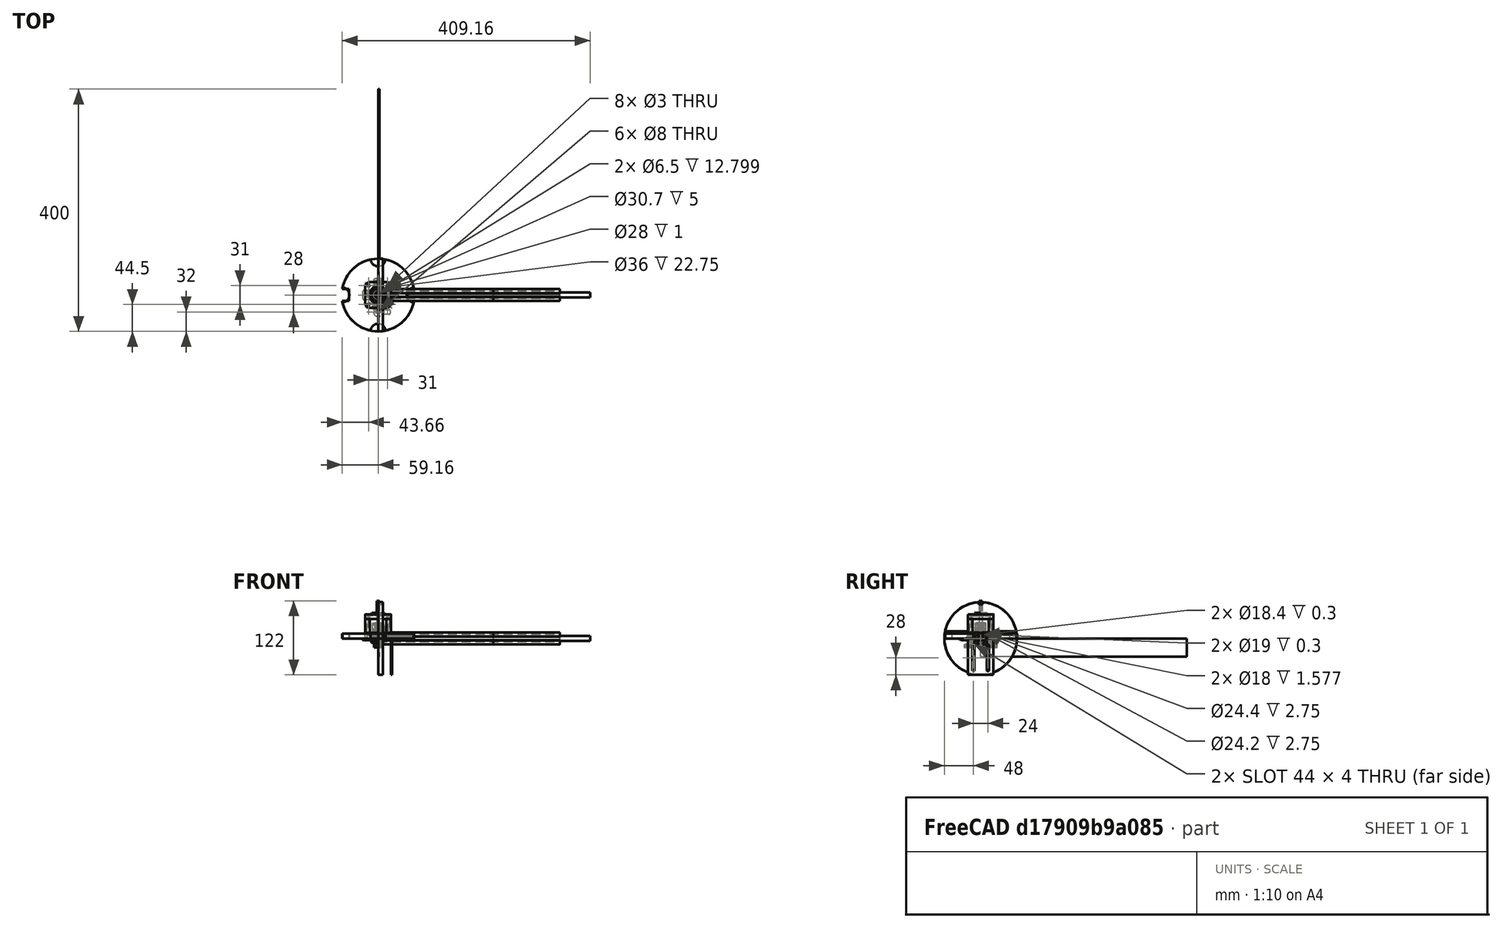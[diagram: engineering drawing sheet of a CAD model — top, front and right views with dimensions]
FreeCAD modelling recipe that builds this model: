
FCSTD DOCUMENT  (FreeCAD 0.19R)
Label: proyectoFinal_ruedasENcero-cero
License: All rights reserved
LicenseURL: http://en.wikipedia.org/wiki/All_rights_reserved
objects: Sketcher::SketchObject×360, PartDesign::Body×269, PartDesign::Pad×217, PartDesign::Fillet×183, App::Part×128, PartDesign::Pocket×123, PartDesign::FeatureBase×92, PartDesign::Revolution×52, App::DocumentObjectGroup×42, App::LinkGroup×30, PartDesign::PolarPattern×29, PartDesign::Chamfer×21, PartDesign::Groove×8, Part::FeaturePython×8, PartDesign::Mirrored×6, PartDesign::ShapeBinder×5, PartDesign::Hole×2, PartDesign::Draft×2, PartDesign::LinearPattern×2, PartDesign::Plane×2, +5 more types
note: 2002 computed .brp shape members not serialized (recipe doc carries the construction recipe); baked Part::Feature solids carry a one-line shape summary decoded from their .brp

FEATURE [Sketcher::SketchObject] Sketch001
  FullyConstrained = false
  MapMode = 5
  Support = -> [XY_Plane003]
  sketch-geometry (46):
    g0: LineSegment StartX=3.4 StartY=2.65 StartZ=0 EndX=3.4 EndY=-2.6657 EndZ=0
    g1: LineSegment StartX=2.63162 StartY=-3.4 StartZ=0 EndX=-2.65 EndY=-3.4 EndZ=0
    g2: LineSegment StartX=-3.4 StartY=-2.63136 StartZ=0 EndX=-3.4 EndY=2.61487 EndZ=0
    g3: LineSegment StartX=-10 StartY=10 StartZ=0 EndX=-3.125 EndY=10 EndZ=0
    g4: LineSegment StartX=10 StartY=10 StartZ=0 EndX=10 EndY=3.125 EndZ=0
    g5: LineSegment StartX=10 StartY=-10 StartZ=0 EndX=3.125 EndY=-10 EndZ=0
    g6: LineSegment StartX=-10 StartY=-10 StartZ=0 EndX=-10 EndY=-3.125 EndZ=0
    g7: GeomPoint X=3e-16 Y=0 Z=0
    g8: Circle CenterX=3e-16 CenterY=0 CenterZ=0 NormalX=0 NormalY=0 NormalZ=1 AngleXU=0 Radius=2.1
    g9: LineSegment StartX=-4.76483 StartY=8.08721 StartZ=0 EndX=-3.55 EndY=8.08721 EndZ=0
    g10: LineSegment StartX=8.24722 StartY=4.75 StartZ=0 EndX=8.24722 EndY=3.55 EndZ=0
    g11: LineSegment StartX=-8.2 StartY=-4.73729 StartZ=0 EndX=-8.2 EndY=-3.55 EndZ=0
    g12: LineSegment StartX=5.5 StartY=4.75 StartZ=0 EndX=8.24722 EndY=4.75 EndZ=0
    g13: LineSegment StartX=4.75 StartY=5.50457 StartZ=0 EndX=2.65 EndY=3.4 EndZ=0
    g14: LineSegment StartX=4.75 StartY=5.50457 StartZ=0 EndX=4.75 EndY=8.08721 EndZ=0
    g15: LineSegment StartX=3.4 StartY=2.65 StartZ=0 EndX=5.5 EndY=4.75 EndZ=0
    g16: LineSegment StartX=-4.76483 StartY=5.50457 StartZ=0 EndX=-2.66166 EndY=3.4 EndZ=0
    g17: LineSegment StartX=-5.5 StartY=4.70904 StartZ=0 EndX=-3.4 EndY=2.61487 EndZ=0
    g18: LineSegment StartX=-4.76483 StartY=5.50457 StartZ=0 EndX=-4.76483 EndY=8.08721 EndZ=0
    g19: LineSegment StartX=-5.5 StartY=4.70904 StartZ=0 EndX=-8.2 EndY=4.70904 EndZ=0
    g20: LineSegment StartX=-10 StartY=3.125 StartZ=0 EndX=-10 EndY=10 EndZ=0
    g21: LineSegment StartX=-8.2 StartY=3.55 StartZ=0 EndX=-8.2 EndY=4.70904 EndZ=0
    g22: LineSegment StartX=3.55 StartY=8.08721 StartZ=0 EndX=4.75 EndY=8.08721 EndZ=0
    g23: LineSegment StartX=3.125 StartY=10 StartZ=0 EndX=10 EndY=10 EndZ=0
    g24: LineSegment StartX=-5.5 StartY=-4.73729 StartZ=0 EndX=-8.2 EndY=-4.73729 EndZ=0
    g25: LineSegment StartX=-4.75 StartY=-5.5 StartZ=0 EndX=-2.65 EndY=-3.4 EndZ=0
    g26: LineSegment StartX=-4.75 StartY=-5.5 StartZ=0 EndX=-4.75 EndY=-8.2 EndZ=0
    g27: LineSegment StartX=4.73747 StartY=-5.5 StartZ=0 EndX=4.73747 EndY=-8.2 EndZ=0
    g28: LineSegment StartX=5.5 StartY=-4.7671 StartZ=0 EndX=8.24722 EndY=-4.7671 EndZ=0
    g29: LineSegment StartX=-3.125 StartY=-10 StartZ=0 EndX=-10 EndY=-10 EndZ=0
    g30: LineSegment StartX=-3.55 StartY=-8.2 StartZ=0 EndX=-4.75 EndY=-8.2 EndZ=0
    g31: LineSegment StartX=4.73747 StartY=-8.2 StartZ=0 EndX=3.55 EndY=-8.2 EndZ=0
    g32: LineSegment StartX=10 StartY=-3.125 StartZ=0 EndX=10 EndY=-10 EndZ=0
    g33: LineSegment StartX=8.24722 StartY=-3.55 StartZ=0 EndX=8.24722 EndY=-4.7671 EndZ=0
    g34: LineSegment StartX=-2.66166 StartY=3.4 StartZ=0 EndX=2.65 EndY=3.4 EndZ=0
    g35: LineSegment StartX=-3.4 StartY=-2.63136 StartZ=0 EndX=-5.5 EndY=-4.73729 EndZ=0
    g36: LineSegment StartX=3.4 StartY=-2.6657 StartZ=0 EndX=5.5 EndY=-4.7671 EndZ=0
    g37: LineSegment StartX=2.63162 StartY=-3.4 StartZ=0 EndX=4.73747 EndY=-5.5 EndZ=0
    g38: LineSegment StartX=-3.55 StartY=-8.2 StartZ=0 EndX=-3.125 EndY=-10 EndZ=0
    g39: LineSegment StartX=3.55 StartY=-8.2 StartZ=0 EndX=3.125 EndY=-10 EndZ=0
    g40: LineSegment StartX=-3.125 StartY=10 StartZ=0 EndX=-3.55 EndY=8.08721 EndZ=0
    g41: LineSegment StartX=3.125 StartY=10 StartZ=0 EndX=3.55 EndY=8.08721 EndZ=0
    g42: LineSegment StartX=8.24722 StartY=3.55 StartZ=0 EndX=10 EndY=3.125 EndZ=0
    g43: LineSegment StartX=10 StartY=-3.125 StartZ=0 EndX=8.24722 EndY=-3.55 EndZ=0
    g44: LineSegment StartX=-10 StartY=-3.125 StartZ=0 EndX=-8.2 EndY=-3.55 EndZ=0
    g45: LineSegment StartX=-10 StartY=3.125 StartZ=0 EndX=-8.2 EndY=3.55 EndZ=0
  constraints (61):
    c: Horizontal(g1)
    c: Vertical(g0)
    c: Vertical(g2)
    c: Coincident(g23,g4)
    c: Coincident(g32,g5)
    c: Coincident(g29,g6)
    c: Coincident(g20,g3)
    c: Horizontal(g3)
    c: Horizontal(g5)
    c: Vertical(g4)
    c: Vertical(g6)
    c: PointOnObject(g7,g-1)
    c: DistanceX(g3,g7) = 10
    c: DistanceX(g-1,g23) = 10
    c: DistanceY(g7,g3) = 10
    c: DistanceX(g3,g-1) = 10
    c: DistanceY(g32,g7) = 10
    c: Coincident(g8,g7)
    c: Radius(g8) = 2.1
    c: Horizontal(g9)
    c: Vertical(g10)
    c: Vertical(g11)
    c: Coincident(g12,g15)
    c: Horizontal(g12)
    c: Coincident(g14,g13)
    c: Vertical(g14)
    c: Coincident(g15,g0)
    c: Coincident(g13,g34)
    c: Coincident(g14,g22)
    c: Coincident(g18,g16)
    c: Vertical(g18)
    c: Coincident(g19,g17)
    c: Horizontal(g19)
    c: Coincident(g9,g18)
    c: Coincident(g21,g19)
    c: Coincident(g24,g35)
    c: Horizontal(g24)
    c: Coincident(g26,g25)
    c: Vertical(g26)
    c: Coincident(g27,g37)
    c: Vertical(g27)
    c: Coincident(g28,g36)
    c: Horizontal(g28)
    c: Coincident(g11,g24)
    c: Coincident(g26,g30)
    c: Coincident(g31,g27)
    c: Coincident(g12,g10)
    c: Coincident(g28,g33)
    c: Coincident(g25,g1)
    c: Coincident(g35,g2)
    c: Coincident(g17,g2)
    c: Coincident(g16,g34)
    c: Coincident(g1,g37)
    c: Coincident(g0,g36)
    c: Coincident(g39,g5)
    c: Coincident(g40,g3)
    c: Coincident(g42,g4)
    c: Coincident(g44,g6)
    c: Coincident(g21,g45)
    c: Coincident(g33,g43)
    c: Coincident(g10,g42)
FEATURE [PartDesign::Pad] Pad001
  Direction = (0,0,1)
  Length = 300
  Length2 = 10
  Profile = -> Sketch001
  Type = 0
FEATURE [PartDesign::Fillet] Fillet011
  Base = -> Pad001 [Edge53]
  BaseFeature = -> Pad001
  Radius = 1
  SupportTransform = false
FEATURE [PartDesign::Fillet] Fillet012
  Base = -> Fillet011 [Edge114]
  BaseFeature = -> Fillet011
  Radius = 1
  SupportTransform = false
FEATURE [PartDesign::Fillet] Fillet013
  Base = -> Fillet012 [Edge137,Edge95]
  BaseFeature = -> Fillet012
  Radius = 0.5
  SupportTransform = false
FEATURE [PartDesign::Fillet] Fillet014
  Base = -> Fillet013 [Edge103]
  BaseFeature = -> Fillet013
  Radius = 0.5
  SupportTransform = false
FEATURE [PartDesign::Fillet] Fillet015
  Base = -> Fillet014 [Edge96]
  BaseFeature = -> Fillet014
  Radius = 0.5
  SupportTransform = false
FEATURE [PartDesign::Fillet] Fillet016
  Base = -> Fillet015 [Edge77]
  BaseFeature = -> Fillet015
  Radius = 0.5
  SupportTransform = false
FEATURE [PartDesign::Fillet] Fillet017
  Base = -> Fillet016 [Edge102]
  BaseFeature = -> Fillet016
  Radius = 0.5
  SupportTransform = false
FEATURE [PartDesign::Fillet] Fillet018
  Base = -> Fillet017 [Edge85]
  BaseFeature = -> Fillet017
  Radius = 0.5
  SupportTransform = false
FEATURE [PartDesign::Fillet] Fillet019
  Base = -> Fillet018 [Edge78]
  BaseFeature = -> Fillet018
  Radius = 0.5
  SupportTransform = false
FEATURE [PartDesign::Fillet] Fillet020
  Base = -> Fillet019 [Edge107]
  BaseFeature = -> Fillet019
  Radius = 0.5
  SupportTransform = false
FEATURE [PartDesign::Fillet] Fillet021
  Base = -> Fillet020 [Edge74]
  BaseFeature = -> Fillet020
  Radius = 0.5
  SupportTransform = false
FEATURE [PartDesign::Body] Body001
  Group = -> [Sketch001,Pad001,Fillet011,Fillet012,Fillet013,Fillet014,Fillet015,Fillet016,Fillet017,Fillet018,Fillet019,Fillet020,Fillet021]
  Origin = -> Origin003
  Placement = pos=(0,0,0) rot=(0,1,0;1.5708rad)
  Tip = -> Fillet021
FEATURE [App::Part] Part001  label="2020-300-002"
  Group = -> [Body001]
  Origin = -> Origin002
  Placement = pos=(20,330,10) rot=(0,0,1;0rad)
FEATURE [Sketcher::SketchObject] Sketch002
  FullyConstrained = false
  MapMode = 5
  Support = -> [XY_Plane005]
  sketch-geometry (46):
    g0: LineSegment StartX=3.4 StartY=2.65 StartZ=0 EndX=3.4 EndY=-2.6657 EndZ=0
    g1: LineSegment StartX=2.63162 StartY=-3.4 StartZ=0 EndX=-2.65 EndY=-3.4 EndZ=0
    g2: LineSegment StartX=-3.4 StartY=-2.63136 StartZ=0 EndX=-3.4 EndY=2.61487 EndZ=0
    g3: LineSegment StartX=-10 StartY=10 StartZ=0 EndX=-3.125 EndY=10 EndZ=0
    g4: LineSegment StartX=10 StartY=10 StartZ=0 EndX=10 EndY=3.125 EndZ=0
    g5: LineSegment StartX=10 StartY=-10 StartZ=0 EndX=3.125 EndY=-10 EndZ=0
    g6: LineSegment StartX=-10 StartY=-10 StartZ=0 EndX=-10 EndY=-3.125 EndZ=0
    g7: GeomPoint X=3e-16 Y=0 Z=0
    g8: Circle CenterX=3e-16 CenterY=0 CenterZ=0 NormalX=0 NormalY=0 NormalZ=1 AngleXU=0 Radius=2.1
    g9: LineSegment StartX=-4.76483 StartY=8.08721 StartZ=0 EndX=-3.55 EndY=8.08721 EndZ=0
    g10: LineSegment StartX=8.24722 StartY=4.75 StartZ=0 EndX=8.24722 EndY=3.55 EndZ=0
    g11: LineSegment StartX=-8.2 StartY=-4.73729 StartZ=0 EndX=-8.2 EndY=-3.55 EndZ=0
    g12: LineSegment StartX=5.5 StartY=4.75 StartZ=0 EndX=8.24722 EndY=4.75 EndZ=0
    g13: LineSegment StartX=4.75 StartY=5.50457 StartZ=0 EndX=2.65 EndY=3.4 EndZ=0
    g14: LineSegment StartX=4.75 StartY=5.50457 StartZ=0 EndX=4.75 EndY=8.08721 EndZ=0
    g15: LineSegment StartX=3.4 StartY=2.65 StartZ=0 EndX=5.5 EndY=4.75 EndZ=0
    g16: LineSegment StartX=-4.76483 StartY=5.50457 StartZ=0 EndX=-2.66166 EndY=3.4 EndZ=0
    g17: LineSegment StartX=-5.5 StartY=4.70904 StartZ=0 EndX=-3.4 EndY=2.61487 EndZ=0
    g18: LineSegment StartX=-4.76483 StartY=5.50457 StartZ=0 EndX=-4.76483 EndY=8.08721 EndZ=0
    g19: LineSegment StartX=-5.5 StartY=4.70904 StartZ=0 EndX=-8.2 EndY=4.70904 EndZ=0
    g20: LineSegment StartX=-10 StartY=3.125 StartZ=0 EndX=-10 EndY=10 EndZ=0
    g21: LineSegment StartX=-8.2 StartY=3.55 StartZ=0 EndX=-8.2 EndY=4.70904 EndZ=0
    g22: LineSegment StartX=3.55 StartY=8.08721 StartZ=0 EndX=4.75 EndY=8.08721 EndZ=0
    g23: LineSegment StartX=3.125 StartY=10 StartZ=0 EndX=10 EndY=10 EndZ=0
    g24: LineSegment StartX=-5.5 StartY=-4.73729 StartZ=0 EndX=-8.2 EndY=-4.73729 EndZ=0
    g25: LineSegment StartX=-4.75 StartY=-5.5 StartZ=0 EndX=-2.65 EndY=-3.4 EndZ=0
    g26: LineSegment StartX=-4.75 StartY=-5.5 StartZ=0 EndX=-4.75 EndY=-8.2 EndZ=0
    g27: LineSegment StartX=4.73747 StartY=-5.5 StartZ=0 EndX=4.73747 EndY=-8.2 EndZ=0
    g28: LineSegment StartX=5.5 StartY=-4.7671 StartZ=0 EndX=8.24722 EndY=-4.7671 EndZ=0
    g29: LineSegment StartX=-3.125 StartY=-10 StartZ=0 EndX=-10 EndY=-10 EndZ=0
    g30: LineSegment StartX=-3.55 StartY=-8.2 StartZ=0 EndX=-4.75 EndY=-8.2 EndZ=0
    g31: LineSegment StartX=4.73747 StartY=-8.2 StartZ=0 EndX=3.55 EndY=-8.2 EndZ=0
    g32: LineSegment StartX=10 StartY=-3.125 StartZ=0 EndX=10 EndY=-10 EndZ=0
    g33: LineSegment StartX=8.24722 StartY=-3.55 StartZ=0 EndX=8.24722 EndY=-4.7671 EndZ=0
    g34: LineSegment StartX=-2.66166 StartY=3.4 StartZ=0 EndX=2.65 EndY=3.4 EndZ=0
    g35: LineSegment StartX=-3.4 StartY=-2.63136 StartZ=0 EndX=-5.5 EndY=-4.73729 EndZ=0
    g36: LineSegment StartX=3.4 StartY=-2.6657 StartZ=0 EndX=5.5 EndY=-4.7671 EndZ=0
    g37: LineSegment StartX=2.63162 StartY=-3.4 StartZ=0 EndX=4.73747 EndY=-5.5 EndZ=0
    g38: LineSegment StartX=-3.55 StartY=-8.2 StartZ=0 EndX=-3.125 EndY=-10 EndZ=0
    g39: LineSegment StartX=3.55 StartY=-8.2 StartZ=0 EndX=3.125 EndY=-10 EndZ=0
    g40: LineSegment StartX=-3.125 StartY=10 StartZ=0 EndX=-3.55 EndY=8.08721 EndZ=0
    g41: LineSegment StartX=3.125 StartY=10 StartZ=0 EndX=3.55 EndY=8.08721 EndZ=0
    g42: LineSegment StartX=8.24722 StartY=3.55 StartZ=0 EndX=10 EndY=3.125 EndZ=0
    g43: LineSegment StartX=10 StartY=-3.125 StartZ=0 EndX=8.24722 EndY=-3.55 EndZ=0
    g44: LineSegment StartX=-10 StartY=-3.125 StartZ=0 EndX=-8.2 EndY=-3.55 EndZ=0
    g45: LineSegment StartX=-10 StartY=3.125 StartZ=0 EndX=-8.2 EndY=3.55 EndZ=0
  constraints (61):
    c: Horizontal(g1)
    c: Vertical(g0)
    c: Vertical(g2)
    c: Coincident(g23,g4)
    c: Coincident(g32,g5)
    c: Coincident(g29,g6)
    c: Coincident(g20,g3)
    c: Horizontal(g3)
    c: Horizontal(g5)
    c: Vertical(g4)
    c: Vertical(g6)
    c: PointOnObject(g7,g-1)
    c: DistanceX(g3,g7) = 10
    c: DistanceX(g-1,g23) = 10
    c: DistanceY(g7,g3) = 10
    c: DistanceX(g3,g-1) = 10
    c: DistanceY(g32,g7) = 10
    c: Coincident(g8,g7)
    c: Radius(g8) = 2.1
    c: Horizontal(g9)
    c: Vertical(g10)
    c: Vertical(g11)
    c: Coincident(g12,g15)
    c: Horizontal(g12)
    c: Coincident(g14,g13)
    c: Vertical(g14)
    c: Coincident(g15,g0)
    c: Coincident(g13,g34)
    c: Coincident(g14,g22)
    c: Coincident(g18,g16)
    c: Vertical(g18)
    c: Coincident(g19,g17)
    c: Horizontal(g19)
    c: Coincident(g9,g18)
    c: Coincident(g21,g19)
    c: Coincident(g24,g35)
    c: Horizontal(g24)
    c: Coincident(g26,g25)
    c: Vertical(g26)
    c: Coincident(g27,g37)
    c: Vertical(g27)
    c: Coincident(g28,g36)
    c: Horizontal(g28)
    c: Coincident(g11,g24)
    c: Coincident(g26,g30)
    c: Coincident(g31,g27)
    c: Coincident(g12,g10)
    c: Coincident(g28,g33)
    c: Coincident(g25,g1)
    c: Coincident(g35,g2)
    c: Coincident(g17,g2)
    c: Coincident(g16,g34)
    c: Coincident(g1,g37)
    c: Coincident(g0,g36)
    c: Coincident(g39,g5)
    c: Coincident(g40,g3)
    c: Coincident(g42,g4)
    c: Coincident(g44,g6)
    c: Coincident(g21,g45)
    c: Coincident(g33,g43)
    c: Coincident(g10,g42)
FEATURE [PartDesign::Pad] Pad002
  Direction = (0,0,1)
  Length = 300
  Length2 = 10
  Profile = -> Sketch002
  Type = 0
FEATURE [PartDesign::Fillet] Fillet022
  Base = -> Pad002 [Edge53]
  BaseFeature = -> Pad002
  Radius = 1
  SupportTransform = false
FEATURE [PartDesign::Fillet] Fillet023
  Base = -> Fillet022 [Edge114]
  BaseFeature = -> Fillet022
  Radius = 1
  SupportTransform = false
FEATURE [PartDesign::Fillet] Fillet024
  Base = -> Fillet023 [Edge137,Edge95]
  BaseFeature = -> Fillet023
  Radius = 0.5
  SupportTransform = false
FEATURE [PartDesign::Fillet] Fillet025
  Base = -> Fillet024 [Edge103]
  BaseFeature = -> Fillet024
  Radius = 0.5
  SupportTransform = false
FEATURE [PartDesign::Fillet] Fillet026
  Base = -> Fillet025 [Edge96]
  BaseFeature = -> Fillet025
  Radius = 0.5
  SupportTransform = false
FEATURE [PartDesign::Fillet] Fillet027
  Base = -> Fillet026 [Edge77]
  BaseFeature = -> Fillet026
  Radius = 0.5
  SupportTransform = false
FEATURE [PartDesign::Fillet] Fillet028
  Base = -> Fillet027 [Edge102]
  BaseFeature = -> Fillet027
  Radius = 0.5
  SupportTransform = false
FEATURE [PartDesign::Fillet] Fillet029
  Base = -> Fillet028 [Edge85]
  BaseFeature = -> Fillet028
  Radius = 0.5
  SupportTransform = false
FEATURE [PartDesign::Fillet] Fillet030
  Base = -> Fillet029 [Edge78]
  BaseFeature = -> Fillet029
  Radius = 0.5
  SupportTransform = false
FEATURE [PartDesign::Fillet] Fillet031
  Base = -> Fillet030 [Edge107]
  BaseFeature = -> Fillet030
  Radius = 0.5
  SupportTransform = false
FEATURE [PartDesign::Fillet] Fillet032
  Base = -> Fillet031 [Edge74]
  BaseFeature = -> Fillet031
  Radius = 0.5
  SupportTransform = false
FEATURE [PartDesign::Body] Body002
  Group = -> [Sketch002,Pad002,Fillet022,Fillet023,Fillet024,Fillet025,Fillet026,Fillet027,Fillet028,Fillet029,Fillet030,Fillet031,Fillet032]
  Origin = -> Origin005
  Placement = pos=(0,0,0) rot=(0,1,0;1.5708rad)
  Tip = -> Fillet032
FEATURE [App::Part] Part002  label="2020-300-003"
  Group = -> [Body002]
  Origin = -> Origin004
  Placement = pos=(10,20,10) rot=(0,0,1;1.5708rad)
FEATURE [Sketcher::SketchObject] Sketch003
  FullyConstrained = false
  MapMode = 5
  Support = -> [XY_Plane007]
  sketch-geometry (46):
    g0: LineSegment StartX=3.4 StartY=2.65 StartZ=0 EndX=3.4 EndY=-2.6657 EndZ=0
    g1: LineSegment StartX=2.63162 StartY=-3.4 StartZ=0 EndX=-2.65 EndY=-3.4 EndZ=0
    g2: LineSegment StartX=-3.4 StartY=-2.63136 StartZ=0 EndX=-3.4 EndY=2.61487 EndZ=0
    g3: LineSegment StartX=-10 StartY=10 StartZ=0 EndX=-3.125 EndY=10 EndZ=0
    g4: LineSegment StartX=10 StartY=10 StartZ=0 EndX=10 EndY=3.125 EndZ=0
    g5: LineSegment StartX=10 StartY=-10 StartZ=0 EndX=3.125 EndY=-10 EndZ=0
    g6: LineSegment StartX=-10 StartY=-10 StartZ=0 EndX=-10 EndY=-3.125 EndZ=0
    g7: GeomPoint X=3e-16 Y=0 Z=0
    g8: Circle CenterX=3e-16 CenterY=0 CenterZ=0 NormalX=0 NormalY=0 NormalZ=1 AngleXU=0 Radius=2.1
    g9: LineSegment StartX=-4.76483 StartY=8.08721 StartZ=0 EndX=-3.55 EndY=8.08721 EndZ=0
    g10: LineSegment StartX=8.24722 StartY=4.75 StartZ=0 EndX=8.24722 EndY=3.55 EndZ=0
    g11: LineSegment StartX=-8.2 StartY=-4.73729 StartZ=0 EndX=-8.2 EndY=-3.55 EndZ=0
    g12: LineSegment StartX=5.5 StartY=4.75 StartZ=0 EndX=8.24722 EndY=4.75 EndZ=0
    g13: LineSegment StartX=4.75 StartY=5.50457 StartZ=0 EndX=2.65 EndY=3.4 EndZ=0
    g14: LineSegment StartX=4.75 StartY=5.50457 StartZ=0 EndX=4.75 EndY=8.08721 EndZ=0
    g15: LineSegment StartX=3.4 StartY=2.65 StartZ=0 EndX=5.5 EndY=4.75 EndZ=0
    g16: LineSegment StartX=-4.76483 StartY=5.50457 StartZ=0 EndX=-2.66166 EndY=3.4 EndZ=0
    g17: LineSegment StartX=-5.5 StartY=4.70904 StartZ=0 EndX=-3.4 EndY=2.61487 EndZ=0
    g18: LineSegment StartX=-4.76483 StartY=5.50457 StartZ=0 EndX=-4.76483 EndY=8.08721 EndZ=0
    g19: LineSegment StartX=-5.5 StartY=4.70904 StartZ=0 EndX=-8.2 EndY=4.70904 EndZ=0
    g20: LineSegment StartX=-10 StartY=3.125 StartZ=0 EndX=-10 EndY=10 EndZ=0
    g21: LineSegment StartX=-8.2 StartY=3.55 StartZ=0 EndX=-8.2 EndY=4.70904 EndZ=0
    g22: LineSegment StartX=3.55 StartY=8.08721 StartZ=0 EndX=4.75 EndY=8.08721 EndZ=0
    g23: LineSegment StartX=3.125 StartY=10 StartZ=0 EndX=10 EndY=10 EndZ=0
    g24: LineSegment StartX=-5.5 StartY=-4.73729 StartZ=0 EndX=-8.2 EndY=-4.73729 EndZ=0
    g25: LineSegment StartX=-4.75 StartY=-5.5 StartZ=0 EndX=-2.65 EndY=-3.4 EndZ=0
    g26: LineSegment StartX=-4.75 StartY=-5.5 StartZ=0 EndX=-4.75 EndY=-8.2 EndZ=0
    g27: LineSegment StartX=4.73747 StartY=-5.5 StartZ=0 EndX=4.73747 EndY=-8.2 EndZ=0
    g28: LineSegment StartX=5.5 StartY=-4.7671 StartZ=0 EndX=8.24722 EndY=-4.7671 EndZ=0
    g29: LineSegment StartX=-3.125 StartY=-10 StartZ=0 EndX=-10 EndY=-10 EndZ=0
    g30: LineSegment StartX=-3.55 StartY=-8.2 StartZ=0 EndX=-4.75 EndY=-8.2 EndZ=0
    g31: LineSegment StartX=4.73747 StartY=-8.2 StartZ=0 EndX=3.55 EndY=-8.2 EndZ=0
    g32: LineSegment StartX=10 StartY=-3.125 StartZ=0 EndX=10 EndY=-10 EndZ=0
    g33: LineSegment StartX=8.24722 StartY=-3.55 StartZ=0 EndX=8.24722 EndY=-4.7671 EndZ=0
    g34: LineSegment StartX=-2.66166 StartY=3.4 StartZ=0 EndX=2.65 EndY=3.4 EndZ=0
    g35: LineSegment StartX=-3.4 StartY=-2.63136 StartZ=0 EndX=-5.5 EndY=-4.73729 EndZ=0
    g36: LineSegment StartX=3.4 StartY=-2.6657 StartZ=0 EndX=5.5 EndY=-4.7671 EndZ=0
    g37: LineSegment StartX=2.63162 StartY=-3.4 StartZ=0 EndX=4.73747 EndY=-5.5 EndZ=0
    g38: LineSegment StartX=-3.55 StartY=-8.2 StartZ=0 EndX=-3.125 EndY=-10 EndZ=0
    g39: LineSegment StartX=3.55 StartY=-8.2 StartZ=0 EndX=3.125 EndY=-10 EndZ=0
    g40: LineSegment StartX=-3.125 StartY=10 StartZ=0 EndX=-3.55 EndY=8.08721 EndZ=0
    g41: LineSegment StartX=3.125 StartY=10 StartZ=0 EndX=3.55 EndY=8.08721 EndZ=0
    g42: LineSegment StartX=8.24722 StartY=3.55 StartZ=0 EndX=10 EndY=3.125 EndZ=0
    g43: LineSegment StartX=10 StartY=-3.125 StartZ=0 EndX=8.24722 EndY=-3.55 EndZ=0
    g44: LineSegment StartX=-10 StartY=-3.125 StartZ=0 EndX=-8.2 EndY=-3.55 EndZ=0
    g45: LineSegment StartX=-10 StartY=3.125 StartZ=0 EndX=-8.2 EndY=3.55 EndZ=0
  constraints (61):
    c: Horizontal(g1)
    c: Vertical(g0)
    c: Vertical(g2)
    c: Coincident(g23,g4)
    c: Coincident(g32,g5)
    c: Coincident(g29,g6)
    c: Coincident(g20,g3)
    c: Horizontal(g3)
    c: Horizontal(g5)
    c: Vertical(g4)
    c: Vertical(g6)
    c: PointOnObject(g7,g-1)
    c: DistanceX(g3,g7) = 10
    c: DistanceX(g-1,g23) = 10
    c: DistanceY(g7,g3) = 10
    c: DistanceX(g3,g-1) = 10
    c: DistanceY(g32,g7) = 10
    c: Coincident(g8,g7)
    c: Radius(g8) = 2.1
    c: Horizontal(g9)
    c: Vertical(g10)
    c: Vertical(g11)
    c: Coincident(g12,g15)
    c: Horizontal(g12)
    c: Coincident(g14,g13)
    c: Vertical(g14)
    c: Coincident(g15,g0)
    c: Coincident(g13,g34)
    c: Coincident(g14,g22)
    c: Coincident(g18,g16)
    c: Vertical(g18)
    c: Coincident(g19,g17)
    c: Horizontal(g19)
    c: Coincident(g9,g18)
    c: Coincident(g21,g19)
    c: Coincident(g24,g35)
    c: Horizontal(g24)
    c: Coincident(g26,g25)
    c: Vertical(g26)
    c: Coincident(g27,g37)
    c: Vertical(g27)
    c: Coincident(g28,g36)
    c: Horizontal(g28)
    c: Coincident(g11,g24)
    c: Coincident(g26,g30)
    c: Coincident(g31,g27)
    c: Coincident(g12,g10)
    c: Coincident(g28,g33)
    c: Coincident(g25,g1)
    c: Coincident(g35,g2)
    c: Coincident(g17,g2)
    c: Coincident(g16,g34)
    c: Coincident(g1,g37)
    c: Coincident(g0,g36)
    c: Coincident(g39,g5)
    c: Coincident(g40,g3)
    c: Coincident(g42,g4)
    c: Coincident(g44,g6)
    c: Coincident(g21,g45)
    c: Coincident(g33,g43)
    c: Coincident(g10,g42)
FEATURE [PartDesign::Pad] Pad003
  Direction = (0,0,1)
  Length = 300
  Length2 = 10
  Profile = -> Sketch003
  Type = 0
FEATURE [PartDesign::Fillet] Fillet033
  Base = -> Pad003 [Edge53]
  BaseFeature = -> Pad003
  Radius = 1
  SupportTransform = false
FEATURE [PartDesign::Fillet] Fillet034
  Base = -> Fillet033 [Edge114]
  BaseFeature = -> Fillet033
  Radius = 1
  SupportTransform = false
FEATURE [PartDesign::Fillet] Fillet035
  Base = -> Fillet034 [Edge137,Edge95]
  BaseFeature = -> Fillet034
  Radius = 0.5
  SupportTransform = false
FEATURE [PartDesign::Fillet] Fillet036
  Base = -> Fillet035 [Edge103]
  BaseFeature = -> Fillet035
  Radius = 0.5
  SupportTransform = false
FEATURE [PartDesign::Fillet] Fillet037
  Base = -> Fillet036 [Edge96]
  BaseFeature = -> Fillet036
  Radius = 0.5
  SupportTransform = false
FEATURE [PartDesign::Fillet] Fillet038
  Base = -> Fillet037 [Edge77]
  BaseFeature = -> Fillet037
  Radius = 0.5
  SupportTransform = false
FEATURE [PartDesign::Fillet] Fillet039
  Base = -> Fillet038 [Edge102]
  BaseFeature = -> Fillet038
  Radius = 0.5
  SupportTransform = false
FEATURE [PartDesign::Fillet] Fillet040
  Base = -> Fillet039 [Edge85]
  BaseFeature = -> Fillet039
  Radius = 0.5
  SupportTransform = false
FEATURE [PartDesign::Fillet] Fillet041
  Base = -> Fillet040 [Edge78]
  BaseFeature = -> Fillet040
  Radius = 0.5
  SupportTransform = false
FEATURE [PartDesign::Fillet] Fillet042
  Base = -> Fillet041 [Edge107]
  BaseFeature = -> Fillet041
  Radius = 0.5
  SupportTransform = false
FEATURE [PartDesign::Fillet] Fillet043
  Base = -> Fillet042 [Edge74]
  BaseFeature = -> Fillet042
  Radius = 0.5
  SupportTransform = false
FEATURE [PartDesign::Body] Body003
  Group = -> [Sketch003,Pad003,Fillet033,Fillet034,Fillet035,Fillet036,Fillet037,Fillet038,Fillet039,Fillet040,Fillet041,Fillet042,Fillet043]
  Origin = -> Origin007
  Placement = pos=(0,0,0) rot=(0,1,0;1.5708rad)
  Tip = -> Fillet043
FEATURE [App::Part] Part003  label="2020-300-004"
  Group = -> [Body003]
  Origin = -> Origin006
  Placement = pos=(330,20,10) rot=(0,0,1;1.5708rad)
FEATURE [Sketcher::SketchObject] Sketch004
  FullyConstrained = false
  MapMode = 5
  Support = -> [XY_Plane009]
  sketch-geometry (46):
    g0: LineSegment StartX=3.4 StartY=2.65 StartZ=0 EndX=3.4 EndY=-2.6657 EndZ=0
    g1: LineSegment StartX=2.63162 StartY=-3.4 StartZ=0 EndX=-2.65 EndY=-3.4 EndZ=0
    g2: LineSegment StartX=-3.4 StartY=-2.63136 StartZ=0 EndX=-3.4 EndY=2.61487 EndZ=0
    g3: LineSegment StartX=-10 StartY=10 StartZ=0 EndX=-3.125 EndY=10 EndZ=0
    g4: LineSegment StartX=10 StartY=10 StartZ=0 EndX=10 EndY=3.125 EndZ=0
    g5: LineSegment StartX=10 StartY=-10 StartZ=0 EndX=3.125 EndY=-10 EndZ=0
    g6: LineSegment StartX=-10 StartY=-10 StartZ=0 EndX=-10 EndY=-3.125 EndZ=0
    g7: GeomPoint X=3e-16 Y=0 Z=0
    g8: Circle CenterX=3e-16 CenterY=0 CenterZ=0 NormalX=0 NormalY=0 NormalZ=1 AngleXU=0 Radius=2.1
    g9: LineSegment StartX=-4.76483 StartY=8.08721 StartZ=0 EndX=-3.55 EndY=8.08721 EndZ=0
    g10: LineSegment StartX=8.24722 StartY=4.75 StartZ=0 EndX=8.24722 EndY=3.55 EndZ=0
    g11: LineSegment StartX=-8.2 StartY=-4.73729 StartZ=0 EndX=-8.2 EndY=-3.55 EndZ=0
    g12: LineSegment StartX=5.5 StartY=4.75 StartZ=0 EndX=8.24722 EndY=4.75 EndZ=0
    g13: LineSegment StartX=4.75 StartY=5.50457 StartZ=0 EndX=2.65 EndY=3.4 EndZ=0
    g14: LineSegment StartX=4.75 StartY=5.50457 StartZ=0 EndX=4.75 EndY=8.08721 EndZ=0
    g15: LineSegment StartX=3.4 StartY=2.65 StartZ=0 EndX=5.5 EndY=4.75 EndZ=0
    g16: LineSegment StartX=-4.76483 StartY=5.50457 StartZ=0 EndX=-2.66166 EndY=3.4 EndZ=0
    g17: LineSegment StartX=-5.5 StartY=4.70904 StartZ=0 EndX=-3.4 EndY=2.61487 EndZ=0
    g18: LineSegment StartX=-4.76483 StartY=5.50457 StartZ=0 EndX=-4.76483 EndY=8.08721 EndZ=0
    g19: LineSegment StartX=-5.5 StartY=4.70904 StartZ=0 EndX=-8.2 EndY=4.70904 EndZ=0
    g20: LineSegment StartX=-10 StartY=3.125 StartZ=0 EndX=-10 EndY=10 EndZ=0
    g21: LineSegment StartX=-8.2 StartY=3.55 StartZ=0 EndX=-8.2 EndY=4.70904 EndZ=0
    g22: LineSegment StartX=3.55 StartY=8.08721 StartZ=0 EndX=4.75 EndY=8.08721 EndZ=0
    g23: LineSegment StartX=3.125 StartY=10 StartZ=0 EndX=10 EndY=10 EndZ=0
    g24: LineSegment StartX=-5.5 StartY=-4.73729 StartZ=0 EndX=-8.2 EndY=-4.73729 EndZ=0
    g25: LineSegment StartX=-4.75 StartY=-5.5 StartZ=0 EndX=-2.65 EndY=-3.4 EndZ=0
    g26: LineSegment StartX=-4.75 StartY=-5.5 StartZ=0 EndX=-4.75 EndY=-8.2 EndZ=0
    g27: LineSegment StartX=4.73747 StartY=-5.5 StartZ=0 EndX=4.73747 EndY=-8.2 EndZ=0
    g28: LineSegment StartX=5.5 StartY=-4.7671 StartZ=0 EndX=8.24722 EndY=-4.7671 EndZ=0
    g29: LineSegment StartX=-3.125 StartY=-10 StartZ=0 EndX=-10 EndY=-10 EndZ=0
    g30: LineSegment StartX=-3.55 StartY=-8.2 StartZ=0 EndX=-4.75 EndY=-8.2 EndZ=0
    g31: LineSegment StartX=4.73747 StartY=-8.2 StartZ=0 EndX=3.55 EndY=-8.2 EndZ=0
    g32: LineSegment StartX=10 StartY=-3.125 StartZ=0 EndX=10 EndY=-10 EndZ=0
    g33: LineSegment StartX=8.24722 StartY=-3.55 StartZ=0 EndX=8.24722 EndY=-4.7671 EndZ=0
    g34: LineSegment StartX=-2.66166 StartY=3.4 StartZ=0 EndX=2.65 EndY=3.4 EndZ=0
    g35: LineSegment StartX=-3.4 StartY=-2.63136 StartZ=0 EndX=-5.5 EndY=-4.73729 EndZ=0
    g36: LineSegment StartX=3.4 StartY=-2.6657 StartZ=0 EndX=5.5 EndY=-4.7671 EndZ=0
    g37: LineSegment StartX=2.63162 StartY=-3.4 StartZ=0 EndX=4.73747 EndY=-5.5 EndZ=0
    g38: LineSegment StartX=-3.55 StartY=-8.2 StartZ=0 EndX=-3.125 EndY=-10 EndZ=0
    g39: LineSegment StartX=3.55 StartY=-8.2 StartZ=0 EndX=3.125 EndY=-10 EndZ=0
    g40: LineSegment StartX=-3.125 StartY=10 StartZ=0 EndX=-3.55 EndY=8.08721 EndZ=0
    g41: LineSegment StartX=3.125 StartY=10 StartZ=0 EndX=3.55 EndY=8.08721 EndZ=0
    g42: LineSegment StartX=8.24722 StartY=3.55 StartZ=0 EndX=10 EndY=3.125 EndZ=0
    g43: LineSegment StartX=10 StartY=-3.125 StartZ=0 EndX=8.24722 EndY=-3.55 EndZ=0
    g44: LineSegment StartX=-10 StartY=-3.125 StartZ=0 EndX=-8.2 EndY=-3.55 EndZ=0
    g45: LineSegment StartX=-10 StartY=3.125 StartZ=0 EndX=-8.2 EndY=3.55 EndZ=0
  constraints (61):
    c: Horizontal(g1)
    c: Vertical(g0)
    c: Vertical(g2)
    c: Coincident(g23,g4)
    c: Coincident(g32,g5)
    c: Coincident(g29,g6)
    c: Coincident(g20,g3)
    c: Horizontal(g3)
    c: Horizontal(g5)
    c: Vertical(g4)
    c: Vertical(g6)
    c: PointOnObject(g7,g-1)
    c: DistanceX(g3,g7) = 10
    c: DistanceX(g-1,g23) = 10
    c: DistanceY(g7,g3) = 10
    c: DistanceX(g3,g-1) = 10
    c: DistanceY(g32,g7) = 10
    c: Coincident(g8,g7)
    c: Radius(g8) = 2.1
    c: Horizontal(g9)
    c: Vertical(g10)
    c: Vertical(g11)
    c: Coincident(g12,g15)
    c: Horizontal(g12)
    c: Coincident(g14,g13)
    c: Vertical(g14)
    c: Coincident(g15,g0)
    c: Coincident(g13,g34)
    c: Coincident(g14,g22)
    c: Coincident(g18,g16)
    c: Vertical(g18)
    c: Coincident(g19,g17)
    c: Horizontal(g19)
    c: Coincident(g9,g18)
    c: Coincident(g21,g19)
    c: Coincident(g24,g35)
    c: Horizontal(g24)
    c: Coincident(g26,g25)
    c: Vertical(g26)
    c: Coincident(g27,g37)
    c: Vertical(g27)
    c: Coincident(g28,g36)
    c: Horizontal(g28)
    c: Coincident(g11,g24)
    c: Coincident(g26,g30)
    c: Coincident(g31,g27)
    c: Coincident(g12,g10)
    c: Coincident(g28,g33)
    c: Coincident(g25,g1)
    c: Coincident(g35,g2)
    c: Coincident(g17,g2)
    c: Coincident(g16,g34)
    c: Coincident(g1,g37)
    c: Coincident(g0,g36)
    c: Coincident(g39,g5)
    c: Coincident(g40,g3)
    c: Coincident(g42,g4)
    c: Coincident(g44,g6)
    c: Coincident(g21,g45)
    c: Coincident(g33,g43)
    c: Coincident(g10,g42)
FEATURE [PartDesign::Pad] Pad004
  Direction = (0,0,1)
  Length = 190
  Length2 = 10
  Profile = -> Sketch004
  Type = 0
FEATURE [PartDesign::Fillet] Fillet044
  Base = -> Pad004 [Edge53]
  BaseFeature = -> Pad004
  Radius = 1
  SupportTransform = false
FEATURE [PartDesign::Fillet] Fillet045
  Base = -> Fillet044 [Edge114]
  BaseFeature = -> Fillet044
  Radius = 1
  SupportTransform = false
FEATURE [PartDesign::Fillet] Fillet046
  Base = -> Fillet045 [Edge137,Edge95]
  BaseFeature = -> Fillet045
  Radius = 0.5
  SupportTransform = false
FEATURE [PartDesign::Fillet] Fillet047
  Base = -> Fillet046 [Edge103]
  BaseFeature = -> Fillet046
  Radius = 0.5
  SupportTransform = false
FEATURE [PartDesign::Fillet] Fillet048
  Base = -> Fillet047 [Edge96]
  BaseFeature = -> Fillet047
  Radius = 0.5
  SupportTransform = false
FEATURE [PartDesign::Fillet] Fillet049
  Base = -> Fillet048 [Edge77]
  BaseFeature = -> Fillet048
  Radius = 0.5
  SupportTransform = false
FEATURE [PartDesign::Fillet] Fillet050
  Base = -> Fillet049 [Edge102]
  BaseFeature = -> Fillet049
  Radius = 0.5
  SupportTransform = false
FEATURE [PartDesign::Fillet] Fillet051
  Base = -> Fillet050 [Edge85]
  BaseFeature = -> Fillet050
  Radius = 0.5
  SupportTransform = false
FEATURE [PartDesign::Fillet] Fillet052
  Base = -> Fillet051 [Edge78]
  BaseFeature = -> Fillet051
  Radius = 0.5
  SupportTransform = false
FEATURE [PartDesign::Fillet] Fillet053
  Base = -> Fillet052 [Edge107]
  BaseFeature = -> Fillet052
  Radius = 0.5
  SupportTransform = false
FEATURE [PartDesign::Fillet] Fillet054
  Base = -> Fillet053 [Edge74]
  BaseFeature = -> Fillet053
  Radius = 0.5
  SupportTransform = false
FEATURE [PartDesign::Body] Body004
  Group = -> [Sketch004,Pad004,Fillet044,Fillet045,Fillet046,Fillet047,Fillet048,Fillet049,Fillet050,Fillet051,Fillet052,Fillet053,Fillet054]
  Origin = -> Origin009
  Placement = pos=(0,0,0) rot=(0,1,0;1.5708rad)
  Tip = -> Fillet054
FEATURE [Sketcher::SketchObject] Sketch
  FullyConstrained = false
  MapMode = 4
  Placement = pos=(0,0,0) rot=(0.707107,0.707107,0;3.14159rad)
  Support = -> [Body004]
  sketch-geometry (46):
    g0: LineSegment StartX=3.4 StartY=2.65 StartZ=0 EndX=3.4 EndY=-2.6657 EndZ=0
    g1: LineSegment StartX=2.63162 StartY=-3.4 StartZ=0 EndX=-2.65 EndY=-3.4 EndZ=0
    g2: LineSegment StartX=-3.4 StartY=-2.63136 StartZ=0 EndX=-3.4 EndY=2.61487 EndZ=0
    g3: LineSegment StartX=-10 StartY=10 StartZ=0 EndX=-3.125 EndY=10 EndZ=0
    g4: LineSegment StartX=10 StartY=10 StartZ=0 EndX=10 EndY=3.125 EndZ=0
    g5: LineSegment StartX=10 StartY=-10 StartZ=0 EndX=3.125 EndY=-10 EndZ=0
    g6: LineSegment StartX=-10 StartY=-10 StartZ=0 EndX=-10 EndY=-3.125 EndZ=0
    g7: GeomPoint X=3e-16 Y=0 Z=0
    g8: Circle CenterX=3e-16 CenterY=0 CenterZ=0 NormalX=0 NormalY=0 NormalZ=1 AngleXU=0 Radius=2.1
    g9: LineSegment StartX=-4.76483 StartY=8.08721 StartZ=0 EndX=-3.55 EndY=8.08721 EndZ=0
    g10: LineSegment StartX=8.24722 StartY=4.75 StartZ=0 EndX=8.24722 EndY=3.55 EndZ=0
    g11: LineSegment StartX=-8.2 StartY=-4.73729 StartZ=0 EndX=-8.2 EndY=-3.55 EndZ=0
    g12: LineSegment StartX=5.5 StartY=4.75 StartZ=0 EndX=8.24722 EndY=4.75 EndZ=0
    g13: LineSegment StartX=4.75 StartY=5.50457 StartZ=0 EndX=2.65 EndY=3.4 EndZ=0
    g14: LineSegment StartX=4.75 StartY=5.50457 StartZ=0 EndX=4.75 EndY=8.08721 EndZ=0
    g15: LineSegment StartX=3.4 StartY=2.65 StartZ=0 EndX=5.5 EndY=4.75 EndZ=0
    g16: LineSegment StartX=-4.76483 StartY=5.50457 StartZ=0 EndX=-2.66166 EndY=3.4 EndZ=0
    g17: LineSegment StartX=-5.5 StartY=4.70904 StartZ=0 EndX=-3.4 EndY=2.61487 EndZ=0
    g18: LineSegment StartX=-4.76483 StartY=5.50457 StartZ=0 EndX=-4.76483 EndY=8.08721 EndZ=0
    g19: LineSegment StartX=-5.5 StartY=4.70904 StartZ=0 EndX=-8.2 EndY=4.70904 EndZ=0
    g20: LineSegment StartX=-10 StartY=3.125 StartZ=0 EndX=-10 EndY=10 EndZ=0
    g21: LineSegment StartX=-8.2 StartY=3.55 StartZ=0 EndX=-8.2 EndY=4.70904 EndZ=0
    g22: LineSegment StartX=3.55 StartY=8.08721 StartZ=0 EndX=4.75 EndY=8.08721 EndZ=0
    g23: LineSegment StartX=3.125 StartY=10 StartZ=0 EndX=10 EndY=10 EndZ=0
    g24: LineSegment StartX=-5.5 StartY=-4.73729 StartZ=0 EndX=-8.2 EndY=-4.73729 EndZ=0
    g25: LineSegment StartX=-4.75 StartY=-5.5 StartZ=0 EndX=-2.65 EndY=-3.4 EndZ=0
    g26: LineSegment StartX=-4.75 StartY=-5.5 StartZ=0 EndX=-4.75 EndY=-8.2 EndZ=0
    g27: LineSegment StartX=4.73747 StartY=-5.5 StartZ=0 EndX=4.73747 EndY=-8.2 EndZ=0
    g28: LineSegment StartX=5.5 StartY=-4.7671 StartZ=0 EndX=8.24722 EndY=-4.7671 EndZ=0
    g29: LineSegment StartX=-3.125 StartY=-10 StartZ=0 EndX=-10 EndY=-10 EndZ=0
    g30: LineSegment StartX=-3.55 StartY=-8.2 StartZ=0 EndX=-4.75 EndY=-8.2 EndZ=0
    g31: LineSegment StartX=4.73747 StartY=-8.2 StartZ=0 EndX=3.55 EndY=-8.2 EndZ=0
    g32: LineSegment StartX=10 StartY=-3.125 StartZ=0 EndX=10 EndY=-10 EndZ=0
    g33: LineSegment StartX=8.24722 StartY=-3.55 StartZ=0 EndX=8.24722 EndY=-4.7671 EndZ=0
    g34: LineSegment StartX=-2.66166 StartY=3.4 StartZ=0 EndX=2.65 EndY=3.4 EndZ=0
    g35: LineSegment StartX=-3.4 StartY=-2.63136 StartZ=0 EndX=-5.5 EndY=-4.73729 EndZ=0
    g36: LineSegment StartX=3.4 StartY=-2.6657 StartZ=0 EndX=5.5 EndY=-4.7671 EndZ=0
    g37: LineSegment StartX=2.63162 StartY=-3.4 StartZ=0 EndX=4.73747 EndY=-5.5 EndZ=0
    g38: LineSegment StartX=-3.55 StartY=-8.2 StartZ=0 EndX=-3.125 EndY=-10 EndZ=0
    g39: LineSegment StartX=3.55 StartY=-8.2 StartZ=0 EndX=3.125 EndY=-10 EndZ=0
    g40: LineSegment StartX=-3.125 StartY=10 StartZ=0 EndX=-3.55 EndY=8.08721 EndZ=0
    g41: LineSegment StartX=3.125 StartY=10 StartZ=0 EndX=3.55 EndY=8.08721 EndZ=0
    g42: LineSegment StartX=8.24722 StartY=3.55 StartZ=0 EndX=10 EndY=3.125 EndZ=0
    g43: LineSegment StartX=10 StartY=-3.125 StartZ=0 EndX=8.24722 EndY=-3.55 EndZ=0
    g44: LineSegment StartX=-10 StartY=-3.125 StartZ=0 EndX=-8.2 EndY=-3.55 EndZ=0
    g45: LineSegment StartX=-10 StartY=3.125 StartZ=0 EndX=-8.2 EndY=3.55 EndZ=0
  constraints (61):
    c: Horizontal(g1)
    c: Vertical(g0)
    c: Vertical(g2)
    c: Coincident(g23,g4)
    c: Coincident(g32,g5)
    c: Coincident(g29,g6)
    c: Coincident(g20,g3)
    c: Horizontal(g3)
    c: Horizontal(g5)
    c: Vertical(g4)
    c: Vertical(g6)
    c: PointOnObject(g7,g-1)
    c: DistanceX(g3,g7) = 10
    c: DistanceX(g-1,g23) = 10
    c: DistanceY(g7,g3) = 10
    c: DistanceX(g3,g-1) = 10
    c: DistanceY(g32,g7) = 10
    c: Coincident(g8,g7)
    c: Radius(g8) = 2.1
    c: Horizontal(g9)
    c: Vertical(g10)
    c: Vertical(g11)
    c: Coincident(g12,g15)
    c: Horizontal(g12)
    c: Coincident(g14,g13)
    c: Vertical(g14)
    c: Coincident(g15,g0)
    c: Coincident(g13,g34)
    c: Coincident(g14,g22)
    c: Coincident(g18,g16)
    c: Vertical(g18)
    c: Coincident(g19,g17)
    c: Horizontal(g19)
    c: Coincident(g9,g18)
    c: Coincident(g21,g19)
    c: Coincident(g24,g35)
    c: Horizontal(g24)
    c: Coincident(g26,g25)
    c: Vertical(g26)
    c: Coincident(g27,g37)
    c: Vertical(g27)
    c: Coincident(g28,g36)
    c: Horizontal(g28)
    c: Coincident(g11,g24)
    c: Coincident(g26,g30)
    c: Coincident(g31,g27)
    c: Coincident(g12,g10)
    c: Coincident(g28,g33)
    c: Coincident(g25,g1)
    c: Coincident(g35,g2)
    c: Coincident(g17,g2)
    c: Coincident(g16,g34)
    c: Coincident(g1,g37)
    c: Coincident(g0,g36)
    c: Coincident(g39,g5)
    c: Coincident(g40,g3)
    c: Coincident(g42,g4)
    c: Coincident(g44,g6)
    c: Coincident(g21,g45)
    c: Coincident(g33,g43)
    c: Coincident(g10,g42)
FEATURE [PartDesign::Pad] Pad
  Direction = (2e-16,0,-1)
  Length = 300
  Length2 = 10
  Placement = pos=(0,0,0) rot=(0,1,0;1.5708rad)
  Profile = -> Sketch
  Type = 0
FEATURE [PartDesign::Fillet] Fillet
  Base = -> Pad [Edge53]
  BaseFeature = -> Pad
  Placement = pos=(0,0,0) rot=(0,1,0;1.5708rad)
  Radius = 1
  SupportTransform = false
FEATURE [PartDesign::Fillet] Fillet001
  Base = -> Fillet [Edge114]
  BaseFeature = -> Fillet
  Placement = pos=(0,0,0) rot=(0,1,0;1.5708rad)
  Radius = 1
  SupportTransform = false
FEATURE [PartDesign::Fillet] Fillet002
  Base = -> Fillet001 [Edge137,Edge95]
  BaseFeature = -> Fillet001
  Placement = pos=(0,0,0) rot=(0,1,0;1.5708rad)
  Radius = 0.5
  SupportTransform = false
FEATURE [PartDesign::Fillet] Fillet003
  Base = -> Fillet002 [Edge103]
  BaseFeature = -> Fillet002
  Placement = pos=(0,0,0) rot=(0.57735,0.57735,0.57735;2.0944rad)
  Radius = 0.5
  SupportTransform = false
FEATURE [PartDesign::Fillet] Fillet004
  Base = -> Fillet003 [Edge96]
  BaseFeature = -> Fillet003
  Placement = pos=(0,0,0) rot=(0.57735,0.57735,0.57735;2.0944rad)
  Radius = 0.5
  SupportTransform = false
FEATURE [PartDesign::Fillet] Fillet005
  Base = -> Fillet004 [Edge77]
  BaseFeature = -> Fillet004
  Placement = pos=(0,0,0) rot=(0.57735,0.57735,0.57735;2.0944rad)
  Radius = 0.5
  SupportTransform = false
FEATURE [PartDesign::Fillet] Fillet006
  Base = -> Fillet005 [Edge102]
  BaseFeature = -> Fillet005
  Placement = pos=(0,0,0) rot=(0.57735,0.57735,0.57735;2.0944rad)
  Radius = 0.5
  SupportTransform = false
FEATURE [PartDesign::Fillet] Fillet007
  Base = -> Fillet006 [Edge85]
  BaseFeature = -> Fillet006
  Placement = pos=(0,0,0) rot=(0.57735,0.57735,0.57735;2.0944rad)
  Radius = 0.5
  SupportTransform = false
FEATURE [PartDesign::Fillet] Fillet008
  Base = -> Fillet007 [Edge78]
  BaseFeature = -> Fillet007
  Placement = pos=(0,0,0) rot=(0.57735,0.57735,0.57735;2.0944rad)
  Radius = 0.5
  SupportTransform = false
FEATURE [PartDesign::Fillet] Fillet009
  Base = -> Fillet008 [Edge107]
  BaseFeature = -> Fillet008
  Placement = pos=(0,0,0) rot=(0.57735,0.57735,0.57735;2.0944rad)
  Radius = 0.5
  SupportTransform = false
FEATURE [PartDesign::Fillet] Fillet010
  Base = -> Fillet009 [Edge74]
  BaseFeature = -> Fillet009
  Radius = 0.5
  SupportTransform = false
FEATURE [PartDesign::Body] Body
  Group = -> [Sketch,Pad,Fillet,Fillet001,Fillet002,Fillet003,Fillet004,Fillet005,Fillet006,Fillet007,Fillet008,Fillet009,Fillet010]
  Origin = -> Origin001
  Placement = pos=(0,0,0) rot=(0,1,0;1.5708rad)
  Tip = -> Fillet010
FEATURE [App::Part] Part  label="2020-300-001"
  Group = -> [Body]
  Origin = -> Origin
  Placement = pos=(20,10,10) rot=(0,0,1;0rad)
FEATURE [App::Part] Part004  label="2020-300-005"
  Group = -> [Body004]
  Origin = -> Origin008
  Placement = pos=(10,10,0) rot=(0,1,0;4.71239rad)
FEATURE [Sketcher::SketchObject] Sketch005
  FullyConstrained = false
  MapMode = 5
  Support = -> [XY_Plane011]
  sketch-geometry (46):
    g0: LineSegment StartX=3.4 StartY=2.65 StartZ=0 EndX=3.4 EndY=-2.6657 EndZ=0
    g1: LineSegment StartX=2.63162 StartY=-3.4 StartZ=0 EndX=-2.65 EndY=-3.4 EndZ=0
    g2: LineSegment StartX=-3.4 StartY=-2.63136 StartZ=0 EndX=-3.4 EndY=2.61487 EndZ=0
    g3: LineSegment StartX=-10 StartY=10 StartZ=0 EndX=-3.125 EndY=10 EndZ=0
    g4: LineSegment StartX=10 StartY=10 StartZ=0 EndX=10 EndY=3.125 EndZ=0
    g5: LineSegment StartX=10 StartY=-10 StartZ=0 EndX=3.125 EndY=-10 EndZ=0
    g6: LineSegment StartX=-10 StartY=-10 StartZ=0 EndX=-10 EndY=-3.125 EndZ=0
    g7: GeomPoint X=3e-16 Y=0 Z=0
    g8: Circle CenterX=3e-16 CenterY=0 CenterZ=0 NormalX=0 NormalY=0 NormalZ=1 AngleXU=0 Radius=2.1
    g9: LineSegment StartX=-4.76483 StartY=8.08721 StartZ=0 EndX=-3.55 EndY=8.08721 EndZ=0
    g10: LineSegment StartX=8.24722 StartY=4.75 StartZ=0 EndX=8.24722 EndY=3.55 EndZ=0
    g11: LineSegment StartX=-8.2 StartY=-4.73729 StartZ=0 EndX=-8.2 EndY=-3.55 EndZ=0
    g12: LineSegment StartX=5.5 StartY=4.75 StartZ=0 EndX=8.24722 EndY=4.75 EndZ=0
    g13: LineSegment StartX=4.75 StartY=5.50457 StartZ=0 EndX=2.65 EndY=3.4 EndZ=0
    g14: LineSegment StartX=4.75 StartY=5.50457 StartZ=0 EndX=4.75 EndY=8.08721 EndZ=0
    g15: LineSegment StartX=3.4 StartY=2.65 StartZ=0 EndX=5.5 EndY=4.75 EndZ=0
    g16: LineSegment StartX=-4.76483 StartY=5.50457 StartZ=0 EndX=-2.66166 EndY=3.4 EndZ=0
    g17: LineSegment StartX=-5.5 StartY=4.70904 StartZ=0 EndX=-3.4 EndY=2.61487 EndZ=0
    g18: LineSegment StartX=-4.76483 StartY=5.50457 StartZ=0 EndX=-4.76483 EndY=8.08721 EndZ=0
    g19: LineSegment StartX=-5.5 StartY=4.70904 StartZ=0 EndX=-8.2 EndY=4.70904 EndZ=0
    g20: LineSegment StartX=-10 StartY=3.125 StartZ=0 EndX=-10 EndY=10 EndZ=0
    g21: LineSegment StartX=-8.2 StartY=3.55 StartZ=0 EndX=-8.2 EndY=4.70904 EndZ=0
    g22: LineSegment StartX=3.55 StartY=8.08721 StartZ=0 EndX=4.75 EndY=8.08721 EndZ=0
    g23: LineSegment StartX=3.125 StartY=10 StartZ=0 EndX=10 EndY=10 EndZ=0
    g24: LineSegment StartX=-5.5 StartY=-4.73729 StartZ=0 EndX=-8.2 EndY=-4.73729 EndZ=0
    g25: LineSegment StartX=-4.75 StartY=-5.5 StartZ=0 EndX=-2.65 EndY=-3.4 EndZ=0
    g26: LineSegment StartX=-4.75 StartY=-5.5 StartZ=0 EndX=-4.75 EndY=-8.2 EndZ=0
    g27: LineSegment StartX=4.73747 StartY=-5.5 StartZ=0 EndX=4.73747 EndY=-8.2 EndZ=0
    g28: LineSegment StartX=5.5 StartY=-4.7671 StartZ=0 EndX=8.24722 EndY=-4.7671 EndZ=0
    g29: LineSegment StartX=-3.125 StartY=-10 StartZ=0 EndX=-10 EndY=-10 EndZ=0
    g30: LineSegment StartX=-3.55 StartY=-8.2 StartZ=0 EndX=-4.75 EndY=-8.2 EndZ=0
    g31: LineSegment StartX=4.73747 StartY=-8.2 StartZ=0 EndX=3.55 EndY=-8.2 EndZ=0
    g32: LineSegment StartX=10 StartY=-3.125 StartZ=0 EndX=10 EndY=-10 EndZ=0
    g33: LineSegment StartX=8.24722 StartY=-3.55 StartZ=0 EndX=8.24722 EndY=-4.7671 EndZ=0
    g34: LineSegment StartX=-2.66166 StartY=3.4 StartZ=0 EndX=2.65 EndY=3.4 EndZ=0
    g35: LineSegment StartX=-3.4 StartY=-2.63136 StartZ=0 EndX=-5.5 EndY=-4.73729 EndZ=0
    g36: LineSegment StartX=3.4 StartY=-2.6657 StartZ=0 EndX=5.5 EndY=-4.7671 EndZ=0
    g37: LineSegment StartX=2.63162 StartY=-3.4 StartZ=0 EndX=4.73747 EndY=-5.5 EndZ=0
    g38: LineSegment StartX=-3.55 StartY=-8.2 StartZ=0 EndX=-3.125 EndY=-10 EndZ=0
    g39: LineSegment StartX=3.55 StartY=-8.2 StartZ=0 EndX=3.125 EndY=-10 EndZ=0
    g40: LineSegment StartX=-3.125 StartY=10 StartZ=0 EndX=-3.55 EndY=8.08721 EndZ=0
    g41: LineSegment StartX=3.125 StartY=10 StartZ=0 EndX=3.55 EndY=8.08721 EndZ=0
    g42: LineSegment StartX=8.24722 StartY=3.55 StartZ=0 EndX=10 EndY=3.125 EndZ=0
    g43: LineSegment StartX=10 StartY=-3.125 StartZ=0 EndX=8.24722 EndY=-3.55 EndZ=0
    g44: LineSegment StartX=-10 StartY=-3.125 StartZ=0 EndX=-8.2 EndY=-3.55 EndZ=0
    g45: LineSegment StartX=-10 StartY=3.125 StartZ=0 EndX=-8.2 EndY=3.55 EndZ=0
  constraints (61):
    c: Horizontal(g1)
    c: Vertical(g0)
    c: Vertical(g2)
    c: Coincident(g23,g4)
    c: Coincident(g32,g5)
    c: Coincident(g29,g6)
    c: Coincident(g20,g3)
    c: Horizontal(g3)
    c: Horizontal(g5)
    c: Vertical(g4)
    c: Vertical(g6)
    c: PointOnObject(g7,g-1)
    c: DistanceX(g3,g7) = 10
    c: DistanceX(g-1,g23) = 10
    c: DistanceY(g7,g3) = 10
    c: DistanceX(g3,g-1) = 10
    c: DistanceY(g32,g7) = 10
    c: Coincident(g8,g7)
    c: Radius(g8) = 2.1
    c: Horizontal(g9)
    c: Vertical(g10)
    c: Vertical(g11)
    c: Coincident(g12,g15)
    c: Horizontal(g12)
    c: Coincident(g14,g13)
    c: Vertical(g14)
    c: Coincident(g15,g0)
    c: Coincident(g13,g34)
    c: Coincident(g14,g22)
    c: Coincident(g18,g16)
    c: Vertical(g18)
    c: Coincident(g19,g17)
    c: Horizontal(g19)
    c: Coincident(g9,g18)
    c: Coincident(g21,g19)
    c: Coincident(g24,g35)
    c: Horizontal(g24)
    c: Coincident(g26,g25)
    c: Vertical(g26)
    c: Coincident(g27,g37)
    c: Vertical(g27)
    c: Coincident(g28,g36)
    c: Horizontal(g28)
    c: Coincident(g11,g24)
    c: Coincident(g26,g30)
    c: Coincident(g31,g27)
    c: Coincident(g12,g10)
    c: Coincident(g28,g33)
    c: Coincident(g25,g1)
    c: Coincident(g35,g2)
    c: Coincident(g17,g2)
    c: Coincident(g16,g34)
    c: Coincident(g1,g37)
    c: Coincident(g0,g36)
    c: Coincident(g39,g5)
    c: Coincident(g40,g3)
    c: Coincident(g42,g4)
    c: Coincident(g44,g6)
    c: Coincident(g21,g45)
    c: Coincident(g33,g43)
    c: Coincident(g10,g42)
FEATURE [PartDesign::Pad] Pad005
  Direction = (0,0,1)
  Length = 190
  Length2 = 10
  Profile = -> Sketch005
  Type = 0
FEATURE [PartDesign::Fillet] Fillet055
  Base = -> Pad005 [Edge53]
  BaseFeature = -> Pad005
  Radius = 1
  SupportTransform = false
FEATURE [PartDesign::Fillet] Fillet056
  Base = -> Fillet055 [Edge114]
  BaseFeature = -> Fillet055
  Radius = 1
  SupportTransform = false
FEATURE [PartDesign::Fillet] Fillet057
  Base = -> Fillet056 [Edge137,Edge95]
  BaseFeature = -> Fillet056
  Radius = 0.5
  SupportTransform = false
FEATURE [PartDesign::Fillet] Fillet058
  Base = -> Fillet057 [Edge103]
  BaseFeature = -> Fillet057
  Radius = 0.5
  SupportTransform = false
FEATURE [PartDesign::Fillet] Fillet059
  Base = -> Fillet058 [Edge96]
  BaseFeature = -> Fillet058
  Radius = 0.5
  SupportTransform = false
FEATURE [PartDesign::Fillet] Fillet060
  Base = -> Fillet059 [Edge77]
  BaseFeature = -> Fillet059
  Radius = 0.5
  SupportTransform = false
FEATURE [PartDesign::Fillet] Fillet061
  Base = -> Fillet060 [Edge102]
  BaseFeature = -> Fillet060
  Radius = 0.5
  SupportTransform = false
FEATURE [PartDesign::Fillet] Fillet062
  Base = -> Fillet061 [Edge85]
  BaseFeature = -> Fillet061
  Radius = 0.5
  SupportTransform = false
FEATURE [PartDesign::Fillet] Fillet063
  Base = -> Fillet062 [Edge78]
  BaseFeature = -> Fillet062
  Radius = 0.5
  SupportTransform = false
FEATURE [PartDesign::Fillet] Fillet064
  Base = -> Fillet063 [Edge107]
  BaseFeature = -> Fillet063
  Radius = 0.5
  SupportTransform = false
FEATURE [PartDesign::Fillet] Fillet065
  Base = -> Fillet064 [Edge74]
  BaseFeature = -> Fillet064
  Radius = 0.5
  SupportTransform = false
FEATURE [PartDesign::Body] Body005
  Group = -> [Sketch005,Pad005,Fillet055,Fillet056,Fillet057,Fillet058,Fillet059,Fillet060,Fillet061,Fillet062,Fillet063,Fillet064,Fillet065]
  Origin = -> Origin011
  Placement = pos=(0,0,0) rot=(0,1,0;1.5708rad)
  Tip = -> Fillet065
FEATURE [App::Part] Part005  label="2020-300-006"
  Group = -> [Body005]
  Origin = -> Origin010
  Placement = pos=(10,330,0) rot=(0,1,0;4.71239rad)
FEATURE [Sketcher::SketchObject] Sketch006
  FullyConstrained = false
  MapMode = 5
  Support = -> [XY_Plane013]
  sketch-geometry (46):
    g0: LineSegment StartX=3.4 StartY=2.65 StartZ=0 EndX=3.4 EndY=-2.6657 EndZ=0
    g1: LineSegment StartX=2.63162 StartY=-3.4 StartZ=0 EndX=-2.65 EndY=-3.4 EndZ=0
    g2: LineSegment StartX=-3.4 StartY=-2.63136 StartZ=0 EndX=-3.4 EndY=2.61487 EndZ=0
    g3: LineSegment StartX=-10 StartY=10 StartZ=0 EndX=-3.125 EndY=10 EndZ=0
    g4: LineSegment StartX=10 StartY=10 StartZ=0 EndX=10 EndY=3.125 EndZ=0
    g5: LineSegment StartX=10 StartY=-10 StartZ=0 EndX=3.125 EndY=-10 EndZ=0
    g6: LineSegment StartX=-10 StartY=-10 StartZ=0 EndX=-10 EndY=-3.125 EndZ=0
    g7: GeomPoint X=3e-16 Y=0 Z=0
    g8: Circle CenterX=3e-16 CenterY=0 CenterZ=0 NormalX=0 NormalY=0 NormalZ=1 AngleXU=0 Radius=2.1
    g9: LineSegment StartX=-4.76483 StartY=8.08721 StartZ=0 EndX=-3.55 EndY=8.08721 EndZ=0
    g10: LineSegment StartX=8.24722 StartY=4.75 StartZ=0 EndX=8.24722 EndY=3.55 EndZ=0
    g11: LineSegment StartX=-8.2 StartY=-4.73729 StartZ=0 EndX=-8.2 EndY=-3.55 EndZ=0
    g12: LineSegment StartX=5.5 StartY=4.75 StartZ=0 EndX=8.24722 EndY=4.75 EndZ=0
    g13: LineSegment StartX=4.75 StartY=5.50457 StartZ=0 EndX=2.65 EndY=3.4 EndZ=0
    g14: LineSegment StartX=4.75 StartY=5.50457 StartZ=0 EndX=4.75 EndY=8.08721 EndZ=0
    g15: LineSegment StartX=3.4 StartY=2.65 StartZ=0 EndX=5.5 EndY=4.75 EndZ=0
    g16: LineSegment StartX=-4.76483 StartY=5.50457 StartZ=0 EndX=-2.66166 EndY=3.4 EndZ=0
    g17: LineSegment StartX=-5.5 StartY=4.70904 StartZ=0 EndX=-3.4 EndY=2.61487 EndZ=0
    g18: LineSegment StartX=-4.76483 StartY=5.50457 StartZ=0 EndX=-4.76483 EndY=8.08721 EndZ=0
    g19: LineSegment StartX=-5.5 StartY=4.70904 StartZ=0 EndX=-8.2 EndY=4.70904 EndZ=0
    g20: LineSegment StartX=-10 StartY=3.125 StartZ=0 EndX=-10 EndY=10 EndZ=0
    g21: LineSegment StartX=-8.2 StartY=3.55 StartZ=0 EndX=-8.2 EndY=4.70904 EndZ=0
    g22: LineSegment StartX=3.55 StartY=8.08721 StartZ=0 EndX=4.75 EndY=8.08721 EndZ=0
    g23: LineSegment StartX=3.125 StartY=10 StartZ=0 EndX=10 EndY=10 EndZ=0
    g24: LineSegment StartX=-5.5 StartY=-4.73729 StartZ=0 EndX=-8.2 EndY=-4.73729 EndZ=0
    g25: LineSegment StartX=-4.75 StartY=-5.5 StartZ=0 EndX=-2.65 EndY=-3.4 EndZ=0
    g26: LineSegment StartX=-4.75 StartY=-5.5 StartZ=0 EndX=-4.75 EndY=-8.2 EndZ=0
    g27: LineSegment StartX=4.73747 StartY=-5.5 StartZ=0 EndX=4.73747 EndY=-8.2 EndZ=0
    g28: LineSegment StartX=5.5 StartY=-4.7671 StartZ=0 EndX=8.24722 EndY=-4.7671 EndZ=0
    g29: LineSegment StartX=-3.125 StartY=-10 StartZ=0 EndX=-10 EndY=-10 EndZ=0
    g30: LineSegment StartX=-3.55 StartY=-8.2 StartZ=0 EndX=-4.75 EndY=-8.2 EndZ=0
    g31: LineSegment StartX=4.73747 StartY=-8.2 StartZ=0 EndX=3.55 EndY=-8.2 EndZ=0
    g32: LineSegment StartX=10 StartY=-3.125 StartZ=0 EndX=10 EndY=-10 EndZ=0
    g33: LineSegment StartX=8.24722 StartY=-3.55 StartZ=0 EndX=8.24722 EndY=-4.7671 EndZ=0
    g34: LineSegment StartX=-2.66166 StartY=3.4 StartZ=0 EndX=2.65 EndY=3.4 EndZ=0
    g35: LineSegment StartX=-3.4 StartY=-2.63136 StartZ=0 EndX=-5.5 EndY=-4.73729 EndZ=0
    g36: LineSegment StartX=3.4 StartY=-2.6657 StartZ=0 EndX=5.5 EndY=-4.7671 EndZ=0
    g37: LineSegment StartX=2.63162 StartY=-3.4 StartZ=0 EndX=4.73747 EndY=-5.5 EndZ=0
    g38: LineSegment StartX=-3.55 StartY=-8.2 StartZ=0 EndX=-3.125 EndY=-10 EndZ=0
    g39: LineSegment StartX=3.55 StartY=-8.2 StartZ=0 EndX=3.125 EndY=-10 EndZ=0
    g40: LineSegment StartX=-3.125 StartY=10 StartZ=0 EndX=-3.55 EndY=8.08721 EndZ=0
    g41: LineSegment StartX=3.125 StartY=10 StartZ=0 EndX=3.55 EndY=8.08721 EndZ=0
    g42: LineSegment StartX=8.24722 StartY=3.55 StartZ=0 EndX=10 EndY=3.125 EndZ=0
    g43: LineSegment StartX=10 StartY=-3.125 StartZ=0 EndX=8.24722 EndY=-3.55 EndZ=0
    g44: LineSegment StartX=-10 StartY=-3.125 StartZ=0 EndX=-8.2 EndY=-3.55 EndZ=0
    g45: LineSegment StartX=-10 StartY=3.125 StartZ=0 EndX=-8.2 EndY=3.55 EndZ=0
  constraints (61):
    c: Horizontal(g1)
    c: Vertical(g0)
    c: Vertical(g2)
    c: Coincident(g23,g4)
    c: Coincident(g32,g5)
    c: Coincident(g29,g6)
    c: Coincident(g20,g3)
    c: Horizontal(g3)
    c: Horizontal(g5)
    c: Vertical(g4)
    c: Vertical(g6)
    c: PointOnObject(g7,g-1)
    c: DistanceX(g3,g7) = 10
    c: DistanceX(g-1,g23) = 10
    c: DistanceY(g7,g3) = 10
    c: DistanceX(g3,g-1) = 10
    c: DistanceY(g32,g7) = 10
    c: Coincident(g8,g7)
    c: Radius(g8) = 2.1
    c: Horizontal(g9)
    c: Vertical(g10)
    c: Vertical(g11)
    c: Coincident(g12,g15)
    c: Horizontal(g12)
    c: Coincident(g14,g13)
    c: Vertical(g14)
    c: Coincident(g15,g0)
    c: Coincident(g13,g34)
    c: Coincident(g14,g22)
    c: Coincident(g18,g16)
    c: Vertical(g18)
    c: Coincident(g19,g17)
    c: Horizontal(g19)
    c: Coincident(g9,g18)
    c: Coincident(g21,g19)
    c: Coincident(g24,g35)
    c: Horizontal(g24)
    c: Coincident(g26,g25)
    c: Vertical(g26)
    c: Coincident(g27,g37)
    c: Vertical(g27)
    c: Coincident(g28,g36)
    c: Horizontal(g28)
    c: Coincident(g11,g24)
    c: Coincident(g26,g30)
    c: Coincident(g31,g27)
    c: Coincident(g12,g10)
    c: Coincident(g28,g33)
    c: Coincident(g25,g1)
    c: Coincident(g35,g2)
    c: Coincident(g17,g2)
    c: Coincident(g16,g34)
    c: Coincident(g1,g37)
    c: Coincident(g0,g36)
    c: Coincident(g39,g5)
    c: Coincident(g40,g3)
    c: Coincident(g42,g4)
    c: Coincident(g44,g6)
    c: Coincident(g21,g45)
    c: Coincident(g33,g43)
    c: Coincident(g10,g42)
FEATURE [PartDesign::Pad] Pad006
  Direction = (0,0,1)
  Length = 190
  Length2 = 10
  Profile = -> Sketch006
  Type = 0
FEATURE [PartDesign::Fillet] Fillet066
  Base = -> Pad006 [Edge53]
  BaseFeature = -> Pad006
  Radius = 1
  SupportTransform = false
FEATURE [PartDesign::Fillet] Fillet067
  Base = -> Fillet066 [Edge114]
  BaseFeature = -> Fillet066
  Radius = 1
  SupportTransform = false
FEATURE [PartDesign::Fillet] Fillet068
  Base = -> Fillet067 [Edge137,Edge95]
  BaseFeature = -> Fillet067
  Radius = 0.5
  SupportTransform = false
FEATURE [PartDesign::Fillet] Fillet069
  Base = -> Fillet068 [Edge103]
  BaseFeature = -> Fillet068
  Radius = 0.5
  SupportTransform = false
FEATURE [PartDesign::Fillet] Fillet070
  Base = -> Fillet069 [Edge96]
  BaseFeature = -> Fillet069
  Radius = 0.5
  SupportTransform = false
FEATURE [PartDesign::Fillet] Fillet071
  Base = -> Fillet070 [Edge77]
  BaseFeature = -> Fillet070
  Radius = 0.5
  SupportTransform = false
FEATURE [PartDesign::Fillet] Fillet072
  Base = -> Fillet071 [Edge102]
  BaseFeature = -> Fillet071
  Radius = 0.5
  SupportTransform = false
FEATURE [PartDesign::Fillet] Fillet073
  Base = -> Fillet072 [Edge85]
  BaseFeature = -> Fillet072
  Radius = 0.5
  SupportTransform = false
FEATURE [PartDesign::Fillet] Fillet074
  Base = -> Fillet073 [Edge78]
  BaseFeature = -> Fillet073
  Radius = 0.5
  SupportTransform = false
FEATURE [PartDesign::Fillet] Fillet075
  Base = -> Fillet074 [Edge107]
  BaseFeature = -> Fillet074
  Radius = 0.5
  SupportTransform = false
FEATURE [PartDesign::Fillet] Fillet076
  Base = -> Fillet075 [Edge74]
  BaseFeature = -> Fillet075
  Radius = 0.5
  SupportTransform = false
FEATURE [PartDesign::Body] Body006
  Group = -> [Sketch006,Pad006,Fillet066,Fillet067,Fillet068,Fillet069,Fillet070,Fillet071,Fillet072,Fillet073,Fillet074,Fillet075,Fillet076]
  Origin = -> Origin013
  Placement = pos=(0,0,0) rot=(0,1,0;1.5708rad)
  Tip = -> Fillet076
FEATURE [App::Part] Part006  label="2020-300-007"
  Group = -> [Body006]
  Origin = -> Origin012
  Placement = pos=(330,10,0) rot=(0,1,0;4.71239rad)
FEATURE [Sketcher::SketchObject] Sketch007
  FullyConstrained = false
  MapMode = 5
  Support = -> [XY_Plane015]
  sketch-geometry (46):
    g0: LineSegment StartX=3.4 StartY=2.65 StartZ=0 EndX=3.4 EndY=-2.6657 EndZ=0
    g1: LineSegment StartX=2.63162 StartY=-3.4 StartZ=0 EndX=-2.65 EndY=-3.4 EndZ=0
    g2: LineSegment StartX=-3.4 StartY=-2.63136 StartZ=0 EndX=-3.4 EndY=2.61487 EndZ=0
    g3: LineSegment StartX=-10 StartY=10 StartZ=0 EndX=-3.125 EndY=10 EndZ=0
    g4: LineSegment StartX=10 StartY=10 StartZ=0 EndX=10 EndY=3.125 EndZ=0
    g5: LineSegment StartX=10 StartY=-10 StartZ=0 EndX=3.125 EndY=-10 EndZ=0
    g6: LineSegment StartX=-10 StartY=-10 StartZ=0 EndX=-10 EndY=-3.125 EndZ=0
    g7: GeomPoint X=3e-16 Y=0 Z=0
    g8: Circle CenterX=3e-16 CenterY=0 CenterZ=0 NormalX=0 NormalY=0 NormalZ=1 AngleXU=0 Radius=2.1
    g9: LineSegment StartX=-4.76483 StartY=8.08721 StartZ=0 EndX=-3.55 EndY=8.08721 EndZ=0
    g10: LineSegment StartX=8.24722 StartY=4.75 StartZ=0 EndX=8.24722 EndY=3.55 EndZ=0
    g11: LineSegment StartX=-8.2 StartY=-4.73729 StartZ=0 EndX=-8.2 EndY=-3.55 EndZ=0
    g12: LineSegment StartX=5.5 StartY=4.75 StartZ=0 EndX=8.24722 EndY=4.75 EndZ=0
    g13: LineSegment StartX=4.75 StartY=5.50457 StartZ=0 EndX=2.65 EndY=3.4 EndZ=0
    g14: LineSegment StartX=4.75 StartY=5.50457 StartZ=0 EndX=4.75 EndY=8.08721 EndZ=0
    g15: LineSegment StartX=3.4 StartY=2.65 StartZ=0 EndX=5.5 EndY=4.75 EndZ=0
    g16: LineSegment StartX=-4.76483 StartY=5.50457 StartZ=0 EndX=-2.66166 EndY=3.4 EndZ=0
    g17: LineSegment StartX=-5.5 StartY=4.70904 StartZ=0 EndX=-3.4 EndY=2.61487 EndZ=0
    g18: LineSegment StartX=-4.76483 StartY=5.50457 StartZ=0 EndX=-4.76483 EndY=8.08721 EndZ=0
    g19: LineSegment StartX=-5.5 StartY=4.70904 StartZ=0 EndX=-8.2 EndY=4.70904 EndZ=0
    g20: LineSegment StartX=-10 StartY=3.125 StartZ=0 EndX=-10 EndY=10 EndZ=0
    g21: LineSegment StartX=-8.2 StartY=3.55 StartZ=0 EndX=-8.2 EndY=4.70904 EndZ=0
    g22: LineSegment StartX=3.55 StartY=8.08721 StartZ=0 EndX=4.75 EndY=8.08721 EndZ=0
    g23: LineSegment StartX=3.125 StartY=10 StartZ=0 EndX=10 EndY=10 EndZ=0
    g24: LineSegment StartX=-5.5 StartY=-4.73729 StartZ=0 EndX=-8.2 EndY=-4.73729 EndZ=0
    g25: LineSegment StartX=-4.75 StartY=-5.5 StartZ=0 EndX=-2.65 EndY=-3.4 EndZ=0
    g26: LineSegment StartX=-4.75 StartY=-5.5 StartZ=0 EndX=-4.75 EndY=-8.2 EndZ=0
    g27: LineSegment StartX=4.73747 StartY=-5.5 StartZ=0 EndX=4.73747 EndY=-8.2 EndZ=0
    g28: LineSegment StartX=5.5 StartY=-4.7671 StartZ=0 EndX=8.24722 EndY=-4.7671 EndZ=0
    g29: LineSegment StartX=-3.125 StartY=-10 StartZ=0 EndX=-10 EndY=-10 EndZ=0
    g30: LineSegment StartX=-3.55 StartY=-8.2 StartZ=0 EndX=-4.75 EndY=-8.2 EndZ=0
    g31: LineSegment StartX=4.73747 StartY=-8.2 StartZ=0 EndX=3.55 EndY=-8.2 EndZ=0
    g32: LineSegment StartX=10 StartY=-3.125 StartZ=0 EndX=10 EndY=-10 EndZ=0
    g33: LineSegment StartX=8.24722 StartY=-3.55 StartZ=0 EndX=8.24722 EndY=-4.7671 EndZ=0
    g34: LineSegment StartX=-2.66166 StartY=3.4 StartZ=0 EndX=2.65 EndY=3.4 EndZ=0
    g35: LineSegment StartX=-3.4 StartY=-2.63136 StartZ=0 EndX=-5.5 EndY=-4.73729 EndZ=0
    g36: LineSegment StartX=3.4 StartY=-2.6657 StartZ=0 EndX=5.5 EndY=-4.7671 EndZ=0
    g37: LineSegment StartX=2.63162 StartY=-3.4 StartZ=0 EndX=4.73747 EndY=-5.5 EndZ=0
    g38: LineSegment StartX=-3.55 StartY=-8.2 StartZ=0 EndX=-3.125 EndY=-10 EndZ=0
    g39: LineSegment StartX=3.55 StartY=-8.2 StartZ=0 EndX=3.125 EndY=-10 EndZ=0
    g40: LineSegment StartX=-3.125 StartY=10 StartZ=0 EndX=-3.55 EndY=8.08721 EndZ=0
    g41: LineSegment StartX=3.125 StartY=10 StartZ=0 EndX=3.55 EndY=8.08721 EndZ=0
    g42: LineSegment StartX=8.24722 StartY=3.55 StartZ=0 EndX=10 EndY=3.125 EndZ=0
    g43: LineSegment StartX=10 StartY=-3.125 StartZ=0 EndX=8.24722 EndY=-3.55 EndZ=0
    g44: LineSegment StartX=-10 StartY=-3.125 StartZ=0 EndX=-8.2 EndY=-3.55 EndZ=0
    g45: LineSegment StartX=-10 StartY=3.125 StartZ=0 EndX=-8.2 EndY=3.55 EndZ=0
  constraints (61):
    c: Horizontal(g1)
    c: Vertical(g0)
    c: Vertical(g2)
    c: Coincident(g23,g4)
    c: Coincident(g32,g5)
    c: Coincident(g29,g6)
    c: Coincident(g20,g3)
    c: Horizontal(g3)
    c: Horizontal(g5)
    c: Vertical(g4)
    c: Vertical(g6)
    c: PointOnObject(g7,g-1)
    c: DistanceX(g3,g7) = 10
    c: DistanceX(g-1,g23) = 10
    c: DistanceY(g7,g3) = 10
    c: DistanceX(g3,g-1) = 10
    c: DistanceY(g32,g7) = 10
    c: Coincident(g8,g7)
    c: Radius(g8) = 2.1
    c: Horizontal(g9)
    c: Vertical(g10)
    c: Vertical(g11)
    c: Coincident(g12,g15)
    c: Horizontal(g12)
    c: Coincident(g14,g13)
    c: Vertical(g14)
    c: Coincident(g15,g0)
    c: Coincident(g13,g34)
    c: Coincident(g14,g22)
    c: Coincident(g18,g16)
    c: Vertical(g18)
    c: Coincident(g19,g17)
    c: Horizontal(g19)
    c: Coincident(g9,g18)
    c: Coincident(g21,g19)
    c: Coincident(g24,g35)
    c: Horizontal(g24)
    c: Coincident(g26,g25)
    c: Vertical(g26)
    c: Coincident(g27,g37)
    c: Vertical(g27)
    c: Coincident(g28,g36)
    c: Horizontal(g28)
    c: Coincident(g11,g24)
    c: Coincident(g26,g30)
    c: Coincident(g31,g27)
    c: Coincident(g12,g10)
    c: Coincident(g28,g33)
    c: Coincident(g25,g1)
    c: Coincident(g35,g2)
    c: Coincident(g17,g2)
    c: Coincident(g16,g34)
    c: Coincident(g1,g37)
    c: Coincident(g0,g36)
    c: Coincident(g39,g5)
    c: Coincident(g40,g3)
    c: Coincident(g42,g4)
    c: Coincident(g44,g6)
    c: Coincident(g21,g45)
    c: Coincident(g33,g43)
    c: Coincident(g10,g42)
FEATURE [PartDesign::Pad] Pad007
  Direction = (0,0,1)
  Length = 190
  Length2 = 10
  Profile = -> Sketch007
  Type = 0
FEATURE [PartDesign::Fillet] Fillet077
  Base = -> Pad007 [Edge53]
  BaseFeature = -> Pad007
  Radius = 1
  SupportTransform = false
FEATURE [PartDesign::Fillet] Fillet078
  Base = -> Fillet077 [Edge114]
  BaseFeature = -> Fillet077
  Radius = 1
  SupportTransform = false
FEATURE [PartDesign::Fillet] Fillet079
  Base = -> Fillet078 [Edge137,Edge95]
  BaseFeature = -> Fillet078
  Radius = 0.5
  SupportTransform = false
FEATURE [PartDesign::Fillet] Fillet080
  Base = -> Fillet079 [Edge103]
  BaseFeature = -> Fillet079
  Radius = 0.5
  SupportTransform = false
FEATURE [PartDesign::Fillet] Fillet081
  Base = -> Fillet080 [Edge96]
  BaseFeature = -> Fillet080
  Radius = 0.5
  SupportTransform = false
FEATURE [PartDesign::Fillet] Fillet082
  Base = -> Fillet081 [Edge77]
  BaseFeature = -> Fillet081
  Radius = 0.5
  SupportTransform = false
FEATURE [PartDesign::Fillet] Fillet083
  Base = -> Fillet082 [Edge102]
  BaseFeature = -> Fillet082
  Radius = 0.5
  SupportTransform = false
FEATURE [PartDesign::Fillet] Fillet084
  Base = -> Fillet083 [Edge85]
  BaseFeature = -> Fillet083
  Radius = 0.5
  SupportTransform = false
FEATURE [PartDesign::Fillet] Fillet085
  Base = -> Fillet084 [Edge78]
  BaseFeature = -> Fillet084
  Radius = 0.5
  SupportTransform = false
FEATURE [PartDesign::Fillet] Fillet086
  Base = -> Fillet085 [Edge107]
  BaseFeature = -> Fillet085
  Radius = 0.5
  SupportTransform = false
FEATURE [PartDesign::Fillet] Fillet087
  Base = -> Fillet086 [Edge74]
  BaseFeature = -> Fillet086
  Radius = 0.5
  SupportTransform = false
FEATURE [PartDesign::Body] Body007
  Group = -> [Sketch007,Pad007,Fillet077,Fillet078,Fillet079,Fillet080,Fillet081,Fillet082,Fillet083,Fillet084,Fillet085,Fillet086,Fillet087]
  Origin = -> Origin015
  Placement = pos=(0,0,0) rot=(0,1,0;1.5708rad)
  Tip = -> Fillet087
FEATURE [App::Part] Part007  label="2020-300-008"
  Group = -> [Body007]
  Origin = -> Origin014
  Placement = pos=(330,330,0) rot=(0,1,0;4.71239rad)
FEATURE [Sketcher::SketchObject] Sketch008
  FullyConstrained = false
  MapMode = 5
  Support = -> [XY_Plane017]
  sketch-geometry (46):
    g0: LineSegment StartX=3.4 StartY=2.65 StartZ=0 EndX=3.4 EndY=-2.6657 EndZ=0
    g1: LineSegment StartX=2.63162 StartY=-3.4 StartZ=0 EndX=-2.65 EndY=-3.4 EndZ=0
    g2: LineSegment StartX=-3.4 StartY=-2.63136 StartZ=0 EndX=-3.4 EndY=2.61487 EndZ=0
    g3: LineSegment StartX=-10 StartY=10 StartZ=0 EndX=-3.125 EndY=10 EndZ=0
    g4: LineSegment StartX=10 StartY=10 StartZ=0 EndX=10 EndY=3.125 EndZ=0
    g5: LineSegment StartX=10 StartY=-10 StartZ=0 EndX=3.125 EndY=-10 EndZ=0
    g6: LineSegment StartX=-10 StartY=-10 StartZ=0 EndX=-10 EndY=-3.125 EndZ=0
    g7: GeomPoint X=3e-16 Y=0 Z=0
    g8: Circle CenterX=3e-16 CenterY=0 CenterZ=0 NormalX=0 NormalY=0 NormalZ=1 AngleXU=0 Radius=2.1
    g9: LineSegment StartX=-4.76483 StartY=8.08721 StartZ=0 EndX=-3.55 EndY=8.08721 EndZ=0
    g10: LineSegment StartX=8.24722 StartY=4.75 StartZ=0 EndX=8.24722 EndY=3.55 EndZ=0
    g11: LineSegment StartX=-8.2 StartY=-4.73729 StartZ=0 EndX=-8.2 EndY=-3.55 EndZ=0
    g12: LineSegment StartX=5.5 StartY=4.75 StartZ=0 EndX=8.24722 EndY=4.75 EndZ=0
    g13: LineSegment StartX=4.75 StartY=5.50457 StartZ=0 EndX=2.65 EndY=3.4 EndZ=0
    g14: LineSegment StartX=4.75 StartY=5.50457 StartZ=0 EndX=4.75 EndY=8.08721 EndZ=0
    g15: LineSegment StartX=3.4 StartY=2.65 StartZ=0 EndX=5.5 EndY=4.75 EndZ=0
    g16: LineSegment StartX=-4.76483 StartY=5.50457 StartZ=0 EndX=-2.66166 EndY=3.4 EndZ=0
    g17: LineSegment StartX=-5.5 StartY=4.70904 StartZ=0 EndX=-3.4 EndY=2.61487 EndZ=0
    g18: LineSegment StartX=-4.76483 StartY=5.50457 StartZ=0 EndX=-4.76483 EndY=8.08721 EndZ=0
    g19: LineSegment StartX=-5.5 StartY=4.70904 StartZ=0 EndX=-8.2 EndY=4.70904 EndZ=0
    g20: LineSegment StartX=-10 StartY=3.125 StartZ=0 EndX=-10 EndY=10 EndZ=0
    g21: LineSegment StartX=-8.2 StartY=3.55 StartZ=0 EndX=-8.2 EndY=4.70904 EndZ=0
    g22: LineSegment StartX=3.55 StartY=8.08721 StartZ=0 EndX=4.75 EndY=8.08721 EndZ=0
    g23: LineSegment StartX=3.125 StartY=10 StartZ=0 EndX=10 EndY=10 EndZ=0
    g24: LineSegment StartX=-5.5 StartY=-4.73729 StartZ=0 EndX=-8.2 EndY=-4.73729 EndZ=0
    g25: LineSegment StartX=-4.75 StartY=-5.5 StartZ=0 EndX=-2.65 EndY=-3.4 EndZ=0
    g26: LineSegment StartX=-4.75 StartY=-5.5 StartZ=0 EndX=-4.75 EndY=-8.2 EndZ=0
    g27: LineSegment StartX=4.73747 StartY=-5.5 StartZ=0 EndX=4.73747 EndY=-8.2 EndZ=0
    g28: LineSegment StartX=5.5 StartY=-4.7671 StartZ=0 EndX=8.24722 EndY=-4.7671 EndZ=0
    g29: LineSegment StartX=-3.125 StartY=-10 StartZ=0 EndX=-10 EndY=-10 EndZ=0
    g30: LineSegment StartX=-3.55 StartY=-8.2 StartZ=0 EndX=-4.75 EndY=-8.2 EndZ=0
    g31: LineSegment StartX=4.73747 StartY=-8.2 StartZ=0 EndX=3.55 EndY=-8.2 EndZ=0
    g32: LineSegment StartX=10 StartY=-3.125 StartZ=0 EndX=10 EndY=-10 EndZ=0
    g33: LineSegment StartX=8.24722 StartY=-3.55 StartZ=0 EndX=8.24722 EndY=-4.7671 EndZ=0
    g34: LineSegment StartX=-2.66166 StartY=3.4 StartZ=0 EndX=2.65 EndY=3.4 EndZ=0
    g35: LineSegment StartX=-3.4 StartY=-2.63136 StartZ=0 EndX=-5.5 EndY=-4.73729 EndZ=0
    g36: LineSegment StartX=3.4 StartY=-2.6657 StartZ=0 EndX=5.5 EndY=-4.7671 EndZ=0
    g37: LineSegment StartX=2.63162 StartY=-3.4 StartZ=0 EndX=4.73747 EndY=-5.5 EndZ=0
    g38: LineSegment StartX=-3.55 StartY=-8.2 StartZ=0 EndX=-3.125 EndY=-10 EndZ=0
    g39: LineSegment StartX=3.55 StartY=-8.2 StartZ=0 EndX=3.125 EndY=-10 EndZ=0
    g40: LineSegment StartX=-3.125 StartY=10 StartZ=0 EndX=-3.55 EndY=8.08721 EndZ=0
    g41: LineSegment StartX=3.125 StartY=10 StartZ=0 EndX=3.55 EndY=8.08721 EndZ=0
    g42: LineSegment StartX=8.24722 StartY=3.55 StartZ=0 EndX=10 EndY=3.125 EndZ=0
    g43: LineSegment StartX=10 StartY=-3.125 StartZ=0 EndX=8.24722 EndY=-3.55 EndZ=0
    g44: LineSegment StartX=-10 StartY=-3.125 StartZ=0 EndX=-8.2 EndY=-3.55 EndZ=0
    g45: LineSegment StartX=-10 StartY=3.125 StartZ=0 EndX=-8.2 EndY=3.55 EndZ=0
  constraints (61):
    c: Horizontal(g1)
    c: Vertical(g0)
    c: Vertical(g2)
    c: Coincident(g23,g4)
    c: Coincident(g32,g5)
    c: Coincident(g29,g6)
    c: Coincident(g20,g3)
    c: Horizontal(g3)
    c: Horizontal(g5)
    c: Vertical(g4)
    c: Vertical(g6)
    c: PointOnObject(g7,g-1)
    c: DistanceX(g3,g7) = 10
    c: DistanceX(g-1,g23) = 10
    c: DistanceY(g7,g3) = 10
    c: DistanceX(g3,g-1) = 10
    c: DistanceY(g32,g7) = 10
    c: Coincident(g8,g7)
    c: Radius(g8) = 2.1
    c: Horizontal(g9)
    c: Vertical(g10)
    c: Vertical(g11)
    c: Coincident(g12,g15)
    c: Horizontal(g12)
    c: Coincident(g14,g13)
    c: Vertical(g14)
    c: Coincident(g15,g0)
    c: Coincident(g13,g34)
    c: Coincident(g14,g22)
    c: Coincident(g18,g16)
    c: Vertical(g18)
    c: Coincident(g19,g17)
    c: Horizontal(g19)
    c: Coincident(g9,g18)
    c: Coincident(g21,g19)
    c: Coincident(g24,g35)
    c: Horizontal(g24)
    c: Coincident(g26,g25)
    c: Vertical(g26)
    c: Coincident(g27,g37)
    c: Vertical(g27)
    c: Coincident(g28,g36)
    c: Horizontal(g28)
    c: Coincident(g11,g24)
    c: Coincident(g26,g30)
    c: Coincident(g31,g27)
    c: Coincident(g12,g10)
    c: Coincident(g28,g33)
    c: Coincident(g25,g1)
    c: Coincident(g35,g2)
    c: Coincident(g17,g2)
    c: Coincident(g16,g34)
    c: Coincident(g1,g37)
    c: Coincident(g0,g36)
    c: Coincident(g39,g5)
    c: Coincident(g40,g3)
    c: Coincident(g42,g4)
    c: Coincident(g44,g6)
    c: Coincident(g21,g45)
    c: Coincident(g33,g43)
    c: Coincident(g10,g42)
FEATURE [PartDesign::Pad] Pad008
  Direction = (0,0,1)
  Length = 300
  Length2 = 10
  Profile = -> Sketch008
  Type = 0
FEATURE [PartDesign::Fillet] Fillet088
  Base = -> Pad008 [Edge53]
  BaseFeature = -> Pad008
  Radius = 1
  SupportTransform = false
FEATURE [PartDesign::Fillet] Fillet089
  Base = -> Fillet088 [Edge114]
  BaseFeature = -> Fillet088
  Radius = 1
  SupportTransform = false
FEATURE [PartDesign::Fillet] Fillet090
  Base = -> Fillet089 [Edge137,Edge95]
  BaseFeature = -> Fillet089
  Radius = 0.5
  SupportTransform = false
FEATURE [PartDesign::Fillet] Fillet091
  Base = -> Fillet090 [Edge103]
  BaseFeature = -> Fillet090
  Radius = 0.5
  SupportTransform = false
FEATURE [PartDesign::Fillet] Fillet092
  Base = -> Fillet091 [Edge96]
  BaseFeature = -> Fillet091
  Radius = 0.5
  SupportTransform = false
FEATURE [PartDesign::Fillet] Fillet093
  Base = -> Fillet092 [Edge77]
  BaseFeature = -> Fillet092
  Radius = 0.5
  SupportTransform = false
FEATURE [PartDesign::Fillet] Fillet094
  Base = -> Fillet093 [Edge102]
  BaseFeature = -> Fillet093
  Radius = 0.5
  SupportTransform = false
FEATURE [PartDesign::Fillet] Fillet095
  Base = -> Fillet094 [Edge85]
  BaseFeature = -> Fillet094
  Radius = 0.5
  SupportTransform = false
FEATURE [PartDesign::Fillet] Fillet096
  Base = -> Fillet095 [Edge78]
  BaseFeature = -> Fillet095
  Radius = 0.5
  SupportTransform = false
FEATURE [PartDesign::Fillet] Fillet097
  Base = -> Fillet096 [Edge107]
  BaseFeature = -> Fillet096
  Radius = 0.5
  SupportTransform = false
FEATURE [PartDesign::Fillet] Fillet098
  Base = -> Fillet097 [Edge74]
  BaseFeature = -> Fillet097
  Radius = 0.5
  SupportTransform = false
FEATURE [PartDesign::Body] Body008
  Group = -> [Sketch008,Pad008,Fillet088,Fillet089,Fillet090,Fillet091,Fillet092,Fillet093,Fillet094,Fillet095,Fillet096,Fillet097,Fillet098]
  Origin = -> Origin017
  Placement = pos=(0,0,0) rot=(0,1,0;1.5708rad)
  Tip = -> Fillet098
FEATURE [App::Part] Part008  label="2020-300-009"
  Group = -> [Body008]
  Origin = -> Origin016
  Placement = pos=(20,330,180) rot=(0,0,1;0rad)
FEATURE [Sketcher::SketchObject] Sketch009
  FullyConstrained = false
  MapMode = 5
  Support = -> [XY_Plane019]
  sketch-geometry (46):
    g0: LineSegment StartX=3.4 StartY=2.65 StartZ=0 EndX=3.4 EndY=-2.6657 EndZ=0
    g1: LineSegment StartX=2.63162 StartY=-3.4 StartZ=0 EndX=-2.65 EndY=-3.4 EndZ=0
    g2: LineSegment StartX=-3.4 StartY=-2.63136 StartZ=0 EndX=-3.4 EndY=2.61487 EndZ=0
    g3: LineSegment StartX=-10 StartY=10 StartZ=0 EndX=-3.125 EndY=10 EndZ=0
    g4: LineSegment StartX=10 StartY=10 StartZ=0 EndX=10 EndY=3.125 EndZ=0
    g5: LineSegment StartX=10 StartY=-10 StartZ=0 EndX=3.125 EndY=-10 EndZ=0
    g6: LineSegment StartX=-10 StartY=-10 StartZ=0 EndX=-10 EndY=-3.125 EndZ=0
    g7: GeomPoint X=3e-16 Y=0 Z=0
    g8: Circle CenterX=3e-16 CenterY=0 CenterZ=0 NormalX=0 NormalY=0 NormalZ=1 AngleXU=0 Radius=2.1
    g9: LineSegment StartX=-4.76483 StartY=8.08721 StartZ=0 EndX=-3.55 EndY=8.08721 EndZ=0
    g10: LineSegment StartX=8.24722 StartY=4.75 StartZ=0 EndX=8.24722 EndY=3.55 EndZ=0
    g11: LineSegment StartX=-8.2 StartY=-4.73729 StartZ=0 EndX=-8.2 EndY=-3.55 EndZ=0
    g12: LineSegment StartX=5.5 StartY=4.75 StartZ=0 EndX=8.24722 EndY=4.75 EndZ=0
    g13: LineSegment StartX=4.75 StartY=5.50457 StartZ=0 EndX=2.65 EndY=3.4 EndZ=0
    g14: LineSegment StartX=4.75 StartY=5.50457 StartZ=0 EndX=4.75 EndY=8.08721 EndZ=0
    g15: LineSegment StartX=3.4 StartY=2.65 StartZ=0 EndX=5.5 EndY=4.75 EndZ=0
    g16: LineSegment StartX=-4.76483 StartY=5.50457 StartZ=0 EndX=-2.66166 EndY=3.4 EndZ=0
    g17: LineSegment StartX=-5.5 StartY=4.70904 StartZ=0 EndX=-3.4 EndY=2.61487 EndZ=0
    g18: LineSegment StartX=-4.76483 StartY=5.50457 StartZ=0 EndX=-4.76483 EndY=8.08721 EndZ=0
    g19: LineSegment StartX=-5.5 StartY=4.70904 StartZ=0 EndX=-8.2 EndY=4.70904 EndZ=0
    g20: LineSegment StartX=-10 StartY=3.125 StartZ=0 EndX=-10 EndY=10 EndZ=0
    g21: LineSegment StartX=-8.2 StartY=3.55 StartZ=0 EndX=-8.2 EndY=4.70904 EndZ=0
    g22: LineSegment StartX=3.55 StartY=8.08721 StartZ=0 EndX=4.75 EndY=8.08721 EndZ=0
    g23: LineSegment StartX=3.125 StartY=10 StartZ=0 EndX=10 EndY=10 EndZ=0
    g24: LineSegment StartX=-5.5 StartY=-4.73729 StartZ=0 EndX=-8.2 EndY=-4.73729 EndZ=0
    g25: LineSegment StartX=-4.75 StartY=-5.5 StartZ=0 EndX=-2.65 EndY=-3.4 EndZ=0
    g26: LineSegment StartX=-4.75 StartY=-5.5 StartZ=0 EndX=-4.75 EndY=-8.2 EndZ=0
    g27: LineSegment StartX=4.73747 StartY=-5.5 StartZ=0 EndX=4.73747 EndY=-8.2 EndZ=0
    g28: LineSegment StartX=5.5 StartY=-4.7671 StartZ=0 EndX=8.24722 EndY=-4.7671 EndZ=0
    g29: LineSegment StartX=-3.125 StartY=-10 StartZ=0 EndX=-10 EndY=-10 EndZ=0
    g30: LineSegment StartX=-3.55 StartY=-8.2 StartZ=0 EndX=-4.75 EndY=-8.2 EndZ=0
    g31: LineSegment StartX=4.73747 StartY=-8.2 StartZ=0 EndX=3.55 EndY=-8.2 EndZ=0
    g32: LineSegment StartX=10 StartY=-3.125 StartZ=0 EndX=10 EndY=-10 EndZ=0
    g33: LineSegment StartX=8.24722 StartY=-3.55 StartZ=0 EndX=8.24722 EndY=-4.7671 EndZ=0
    g34: LineSegment StartX=-2.66166 StartY=3.4 StartZ=0 EndX=2.65 EndY=3.4 EndZ=0
    g35: LineSegment StartX=-3.4 StartY=-2.63136 StartZ=0 EndX=-5.5 EndY=-4.73729 EndZ=0
    g36: LineSegment StartX=3.4 StartY=-2.6657 StartZ=0 EndX=5.5 EndY=-4.7671 EndZ=0
    g37: LineSegment StartX=2.63162 StartY=-3.4 StartZ=0 EndX=4.73747 EndY=-5.5 EndZ=0
    g38: LineSegment StartX=-3.55 StartY=-8.2 StartZ=0 EndX=-3.125 EndY=-10 EndZ=0
    g39: LineSegment StartX=3.55 StartY=-8.2 StartZ=0 EndX=3.125 EndY=-10 EndZ=0
    g40: LineSegment StartX=-3.125 StartY=10 StartZ=0 EndX=-3.55 EndY=8.08721 EndZ=0
    g41: LineSegment StartX=3.125 StartY=10 StartZ=0 EndX=3.55 EndY=8.08721 EndZ=0
    g42: LineSegment StartX=8.24722 StartY=3.55 StartZ=0 EndX=10 EndY=3.125 EndZ=0
    g43: LineSegment StartX=10 StartY=-3.125 StartZ=0 EndX=8.24722 EndY=-3.55 EndZ=0
    g44: LineSegment StartX=-10 StartY=-3.125 StartZ=0 EndX=-8.2 EndY=-3.55 EndZ=0
    g45: LineSegment StartX=-10 StartY=3.125 StartZ=0 EndX=-8.2 EndY=3.55 EndZ=0
  constraints (61):
    c: Horizontal(g1)
    c: Vertical(g0)
    c: Vertical(g2)
    c: Coincident(g23,g4)
    c: Coincident(g32,g5)
    c: Coincident(g29,g6)
    c: Coincident(g20,g3)
    c: Horizontal(g3)
    c: Horizontal(g5)
    c: Vertical(g4)
    c: Vertical(g6)
    c: PointOnObject(g7,g-1)
    c: DistanceX(g3,g7) = 10
    c: DistanceX(g-1,g23) = 10
    c: DistanceY(g7,g3) = 10
    c: DistanceX(g3,g-1) = 10
    c: DistanceY(g32,g7) = 10
    c: Coincident(g8,g7)
    c: Radius(g8) = 2.1
    c: Horizontal(g9)
    c: Vertical(g10)
    c: Vertical(g11)
    c: Coincident(g12,g15)
    c: Horizontal(g12)
    c: Coincident(g14,g13)
    c: Vertical(g14)
    c: Coincident(g15,g0)
    c: Coincident(g13,g34)
    c: Coincident(g14,g22)
    c: Coincident(g18,g16)
    c: Vertical(g18)
    c: Coincident(g19,g17)
    c: Horizontal(g19)
    c: Coincident(g9,g18)
    c: Coincident(g21,g19)
    c: Coincident(g24,g35)
    c: Horizontal(g24)
    c: Coincident(g26,g25)
    c: Vertical(g26)
    c: Coincident(g27,g37)
    c: Vertical(g27)
    c: Coincident(g28,g36)
    c: Horizontal(g28)
    c: Coincident(g11,g24)
    c: Coincident(g26,g30)
    c: Coincident(g31,g27)
    c: Coincident(g12,g10)
    c: Coincident(g28,g33)
    c: Coincident(g25,g1)
    c: Coincident(g35,g2)
    c: Coincident(g17,g2)
    c: Coincident(g16,g34)
    c: Coincident(g1,g37)
    c: Coincident(g0,g36)
    c: Coincident(g39,g5)
    c: Coincident(g40,g3)
    c: Coincident(g42,g4)
    c: Coincident(g44,g6)
    c: Coincident(g21,g45)
    c: Coincident(g33,g43)
    c: Coincident(g10,g42)
FEATURE [PartDesign::Pad] Pad009
  Direction = (0,0,1)
  Length = 300
  Length2 = 10
  Profile = -> Sketch009
  Type = 0
FEATURE [PartDesign::Fillet] Fillet099
  Base = -> Pad009 [Edge53]
  BaseFeature = -> Pad009
  Radius = 1
  SupportTransform = false
FEATURE [PartDesign::Fillet] Fillet100
  Base = -> Fillet099 [Edge114]
  BaseFeature = -> Fillet099
  Radius = 1
  SupportTransform = false
FEATURE [PartDesign::Fillet] Fillet101
  Base = -> Fillet100 [Edge137,Edge95]
  BaseFeature = -> Fillet100
  Radius = 0.5
  SupportTransform = false
FEATURE [PartDesign::Fillet] Fillet102
  Base = -> Fillet101 [Edge103]
  BaseFeature = -> Fillet101
  Radius = 0.5
  SupportTransform = false
FEATURE [PartDesign::Fillet] Fillet103
  Base = -> Fillet102 [Edge96]
  BaseFeature = -> Fillet102
  Radius = 0.5
  SupportTransform = false
FEATURE [PartDesign::Fillet] Fillet104
  Base = -> Fillet103 [Edge77]
  BaseFeature = -> Fillet103
  Radius = 0.5
  SupportTransform = false
FEATURE [PartDesign::Fillet] Fillet105
  Base = -> Fillet104 [Edge102]
  BaseFeature = -> Fillet104
  Radius = 0.5
  SupportTransform = false
FEATURE [PartDesign::Fillet] Fillet106
  Base = -> Fillet105 [Edge85]
  BaseFeature = -> Fillet105
  Radius = 0.5
  SupportTransform = false
FEATURE [PartDesign::Fillet] Fillet107
  Base = -> Fillet106 [Edge78]
  BaseFeature = -> Fillet106
  Radius = 0.5
  SupportTransform = false
FEATURE [PartDesign::Fillet] Fillet108
  Base = -> Fillet107 [Edge107]
  BaseFeature = -> Fillet107
  Radius = 0.5
  SupportTransform = false
FEATURE [PartDesign::Fillet] Fillet109
  Base = -> Fillet108 [Edge74]
  BaseFeature = -> Fillet108
  Radius = 0.5
  SupportTransform = false
FEATURE [PartDesign::Body] Body009
  Group = -> [Sketch009,Pad009,Fillet099,Fillet100,Fillet101,Fillet102,Fillet103,Fillet104,Fillet105,Fillet106,Fillet107,Fillet108,Fillet109]
  Origin = -> Origin019
  Placement = pos=(0,0,0) rot=(0,1,0;1.5708rad)
  Tip = -> Fillet109
FEATURE [App::Part] Part009  label="2020-300-010"
  Group = -> [Body009]
  Origin = -> Origin018
  Placement = pos=(20,10,180) rot=(0,0,1;0rad)
FEATURE [Sketcher::SketchObject] Sketch010
  FullyConstrained = false
  MapMode = 5
  Support = -> [XY_Plane021]
  sketch-geometry (46):
    g0: LineSegment StartX=3.4 StartY=2.65 StartZ=0 EndX=3.4 EndY=-2.6657 EndZ=0
    g1: LineSegment StartX=2.63162 StartY=-3.4 StartZ=0 EndX=-2.65 EndY=-3.4 EndZ=0
    g2: LineSegment StartX=-3.4 StartY=-2.63136 StartZ=0 EndX=-3.4 EndY=2.61487 EndZ=0
    g3: LineSegment StartX=-10 StartY=10 StartZ=0 EndX=-3.125 EndY=10 EndZ=0
    g4: LineSegment StartX=10 StartY=10 StartZ=0 EndX=10 EndY=3.125 EndZ=0
    g5: LineSegment StartX=10 StartY=-10 StartZ=0 EndX=3.125 EndY=-10 EndZ=0
    g6: LineSegment StartX=-10 StartY=-10 StartZ=0 EndX=-10 EndY=-3.125 EndZ=0
    g7: GeomPoint X=3e-16 Y=0 Z=0
    g8: Circle CenterX=3e-16 CenterY=0 CenterZ=0 NormalX=0 NormalY=0 NormalZ=1 AngleXU=0 Radius=2.1
    g9: LineSegment StartX=-4.76483 StartY=8.08721 StartZ=0 EndX=-3.55 EndY=8.08721 EndZ=0
    g10: LineSegment StartX=8.24722 StartY=4.75 StartZ=0 EndX=8.24722 EndY=3.55 EndZ=0
    g11: LineSegment StartX=-8.2 StartY=-4.73729 StartZ=0 EndX=-8.2 EndY=-3.55 EndZ=0
    g12: LineSegment StartX=5.5 StartY=4.75 StartZ=0 EndX=8.24722 EndY=4.75 EndZ=0
    g13: LineSegment StartX=4.75 StartY=5.50457 StartZ=0 EndX=2.65 EndY=3.4 EndZ=0
    g14: LineSegment StartX=4.75 StartY=5.50457 StartZ=0 EndX=4.75 EndY=8.08721 EndZ=0
    g15: LineSegment StartX=3.4 StartY=2.65 StartZ=0 EndX=5.5 EndY=4.75 EndZ=0
    g16: LineSegment StartX=-4.76483 StartY=5.50457 StartZ=0 EndX=-2.66166 EndY=3.4 EndZ=0
    g17: LineSegment StartX=-5.5 StartY=4.70904 StartZ=0 EndX=-3.4 EndY=2.61487 EndZ=0
    g18: LineSegment StartX=-4.76483 StartY=5.50457 StartZ=0 EndX=-4.76483 EndY=8.08721 EndZ=0
    g19: LineSegment StartX=-5.5 StartY=4.70904 StartZ=0 EndX=-8.2 EndY=4.70904 EndZ=0
    g20: LineSegment StartX=-10 StartY=3.125 StartZ=0 EndX=-10 EndY=10 EndZ=0
    g21: LineSegment StartX=-8.2 StartY=3.55 StartZ=0 EndX=-8.2 EndY=4.70904 EndZ=0
    g22: LineSegment StartX=3.55 StartY=8.08721 StartZ=0 EndX=4.75 EndY=8.08721 EndZ=0
    g23: LineSegment StartX=3.125 StartY=10 StartZ=0 EndX=10 EndY=10 EndZ=0
    g24: LineSegment StartX=-5.5 StartY=-4.73729 StartZ=0 EndX=-8.2 EndY=-4.73729 EndZ=0
    g25: LineSegment StartX=-4.75 StartY=-5.5 StartZ=0 EndX=-2.65 EndY=-3.4 EndZ=0
    g26: LineSegment StartX=-4.75 StartY=-5.5 StartZ=0 EndX=-4.75 EndY=-8.2 EndZ=0
    g27: LineSegment StartX=4.73747 StartY=-5.5 StartZ=0 EndX=4.73747 EndY=-8.2 EndZ=0
    g28: LineSegment StartX=5.5 StartY=-4.7671 StartZ=0 EndX=8.24722 EndY=-4.7671 EndZ=0
    g29: LineSegment StartX=-3.125 StartY=-10 StartZ=0 EndX=-10 EndY=-10 EndZ=0
    g30: LineSegment StartX=-3.55 StartY=-8.2 StartZ=0 EndX=-4.75 EndY=-8.2 EndZ=0
    g31: LineSegment StartX=4.73747 StartY=-8.2 StartZ=0 EndX=3.55 EndY=-8.2 EndZ=0
    g32: LineSegment StartX=10 StartY=-3.125 StartZ=0 EndX=10 EndY=-10 EndZ=0
    g33: LineSegment StartX=8.24722 StartY=-3.55 StartZ=0 EndX=8.24722 EndY=-4.7671 EndZ=0
    g34: LineSegment StartX=-2.66166 StartY=3.4 StartZ=0 EndX=2.65 EndY=3.4 EndZ=0
    g35: LineSegment StartX=-3.4 StartY=-2.63136 StartZ=0 EndX=-5.5 EndY=-4.73729 EndZ=0
    g36: LineSegment StartX=3.4 StartY=-2.6657 StartZ=0 EndX=5.5 EndY=-4.7671 EndZ=0
    g37: LineSegment StartX=2.63162 StartY=-3.4 StartZ=0 EndX=4.73747 EndY=-5.5 EndZ=0
    g38: LineSegment StartX=-3.55 StartY=-8.2 StartZ=0 EndX=-3.125 EndY=-10 EndZ=0
    g39: LineSegment StartX=3.55 StartY=-8.2 StartZ=0 EndX=3.125 EndY=-10 EndZ=0
    g40: LineSegment StartX=-3.125 StartY=10 StartZ=0 EndX=-3.55 EndY=8.08721 EndZ=0
    g41: LineSegment StartX=3.125 StartY=10 StartZ=0 EndX=3.55 EndY=8.08721 EndZ=0
    g42: LineSegment StartX=8.24722 StartY=3.55 StartZ=0 EndX=10 EndY=3.125 EndZ=0
    g43: LineSegment StartX=10 StartY=-3.125 StartZ=0 EndX=8.24722 EndY=-3.55 EndZ=0
    g44: LineSegment StartX=-10 StartY=-3.125 StartZ=0 EndX=-8.2 EndY=-3.55 EndZ=0
    g45: LineSegment StartX=-10 StartY=3.125 StartZ=0 EndX=-8.2 EndY=3.55 EndZ=0
  constraints (61):
    c: Horizontal(g1)
    c: Vertical(g0)
    c: Vertical(g2)
    c: Coincident(g23,g4)
    c: Coincident(g32,g5)
    c: Coincident(g29,g6)
    c: Coincident(g20,g3)
    c: Horizontal(g3)
    c: Horizontal(g5)
    c: Vertical(g4)
    c: Vertical(g6)
    c: PointOnObject(g7,g-1)
    c: DistanceX(g3,g7) = 10
    c: DistanceX(g-1,g23) = 10
    c: DistanceY(g7,g3) = 10
    c: DistanceX(g3,g-1) = 10
    c: DistanceY(g32,g7) = 10
    c: Coincident(g8,g7)
    c: Radius(g8) = 2.1
    c: Horizontal(g9)
    c: Vertical(g10)
    c: Vertical(g11)
    c: Coincident(g12,g15)
    c: Horizontal(g12)
    c: Coincident(g14,g13)
    c: Vertical(g14)
    c: Coincident(g15,g0)
    c: Coincident(g13,g34)
    c: Coincident(g14,g22)
    c: Coincident(g18,g16)
    c: Vertical(g18)
    c: Coincident(g19,g17)
    c: Horizontal(g19)
    c: Coincident(g9,g18)
    c: Coincident(g21,g19)
    c: Coincident(g24,g35)
    c: Horizontal(g24)
    c: Coincident(g26,g25)
    c: Vertical(g26)
    c: Coincident(g27,g37)
    c: Vertical(g27)
    c: Coincident(g28,g36)
    c: Horizontal(g28)
    c: Coincident(g11,g24)
    c: Coincident(g26,g30)
    c: Coincident(g31,g27)
    c: Coincident(g12,g10)
    c: Coincident(g28,g33)
    c: Coincident(g25,g1)
    c: Coincident(g35,g2)
    c: Coincident(g17,g2)
    c: Coincident(g16,g34)
    c: Coincident(g1,g37)
    c: Coincident(g0,g36)
    c: Coincident(g39,g5)
    c: Coincident(g40,g3)
    c: Coincident(g42,g4)
    c: Coincident(g44,g6)
    c: Coincident(g21,g45)
    c: Coincident(g33,g43)
    c: Coincident(g10,g42)
FEATURE [PartDesign::Pad] Pad010
  Direction = (0,0,1)
  Length = 300
  Length2 = 10
  Profile = -> Sketch010
  Type = 0
FEATURE [PartDesign::Fillet] Fillet110
  Base = -> Pad010 [Edge53]
  BaseFeature = -> Pad010
  Radius = 1
  SupportTransform = false
FEATURE [PartDesign::Fillet] Fillet111
  Base = -> Fillet110 [Edge114]
  BaseFeature = -> Fillet110
  Radius = 1
  SupportTransform = false
FEATURE [PartDesign::Fillet] Fillet112
  Base = -> Fillet111 [Edge137,Edge95]
  BaseFeature = -> Fillet111
  Radius = 0.5
  SupportTransform = false
FEATURE [PartDesign::Fillet] Fillet113
  Base = -> Fillet112 [Edge103]
  BaseFeature = -> Fillet112
  Radius = 0.5
  SupportTransform = false
FEATURE [PartDesign::Fillet] Fillet114
  Base = -> Fillet113 [Edge96]
  BaseFeature = -> Fillet113
  Radius = 0.5
  SupportTransform = false
FEATURE [PartDesign::Fillet] Fillet115
  Base = -> Fillet114 [Edge77]
  BaseFeature = -> Fillet114
  Radius = 0.5
  SupportTransform = false
FEATURE [PartDesign::Fillet] Fillet116
  Base = -> Fillet115 [Edge102]
  BaseFeature = -> Fillet115
  Radius = 0.5
  SupportTransform = false
FEATURE [PartDesign::Fillet] Fillet117
  Base = -> Fillet116 [Edge85]
  BaseFeature = -> Fillet116
  Radius = 0.5
  SupportTransform = false
FEATURE [PartDesign::Fillet] Fillet118
  Base = -> Fillet117 [Edge78]
  BaseFeature = -> Fillet117
  Radius = 0.5
  SupportTransform = false
FEATURE [PartDesign::Fillet] Fillet119
  Base = -> Fillet118 [Edge107]
  BaseFeature = -> Fillet118
  Radius = 0.5
  SupportTransform = false
FEATURE [PartDesign::Fillet] Fillet120
  Base = -> Fillet119 [Edge74]
  BaseFeature = -> Fillet119
  Radius = 0.5
  SupportTransform = false
FEATURE [PartDesign::Body] Body010
  Group = -> [Sketch010,Pad010,Fillet110,Fillet111,Fillet112,Fillet113,Fillet114,Fillet115,Fillet116,Fillet117,Fillet118,Fillet119,Fillet120]
  Origin = -> Origin021
  Placement = pos=(0,0,0) rot=(0,1,0;1.5708rad)
  Tip = -> Fillet120
FEATURE [App::Part] Part010  label="2020-300-011"
  Group = -> [Body010]
  Origin = -> Origin020
  Placement = pos=(10,20,179) rot=(0,0,1;1.5708rad)
FEATURE [Sketcher::SketchObject] Sketch011
  FullyConstrained = false
  MapMode = 5
  Support = -> [XY_Plane023]
  sketch-geometry (46):
    g0: LineSegment StartX=3.4 StartY=2.65 StartZ=0 EndX=3.4 EndY=-2.6657 EndZ=0
    g1: LineSegment StartX=2.63162 StartY=-3.4 StartZ=0 EndX=-2.65 EndY=-3.4 EndZ=0
    g2: LineSegment StartX=-3.4 StartY=-2.63136 StartZ=0 EndX=-3.4 EndY=2.61487 EndZ=0
    g3: LineSegment StartX=-10 StartY=10 StartZ=0 EndX=-3.125 EndY=10 EndZ=0
    g4: LineSegment StartX=10 StartY=10 StartZ=0 EndX=10 EndY=3.125 EndZ=0
    g5: LineSegment StartX=10 StartY=-10 StartZ=0 EndX=3.125 EndY=-10 EndZ=0
    g6: LineSegment StartX=-10 StartY=-10 StartZ=0 EndX=-10 EndY=-3.125 EndZ=0
    g7: GeomPoint X=3e-16 Y=0 Z=0
    g8: Circle CenterX=3e-16 CenterY=0 CenterZ=0 NormalX=0 NormalY=0 NormalZ=1 AngleXU=0 Radius=2.1
    g9: LineSegment StartX=-4.76483 StartY=8.08721 StartZ=0 EndX=-3.55 EndY=8.08721 EndZ=0
    g10: LineSegment StartX=8.24722 StartY=4.75 StartZ=0 EndX=8.24722 EndY=3.55 EndZ=0
    g11: LineSegment StartX=-8.2 StartY=-4.73729 StartZ=0 EndX=-8.2 EndY=-3.55 EndZ=0
    g12: LineSegment StartX=5.5 StartY=4.75 StartZ=0 EndX=8.24722 EndY=4.75 EndZ=0
    g13: LineSegment StartX=4.75 StartY=5.50457 StartZ=0 EndX=2.65 EndY=3.4 EndZ=0
    g14: LineSegment StartX=4.75 StartY=5.50457 StartZ=0 EndX=4.75 EndY=8.08721 EndZ=0
    g15: LineSegment StartX=3.4 StartY=2.65 StartZ=0 EndX=5.5 EndY=4.75 EndZ=0
    g16: LineSegment StartX=-4.76483 StartY=5.50457 StartZ=0 EndX=-2.66166 EndY=3.4 EndZ=0
    g17: LineSegment StartX=-5.5 StartY=4.70904 StartZ=0 EndX=-3.4 EndY=2.61487 EndZ=0
    g18: LineSegment StartX=-4.76483 StartY=5.50457 StartZ=0 EndX=-4.76483 EndY=8.08721 EndZ=0
    g19: LineSegment StartX=-5.5 StartY=4.70904 StartZ=0 EndX=-8.2 EndY=4.70904 EndZ=0
    g20: LineSegment StartX=-10 StartY=3.125 StartZ=0 EndX=-10 EndY=10 EndZ=0
    g21: LineSegment StartX=-8.2 StartY=3.55 StartZ=0 EndX=-8.2 EndY=4.70904 EndZ=0
    g22: LineSegment StartX=3.55 StartY=8.08721 StartZ=0 EndX=4.75 EndY=8.08721 EndZ=0
    g23: LineSegment StartX=3.125 StartY=10 StartZ=0 EndX=10 EndY=10 EndZ=0
    g24: LineSegment StartX=-5.5 StartY=-4.73729 StartZ=0 EndX=-8.2 EndY=-4.73729 EndZ=0
    g25: LineSegment StartX=-4.75 StartY=-5.5 StartZ=0 EndX=-2.65 EndY=-3.4 EndZ=0
    g26: LineSegment StartX=-4.75 StartY=-5.5 StartZ=0 EndX=-4.75 EndY=-8.2 EndZ=0
    g27: LineSegment StartX=4.73747 StartY=-5.5 StartZ=0 EndX=4.73747 EndY=-8.2 EndZ=0
    g28: LineSegment StartX=5.5 StartY=-4.7671 StartZ=0 EndX=8.24722 EndY=-4.7671 EndZ=0
    g29: LineSegment StartX=-3.125 StartY=-10 StartZ=0 EndX=-10 EndY=-10 EndZ=0
    g30: LineSegment StartX=-3.55 StartY=-8.2 StartZ=0 EndX=-4.75 EndY=-8.2 EndZ=0
    g31: LineSegment StartX=4.73747 StartY=-8.2 StartZ=0 EndX=3.55 EndY=-8.2 EndZ=0
    g32: LineSegment StartX=10 StartY=-3.125 StartZ=0 EndX=10 EndY=-10 EndZ=0
    g33: LineSegment StartX=8.24722 StartY=-3.55 StartZ=0 EndX=8.24722 EndY=-4.7671 EndZ=0
    g34: LineSegment StartX=-2.66166 StartY=3.4 StartZ=0 EndX=2.65 EndY=3.4 EndZ=0
    g35: LineSegment StartX=-3.4 StartY=-2.63136 StartZ=0 EndX=-5.5 EndY=-4.73729 EndZ=0
    g36: LineSegment StartX=3.4 StartY=-2.6657 StartZ=0 EndX=5.5 EndY=-4.7671 EndZ=0
    g37: LineSegment StartX=2.63162 StartY=-3.4 StartZ=0 EndX=4.73747 EndY=-5.5 EndZ=0
    g38: LineSegment StartX=-3.55 StartY=-8.2 StartZ=0 EndX=-3.125 EndY=-10 EndZ=0
    g39: LineSegment StartX=3.55 StartY=-8.2 StartZ=0 EndX=3.125 EndY=-10 EndZ=0
    g40: LineSegment StartX=-3.125 StartY=10 StartZ=0 EndX=-3.55 EndY=8.08721 EndZ=0
    g41: LineSegment StartX=3.125 StartY=10 StartZ=0 EndX=3.55 EndY=8.08721 EndZ=0
    g42: LineSegment StartX=8.24722 StartY=3.55 StartZ=0 EndX=10 EndY=3.125 EndZ=0
    g43: LineSegment StartX=10 StartY=-3.125 StartZ=0 EndX=8.24722 EndY=-3.55 EndZ=0
    g44: LineSegment StartX=-10 StartY=-3.125 StartZ=0 EndX=-8.2 EndY=-3.55 EndZ=0
    g45: LineSegment StartX=-10 StartY=3.125 StartZ=0 EndX=-8.2 EndY=3.55 EndZ=0
  constraints (61):
    c: Horizontal(g1)
    c: Vertical(g0)
    c: Vertical(g2)
    c: Coincident(g23,g4)
    c: Coincident(g32,g5)
    c: Coincident(g29,g6)
    c: Coincident(g20,g3)
    c: Horizontal(g3)
    c: Horizontal(g5)
    c: Vertical(g4)
    c: Vertical(g6)
    c: PointOnObject(g7,g-1)
    c: DistanceX(g3,g7) = 10
    c: DistanceX(g-1,g23) = 10
    c: DistanceY(g7,g3) = 10
    c: DistanceX(g3,g-1) = 10
    c: DistanceY(g32,g7) = 10
    c: Coincident(g8,g7)
    c: Radius(g8) = 2.1
    c: Horizontal(g9)
    c: Vertical(g10)
    c: Vertical(g11)
    c: Coincident(g12,g15)
    c: Horizontal(g12)
    c: Coincident(g14,g13)
    c: Vertical(g14)
    c: Coincident(g15,g0)
    c: Coincident(g13,g34)
    c: Coincident(g14,g22)
    c: Coincident(g18,g16)
    c: Vertical(g18)
    c: Coincident(g19,g17)
    c: Horizontal(g19)
    c: Coincident(g9,g18)
    c: Coincident(g21,g19)
    c: Coincident(g24,g35)
    c: Horizontal(g24)
    c: Coincident(g26,g25)
    c: Vertical(g26)
    c: Coincident(g27,g37)
    c: Vertical(g27)
    c: Coincident(g28,g36)
    c: Horizontal(g28)
    c: Coincident(g11,g24)
    c: Coincident(g26,g30)
    c: Coincident(g31,g27)
    c: Coincident(g12,g10)
    c: Coincident(g28,g33)
    c: Coincident(g25,g1)
    c: Coincident(g35,g2)
    c: Coincident(g17,g2)
    c: Coincident(g16,g34)
    c: Coincident(g1,g37)
    c: Coincident(g0,g36)
    c: Coincident(g39,g5)
    c: Coincident(g40,g3)
    c: Coincident(g42,g4)
    c: Coincident(g44,g6)
    c: Coincident(g21,g45)
    c: Coincident(g33,g43)
    c: Coincident(g10,g42)
FEATURE [PartDesign::Pad] Pad011
  Direction = (0,0,1)
  Length = 300
  Length2 = 10
  Profile = -> Sketch011
  Type = 0
FEATURE [PartDesign::Fillet] Fillet121
  Base = -> Pad011 [Edge53]
  BaseFeature = -> Pad011
  Radius = 1
  SupportTransform = false
FEATURE [PartDesign::Fillet] Fillet122
  Base = -> Fillet121 [Edge114]
  BaseFeature = -> Fillet121
  Radius = 1
  SupportTransform = false
FEATURE [PartDesign::Fillet] Fillet123
  Base = -> Fillet122 [Edge137,Edge95]
  BaseFeature = -> Fillet122
  Radius = 0.5
  SupportTransform = false
FEATURE [PartDesign::Fillet] Fillet124
  Base = -> Fillet123 [Edge103]
  BaseFeature = -> Fillet123
  Radius = 0.5
  SupportTransform = false
FEATURE [PartDesign::Fillet] Fillet125
  Base = -> Fillet124 [Edge96]
  BaseFeature = -> Fillet124
  Radius = 0.5
  SupportTransform = false
FEATURE [PartDesign::Fillet] Fillet126
  Base = -> Fillet125 [Edge77]
  BaseFeature = -> Fillet125
  Radius = 0.5
  SupportTransform = false
FEATURE [PartDesign::Fillet] Fillet127
  Base = -> Fillet126 [Edge102]
  BaseFeature = -> Fillet126
  Radius = 0.5
  SupportTransform = false
FEATURE [PartDesign::Fillet] Fillet128
  Base = -> Fillet127 [Edge85]
  BaseFeature = -> Fillet127
  Radius = 0.5
  SupportTransform = false
FEATURE [PartDesign::Fillet] Fillet129
  Base = -> Fillet128 [Edge78]
  BaseFeature = -> Fillet128
  Radius = 0.5
  SupportTransform = false
FEATURE [PartDesign::Fillet] Fillet130
  Base = -> Fillet129 [Edge107]
  BaseFeature = -> Fillet129
  Radius = 0.5
  SupportTransform = false
FEATURE [PartDesign::Fillet] Fillet131
  Base = -> Fillet130 [Edge74]
  BaseFeature = -> Fillet130
  Radius = 0.5
  SupportTransform = false
FEATURE [PartDesign::Body] Body011
  Group = -> [Sketch011,Pad011,Fillet121,Fillet122,Fillet123,Fillet124,Fillet125,Fillet126,Fillet127,Fillet128,Fillet129,Fillet130,Fillet131]
  Origin = -> Origin023
  Placement = pos=(0,0,0) rot=(0,1,0;1.5708rad)
  Tip = -> Fillet131
FEATURE [App::Part] Part011  label="2020-300-012"
  Group = -> [Body011]
  Origin = -> Origin022
  Placement = pos=(330,20,180) rot=(0,0,1;1.5708rad)
FEATURE [Sketcher::SketchObject] Sketch012
  FullyConstrained = false
  MapMode = 5
  Support = -> [XY_Plane025]
  sketch-geometry (46):
    g0: LineSegment StartX=3.4 StartY=2.65 StartZ=0 EndX=3.4 EndY=-2.6657 EndZ=0
    g1: LineSegment StartX=2.63162 StartY=-3.4 StartZ=0 EndX=-2.65 EndY=-3.4 EndZ=0
    g2: LineSegment StartX=-3.4 StartY=-2.63136 StartZ=0 EndX=-3.4 EndY=2.61487 EndZ=0
    g3: LineSegment StartX=-10 StartY=10 StartZ=0 EndX=-3.125 EndY=10 EndZ=0
    g4: LineSegment StartX=10 StartY=10 StartZ=0 EndX=10 EndY=3.125 EndZ=0
    g5: LineSegment StartX=10 StartY=-10 StartZ=0 EndX=3.125 EndY=-10 EndZ=0
    g6: LineSegment StartX=-10 StartY=-10 StartZ=0 EndX=-10 EndY=-3.125 EndZ=0
    g7: GeomPoint X=3e-16 Y=0 Z=0
    g8: Circle CenterX=3e-16 CenterY=0 CenterZ=0 NormalX=0 NormalY=0 NormalZ=1 AngleXU=0 Radius=2.1
    g9: LineSegment StartX=-4.76483 StartY=8.08721 StartZ=0 EndX=-3.55 EndY=8.08721 EndZ=0
    g10: LineSegment StartX=8.24722 StartY=4.75 StartZ=0 EndX=8.24722 EndY=3.55 EndZ=0
    g11: LineSegment StartX=-8.2 StartY=-4.73729 StartZ=0 EndX=-8.2 EndY=-3.55 EndZ=0
    g12: LineSegment StartX=5.5 StartY=4.75 StartZ=0 EndX=8.24722 EndY=4.75 EndZ=0
    g13: LineSegment StartX=4.75 StartY=5.50457 StartZ=0 EndX=2.65 EndY=3.4 EndZ=0
    g14: LineSegment StartX=4.75 StartY=5.50457 StartZ=0 EndX=4.75 EndY=8.08721 EndZ=0
    g15: LineSegment StartX=3.4 StartY=2.65 StartZ=0 EndX=5.5 EndY=4.75 EndZ=0
    g16: LineSegment StartX=-4.76483 StartY=5.50457 StartZ=0 EndX=-2.66166 EndY=3.4 EndZ=0
    g17: LineSegment StartX=-5.5 StartY=4.70904 StartZ=0 EndX=-3.4 EndY=2.61487 EndZ=0
    g18: LineSegment StartX=-4.76483 StartY=5.50457 StartZ=0 EndX=-4.76483 EndY=8.08721 EndZ=0
    g19: LineSegment StartX=-5.5 StartY=4.70904 StartZ=0 EndX=-8.2 EndY=4.70904 EndZ=0
    g20: LineSegment StartX=-10 StartY=3.125 StartZ=0 EndX=-10 EndY=10 EndZ=0
    g21: LineSegment StartX=-8.2 StartY=3.55 StartZ=0 EndX=-8.2 EndY=4.70904 EndZ=0
    g22: LineSegment StartX=3.55 StartY=8.08721 StartZ=0 EndX=4.75 EndY=8.08721 EndZ=0
    g23: LineSegment StartX=3.125 StartY=10 StartZ=0 EndX=10 EndY=10 EndZ=0
    g24: LineSegment StartX=-5.5 StartY=-4.73729 StartZ=0 EndX=-8.2 EndY=-4.73729 EndZ=0
    g25: LineSegment StartX=-4.75 StartY=-5.5 StartZ=0 EndX=-2.65 EndY=-3.4 EndZ=0
    g26: LineSegment StartX=-4.75 StartY=-5.5 StartZ=0 EndX=-4.75 EndY=-8.2 EndZ=0
    g27: LineSegment StartX=4.73747 StartY=-5.5 StartZ=0 EndX=4.73747 EndY=-8.2 EndZ=0
    g28: LineSegment StartX=5.5 StartY=-4.7671 StartZ=0 EndX=8.24722 EndY=-4.7671 EndZ=0
    g29: LineSegment StartX=-3.125 StartY=-10 StartZ=0 EndX=-10 EndY=-10 EndZ=0
    g30: LineSegment StartX=-3.55 StartY=-8.2 StartZ=0 EndX=-4.75 EndY=-8.2 EndZ=0
    g31: LineSegment StartX=4.73747 StartY=-8.2 StartZ=0 EndX=3.55 EndY=-8.2 EndZ=0
    g32: LineSegment StartX=10 StartY=-3.125 StartZ=0 EndX=10 EndY=-10 EndZ=0
    g33: LineSegment StartX=8.24722 StartY=-3.55 StartZ=0 EndX=8.24722 EndY=-4.7671 EndZ=0
    g34: LineSegment StartX=-2.66166 StartY=3.4 StartZ=0 EndX=2.65 EndY=3.4 EndZ=0
    g35: LineSegment StartX=-3.4 StartY=-2.63136 StartZ=0 EndX=-5.5 EndY=-4.73729 EndZ=0
    g36: LineSegment StartX=3.4 StartY=-2.6657 StartZ=0 EndX=5.5 EndY=-4.7671 EndZ=0
    g37: LineSegment StartX=2.63162 StartY=-3.4 StartZ=0 EndX=4.73747 EndY=-5.5 EndZ=0
    g38: LineSegment StartX=-3.55 StartY=-8.2 StartZ=0 EndX=-3.125 EndY=-10 EndZ=0
    g39: LineSegment StartX=3.55 StartY=-8.2 StartZ=0 EndX=3.125 EndY=-10 EndZ=0
    g40: LineSegment StartX=-3.125 StartY=10 StartZ=0 EndX=-3.55 EndY=8.08721 EndZ=0
    g41: LineSegment StartX=3.125 StartY=10 StartZ=0 EndX=3.55 EndY=8.08721 EndZ=0
    g42: LineSegment StartX=8.24722 StartY=3.55 StartZ=0 EndX=10 EndY=3.125 EndZ=0
    g43: LineSegment StartX=10 StartY=-3.125 StartZ=0 EndX=8.24722 EndY=-3.55 EndZ=0
    g44: LineSegment StartX=-10 StartY=-3.125 StartZ=0 EndX=-8.2 EndY=-3.55 EndZ=0
    g45: LineSegment StartX=-10 StartY=3.125 StartZ=0 EndX=-8.2 EndY=3.55 EndZ=0
  constraints (61):
    c: Horizontal(g1)
    c: Vertical(g0)
    c: Vertical(g2)
    c: Coincident(g23,g4)
    c: Coincident(g32,g5)
    c: Coincident(g29,g6)
    c: Coincident(g20,g3)
    c: Horizontal(g3)
    c: Horizontal(g5)
    c: Vertical(g4)
    c: Vertical(g6)
    c: PointOnObject(g7,g-1)
    c: DistanceX(g3,g7) = 10
    c: DistanceX(g-1,g23) = 10
    c: DistanceY(g7,g3) = 10
    c: DistanceX(g3,g-1) = 10
    c: DistanceY(g32,g7) = 10
    c: Coincident(g8,g7)
    c: Radius(g8) = 2.1
    c: Horizontal(g9)
    c: Vertical(g10)
    c: Vertical(g11)
    c: Coincident(g12,g15)
    c: Horizontal(g12)
    c: Coincident(g14,g13)
    c: Vertical(g14)
    c: Coincident(g15,g0)
    c: Coincident(g13,g34)
    c: Coincident(g14,g22)
    c: Coincident(g18,g16)
    c: Vertical(g18)
    c: Coincident(g19,g17)
    c: Horizontal(g19)
    c: Coincident(g9,g18)
    c: Coincident(g21,g19)
    c: Coincident(g24,g35)
    c: Horizontal(g24)
    c: Coincident(g26,g25)
    c: Vertical(g26)
    c: Coincident(g27,g37)
    c: Vertical(g27)
    c: Coincident(g28,g36)
    c: Horizontal(g28)
    c: Coincident(g11,g24)
    c: Coincident(g26,g30)
    c: Coincident(g31,g27)
    c: Coincident(g12,g10)
    c: Coincident(g28,g33)
    c: Coincident(g25,g1)
    c: Coincident(g35,g2)
    c: Coincident(g17,g2)
    c: Coincident(g16,g34)
    c: Coincident(g1,g37)
    c: Coincident(g0,g36)
    c: Coincident(g39,g5)
    c: Coincident(g40,g3)
    c: Coincident(g42,g4)
    c: Coincident(g44,g6)
    c: Coincident(g21,g45)
    c: Coincident(g33,g43)
    c: Coincident(g10,g42)
FEATURE [PartDesign::Pad] Pad012
  Direction = (0,0,1)
  Length = 300
  Length2 = 10
  Profile = -> Sketch012
  Type = 0
FEATURE [PartDesign::Fillet] Fillet132
  Base = -> Pad012 [Edge53]
  BaseFeature = -> Pad012
  Radius = 1
  SupportTransform = false
FEATURE [PartDesign::Fillet] Fillet133
  Base = -> Fillet132 [Edge114]
  BaseFeature = -> Fillet132
  Radius = 1
  SupportTransform = false
FEATURE [PartDesign::Fillet] Fillet134
  Base = -> Fillet133 [Edge137,Edge95]
  BaseFeature = -> Fillet133
  Radius = 0.5
  SupportTransform = false
FEATURE [PartDesign::Fillet] Fillet135
  Base = -> Fillet134 [Edge103]
  BaseFeature = -> Fillet134
  Radius = 0.5
  SupportTransform = false
FEATURE [PartDesign::Fillet] Fillet136
  Base = -> Fillet135 [Edge96]
  BaseFeature = -> Fillet135
  Radius = 0.5
  SupportTransform = false
FEATURE [PartDesign::Fillet] Fillet137
  Base = -> Fillet136 [Edge77]
  BaseFeature = -> Fillet136
  Radius = 0.5
  SupportTransform = false
FEATURE [PartDesign::Fillet] Fillet138
  Base = -> Fillet137 [Edge102]
  BaseFeature = -> Fillet137
  Radius = 0.5
  SupportTransform = false
FEATURE [PartDesign::Fillet] Fillet139
  Base = -> Fillet138 [Edge85]
  BaseFeature = -> Fillet138
  Radius = 0.5
  SupportTransform = false
FEATURE [PartDesign::Fillet] Fillet140
  Base = -> Fillet139 [Edge78]
  BaseFeature = -> Fillet139
  Radius = 0.5
  SupportTransform = false
FEATURE [PartDesign::Fillet] Fillet141
  Base = -> Fillet140 [Edge107]
  BaseFeature = -> Fillet140
  Radius = 0.5
  SupportTransform = false
FEATURE [PartDesign::Fillet] Fillet142
  Base = -> Fillet141 [Edge74]
  BaseFeature = -> Fillet141
  Radius = 0.5
  SupportTransform = false
FEATURE [PartDesign::Body] Body012
  Group = -> [Sketch012,Pad012,Fillet132,Fillet133,Fillet134,Fillet135,Fillet136,Fillet137,Fillet138,Fillet139,Fillet140,Fillet141,Fillet142]
  Origin = -> Origin025
  Placement = pos=(0,0,0) rot=(0,1,0;1.5708rad)
  Tip = -> Fillet142
FEATURE [App::Part] Part012  label="2020-300-013"
  Group = -> [Body012]
  Origin = -> Origin024
  Placement = pos=(10,20,80) rot=(0,0,1;1.5708rad)
FEATURE [Sketcher::SketchObject] Sketch013
  FullyConstrained = false
  MapMode = 5
  Support = -> [XY_Plane027]
  sketch-geometry (46):
    g0: LineSegment StartX=3.4 StartY=2.65 StartZ=0 EndX=3.4 EndY=-2.6657 EndZ=0
    g1: LineSegment StartX=2.63162 StartY=-3.4 StartZ=0 EndX=-2.65 EndY=-3.4 EndZ=0
    g2: LineSegment StartX=-3.4 StartY=-2.63136 StartZ=0 EndX=-3.4 EndY=2.61487 EndZ=0
    g3: LineSegment StartX=-10 StartY=10 StartZ=0 EndX=-3.125 EndY=10 EndZ=0
    g4: LineSegment StartX=10 StartY=10 StartZ=0 EndX=10 EndY=3.125 EndZ=0
    g5: LineSegment StartX=10 StartY=-10 StartZ=0 EndX=3.125 EndY=-10 EndZ=0
    g6: LineSegment StartX=-10 StartY=-10 StartZ=0 EndX=-10 EndY=-3.125 EndZ=0
    g7: GeomPoint X=3e-16 Y=0 Z=0
    g8: Circle CenterX=3e-16 CenterY=0 CenterZ=0 NormalX=0 NormalY=0 NormalZ=1 AngleXU=0 Radius=2.1
    g9: LineSegment StartX=-4.76483 StartY=8.08721 StartZ=0 EndX=-3.55 EndY=8.08721 EndZ=0
    g10: LineSegment StartX=8.24722 StartY=4.75 StartZ=0 EndX=8.24722 EndY=3.55 EndZ=0
    g11: LineSegment StartX=-8.2 StartY=-4.73729 StartZ=0 EndX=-8.2 EndY=-3.55 EndZ=0
    g12: LineSegment StartX=5.5 StartY=4.75 StartZ=0 EndX=8.24722 EndY=4.75 EndZ=0
    g13: LineSegment StartX=4.75 StartY=5.50457 StartZ=0 EndX=2.65 EndY=3.4 EndZ=0
    g14: LineSegment StartX=4.75 StartY=5.50457 StartZ=0 EndX=4.75 EndY=8.08721 EndZ=0
    g15: LineSegment StartX=3.4 StartY=2.65 StartZ=0 EndX=5.5 EndY=4.75 EndZ=0
    g16: LineSegment StartX=-4.76483 StartY=5.50457 StartZ=0 EndX=-2.66166 EndY=3.4 EndZ=0
    g17: LineSegment StartX=-5.5 StartY=4.70904 StartZ=0 EndX=-3.4 EndY=2.61487 EndZ=0
    g18: LineSegment StartX=-4.76483 StartY=5.50457 StartZ=0 EndX=-4.76483 EndY=8.08721 EndZ=0
    g19: LineSegment StartX=-5.5 StartY=4.70904 StartZ=0 EndX=-8.2 EndY=4.70904 EndZ=0
    g20: LineSegment StartX=-10 StartY=3.125 StartZ=0 EndX=-10 EndY=10 EndZ=0
    g21: LineSegment StartX=-8.2 StartY=3.55 StartZ=0 EndX=-8.2 EndY=4.70904 EndZ=0
    g22: LineSegment StartX=3.55 StartY=8.08721 StartZ=0 EndX=4.75 EndY=8.08721 EndZ=0
    g23: LineSegment StartX=3.125 StartY=10 StartZ=0 EndX=10 EndY=10 EndZ=0
    g24: LineSegment StartX=-5.5 StartY=-4.73729 StartZ=0 EndX=-8.2 EndY=-4.73729 EndZ=0
    g25: LineSegment StartX=-4.75 StartY=-5.5 StartZ=0 EndX=-2.65 EndY=-3.4 EndZ=0
    g26: LineSegment StartX=-4.75 StartY=-5.5 StartZ=0 EndX=-4.75 EndY=-8.2 EndZ=0
    g27: LineSegment StartX=4.73747 StartY=-5.5 StartZ=0 EndX=4.73747 EndY=-8.2 EndZ=0
    g28: LineSegment StartX=5.5 StartY=-4.7671 StartZ=0 EndX=8.24722 EndY=-4.7671 EndZ=0
    g29: LineSegment StartX=-3.125 StartY=-10 StartZ=0 EndX=-10 EndY=-10 EndZ=0
    g30: LineSegment StartX=-3.55 StartY=-8.2 StartZ=0 EndX=-4.75 EndY=-8.2 EndZ=0
    g31: LineSegment StartX=4.73747 StartY=-8.2 StartZ=0 EndX=3.55 EndY=-8.2 EndZ=0
    g32: LineSegment StartX=10 StartY=-3.125 StartZ=0 EndX=10 EndY=-10 EndZ=0
    g33: LineSegment StartX=8.24722 StartY=-3.55 StartZ=0 EndX=8.24722 EndY=-4.7671 EndZ=0
    g34: LineSegment StartX=-2.66166 StartY=3.4 StartZ=0 EndX=2.65 EndY=3.4 EndZ=0
    g35: LineSegment StartX=-3.4 StartY=-2.63136 StartZ=0 EndX=-5.5 EndY=-4.73729 EndZ=0
    g36: LineSegment StartX=3.4 StartY=-2.6657 StartZ=0 EndX=5.5 EndY=-4.7671 EndZ=0
    g37: LineSegment StartX=2.63162 StartY=-3.4 StartZ=0 EndX=4.73747 EndY=-5.5 EndZ=0
    g38: LineSegment StartX=-3.55 StartY=-8.2 StartZ=0 EndX=-3.125 EndY=-10 EndZ=0
    g39: LineSegment StartX=3.55 StartY=-8.2 StartZ=0 EndX=3.125 EndY=-10 EndZ=0
    g40: LineSegment StartX=-3.125 StartY=10 StartZ=0 EndX=-3.55 EndY=8.08721 EndZ=0
    g41: LineSegment StartX=3.125 StartY=10 StartZ=0 EndX=3.55 EndY=8.08721 EndZ=0
    g42: LineSegment StartX=8.24722 StartY=3.55 StartZ=0 EndX=10 EndY=3.125 EndZ=0
    g43: LineSegment StartX=10 StartY=-3.125 StartZ=0 EndX=8.24722 EndY=-3.55 EndZ=0
    g44: LineSegment StartX=-10 StartY=-3.125 StartZ=0 EndX=-8.2 EndY=-3.55 EndZ=0
    g45: LineSegment StartX=-10 StartY=3.125 StartZ=0 EndX=-8.2 EndY=3.55 EndZ=0
  constraints (61):
    c: Horizontal(g1)
    c: Vertical(g0)
    c: Vertical(g2)
    c: Coincident(g23,g4)
    c: Coincident(g32,g5)
    c: Coincident(g29,g6)
    c: Coincident(g20,g3)
    c: Horizontal(g3)
    c: Horizontal(g5)
    c: Vertical(g4)
    c: Vertical(g6)
    c: PointOnObject(g7,g-1)
    c: DistanceX(g3,g7) = 10
    c: DistanceX(g-1,g23) = 10
    c: DistanceY(g7,g3) = 10
    c: DistanceX(g3,g-1) = 10
    c: DistanceY(g32,g7) = 10
    c: Coincident(g8,g7)
    c: Radius(g8) = 2.1
    c: Horizontal(g9)
    c: Vertical(g10)
    c: Vertical(g11)
    c: Coincident(g12,g15)
    c: Horizontal(g12)
    c: Coincident(g14,g13)
    c: Vertical(g14)
    c: Coincident(g15,g0)
    c: Coincident(g13,g34)
    c: Coincident(g14,g22)
    c: Coincident(g18,g16)
    c: Vertical(g18)
    c: Coincident(g19,g17)
    c: Horizontal(g19)
    c: Coincident(g9,g18)
    c: Coincident(g21,g19)
    c: Coincident(g24,g35)
    c: Horizontal(g24)
    c: Coincident(g26,g25)
    c: Vertical(g26)
    c: Coincident(g27,g37)
    c: Vertical(g27)
    c: Coincident(g28,g36)
    c: Horizontal(g28)
    c: Coincident(g11,g24)
    c: Coincident(g26,g30)
    c: Coincident(g31,g27)
    c: Coincident(g12,g10)
    c: Coincident(g28,g33)
    c: Coincident(g25,g1)
    c: Coincident(g35,g2)
    c: Coincident(g17,g2)
    c: Coincident(g16,g34)
    c: Coincident(g1,g37)
    c: Coincident(g0,g36)
    c: Coincident(g39,g5)
    c: Coincident(g40,g3)
    c: Coincident(g42,g4)
    c: Coincident(g44,g6)
    c: Coincident(g21,g45)
    c: Coincident(g33,g43)
    c: Coincident(g10,g42)
FEATURE [PartDesign::Pad] Pad013
  Direction = (0,0,1)
  Length = 300
  Length2 = 10
  Profile = -> Sketch013
  Type = 0
FEATURE [PartDesign::Fillet] Fillet143
  Base = -> Pad013 [Edge53]
  BaseFeature = -> Pad013
  Radius = 1
  SupportTransform = false
FEATURE [PartDesign::Fillet] Fillet144
  Base = -> Fillet143 [Edge114]
  BaseFeature = -> Fillet143
  Radius = 1
  SupportTransform = false
FEATURE [PartDesign::Fillet] Fillet145
  Base = -> Fillet144 [Edge137,Edge95]
  BaseFeature = -> Fillet144
  Radius = 0.5
  SupportTransform = false
FEATURE [PartDesign::Fillet] Fillet146
  Base = -> Fillet145 [Edge103]
  BaseFeature = -> Fillet145
  Radius = 0.5
  SupportTransform = false
FEATURE [PartDesign::Fillet] Fillet147
  Base = -> Fillet146 [Edge96]
  BaseFeature = -> Fillet146
  Radius = 0.5
  SupportTransform = false
FEATURE [PartDesign::Fillet] Fillet148
  Base = -> Fillet147 [Edge77]
  BaseFeature = -> Fillet147
  Radius = 0.5
  SupportTransform = false
FEATURE [PartDesign::Fillet] Fillet149
  Base = -> Fillet148 [Edge102]
  BaseFeature = -> Fillet148
  Radius = 0.5
  SupportTransform = false
FEATURE [PartDesign::Fillet] Fillet150
  Base = -> Fillet149 [Edge85]
  BaseFeature = -> Fillet149
  Radius = 0.5
  SupportTransform = false
FEATURE [PartDesign::Fillet] Fillet151
  Base = -> Fillet150 [Edge78]
  BaseFeature = -> Fillet150
  Radius = 0.5
  SupportTransform = false
FEATURE [PartDesign::Fillet] Fillet152
  Base = -> Fillet151 [Edge107]
  BaseFeature = -> Fillet151
  Radius = 0.5
  SupportTransform = false
FEATURE [PartDesign::Fillet] Fillet153
  Base = -> Fillet152 [Edge74]
  BaseFeature = -> Fillet152
  Radius = 0.5
  SupportTransform = false
FEATURE [PartDesign::Body] Body013
  Group = -> [Sketch013,Pad013,Fillet143,Fillet144,Fillet145,Fillet146,Fillet147,Fillet148,Fillet149,Fillet150,Fillet151,Fillet152,Fillet153]
  Origin = -> Origin027
  Placement = pos=(0,0,0) rot=(0,1,0;1.5708rad)
  Tip = -> Fillet153
FEATURE [App::Part] Part013  label="2020-300-014"
  Group = -> [Body013]
  Origin = -> Origin026
  Placement = pos=(330,20,80) rot=(0,0,1;1.5708rad)
FEATURE [Sketcher::SketchObject] Sketch014
  FullyConstrained = true
  MapMode = 5
  Placement = pos=(0,0,0) rot=(-0.57735,0.57735,0.57735;4.18879rad)
  Support = -> [YZ_Plane036]
  sketch-geometry (1):
    g0: Circle CenterX=0 CenterY=-7.5 CenterZ=0 NormalX=0 NormalY=0 NormalZ=1 AngleXU=0 Radius=0.25
  constraints (3):
    c: PointOnObject(g0,g-2)
    c: DistanceY(g0) = -7.5
    c: Diameter(g0) = 0.5
FEATURE [Sketcher::SketchObject] Sketch015
  FullyConstrained = true
  MapMode = 5
  Support = -> [XY_Plane029]
  sketch-geometry (2):
    g0: LineSegment StartX=0 StartY=5.5 StartZ=0 EndX=6e-16 EndY=9.5 EndZ=0
    g1: ArcOfCircle CenterX=0 CenterY=7.5 CenterZ=0 NormalX=0 NormalY=0 NormalZ=1 AngleXU=0 Radius=2 StartAngle=4.71239 EndAngle=7.85398
  constraints (7):
    c: PointOnObject(g0,g-2)
    c: PointOnObject(g0,g-2)
    c: PointOnObject(g1,g0)
    c: Coincident(g1,g0)
    c: Coincident(g1,g0)
    c: Radius(g1) = 2
    c: DistanceY(g1) = 7.5
FEATURE [PartDesign::Revolution] Revolution
  Angle = 360
  Axis = (0,1,0)
  Base = (0,0,0)
  Profile = -> Sketch015
  ReferenceAxis = -> Sketch015 [V_Axis]
  Reversed = true
FEATURE [PartDesign::Body] Body015  label="Ball 001"
  Group = -> [Sketch015,Revolution]
  Origin = -> Origin029
  Tip = -> Revolution
FEATURE [PartDesign::FeatureBase] Clone
  BaseFeature = -> Body015
FEATURE [PartDesign::Body] Body016  label="Ball 002"
  BaseFeature = -> Body015
  Group = -> [Clone]
  Origin = -> Origin030
  Placement = pos=(0,0,0) rot=(-1,0,0;0.897598rad)
  Tip = -> Clone
FEATURE [PartDesign::FeatureBase] Clone001
  BaseFeature = -> Body015
FEATURE [PartDesign::Body] Body017  label="Ball 003"
  BaseFeature = -> Body015
  Group = -> [Clone001]
  Origin = -> Origin031
  Placement = pos=(0,0,0) rot=(-1,0,0;1.7952rad)
  Tip = -> Clone001
FEATURE [PartDesign::FeatureBase] Clone002
  BaseFeature = -> Body015
FEATURE [PartDesign::Body] Body018  label="Ball 004"
  BaseFeature = -> Body015
  Group = -> [Clone002]
  Origin = -> Origin032
  Placement = pos=(0,0,0) rot=(1,0,0;3.59039rad)
  Tip = -> Clone002
FEATURE [PartDesign::FeatureBase] Clone003
  BaseFeature = -> Body015
FEATURE [PartDesign::Body] Body019  label="Ball 005"
  BaseFeature = -> Body015
  Group = -> [Clone003]
  Origin = -> Origin033
  Placement = pos=(0,0,0) rot=(1,0,0;2.69279rad)
  Tip = -> Clone003
FEATURE [PartDesign::FeatureBase] Clone004
  BaseFeature = -> Body015
FEATURE [PartDesign::Body] Body020  label="Ball 006"
  BaseFeature = -> Body015
  Group = -> [Clone004]
  Origin = -> Origin034
  Placement = pos=(0,0,0) rot=(1,0,0;1.7952rad)
  Tip = -> Clone004
FEATURE [PartDesign::FeatureBase] Clone005
  BaseFeature = -> Body015
FEATURE [PartDesign::Body] Body021  label="Ball 007"
  BaseFeature = -> Body015
  Group = -> [Clone005]
  Origin = -> Origin035
  Placement = pos=(0,0,0) rot=(1,0,0;0.897598rad)
  Tip = -> Clone005
FEATURE [App::DocumentObjectGroup] Group  label="Balls"
  Group = -> [Body015,Body016,Body017,Body018,Body019,Body020,Body021]
FEATURE [Sketcher::SketchObject] Sketch019
  FullyConstrained = true
  MapMode = 5
  Support = -> [XY_Plane038]
  sketch-geometry (7):
    g0: LineSegment StartX=-5 StartY=7.5 StartZ=0 EndX=5 EndY=7.5 EndZ=0
    g1: LineSegment StartX=-0.210977 StartY=7.5 StartZ=0 EndX=0.210977 EndY=7.5 EndZ=0
    g2: ArcOfCircle CenterX=0.25 CenterY=7.5 CenterZ=0 NormalX=0 NormalY=0 NormalZ=1 AngleXU=0 Radius=0.460977 StartAngle=2.43297 EndAngle=3.14159
    g3: ArcOfCircle CenterX=-0.25 CenterY=7.5 CenterZ=0 NormalX=0 NormalY=0 NormalZ=1 AngleXU=0 Radius=0.460977 StartAngle=9.792e-13 EndAngle=0.708626
    g4: LineSegment StartX=-0.1 StartY=7.8 StartZ=0 EndX=-0.1 EndY=7.75 EndZ=0
    g5: LineSegment StartX=-0.1 StartY=7.75 StartZ=0 EndX=0.1 EndY=7.75 EndZ=0
    g6: LineSegment StartX=0.1 StartY=7.75 StartZ=0 EndX=0.1 EndY=7.8 EndZ=0
  constraints (22):
    c: DistanceY(g-1,g0) = 7.5
    c: Symmetric(g0,g0,g-2)
    c: DistanceX(g0,g0) = 10
    c: PointOnObject(g1,g0)
    c: PointOnObject(g1,g0)
    c: Coincident(g3,g1)
    c: Coincident(g2,g1)
    c: Coincident(g2,g4)
    c: Coincident(g4,g5)
    c: Horizontal(g5)
    c: Coincident(g5,g6)
    c: Coincident(g6,g3)
    c: Vertical(g6)
    c: Equal(g3,g2)
    c: Vertical(g4)
    c: Symmetric(g2,g3,g-2)
    c: DistanceX(g5,g5) = 0.2
    c: Distance(g5,g1) = 0.25
    c: DistanceX(g3,g-1) = 0.25
    c: PointOnObject(g3,g1)
    c: PointOnObject(g2,g1)
    c: Distance(g3,g1) = 0.3
FEATURE [PartDesign::Revolution] Revolution005
  Angle = 360
  Axis = (10,0,0)
  Base = (-5,7.5,0)
  Profile = -> Sketch019
  ReferenceAxis = -> Sketch019 [Axis]
FEATURE [PartDesign::Body] Body024  label="Rivet 001"
  Group = -> [Sketch019,Revolution005]
  Origin = -> Origin038
  Placement = pos=(0,0,0) rot=(1,0,0;0.448799rad)
  Tip = -> Revolution005
FEATURE [PartDesign::FeatureBase] Clone007
  BaseFeature = -> Body024
  Placement = pos=(0,0,0) rot=(1,0,0;0.448799rad)
FEATURE [PartDesign::Body] Body025  label="Rivet 002"
  BaseFeature = -> Body024
  Group = -> [Clone007]
  Origin = -> Origin039
  Placement = pos=(0,0,0) rot=(1,0,0;0.897598rad)
  Tip = -> Clone007
FEATURE [PartDesign::FeatureBase] Clone008
  BaseFeature = -> Body024
  Placement = pos=(0,0,0) rot=(1,0,0;0.448799rad)
FEATURE [PartDesign::Body] Body026  label="Rivet 003"
  BaseFeature = -> Body024
  Group = -> [Clone008]
  Origin = -> Origin040
  Placement = pos=(0,0,0) rot=(1,0,0;1.7952rad)
  Tip = -> Clone008
FEATURE [PartDesign::FeatureBase] Clone009
  BaseFeature = -> Body024
  Placement = pos=(0,0,0) rot=(1,0,0;0.448799rad)
FEATURE [PartDesign::Body] Body027  label="Rivet 004"
  BaseFeature = -> Body024
  Group = -> [Clone009]
  Origin = -> Origin041
  Placement = pos=(0,0,0) rot=(1,0,0;2.69279rad)
  Tip = -> Clone009
FEATURE [PartDesign::FeatureBase] Clone010
  BaseFeature = -> Body024
  Placement = pos=(0,0,0) rot=(1,0,0;0.448799rad)
FEATURE [PartDesign::Body] Body028  label="Rivet 005"
  BaseFeature = -> Body024
  Group = -> [Clone010]
  Origin = -> Origin042
  Placement = pos=(0,0,0) rot=(1,0,0;3.59039rad)
  Tip = -> Clone010
FEATURE [PartDesign::FeatureBase] Clone011
  BaseFeature = -> Body024
  Placement = pos=(0,0,0) rot=(1,0,0;0.448799rad)
FEATURE [PartDesign::Body] Body029  label="Rivet 006"
  BaseFeature = -> Body024
  Group = -> [Clone011]
  Origin = -> Origin043
  Placement = pos=(0,0,0) rot=(-1,0,0;1.7952rad)
  Tip = -> Clone011
FEATURE [PartDesign::FeatureBase] Clone012
  BaseFeature = -> Body024
  Placement = pos=(0,0,0) rot=(1,0,0;0.448799rad)
FEATURE [PartDesign::Body] Body030  label="Rivet 007"
  BaseFeature = -> Body024
  Group = -> [Clone012]
  Origin = -> Origin044
  Placement = pos=(0,0,0) rot=(-1,0,0;0.897598rad)
  Tip = -> Clone012
FEATURE [App::DocumentObjectGroup] Group002  label="Rivets"
  Group = -> [Body024,Body025,Body026,Body027,Body028,Body029,Body030]
FEATURE [Sketcher::SketchObject] Sketch023
  FullyConstrained = true
  MapMode = 5
  Placement = pos=(0,0,0) rot=(1,0,0;1.5708rad)
  Support = -> [XZ_Plane036]
  sketch-geometry (4):
    g0: LineSegment StartX=0 StartY=8.5 StartZ=0 EndX=0.1 EndY=8.5 EndZ=0
    g1: LineSegment StartX=0.1 StartY=8.5 StartZ=0 EndX=0.1 EndY=6.5 EndZ=0
    g2: LineSegment StartX=0.1 StartY=6.5 StartZ=0 EndX=0 EndY=6.5 EndZ=0
    g3: LineSegment StartX=0 StartY=6.5 StartZ=0 EndX=0 EndY=8.5 EndZ=0
  constraints (12):
    c: Coincident(g0,g1)
    c: Coincident(g1,g2)
    c: Coincident(g2,g3)
    c: Coincident(g3,g0)
    c: Horizontal(g0)
    c: Horizontal(g2)
    c: Vertical(g1)
    c: Vertical(g3)
    c: PointOnObject(g0,g-2)
    c: DistanceX(g0,g0) = 0.1
    c: DistanceY(g0) = 8.5
    c: DistanceY(g1) = 6.5
FEATURE [PartDesign::Revolution] Revolution006
  Angle = 360
  Axis = (1,0,0)
  Base = (0,0,0)
  Placement = pos=(0,0,0) rot=(1,0,0;1.5708rad)
  Profile = -> Sketch023
  ReferenceAxis = -> Sketch023 [H_Axis]
FEATURE [Sketcher::SketchObject] Sketch025
  FullyConstrained = true
  MapMode = 5
  Placement = pos=(0,0,0) rot=(0.57735,0.57735,0.57735;2.0944rad)
  Support = -> [YZ_Plane036]
  sketch-geometry (5):
    g0: ArcOfCircle CenterX=0 CenterY=7.5 CenterZ=0 NormalX=0 NormalY=0 NormalZ=1 AngleXU=0 Radius=2.11 StartAngle=5.66076 EndAngle=6.65667
    g1: LineSegment StartX=5e-16 StartY=8.5 StartZ=0 EndX=0 EndY=6.26986 EndZ=0
    g2: ArcOfCircle CenterX=0 CenterY=0 CenterZ=0 NormalX=0 NormalY=0 NormalZ=1 AngleXU=0 Radius=6.5 StartAngle=1.3039 EndAngle=1.5708
    g3: LineSegment StartX=1.71431 StartY=6.26986 StartZ=0 EndX=0 EndY=6.26986 EndZ=0
    g4: ArcOfCircle CenterX=0 CenterY=0 CenterZ=0 NormalX=0 NormalY=0 NormalZ=1 AngleXU=0 Radius=8.5 StartAngle=1.33757 EndAngle=1.5708
  constraints (16):
    c: PointOnObject(g0,g-2)
    c: DistanceY(g0) = 7.5
    c: Radius(g0) = 2.11
    c: PointOnObject(g2,g1)
    c: DistanceY(g2) = 6.5
    c: Coincident(g2,g-1)
    c: Coincident(g3,g2)
    c: Horizontal(g3)
    c: Coincident(g0,g2)
    c: Coincident(g1,g3)
    c: PointOnObject(g1,g-2)
    c: PointOnObject(g1,g-2)
    c: Coincident(g4,g-1)
    c: Coincident(g4,g1)
    c: DistanceY(g1) = 8.5
    c: Coincident(g0,g4)
FEATURE [PartDesign::Revolution] Revolution007
  Angle = 180
  Axis = (-2e-16,3e-16,1)
  Base = (0,0,0)
  BaseFeature = -> Revolution006
  Placement = pos=(0,0,0) rot=(1,0,0;1.5708rad)
  Profile = -> Sketch025
  ReferenceAxis = -> Sketch025 [V_Axis]
  Reversed = true
FEATURE [PartDesign::PolarPattern] PolarPattern
  Angle = 360
  Axis = -> Sketch025 [N_Axis]
  BaseFeature = -> Revolution007
  Occurrences = 3
  Originals = -> [Revolution007]
  Placement = pos=(0,0,0) rot=(1,0,0;1.5708rad)
  Refine = true
FEATURE [Sketcher::SketchObject] Sketch026
  FullyConstrained = true
  MapMode = 5
  Placement = pos=(0,0,0) rot=(0.57735,0.57735,0.57735;2.0944rad)
  Support = -> [YZ_Plane036]
  sketch-geometry (4):
    g0: ArcOfCircle CenterX=0 CenterY=7.5 CenterZ=0 NormalX=0 NormalY=0 NormalZ=1 AngleXU=0 Radius=2.01 StartAngle=5.57985 EndAngle=6.86228
    g1: LineSegment StartX=0 StartY=6.2 StartZ=0 EndX=1.533 EndY=6.2 EndZ=0
    g2: LineSegment StartX=0 StartY=8.6 StartZ=0 EndX=0 EndY=6.2 EndZ=0
    g3: LineSegment StartX=0 StartY=8.6 StartZ=0 EndX=1.68229 EndY=8.6 EndZ=0
  constraints (13):
    c: PointOnObject(g0,g-2)
    c: DistanceY(g0) = 7.5
    c: Radius(g0) = 2.01
    c: PointOnObject(g1,g-2)
    c: Horizontal(g1)
    c: Coincident(g0,g1)
    c: DistanceY(g1) = 6.2
    c: DistanceY(g2) = 8.6
    c: Coincident(g2,g1)
    c: PointOnObject(g2,g-2)
    c: Coincident(g3,g2)
    c: Horizontal(g3)
    c: Coincident(g0,g3)
FEATURE [PartDesign::Groove] Groove
  Angle = 360
  Axis = (-2e-16,3e-16,1)
  Base = (0,0,0)
  BaseFeature = -> PolarPattern
  Placement = pos=(0,0,0) rot=(1,0,0;1.5708rad)
  Profile = -> Sketch026
  ReferenceAxis = -> Sketch026 [V_Axis]
FEATURE [PartDesign::PolarPattern] PolarPattern001
  Angle = 360
  Axis = -> Sketch026 [N_Axis]
  BaseFeature = -> Groove
  Occurrences = 3
  Originals = -> [Groove]
  Placement = pos=(0,0,0) rot=(1,0,0;1.5708rad)
FEATURE [PartDesign::Pocket] Pocket
  BaseFeature = -> PolarPattern001
  Length = 5
  Length2 = 100
  Placement = pos=(0,0,0) rot=(1,0,0;1.5708rad)
  Profile = -> Sketch014
  Type = 1
FEATURE [PartDesign::PolarPattern] PolarPattern002
  Angle = 360
  Axis = -> Sketch014 [N_Axis]
  BaseFeature = -> Pocket
  Occurrences = 3
  Originals = -> [Pocket]
  Placement = pos=(0,0,0) rot=(1,0,0;1.5708rad)
FEATURE [PartDesign::Body] Body022  label="Cage 001"
  Group = -> [Sketch023,Revolution006,Sketch025,Revolution007,PolarPattern,Sketch026,Groove,PolarPattern001,Sketch014,Pocket,PolarPattern002]
  Origin = -> Origin036
  Placement = pos=(0,0,0) rot=(-1,0,0;1.5708rad)
  Tip = -> PolarPattern002
FEATURE [PartDesign::FeatureBase] Clone006
  BaseFeature = -> Body022
  Placement = pos=(0,0,0) rot=(-1,0,0;1.5708rad)
FEATURE [PartDesign::Body] Body023  label="Cage 002"
  BaseFeature = -> Body022
  Group = -> [Clone006]
  Origin = -> Origin037
  Placement = pos=(0,0,0) rot=(0,1,0;3.14159rad)
  Tip = -> Clone006
FEATURE [App::DocumentObjectGroup] Group001  label="Cages"
  Group = -> [Body022,Body023]
FEATURE [Sketcher::SketchObject] Sketch027
  FullyConstrained = true
  MapMode = 5
  Support = -> [XY_Plane045]
  sketch-geometry (14):
    g0: ArcOfCircle CenterX=-1e-16 CenterY=7.5 CenterZ=0 NormalX=0 NormalY=0 NormalZ=1 AngleXU=0 Radius=2 StartAngle=0.848062 EndAngle=2.29353
    g1: LineSegment StartX=-3.5 StartY=11 StartZ=0 EndX=3.5 EndY=11 EndZ=0
    g2: LineSegment StartX=3.5 StartY=11 StartZ=0 EndX=3.5 EndY=9.2 EndZ=0
    g3: LineSegment StartX=2.9 StartY=9 StartZ=0 EndX=1.32288 EndY=9 EndZ=0
    g4: LineSegment StartX=-3.5 StartY=9.2 StartZ=0 EndX=-3.5 EndY=11 EndZ=0
    g5: LineSegment StartX=-1.32288 StartY=9 StartZ=0 EndX=-2.9 EndY=9 EndZ=0
    g6: LineSegment StartX=2.9 StartY=9 StartZ=0 EndX=2.9 EndY=9.5 EndZ=0
    g7: LineSegment StartX=2.9 StartY=9.5 StartZ=0 EndX=3.2 EndY=9.5 EndZ=0
    g8: LineSegment StartX=3.2 StartY=9.5 StartZ=0 EndX=3.2 EndY=9.2 EndZ=0
    g9: LineSegment StartX=3.2 StartY=9.2 StartZ=0 EndX=3.5 EndY=9.2 EndZ=0
    g10: LineSegment StartX=-3.5 StartY=9.2 StartZ=0 EndX=-3.2 EndY=9.2 EndZ=0
    g11: LineSegment StartX=-3.2 StartY=9.2 StartZ=0 EndX=-3.2 EndY=9.5 EndZ=0
    g12: LineSegment StartX=-3.2 StartY=9.5 StartZ=0 EndX=-2.9 EndY=9.5 EndZ=0
    g13: LineSegment StartX=-2.9 StartY=9.5 StartZ=0 EndX=-2.9 EndY=9 EndZ=0
  constraints (41):
    c: Coincident(g1,g2)
    c: Coincident(g4,g1)
    c: Horizontal(g3)
    c: Vertical(g2)
    c: Vertical(g4)
    c: Coincident(g0,g5)
    c: Coincident(g0,g3)
    c: DistanceY(g-1,g0) = 7.5
    c: Radius(g0) = 2
    c: Symmetric(g1,g1,g-2)
    c: Symmetric(g0,g0,g-2)
    c: DistanceY(g1) = 11
    c: DistanceX(g1,g1) = 7
    c: Vertical(g6)
    c: Coincident(g6,g7)
    c: Horizontal(g7)
    c: Coincident(g7,g8)
    c: Vertical(g8)
    c: Coincident(g8,g9)
    c: Coincident(g3,g6)
    c: Coincident(g2,g9)
    c: Horizontal(g10)
    c: Coincident(g10,g11)
    c: Coincident(g11,g12)
    c: Horizontal(g12)
    c: Coincident(g12,g13)
    c: Vertical(g13)
    c: Vertical(g11)
    c: Coincident(g4,g10)
    c: Coincident(g5,g13)
    c: DistanceY(g13,g13) = 0.5
    c: DistanceX(g12,g12) = 0.3
    c: DistanceY(g5,g10) = 0.2
    c: Symmetric(g5,g3,g-2)
    c: DistanceY(g3) = 9
    c: DistanceY(g6) = 9.5
    c: Equal(g7,g12)
    c: Equal(g13,g6)
    c: Horizontal(g9)
    c: Horizontal(g8,g10)
    c: Equal(g12,g10)
FEATURE [PartDesign::Revolution] Revolution008
  Angle = 360
  Axis = (1,0,0)
  Base = (0,0,0)
  Profile = -> Sketch027
  ReferenceAxis = -> X_Axis045
FEATURE [PartDesign::Fillet] Fillet154
  Base = -> Revolution008 [Edge14,Edge15]
  BaseFeature = -> Revolution008
  Radius = 0.3
  SupportTransform = false
FEATURE [PartDesign::Body] Body031  label="Outer Ring001"
  Group = -> [Sketch027,Revolution008,Fillet154]
  Origin = -> Origin045
  Tip = -> Fillet154
FEATURE [Sketcher::SketchObject] Sketch028
  FullyConstrained = true
  MapMode = 5
  Support = -> [XY_Plane046]
  sketch-geometry (14):
    g0: LineSegment StartX=-2.9 StartY=6 StartZ=0 EndX=-1.32288 EndY=6 EndZ=0
    g1: LineSegment StartX=-3.5 StartY=4 StartZ=0 EndX=-3.5 EndY=5.7 EndZ=0
    g2: ArcOfCircle CenterX=-1e-16 CenterY=7.5 CenterZ=0 NormalX=0 NormalY=0 NormalZ=1 AngleXU=0 Radius=2 StartAngle=3.98965 EndAngle=5.43512
    g3: LineSegment StartX=1.32288 StartY=6 StartZ=0 EndX=2.9 EndY=6 EndZ=0
    g4: LineSegment StartX=-3.5 StartY=5.7 StartZ=0 EndX=-3.2 EndY=5.7 EndZ=0
    g5: LineSegment StartX=-3.2 StartY=5.7 StartZ=0 EndX=-3.2 EndY=5.5 EndZ=0
    g6: LineSegment StartX=-3.2 StartY=5.5 StartZ=0 EndX=-2.9 EndY=5.5 EndZ=0
    g7: LineSegment StartX=-2.9 StartY=5.5 StartZ=0 EndX=-2.9 EndY=6 EndZ=0
    g8: LineSegment StartX=8.5 StartY=6 StartZ=0 EndX=3.2 EndY=6 EndZ=0
    g9: LineSegment StartX=3.2 StartY=6 StartZ=0 EndX=3.2 EndY=5.5 EndZ=0
    g10: LineSegment StartX=3.2 StartY=5.5 StartZ=0 EndX=2.9 EndY=5.5 EndZ=0
    g11: LineSegment StartX=2.9 StartY=5.5 StartZ=0 EndX=2.9 EndY=6 EndZ=0
    g12: LineSegment StartX=8.5 StartY=4 StartZ=0 EndX=8.5 EndY=6 EndZ=0
    g13: LineSegment StartX=-3.5 StartY=4 StartZ=0 EndX=8.5 EndY=4 EndZ=0
  constraints (43):
    c: Horizontal(g0)
    c: Vertical(g1)
    c: DistanceY(g1) = 4
    c: Coincident(g2,g0)
    c: Coincident(g2,g3)
    c: Horizontal(g3)
    c: Radius(g2) = 2
    c: DistanceY(g2) = 7.5
    c: Symmetric(g0,g2,g-2)
    c: Horizontal(g4)
    c: Coincident(g4,g5)
    c: Vertical(g5)
    c: Coincident(g5,g6)
    c: Horizontal(g6)
    c: Coincident(g6,g7)
    c: Vertical(g7)
    c: Horizontal(g8)
    c: Coincident(g8,g9)
    c: Vertical(g9)
    c: Coincident(g9,g10)
    c: Horizontal(g10)
    c: Coincident(g10,g11)
    c: Vertical(g11)
    c: Coincident(g3,g11)
    c: Coincident(g0,g7)
    c: Coincident(g1,g4)
    c: DistanceY(g3) = 6
    c: DistanceY(g6,g0) = 0.5
    c: DistanceX(g4,g4) = 0.3
    c: DistanceX(g6,g6) = 0.3
    c: DistanceY(g5,g4) = 0.2
    c: Vertical(g12)
    c: Equal(g11,g7)
    c: DistanceY(g1,g0) = 2
    c: DistanceX(g8,g8) = 5.3
    c: Coincident(g13,g1)
    c: Coincident(g13,g12)
    c: Horizontal(g13)
    c: DistanceX(g13,g13) = 12
    c: DistanceX(g1,g2) = 3.5
    c: Coincident(g8,g12)
    c: Equal(g7,g9)
    c: Equal(g6,g10)
FEATURE [PartDesign::Revolution] Revolution009
  Angle = 360
  Axis = (1,0,0)
  Base = (0,0,0)
  Profile = -> Sketch028
  ReferenceAxis = -> X_Axis046
FEATURE [PartDesign::Fillet] Fillet155
  Base = -> Revolution009 [Edge13,Edge11]
  BaseFeature = -> Revolution009
  Radius = 0.2
  SupportTransform = false
FEATURE [PartDesign::Body] Body032  label="Inner Ring001"
  Group = -> [Sketch028,Revolution009,Fillet155]
  Origin = -> Origin046
  Tip = -> Fillet155
FEATURE [App::DocumentObjectGroup] Group004  label="Rings"
  Group = -> [Body031,Body032]
FEATURE [Sketcher::SketchObject] Sketch029
  FullyConstrained = true
  MapMode = 5
  Placement = pos=(0,0,0) rot=(1,0,0;1.5708rad)
  Support = -> [XZ_Plane047]
  sketch-geometry (12):
    g0: LineSegment StartX=2.9 StartY=9.5 StartZ=0 EndX=2.9 EndY=8.5 EndZ=0
    g1: LineSegment StartX=2.9 StartY=8.5 StartZ=0 EndX=3.2 EndY=8.5 EndZ=0
    g2: LineSegment StartX=3.2 StartY=8.5 StartZ=0 EndX=3.2 EndY=6.5 EndZ=0
    g3: LineSegment StartX=3.2 StartY=6.5 StartZ=0 EndX=2.9 EndY=6.5 EndZ=0
    g4: LineSegment StartX=2.9 StartY=6.5 StartZ=0 EndX=2.9 EndY=5.5 EndZ=0
    g5: LineSegment StartX=2.9 StartY=5.5 StartZ=0 EndX=3.2 EndY=5.5 EndZ=0
    g6: LineSegment StartX=3.2 StartY=5.5 StartZ=0 EndX=3.2 EndY=6 EndZ=0
    g7: LineSegment StartX=3.2 StartY=6 StartZ=0 EndX=3.5 EndY=6 EndZ=0
    g8: LineSegment StartX=3.5 StartY=6 StartZ=0 EndX=3.5 EndY=9 EndZ=0
    g9: LineSegment StartX=3.5 StartY=9 StartZ=0 EndX=3.2 EndY=9 EndZ=0
    g10: LineSegment StartX=3.2 StartY=9 StartZ=0 EndX=3.2 EndY=9.5 EndZ=0
    g11: LineSegment StartX=3.2 StartY=9.5 StartZ=0 EndX=2.9 EndY=9.5 EndZ=0
  constraints (36):
    c: Vertical(g0)
    c: Coincident(g0,g1)
    c: Horizontal(g1)
    c: Coincident(g1,g2)
    c: Vertical(g2)
    c: Coincident(g2,g3)
    c: Horizontal(g3)
    c: Coincident(g3,g4)
    c: Vertical(g4)
    c: Coincident(g4,g5)
    c: Horizontal(g5)
    c: Coincident(g5,g6)
    c: Vertical(g6)
    c: Coincident(g6,g7)
    c: Horizontal(g7)
    c: Coincident(g7,g8)
    c: Vertical(g8)
    c: Coincident(g8,g9)
    c: Horizontal(g9)
    c: Coincident(g9,g10)
    c: Vertical(g10)
    c: Coincident(g10,g11)
    c: Coincident(g11,g0)
    c: Horizontal(g11)
    c: DistanceY(g4) = 5.5
    c: DistanceX(g4) = 2.9
    c: DistanceY(g5,g6) = 0.5
    c: DistanceY(g6,g2) = 0.5
    c: DistanceX(g5,g5) = 0.3
    c: Equal(g5,g7)
    c: Equal(g7,g3)
    c: Equal(g3,g1)
    c: Equal(g1,g9)
    c: Equal(g4,g0)
    c: Equal(g6,g10)
    c: DistanceY(g4,g0) = 4
FEATURE [PartDesign::Revolution] Revolution010
  Angle = 360
  Axis = (1,0,0)
  Base = (0,0,0)
  Placement = pos=(0,0,0) rot=(1,0,0;1.5708rad)
  Profile = -> Sketch029
  ReferenceAxis = -> Sketch029 [H_Axis]
FEATURE [PartDesign::Fillet] Fillet156
  Base = -> Revolution010 [Edge14,Edge12]
  BaseFeature = -> Revolution010
  Placement = pos=(0,0,0) rot=(1,0,0;1.5708rad)
  Radius = 0.2
  SupportTransform = false
FEATURE [PartDesign::Body] Body033  label="Seal 001"
  Group = -> [Sketch029,Revolution010,Fillet156]
  Origin = -> Origin047
  Tip = -> Fillet156
FEATURE [PartDesign::FeatureBase] Clone013
  BaseFeature = -> Body033
FEATURE [PartDesign::Body] Body034  label="Seal 002"
  BaseFeature = -> Body033
  Group = -> [Clone013]
  Origin = -> Origin048
  Placement = pos=(0,0,0) rot=(0,1,0;3.14159rad)
  Tip = -> Clone013
FEATURE [App::DocumentObjectGroup] Group003  label="Seals"
  Group = -> [Body033,Body034]
FEATURE [Sketcher::SketchObject] Sketch030
  AttachmentOffset = pos=(0,0,4) rot=(0,0,1;0rad)
  FullyConstrained = true
  MapMode = 5
  Placement = pos=(0,0,4) rot=(0,0,1;0rad)
  Support = -> [XY_Plane028]
  sketch-geometry (1):
    g0: Circle CenterX=6 CenterY=0 CenterZ=0 NormalX=0 NormalY=0 NormalZ=1 AngleXU=0 Radius=1.5
  constraints (3):
    c: PointOnObject(g0,g-1)
    c: Diameter(g0) = 3
    c: DistanceX(g-1,g0) = 6
FEATURE [PartDesign::Pad] Pad014
  Direction = (0,0,1)
  Length = 3
  Length2 = 100
  Profile = -> Sketch030
  Type = 0
FEATURE [Sketcher::SketchObject] Sketch031
  ExternalGeometry = -> [Pad014]
  FullyConstrained = true
  MapMode = 5
  Placement = pos=(0,0,7) rot=(0,0,1;0rad)
  Support = -> [Pad014]
  sketch-geometry (7):
    g0: LineSegment StartX=6.43301 StartY=-0.75 StartZ=0 EndX=6.86603 EndY=0 EndZ=0
    g1: LineSegment StartX=6.86603 StartY=0 StartZ=0 EndX=6.43301 EndY=0.75 EndZ=0
    g2: LineSegment StartX=6.43301 StartY=0.75 StartZ=0 EndX=5.56699 EndY=0.75 EndZ=0
    g3: LineSegment StartX=5.56699 StartY=0.75 StartZ=0 EndX=5.13397 EndY=-1e-16 EndZ=0
    g4: LineSegment StartX=5.13397 StartY=-1e-16 StartZ=0 EndX=5.56699 EndY=-0.75 EndZ=0
    g5: LineSegment StartX=5.56699 StartY=-0.75 StartZ=0 EndX=6.43301 EndY=-0.75 EndZ=0
    g6: Circle CenterX=6 CenterY=0 CenterZ=0 NormalX=0 NormalY=0 NormalZ=1 AngleXU=0 Radius=0.866025
  constraints (16):
    c: Coincident(g0,g1)
    c: Coincident(g1,g2)
    c: Coincident(g2,g3)
    c: Coincident(g3,g4)
    c: Coincident(g4,g5)
    c: Coincident(g5,g0)
    c: Equal(g0, g1-g5) x5
    c: PointOnObject(g0,g6)
    c: PointOnObject(g1,g6)
    c: PointOnObject(g2,g6)
    c: PointOnObject(g3,g6)
    c: PointOnObject(g4,g6)
    c: PointOnObject(g5,g6)
    c: Coincident(g6,g-3)
    c: Horizontal(g5)
    c: DistanceY(g4,g2) = 1.5
FEATURE [PartDesign::Pocket] Pocket001
  BaseFeature = -> Pad014
  Length = 0.9
  Length2 = 100
  Profile = -> Sketch031
  Type = 0
FEATURE [PartDesign::PolarPattern] PolarPattern003
  Angle = 120
  Axis = -> X_Axis028
  BaseFeature = -> Pocket001
  Occurrences = 3
  Originals = -> [Pad014,Pocket001]
FEATURE [PartDesign::Body] Body014
  Group = -> [Sketch030,Pad014,Sketch031,Pocket001,PolarPattern003]
  Origin = -> Origin028
  Tip = -> PolarPattern003
FEATURE [App::DocumentObjectGroup] Group005  label="Set screws"
  Group = -> [Body014]
FEATURE [Sketcher::SketchObject] Sketch032
  AttachmentOffset = pos=(0,0,-6.5) rot=(0,0,1;0rad)
  FullyConstrained = true
  MapMode = 5
  Placement = pos=(-6.5,1.4e-15,-1.4e-15) rot=(0.57735,0.57735,0.57735;2.0944rad)
  Support = -> [YZ_Plane049]
  sketch-geometry (14):
    g0: Circle CenterX=0 CenterY=0 CenterZ=0 NormalX=0 NormalY=0 NormalZ=1 AngleXU=0 Radius=11
    g1: ArcOfCircle CenterX=0 CenterY=0 CenterZ=0 NormalX=0 NormalY=0 NormalZ=1 AngleXU=0 Radius=13.5 StartAngle=0.0668757 EndAngle=3.07472
    g2: LineSegment StartX=-13.4698 StartY=0.902148 StartZ=0 EndX=-14.2 EndY=-10 EndZ=0
    g3: LineSegment StartX=-14.2 StartY=-10 StartZ=0 EndX=-27.5 EndY=-10 EndZ=0
    g4: LineSegment StartX=-27.5 StartY=-10 StartZ=0 EndX=-27.5 EndY=-15 EndZ=0
    g5: LineSegment StartX=-27.5 StartY=-15 StartZ=0 EndX=-12.3 EndY=-15 EndZ=0
    g6: LineSegment StartX=27.5 StartY=-15 StartZ=0 EndX=27.5 EndY=-10 EndZ=0
    g7: LineSegment StartX=27.5 StartY=-10 StartZ=0 EndX=14.2 EndY=-10 EndZ=0
    g8: LineSegment StartX=14.2 StartY=-10 StartZ=0 EndX=13.4698 EndY=0.902148 EndZ=0
    g9: LineSegment StartX=12.3 StartY=-15 StartZ=0 EndX=12.1995 EndY=-13.5 EndZ=0
    g10: LineSegment StartX=12.1995 StartY=-13.5 StartZ=0 EndX=-12.1995 EndY=-13.5 EndZ=0
    g11: LineSegment StartX=-12.1995 StartY=-13.5 StartZ=0 EndX=-12.3 EndY=-15 EndZ=0
    g12: LineSegment StartX=12.3 StartY=-15 StartZ=0 EndX=27.5 EndY=-15 EndZ=0
    g13: GeomPoint X=0 Y=13.5 Z=0
  constraints (39):
    c: Coincident(g0,g-1)
    c: Radius(g0) = 11
    c: Coincident(g1,g0)
    c: Coincident(g2,g3)
    c: Coincident(g3,g4)
    c: Coincident(g4,g5)
    c: Horizontal(g5)
    c: Coincident(g12,g6)
    c: Coincident(g6,g7)
    c: Horizontal(g7)
    c: Coincident(g7,g8)
    c: Coincident(g9,g10)
    c: Horizontal(g10)
    c: Coincident(g10,g11)
    c: Coincident(g5,g11)
    c: Coincident(g12,g9)
    c: Horizontal(g3)
    c: Vertical(g6)
    c: Vertical(g4)
    c: Equal(g9,g11)
    c: Horizontal(g12)
    c: Horizontal(g5,g9)
    c: Equal(g6,g4)
    c: Equal(g12,g5)
    c: Equal(g7,g3)
    c: DistanceX(g4,g6) = 55
    c: DistanceY(g6,g0) = 15
    c: Equal(g8,g2)
    c: DistanceY(g6,g6) = 5
    c: Parallel(g9,g8)
    c: DistanceY(g9,g9) = 1.5
    c: DistanceX(g5,g5) = 15.2
    c: Diameter(g1) = 27
    c: PointOnObject(g13,g1)
    c: PointOnObject(g13,g-2)
    c: DistanceY(g6,g13) = 28.5
    c: Tangent(g1,g2) = -1.5708
    c: Tangent(g1,g8) = -1.5708
    c: DistanceX(g3,g3) = 13.3
FEATURE [PartDesign::Pad] Pad015
  Direction = (1,-2e-16,3e-16)
  Length = 13
  Length2 = 100
  Placement = pos=(0,0,0) rot=(0.57735,0.57735,0.57735;2.0944rad)
  Profile = -> Sketch032
  Type = 0
FEATURE [Sketcher::SketchObject] Sketch033
  ExternalGeometry = -> [Pad015]
  FullyConstrained = true
  MapMode = 5
  Placement = pos=(4.2e-15,-6.6e-15,-15) rot=(0.707107,0.707107,0;3.14159rad)
  Support = -> [Pad015]
  sketch-geometry (7):
    g0: LineSegment StartX=-24.9 StartY=4.15 StartZ=0 EndX=-14.9 EndY=4.15 EndZ=0
    g1: LineSegment StartX=-14.9 StartY=4.15 StartZ=0 EndX=-14.9 EndY=-4.15 EndZ=0
    g2: LineSegment StartX=-14.9 StartY=-4.15 StartZ=0 EndX=-24.9 EndY=-4.15 EndZ=0
    g3: LineSegment StartX=-24.9 StartY=-4.15 StartZ=0 EndX=-24.9 EndY=4.15 EndZ=0
    g4: LineSegment StartX=-27.5 StartY=6.5 StartZ=0 EndX=-12.3 EndY=-6.5 EndZ=0
    g5: LineSegment StartX=-27.5 StartY=-6.5 StartZ=0 EndX=-12.3 EndY=6.5 EndZ=0
    g6: GeomPoint X=-19.9 Y=2.6e-15 Z=0
  constraints (17):
    c: Coincident(g0,g1)
    c: Coincident(g1,g2)
    c: Coincident(g2,g3)
    c: Coincident(g3,g0)
    c: Horizontal(g0)
    c: Horizontal(g2)
    c: Vertical(g1)
    c: Vertical(g3)
    c: DistanceX(g0,g0) = 10
    c: DistanceY(g1,g1) = 8.3
    c: Coincident(g4,g-3)
    c: Coincident(g4,g-4)
    c: Coincident(g5,g-4)
    c: Coincident(g5,g-3)
    c: PointOnObject(g6,g4)
    c: PointOnObject(g6,g5)
    c: Symmetric(g0,g1,g6)
FEATURE [PartDesign::Pocket] Pocket002
  BaseFeature = -> Pad015
  Length = 2.3
  Length2 = 100
  Placement = pos=(0,0,0) rot=(0.57735,0.57735,0.57735;2.0944rad)
  Profile = -> Sketch033
  Type = 0
FEATURE [Sketcher::SketchObject] Sketch034
  ExternalGeometry = -> [Pocket002]
  FullyConstrained = true
  MapMode = 5
  Placement = pos=(2.8e-15,-4.4e-15,-10) rot=(0,0,-1;1.5708rad)
  Support = -> [Pocket002]
  sketch-geometry (2):
    g0: Circle CenterX=21.2 CenterY=2.1e-15 CenterZ=0 NormalX=0 NormalY=0 NormalZ=1 AngleXU=0 Radius=2.5
    g1: LineSegment StartX=21.2 StartY=2.1e-15 StartZ=0 EndX=27.5 EndY=2.1e-15 EndZ=0
  constraints (5):
    c: Diameter(g0) = 5
    c: DistanceX(g0,g-3) = 6.3
    c: Coincident(g1,g0)
    c: Horizontal(g1)
    c: Symmetric(g-5,g-5,g1)
FEATURE [PartDesign::Pocket] Pocket003
  BaseFeature = -> Pocket002
  Length = 5
  Length2 = 100
  Placement = pos=(0,0,0) rot=(0.57735,0.57735,0.57735;2.0944rad)
  Profile = -> Sketch034
  Type = 2
FEATURE [Sketcher::SketchObject] Sketch035
  ExternalGeometry = -> [Pocket003]
  FullyConstrained = true
  MapMode = 5
  Placement = pos=(6.5,-1.4e-15,1.5e-15) rot=(0.57735,0.57735,0.57735;2.0944rad)
  Support = -> [Pocket003]
  sketch-geometry (6):
    g0: LineSegment StartX=-24.6 StartY=-13.7 StartZ=0 EndX=-24.6 EndY=-11.3 EndZ=0
    g1: LineSegment StartX=-24.6 StartY=-11.3 StartZ=0 EndX=-14.2 EndY=-11.3 EndZ=0
    g2: LineSegment StartX=-14.2 StartY=-11.3 StartZ=0 EndX=-14.2 EndY=-13.7 EndZ=0
    g3: LineSegment StartX=-14.2 StartY=-13.7 StartZ=0 EndX=-24.6 EndY=-13.7 EndZ=0
    g4: GeomPoint X=-19.4 Y=-12.5 Z=0
    g5: LineSegment StartX=-19.4 StartY=-12.5 StartZ=0 EndX=-27.5 EndY=-12.5 EndZ=0
  constraints (15):
    c: Coincident(g0,g1)
    c: Coincident(g1,g2)
    c: Coincident(g2,g3)
    c: Coincident(g3,g0)
    c: Horizontal(g1)
    c: Horizontal(g3)
    c: Vertical(g0)
    c: Vertical(g2)
    c: Symmetric(g1,g0,g4)
    c: DistanceX(g1,g1) = 10.4
    c: DistanceY(g2,g2) = 2.4
    c: DistanceX(g2,g-4) = 1.9
    c: Coincident(g5,g4)
    c: Horizontal(g5)
    c: Symmetric(g-5,g-5,g5)
FEATURE [PartDesign::Pocket] Pocket004
  BaseFeature = -> Pocket003
  Length = 0.4
  Length2 = 100
  Placement = pos=(0,0,0) rot=(0.57735,0.57735,0.57735;2.0944rad)
  Profile = -> Sketch035
  Type = 0
FEATURE [PartDesign::Mirrored] Mirrored
  BaseFeature = -> Pocket004
  MirrorPlane = -> Sketch033 [V_Axis]
  Originals = -> [Pocket002,Pocket003,Pocket004]
  Placement = pos=(0,0,0) rot=(0.57735,0.57735,0.57735;2.0944rad)
FEATURE [Sketcher::SketchObject] Sketch036
  ExternalGeometry = -> [Mirrored]
  FullyConstrained = true
  MapMode = 5
  Placement = pos=(0,0,0) rot=(1,0,0;1.5708rad)
  Support = -> [XZ_Plane049]
  sketch-geometry (9):
    g0: GeomPoint X=-6.5 Y=13.5 Z=0
    g1: LineSegment StartX=6.5 StartY=-10 StartZ=0 EndX=6.5 EndY=13.5 EndZ=0
    g2: LineSegment StartX=6.5 StartY=13.5 StartZ=0 EndX=4.75 EndY=13.5 EndZ=0
    g3: LineSegment StartX=-6.5 StartY=13.5 StartZ=0 EndX=-4.75 EndY=13.5 EndZ=0
    g4: LineSegment StartX=-6.5 StartY=-10 StartZ=0 EndX=-6.5 EndY=13.5 EndZ=0
    g5: LineSegment StartX=6.5 StartY=-10 StartZ=0 EndX=4.75 EndY=-1 EndZ=0
    g6: LineSegment StartX=4.75 StartY=-1 StartZ=0 EndX=4.75 EndY=13.5 EndZ=0
    g7: LineSegment StartX=-4.75 StartY=13.5 StartZ=0 EndX=-4.75 EndY=-1 EndZ=0
    g8: LineSegment StartX=-4.75 StartY=-1 StartZ=0 EndX=-6.5 EndY=-10 EndZ=0
  constraints (24):
    c: Vertical(g0,g-4)
    c: Horizontal(g-3,g0)
    c: Coincident(g1,g-3)
    c: Coincident(g1,g2)
    c: Horizontal(g2)
    c: Coincident(g3,g0)
    c: Horizontal(g3)
    c: Coincident(g4,g3)
    c: Vertical(g4,g-4)
    c: DistanceX(g3,g2) = 9.5
    c: Equal(g2,g3)
    c: Horizontal(g1,g4)
    c: Coincident(g1,g-5)
    c: Coincident(g1,g5)
    c: Coincident(g5,g6)
    c: Coincident(g6,g2)
    c: Vertical(g6)
    c: DistanceY(g1,g5) = 9
    c: Coincident(g3,g7)
    c: Vertical(g7)
    c: Coincident(g7,g8)
    c: Coincident(g8,g4)
    c: Horizontal(g7,g5)
    c: DistanceX(g2,g2) = 1.75
FEATURE [PartDesign::Pocket] Pocket005
  BaseFeature = -> Mirrored
  Length = 15
  Length2 = 15
  Placement = pos=(0,0,0) rot=(0.57735,0.57735,0.57735;2.0944rad)
  Profile = -> Sketch036
  Type = 4
FEATURE [Sketcher::SketchObject] Sketch037
  FullyConstrained = true
  MapMode = 5
  Placement = pos=(-6.5,1.4e-15,-1.5e-15) rot=(0.57735,0.57735,-0.57735;4.18879rad)
  Support = -> [Pocket005]
  sketch-geometry (1):
    g0: Circle CenterX=0 CenterY=0 CenterZ=0 NormalX=0 NormalY=0 NormalZ=1 AngleXU=0 Radius=12.2
  constraints (2):
    c: Coincident(g0,g-1)
    c: Diameter(g0) = 24.4
FEATURE [PartDesign::Pocket] Pocket006
  BaseFeature = -> Pocket005
  Length = 2.75
  Length2 = 100
  Placement = pos=(0,0,0) rot=(0.57735,0.57735,0.57735;2.0944rad)
  Profile = -> Sketch037
  Type = 0
FEATURE [Sketcher::SketchObject] Sketch038
  FullyConstrained = true
  MapMode = 5
  Placement = pos=(6.5,-1.4e-15,1.5e-15) rot=(0.57735,0.57735,0.57735;2.0944rad)
  Support = -> [Pocket006]
  sketch-geometry (1):
    g0: Circle CenterX=0 CenterY=0 CenterZ=0 NormalX=0 NormalY=0 NormalZ=1 AngleXU=0 Radius=12.1
  constraints (2):
    c: Coincident(g0,g-1)
    c: Diameter(g0) = 24.2
FEATURE [PartDesign::Pocket] Pocket007
  BaseFeature = -> Pocket006
  Length = 2.75
  Length2 = 100
  Placement = pos=(0,0,0) rot=(0.57735,0.57735,0.57735;2.0944rad)
  Profile = -> Sketch038
  Type = 0
FEATURE [Sketcher::SketchObject] Sketch039
  ExternalGeometry = -> [Pocket007]
  FullyConstrained = true
  MapMode = 5
  Placement = pos=(6.5,-1.4e-15,1.5e-15) rot=(0.57735,0.57735,0.57735;2.0944rad)
  Support = -> [Pocket007]
  sketch-geometry (6):
    g0: ArcOfCircle CenterX=0 CenterY=0 CenterZ=0 NormalX=0 NormalY=0 NormalZ=1 AngleXU=0 Radius=13.5 StartAngle=3.79664 EndAngle=5.62814
    g1: LineSegment StartX=-11.8698 StartY=-8.57666 StartZ=0 EndX=-12.3 EndY=-15 EndZ=0
    g2: LineSegment StartX=-12.3 StartY=-15 StartZ=0 EndX=12.3 EndY=-15 EndZ=0
    g3: LineSegment StartX=12.3 StartY=-15 StartZ=0 EndX=11.8698 EndY=-8.57666 EndZ=0
    g4: ArcOfCircle CenterX=11.2212 CenterY=-8.6201 CenterZ=0 NormalX=0 NormalY=0 NormalZ=1 AngleXU=0 Radius=0.65 StartAngle=0.0668757 EndAngle=2.48655
    g5: ArcOfCircle CenterX=-11.2212 CenterY=-8.6201 CenterZ=0 NormalX=0 NormalY=0 NormalZ=1 AngleXU=0 Radius=0.65 StartAngle=0.655044 EndAngle=3.07472
  constraints (14):
    c: Coincident(g0,g-1)
    c: Diameter(g0) = 27
    c: Coincident(g1,g2)
    c: Coincident(g2,g3)
    c: Coincident(g1,g-3)
    c: Coincident(g2,g-4)
    c: Tangent(g3,g4) = -1.5708
    c: Tangent(g0,g4) = 1.5708
    c: Tangent(g0,g5) = 1.5708
    c: Tangent(g1,g5) = -1.5708
    c: Equal(g4,g5)
    c: Horizontal(g4,g5)
    c: Parallel(g-4,g3)
    c: Radius(g4) = 0.65
FEATURE [PartDesign::Pocket] Pocket008
  BaseFeature = -> Pocket007
  Length = 5.25
  Length2 = 100
  Placement = pos=(0,0,0) rot=(0.57735,0.57735,0.57735;2.0944rad)
  Profile = -> Sketch039
  Type = 0
FEATURE [Sketcher::SketchObject] Sketch040
  ExternalGeometry = -> [Pocket008]
  FullyConstrained = true
  MapMode = 5
  Placement = pos=(-6.5,1.4e-15,-1.5e-15) rot=(0.57735,0.57735,-0.57735;4.18879rad)
  Support = -> [Pocket008]
  sketch-geometry (6):
    g0: ArcOfCircle CenterX=0 CenterY=0 CenterZ=0 NormalX=0 NormalY=0 NormalZ=1 AngleXU=0 Radius=13.5 StartAngle=0.655044 EndAngle=2.48655
    g1: LineSegment StartX=11.8698 StartY=8.57666 StartZ=0 EndX=12.3 EndY=15 EndZ=0
    g2: LineSegment StartX=12.3 StartY=15 StartZ=0 EndX=-12.3 EndY=15 EndZ=0
    g3: LineSegment StartX=-12.3 StartY=15 StartZ=0 EndX=-11.8698 EndY=8.57666 EndZ=0
    g4: ArcOfCircle CenterX=-11.2212 CenterY=8.6201 CenterZ=0 NormalX=0 NormalY=0 NormalZ=1 AngleXU=0 Radius=0.65 StartAngle=3.20847 EndAngle=5.62814
    g5: ArcOfCircle CenterX=11.2212 CenterY=8.6201 CenterZ=0 NormalX=0 NormalY=0 NormalZ=1 AngleXU=0 Radius=0.65 StartAngle=3.79664 EndAngle=6.21631
  constraints (14):
    c: Coincident(g0,g-1)
    c: Radius(g0) = 13.5
    c: Coincident(g1,g2)
    c: Coincident(g2,g-3)
    c: Coincident(g2,g3)
    c: Coincident(g-4,g1)
    c: Tangent(g3,g4) = -1.5708
    c: Tangent(g0,g4) = 1.5708
    c: Tangent(g0,g5) = 1.5708
    c: Tangent(g1,g5) = -1.5708
    c: Equal(g4,g5)
    c: Radius(g4) = 0.65
    c: Parallel(g-4,g1)
    c: Parallel(g3,g-3)
FEATURE [PartDesign::Pocket] Pocket009
  BaseFeature = -> Pocket008
  Length = 5.25
  Length2 = 100
  Placement = pos=(0,0,0) rot=(0.57735,0.57735,0.57735;2.0944rad)
  Profile = -> Sketch040
  Type = 0
FEATURE [PartDesign::Chamfer] Chamfer
  Angle = 45
  Base = -> Pocket009 [Edge159,Edge155,Edge22,Edge27]
  BaseFeature = -> Pocket009
  ChamferType = 0
  FlipDirection = false
  Placement = pos=(0,0,0) rot=(0.57735,0.57735,0.57735;2.0944rad)
  Size = 2
  Size2 = 1
  SupportTransform = false
FEATURE [Sketcher::SketchObject] Sketch041
  ExternalGeometry = -> [Chamfer]
  FullyConstrained = true
  MapMode = 5
  Placement = pos=(-3.75,5e-15,-2.7e-15) rot=(-0.57735,-0.57735,0.57735;2.0944rad)
  Support = -> [Chamfer]
  sketch-geometry (13):
    g0: ArcOfCircle CenterX=-6.9e-15 CenterY=-3.7e-15 CenterZ=0 NormalX=0 NormalY=0 NormalZ=1 AngleXU=0 Radius=11 StartAngle=5.75419 EndAngle=6.81218
    g1: ArcOfCircle CenterX=-6.9e-15 CenterY=-3.7e-15 CenterZ=0 NormalX=0 NormalY=0 NormalZ=1 AngleXU=0 Radius=12.2 StartAngle=5.94045 EndAngle=6.62592
    g2: ArcOfCircle CenterX=-6.9e-15 CenterY=-3.7e-15 CenterZ=0 NormalX=0 NormalY=0 NormalZ=1 AngleXU=0 Radius=11 StartAngle=2.6126 EndAngle=3.67059
    g3: ArcOfCircle CenterX=-6.9e-15 CenterY=-3.7e-15 CenterZ=0 NormalX=0 NormalY=0 NormalZ=1 AngleXU=0 Radius=12.2 StartAngle=2.79886 EndAngle=3.48433
    g4: Ellipse CenterX=-6.9e-15 CenterY=-3.7e-15 CenterZ=0 NormalX=0 NormalY=0 NormalZ=1 MajorRadius=13.5 MinorRadius=7.81051 AngleXU=-3e-16
    g5: LineSegment StartX=13.5 StartY=-7.4e-15 StartZ=0 EndX=-13.5 EndY=0 EndZ=0
    g6: LineSegment StartX=-4.8e-15 StartY=7.81051 StartZ=0 EndX=-9.1e-15 EndY=-7.81051 EndZ=0
    g7: GeomPoint X=11.0112 Y=-6.8e-15 Z=0
    g8: GeomPoint X=-11.0112 Y=-7e-16 Z=0
    g9: LineSegment StartX=-11.4904 StartY=4.1 StartZ=0 EndX=-9.49645 EndY=5.55135 EndZ=0
    g10: LineSegment StartX=-11.4904 StartY=-4.1 StartZ=0 EndX=-9.49645 EndY=-5.55135 EndZ=0
    g11: LineSegment StartX=9.49645 StartY=-5.55135 StartZ=0 EndX=11.4904 EndY=-4.1 EndZ=0
    g12: LineSegment StartX=11.4904 StartY=4.1 StartZ=0 EndX=9.49645 EndY=5.55135 EndZ=0
  constraints (29):
    c: Coincident(g0,g-4)
    c: PointOnObject(g0,g-4)
    c: Coincident(g1,g0)
    c: PointOnObject(g1,g-3)
    c: Coincident(g2,g0)
    c: PointOnObject(g2,g-4)
    c: Coincident(g3,g0)
    c: PointOnObject(g3,g-3)
    c: InternalAlignment(g5-g8 -> g4) x4
    c: Coincident(g4,g0)
    c: PointOnObject(g3,g4)
    c: PointOnObject(g2,g4)
    c: PointOnObject(g3,g4)
    c: PointOnObject(g2,g4)
    c: PointOnObject(g0,g4)
    c: PointOnObject(g1,g4)
    c: PointOnObject(g1,g4)
    c: PointOnObject(g0,g4)
    c: PointOnObject(g5,g-1)
    c: DistanceX(g5,g5) = 27
    c: DistanceY(g3,g3) = 8.2
    c: Coincident(g9,g3)
    c: Coincident(g9,g2)
    c: Coincident(g10,g3)
    c: Coincident(g10,g2)
    c: Coincident(g11,g0)
    c: Coincident(g11,g1)
    c: Coincident(g12,g1)
    c: Coincident(g12,g0)
FEATURE [PartDesign::Pocket] Pocket010
  BaseFeature = -> Chamfer
  Length = 5
  Length2 = 100
  Placement = pos=(0,0,0) rot=(0.57735,0.57735,0.57735;2.0944rad)
  Profile = -> Sketch041
  Type = 0
FEATURE [PartDesign::Body] Body035  label="Metal case"
  Group = -> [Sketch032,Pad015,Sketch033,Pocket002,Sketch034,Pocket003,Sketch035,Pocket004,Mirrored,Sketch036,Pocket005,Sketch037,Pocket006,Sketch038,Pocket007,Sketch039,Pocket008,Sketch040,Pocket009,Chamfer,Sketch041,Pocket010]
  Origin = -> Origin049
  Tip = -> Pocket010
FEATURE [App::DocumentObjectGroup] Group006  label="Case"
  Group = -> [Body035]
FEATURE [App::Part] Part014  label="KP08-001"
  Group = -> [Group,Body016,Body015,Body020,Body017,Body021,Body019,Body018,Group001,Body023,Body022,Group002,Body028,Body027,Body030,Body026,Body029,Body025,Body024,Group003,Body034,Body033,Group004,Body031,Body032,Group005,Body014,Group006,Body035]
  Origin = -> Origin050
  Placement = pos=(10,246,105) rot=(0,0,1;0rad)
FEATURE [Sketcher::SketchObject] Sketch042
  FullyConstrained = true
  MapMode = 5
  Placement = pos=(0,0,0) rot=(-0.57735,0.57735,0.57735;4.18879rad)
  Support = -> [YZ_Plane058]
  sketch-geometry (1):
    g0: Circle CenterX=0 CenterY=-7.5 CenterZ=0 NormalX=0 NormalY=0 NormalZ=1 AngleXU=0 Radius=0.25
  constraints (3):
    c: PointOnObject(g0,g-2)
    c: DistanceY(g0) = -7.5
    c: Diameter(g0) = 0.5
FEATURE [Sketcher::SketchObject] Sketch043
  FullyConstrained = true
  MapMode = 5
  Support = -> [XY_Plane051]
  sketch-geometry (2):
    g0: LineSegment StartX=0 StartY=5.5 StartZ=0 EndX=6e-16 EndY=9.5 EndZ=0
    g1: ArcOfCircle CenterX=0 CenterY=7.5 CenterZ=0 NormalX=0 NormalY=0 NormalZ=1 AngleXU=0 Radius=2 StartAngle=4.71239 EndAngle=7.85398
  constraints (7):
    c: PointOnObject(g0,g-2)
    c: PointOnObject(g0,g-2)
    c: PointOnObject(g1,g0)
    c: Coincident(g1,g0)
    c: Coincident(g1,g0)
    c: Radius(g1) = 2
    c: DistanceY(g1) = 7.5
FEATURE [PartDesign::Revolution] Revolution011
  Angle = 360
  Axis = (0,1,0)
  Base = (0,0,0)
  Profile = -> Sketch043
  ReferenceAxis = -> Sketch043 [V_Axis]
  Reversed = true
FEATURE [PartDesign::Body] Body037  label="Ball 008"
  Group = -> [Sketch043,Revolution011]
  Origin = -> Origin052
  Tip = -> Revolution011
FEATURE [PartDesign::FeatureBase] Clone014
  BaseFeature = -> Body037
FEATURE [PartDesign::Body] Body038  label="Ball 009"
  BaseFeature = -> Body037
  Group = -> [Clone014]
  Origin = -> Origin053
  Placement = pos=(0,0,0) rot=(-1,0,0;0.897598rad)
  Tip = -> Clone014
FEATURE [PartDesign::FeatureBase] Clone015
  BaseFeature = -> Body037
FEATURE [PartDesign::Body] Body039  label="Ball 010"
  BaseFeature = -> Body037
  Group = -> [Clone015]
  Origin = -> Origin054
  Placement = pos=(0,0,0) rot=(-1,0,0;1.7952rad)
  Tip = -> Clone015
FEATURE [PartDesign::FeatureBase] Clone016
  BaseFeature = -> Body037
FEATURE [PartDesign::Body] Body040  label="Ball 011"
  BaseFeature = -> Body037
  Group = -> [Clone016]
  Origin = -> Origin055
  Placement = pos=(0,0,0) rot=(1,0,0;3.59039rad)
  Tip = -> Clone016
FEATURE [PartDesign::FeatureBase] Clone017
  BaseFeature = -> Body037
FEATURE [PartDesign::Body] Body041  label="Ball 012"
  BaseFeature = -> Body037
  Group = -> [Clone017]
  Origin = -> Origin056
  Placement = pos=(0,0,0) rot=(1,0,0;2.69279rad)
  Tip = -> Clone017
FEATURE [PartDesign::FeatureBase] Clone018
  BaseFeature = -> Body037
FEATURE [PartDesign::Body] Body042  label="Ball 013"
  BaseFeature = -> Body037
  Group = -> [Clone018]
  Origin = -> Origin057
  Placement = pos=(0,0,0) rot=(1,0,0;1.7952rad)
  Tip = -> Clone018
FEATURE [PartDesign::FeatureBase] Clone019
  BaseFeature = -> Body037
FEATURE [PartDesign::Body] Body043  label="Ball 014"
  BaseFeature = -> Body037
  Group = -> [Clone019]
  Origin = -> Origin058
  Placement = pos=(0,0,0) rot=(1,0,0;0.897598rad)
  Tip = -> Clone019
FEATURE [App::DocumentObjectGroup] Group007  label="Balls001"
  Group = -> [Body037,Body038,Body039,Body040,Body041,Body042,Body043]
FEATURE [Sketcher::SketchObject] Sketch044
  FullyConstrained = true
  MapMode = 5
  Support = -> [XY_Plane060]
  sketch-geometry (7):
    g0: LineSegment StartX=-5 StartY=7.5 StartZ=0 EndX=5 EndY=7.5 EndZ=0
    g1: LineSegment StartX=-0.210977 StartY=7.5 StartZ=0 EndX=0.210977 EndY=7.5 EndZ=0
    g2: ArcOfCircle CenterX=0.25 CenterY=7.5 CenterZ=0 NormalX=0 NormalY=0 NormalZ=1 AngleXU=0 Radius=0.460977 StartAngle=2.43297 EndAngle=3.14159
    g3: ArcOfCircle CenterX=-0.25 CenterY=7.5 CenterZ=0 NormalX=0 NormalY=0 NormalZ=1 AngleXU=0 Radius=0.460977 StartAngle=9.792e-13 EndAngle=0.708626
    g4: LineSegment StartX=-0.1 StartY=7.8 StartZ=0 EndX=-0.1 EndY=7.75 EndZ=0
    g5: LineSegment StartX=-0.1 StartY=7.75 StartZ=0 EndX=0.1 EndY=7.75 EndZ=0
    g6: LineSegment StartX=0.1 StartY=7.75 StartZ=0 EndX=0.1 EndY=7.8 EndZ=0
  constraints (22):
    c: DistanceY(g-1,g0) = 7.5
    c: Symmetric(g0,g0,g-2)
    c: DistanceX(g0,g0) = 10
    c: PointOnObject(g1,g0)
    c: PointOnObject(g1,g0)
    c: Coincident(g3,g1)
    c: Coincident(g2,g1)
    c: Coincident(g2,g4)
    c: Coincident(g4,g5)
    c: Horizontal(g5)
    c: Coincident(g5,g6)
    c: Coincident(g6,g3)
    c: Vertical(g6)
    c: Equal(g3,g2)
    c: Vertical(g4)
    c: Symmetric(g2,g3,g-2)
    c: DistanceX(g5,g5) = 0.2
    c: Distance(g5,g1) = 0.25
    c: DistanceX(g3,g-1) = 0.25
    c: PointOnObject(g3,g1)
    c: PointOnObject(g2,g1)
    c: Distance(g3,g1) = 0.3
FEATURE [PartDesign::Revolution] Revolution012
  Angle = 360
  Axis = (10,0,0)
  Base = (-5,7.5,0)
  Profile = -> Sketch044
  ReferenceAxis = -> Sketch044 [Axis]
FEATURE [PartDesign::Body] Body046  label="Rivet 008"
  Group = -> [Sketch044,Revolution012]
  Origin = -> Origin061
  Placement = pos=(0,0,0) rot=(1,0,0;0.448799rad)
  Tip = -> Revolution012
FEATURE [PartDesign::FeatureBase] Clone021
  BaseFeature = -> Body046
  Placement = pos=(0,0,0) rot=(1,0,0;0.448799rad)
FEATURE [PartDesign::Body] Body047  label="Rivet 009"
  BaseFeature = -> Body046
  Group = -> [Clone021]
  Origin = -> Origin062
  Placement = pos=(0,0,0) rot=(1,0,0;0.897598rad)
  Tip = -> Clone021
FEATURE [PartDesign::FeatureBase] Clone022
  BaseFeature = -> Body046
  Placement = pos=(0,0,0) rot=(1,0,0;0.448799rad)
FEATURE [PartDesign::Body] Body048  label="Rivet 010"
  BaseFeature = -> Body046
  Group = -> [Clone022]
  Origin = -> Origin063
  Placement = pos=(0,0,0) rot=(1,0,0;1.7952rad)
  Tip = -> Clone022
FEATURE [PartDesign::FeatureBase] Clone023
  BaseFeature = -> Body046
  Placement = pos=(0,0,0) rot=(1,0,0;0.448799rad)
FEATURE [PartDesign::Body] Body049  label="Rivet 011"
  BaseFeature = -> Body046
  Group = -> [Clone023]
  Origin = -> Origin064
  Placement = pos=(0,0,0) rot=(1,0,0;2.69279rad)
  Tip = -> Clone023
FEATURE [PartDesign::FeatureBase] Clone024
  BaseFeature = -> Body046
  Placement = pos=(0,0,0) rot=(1,0,0;0.448799rad)
FEATURE [PartDesign::Body] Body050  label="Rivet 012"
  BaseFeature = -> Body046
  Group = -> [Clone024]
  Origin = -> Origin065
  Placement = pos=(0,0,0) rot=(1,0,0;3.59039rad)
  Tip = -> Clone024
FEATURE [PartDesign::FeatureBase] Clone025
  BaseFeature = -> Body046
  Placement = pos=(0,0,0) rot=(1,0,0;0.448799rad)
FEATURE [PartDesign::Body] Body051  label="Rivet 013"
  BaseFeature = -> Body046
  Group = -> [Clone025]
  Origin = -> Origin066
  Placement = pos=(0,0,0) rot=(-1,0,0;1.7952rad)
  Tip = -> Clone025
FEATURE [PartDesign::FeatureBase] Clone026
  BaseFeature = -> Body046
  Placement = pos=(0,0,0) rot=(1,0,0;0.448799rad)
FEATURE [PartDesign::Body] Body052  label="Rivet 014"
  BaseFeature = -> Body046
  Group = -> [Clone026]
  Origin = -> Origin067
  Placement = pos=(0,0,0) rot=(-1,0,0;0.897598rad)
  Tip = -> Clone026
FEATURE [App::DocumentObjectGroup] Group009  label="Rivets001"
  Group = -> [Body046,Body047,Body048,Body049,Body050,Body051,Body052]
FEATURE [Sketcher::SketchObject] Sketch045
  FullyConstrained = true
  MapMode = 5
  Placement = pos=(0,0,0) rot=(1,0,0;1.5708rad)
  Support = -> [XZ_Plane058]
  sketch-geometry (4):
    g0: LineSegment StartX=0 StartY=8.5 StartZ=0 EndX=0.1 EndY=8.5 EndZ=0
    g1: LineSegment StartX=0.1 StartY=8.5 StartZ=0 EndX=0.1 EndY=6.5 EndZ=0
    g2: LineSegment StartX=0.1 StartY=6.5 StartZ=0 EndX=0 EndY=6.5 EndZ=0
    g3: LineSegment StartX=0 StartY=6.5 StartZ=0 EndX=0 EndY=8.5 EndZ=0
  constraints (12):
    c: Coincident(g0,g1)
    c: Coincident(g1,g2)
    c: Coincident(g2,g3)
    c: Coincident(g3,g0)
    c: Horizontal(g0)
    c: Horizontal(g2)
    c: Vertical(g1)
    c: Vertical(g3)
    c: PointOnObject(g0,g-2)
    c: DistanceX(g0,g0) = 0.1
    c: DistanceY(g0) = 8.5
    c: DistanceY(g1) = 6.5
FEATURE [PartDesign::Revolution] Revolution013
  Angle = 360
  Axis = (1,0,0)
  Base = (0,0,0)
  Placement = pos=(0,0,0) rot=(1,0,0;1.5708rad)
  Profile = -> Sketch045
  ReferenceAxis = -> Sketch045 [H_Axis]
FEATURE [Sketcher::SketchObject] Sketch046
  FullyConstrained = true
  MapMode = 5
  Placement = pos=(0,0,0) rot=(0.57735,0.57735,0.57735;2.0944rad)
  Support = -> [YZ_Plane058]
  sketch-geometry (5):
    g0: ArcOfCircle CenterX=0 CenterY=7.5 CenterZ=0 NormalX=0 NormalY=0 NormalZ=1 AngleXU=0 Radius=2.11 StartAngle=5.66076 EndAngle=6.65667
    g1: LineSegment StartX=5e-16 StartY=8.5 StartZ=0 EndX=0 EndY=6.26986 EndZ=0
    g2: ArcOfCircle CenterX=0 CenterY=0 CenterZ=0 NormalX=0 NormalY=0 NormalZ=1 AngleXU=0 Radius=6.5 StartAngle=1.3039 EndAngle=1.5708
    g3: LineSegment StartX=1.71431 StartY=6.26986 StartZ=0 EndX=0 EndY=6.26986 EndZ=0
    g4: ArcOfCircle CenterX=0 CenterY=0 CenterZ=0 NormalX=0 NormalY=0 NormalZ=1 AngleXU=0 Radius=8.5 StartAngle=1.33757 EndAngle=1.5708
  constraints (16):
    c: PointOnObject(g0,g-2)
    c: DistanceY(g0) = 7.5
    c: Radius(g0) = 2.11
    c: PointOnObject(g2,g1)
    c: DistanceY(g2) = 6.5
    c: Coincident(g2,g-1)
    c: Coincident(g3,g2)
    c: Horizontal(g3)
    c: Coincident(g0,g2)
    c: Coincident(g1,g3)
    c: PointOnObject(g1,g-2)
    c: PointOnObject(g1,g-2)
    c: Coincident(g4,g-1)
    c: Coincident(g4,g1)
    c: DistanceY(g1) = 8.5
    c: Coincident(g0,g4)
FEATURE [PartDesign::Revolution] Revolution014
  Angle = 180
  Axis = (-2e-16,3e-16,1)
  Base = (0,0,0)
  BaseFeature = -> Revolution013
  Placement = pos=(0,0,0) rot=(1,0,0;1.5708rad)
  Profile = -> Sketch046
  ReferenceAxis = -> Sketch046 [V_Axis]
  Reversed = true
FEATURE [PartDesign::PolarPattern] PolarPattern004
  Angle = 360
  Axis = -> Sketch046 [N_Axis]
  BaseFeature = -> Revolution014
  Occurrences = 3
  Originals = -> [Revolution014]
  Placement = pos=(0,0,0) rot=(1,0,0;1.5708rad)
  Refine = true
FEATURE [Sketcher::SketchObject] Sketch047
  FullyConstrained = true
  MapMode = 5
  Placement = pos=(0,0,0) rot=(0.57735,0.57735,0.57735;2.0944rad)
  Support = -> [YZ_Plane058]
  sketch-geometry (4):
    g0: ArcOfCircle CenterX=0 CenterY=7.5 CenterZ=0 NormalX=0 NormalY=0 NormalZ=1 AngleXU=0 Radius=2.01 StartAngle=5.57985 EndAngle=6.86228
    g1: LineSegment StartX=0 StartY=6.2 StartZ=0 EndX=1.533 EndY=6.2 EndZ=0
    g2: LineSegment StartX=0 StartY=8.6 StartZ=0 EndX=0 EndY=6.2 EndZ=0
    g3: LineSegment StartX=0 StartY=8.6 StartZ=0 EndX=1.68229 EndY=8.6 EndZ=0
  constraints (13):
    c: PointOnObject(g0,g-2)
    c: DistanceY(g0) = 7.5
    c: Radius(g0) = 2.01
    c: PointOnObject(g1,g-2)
    c: Horizontal(g1)
    c: Coincident(g0,g1)
    c: DistanceY(g1) = 6.2
    c: DistanceY(g2) = 8.6
    c: Coincident(g2,g1)
    c: PointOnObject(g2,g-2)
    c: Coincident(g3,g2)
    c: Horizontal(g3)
    c: Coincident(g0,g3)
FEATURE [PartDesign::Groove] Groove001
  Angle = 360
  Axis = (-2e-16,3e-16,1)
  Base = (0,0,0)
  BaseFeature = -> PolarPattern004
  Placement = pos=(0,0,0) rot=(1,0,0;1.5708rad)
  Profile = -> Sketch047
  ReferenceAxis = -> Sketch047 [V_Axis]
FEATURE [PartDesign::PolarPattern] PolarPattern005
  Angle = 360
  Axis = -> Sketch047 [N_Axis]
  BaseFeature = -> Groove001
  Occurrences = 3
  Originals = -> [Groove001]
  Placement = pos=(0,0,0) rot=(1,0,0;1.5708rad)
FEATURE [PartDesign::Pocket] Pocket011
  BaseFeature = -> PolarPattern005
  Length = 5
  Length2 = 100
  Placement = pos=(0,0,0) rot=(1,0,0;1.5708rad)
  Profile = -> Sketch042
  Type = 1
FEATURE [PartDesign::PolarPattern] PolarPattern006
  Angle = 360
  Axis = -> Sketch042 [N_Axis]
  BaseFeature = -> Pocket011
  Occurrences = 3
  Originals = -> [Pocket011]
  Placement = pos=(0,0,0) rot=(1,0,0;1.5708rad)
FEATURE [PartDesign::Body] Body044  label="Cage 003"
  Group = -> [Sketch045,Revolution013,Sketch046,Revolution014,PolarPattern004,Sketch047,Groove001,PolarPattern005,Sketch042,Pocket011,PolarPattern006]
  Origin = -> Origin059
  Placement = pos=(0,0,0) rot=(-1,0,0;1.5708rad)
  Tip = -> PolarPattern006
FEATURE [PartDesign::FeatureBase] Clone020
  BaseFeature = -> Body044
  Placement = pos=(0,0,0) rot=(-1,0,0;1.5708rad)
FEATURE [PartDesign::Body] Body045  label="Cage 004"
  BaseFeature = -> Body044
  Group = -> [Clone020]
  Origin = -> Origin060
  Placement = pos=(0,0,0) rot=(0,1,0;3.14159rad)
  Tip = -> Clone020
FEATURE [App::DocumentObjectGroup] Group008  label="Cages001"
  Group = -> [Body044,Body045]
FEATURE [Sketcher::SketchObject] Sketch048
  FullyConstrained = true
  MapMode = 5
  Support = -> [XY_Plane067]
  sketch-geometry (14):
    g0: ArcOfCircle CenterX=-1e-16 CenterY=7.5 CenterZ=0 NormalX=0 NormalY=0 NormalZ=1 AngleXU=0 Radius=2 StartAngle=0.848062 EndAngle=2.29353
    g1: LineSegment StartX=-3.5 StartY=11 StartZ=0 EndX=3.5 EndY=11 EndZ=0
    g2: LineSegment StartX=3.5 StartY=11 StartZ=0 EndX=3.5 EndY=9.2 EndZ=0
    g3: LineSegment StartX=2.9 StartY=9 StartZ=0 EndX=1.32288 EndY=9 EndZ=0
    g4: LineSegment StartX=-3.5 StartY=9.2 StartZ=0 EndX=-3.5 EndY=11 EndZ=0
    g5: LineSegment StartX=-1.32288 StartY=9 StartZ=0 EndX=-2.9 EndY=9 EndZ=0
    g6: LineSegment StartX=2.9 StartY=9 StartZ=0 EndX=2.9 EndY=9.5 EndZ=0
    g7: LineSegment StartX=2.9 StartY=9.5 StartZ=0 EndX=3.2 EndY=9.5 EndZ=0
    g8: LineSegment StartX=3.2 StartY=9.5 StartZ=0 EndX=3.2 EndY=9.2 EndZ=0
    g9: LineSegment StartX=3.2 StartY=9.2 StartZ=0 EndX=3.5 EndY=9.2 EndZ=0
    g10: LineSegment StartX=-3.5 StartY=9.2 StartZ=0 EndX=-3.2 EndY=9.2 EndZ=0
    g11: LineSegment StartX=-3.2 StartY=9.2 StartZ=0 EndX=-3.2 EndY=9.5 EndZ=0
    g12: LineSegment StartX=-3.2 StartY=9.5 StartZ=0 EndX=-2.9 EndY=9.5 EndZ=0
    g13: LineSegment StartX=-2.9 StartY=9.5 StartZ=0 EndX=-2.9 EndY=9 EndZ=0
  constraints (41):
    c: Coincident(g1,g2)
    c: Coincident(g4,g1)
    c: Horizontal(g3)
    c: Vertical(g2)
    c: Vertical(g4)
    c: Coincident(g0,g5)
    c: Coincident(g0,g3)
    c: DistanceY(g-1,g0) = 7.5
    c: Radius(g0) = 2
    c: Symmetric(g1,g1,g-2)
    c: Symmetric(g0,g0,g-2)
    c: DistanceY(g1) = 11
    c: DistanceX(g1,g1) = 7
    c: Vertical(g6)
    c: Coincident(g6,g7)
    c: Horizontal(g7)
    c: Coincident(g7,g8)
    c: Vertical(g8)
    c: Coincident(g8,g9)
    c: Coincident(g3,g6)
    c: Coincident(g2,g9)
    c: Horizontal(g10)
    c: Coincident(g10,g11)
    c: Coincident(g11,g12)
    c: Horizontal(g12)
    c: Coincident(g12,g13)
    c: Vertical(g13)
    c: Vertical(g11)
    c: Coincident(g4,g10)
    c: Coincident(g5,g13)
    c: DistanceY(g13,g13) = 0.5
    c: DistanceX(g12,g12) = 0.3
    c: DistanceY(g5,g10) = 0.2
    c: Symmetric(g5,g3,g-2)
    c: DistanceY(g3) = 9
    c: DistanceY(g6) = 9.5
    c: Equal(g7,g12)
    c: Equal(g13,g6)
    c: Horizontal(g9)
    c: Horizontal(g8,g10)
    c: Equal(g12,g10)
FEATURE [PartDesign::Revolution] Revolution015
  Angle = 360
  Axis = (1,0,0)
  Base = (0,0,0)
  Profile = -> Sketch048
  ReferenceAxis = -> X_Axis067
FEATURE [PartDesign::Fillet] Fillet157
  Base = -> Revolution015 [Edge14,Edge15]
  BaseFeature = -> Revolution015
  Radius = 0.3
  SupportTransform = false
FEATURE [PartDesign::Body] Body053  label="Outer Ring002"
  Group = -> [Sketch048,Revolution015,Fillet157]
  Origin = -> Origin068
  Tip = -> Fillet157
FEATURE [Sketcher::SketchObject] Sketch049
  FullyConstrained = true
  MapMode = 5
  Support = -> [XY_Plane068]
  sketch-geometry (14):
    g0: LineSegment StartX=-2.9 StartY=6 StartZ=0 EndX=-1.32288 EndY=6 EndZ=0
    g1: LineSegment StartX=-3.5 StartY=4 StartZ=0 EndX=-3.5 EndY=5.7 EndZ=0
    g2: ArcOfCircle CenterX=-1e-16 CenterY=7.5 CenterZ=0 NormalX=0 NormalY=0 NormalZ=1 AngleXU=0 Radius=2 StartAngle=3.98965 EndAngle=5.43512
    g3: LineSegment StartX=1.32288 StartY=6 StartZ=0 EndX=2.9 EndY=6 EndZ=0
    g4: LineSegment StartX=-3.5 StartY=5.7 StartZ=0 EndX=-3.2 EndY=5.7 EndZ=0
    g5: LineSegment StartX=-3.2 StartY=5.7 StartZ=0 EndX=-3.2 EndY=5.5 EndZ=0
    g6: LineSegment StartX=-3.2 StartY=5.5 StartZ=0 EndX=-2.9 EndY=5.5 EndZ=0
    g7: LineSegment StartX=-2.9 StartY=5.5 StartZ=0 EndX=-2.9 EndY=6 EndZ=0
    g8: LineSegment StartX=8.5 StartY=6 StartZ=0 EndX=3.2 EndY=6 EndZ=0
    g9: LineSegment StartX=3.2 StartY=6 StartZ=0 EndX=3.2 EndY=5.5 EndZ=0
    g10: LineSegment StartX=3.2 StartY=5.5 StartZ=0 EndX=2.9 EndY=5.5 EndZ=0
    g11: LineSegment StartX=2.9 StartY=5.5 StartZ=0 EndX=2.9 EndY=6 EndZ=0
    g12: LineSegment StartX=8.5 StartY=4 StartZ=0 EndX=8.5 EndY=6 EndZ=0
    g13: LineSegment StartX=-3.5 StartY=4 StartZ=0 EndX=8.5 EndY=4 EndZ=0
  constraints (43):
    c: Horizontal(g0)
    c: Vertical(g1)
    c: DistanceY(g1) = 4
    c: Coincident(g2,g0)
    c: Coincident(g2,g3)
    c: Horizontal(g3)
    c: Radius(g2) = 2
    c: DistanceY(g2) = 7.5
    c: Symmetric(g0,g2,g-2)
    c: Horizontal(g4)
    c: Coincident(g4,g5)
    c: Vertical(g5)
    c: Coincident(g5,g6)
    c: Horizontal(g6)
    c: Coincident(g6,g7)
    c: Vertical(g7)
    c: Horizontal(g8)
    c: Coincident(g8,g9)
    c: Vertical(g9)
    c: Coincident(g9,g10)
    c: Horizontal(g10)
    c: Coincident(g10,g11)
    c: Vertical(g11)
    c: Coincident(g3,g11)
    c: Coincident(g0,g7)
    c: Coincident(g1,g4)
    c: DistanceY(g3) = 6
    c: DistanceY(g6,g0) = 0.5
    c: DistanceX(g4,g4) = 0.3
    c: DistanceX(g6,g6) = 0.3
    c: DistanceY(g5,g4) = 0.2
    c: Vertical(g12)
    c: Equal(g11,g7)
    c: DistanceY(g1,g0) = 2
    c: DistanceX(g8,g8) = 5.3
    c: Coincident(g13,g1)
    c: Coincident(g13,g12)
    c: Horizontal(g13)
    c: DistanceX(g13,g13) = 12
    c: DistanceX(g1,g2) = 3.5
    c: Coincident(g8,g12)
    c: Equal(g7,g9)
    c: Equal(g6,g10)
FEATURE [PartDesign::Revolution] Revolution016
  Angle = 360
  Axis = (1,0,0)
  Base = (0,0,0)
  Profile = -> Sketch049
  ReferenceAxis = -> X_Axis068
FEATURE [PartDesign::Fillet] Fillet158
  Base = -> Revolution016 [Edge13,Edge11]
  BaseFeature = -> Revolution016
  Radius = 0.2
  SupportTransform = false
FEATURE [PartDesign::Body] Body054  label="Inner Ring002"
  Group = -> [Sketch049,Revolution016,Fillet158]
  Origin = -> Origin069
  Tip = -> Fillet158
FEATURE [App::DocumentObjectGroup] Group011  label="Rings001"
  Group = -> [Body053,Body054]
FEATURE [Sketcher::SketchObject] Sketch050
  FullyConstrained = true
  MapMode = 5
  Placement = pos=(0,0,0) rot=(1,0,0;1.5708rad)
  Support = -> [XZ_Plane069]
  sketch-geometry (12):
    g0: LineSegment StartX=2.9 StartY=9.5 StartZ=0 EndX=2.9 EndY=8.5 EndZ=0
    g1: LineSegment StartX=2.9 StartY=8.5 StartZ=0 EndX=3.2 EndY=8.5 EndZ=0
    g2: LineSegment StartX=3.2 StartY=8.5 StartZ=0 EndX=3.2 EndY=6.5 EndZ=0
    g3: LineSegment StartX=3.2 StartY=6.5 StartZ=0 EndX=2.9 EndY=6.5 EndZ=0
    g4: LineSegment StartX=2.9 StartY=6.5 StartZ=0 EndX=2.9 EndY=5.5 EndZ=0
    g5: LineSegment StartX=2.9 StartY=5.5 StartZ=0 EndX=3.2 EndY=5.5 EndZ=0
    g6: LineSegment StartX=3.2 StartY=5.5 StartZ=0 EndX=3.2 EndY=6 EndZ=0
    g7: LineSegment StartX=3.2 StartY=6 StartZ=0 EndX=3.5 EndY=6 EndZ=0
    g8: LineSegment StartX=3.5 StartY=6 StartZ=0 EndX=3.5 EndY=9 EndZ=0
    g9: LineSegment StartX=3.5 StartY=9 StartZ=0 EndX=3.2 EndY=9 EndZ=0
    g10: LineSegment StartX=3.2 StartY=9 StartZ=0 EndX=3.2 EndY=9.5 EndZ=0
    g11: LineSegment StartX=3.2 StartY=9.5 StartZ=0 EndX=2.9 EndY=9.5 EndZ=0
  constraints (36):
    c: Vertical(g0)
    c: Coincident(g0,g1)
    c: Horizontal(g1)
    c: Coincident(g1,g2)
    c: Vertical(g2)
    c: Coincident(g2,g3)
    c: Horizontal(g3)
    c: Coincident(g3,g4)
    c: Vertical(g4)
    c: Coincident(g4,g5)
    c: Horizontal(g5)
    c: Coincident(g5,g6)
    c: Vertical(g6)
    c: Coincident(g6,g7)
    c: Horizontal(g7)
    c: Coincident(g7,g8)
    c: Vertical(g8)
    c: Coincident(g8,g9)
    c: Horizontal(g9)
    c: Coincident(g9,g10)
    c: Vertical(g10)
    c: Coincident(g10,g11)
    c: Coincident(g11,g0)
    c: Horizontal(g11)
    c: DistanceY(g4) = 5.5
    c: DistanceX(g4) = 2.9
    c: DistanceY(g5,g6) = 0.5
    c: DistanceY(g6,g2) = 0.5
    c: DistanceX(g5,g5) = 0.3
    c: Equal(g5,g7)
    c: Equal(g7,g3)
    c: Equal(g3,g1)
    c: Equal(g1,g9)
    c: Equal(g4,g0)
    c: Equal(g6,g10)
    c: DistanceY(g4,g0) = 4
FEATURE [PartDesign::Revolution] Revolution017
  Angle = 360
  Axis = (1,0,0)
  Base = (0,0,0)
  Placement = pos=(0,0,0) rot=(1,0,0;1.5708rad)
  Profile = -> Sketch050
  ReferenceAxis = -> Sketch050 [H_Axis]
FEATURE [PartDesign::Fillet] Fillet159
  Base = -> Revolution017 [Edge14,Edge12]
  BaseFeature = -> Revolution017
  Placement = pos=(0,0,0) rot=(1,0,0;1.5708rad)
  Radius = 0.2
  SupportTransform = false
FEATURE [PartDesign::Body] Body055  label="Seal 003"
  Group = -> [Sketch050,Revolution017,Fillet159]
  Origin = -> Origin070
  Tip = -> Fillet159
FEATURE [PartDesign::FeatureBase] Clone027
  BaseFeature = -> Body055
FEATURE [PartDesign::Body] Body056  label="Seal 004"
  BaseFeature = -> Body055
  Group = -> [Clone027]
  Origin = -> Origin071
  Placement = pos=(0,0,0) rot=(0,1,0;3.14159rad)
  Tip = -> Clone027
FEATURE [App::DocumentObjectGroup] Group010  label="Seals001"
  Group = -> [Body055,Body056]
FEATURE [Sketcher::SketchObject] Sketch051
  AttachmentOffset = pos=(0,0,4) rot=(0,0,1;0rad)
  FullyConstrained = true
  MapMode = 5
  Placement = pos=(0,0,4) rot=(0,0,1;0rad)
  Support = -> [XY_Plane050]
  sketch-geometry (1):
    g0: Circle CenterX=6 CenterY=0 CenterZ=0 NormalX=0 NormalY=0 NormalZ=1 AngleXU=0 Radius=1.5
  constraints (3):
    c: PointOnObject(g0,g-1)
    c: Diameter(g0) = 3
    c: DistanceX(g-1,g0) = 6
FEATURE [PartDesign::Pad] Pad016
  Direction = (0,0,1)
  Length = 3
  Length2 = 100
  Profile = -> Sketch051
  Type = 0
FEATURE [Sketcher::SketchObject] Sketch052
  ExternalGeometry = -> [Pad016]
  FullyConstrained = true
  MapMode = 5
  Placement = pos=(0,0,7) rot=(0,0,1;0rad)
  Support = -> [Pad016]
  sketch-geometry (7):
    g0: LineSegment StartX=6.43301 StartY=-0.75 StartZ=0 EndX=6.86603 EndY=0 EndZ=0
    g1: LineSegment StartX=6.86603 StartY=0 StartZ=0 EndX=6.43301 EndY=0.75 EndZ=0
    g2: LineSegment StartX=6.43301 StartY=0.75 StartZ=0 EndX=5.56699 EndY=0.75 EndZ=0
    g3: LineSegment StartX=5.56699 StartY=0.75 StartZ=0 EndX=5.13397 EndY=-1e-16 EndZ=0
    g4: LineSegment StartX=5.13397 StartY=-1e-16 StartZ=0 EndX=5.56699 EndY=-0.75 EndZ=0
    g5: LineSegment StartX=5.56699 StartY=-0.75 StartZ=0 EndX=6.43301 EndY=-0.75 EndZ=0
    g6: Circle CenterX=6 CenterY=0 CenterZ=0 NormalX=0 NormalY=0 NormalZ=1 AngleXU=0 Radius=0.866025
  constraints (16):
    c: Coincident(g0,g1)
    c: Coincident(g1,g2)
    c: Coincident(g2,g3)
    c: Coincident(g3,g4)
    c: Coincident(g4,g5)
    c: Coincident(g5,g0)
    c: Equal(g0, g1-g5) x5
    c: PointOnObject(g0,g6)
    c: PointOnObject(g1,g6)
    c: PointOnObject(g2,g6)
    c: PointOnObject(g3,g6)
    c: PointOnObject(g4,g6)
    c: PointOnObject(g5,g6)
    c: Coincident(g6,g-3)
    c: Horizontal(g5)
    c: DistanceY(g4,g2) = 1.5
FEATURE [PartDesign::Pocket] Pocket012
  BaseFeature = -> Pad016
  Length = 0.9
  Length2 = 100
  Profile = -> Sketch052
  Type = 0
FEATURE [PartDesign::PolarPattern] PolarPattern007
  Angle = 120
  Axis = -> X_Axis050
  BaseFeature = -> Pocket012
  Occurrences = 3
  Originals = -> [Pad016,Pocket012]
FEATURE [PartDesign::Body] Body036
  Group = -> [Sketch051,Pad016,Sketch052,Pocket012,PolarPattern007]
  Origin = -> Origin051
  Tip = -> PolarPattern007
FEATURE [App::DocumentObjectGroup] Group012  label="Set screws001"
  Group = -> [Body036]
FEATURE [Sketcher::SketchObject] Sketch053
  AttachmentOffset = pos=(0,0,-6.5) rot=(0,0,1;0rad)
  FullyConstrained = true
  MapMode = 5
  Placement = pos=(-6.5,1.4e-15,-1.4e-15) rot=(0.57735,0.57735,0.57735;2.0944rad)
  Support = -> [YZ_Plane071]
  sketch-geometry (14):
    g0: Circle CenterX=0 CenterY=0 CenterZ=0 NormalX=0 NormalY=0 NormalZ=1 AngleXU=0 Radius=11
    g1: ArcOfCircle CenterX=0 CenterY=0 CenterZ=0 NormalX=0 NormalY=0 NormalZ=1 AngleXU=0 Radius=13.5 StartAngle=0.0668757 EndAngle=3.07472
    g2: LineSegment StartX=-13.4698 StartY=0.902148 StartZ=0 EndX=-14.2 EndY=-10 EndZ=0
    g3: LineSegment StartX=-14.2 StartY=-10 StartZ=0 EndX=-27.5 EndY=-10 EndZ=0
    g4: LineSegment StartX=-27.5 StartY=-10 StartZ=0 EndX=-27.5 EndY=-15 EndZ=0
    g5: LineSegment StartX=-27.5 StartY=-15 StartZ=0 EndX=-12.3 EndY=-15 EndZ=0
    g6: LineSegment StartX=27.5 StartY=-15 StartZ=0 EndX=27.5 EndY=-10 EndZ=0
    g7: LineSegment StartX=27.5 StartY=-10 StartZ=0 EndX=14.2 EndY=-10 EndZ=0
    g8: LineSegment StartX=14.2 StartY=-10 StartZ=0 EndX=13.4698 EndY=0.902148 EndZ=0
    g9: LineSegment StartX=12.3 StartY=-15 StartZ=0 EndX=12.1995 EndY=-13.5 EndZ=0
    g10: LineSegment StartX=12.1995 StartY=-13.5 StartZ=0 EndX=-12.1995 EndY=-13.5 EndZ=0
    g11: LineSegment StartX=-12.1995 StartY=-13.5 StartZ=0 EndX=-12.3 EndY=-15 EndZ=0
    g12: LineSegment StartX=12.3 StartY=-15 StartZ=0 EndX=27.5 EndY=-15 EndZ=0
    g13: GeomPoint X=0 Y=13.5 Z=0
  constraints (39):
    c: Coincident(g0,g-1)
    c: Radius(g0) = 11
    c: Coincident(g1,g0)
    c: Coincident(g2,g3)
    c: Coincident(g3,g4)
    c: Coincident(g4,g5)
    c: Horizontal(g5)
    c: Coincident(g12,g6)
    c: Coincident(g6,g7)
    c: Horizontal(g7)
    c: Coincident(g7,g8)
    c: Coincident(g9,g10)
    c: Horizontal(g10)
    c: Coincident(g10,g11)
    c: Coincident(g5,g11)
    c: Coincident(g12,g9)
    c: Horizontal(g3)
    c: Vertical(g6)
    c: Vertical(g4)
    c: Equal(g9,g11)
    c: Horizontal(g12)
    c: Horizontal(g5,g9)
    c: Equal(g6,g4)
    c: Equal(g12,g5)
    c: Equal(g7,g3)
    c: DistanceX(g4,g6) = 55
    c: DistanceY(g6,g0) = 15
    c: Equal(g8,g2)
    c: DistanceY(g6,g6) = 5
    c: Parallel(g9,g8)
    c: DistanceY(g9,g9) = 1.5
    c: DistanceX(g5,g5) = 15.2
    c: Diameter(g1) = 27
    c: PointOnObject(g13,g1)
    c: PointOnObject(g13,g-2)
    c: DistanceY(g6,g13) = 28.5
    c: Tangent(g1,g2) = -1.5708
    c: Tangent(g1,g8) = -1.5708
    c: DistanceX(g3,g3) = 13.3
FEATURE [PartDesign::Pad] Pad017
  Direction = (1,-2e-16,3e-16)
  Length = 13
  Length2 = 100
  Placement = pos=(0,0,0) rot=(0.57735,0.57735,0.57735;2.0944rad)
  Profile = -> Sketch053
  Type = 0
FEATURE [Sketcher::SketchObject] Sketch054
  ExternalGeometry = -> [Pad017]
  FullyConstrained = true
  MapMode = 5
  Placement = pos=(4.2e-15,-6.6e-15,-15) rot=(0.707107,0.707107,0;3.14159rad)
  Support = -> [Pad017]
  sketch-geometry (7):
    g0: LineSegment StartX=-24.9 StartY=4.15 StartZ=0 EndX=-14.9 EndY=4.15 EndZ=0
    g1: LineSegment StartX=-14.9 StartY=4.15 StartZ=0 EndX=-14.9 EndY=-4.15 EndZ=0
    g2: LineSegment StartX=-14.9 StartY=-4.15 StartZ=0 EndX=-24.9 EndY=-4.15 EndZ=0
    g3: LineSegment StartX=-24.9 StartY=-4.15 StartZ=0 EndX=-24.9 EndY=4.15 EndZ=0
    g4: LineSegment StartX=-27.5 StartY=6.5 StartZ=0 EndX=-12.3 EndY=-6.5 EndZ=0
    g5: LineSegment StartX=-27.5 StartY=-6.5 StartZ=0 EndX=-12.3 EndY=6.5 EndZ=0
    g6: GeomPoint X=-19.9 Y=2.6e-15 Z=0
  constraints (17):
    c: Coincident(g0,g1)
    c: Coincident(g1,g2)
    c: Coincident(g2,g3)
    c: Coincident(g3,g0)
    c: Horizontal(g0)
    c: Horizontal(g2)
    c: Vertical(g1)
    c: Vertical(g3)
    c: DistanceX(g0,g0) = 10
    c: DistanceY(g1,g1) = 8.3
    c: Coincident(g4,g-3)
    c: Coincident(g4,g-4)
    c: Coincident(g5,g-4)
    c: Coincident(g5,g-3)
    c: PointOnObject(g6,g4)
    c: PointOnObject(g6,g5)
    c: Symmetric(g0,g1,g6)
FEATURE [PartDesign::Pocket] Pocket013
  BaseFeature = -> Pad017
  Length = 2.3
  Length2 = 100
  Placement = pos=(0,0,0) rot=(0.57735,0.57735,0.57735;2.0944rad)
  Profile = -> Sketch054
  Type = 0
FEATURE [Sketcher::SketchObject] Sketch055
  ExternalGeometry = -> [Pocket013]
  FullyConstrained = true
  MapMode = 5
  Placement = pos=(2.8e-15,-4.4e-15,-10) rot=(0,0,-1;1.5708rad)
  Support = -> [Pocket013]
  sketch-geometry (2):
    g0: Circle CenterX=21.2 CenterY=2.1e-15 CenterZ=0 NormalX=0 NormalY=0 NormalZ=1 AngleXU=0 Radius=2.5
    g1: LineSegment StartX=21.2 StartY=2.1e-15 StartZ=0 EndX=27.5 EndY=2.1e-15 EndZ=0
  constraints (5):
    c: Diameter(g0) = 5
    c: DistanceX(g0,g-3) = 6.3
    c: Coincident(g1,g0)
    c: Horizontal(g1)
    c: Symmetric(g-5,g-5,g1)
FEATURE [PartDesign::Pocket] Pocket014
  BaseFeature = -> Pocket013
  Length = 5
  Length2 = 100
  Placement = pos=(0,0,0) rot=(0.57735,0.57735,0.57735;2.0944rad)
  Profile = -> Sketch055
  Type = 2
FEATURE [Sketcher::SketchObject] Sketch056
  ExternalGeometry = -> [Pocket014]
  FullyConstrained = true
  MapMode = 5
  Placement = pos=(6.5,-1.4e-15,1.5e-15) rot=(0.57735,0.57735,0.57735;2.0944rad)
  Support = -> [Pocket014]
  sketch-geometry (6):
    g0: LineSegment StartX=-24.6 StartY=-13.7 StartZ=0 EndX=-24.6 EndY=-11.3 EndZ=0
    g1: LineSegment StartX=-24.6 StartY=-11.3 StartZ=0 EndX=-14.2 EndY=-11.3 EndZ=0
    g2: LineSegment StartX=-14.2 StartY=-11.3 StartZ=0 EndX=-14.2 EndY=-13.7 EndZ=0
    g3: LineSegment StartX=-14.2 StartY=-13.7 StartZ=0 EndX=-24.6 EndY=-13.7 EndZ=0
    g4: GeomPoint X=-19.4 Y=-12.5 Z=0
    g5: LineSegment StartX=-19.4 StartY=-12.5 StartZ=0 EndX=-27.5 EndY=-12.5 EndZ=0
  constraints (15):
    c: Coincident(g0,g1)
    c: Coincident(g1,g2)
    c: Coincident(g2,g3)
    c: Coincident(g3,g0)
    c: Horizontal(g1)
    c: Horizontal(g3)
    c: Vertical(g0)
    c: Vertical(g2)
    c: Symmetric(g1,g0,g4)
    c: DistanceX(g1,g1) = 10.4
    c: DistanceY(g2,g2) = 2.4
    c: DistanceX(g2,g-4) = 1.9
    c: Coincident(g5,g4)
    c: Horizontal(g5)
    c: Symmetric(g-5,g-5,g5)
FEATURE [PartDesign::Pocket] Pocket015
  BaseFeature = -> Pocket014
  Length = 0.4
  Length2 = 100
  Placement = pos=(0,0,0) rot=(0.57735,0.57735,0.57735;2.0944rad)
  Profile = -> Sketch056
  Type = 0
FEATURE [PartDesign::Mirrored] Mirrored001
  BaseFeature = -> Pocket015
  MirrorPlane = -> Sketch054 [V_Axis]
  Originals = -> [Pocket013,Pocket014,Pocket015]
  Placement = pos=(0,0,0) rot=(0.57735,0.57735,0.57735;2.0944rad)
FEATURE [Sketcher::SketchObject] Sketch057
  ExternalGeometry = -> [Mirrored001]
  FullyConstrained = true
  MapMode = 5
  Placement = pos=(0,0,0) rot=(1,0,0;1.5708rad)
  Support = -> [XZ_Plane071]
  sketch-geometry (9):
    g0: GeomPoint X=-6.5 Y=13.5 Z=0
    g1: LineSegment StartX=6.5 StartY=-10 StartZ=0 EndX=6.5 EndY=13.5 EndZ=0
    g2: LineSegment StartX=6.5 StartY=13.5 StartZ=0 EndX=4.75 EndY=13.5 EndZ=0
    g3: LineSegment StartX=-6.5 StartY=13.5 StartZ=0 EndX=-4.75 EndY=13.5 EndZ=0
    g4: LineSegment StartX=-6.5 StartY=-10 StartZ=0 EndX=-6.5 EndY=13.5 EndZ=0
    g5: LineSegment StartX=6.5 StartY=-10 StartZ=0 EndX=4.75 EndY=-1 EndZ=0
    g6: LineSegment StartX=4.75 StartY=-1 StartZ=0 EndX=4.75 EndY=13.5 EndZ=0
    g7: LineSegment StartX=-4.75 StartY=13.5 StartZ=0 EndX=-4.75 EndY=-1 EndZ=0
    g8: LineSegment StartX=-4.75 StartY=-1 StartZ=0 EndX=-6.5 EndY=-10 EndZ=0
  constraints (24):
    c: Vertical(g0,g-4)
    c: Horizontal(g-3,g0)
    c: Coincident(g1,g-3)
    c: Coincident(g1,g2)
    c: Horizontal(g2)
    c: Coincident(g3,g0)
    c: Horizontal(g3)
    c: Coincident(g4,g3)
    c: Vertical(g4,g-4)
    c: DistanceX(g3,g2) = 9.5
    c: Equal(g2,g3)
    c: Horizontal(g1,g4)
    c: Coincident(g1,g-5)
    c: Coincident(g1,g5)
    c: Coincident(g5,g6)
    c: Coincident(g6,g2)
    c: Vertical(g6)
    c: DistanceY(g1,g5) = 9
    c: Coincident(g3,g7)
    c: Vertical(g7)
    c: Coincident(g7,g8)
    c: Coincident(g8,g4)
    c: Horizontal(g7,g5)
    c: DistanceX(g2,g2) = 1.75
FEATURE [PartDesign::Pocket] Pocket016
  BaseFeature = -> Mirrored001
  Length = 15
  Length2 = 15
  Placement = pos=(0,0,0) rot=(0.57735,0.57735,0.57735;2.0944rad)
  Profile = -> Sketch057
  Type = 4
FEATURE [Sketcher::SketchObject] Sketch058
  FullyConstrained = true
  MapMode = 5
  Placement = pos=(-6.5,1.4e-15,-1.5e-15) rot=(0.57735,0.57735,-0.57735;4.18879rad)
  Support = -> [Pocket016]
  sketch-geometry (1):
    g0: Circle CenterX=0 CenterY=0 CenterZ=0 NormalX=0 NormalY=0 NormalZ=1 AngleXU=0 Radius=12.2
  constraints (2):
    c: Coincident(g0,g-1)
    c: Diameter(g0) = 24.4
FEATURE [PartDesign::Pocket] Pocket017
  BaseFeature = -> Pocket016
  Length = 2.75
  Length2 = 100
  Placement = pos=(0,0,0) rot=(0.57735,0.57735,0.57735;2.0944rad)
  Profile = -> Sketch058
  Type = 0
FEATURE [Sketcher::SketchObject] Sketch059
  FullyConstrained = true
  MapMode = 5
  Placement = pos=(6.5,-1.4e-15,1.5e-15) rot=(0.57735,0.57735,0.57735;2.0944rad)
  Support = -> [Pocket017]
  sketch-geometry (1):
    g0: Circle CenterX=0 CenterY=0 CenterZ=0 NormalX=0 NormalY=0 NormalZ=1 AngleXU=0 Radius=12.1
  constraints (2):
    c: Coincident(g0,g-1)
    c: Diameter(g0) = 24.2
FEATURE [PartDesign::Pocket] Pocket018
  BaseFeature = -> Pocket017
  Length = 2.75
  Length2 = 100
  Placement = pos=(0,0,0) rot=(0.57735,0.57735,0.57735;2.0944rad)
  Profile = -> Sketch059
  Type = 0
FEATURE [Sketcher::SketchObject] Sketch060
  ExternalGeometry = -> [Pocket018]
  FullyConstrained = true
  MapMode = 5
  Placement = pos=(6.5,-1.4e-15,1.5e-15) rot=(0.57735,0.57735,0.57735;2.0944rad)
  Support = -> [Pocket018]
  sketch-geometry (6):
    g0: ArcOfCircle CenterX=0 CenterY=0 CenterZ=0 NormalX=0 NormalY=0 NormalZ=1 AngleXU=0 Radius=13.5 StartAngle=3.79664 EndAngle=5.62814
    g1: LineSegment StartX=-11.8698 StartY=-8.57666 StartZ=0 EndX=-12.3 EndY=-15 EndZ=0
    g2: LineSegment StartX=-12.3 StartY=-15 StartZ=0 EndX=12.3 EndY=-15 EndZ=0
    g3: LineSegment StartX=12.3 StartY=-15 StartZ=0 EndX=11.8698 EndY=-8.57666 EndZ=0
    g4: ArcOfCircle CenterX=11.2212 CenterY=-8.6201 CenterZ=0 NormalX=0 NormalY=0 NormalZ=1 AngleXU=0 Radius=0.65 StartAngle=0.0668757 EndAngle=2.48655
    g5: ArcOfCircle CenterX=-11.2212 CenterY=-8.6201 CenterZ=0 NormalX=0 NormalY=0 NormalZ=1 AngleXU=0 Radius=0.65 StartAngle=0.655044 EndAngle=3.07472
  constraints (14):
    c: Coincident(g0,g-1)
    c: Diameter(g0) = 27
    c: Coincident(g1,g2)
    c: Coincident(g2,g3)
    c: Coincident(g1,g-3)
    c: Coincident(g2,g-4)
    c: Tangent(g3,g4) = -1.5708
    c: Tangent(g0,g4) = 1.5708
    c: Tangent(g0,g5) = 1.5708
    c: Tangent(g1,g5) = -1.5708
    c: Equal(g4,g5)
    c: Horizontal(g4,g5)
    c: Parallel(g-4,g3)
    c: Radius(g4) = 0.65
FEATURE [PartDesign::Pocket] Pocket019
  BaseFeature = -> Pocket018
  Length = 5.25
  Length2 = 100
  Placement = pos=(0,0,0) rot=(0.57735,0.57735,0.57735;2.0944rad)
  Profile = -> Sketch060
  Type = 0
FEATURE [Sketcher::SketchObject] Sketch061
  ExternalGeometry = -> [Pocket019]
  FullyConstrained = true
  MapMode = 5
  Placement = pos=(-6.5,1.4e-15,-1.5e-15) rot=(0.57735,0.57735,-0.57735;4.18879rad)
  Support = -> [Pocket019]
  sketch-geometry (6):
    g0: ArcOfCircle CenterX=0 CenterY=0 CenterZ=0 NormalX=0 NormalY=0 NormalZ=1 AngleXU=0 Radius=13.5 StartAngle=0.655044 EndAngle=2.48655
    g1: LineSegment StartX=11.8698 StartY=8.57666 StartZ=0 EndX=12.3 EndY=15 EndZ=0
    g2: LineSegment StartX=12.3 StartY=15 StartZ=0 EndX=-12.3 EndY=15 EndZ=0
    g3: LineSegment StartX=-12.3 StartY=15 StartZ=0 EndX=-11.8698 EndY=8.57666 EndZ=0
    g4: ArcOfCircle CenterX=-11.2212 CenterY=8.6201 CenterZ=0 NormalX=0 NormalY=0 NormalZ=1 AngleXU=0 Radius=0.65 StartAngle=3.20847 EndAngle=5.62814
    g5: ArcOfCircle CenterX=11.2212 CenterY=8.6201 CenterZ=0 NormalX=0 NormalY=0 NormalZ=1 AngleXU=0 Radius=0.65 StartAngle=3.79664 EndAngle=6.21631
  constraints (14):
    c: Coincident(g0,g-1)
    c: Radius(g0) = 13.5
    c: Coincident(g1,g2)
    c: Coincident(g2,g-3)
    c: Coincident(g2,g3)
    c: Coincident(g-4,g1)
    c: Tangent(g3,g4) = -1.5708
    c: Tangent(g0,g4) = 1.5708
    c: Tangent(g0,g5) = 1.5708
    c: Tangent(g1,g5) = -1.5708
    c: Equal(g4,g5)
    c: Radius(g4) = 0.65
    c: Parallel(g-4,g1)
    c: Parallel(g3,g-3)
FEATURE [PartDesign::Pocket] Pocket020
  BaseFeature = -> Pocket019
  Length = 5.25
  Length2 = 100
  Placement = pos=(0,0,0) rot=(0.57735,0.57735,0.57735;2.0944rad)
  Profile = -> Sketch061
  Type = 0
FEATURE [PartDesign::Chamfer] Chamfer001
  Angle = 45
  Base = -> Pocket020 [Edge159,Edge155,Edge22,Edge27]
  BaseFeature = -> Pocket020
  ChamferType = 0
  FlipDirection = false
  Placement = pos=(0,0,0) rot=(0.57735,0.57735,0.57735;2.0944rad)
  Size = 2
  Size2 = 1
  SupportTransform = false
FEATURE [Sketcher::SketchObject] Sketch062
  ExternalGeometry = -> [Chamfer001]
  FullyConstrained = true
  MapMode = 5
  Placement = pos=(-3.75,5e-15,-2.7e-15) rot=(-0.57735,-0.57735,0.57735;2.0944rad)
  Support = -> [Chamfer001]
  sketch-geometry (13):
    g0: ArcOfCircle CenterX=-6.9e-15 CenterY=-3.7e-15 CenterZ=0 NormalX=0 NormalY=0 NormalZ=1 AngleXU=0 Radius=11 StartAngle=5.75419 EndAngle=6.81218
    g1: ArcOfCircle CenterX=-6.9e-15 CenterY=-3.7e-15 CenterZ=0 NormalX=0 NormalY=0 NormalZ=1 AngleXU=0 Radius=12.2 StartAngle=5.94045 EndAngle=6.62592
    g2: ArcOfCircle CenterX=-6.9e-15 CenterY=-3.7e-15 CenterZ=0 NormalX=0 NormalY=0 NormalZ=1 AngleXU=0 Radius=11 StartAngle=2.6126 EndAngle=3.67059
    g3: ArcOfCircle CenterX=-6.9e-15 CenterY=-3.7e-15 CenterZ=0 NormalX=0 NormalY=0 NormalZ=1 AngleXU=0 Radius=12.2 StartAngle=2.79886 EndAngle=3.48433
    g4: Ellipse CenterX=-6.9e-15 CenterY=-3.7e-15 CenterZ=0 NormalX=0 NormalY=0 NormalZ=1 MajorRadius=13.5 MinorRadius=7.81051 AngleXU=-3e-16
    g5: LineSegment StartX=13.5 StartY=-7.4e-15 StartZ=0 EndX=-13.5 EndY=0 EndZ=0
    g6: LineSegment StartX=-4.8e-15 StartY=7.81051 StartZ=0 EndX=-9.1e-15 EndY=-7.81051 EndZ=0
    g7: GeomPoint X=11.0112 Y=-6.8e-15 Z=0
    g8: GeomPoint X=-11.0112 Y=-7e-16 Z=0
    g9: LineSegment StartX=-11.4904 StartY=4.1 StartZ=0 EndX=-9.49645 EndY=5.55135 EndZ=0
    g10: LineSegment StartX=-11.4904 StartY=-4.1 StartZ=0 EndX=-9.49645 EndY=-5.55135 EndZ=0
    g11: LineSegment StartX=9.49645 StartY=-5.55135 StartZ=0 EndX=11.4904 EndY=-4.1 EndZ=0
    g12: LineSegment StartX=11.4904 StartY=4.1 StartZ=0 EndX=9.49645 EndY=5.55135 EndZ=0
  constraints (29):
    c: Coincident(g0,g-4)
    c: PointOnObject(g0,g-4)
    c: Coincident(g1,g0)
    c: PointOnObject(g1,g-3)
    c: Coincident(g2,g0)
    c: PointOnObject(g2,g-4)
    c: Coincident(g3,g0)
    c: PointOnObject(g3,g-3)
    c: InternalAlignment(g5-g8 -> g4) x4
    c: Coincident(g4,g0)
    c: PointOnObject(g3,g4)
    c: PointOnObject(g2,g4)
    c: PointOnObject(g3,g4)
    c: PointOnObject(g2,g4)
    c: PointOnObject(g0,g4)
    c: PointOnObject(g1,g4)
    c: PointOnObject(g1,g4)
    c: PointOnObject(g0,g4)
    c: PointOnObject(g5,g-1)
    c: DistanceX(g5,g5) = 27
    c: DistanceY(g3,g3) = 8.2
    c: Coincident(g9,g3)
    c: Coincident(g9,g2)
    c: Coincident(g10,g3)
    c: Coincident(g10,g2)
    c: Coincident(g11,g0)
    c: Coincident(g11,g1)
    c: Coincident(g12,g1)
    c: Coincident(g12,g0)
FEATURE [PartDesign::Pocket] Pocket021
  BaseFeature = -> Chamfer001
  Length = 5
  Length2 = 100
  Placement = pos=(0,0,0) rot=(0.57735,0.57735,0.57735;2.0944rad)
  Profile = -> Sketch062
  Type = 0
FEATURE [PartDesign::Body] Body057  label="Metal case001"
  Group = -> [Sketch053,Pad017,Sketch054,Pocket013,Sketch055,Pocket014,Sketch056,Pocket015,Mirrored001,Sketch057,Pocket016,Sketch058,Pocket017,Sketch059,Pocket018,Sketch060,Pocket019,Sketch061,Pocket020,Chamfer001,Sketch062,Pocket021]
  Origin = -> Origin072
  Tip = -> Pocket021
FEATURE [App::DocumentObjectGroup] Group013  label="Case001"
  Group = -> [Body057]
FEATURE [App::Part] Part015  label="KP08-002"
  Group = -> [Group007,Body038,Body037,Body042,Body039,Body043,Body041,Body040,Group008,Body045,Body044,Group009,Body050,Body049,Body052,Body048,Body051,Body047,Body046,Group010,Body056,Body055,Group011,Body053,Body054,Group012,Body036,Group013,Body057]
  Origin = -> Origin073
  Placement = pos=(10,120,105) rot=(0,0,1;0rad)
FEATURE [Sketcher::SketchObject] Sketch063
  FullyConstrained = true
  MapMode = 5
  Placement = pos=(0,0,0) rot=(-0.57735,0.57735,0.57735;4.18879rad)
  Support = -> [YZ_Plane080]
  sketch-geometry (1):
    g0: Circle CenterX=0 CenterY=-7.5 CenterZ=0 NormalX=0 NormalY=0 NormalZ=1 AngleXU=0 Radius=0.25
  constraints (3):
    c: PointOnObject(g0,g-2)
    c: DistanceY(g0) = -7.5
    c: Diameter(g0) = 0.5
FEATURE [Sketcher::SketchObject] Sketch064
  FullyConstrained = true
  MapMode = 5
  Support = -> [XY_Plane073]
  sketch-geometry (2):
    g0: LineSegment StartX=0 StartY=5.5 StartZ=0 EndX=6e-16 EndY=9.5 EndZ=0
    g1: ArcOfCircle CenterX=0 CenterY=7.5 CenterZ=0 NormalX=0 NormalY=0 NormalZ=1 AngleXU=0 Radius=2 StartAngle=4.71239 EndAngle=7.85398
  constraints (7):
    c: PointOnObject(g0,g-2)
    c: PointOnObject(g0,g-2)
    c: PointOnObject(g1,g0)
    c: Coincident(g1,g0)
    c: Coincident(g1,g0)
    c: Radius(g1) = 2
    c: DistanceY(g1) = 7.5
FEATURE [PartDesign::Revolution] Revolution018
  Angle = 360
  Axis = (0,1,0)
  Base = (0,0,0)
  Profile = -> Sketch064
  ReferenceAxis = -> Sketch064 [V_Axis]
  Reversed = true
FEATURE [PartDesign::Body] Body059  label="Ball 015"
  Group = -> [Sketch064,Revolution018]
  Origin = -> Origin075
  Tip = -> Revolution018
FEATURE [PartDesign::FeatureBase] Clone028
  BaseFeature = -> Body059
FEATURE [PartDesign::Body] Body060  label="Ball 016"
  BaseFeature = -> Body059
  Group = -> [Clone028]
  Origin = -> Origin076
  Placement = pos=(0,0,0) rot=(-1,0,0;0.897598rad)
  Tip = -> Clone028
FEATURE [PartDesign::FeatureBase] Clone029
  BaseFeature = -> Body059
FEATURE [PartDesign::Body] Body061  label="Ball 017"
  BaseFeature = -> Body059
  Group = -> [Clone029]
  Origin = -> Origin077
  Placement = pos=(0,0,0) rot=(-1,0,0;1.7952rad)
  Tip = -> Clone029
FEATURE [PartDesign::FeatureBase] Clone030
  BaseFeature = -> Body059
FEATURE [PartDesign::Body] Body062  label="Ball 018"
  BaseFeature = -> Body059
  Group = -> [Clone030]
  Origin = -> Origin078
  Placement = pos=(0,0,0) rot=(1,0,0;3.59039rad)
  Tip = -> Clone030
FEATURE [PartDesign::FeatureBase] Clone031
  BaseFeature = -> Body059
FEATURE [PartDesign::Body] Body063  label="Ball 019"
  BaseFeature = -> Body059
  Group = -> [Clone031]
  Origin = -> Origin079
  Placement = pos=(0,0,0) rot=(1,0,0;2.69279rad)
  Tip = -> Clone031
FEATURE [PartDesign::FeatureBase] Clone032
  BaseFeature = -> Body059
FEATURE [PartDesign::Body] Body064  label="Ball 020"
  BaseFeature = -> Body059
  Group = -> [Clone032]
  Origin = -> Origin080
  Placement = pos=(0,0,0) rot=(1,0,0;1.7952rad)
  Tip = -> Clone032
FEATURE [PartDesign::FeatureBase] Clone033
  BaseFeature = -> Body059
FEATURE [PartDesign::Body] Body065  label="Ball 021"
  BaseFeature = -> Body059
  Group = -> [Clone033]
  Origin = -> Origin081
  Placement = pos=(0,0,0) rot=(1,0,0;0.897598rad)
  Tip = -> Clone033
FEATURE [App::DocumentObjectGroup] Group014  label="Balls002"
  Group = -> [Body059,Body060,Body061,Body062,Body063,Body064,Body065]
FEATURE [Sketcher::SketchObject] Sketch065
  FullyConstrained = true
  MapMode = 5
  Support = -> [XY_Plane082]
  sketch-geometry (7):
    g0: LineSegment StartX=-5 StartY=7.5 StartZ=0 EndX=5 EndY=7.5 EndZ=0
    g1: LineSegment StartX=-0.210977 StartY=7.5 StartZ=0 EndX=0.210977 EndY=7.5 EndZ=0
    g2: ArcOfCircle CenterX=0.25 CenterY=7.5 CenterZ=0 NormalX=0 NormalY=0 NormalZ=1 AngleXU=0 Radius=0.460977 StartAngle=2.43297 EndAngle=3.14159
    g3: ArcOfCircle CenterX=-0.25 CenterY=7.5 CenterZ=0 NormalX=0 NormalY=0 NormalZ=1 AngleXU=0 Radius=0.460977 StartAngle=9.792e-13 EndAngle=0.708626
    g4: LineSegment StartX=-0.1 StartY=7.8 StartZ=0 EndX=-0.1 EndY=7.75 EndZ=0
    g5: LineSegment StartX=-0.1 StartY=7.75 StartZ=0 EndX=0.1 EndY=7.75 EndZ=0
    g6: LineSegment StartX=0.1 StartY=7.75 StartZ=0 EndX=0.1 EndY=7.8 EndZ=0
  constraints (22):
    c: DistanceY(g-1,g0) = 7.5
    c: Symmetric(g0,g0,g-2)
    c: DistanceX(g0,g0) = 10
    c: PointOnObject(g1,g0)
    c: PointOnObject(g1,g0)
    c: Coincident(g3,g1)
    c: Coincident(g2,g1)
    c: Coincident(g2,g4)
    c: Coincident(g4,g5)
    c: Horizontal(g5)
    c: Coincident(g5,g6)
    c: Coincident(g6,g3)
    c: Vertical(g6)
    c: Equal(g3,g2)
    c: Vertical(g4)
    c: Symmetric(g2,g3,g-2)
    c: DistanceX(g5,g5) = 0.2
    c: Distance(g5,g1) = 0.25
    c: DistanceX(g3,g-1) = 0.25
    c: PointOnObject(g3,g1)
    c: PointOnObject(g2,g1)
    c: Distance(g3,g1) = 0.3
FEATURE [PartDesign::Revolution] Revolution019
  Angle = 360
  Axis = (10,0,0)
  Base = (-5,7.5,0)
  Profile = -> Sketch065
  ReferenceAxis = -> Sketch065 [Axis]
FEATURE [PartDesign::Body] Body068  label="Rivet 015"
  Group = -> [Sketch065,Revolution019]
  Origin = -> Origin084
  Placement = pos=(0,0,0) rot=(1,0,0;0.448799rad)
  Tip = -> Revolution019
FEATURE [PartDesign::FeatureBase] Clone035
  BaseFeature = -> Body068
  Placement = pos=(0,0,0) rot=(1,0,0;0.448799rad)
FEATURE [PartDesign::Body] Body069  label="Rivet 016"
  BaseFeature = -> Body068
  Group = -> [Clone035]
  Origin = -> Origin085
  Placement = pos=(0,0,0) rot=(1,0,0;0.897598rad)
  Tip = -> Clone035
FEATURE [PartDesign::FeatureBase] Clone036
  BaseFeature = -> Body068
  Placement = pos=(0,0,0) rot=(1,0,0;0.448799rad)
FEATURE [PartDesign::Body] Body070  label="Rivet 017"
  BaseFeature = -> Body068
  Group = -> [Clone036]
  Origin = -> Origin086
  Placement = pos=(0,0,0) rot=(1,0,0;1.7952rad)
  Tip = -> Clone036
FEATURE [PartDesign::FeatureBase] Clone037
  BaseFeature = -> Body068
  Placement = pos=(0,0,0) rot=(1,0,0;0.448799rad)
FEATURE [PartDesign::Body] Body071  label="Rivet 018"
  BaseFeature = -> Body068
  Group = -> [Clone037]
  Origin = -> Origin087
  Placement = pos=(0,0,0) rot=(1,0,0;2.69279rad)
  Tip = -> Clone037
FEATURE [PartDesign::FeatureBase] Clone038
  BaseFeature = -> Body068
  Placement = pos=(0,0,0) rot=(1,0,0;0.448799rad)
FEATURE [PartDesign::Body] Body072  label="Rivet 019"
  BaseFeature = -> Body068
  Group = -> [Clone038]
  Origin = -> Origin088
  Placement = pos=(0,0,0) rot=(1,0,0;3.59039rad)
  Tip = -> Clone038
FEATURE [PartDesign::FeatureBase] Clone039
  BaseFeature = -> Body068
  Placement = pos=(0,0,0) rot=(1,0,0;0.448799rad)
FEATURE [PartDesign::Body] Body073  label="Rivet 020"
  BaseFeature = -> Body068
  Group = -> [Clone039]
  Origin = -> Origin089
  Placement = pos=(0,0,0) rot=(-1,0,0;1.7952rad)
  Tip = -> Clone039
FEATURE [PartDesign::FeatureBase] Clone040
  BaseFeature = -> Body068
  Placement = pos=(0,0,0) rot=(1,0,0;0.448799rad)
FEATURE [PartDesign::Body] Body074  label="Rivet 021"
  BaseFeature = -> Body068
  Group = -> [Clone040]
  Origin = -> Origin090
  Placement = pos=(0,0,0) rot=(-1,0,0;0.897598rad)
  Tip = -> Clone040
FEATURE [App::DocumentObjectGroup] Group016  label="Rivets002"
  Group = -> [Body068,Body069,Body070,Body071,Body072,Body073,Body074]
FEATURE [Sketcher::SketchObject] Sketch066
  FullyConstrained = true
  MapMode = 5
  Placement = pos=(0,0,0) rot=(1,0,0;1.5708rad)
  Support = -> [XZ_Plane080]
  sketch-geometry (4):
    g0: LineSegment StartX=0 StartY=8.5 StartZ=0 EndX=0.1 EndY=8.5 EndZ=0
    g1: LineSegment StartX=0.1 StartY=8.5 StartZ=0 EndX=0.1 EndY=6.5 EndZ=0
    g2: LineSegment StartX=0.1 StartY=6.5 StartZ=0 EndX=0 EndY=6.5 EndZ=0
    g3: LineSegment StartX=0 StartY=6.5 StartZ=0 EndX=0 EndY=8.5 EndZ=0
  constraints (12):
    c: Coincident(g0,g1)
    c: Coincident(g1,g2)
    c: Coincident(g2,g3)
    c: Coincident(g3,g0)
    c: Horizontal(g0)
    c: Horizontal(g2)
    c: Vertical(g1)
    c: Vertical(g3)
    c: PointOnObject(g0,g-2)
    c: DistanceX(g0,g0) = 0.1
    c: DistanceY(g0) = 8.5
    c: DistanceY(g1) = 6.5
FEATURE [PartDesign::Revolution] Revolution020
  Angle = 360
  Axis = (1,0,0)
  Base = (0,0,0)
  Placement = pos=(0,0,0) rot=(1,0,0;1.5708rad)
  Profile = -> Sketch066
  ReferenceAxis = -> Sketch066 [H_Axis]
FEATURE [Sketcher::SketchObject] Sketch067
  FullyConstrained = true
  MapMode = 5
  Placement = pos=(0,0,0) rot=(0.57735,0.57735,0.57735;2.0944rad)
  Support = -> [YZ_Plane080]
  sketch-geometry (5):
    g0: ArcOfCircle CenterX=0 CenterY=7.5 CenterZ=0 NormalX=0 NormalY=0 NormalZ=1 AngleXU=0 Radius=2.11 StartAngle=5.66076 EndAngle=6.65667
    g1: LineSegment StartX=5e-16 StartY=8.5 StartZ=0 EndX=0 EndY=6.26986 EndZ=0
    g2: ArcOfCircle CenterX=0 CenterY=0 CenterZ=0 NormalX=0 NormalY=0 NormalZ=1 AngleXU=0 Radius=6.5 StartAngle=1.3039 EndAngle=1.5708
    g3: LineSegment StartX=1.71431 StartY=6.26986 StartZ=0 EndX=0 EndY=6.26986 EndZ=0
    g4: ArcOfCircle CenterX=0 CenterY=0 CenterZ=0 NormalX=0 NormalY=0 NormalZ=1 AngleXU=0 Radius=8.5 StartAngle=1.33757 EndAngle=1.5708
  constraints (16):
    c: PointOnObject(g0,g-2)
    c: DistanceY(g0) = 7.5
    c: Radius(g0) = 2.11
    c: PointOnObject(g2,g1)
    c: DistanceY(g2) = 6.5
    c: Coincident(g2,g-1)
    c: Coincident(g3,g2)
    c: Horizontal(g3)
    c: Coincident(g0,g2)
    c: Coincident(g1,g3)
    c: PointOnObject(g1,g-2)
    c: PointOnObject(g1,g-2)
    c: Coincident(g4,g-1)
    c: Coincident(g4,g1)
    c: DistanceY(g1) = 8.5
    c: Coincident(g0,g4)
FEATURE [PartDesign::Revolution] Revolution021
  Angle = 180
  Axis = (-2e-16,3e-16,1)
  Base = (0,0,0)
  BaseFeature = -> Revolution020
  Placement = pos=(0,0,0) rot=(1,0,0;1.5708rad)
  Profile = -> Sketch067
  ReferenceAxis = -> Sketch067 [V_Axis]
  Reversed = true
FEATURE [PartDesign::PolarPattern] PolarPattern008
  Angle = 360
  Axis = -> Sketch067 [N_Axis]
  BaseFeature = -> Revolution021
  Occurrences = 3
  Originals = -> [Revolution021]
  Placement = pos=(0,0,0) rot=(1,0,0;1.5708rad)
  Refine = true
FEATURE [Sketcher::SketchObject] Sketch068
  FullyConstrained = true
  MapMode = 5
  Placement = pos=(0,0,0) rot=(0.57735,0.57735,0.57735;2.0944rad)
  Support = -> [YZ_Plane080]
  sketch-geometry (4):
    g0: ArcOfCircle CenterX=0 CenterY=7.5 CenterZ=0 NormalX=0 NormalY=0 NormalZ=1 AngleXU=0 Radius=2.01 StartAngle=5.57985 EndAngle=6.86228
    g1: LineSegment StartX=0 StartY=6.2 StartZ=0 EndX=1.533 EndY=6.2 EndZ=0
    g2: LineSegment StartX=0 StartY=8.6 StartZ=0 EndX=0 EndY=6.2 EndZ=0
    g3: LineSegment StartX=0 StartY=8.6 StartZ=0 EndX=1.68229 EndY=8.6 EndZ=0
  constraints (13):
    c: PointOnObject(g0,g-2)
    c: DistanceY(g0) = 7.5
    c: Radius(g0) = 2.01
    c: PointOnObject(g1,g-2)
    c: Horizontal(g1)
    c: Coincident(g0,g1)
    c: DistanceY(g1) = 6.2
    c: DistanceY(g2) = 8.6
    c: Coincident(g2,g1)
    c: PointOnObject(g2,g-2)
    c: Coincident(g3,g2)
    c: Horizontal(g3)
    c: Coincident(g0,g3)
FEATURE [PartDesign::Groove] Groove002
  Angle = 360
  Axis = (-2e-16,3e-16,1)
  Base = (0,0,0)
  BaseFeature = -> PolarPattern008
  Placement = pos=(0,0,0) rot=(1,0,0;1.5708rad)
  Profile = -> Sketch068
  ReferenceAxis = -> Sketch068 [V_Axis]
FEATURE [PartDesign::PolarPattern] PolarPattern009
  Angle = 360
  Axis = -> Sketch068 [N_Axis]
  BaseFeature = -> Groove002
  Occurrences = 3
  Originals = -> [Groove002]
  Placement = pos=(0,0,0) rot=(1,0,0;1.5708rad)
FEATURE [PartDesign::Pocket] Pocket022
  BaseFeature = -> PolarPattern009
  Length = 5
  Length2 = 100
  Placement = pos=(0,0,0) rot=(1,0,0;1.5708rad)
  Profile = -> Sketch063
  Type = 1
FEATURE [PartDesign::PolarPattern] PolarPattern010
  Angle = 360
  Axis = -> Sketch063 [N_Axis]
  BaseFeature = -> Pocket022
  Occurrences = 3
  Originals = -> [Pocket022]
  Placement = pos=(0,0,0) rot=(1,0,0;1.5708rad)
FEATURE [PartDesign::Body] Body066  label="Cage 005"
  Group = -> [Sketch066,Revolution020,Sketch067,Revolution021,PolarPattern008,Sketch068,Groove002,PolarPattern009,Sketch063,Pocket022,PolarPattern010]
  Origin = -> Origin082
  Placement = pos=(0,0,0) rot=(-1,0,0;1.5708rad)
  Tip = -> PolarPattern010
FEATURE [PartDesign::FeatureBase] Clone034
  BaseFeature = -> Body066
  Placement = pos=(0,0,0) rot=(-1,0,0;1.5708rad)
FEATURE [PartDesign::Body] Body067  label="Cage 006"
  BaseFeature = -> Body066
  Group = -> [Clone034]
  Origin = -> Origin083
  Placement = pos=(0,0,0) rot=(0,1,0;3.14159rad)
  Tip = -> Clone034
FEATURE [App::DocumentObjectGroup] Group015  label="Cages002"
  Group = -> [Body066,Body067]
FEATURE [Sketcher::SketchObject] Sketch069
  FullyConstrained = true
  MapMode = 5
  Support = -> [XY_Plane089]
  sketch-geometry (14):
    g0: ArcOfCircle CenterX=-1e-16 CenterY=7.5 CenterZ=0 NormalX=0 NormalY=0 NormalZ=1 AngleXU=0 Radius=2 StartAngle=0.848062 EndAngle=2.29353
    g1: LineSegment StartX=-3.5 StartY=11 StartZ=0 EndX=3.5 EndY=11 EndZ=0
    g2: LineSegment StartX=3.5 StartY=11 StartZ=0 EndX=3.5 EndY=9.2 EndZ=0
    g3: LineSegment StartX=2.9 StartY=9 StartZ=0 EndX=1.32288 EndY=9 EndZ=0
    g4: LineSegment StartX=-3.5 StartY=9.2 StartZ=0 EndX=-3.5 EndY=11 EndZ=0
    g5: LineSegment StartX=-1.32288 StartY=9 StartZ=0 EndX=-2.9 EndY=9 EndZ=0
    g6: LineSegment StartX=2.9 StartY=9 StartZ=0 EndX=2.9 EndY=9.5 EndZ=0
    g7: LineSegment StartX=2.9 StartY=9.5 StartZ=0 EndX=3.2 EndY=9.5 EndZ=0
    g8: LineSegment StartX=3.2 StartY=9.5 StartZ=0 EndX=3.2 EndY=9.2 EndZ=0
    g9: LineSegment StartX=3.2 StartY=9.2 StartZ=0 EndX=3.5 EndY=9.2 EndZ=0
    g10: LineSegment StartX=-3.5 StartY=9.2 StartZ=0 EndX=-3.2 EndY=9.2 EndZ=0
    g11: LineSegment StartX=-3.2 StartY=9.2 StartZ=0 EndX=-3.2 EndY=9.5 EndZ=0
    g12: LineSegment StartX=-3.2 StartY=9.5 StartZ=0 EndX=-2.9 EndY=9.5 EndZ=0
    g13: LineSegment StartX=-2.9 StartY=9.5 StartZ=0 EndX=-2.9 EndY=9 EndZ=0
  constraints (41):
    c: Coincident(g1,g2)
    c: Coincident(g4,g1)
    c: Horizontal(g3)
    c: Vertical(g2)
    c: Vertical(g4)
    c: Coincident(g0,g5)
    c: Coincident(g0,g3)
    c: DistanceY(g-1,g0) = 7.5
    c: Radius(g0) = 2
    c: Symmetric(g1,g1,g-2)
    c: Symmetric(g0,g0,g-2)
    c: DistanceY(g1) = 11
    c: DistanceX(g1,g1) = 7
    c: Vertical(g6)
    c: Coincident(g6,g7)
    c: Horizontal(g7)
    c: Coincident(g7,g8)
    c: Vertical(g8)
    c: Coincident(g8,g9)
    c: Coincident(g3,g6)
    c: Coincident(g2,g9)
    c: Horizontal(g10)
    c: Coincident(g10,g11)
    c: Coincident(g11,g12)
    c: Horizontal(g12)
    c: Coincident(g12,g13)
    c: Vertical(g13)
    c: Vertical(g11)
    c: Coincident(g4,g10)
    c: Coincident(g5,g13)
    c: DistanceY(g13,g13) = 0.5
    c: DistanceX(g12,g12) = 0.3
    c: DistanceY(g5,g10) = 0.2
    c: Symmetric(g5,g3,g-2)
    c: DistanceY(g3) = 9
    c: DistanceY(g6) = 9.5
    c: Equal(g7,g12)
    c: Equal(g13,g6)
    c: Horizontal(g9)
    c: Horizontal(g8,g10)
    c: Equal(g12,g10)
FEATURE [PartDesign::Revolution] Revolution022
  Angle = 360
  Axis = (1,0,0)
  Base = (0,0,0)
  Profile = -> Sketch069
  ReferenceAxis = -> X_Axis089
FEATURE [PartDesign::Fillet] Fillet160
  Base = -> Revolution022 [Edge14,Edge15]
  BaseFeature = -> Revolution022
  Radius = 0.3
  SupportTransform = false
FEATURE [PartDesign::Body] Body075  label="Outer Ring003"
  Group = -> [Sketch069,Revolution022,Fillet160]
  Origin = -> Origin091
  Tip = -> Fillet160
FEATURE [Sketcher::SketchObject] Sketch070
  FullyConstrained = true
  MapMode = 5
  Support = -> [XY_Plane090]
  sketch-geometry (14):
    g0: LineSegment StartX=-2.9 StartY=6 StartZ=0 EndX=-1.32288 EndY=6 EndZ=0
    g1: LineSegment StartX=-3.5 StartY=4 StartZ=0 EndX=-3.5 EndY=5.7 EndZ=0
    g2: ArcOfCircle CenterX=-1e-16 CenterY=7.5 CenterZ=0 NormalX=0 NormalY=0 NormalZ=1 AngleXU=0 Radius=2 StartAngle=3.98965 EndAngle=5.43512
    g3: LineSegment StartX=1.32288 StartY=6 StartZ=0 EndX=2.9 EndY=6 EndZ=0
    g4: LineSegment StartX=-3.5 StartY=5.7 StartZ=0 EndX=-3.2 EndY=5.7 EndZ=0
    g5: LineSegment StartX=-3.2 StartY=5.7 StartZ=0 EndX=-3.2 EndY=5.5 EndZ=0
    g6: LineSegment StartX=-3.2 StartY=5.5 StartZ=0 EndX=-2.9 EndY=5.5 EndZ=0
    g7: LineSegment StartX=-2.9 StartY=5.5 StartZ=0 EndX=-2.9 EndY=6 EndZ=0
    g8: LineSegment StartX=8.5 StartY=6 StartZ=0 EndX=3.2 EndY=6 EndZ=0
    g9: LineSegment StartX=3.2 StartY=6 StartZ=0 EndX=3.2 EndY=5.5 EndZ=0
    g10: LineSegment StartX=3.2 StartY=5.5 StartZ=0 EndX=2.9 EndY=5.5 EndZ=0
    g11: LineSegment StartX=2.9 StartY=5.5 StartZ=0 EndX=2.9 EndY=6 EndZ=0
    g12: LineSegment StartX=8.5 StartY=4 StartZ=0 EndX=8.5 EndY=6 EndZ=0
    g13: LineSegment StartX=-3.5 StartY=4 StartZ=0 EndX=8.5 EndY=4 EndZ=0
  constraints (43):
    c: Horizontal(g0)
    c: Vertical(g1)
    c: DistanceY(g1) = 4
    c: Coincident(g2,g0)
    c: Coincident(g2,g3)
    c: Horizontal(g3)
    c: Radius(g2) = 2
    c: DistanceY(g2) = 7.5
    c: Symmetric(g0,g2,g-2)
    c: Horizontal(g4)
    c: Coincident(g4,g5)
    c: Vertical(g5)
    c: Coincident(g5,g6)
    c: Horizontal(g6)
    c: Coincident(g6,g7)
    c: Vertical(g7)
    c: Horizontal(g8)
    c: Coincident(g8,g9)
    c: Vertical(g9)
    c: Coincident(g9,g10)
    c: Horizontal(g10)
    c: Coincident(g10,g11)
    c: Vertical(g11)
    c: Coincident(g3,g11)
    c: Coincident(g0,g7)
    c: Coincident(g1,g4)
    c: DistanceY(g3) = 6
    c: DistanceY(g6,g0) = 0.5
    c: DistanceX(g4,g4) = 0.3
    c: DistanceX(g6,g6) = 0.3
    c: DistanceY(g5,g4) = 0.2
    c: Vertical(g12)
    c: Equal(g11,g7)
    c: DistanceY(g1,g0) = 2
    c: DistanceX(g8,g8) = 5.3
    c: Coincident(g13,g1)
    c: Coincident(g13,g12)
    c: Horizontal(g13)
    c: DistanceX(g13,g13) = 12
    c: DistanceX(g1,g2) = 3.5
    c: Coincident(g8,g12)
    c: Equal(g7,g9)
    c: Equal(g6,g10)
FEATURE [PartDesign::Revolution] Revolution023
  Angle = 360
  Axis = (1,0,0)
  Base = (0,0,0)
  Profile = -> Sketch070
  ReferenceAxis = -> X_Axis090
FEATURE [PartDesign::Fillet] Fillet161
  Base = -> Revolution023 [Edge13,Edge11]
  BaseFeature = -> Revolution023
  Radius = 0.2
  SupportTransform = false
FEATURE [PartDesign::Body] Body076  label="Inner Ring003"
  Group = -> [Sketch070,Revolution023,Fillet161]
  Origin = -> Origin092
  Tip = -> Fillet161
FEATURE [App::DocumentObjectGroup] Group018  label="Rings002"
  Group = -> [Body075,Body076]
FEATURE [Sketcher::SketchObject] Sketch071
  FullyConstrained = true
  MapMode = 5
  Placement = pos=(0,0,0) rot=(1,0,0;1.5708rad)
  Support = -> [XZ_Plane091]
  sketch-geometry (12):
    g0: LineSegment StartX=2.9 StartY=9.5 StartZ=0 EndX=2.9 EndY=8.5 EndZ=0
    g1: LineSegment StartX=2.9 StartY=8.5 StartZ=0 EndX=3.2 EndY=8.5 EndZ=0
    g2: LineSegment StartX=3.2 StartY=8.5 StartZ=0 EndX=3.2 EndY=6.5 EndZ=0
    g3: LineSegment StartX=3.2 StartY=6.5 StartZ=0 EndX=2.9 EndY=6.5 EndZ=0
    g4: LineSegment StartX=2.9 StartY=6.5 StartZ=0 EndX=2.9 EndY=5.5 EndZ=0
    g5: LineSegment StartX=2.9 StartY=5.5 StartZ=0 EndX=3.2 EndY=5.5 EndZ=0
    g6: LineSegment StartX=3.2 StartY=5.5 StartZ=0 EndX=3.2 EndY=6 EndZ=0
    g7: LineSegment StartX=3.2 StartY=6 StartZ=0 EndX=3.5 EndY=6 EndZ=0
    g8: LineSegment StartX=3.5 StartY=6 StartZ=0 EndX=3.5 EndY=9 EndZ=0
    g9: LineSegment StartX=3.5 StartY=9 StartZ=0 EndX=3.2 EndY=9 EndZ=0
    g10: LineSegment StartX=3.2 StartY=9 StartZ=0 EndX=3.2 EndY=9.5 EndZ=0
    g11: LineSegment StartX=3.2 StartY=9.5 StartZ=0 EndX=2.9 EndY=9.5 EndZ=0
  constraints (36):
    c: Vertical(g0)
    c: Coincident(g0,g1)
    c: Horizontal(g1)
    c: Coincident(g1,g2)
    c: Vertical(g2)
    c: Coincident(g2,g3)
    c: Horizontal(g3)
    c: Coincident(g3,g4)
    c: Vertical(g4)
    c: Coincident(g4,g5)
    c: Horizontal(g5)
    c: Coincident(g5,g6)
    c: Vertical(g6)
    c: Coincident(g6,g7)
    c: Horizontal(g7)
    c: Coincident(g7,g8)
    c: Vertical(g8)
    c: Coincident(g8,g9)
    c: Horizontal(g9)
    c: Coincident(g9,g10)
    c: Vertical(g10)
    c: Coincident(g10,g11)
    c: Coincident(g11,g0)
    c: Horizontal(g11)
    c: DistanceY(g4) = 5.5
    c: DistanceX(g4) = 2.9
    c: DistanceY(g5,g6) = 0.5
    c: DistanceY(g6,g2) = 0.5
    c: DistanceX(g5,g5) = 0.3
    c: Equal(g5,g7)
    c: Equal(g7,g3)
    c: Equal(g3,g1)
    c: Equal(g1,g9)
    c: Equal(g4,g0)
    c: Equal(g6,g10)
    c: DistanceY(g4,g0) = 4
FEATURE [PartDesign::Revolution] Revolution024
  Angle = 360
  Axis = (1,0,0)
  Base = (0,0,0)
  Placement = pos=(0,0,0) rot=(1,0,0;1.5708rad)
  Profile = -> Sketch071
  ReferenceAxis = -> Sketch071 [H_Axis]
FEATURE [PartDesign::Fillet] Fillet162
  Base = -> Revolution024 [Edge14,Edge12]
  BaseFeature = -> Revolution024
  Placement = pos=(0,0,0) rot=(1,0,0;1.5708rad)
  Radius = 0.2
  SupportTransform = false
FEATURE [PartDesign::Body] Body077  label="Seal 005"
  Group = -> [Sketch071,Revolution024,Fillet162]
  Origin = -> Origin093
  Tip = -> Fillet162
FEATURE [PartDesign::FeatureBase] Clone041
  BaseFeature = -> Body077
FEATURE [PartDesign::Body] Body078  label="Seal 006"
  BaseFeature = -> Body077
  Group = -> [Clone041]
  Origin = -> Origin094
  Placement = pos=(0,0,0) rot=(0,1,0;3.14159rad)
  Tip = -> Clone041
FEATURE [App::DocumentObjectGroup] Group017  label="Seals002"
  Group = -> [Body077,Body078]
FEATURE [Sketcher::SketchObject] Sketch072
  AttachmentOffset = pos=(0,0,4) rot=(0,0,1;0rad)
  FullyConstrained = true
  MapMode = 5
  Placement = pos=(0,0,4) rot=(0,0,1;0rad)
  Support = -> [XY_Plane072]
  sketch-geometry (1):
    g0: Circle CenterX=6 CenterY=0 CenterZ=0 NormalX=0 NormalY=0 NormalZ=1 AngleXU=0 Radius=1.5
  constraints (3):
    c: PointOnObject(g0,g-1)
    c: Diameter(g0) = 3
    c: DistanceX(g-1,g0) = 6
FEATURE [PartDesign::Pad] Pad018
  Direction = (0,0,1)
  Length = 3
  Length2 = 100
  Profile = -> Sketch072
  Type = 0
FEATURE [Sketcher::SketchObject] Sketch073
  ExternalGeometry = -> [Pad018]
  FullyConstrained = true
  MapMode = 5
  Placement = pos=(0,0,7) rot=(0,0,1;0rad)
  Support = -> [Pad018]
  sketch-geometry (7):
    g0: LineSegment StartX=6.43301 StartY=-0.75 StartZ=0 EndX=6.86603 EndY=0 EndZ=0
    g1: LineSegment StartX=6.86603 StartY=0 StartZ=0 EndX=6.43301 EndY=0.75 EndZ=0
    g2: LineSegment StartX=6.43301 StartY=0.75 StartZ=0 EndX=5.56699 EndY=0.75 EndZ=0
    g3: LineSegment StartX=5.56699 StartY=0.75 StartZ=0 EndX=5.13397 EndY=-1e-16 EndZ=0
    g4: LineSegment StartX=5.13397 StartY=-1e-16 StartZ=0 EndX=5.56699 EndY=-0.75 EndZ=0
    g5: LineSegment StartX=5.56699 StartY=-0.75 StartZ=0 EndX=6.43301 EndY=-0.75 EndZ=0
    g6: Circle CenterX=6 CenterY=0 CenterZ=0 NormalX=0 NormalY=0 NormalZ=1 AngleXU=0 Radius=0.866025
  constraints (16):
    c: Coincident(g0,g1)
    c: Coincident(g1,g2)
    c: Coincident(g2,g3)
    c: Coincident(g3,g4)
    c: Coincident(g4,g5)
    c: Coincident(g5,g0)
    c: Equal(g0, g1-g5) x5
    c: PointOnObject(g0,g6)
    c: PointOnObject(g1,g6)
    c: PointOnObject(g2,g6)
    c: PointOnObject(g3,g6)
    c: PointOnObject(g4,g6)
    c: PointOnObject(g5,g6)
    c: Coincident(g6,g-3)
    c: Horizontal(g5)
    c: DistanceY(g4,g2) = 1.5
FEATURE [PartDesign::Pocket] Pocket023
  BaseFeature = -> Pad018
  Length = 0.9
  Length2 = 100
  Profile = -> Sketch073
  Type = 0
FEATURE [PartDesign::PolarPattern] PolarPattern011
  Angle = 120
  Axis = -> X_Axis072
  BaseFeature = -> Pocket023
  Occurrences = 3
  Originals = -> [Pad018,Pocket023]
FEATURE [PartDesign::Body] Body058
  Group = -> [Sketch072,Pad018,Sketch073,Pocket023,PolarPattern011]
  Origin = -> Origin074
  Tip = -> PolarPattern011
FEATURE [App::DocumentObjectGroup] Group019  label="Set screws002"
  Group = -> [Body058]
FEATURE [Sketcher::SketchObject] Sketch074
  AttachmentOffset = pos=(0,0,-6.5) rot=(0,0,1;0rad)
  FullyConstrained = true
  MapMode = 5
  Placement = pos=(-6.5,1.4e-15,-1.4e-15) rot=(0.57735,0.57735,0.57735;2.0944rad)
  Support = -> [YZ_Plane093]
  sketch-geometry (14):
    g0: Circle CenterX=0 CenterY=0 CenterZ=0 NormalX=0 NormalY=0 NormalZ=1 AngleXU=0 Radius=11
    g1: ArcOfCircle CenterX=0 CenterY=0 CenterZ=0 NormalX=0 NormalY=0 NormalZ=1 AngleXU=0 Radius=13.5 StartAngle=0.0668757 EndAngle=3.07472
    g2: LineSegment StartX=-13.4698 StartY=0.902148 StartZ=0 EndX=-14.2 EndY=-10 EndZ=0
    g3: LineSegment StartX=-14.2 StartY=-10 StartZ=0 EndX=-27.5 EndY=-10 EndZ=0
    g4: LineSegment StartX=-27.5 StartY=-10 StartZ=0 EndX=-27.5 EndY=-15 EndZ=0
    g5: LineSegment StartX=-27.5 StartY=-15 StartZ=0 EndX=-12.3 EndY=-15 EndZ=0
    g6: LineSegment StartX=27.5 StartY=-15 StartZ=0 EndX=27.5 EndY=-10 EndZ=0
    g7: LineSegment StartX=27.5 StartY=-10 StartZ=0 EndX=14.2 EndY=-10 EndZ=0
    g8: LineSegment StartX=14.2 StartY=-10 StartZ=0 EndX=13.4698 EndY=0.902148 EndZ=0
    g9: LineSegment StartX=12.3 StartY=-15 StartZ=0 EndX=12.1995 EndY=-13.5 EndZ=0
    g10: LineSegment StartX=12.1995 StartY=-13.5 StartZ=0 EndX=-12.1995 EndY=-13.5 EndZ=0
    g11: LineSegment StartX=-12.1995 StartY=-13.5 StartZ=0 EndX=-12.3 EndY=-15 EndZ=0
    g12: LineSegment StartX=12.3 StartY=-15 StartZ=0 EndX=27.5 EndY=-15 EndZ=0
    g13: GeomPoint X=0 Y=13.5 Z=0
  constraints (39):
    c: Coincident(g0,g-1)
    c: Radius(g0) = 11
    c: Coincident(g1,g0)
    c: Coincident(g2,g3)
    c: Coincident(g3,g4)
    c: Coincident(g4,g5)
    c: Horizontal(g5)
    c: Coincident(g12,g6)
    c: Coincident(g6,g7)
    c: Horizontal(g7)
    c: Coincident(g7,g8)
    c: Coincident(g9,g10)
    c: Horizontal(g10)
    c: Coincident(g10,g11)
    c: Coincident(g5,g11)
    c: Coincident(g12,g9)
    c: Horizontal(g3)
    c: Vertical(g6)
    c: Vertical(g4)
    c: Equal(g9,g11)
    c: Horizontal(g12)
    c: Horizontal(g5,g9)
    c: Equal(g6,g4)
    c: Equal(g12,g5)
    c: Equal(g7,g3)
    c: DistanceX(g4,g6) = 55
    c: DistanceY(g6,g0) = 15
    c: Equal(g8,g2)
    c: DistanceY(g6,g6) = 5
    c: Parallel(g9,g8)
    c: DistanceY(g9,g9) = 1.5
    c: DistanceX(g5,g5) = 15.2
    c: Diameter(g1) = 27
    c: PointOnObject(g13,g1)
    c: PointOnObject(g13,g-2)
    c: DistanceY(g6,g13) = 28.5
    c: Tangent(g1,g2) = -1.5708
    c: Tangent(g1,g8) = -1.5708
    c: DistanceX(g3,g3) = 13.3
FEATURE [PartDesign::Pad] Pad019
  Direction = (1,-2e-16,3e-16)
  Length = 13
  Length2 = 100
  Placement = pos=(0,0,0) rot=(0.57735,0.57735,0.57735;2.0944rad)
  Profile = -> Sketch074
  Type = 0
FEATURE [Sketcher::SketchObject] Sketch075
  ExternalGeometry = -> [Pad019]
  FullyConstrained = true
  MapMode = 5
  Placement = pos=(4.2e-15,-6.6e-15,-15) rot=(0.707107,0.707107,0;3.14159rad)
  Support = -> [Pad019]
  sketch-geometry (7):
    g0: LineSegment StartX=-24.9 StartY=4.15 StartZ=0 EndX=-14.9 EndY=4.15 EndZ=0
    g1: LineSegment StartX=-14.9 StartY=4.15 StartZ=0 EndX=-14.9 EndY=-4.15 EndZ=0
    g2: LineSegment StartX=-14.9 StartY=-4.15 StartZ=0 EndX=-24.9 EndY=-4.15 EndZ=0
    g3: LineSegment StartX=-24.9 StartY=-4.15 StartZ=0 EndX=-24.9 EndY=4.15 EndZ=0
    g4: LineSegment StartX=-27.5 StartY=6.5 StartZ=0 EndX=-12.3 EndY=-6.5 EndZ=0
    g5: LineSegment StartX=-27.5 StartY=-6.5 StartZ=0 EndX=-12.3 EndY=6.5 EndZ=0
    g6: GeomPoint X=-19.9 Y=2.6e-15 Z=0
  constraints (17):
    c: Coincident(g0,g1)
    c: Coincident(g1,g2)
    c: Coincident(g2,g3)
    c: Coincident(g3,g0)
    c: Horizontal(g0)
    c: Horizontal(g2)
    c: Vertical(g1)
    c: Vertical(g3)
    c: DistanceX(g0,g0) = 10
    c: DistanceY(g1,g1) = 8.3
    c: Coincident(g4,g-3)
    c: Coincident(g4,g-4)
    c: Coincident(g5,g-4)
    c: Coincident(g5,g-3)
    c: PointOnObject(g6,g4)
    c: PointOnObject(g6,g5)
    c: Symmetric(g0,g1,g6)
FEATURE [PartDesign::Pocket] Pocket024
  BaseFeature = -> Pad019
  Length = 2.3
  Length2 = 100
  Placement = pos=(0,0,0) rot=(0.57735,0.57735,0.57735;2.0944rad)
  Profile = -> Sketch075
  Type = 0
FEATURE [Sketcher::SketchObject] Sketch076
  ExternalGeometry = -> [Pocket024]
  FullyConstrained = true
  MapMode = 5
  Placement = pos=(2.8e-15,-4.4e-15,-10) rot=(0,0,-1;1.5708rad)
  Support = -> [Pocket024]
  sketch-geometry (2):
    g0: Circle CenterX=21.2 CenterY=2.1e-15 CenterZ=0 NormalX=0 NormalY=0 NormalZ=1 AngleXU=0 Radius=2.5
    g1: LineSegment StartX=21.2 StartY=2.1e-15 StartZ=0 EndX=27.5 EndY=2.1e-15 EndZ=0
  constraints (5):
    c: Diameter(g0) = 5
    c: DistanceX(g0,g-3) = 6.3
    c: Coincident(g1,g0)
    c: Horizontal(g1)
    c: Symmetric(g-5,g-5,g1)
FEATURE [PartDesign::Pocket] Pocket025
  BaseFeature = -> Pocket024
  Length = 5
  Length2 = 100
  Placement = pos=(0,0,0) rot=(0.57735,0.57735,0.57735;2.0944rad)
  Profile = -> Sketch076
  Type = 2
FEATURE [Sketcher::SketchObject] Sketch077
  ExternalGeometry = -> [Pocket025]
  FullyConstrained = true
  MapMode = 5
  Placement = pos=(6.5,-1.4e-15,1.5e-15) rot=(0.57735,0.57735,0.57735;2.0944rad)
  Support = -> [Pocket025]
  sketch-geometry (6):
    g0: LineSegment StartX=-24.6 StartY=-13.7 StartZ=0 EndX=-24.6 EndY=-11.3 EndZ=0
    g1: LineSegment StartX=-24.6 StartY=-11.3 StartZ=0 EndX=-14.2 EndY=-11.3 EndZ=0
    g2: LineSegment StartX=-14.2 StartY=-11.3 StartZ=0 EndX=-14.2 EndY=-13.7 EndZ=0
    g3: LineSegment StartX=-14.2 StartY=-13.7 StartZ=0 EndX=-24.6 EndY=-13.7 EndZ=0
    g4: GeomPoint X=-19.4 Y=-12.5 Z=0
    g5: LineSegment StartX=-19.4 StartY=-12.5 StartZ=0 EndX=-27.5 EndY=-12.5 EndZ=0
  constraints (15):
    c: Coincident(g0,g1)
    c: Coincident(g1,g2)
    c: Coincident(g2,g3)
    c: Coincident(g3,g0)
    c: Horizontal(g1)
    c: Horizontal(g3)
    c: Vertical(g0)
    c: Vertical(g2)
    c: Symmetric(g1,g0,g4)
    c: DistanceX(g1,g1) = 10.4
    c: DistanceY(g2,g2) = 2.4
    c: DistanceX(g2,g-4) = 1.9
    c: Coincident(g5,g4)
    c: Horizontal(g5)
    c: Symmetric(g-5,g-5,g5)
FEATURE [PartDesign::Pocket] Pocket026
  BaseFeature = -> Pocket025
  Length = 0.4
  Length2 = 100
  Placement = pos=(0,0,0) rot=(0.57735,0.57735,0.57735;2.0944rad)
  Profile = -> Sketch077
  Type = 0
FEATURE [PartDesign::Mirrored] Mirrored002
  BaseFeature = -> Pocket026
  MirrorPlane = -> Sketch075 [V_Axis]
  Originals = -> [Pocket024,Pocket025,Pocket026]
  Placement = pos=(0,0,0) rot=(0.57735,0.57735,0.57735;2.0944rad)
FEATURE [Sketcher::SketchObject] Sketch078
  ExternalGeometry = -> [Mirrored002]
  FullyConstrained = true
  MapMode = 5
  Placement = pos=(0,0,0) rot=(1,0,0;1.5708rad)
  Support = -> [XZ_Plane093]
  sketch-geometry (9):
    g0: GeomPoint X=-6.5 Y=13.5 Z=0
    g1: LineSegment StartX=6.5 StartY=-10 StartZ=0 EndX=6.5 EndY=13.5 EndZ=0
    g2: LineSegment StartX=6.5 StartY=13.5 StartZ=0 EndX=4.75 EndY=13.5 EndZ=0
    g3: LineSegment StartX=-6.5 StartY=13.5 StartZ=0 EndX=-4.75 EndY=13.5 EndZ=0
    g4: LineSegment StartX=-6.5 StartY=-10 StartZ=0 EndX=-6.5 EndY=13.5 EndZ=0
    g5: LineSegment StartX=6.5 StartY=-10 StartZ=0 EndX=4.75 EndY=-1 EndZ=0
    g6: LineSegment StartX=4.75 StartY=-1 StartZ=0 EndX=4.75 EndY=13.5 EndZ=0
    g7: LineSegment StartX=-4.75 StartY=13.5 StartZ=0 EndX=-4.75 EndY=-1 EndZ=0
    g8: LineSegment StartX=-4.75 StartY=-1 StartZ=0 EndX=-6.5 EndY=-10 EndZ=0
  constraints (24):
    c: Vertical(g0,g-4)
    c: Horizontal(g-3,g0)
    c: Coincident(g1,g-3)
    c: Coincident(g1,g2)
    c: Horizontal(g2)
    c: Coincident(g3,g0)
    c: Horizontal(g3)
    c: Coincident(g4,g3)
    c: Vertical(g4,g-4)
    c: DistanceX(g3,g2) = 9.5
    c: Equal(g2,g3)
    c: Horizontal(g1,g4)
    c: Coincident(g1,g-5)
    c: Coincident(g1,g5)
    c: Coincident(g5,g6)
    c: Coincident(g6,g2)
    c: Vertical(g6)
    c: DistanceY(g1,g5) = 9
    c: Coincident(g3,g7)
    c: Vertical(g7)
    c: Coincident(g7,g8)
    c: Coincident(g8,g4)
    c: Horizontal(g7,g5)
    c: DistanceX(g2,g2) = 1.75
FEATURE [PartDesign::Pocket] Pocket027
  BaseFeature = -> Mirrored002
  Length = 15
  Length2 = 15
  Placement = pos=(0,0,0) rot=(0.57735,0.57735,0.57735;2.0944rad)
  Profile = -> Sketch078
  Type = 4
FEATURE [Sketcher::SketchObject] Sketch079
  FullyConstrained = true
  MapMode = 5
  Placement = pos=(-6.5,1.4e-15,-1.5e-15) rot=(0.57735,0.57735,-0.57735;4.18879rad)
  Support = -> [Pocket027]
  sketch-geometry (1):
    g0: Circle CenterX=0 CenterY=0 CenterZ=0 NormalX=0 NormalY=0 NormalZ=1 AngleXU=0 Radius=12.2
  constraints (2):
    c: Coincident(g0,g-1)
    c: Diameter(g0) = 24.4
FEATURE [PartDesign::Pocket] Pocket028
  BaseFeature = -> Pocket027
  Length = 2.75
  Length2 = 100
  Placement = pos=(0,0,0) rot=(0.57735,0.57735,0.57735;2.0944rad)
  Profile = -> Sketch079
  Type = 0
FEATURE [Sketcher::SketchObject] Sketch080
  FullyConstrained = true
  MapMode = 5
  Placement = pos=(6.5,-1.4e-15,1.5e-15) rot=(0.57735,0.57735,0.57735;2.0944rad)
  Support = -> [Pocket028]
  sketch-geometry (1):
    g0: Circle CenterX=0 CenterY=0 CenterZ=0 NormalX=0 NormalY=0 NormalZ=1 AngleXU=0 Radius=12.1
  constraints (2):
    c: Coincident(g0,g-1)
    c: Diameter(g0) = 24.2
FEATURE [PartDesign::Pocket] Pocket029
  BaseFeature = -> Pocket028
  Length = 2.75
  Length2 = 100
  Placement = pos=(0,0,0) rot=(0.57735,0.57735,0.57735;2.0944rad)
  Profile = -> Sketch080
  Type = 0
FEATURE [Sketcher::SketchObject] Sketch081
  ExternalGeometry = -> [Pocket029]
  FullyConstrained = true
  MapMode = 5
  Placement = pos=(6.5,-1.4e-15,1.5e-15) rot=(0.57735,0.57735,0.57735;2.0944rad)
  Support = -> [Pocket029]
  sketch-geometry (6):
    g0: ArcOfCircle CenterX=0 CenterY=0 CenterZ=0 NormalX=0 NormalY=0 NormalZ=1 AngleXU=0 Radius=13.5 StartAngle=3.79664 EndAngle=5.62814
    g1: LineSegment StartX=-11.8698 StartY=-8.57666 StartZ=0 EndX=-12.3 EndY=-15 EndZ=0
    g2: LineSegment StartX=-12.3 StartY=-15 StartZ=0 EndX=12.3 EndY=-15 EndZ=0
    g3: LineSegment StartX=12.3 StartY=-15 StartZ=0 EndX=11.8698 EndY=-8.57666 EndZ=0
    g4: ArcOfCircle CenterX=11.2212 CenterY=-8.6201 CenterZ=0 NormalX=0 NormalY=0 NormalZ=1 AngleXU=0 Radius=0.65 StartAngle=0.0668757 EndAngle=2.48655
    g5: ArcOfCircle CenterX=-11.2212 CenterY=-8.6201 CenterZ=0 NormalX=0 NormalY=0 NormalZ=1 AngleXU=0 Radius=0.65 StartAngle=0.655044 EndAngle=3.07472
  constraints (14):
    c: Coincident(g0,g-1)
    c: Diameter(g0) = 27
    c: Coincident(g1,g2)
    c: Coincident(g2,g3)
    c: Coincident(g1,g-3)
    c: Coincident(g2,g-4)
    c: Tangent(g3,g4) = -1.5708
    c: Tangent(g0,g4) = 1.5708
    c: Tangent(g0,g5) = 1.5708
    c: Tangent(g1,g5) = -1.5708
    c: Equal(g4,g5)
    c: Horizontal(g4,g5)
    c: Parallel(g-4,g3)
    c: Radius(g4) = 0.65
FEATURE [PartDesign::Pocket] Pocket030
  BaseFeature = -> Pocket029
  Length = 5.25
  Length2 = 100
  Placement = pos=(0,0,0) rot=(0.57735,0.57735,0.57735;2.0944rad)
  Profile = -> Sketch081
  Type = 0
FEATURE [Sketcher::SketchObject] Sketch082
  ExternalGeometry = -> [Pocket030]
  FullyConstrained = true
  MapMode = 5
  Placement = pos=(-6.5,1.4e-15,-1.5e-15) rot=(0.57735,0.57735,-0.57735;4.18879rad)
  Support = -> [Pocket030]
  sketch-geometry (6):
    g0: ArcOfCircle CenterX=0 CenterY=0 CenterZ=0 NormalX=0 NormalY=0 NormalZ=1 AngleXU=0 Radius=13.5 StartAngle=0.655044 EndAngle=2.48655
    g1: LineSegment StartX=11.8698 StartY=8.57666 StartZ=0 EndX=12.3 EndY=15 EndZ=0
    g2: LineSegment StartX=12.3 StartY=15 StartZ=0 EndX=-12.3 EndY=15 EndZ=0
    g3: LineSegment StartX=-12.3 StartY=15 StartZ=0 EndX=-11.8698 EndY=8.57666 EndZ=0
    g4: ArcOfCircle CenterX=-11.2212 CenterY=8.6201 CenterZ=0 NormalX=0 NormalY=0 NormalZ=1 AngleXU=0 Radius=0.65 StartAngle=3.20847 EndAngle=5.62814
    g5: ArcOfCircle CenterX=11.2212 CenterY=8.6201 CenterZ=0 NormalX=0 NormalY=0 NormalZ=1 AngleXU=0 Radius=0.65 StartAngle=3.79664 EndAngle=6.21631
  constraints (14):
    c: Coincident(g0,g-1)
    c: Radius(g0) = 13.5
    c: Coincident(g1,g2)
    c: Coincident(g2,g-3)
    c: Coincident(g2,g3)
    c: Coincident(g-4,g1)
    c: Tangent(g3,g4) = -1.5708
    c: Tangent(g0,g4) = 1.5708
    c: Tangent(g0,g5) = 1.5708
    c: Tangent(g1,g5) = -1.5708
    c: Equal(g4,g5)
    c: Radius(g4) = 0.65
    c: Parallel(g-4,g1)
    c: Parallel(g3,g-3)
FEATURE [PartDesign::Pocket] Pocket031
  BaseFeature = -> Pocket030
  Length = 5.25
  Length2 = 100
  Placement = pos=(0,0,0) rot=(0.57735,0.57735,0.57735;2.0944rad)
  Profile = -> Sketch082
  Type = 0
FEATURE [PartDesign::Chamfer] Chamfer002
  Angle = 45
  Base = -> Pocket031 [Edge159,Edge155,Edge22,Edge27]
  BaseFeature = -> Pocket031
  ChamferType = 0
  FlipDirection = false
  Placement = pos=(0,0,0) rot=(0.57735,0.57735,0.57735;2.0944rad)
  Size = 2
  Size2 = 1
  SupportTransform = false
FEATURE [Sketcher::SketchObject] Sketch083
  ExternalGeometry = -> [Chamfer002]
  FullyConstrained = true
  MapMode = 5
  Placement = pos=(-3.75,5e-15,-2.7e-15) rot=(-0.57735,-0.57735,0.57735;2.0944rad)
  Support = -> [Chamfer002]
  sketch-geometry (13):
    g0: ArcOfCircle CenterX=-6.9e-15 CenterY=-3.7e-15 CenterZ=0 NormalX=0 NormalY=0 NormalZ=1 AngleXU=0 Radius=11 StartAngle=5.75419 EndAngle=6.81218
    g1: ArcOfCircle CenterX=-6.9e-15 CenterY=-3.7e-15 CenterZ=0 NormalX=0 NormalY=0 NormalZ=1 AngleXU=0 Radius=12.2 StartAngle=5.94045 EndAngle=6.62592
    g2: ArcOfCircle CenterX=-6.9e-15 CenterY=-3.7e-15 CenterZ=0 NormalX=0 NormalY=0 NormalZ=1 AngleXU=0 Radius=11 StartAngle=2.6126 EndAngle=3.67059
    g3: ArcOfCircle CenterX=-6.9e-15 CenterY=-3.7e-15 CenterZ=0 NormalX=0 NormalY=0 NormalZ=1 AngleXU=0 Radius=12.2 StartAngle=2.79886 EndAngle=3.48433
    g4: Ellipse CenterX=-6.9e-15 CenterY=-3.7e-15 CenterZ=0 NormalX=0 NormalY=0 NormalZ=1 MajorRadius=13.5 MinorRadius=7.81051 AngleXU=-3e-16
    g5: LineSegment StartX=13.5 StartY=-7.4e-15 StartZ=0 EndX=-13.5 EndY=0 EndZ=0
    g6: LineSegment StartX=-4.8e-15 StartY=7.81051 StartZ=0 EndX=-9.1e-15 EndY=-7.81051 EndZ=0
    g7: GeomPoint X=11.0112 Y=-6.8e-15 Z=0
    g8: GeomPoint X=-11.0112 Y=-7e-16 Z=0
    g9: LineSegment StartX=-11.4904 StartY=4.1 StartZ=0 EndX=-9.49645 EndY=5.55135 EndZ=0
    g10: LineSegment StartX=-11.4904 StartY=-4.1 StartZ=0 EndX=-9.49645 EndY=-5.55135 EndZ=0
    g11: LineSegment StartX=9.49645 StartY=-5.55135 StartZ=0 EndX=11.4904 EndY=-4.1 EndZ=0
    g12: LineSegment StartX=11.4904 StartY=4.1 StartZ=0 EndX=9.49645 EndY=5.55135 EndZ=0
  constraints (29):
    c: Coincident(g0,g-4)
    c: PointOnObject(g0,g-4)
    c: Coincident(g1,g0)
    c: PointOnObject(g1,g-3)
    c: Coincident(g2,g0)
    c: PointOnObject(g2,g-4)
    c: Coincident(g3,g0)
    c: PointOnObject(g3,g-3)
    c: InternalAlignment(g5-g8 -> g4) x4
    c: Coincident(g4,g0)
    c: PointOnObject(g3,g4)
    c: PointOnObject(g2,g4)
    c: PointOnObject(g3,g4)
    c: PointOnObject(g2,g4)
    c: PointOnObject(g0,g4)
    c: PointOnObject(g1,g4)
    c: PointOnObject(g1,g4)
    c: PointOnObject(g0,g4)
    c: PointOnObject(g5,g-1)
    c: DistanceX(g5,g5) = 27
    c: DistanceY(g3,g3) = 8.2
    c: Coincident(g9,g3)
    c: Coincident(g9,g2)
    c: Coincident(g10,g3)
    c: Coincident(g10,g2)
    c: Coincident(g11,g0)
    c: Coincident(g11,g1)
    c: Coincident(g12,g1)
    c: Coincident(g12,g0)
FEATURE [PartDesign::Pocket] Pocket032
  BaseFeature = -> Chamfer002
  Length = 5
  Length2 = 100
  Placement = pos=(0,0,0) rot=(0.57735,0.57735,0.57735;2.0944rad)
  Profile = -> Sketch083
  Type = 0
FEATURE [PartDesign::Body] Body079  label="Metal case002"
  Group = -> [Sketch074,Pad019,Sketch075,Pocket024,Sketch076,Pocket025,Sketch077,Pocket026,Mirrored002,Sketch078,Pocket027,Sketch079,Pocket028,Sketch080,Pocket029,Sketch081,Pocket030,Sketch082,Pocket031,Chamfer002,Sketch083,Pocket032]
  Origin = -> Origin095
  Tip = -> Pocket032
FEATURE [App::DocumentObjectGroup] Group020  label="Case002"
  Group = -> [Body079]
FEATURE [App::Part] Part016  label="KP08-003"
  Group = -> [Group014,Body060,Body059,Body064,Body061,Body065,Body063,Body062,Group015,Body067,Body066,Group016,Body072,Body071,Body074,Body070,Body073,Body069,Body068,Group017,Body078,Body077,Group018,Body075,Body076,Group019,Body058,Group020,Body079]
  Origin = -> Origin096
  Placement = pos=(332,120,105) rot=(0,0,1;3.14159rad)
FEATURE [Sketcher::SketchObject] Sketch084
  FullyConstrained = true
  MapMode = 5
  Placement = pos=(0,0,0) rot=(-0.57735,0.57735,0.57735;4.18879rad)
  Support = -> [YZ_Plane102]
  sketch-geometry (1):
    g0: Circle CenterX=0 CenterY=-7.5 CenterZ=0 NormalX=0 NormalY=0 NormalZ=1 AngleXU=0 Radius=0.25
  constraints (3):
    c: PointOnObject(g0,g-2)
    c: DistanceY(g0) = -7.5
    c: Diameter(g0) = 0.5
FEATURE [Sketcher::SketchObject] Sketch085
  FullyConstrained = true
  MapMode = 5
  Support = -> [XY_Plane095]
  sketch-geometry (2):
    g0: LineSegment StartX=0 StartY=5.5 StartZ=0 EndX=6e-16 EndY=9.5 EndZ=0
    g1: ArcOfCircle CenterX=0 CenterY=7.5 CenterZ=0 NormalX=0 NormalY=0 NormalZ=1 AngleXU=0 Radius=2 StartAngle=4.71239 EndAngle=7.85398
  constraints (7):
    c: PointOnObject(g0,g-2)
    c: PointOnObject(g0,g-2)
    c: PointOnObject(g1,g0)
    c: Coincident(g1,g0)
    c: Coincident(g1,g0)
    c: Radius(g1) = 2
    c: DistanceY(g1) = 7.5
FEATURE [PartDesign::Revolution] Revolution025
  Angle = 360
  Axis = (0,1,0)
  Base = (0,0,0)
  Profile = -> Sketch085
  ReferenceAxis = -> Sketch085 [V_Axis]
  Reversed = true
FEATURE [PartDesign::Body] Body081  label="Ball 022"
  Group = -> [Sketch085,Revolution025]
  Origin = -> Origin098
  Tip = -> Revolution025
FEATURE [PartDesign::FeatureBase] Clone042
  BaseFeature = -> Body081
FEATURE [PartDesign::Body] Body082  label="Ball 023"
  BaseFeature = -> Body081
  Group = -> [Clone042]
  Origin = -> Origin099
  Placement = pos=(0,0,0) rot=(-1,0,0;0.897598rad)
  Tip = -> Clone042
FEATURE [PartDesign::FeatureBase] Clone043
  BaseFeature = -> Body081
FEATURE [PartDesign::Body] Body083  label="Ball 024"
  BaseFeature = -> Body081
  Group = -> [Clone043]
  Origin = -> Origin100
  Placement = pos=(0,0,0) rot=(-1,0,0;1.7952rad)
  Tip = -> Clone043
FEATURE [PartDesign::FeatureBase] Clone044
  BaseFeature = -> Body081
FEATURE [PartDesign::Body] Body084  label="Ball 025"
  BaseFeature = -> Body081
  Group = -> [Clone044]
  Origin = -> Origin101
  Placement = pos=(0,0,0) rot=(1,0,0;3.59039rad)
  Tip = -> Clone044
FEATURE [PartDesign::FeatureBase] Clone045
  BaseFeature = -> Body081
FEATURE [PartDesign::Body] Body085  label="Ball 026"
  BaseFeature = -> Body081
  Group = -> [Clone045]
  Origin = -> Origin102
  Placement = pos=(0,0,0) rot=(1,0,0;2.69279rad)
  Tip = -> Clone045
FEATURE [PartDesign::FeatureBase] Clone046
  BaseFeature = -> Body081
FEATURE [PartDesign::Body] Body086  label="Ball 027"
  BaseFeature = -> Body081
  Group = -> [Clone046]
  Origin = -> Origin103
  Placement = pos=(0,0,0) rot=(1,0,0;1.7952rad)
  Tip = -> Clone046
FEATURE [PartDesign::FeatureBase] Clone047
  BaseFeature = -> Body081
FEATURE [PartDesign::Body] Body087  label="Ball 028"
  BaseFeature = -> Body081
  Group = -> [Clone047]
  Origin = -> Origin104
  Placement = pos=(0,0,0) rot=(1,0,0;0.897598rad)
  Tip = -> Clone047
FEATURE [App::DocumentObjectGroup] Group021  label="Balls003"
  Group = -> [Body081,Body082,Body083,Body084,Body085,Body086,Body087]
FEATURE [Sketcher::SketchObject] Sketch086
  FullyConstrained = true
  MapMode = 5
  Support = -> [XY_Plane104]
  sketch-geometry (7):
    g0: LineSegment StartX=-5 StartY=7.5 StartZ=0 EndX=5 EndY=7.5 EndZ=0
    g1: LineSegment StartX=-0.210977 StartY=7.5 StartZ=0 EndX=0.210977 EndY=7.5 EndZ=0
    g2: ArcOfCircle CenterX=0.25 CenterY=7.5 CenterZ=0 NormalX=0 NormalY=0 NormalZ=1 AngleXU=0 Radius=0.460977 StartAngle=2.43297 EndAngle=3.14159
    g3: ArcOfCircle CenterX=-0.25 CenterY=7.5 CenterZ=0 NormalX=0 NormalY=0 NormalZ=1 AngleXU=0 Radius=0.460977 StartAngle=9.792e-13 EndAngle=0.708626
    g4: LineSegment StartX=-0.1 StartY=7.8 StartZ=0 EndX=-0.1 EndY=7.75 EndZ=0
    g5: LineSegment StartX=-0.1 StartY=7.75 StartZ=0 EndX=0.1 EndY=7.75 EndZ=0
    g6: LineSegment StartX=0.1 StartY=7.75 StartZ=0 EndX=0.1 EndY=7.8 EndZ=0
  constraints (22):
    c: DistanceY(g-1,g0) = 7.5
    c: Symmetric(g0,g0,g-2)
    c: DistanceX(g0,g0) = 10
    c: PointOnObject(g1,g0)
    c: PointOnObject(g1,g0)
    c: Coincident(g3,g1)
    c: Coincident(g2,g1)
    c: Coincident(g2,g4)
    c: Coincident(g4,g5)
    c: Horizontal(g5)
    c: Coincident(g5,g6)
    c: Coincident(g6,g3)
    c: Vertical(g6)
    c: Equal(g3,g2)
    c: Vertical(g4)
    c: Symmetric(g2,g3,g-2)
    c: DistanceX(g5,g5) = 0.2
    c: Distance(g5,g1) = 0.25
    c: DistanceX(g3,g-1) = 0.25
    c: PointOnObject(g3,g1)
    c: PointOnObject(g2,g1)
    c: Distance(g3,g1) = 0.3
FEATURE [PartDesign::Revolution] Revolution026
  Angle = 360
  Axis = (10,0,0)
  Base = (-5,7.5,0)
  Profile = -> Sketch086
  ReferenceAxis = -> Sketch086 [Axis]
FEATURE [PartDesign::Body] Body090  label="Rivet 022"
  Group = -> [Sketch086,Revolution026]
  Origin = -> Origin107
  Placement = pos=(0,0,0) rot=(1,0,0;0.448799rad)
  Tip = -> Revolution026
FEATURE [PartDesign::FeatureBase] Clone049
  BaseFeature = -> Body090
  Placement = pos=(0,0,0) rot=(1,0,0;0.448799rad)
FEATURE [PartDesign::Body] Body091  label="Rivet 023"
  BaseFeature = -> Body090
  Group = -> [Clone049]
  Origin = -> Origin108
  Placement = pos=(0,0,0) rot=(1,0,0;0.897598rad)
  Tip = -> Clone049
FEATURE [PartDesign::FeatureBase] Clone050
  BaseFeature = -> Body090
  Placement = pos=(0,0,0) rot=(1,0,0;0.448799rad)
FEATURE [PartDesign::Body] Body092  label="Rivet 024"
  BaseFeature = -> Body090
  Group = -> [Clone050]
  Origin = -> Origin109
  Placement = pos=(0,0,0) rot=(1,0,0;1.7952rad)
  Tip = -> Clone050
FEATURE [PartDesign::FeatureBase] Clone051
  BaseFeature = -> Body090
  Placement = pos=(0,0,0) rot=(1,0,0;0.448799rad)
FEATURE [PartDesign::Body] Body093  label="Rivet 025"
  BaseFeature = -> Body090
  Group = -> [Clone051]
  Origin = -> Origin110
  Placement = pos=(0,0,0) rot=(1,0,0;2.69279rad)
  Tip = -> Clone051
FEATURE [PartDesign::FeatureBase] Clone052
  BaseFeature = -> Body090
  Placement = pos=(0,0,0) rot=(1,0,0;0.448799rad)
FEATURE [PartDesign::Body] Body094  label="Rivet 026"
  BaseFeature = -> Body090
  Group = -> [Clone052]
  Origin = -> Origin111
  Placement = pos=(0,0,0) rot=(1,0,0;3.59039rad)
  Tip = -> Clone052
FEATURE [PartDesign::FeatureBase] Clone053
  BaseFeature = -> Body090
  Placement = pos=(0,0,0) rot=(1,0,0;0.448799rad)
FEATURE [PartDesign::Body] Body095  label="Rivet 027"
  BaseFeature = -> Body090
  Group = -> [Clone053]
  Origin = -> Origin112
  Placement = pos=(0,0,0) rot=(-1,0,0;1.7952rad)
  Tip = -> Clone053
FEATURE [PartDesign::FeatureBase] Clone054
  BaseFeature = -> Body090
  Placement = pos=(0,0,0) rot=(1,0,0;0.448799rad)
FEATURE [PartDesign::Body] Body096  label="Rivet 028"
  BaseFeature = -> Body090
  Group = -> [Clone054]
  Origin = -> Origin113
  Placement = pos=(0,0,0) rot=(-1,0,0;0.897598rad)
  Tip = -> Clone054
FEATURE [App::DocumentObjectGroup] Group023  label="Rivets003"
  Group = -> [Body090,Body091,Body092,Body093,Body094,Body095,Body096]
FEATURE [Sketcher::SketchObject] Sketch087
  FullyConstrained = true
  MapMode = 5
  Placement = pos=(0,0,0) rot=(1,0,0;1.5708rad)
  Support = -> [XZ_Plane102]
  sketch-geometry (4):
    g0: LineSegment StartX=0 StartY=8.5 StartZ=0 EndX=0.1 EndY=8.5 EndZ=0
    g1: LineSegment StartX=0.1 StartY=8.5 StartZ=0 EndX=0.1 EndY=6.5 EndZ=0
    g2: LineSegment StartX=0.1 StartY=6.5 StartZ=0 EndX=0 EndY=6.5 EndZ=0
    g3: LineSegment StartX=0 StartY=6.5 StartZ=0 EndX=0 EndY=8.5 EndZ=0
  constraints (12):
    c: Coincident(g0,g1)
    c: Coincident(g1,g2)
    c: Coincident(g2,g3)
    c: Coincident(g3,g0)
    c: Horizontal(g0)
    c: Horizontal(g2)
    c: Vertical(g1)
    c: Vertical(g3)
    c: PointOnObject(g0,g-2)
    c: DistanceX(g0,g0) = 0.1
    c: DistanceY(g0) = 8.5
    c: DistanceY(g1) = 6.5
FEATURE [PartDesign::Revolution] Revolution027
  Angle = 360
  Axis = (1,0,0)
  Base = (0,0,0)
  Placement = pos=(0,0,0) rot=(1,0,0;1.5708rad)
  Profile = -> Sketch087
  ReferenceAxis = -> Sketch087 [H_Axis]
FEATURE [Sketcher::SketchObject] Sketch088
  FullyConstrained = true
  MapMode = 5
  Placement = pos=(0,0,0) rot=(0.57735,0.57735,0.57735;2.0944rad)
  Support = -> [YZ_Plane102]
  sketch-geometry (5):
    g0: ArcOfCircle CenterX=0 CenterY=7.5 CenterZ=0 NormalX=0 NormalY=0 NormalZ=1 AngleXU=0 Radius=2.11 StartAngle=5.66076 EndAngle=6.65667
    g1: LineSegment StartX=5e-16 StartY=8.5 StartZ=0 EndX=0 EndY=6.26986 EndZ=0
    g2: ArcOfCircle CenterX=0 CenterY=0 CenterZ=0 NormalX=0 NormalY=0 NormalZ=1 AngleXU=0 Radius=6.5 StartAngle=1.3039 EndAngle=1.5708
    g3: LineSegment StartX=1.71431 StartY=6.26986 StartZ=0 EndX=0 EndY=6.26986 EndZ=0
    g4: ArcOfCircle CenterX=0 CenterY=0 CenterZ=0 NormalX=0 NormalY=0 NormalZ=1 AngleXU=0 Radius=8.5 StartAngle=1.33757 EndAngle=1.5708
  constraints (16):
    c: PointOnObject(g0,g-2)
    c: DistanceY(g0) = 7.5
    c: Radius(g0) = 2.11
    c: PointOnObject(g2,g1)
    c: DistanceY(g2) = 6.5
    c: Coincident(g2,g-1)
    c: Coincident(g3,g2)
    c: Horizontal(g3)
    c: Coincident(g0,g2)
    c: Coincident(g1,g3)
    c: PointOnObject(g1,g-2)
    c: PointOnObject(g1,g-2)
    c: Coincident(g4,g-1)
    c: Coincident(g4,g1)
    c: DistanceY(g1) = 8.5
    c: Coincident(g0,g4)
FEATURE [PartDesign::Revolution] Revolution028
  Angle = 180
  Axis = (-2e-16,3e-16,1)
  Base = (0,0,0)
  BaseFeature = -> Revolution027
  Placement = pos=(0,0,0) rot=(1,0,0;1.5708rad)
  Profile = -> Sketch088
  ReferenceAxis = -> Sketch088 [V_Axis]
  Reversed = true
FEATURE [PartDesign::PolarPattern] PolarPattern012
  Angle = 360
  Axis = -> Sketch088 [N_Axis]
  BaseFeature = -> Revolution028
  Occurrences = 3
  Originals = -> [Revolution028]
  Placement = pos=(0,0,0) rot=(1,0,0;1.5708rad)
  Refine = true
FEATURE [Sketcher::SketchObject] Sketch089
  FullyConstrained = true
  MapMode = 5
  Placement = pos=(0,0,0) rot=(0.57735,0.57735,0.57735;2.0944rad)
  Support = -> [YZ_Plane102]
  sketch-geometry (4):
    g0: ArcOfCircle CenterX=0 CenterY=7.5 CenterZ=0 NormalX=0 NormalY=0 NormalZ=1 AngleXU=0 Radius=2.01 StartAngle=5.57985 EndAngle=6.86228
    g1: LineSegment StartX=0 StartY=6.2 StartZ=0 EndX=1.533 EndY=6.2 EndZ=0
    g2: LineSegment StartX=0 StartY=8.6 StartZ=0 EndX=0 EndY=6.2 EndZ=0
    g3: LineSegment StartX=0 StartY=8.6 StartZ=0 EndX=1.68229 EndY=8.6 EndZ=0
  constraints (13):
    c: PointOnObject(g0,g-2)
    c: DistanceY(g0) = 7.5
    c: Radius(g0) = 2.01
    c: PointOnObject(g1,g-2)
    c: Horizontal(g1)
    c: Coincident(g0,g1)
    c: DistanceY(g1) = 6.2
    c: DistanceY(g2) = 8.6
    c: Coincident(g2,g1)
    c: PointOnObject(g2,g-2)
    c: Coincident(g3,g2)
    c: Horizontal(g3)
    c: Coincident(g0,g3)
FEATURE [PartDesign::Groove] Groove003
  Angle = 360
  Axis = (-2e-16,3e-16,1)
  Base = (0,0,0)
  BaseFeature = -> PolarPattern012
  Placement = pos=(0,0,0) rot=(1,0,0;1.5708rad)
  Profile = -> Sketch089
  ReferenceAxis = -> Sketch089 [V_Axis]
FEATURE [PartDesign::PolarPattern] PolarPattern013
  Angle = 360
  Axis = -> Sketch089 [N_Axis]
  BaseFeature = -> Groove003
  Occurrences = 3
  Originals = -> [Groove003]
  Placement = pos=(0,0,0) rot=(1,0,0;1.5708rad)
FEATURE [PartDesign::Pocket] Pocket033
  BaseFeature = -> PolarPattern013
  Length = 5
  Length2 = 100
  Placement = pos=(0,0,0) rot=(1,0,0;1.5708rad)
  Profile = -> Sketch084
  Type = 1
FEATURE [PartDesign::PolarPattern] PolarPattern014
  Angle = 360
  Axis = -> Sketch084 [N_Axis]
  BaseFeature = -> Pocket033
  Occurrences = 3
  Originals = -> [Pocket033]
  Placement = pos=(0,0,0) rot=(1,0,0;1.5708rad)
FEATURE [PartDesign::Body] Body088  label="Cage 007"
  Group = -> [Sketch087,Revolution027,Sketch088,Revolution028,PolarPattern012,Sketch089,Groove003,PolarPattern013,Sketch084,Pocket033,PolarPattern014]
  Origin = -> Origin105
  Placement = pos=(0,0,0) rot=(-1,0,0;1.5708rad)
  Tip = -> PolarPattern014
FEATURE [PartDesign::FeatureBase] Clone048
  BaseFeature = -> Body088
  Placement = pos=(0,0,0) rot=(-1,0,0;1.5708rad)
FEATURE [PartDesign::Body] Body089  label="Cage 008"
  BaseFeature = -> Body088
  Group = -> [Clone048]
  Origin = -> Origin106
  Placement = pos=(0,0,0) rot=(0,1,0;3.14159rad)
  Tip = -> Clone048
FEATURE [App::DocumentObjectGroup] Group022  label="Cages003"
  Group = -> [Body088,Body089]
FEATURE [Sketcher::SketchObject] Sketch090
  FullyConstrained = true
  MapMode = 5
  Support = -> [XY_Plane111]
  sketch-geometry (14):
    g0: ArcOfCircle CenterX=-1e-16 CenterY=7.5 CenterZ=0 NormalX=0 NormalY=0 NormalZ=1 AngleXU=0 Radius=2 StartAngle=0.848062 EndAngle=2.29353
    g1: LineSegment StartX=-3.5 StartY=11 StartZ=0 EndX=3.5 EndY=11 EndZ=0
    g2: LineSegment StartX=3.5 StartY=11 StartZ=0 EndX=3.5 EndY=9.2 EndZ=0
    g3: LineSegment StartX=2.9 StartY=9 StartZ=0 EndX=1.32288 EndY=9 EndZ=0
    g4: LineSegment StartX=-3.5 StartY=9.2 StartZ=0 EndX=-3.5 EndY=11 EndZ=0
    g5: LineSegment StartX=-1.32288 StartY=9 StartZ=0 EndX=-2.9 EndY=9 EndZ=0
    g6: LineSegment StartX=2.9 StartY=9 StartZ=0 EndX=2.9 EndY=9.5 EndZ=0
    g7: LineSegment StartX=2.9 StartY=9.5 StartZ=0 EndX=3.2 EndY=9.5 EndZ=0
    g8: LineSegment StartX=3.2 StartY=9.5 StartZ=0 EndX=3.2 EndY=9.2 EndZ=0
    g9: LineSegment StartX=3.2 StartY=9.2 StartZ=0 EndX=3.5 EndY=9.2 EndZ=0
    g10: LineSegment StartX=-3.5 StartY=9.2 StartZ=0 EndX=-3.2 EndY=9.2 EndZ=0
    g11: LineSegment StartX=-3.2 StartY=9.2 StartZ=0 EndX=-3.2 EndY=9.5 EndZ=0
    g12: LineSegment StartX=-3.2 StartY=9.5 StartZ=0 EndX=-2.9 EndY=9.5 EndZ=0
    g13: LineSegment StartX=-2.9 StartY=9.5 StartZ=0 EndX=-2.9 EndY=9 EndZ=0
  constraints (41):
    c: Coincident(g1,g2)
    c: Coincident(g4,g1)
    c: Horizontal(g3)
    c: Vertical(g2)
    c: Vertical(g4)
    c: Coincident(g0,g5)
    c: Coincident(g0,g3)
    c: DistanceY(g-1,g0) = 7.5
    c: Radius(g0) = 2
    c: Symmetric(g1,g1,g-2)
    c: Symmetric(g0,g0,g-2)
    c: DistanceY(g1) = 11
    c: DistanceX(g1,g1) = 7
    c: Vertical(g6)
    c: Coincident(g6,g7)
    c: Horizontal(g7)
    c: Coincident(g7,g8)
    c: Vertical(g8)
    c: Coincident(g8,g9)
    c: Coincident(g3,g6)
    c: Coincident(g2,g9)
    c: Horizontal(g10)
    c: Coincident(g10,g11)
    c: Coincident(g11,g12)
    c: Horizontal(g12)
    c: Coincident(g12,g13)
    c: Vertical(g13)
    c: Vertical(g11)
    c: Coincident(g4,g10)
    c: Coincident(g5,g13)
    c: DistanceY(g13,g13) = 0.5
    c: DistanceX(g12,g12) = 0.3
    c: DistanceY(g5,g10) = 0.2
    c: Symmetric(g5,g3,g-2)
    c: DistanceY(g3) = 9
    c: DistanceY(g6) = 9.5
    c: Equal(g7,g12)
    c: Equal(g13,g6)
    c: Horizontal(g9)
    c: Horizontal(g8,g10)
    c: Equal(g12,g10)
FEATURE [PartDesign::Revolution] Revolution029
  Angle = 360
  Axis = (1,0,0)
  Base = (0,0,0)
  Profile = -> Sketch090
  ReferenceAxis = -> X_Axis111
FEATURE [PartDesign::Fillet] Fillet163
  Base = -> Revolution029 [Edge14,Edge15]
  BaseFeature = -> Revolution029
  Radius = 0.3
  SupportTransform = false
FEATURE [PartDesign::Body] Body097  label="Outer Ring004"
  Group = -> [Sketch090,Revolution029,Fillet163]
  Origin = -> Origin114
  Tip = -> Fillet163
FEATURE [Sketcher::SketchObject] Sketch091
  FullyConstrained = true
  MapMode = 5
  Support = -> [XY_Plane112]
  sketch-geometry (14):
    g0: LineSegment StartX=-2.9 StartY=6 StartZ=0 EndX=-1.32288 EndY=6 EndZ=0
    g1: LineSegment StartX=-3.5 StartY=4 StartZ=0 EndX=-3.5 EndY=5.7 EndZ=0
    g2: ArcOfCircle CenterX=-1e-16 CenterY=7.5 CenterZ=0 NormalX=0 NormalY=0 NormalZ=1 AngleXU=0 Radius=2 StartAngle=3.98965 EndAngle=5.43512
    g3: LineSegment StartX=1.32288 StartY=6 StartZ=0 EndX=2.9 EndY=6 EndZ=0
    g4: LineSegment StartX=-3.5 StartY=5.7 StartZ=0 EndX=-3.2 EndY=5.7 EndZ=0
    g5: LineSegment StartX=-3.2 StartY=5.7 StartZ=0 EndX=-3.2 EndY=5.5 EndZ=0
    g6: LineSegment StartX=-3.2 StartY=5.5 StartZ=0 EndX=-2.9 EndY=5.5 EndZ=0
    g7: LineSegment StartX=-2.9 StartY=5.5 StartZ=0 EndX=-2.9 EndY=6 EndZ=0
    g8: LineSegment StartX=8.5 StartY=6 StartZ=0 EndX=3.2 EndY=6 EndZ=0
    g9: LineSegment StartX=3.2 StartY=6 StartZ=0 EndX=3.2 EndY=5.5 EndZ=0
    g10: LineSegment StartX=3.2 StartY=5.5 StartZ=0 EndX=2.9 EndY=5.5 EndZ=0
    g11: LineSegment StartX=2.9 StartY=5.5 StartZ=0 EndX=2.9 EndY=6 EndZ=0
    g12: LineSegment StartX=8.5 StartY=4 StartZ=0 EndX=8.5 EndY=6 EndZ=0
    g13: LineSegment StartX=-3.5 StartY=4 StartZ=0 EndX=8.5 EndY=4 EndZ=0
  constraints (43):
    c: Horizontal(g0)
    c: Vertical(g1)
    c: DistanceY(g1) = 4
    c: Coincident(g2,g0)
    c: Coincident(g2,g3)
    c: Horizontal(g3)
    c: Radius(g2) = 2
    c: DistanceY(g2) = 7.5
    c: Symmetric(g0,g2,g-2)
    c: Horizontal(g4)
    c: Coincident(g4,g5)
    c: Vertical(g5)
    c: Coincident(g5,g6)
    c: Horizontal(g6)
    c: Coincident(g6,g7)
    c: Vertical(g7)
    c: Horizontal(g8)
    c: Coincident(g8,g9)
    c: Vertical(g9)
    c: Coincident(g9,g10)
    c: Horizontal(g10)
    c: Coincident(g10,g11)
    c: Vertical(g11)
    c: Coincident(g3,g11)
    c: Coincident(g0,g7)
    c: Coincident(g1,g4)
    c: DistanceY(g3) = 6
    c: DistanceY(g6,g0) = 0.5
    c: DistanceX(g4,g4) = 0.3
    c: DistanceX(g6,g6) = 0.3
    c: DistanceY(g5,g4) = 0.2
    c: Vertical(g12)
    c: Equal(g11,g7)
    c: DistanceY(g1,g0) = 2
    c: DistanceX(g8,g8) = 5.3
    c: Coincident(g13,g1)
    c: Coincident(g13,g12)
    c: Horizontal(g13)
    c: DistanceX(g13,g13) = 12
    c: DistanceX(g1,g2) = 3.5
    c: Coincident(g8,g12)
    c: Equal(g7,g9)
    c: Equal(g6,g10)
FEATURE [PartDesign::Revolution] Revolution030
  Angle = 360
  Axis = (1,0,0)
  Base = (0,0,0)
  Profile = -> Sketch091
  ReferenceAxis = -> X_Axis112
FEATURE [PartDesign::Fillet] Fillet164
  Base = -> Revolution030 [Edge13,Edge11]
  BaseFeature = -> Revolution030
  Radius = 0.2
  SupportTransform = false
FEATURE [PartDesign::Body] Body098  label="Inner Ring004"
  Group = -> [Sketch091,Revolution030,Fillet164]
  Origin = -> Origin115
  Tip = -> Fillet164
FEATURE [App::DocumentObjectGroup] Group025  label="Rings003"
  Group = -> [Body097,Body098]
FEATURE [Sketcher::SketchObject] Sketch092
  FullyConstrained = true
  MapMode = 5
  Placement = pos=(0,0,0) rot=(1,0,0;1.5708rad)
  Support = -> [XZ_Plane113]
  sketch-geometry (12):
    g0: LineSegment StartX=2.9 StartY=9.5 StartZ=0 EndX=2.9 EndY=8.5 EndZ=0
    g1: LineSegment StartX=2.9 StartY=8.5 StartZ=0 EndX=3.2 EndY=8.5 EndZ=0
    g2: LineSegment StartX=3.2 StartY=8.5 StartZ=0 EndX=3.2 EndY=6.5 EndZ=0
    g3: LineSegment StartX=3.2 StartY=6.5 StartZ=0 EndX=2.9 EndY=6.5 EndZ=0
    g4: LineSegment StartX=2.9 StartY=6.5 StartZ=0 EndX=2.9 EndY=5.5 EndZ=0
    g5: LineSegment StartX=2.9 StartY=5.5 StartZ=0 EndX=3.2 EndY=5.5 EndZ=0
    g6: LineSegment StartX=3.2 StartY=5.5 StartZ=0 EndX=3.2 EndY=6 EndZ=0
    g7: LineSegment StartX=3.2 StartY=6 StartZ=0 EndX=3.5 EndY=6 EndZ=0
    g8: LineSegment StartX=3.5 StartY=6 StartZ=0 EndX=3.5 EndY=9 EndZ=0
    g9: LineSegment StartX=3.5 StartY=9 StartZ=0 EndX=3.2 EndY=9 EndZ=0
    g10: LineSegment StartX=3.2 StartY=9 StartZ=0 EndX=3.2 EndY=9.5 EndZ=0
    g11: LineSegment StartX=3.2 StartY=9.5 StartZ=0 EndX=2.9 EndY=9.5 EndZ=0
  constraints (36):
    c: Vertical(g0)
    c: Coincident(g0,g1)
    c: Horizontal(g1)
    c: Coincident(g1,g2)
    c: Vertical(g2)
    c: Coincident(g2,g3)
    c: Horizontal(g3)
    c: Coincident(g3,g4)
    c: Vertical(g4)
    c: Coincident(g4,g5)
    c: Horizontal(g5)
    c: Coincident(g5,g6)
    c: Vertical(g6)
    c: Coincident(g6,g7)
    c: Horizontal(g7)
    c: Coincident(g7,g8)
    c: Vertical(g8)
    c: Coincident(g8,g9)
    c: Horizontal(g9)
    c: Coincident(g9,g10)
    c: Vertical(g10)
    c: Coincident(g10,g11)
    c: Coincident(g11,g0)
    c: Horizontal(g11)
    c: DistanceY(g4) = 5.5
    c: DistanceX(g4) = 2.9
    c: DistanceY(g5,g6) = 0.5
    c: DistanceY(g6,g2) = 0.5
    c: DistanceX(g5,g5) = 0.3
    c: Equal(g5,g7)
    c: Equal(g7,g3)
    c: Equal(g3,g1)
    c: Equal(g1,g9)
    c: Equal(g4,g0)
    c: Equal(g6,g10)
    c: DistanceY(g4,g0) = 4
FEATURE [PartDesign::Revolution] Revolution031
  Angle = 360
  Axis = (1,0,0)
  Base = (0,0,0)
  Placement = pos=(0,0,0) rot=(1,0,0;1.5708rad)
  Profile = -> Sketch092
  ReferenceAxis = -> Sketch092 [H_Axis]
FEATURE [PartDesign::Fillet] Fillet165
  Base = -> Revolution031 [Edge14,Edge12]
  BaseFeature = -> Revolution031
  Placement = pos=(0,0,0) rot=(1,0,0;1.5708rad)
  Radius = 0.2
  SupportTransform = false
FEATURE [PartDesign::Body] Body099  label="Seal 007"
  Group = -> [Sketch092,Revolution031,Fillet165]
  Origin = -> Origin116
  Tip = -> Fillet165
FEATURE [PartDesign::FeatureBase] Clone055
  BaseFeature = -> Body099
FEATURE [PartDesign::Body] Body100  label="Seal 008"
  BaseFeature = -> Body099
  Group = -> [Clone055]
  Origin = -> Origin117
  Placement = pos=(0,0,0) rot=(0,1,0;3.14159rad)
  Tip = -> Clone055
FEATURE [App::DocumentObjectGroup] Group024  label="Seals003"
  Group = -> [Body099,Body100]
FEATURE [Sketcher::SketchObject] Sketch093
  AttachmentOffset = pos=(0,0,4) rot=(0,0,1;0rad)
  FullyConstrained = true
  MapMode = 5
  Placement = pos=(0,0,4) rot=(0,0,1;0rad)
  Support = -> [XY_Plane094]
  sketch-geometry (1):
    g0: Circle CenterX=6 CenterY=0 CenterZ=0 NormalX=0 NormalY=0 NormalZ=1 AngleXU=0 Radius=1.5
  constraints (3):
    c: PointOnObject(g0,g-1)
    c: Diameter(g0) = 3
    c: DistanceX(g-1,g0) = 6
FEATURE [PartDesign::Pad] Pad020
  Direction = (0,0,1)
  Length = 3
  Length2 = 100
  Profile = -> Sketch093
  Type = 0
FEATURE [Sketcher::SketchObject] Sketch094
  ExternalGeometry = -> [Pad020]
  FullyConstrained = true
  MapMode = 5
  Placement = pos=(0,0,7) rot=(0,0,1;0rad)
  Support = -> [Pad020]
  sketch-geometry (7):
    g0: LineSegment StartX=6.43301 StartY=-0.75 StartZ=0 EndX=6.86603 EndY=0 EndZ=0
    g1: LineSegment StartX=6.86603 StartY=0 StartZ=0 EndX=6.43301 EndY=0.75 EndZ=0
    g2: LineSegment StartX=6.43301 StartY=0.75 StartZ=0 EndX=5.56699 EndY=0.75 EndZ=0
    g3: LineSegment StartX=5.56699 StartY=0.75 StartZ=0 EndX=5.13397 EndY=-1e-16 EndZ=0
    g4: LineSegment StartX=5.13397 StartY=-1e-16 StartZ=0 EndX=5.56699 EndY=-0.75 EndZ=0
    g5: LineSegment StartX=5.56699 StartY=-0.75 StartZ=0 EndX=6.43301 EndY=-0.75 EndZ=0
    g6: Circle CenterX=6 CenterY=0 CenterZ=0 NormalX=0 NormalY=0 NormalZ=1 AngleXU=0 Radius=0.866025
  constraints (16):
    c: Coincident(g0,g1)
    c: Coincident(g1,g2)
    c: Coincident(g2,g3)
    c: Coincident(g3,g4)
    c: Coincident(g4,g5)
    c: Coincident(g5,g0)
    c: Equal(g0, g1-g5) x5
    c: PointOnObject(g0,g6)
    c: PointOnObject(g1,g6)
    c: PointOnObject(g2,g6)
    c: PointOnObject(g3,g6)
    c: PointOnObject(g4,g6)
    c: PointOnObject(g5,g6)
    c: Coincident(g6,g-3)
    c: Horizontal(g5)
    c: DistanceY(g4,g2) = 1.5
FEATURE [PartDesign::Pocket] Pocket034
  BaseFeature = -> Pad020
  Length = 0.9
  Length2 = 100
  Profile = -> Sketch094
  Type = 0
FEATURE [PartDesign::PolarPattern] PolarPattern015
  Angle = 120
  Axis = -> X_Axis094
  BaseFeature = -> Pocket034
  Occurrences = 3
  Originals = -> [Pad020,Pocket034]
FEATURE [PartDesign::Body] Body080
  Group = -> [Sketch093,Pad020,Sketch094,Pocket034,PolarPattern015]
  Origin = -> Origin097
  Tip = -> PolarPattern015
FEATURE [App::DocumentObjectGroup] Group026  label="Set screws003"
  Group = -> [Body080]
FEATURE [Sketcher::SketchObject] Sketch095
  AttachmentOffset = pos=(0,0,-6.5) rot=(0,0,1;0rad)
  FullyConstrained = true
  MapMode = 5
  Placement = pos=(-6.5,1.4e-15,-1.4e-15) rot=(0.57735,0.57735,0.57735;2.0944rad)
  Support = -> [YZ_Plane115]
  sketch-geometry (14):
    g0: Circle CenterX=0 CenterY=0 CenterZ=0 NormalX=0 NormalY=0 NormalZ=1 AngleXU=0 Radius=11
    g1: ArcOfCircle CenterX=0 CenterY=0 CenterZ=0 NormalX=0 NormalY=0 NormalZ=1 AngleXU=0 Radius=13.5 StartAngle=0.0668757 EndAngle=3.07472
    g2: LineSegment StartX=-13.4698 StartY=0.902148 StartZ=0 EndX=-14.2 EndY=-10 EndZ=0
    g3: LineSegment StartX=-14.2 StartY=-10 StartZ=0 EndX=-27.5 EndY=-10 EndZ=0
    g4: LineSegment StartX=-27.5 StartY=-10 StartZ=0 EndX=-27.5 EndY=-15 EndZ=0
    g5: LineSegment StartX=-27.5 StartY=-15 StartZ=0 EndX=-12.3 EndY=-15 EndZ=0
    g6: LineSegment StartX=27.5 StartY=-15 StartZ=0 EndX=27.5 EndY=-10 EndZ=0
    g7: LineSegment StartX=27.5 StartY=-10 StartZ=0 EndX=14.2 EndY=-10 EndZ=0
    g8: LineSegment StartX=14.2 StartY=-10 StartZ=0 EndX=13.4698 EndY=0.902148 EndZ=0
    g9: LineSegment StartX=12.3 StartY=-15 StartZ=0 EndX=12.1995 EndY=-13.5 EndZ=0
    g10: LineSegment StartX=12.1995 StartY=-13.5 StartZ=0 EndX=-12.1995 EndY=-13.5 EndZ=0
    g11: LineSegment StartX=-12.1995 StartY=-13.5 StartZ=0 EndX=-12.3 EndY=-15 EndZ=0
    g12: LineSegment StartX=12.3 StartY=-15 StartZ=0 EndX=27.5 EndY=-15 EndZ=0
    g13: GeomPoint X=0 Y=13.5 Z=0
  constraints (39):
    c: Coincident(g0,g-1)
    c: Radius(g0) = 11
    c: Coincident(g1,g0)
    c: Coincident(g2,g3)
    c: Coincident(g3,g4)
    c: Coincident(g4,g5)
    c: Horizontal(g5)
    c: Coincident(g12,g6)
    c: Coincident(g6,g7)
    c: Horizontal(g7)
    c: Coincident(g7,g8)
    c: Coincident(g9,g10)
    c: Horizontal(g10)
    c: Coincident(g10,g11)
    c: Coincident(g5,g11)
    c: Coincident(g12,g9)
    c: Horizontal(g3)
    c: Vertical(g6)
    c: Vertical(g4)
    c: Equal(g9,g11)
    c: Horizontal(g12)
    c: Horizontal(g5,g9)
    c: Equal(g6,g4)
    c: Equal(g12,g5)
    c: Equal(g7,g3)
    c: DistanceX(g4,g6) = 55
    c: DistanceY(g6,g0) = 15
    c: Equal(g8,g2)
    c: DistanceY(g6,g6) = 5
    c: Parallel(g9,g8)
    c: DistanceY(g9,g9) = 1.5
    c: DistanceX(g5,g5) = 15.2
    c: Diameter(g1) = 27
    c: PointOnObject(g13,g1)
    c: PointOnObject(g13,g-2)
    c: DistanceY(g6,g13) = 28.5
    c: Tangent(g1,g2) = -1.5708
    c: Tangent(g1,g8) = -1.5708
    c: DistanceX(g3,g3) = 13.3
FEATURE [PartDesign::Pad] Pad021
  Direction = (1,-2e-16,3e-16)
  Length = 13
  Length2 = 100
  Placement = pos=(0,0,0) rot=(0.57735,0.57735,0.57735;2.0944rad)
  Profile = -> Sketch095
  Type = 0
FEATURE [Sketcher::SketchObject] Sketch096
  ExternalGeometry = -> [Pad021]
  FullyConstrained = true
  MapMode = 5
  Placement = pos=(4.2e-15,-6.6e-15,-15) rot=(0.707107,0.707107,0;3.14159rad)
  Support = -> [Pad021]
  sketch-geometry (7):
    g0: LineSegment StartX=-24.9 StartY=4.15 StartZ=0 EndX=-14.9 EndY=4.15 EndZ=0
    g1: LineSegment StartX=-14.9 StartY=4.15 StartZ=0 EndX=-14.9 EndY=-4.15 EndZ=0
    g2: LineSegment StartX=-14.9 StartY=-4.15 StartZ=0 EndX=-24.9 EndY=-4.15 EndZ=0
    g3: LineSegment StartX=-24.9 StartY=-4.15 StartZ=0 EndX=-24.9 EndY=4.15 EndZ=0
    g4: LineSegment StartX=-27.5 StartY=6.5 StartZ=0 EndX=-12.3 EndY=-6.5 EndZ=0
    g5: LineSegment StartX=-27.5 StartY=-6.5 StartZ=0 EndX=-12.3 EndY=6.5 EndZ=0
    g6: GeomPoint X=-19.9 Y=2.6e-15 Z=0
  constraints (17):
    c: Coincident(g0,g1)
    c: Coincident(g1,g2)
    c: Coincident(g2,g3)
    c: Coincident(g3,g0)
    c: Horizontal(g0)
    c: Horizontal(g2)
    c: Vertical(g1)
    c: Vertical(g3)
    c: DistanceX(g0,g0) = 10
    c: DistanceY(g1,g1) = 8.3
    c: Coincident(g4,g-3)
    c: Coincident(g4,g-4)
    c: Coincident(g5,g-4)
    c: Coincident(g5,g-3)
    c: PointOnObject(g6,g4)
    c: PointOnObject(g6,g5)
    c: Symmetric(g0,g1,g6)
FEATURE [PartDesign::Pocket] Pocket035
  BaseFeature = -> Pad021
  Length = 2.3
  Length2 = 100
  Placement = pos=(0,0,0) rot=(0.57735,0.57735,0.57735;2.0944rad)
  Profile = -> Sketch096
  Type = 0
FEATURE [Sketcher::SketchObject] Sketch097
  ExternalGeometry = -> [Pocket035]
  FullyConstrained = true
  MapMode = 5
  Placement = pos=(2.8e-15,-4.4e-15,-10) rot=(0,0,-1;1.5708rad)
  Support = -> [Pocket035]
  sketch-geometry (2):
    g0: Circle CenterX=21.2 CenterY=2.1e-15 CenterZ=0 NormalX=0 NormalY=0 NormalZ=1 AngleXU=0 Radius=2.5
    g1: LineSegment StartX=21.2 StartY=2.1e-15 StartZ=0 EndX=27.5 EndY=2.1e-15 EndZ=0
  constraints (5):
    c: Diameter(g0) = 5
    c: DistanceX(g0,g-3) = 6.3
    c: Coincident(g1,g0)
    c: Horizontal(g1)
    c: Symmetric(g-5,g-5,g1)
FEATURE [PartDesign::Pocket] Pocket036
  BaseFeature = -> Pocket035
  Length = 5
  Length2 = 100
  Placement = pos=(0,0,0) rot=(0.57735,0.57735,0.57735;2.0944rad)
  Profile = -> Sketch097
  Type = 2
FEATURE [Sketcher::SketchObject] Sketch098
  ExternalGeometry = -> [Pocket036]
  FullyConstrained = true
  MapMode = 5
  Placement = pos=(6.5,-1.4e-15,1.5e-15) rot=(0.57735,0.57735,0.57735;2.0944rad)
  Support = -> [Pocket036]
  sketch-geometry (6):
    g0: LineSegment StartX=-24.6 StartY=-13.7 StartZ=0 EndX=-24.6 EndY=-11.3 EndZ=0
    g1: LineSegment StartX=-24.6 StartY=-11.3 StartZ=0 EndX=-14.2 EndY=-11.3 EndZ=0
    g2: LineSegment StartX=-14.2 StartY=-11.3 StartZ=0 EndX=-14.2 EndY=-13.7 EndZ=0
    g3: LineSegment StartX=-14.2 StartY=-13.7 StartZ=0 EndX=-24.6 EndY=-13.7 EndZ=0
    g4: GeomPoint X=-19.4 Y=-12.5 Z=0
    g5: LineSegment StartX=-19.4 StartY=-12.5 StartZ=0 EndX=-27.5 EndY=-12.5 EndZ=0
  constraints (15):
    c: Coincident(g0,g1)
    c: Coincident(g1,g2)
    c: Coincident(g2,g3)
    c: Coincident(g3,g0)
    c: Horizontal(g1)
    c: Horizontal(g3)
    c: Vertical(g0)
    c: Vertical(g2)
    c: Symmetric(g1,g0,g4)
    c: DistanceX(g1,g1) = 10.4
    c: DistanceY(g2,g2) = 2.4
    c: DistanceX(g2,g-4) = 1.9
    c: Coincident(g5,g4)
    c: Horizontal(g5)
    c: Symmetric(g-5,g-5,g5)
FEATURE [PartDesign::Pocket] Pocket037
  BaseFeature = -> Pocket036
  Length = 0.4
  Length2 = 100
  Placement = pos=(0,0,0) rot=(0.57735,0.57735,0.57735;2.0944rad)
  Profile = -> Sketch098
  Type = 0
FEATURE [PartDesign::Mirrored] Mirrored003
  BaseFeature = -> Pocket037
  MirrorPlane = -> Sketch096 [V_Axis]
  Originals = -> [Pocket035,Pocket036,Pocket037]
  Placement = pos=(0,0,0) rot=(0.57735,0.57735,0.57735;2.0944rad)
FEATURE [Sketcher::SketchObject] Sketch099
  ExternalGeometry = -> [Mirrored003]
  FullyConstrained = true
  MapMode = 5
  Placement = pos=(0,0,0) rot=(1,0,0;1.5708rad)
  Support = -> [XZ_Plane115]
  sketch-geometry (9):
    g0: GeomPoint X=-6.5 Y=13.5 Z=0
    g1: LineSegment StartX=6.5 StartY=-10 StartZ=0 EndX=6.5 EndY=13.5 EndZ=0
    g2: LineSegment StartX=6.5 StartY=13.5 StartZ=0 EndX=4.75 EndY=13.5 EndZ=0
    g3: LineSegment StartX=-6.5 StartY=13.5 StartZ=0 EndX=-4.75 EndY=13.5 EndZ=0
    g4: LineSegment StartX=-6.5 StartY=-10 StartZ=0 EndX=-6.5 EndY=13.5 EndZ=0
    g5: LineSegment StartX=6.5 StartY=-10 StartZ=0 EndX=4.75 EndY=-1 EndZ=0
    g6: LineSegment StartX=4.75 StartY=-1 StartZ=0 EndX=4.75 EndY=13.5 EndZ=0
    g7: LineSegment StartX=-4.75 StartY=13.5 StartZ=0 EndX=-4.75 EndY=-1 EndZ=0
    g8: LineSegment StartX=-4.75 StartY=-1 StartZ=0 EndX=-6.5 EndY=-10 EndZ=0
  constraints (24):
    c: Vertical(g0,g-4)
    c: Horizontal(g-3,g0)
    c: Coincident(g1,g-3)
    c: Coincident(g1,g2)
    c: Horizontal(g2)
    c: Coincident(g3,g0)
    c: Horizontal(g3)
    c: Coincident(g4,g3)
    c: Vertical(g4,g-4)
    c: DistanceX(g3,g2) = 9.5
    c: Equal(g2,g3)
    c: Horizontal(g1,g4)
    c: Coincident(g1,g-5)
    c: Coincident(g1,g5)
    c: Coincident(g5,g6)
    c: Coincident(g6,g2)
    c: Vertical(g6)
    c: DistanceY(g1,g5) = 9
    c: Coincident(g3,g7)
    c: Vertical(g7)
    c: Coincident(g7,g8)
    c: Coincident(g8,g4)
    c: Horizontal(g7,g5)
    c: DistanceX(g2,g2) = 1.75
FEATURE [PartDesign::Pocket] Pocket038
  BaseFeature = -> Mirrored003
  Length = 15
  Length2 = 15
  Placement = pos=(0,0,0) rot=(0.57735,0.57735,0.57735;2.0944rad)
  Profile = -> Sketch099
  Type = 4
FEATURE [Sketcher::SketchObject] Sketch100
  FullyConstrained = true
  MapMode = 5
  Placement = pos=(-6.5,1.4e-15,-1.5e-15) rot=(0.57735,0.57735,-0.57735;4.18879rad)
  Support = -> [Pocket038]
  sketch-geometry (1):
    g0: Circle CenterX=0 CenterY=0 CenterZ=0 NormalX=0 NormalY=0 NormalZ=1 AngleXU=0 Radius=12.2
  constraints (2):
    c: Coincident(g0,g-1)
    c: Diameter(g0) = 24.4
FEATURE [PartDesign::Pocket] Pocket039
  BaseFeature = -> Pocket038
  Length = 2.75
  Length2 = 100
  Placement = pos=(0,0,0) rot=(0.57735,0.57735,0.57735;2.0944rad)
  Profile = -> Sketch100
  Type = 0
FEATURE [Sketcher::SketchObject] Sketch101
  FullyConstrained = true
  MapMode = 5
  Placement = pos=(6.5,-1.4e-15,1.5e-15) rot=(0.57735,0.57735,0.57735;2.0944rad)
  Support = -> [Pocket039]
  sketch-geometry (1):
    g0: Circle CenterX=0 CenterY=0 CenterZ=0 NormalX=0 NormalY=0 NormalZ=1 AngleXU=0 Radius=12.1
  constraints (2):
    c: Coincident(g0,g-1)
    c: Diameter(g0) = 24.2
FEATURE [PartDesign::Pocket] Pocket040
  BaseFeature = -> Pocket039
  Length = 2.75
  Length2 = 100
  Placement = pos=(0,0,0) rot=(0.57735,0.57735,0.57735;2.0944rad)
  Profile = -> Sketch101
  Type = 0
FEATURE [Sketcher::SketchObject] Sketch102
  ExternalGeometry = -> [Pocket040]
  FullyConstrained = true
  MapMode = 5
  Placement = pos=(6.5,-1.4e-15,1.5e-15) rot=(0.57735,0.57735,0.57735;2.0944rad)
  Support = -> [Pocket040]
  sketch-geometry (6):
    g0: ArcOfCircle CenterX=0 CenterY=0 CenterZ=0 NormalX=0 NormalY=0 NormalZ=1 AngleXU=0 Radius=13.5 StartAngle=3.79664 EndAngle=5.62814
    g1: LineSegment StartX=-11.8698 StartY=-8.57666 StartZ=0 EndX=-12.3 EndY=-15 EndZ=0
    g2: LineSegment StartX=-12.3 StartY=-15 StartZ=0 EndX=12.3 EndY=-15 EndZ=0
    g3: LineSegment StartX=12.3 StartY=-15 StartZ=0 EndX=11.8698 EndY=-8.57666 EndZ=0
    g4: ArcOfCircle CenterX=11.2212 CenterY=-8.6201 CenterZ=0 NormalX=0 NormalY=0 NormalZ=1 AngleXU=0 Radius=0.65 StartAngle=0.0668757 EndAngle=2.48655
    g5: ArcOfCircle CenterX=-11.2212 CenterY=-8.6201 CenterZ=0 NormalX=0 NormalY=0 NormalZ=1 AngleXU=0 Radius=0.65 StartAngle=0.655044 EndAngle=3.07472
  constraints (14):
    c: Coincident(g0,g-1)
    c: Diameter(g0) = 27
    c: Coincident(g1,g2)
    c: Coincident(g2,g3)
    c: Coincident(g1,g-3)
    c: Coincident(g2,g-4)
    c: Tangent(g3,g4) = -1.5708
    c: Tangent(g0,g4) = 1.5708
    c: Tangent(g0,g5) = 1.5708
    c: Tangent(g1,g5) = -1.5708
    c: Equal(g4,g5)
    c: Horizontal(g4,g5)
    c: Parallel(g-4,g3)
    c: Radius(g4) = 0.65
FEATURE [PartDesign::Pocket] Pocket041
  BaseFeature = -> Pocket040
  Length = 5.25
  Length2 = 100
  Placement = pos=(0,0,0) rot=(0.57735,0.57735,0.57735;2.0944rad)
  Profile = -> Sketch102
  Type = 0
FEATURE [Sketcher::SketchObject] Sketch103
  ExternalGeometry = -> [Pocket041]
  FullyConstrained = true
  MapMode = 5
  Placement = pos=(-6.5,1.4e-15,-1.5e-15) rot=(0.57735,0.57735,-0.57735;4.18879rad)
  Support = -> [Pocket041]
  sketch-geometry (6):
    g0: ArcOfCircle CenterX=0 CenterY=0 CenterZ=0 NormalX=0 NormalY=0 NormalZ=1 AngleXU=0 Radius=13.5 StartAngle=0.655044 EndAngle=2.48655
    g1: LineSegment StartX=11.8698 StartY=8.57666 StartZ=0 EndX=12.3 EndY=15 EndZ=0
    g2: LineSegment StartX=12.3 StartY=15 StartZ=0 EndX=-12.3 EndY=15 EndZ=0
    g3: LineSegment StartX=-12.3 StartY=15 StartZ=0 EndX=-11.8698 EndY=8.57666 EndZ=0
    g4: ArcOfCircle CenterX=-11.2212 CenterY=8.6201 CenterZ=0 NormalX=0 NormalY=0 NormalZ=1 AngleXU=0 Radius=0.65 StartAngle=3.20847 EndAngle=5.62814
    g5: ArcOfCircle CenterX=11.2212 CenterY=8.6201 CenterZ=0 NormalX=0 NormalY=0 NormalZ=1 AngleXU=0 Radius=0.65 StartAngle=3.79664 EndAngle=6.21631
  constraints (14):
    c: Coincident(g0,g-1)
    c: Radius(g0) = 13.5
    c: Coincident(g1,g2)
    c: Coincident(g2,g-3)
    c: Coincident(g2,g3)
    c: Coincident(g-4,g1)
    c: Tangent(g3,g4) = -1.5708
    c: Tangent(g0,g4) = 1.5708
    c: Tangent(g0,g5) = 1.5708
    c: Tangent(g1,g5) = -1.5708
    c: Equal(g4,g5)
    c: Radius(g4) = 0.65
    c: Parallel(g-4,g1)
    c: Parallel(g3,g-3)
FEATURE [PartDesign::Pocket] Pocket042
  BaseFeature = -> Pocket041
  Length = 5.25
  Length2 = 100
  Placement = pos=(0,0,0) rot=(0.57735,0.57735,0.57735;2.0944rad)
  Profile = -> Sketch103
  Type = 0
FEATURE [PartDesign::Chamfer] Chamfer003
  Angle = 45
  Base = -> Pocket042 [Edge159,Edge155,Edge22,Edge27]
  BaseFeature = -> Pocket042
  ChamferType = 0
  FlipDirection = false
  Placement = pos=(0,0,0) rot=(0.57735,0.57735,0.57735;2.0944rad)
  Size = 2
  Size2 = 1
  SupportTransform = false
FEATURE [Sketcher::SketchObject] Sketch104
  ExternalGeometry = -> [Chamfer003]
  FullyConstrained = true
  MapMode = 5
  Placement = pos=(-3.75,5e-15,-2.7e-15) rot=(-0.57735,-0.57735,0.57735;2.0944rad)
  Support = -> [Chamfer003]
  sketch-geometry (13):
    g0: ArcOfCircle CenterX=-6.9e-15 CenterY=-3.7e-15 CenterZ=0 NormalX=0 NormalY=0 NormalZ=1 AngleXU=0 Radius=11 StartAngle=5.75419 EndAngle=6.81218
    g1: ArcOfCircle CenterX=-6.9e-15 CenterY=-3.7e-15 CenterZ=0 NormalX=0 NormalY=0 NormalZ=1 AngleXU=0 Radius=12.2 StartAngle=5.94045 EndAngle=6.62592
    g2: ArcOfCircle CenterX=-6.9e-15 CenterY=-3.7e-15 CenterZ=0 NormalX=0 NormalY=0 NormalZ=1 AngleXU=0 Radius=11 StartAngle=2.6126 EndAngle=3.67059
    g3: ArcOfCircle CenterX=-6.9e-15 CenterY=-3.7e-15 CenterZ=0 NormalX=0 NormalY=0 NormalZ=1 AngleXU=0 Radius=12.2 StartAngle=2.79886 EndAngle=3.48433
    g4: Ellipse CenterX=-6.9e-15 CenterY=-3.7e-15 CenterZ=0 NormalX=0 NormalY=0 NormalZ=1 MajorRadius=13.5 MinorRadius=7.81051 AngleXU=-3e-16
    g5: LineSegment StartX=13.5 StartY=-7.4e-15 StartZ=0 EndX=-13.5 EndY=0 EndZ=0
    g6: LineSegment StartX=-4.8e-15 StartY=7.81051 StartZ=0 EndX=-9.1e-15 EndY=-7.81051 EndZ=0
    g7: GeomPoint X=11.0112 Y=-6.8e-15 Z=0
    g8: GeomPoint X=-11.0112 Y=-7e-16 Z=0
    g9: LineSegment StartX=-11.4904 StartY=4.1 StartZ=0 EndX=-9.49645 EndY=5.55135 EndZ=0
    g10: LineSegment StartX=-11.4904 StartY=-4.1 StartZ=0 EndX=-9.49645 EndY=-5.55135 EndZ=0
    g11: LineSegment StartX=9.49645 StartY=-5.55135 StartZ=0 EndX=11.4904 EndY=-4.1 EndZ=0
    g12: LineSegment StartX=11.4904 StartY=4.1 StartZ=0 EndX=9.49645 EndY=5.55135 EndZ=0
  constraints (29):
    c: Coincident(g0,g-4)
    c: PointOnObject(g0,g-4)
    c: Coincident(g1,g0)
    c: PointOnObject(g1,g-3)
    c: Coincident(g2,g0)
    c: PointOnObject(g2,g-4)
    c: Coincident(g3,g0)
    c: PointOnObject(g3,g-3)
    c: InternalAlignment(g5-g8 -> g4) x4
    c: Coincident(g4,g0)
    c: PointOnObject(g3,g4)
    c: PointOnObject(g2,g4)
    c: PointOnObject(g3,g4)
    c: PointOnObject(g2,g4)
    c: PointOnObject(g0,g4)
    c: PointOnObject(g1,g4)
    c: PointOnObject(g1,g4)
    c: PointOnObject(g0,g4)
    c: PointOnObject(g5,g-1)
    c: DistanceX(g5,g5) = 27
    c: DistanceY(g3,g3) = 8.2
    c: Coincident(g9,g3)
    c: Coincident(g9,g2)
    c: Coincident(g10,g3)
    c: Coincident(g10,g2)
    c: Coincident(g11,g0)
    c: Coincident(g11,g1)
    c: Coincident(g12,g1)
    c: Coincident(g12,g0)
FEATURE [PartDesign::Pocket] Pocket043
  BaseFeature = -> Chamfer003
  Length = 5
  Length2 = 100
  Placement = pos=(0,0,0) rot=(0.57735,0.57735,0.57735;2.0944rad)
  Profile = -> Sketch104
  Type = 0
FEATURE [PartDesign::Body] Body101  label="Metal case003"
  Group = -> [Sketch095,Pad021,Sketch096,Pocket035,Sketch097,Pocket036,Sketch098,Pocket037,Mirrored003,Sketch099,Pocket038,Sketch100,Pocket039,Sketch101,Pocket040,Sketch102,Pocket041,Sketch103,Pocket042,Chamfer003,Sketch104,Pocket043]
  Origin = -> Origin118
  Tip = -> Pocket043
FEATURE [App::DocumentObjectGroup] Group027  label="Case003"
  Group = -> [Body101]
FEATURE [App::Part] Part017  label="KP08-004"
  Group = -> [Group021,Body082,Body081,Body086,Body083,Body087,Body085,Body084,Group022,Body089,Body088,Group023,Body094,Body093,Body096,Body092,Body095,Body091,Body090,Group024,Body100,Body099,Group025,Body097,Body098,Group026,Body080,Group027,Body101]
  Origin = -> Origin119
  Placement = pos=(332,246,105) rot=(0,0,1;3.14159rad)
FEATURE [Sketcher::SketchObject] Sketch105
  FullyConstrained = true
  MapMode = 5
  Placement = pos=(0,0,0) rot=(-0.57735,0.57735,0.57735;4.18879rad)
  Support = -> [YZ_Plane124]
  sketch-geometry (1):
    g0: Circle CenterX=0 CenterY=-7.5 CenterZ=0 NormalX=0 NormalY=0 NormalZ=1 AngleXU=0 Radius=0.25
  constraints (3):
    c: PointOnObject(g0,g-2)
    c: DistanceY(g0) = -7.5
    c: Diameter(g0) = 0.5
FEATURE [Sketcher::SketchObject] Sketch106
  FullyConstrained = true
  MapMode = 5
  Support = -> [XY_Plane117]
  sketch-geometry (2):
    g0: LineSegment StartX=0 StartY=5.5 StartZ=0 EndX=6e-16 EndY=9.5 EndZ=0
    g1: ArcOfCircle CenterX=0 CenterY=7.5 CenterZ=0 NormalX=0 NormalY=0 NormalZ=1 AngleXU=0 Radius=2 StartAngle=4.71239 EndAngle=7.85398
  constraints (7):
    c: PointOnObject(g0,g-2)
    c: PointOnObject(g0,g-2)
    c: PointOnObject(g1,g0)
    c: Coincident(g1,g0)
    c: Coincident(g1,g0)
    c: Radius(g1) = 2
    c: DistanceY(g1) = 7.5
FEATURE [PartDesign::Revolution] Revolution032
  Angle = 360
  Axis = (0,1,0)
  Base = (0,0,0)
  Profile = -> Sketch106
  ReferenceAxis = -> Sketch106 [V_Axis]
  Reversed = true
FEATURE [PartDesign::Body] Body103  label="Ball 029"
  Group = -> [Sketch106,Revolution032]
  Origin = -> Origin121
  Tip = -> Revolution032
FEATURE [PartDesign::FeatureBase] Clone056
  BaseFeature = -> Body103
FEATURE [PartDesign::Body] Body104  label="Ball 030"
  BaseFeature = -> Body103
  Group = -> [Clone056]
  Origin = -> Origin122
  Placement = pos=(0,0,0) rot=(-1,0,0;0.897598rad)
  Tip = -> Clone056
FEATURE [PartDesign::FeatureBase] Clone057
  BaseFeature = -> Body103
FEATURE [PartDesign::Body] Body105  label="Ball 031"
  BaseFeature = -> Body103
  Group = -> [Clone057]
  Origin = -> Origin123
  Placement = pos=(0,0,0) rot=(-1,0,0;1.7952rad)
  Tip = -> Clone057
FEATURE [PartDesign::FeatureBase] Clone058
  BaseFeature = -> Body103
FEATURE [PartDesign::Body] Body106  label="Ball 032"
  BaseFeature = -> Body103
  Group = -> [Clone058]
  Origin = -> Origin124
  Placement = pos=(0,0,0) rot=(1,0,0;3.59039rad)
  Tip = -> Clone058
FEATURE [PartDesign::FeatureBase] Clone059
  BaseFeature = -> Body103
FEATURE [PartDesign::Body] Body107  label="Ball 033"
  BaseFeature = -> Body103
  Group = -> [Clone059]
  Origin = -> Origin125
  Placement = pos=(0,0,0) rot=(1,0,0;2.69279rad)
  Tip = -> Clone059
FEATURE [PartDesign::FeatureBase] Clone060
  BaseFeature = -> Body103
FEATURE [PartDesign::Body] Body108  label="Ball 034"
  BaseFeature = -> Body103
  Group = -> [Clone060]
  Origin = -> Origin126
  Placement = pos=(0,0,0) rot=(1,0,0;1.7952rad)
  Tip = -> Clone060
FEATURE [PartDesign::FeatureBase] Clone061
  BaseFeature = -> Body103
FEATURE [PartDesign::Body] Body109  label="Ball 035"
  BaseFeature = -> Body103
  Group = -> [Clone061]
  Origin = -> Origin127
  Placement = pos=(0,0,0) rot=(1,0,0;0.897598rad)
  Tip = -> Clone061
FEATURE [App::DocumentObjectGroup] Group028  label="Balls004"
  Group = -> [Body103,Body104,Body105,Body106,Body107,Body108,Body109]
FEATURE [Sketcher::SketchObject] Sketch107
  FullyConstrained = true
  MapMode = 5
  Support = -> [XY_Plane126]
  sketch-geometry (7):
    g0: LineSegment StartX=-5 StartY=7.5 StartZ=0 EndX=5 EndY=7.5 EndZ=0
    g1: LineSegment StartX=-0.210977 StartY=7.5 StartZ=0 EndX=0.210977 EndY=7.5 EndZ=0
    g2: ArcOfCircle CenterX=0.25 CenterY=7.5 CenterZ=0 NormalX=0 NormalY=0 NormalZ=1 AngleXU=0 Radius=0.460977 StartAngle=2.43297 EndAngle=3.14159
    g3: ArcOfCircle CenterX=-0.25 CenterY=7.5 CenterZ=0 NormalX=0 NormalY=0 NormalZ=1 AngleXU=0 Radius=0.460977 StartAngle=9.792e-13 EndAngle=0.708626
    g4: LineSegment StartX=-0.1 StartY=7.8 StartZ=0 EndX=-0.1 EndY=7.75 EndZ=0
    g5: LineSegment StartX=-0.1 StartY=7.75 StartZ=0 EndX=0.1 EndY=7.75 EndZ=0
    g6: LineSegment StartX=0.1 StartY=7.75 StartZ=0 EndX=0.1 EndY=7.8 EndZ=0
  constraints (22):
    c: DistanceY(g-1,g0) = 7.5
    c: Symmetric(g0,g0,g-2)
    c: DistanceX(g0,g0) = 10
    c: PointOnObject(g1,g0)
    c: PointOnObject(g1,g0)
    c: Coincident(g3,g1)
    c: Coincident(g2,g1)
    c: Coincident(g2,g4)
    c: Coincident(g4,g5)
    c: Horizontal(g5)
    c: Coincident(g5,g6)
    c: Coincident(g6,g3)
    c: Vertical(g6)
    c: Equal(g3,g2)
    c: Vertical(g4)
    c: Symmetric(g2,g3,g-2)
    c: DistanceX(g5,g5) = 0.2
    c: Distance(g5,g1) = 0.25
    c: DistanceX(g3,g-1) = 0.25
    c: PointOnObject(g3,g1)
    c: PointOnObject(g2,g1)
    c: Distance(g3,g1) = 0.3
FEATURE [PartDesign::Revolution] Revolution033
  Angle = 360
  Axis = (10,0,0)
  Base = (-5,7.5,0)
  Profile = -> Sketch107
  ReferenceAxis = -> Sketch107 [Axis]
FEATURE [PartDesign::Body] Body112  label="Rivet 029"
  Group = -> [Sketch107,Revolution033]
  Origin = -> Origin130
  Placement = pos=(0,0,0) rot=(1,0,0;0.448799rad)
  Tip = -> Revolution033
FEATURE [PartDesign::FeatureBase] Clone063
  BaseFeature = -> Body112
  Placement = pos=(0,0,0) rot=(1,0,0;0.448799rad)
FEATURE [PartDesign::Body] Body113  label="Rivet 030"
  BaseFeature = -> Body112
  Group = -> [Clone063]
  Origin = -> Origin131
  Placement = pos=(0,0,0) rot=(1,0,0;0.897598rad)
  Tip = -> Clone063
FEATURE [PartDesign::FeatureBase] Clone064
  BaseFeature = -> Body112
  Placement = pos=(0,0,0) rot=(1,0,0;0.448799rad)
FEATURE [PartDesign::Body] Body114  label="Rivet 031"
  BaseFeature = -> Body112
  Group = -> [Clone064]
  Origin = -> Origin132
  Placement = pos=(0,0,0) rot=(1,0,0;1.7952rad)
  Tip = -> Clone064
FEATURE [PartDesign::FeatureBase] Clone065
  BaseFeature = -> Body112
  Placement = pos=(0,0,0) rot=(1,0,0;0.448799rad)
FEATURE [PartDesign::Body] Body115  label="Rivet 032"
  BaseFeature = -> Body112
  Group = -> [Clone065]
  Origin = -> Origin133
  Placement = pos=(0,0,0) rot=(1,0,0;2.69279rad)
  Tip = -> Clone065
FEATURE [PartDesign::FeatureBase] Clone066
  BaseFeature = -> Body112
  Placement = pos=(0,0,0) rot=(1,0,0;0.448799rad)
FEATURE [PartDesign::Body] Body116  label="Rivet 033"
  BaseFeature = -> Body112
  Group = -> [Clone066]
  Origin = -> Origin134
  Placement = pos=(0,0,0) rot=(1,0,0;3.59039rad)
  Tip = -> Clone066
FEATURE [PartDesign::FeatureBase] Clone067
  BaseFeature = -> Body112
  Placement = pos=(0,0,0) rot=(1,0,0;0.448799rad)
FEATURE [PartDesign::Body] Body117  label="Rivet 034"
  BaseFeature = -> Body112
  Group = -> [Clone067]
  Origin = -> Origin135
  Placement = pos=(0,0,0) rot=(-1,0,0;1.7952rad)
  Tip = -> Clone067
FEATURE [PartDesign::FeatureBase] Clone068
  BaseFeature = -> Body112
  Placement = pos=(0,0,0) rot=(1,0,0;0.448799rad)
FEATURE [PartDesign::Body] Body118  label="Rivet 035"
  BaseFeature = -> Body112
  Group = -> [Clone068]
  Origin = -> Origin136
  Placement = pos=(0,0,0) rot=(-1,0,0;0.897598rad)
  Tip = -> Clone068
FEATURE [App::DocumentObjectGroup] Group030  label="Rivets004"
  Group = -> [Body112,Body113,Body114,Body115,Body116,Body117,Body118]
FEATURE [Sketcher::SketchObject] Sketch108
  FullyConstrained = true
  MapMode = 5
  Placement = pos=(0,0,0) rot=(1,0,0;1.5708rad)
  Support = -> [XZ_Plane124]
  sketch-geometry (4):
    g0: LineSegment StartX=0 StartY=8.5 StartZ=0 EndX=0.1 EndY=8.5 EndZ=0
    g1: LineSegment StartX=0.1 StartY=8.5 StartZ=0 EndX=0.1 EndY=6.5 EndZ=0
    g2: LineSegment StartX=0.1 StartY=6.5 StartZ=0 EndX=0 EndY=6.5 EndZ=0
    g3: LineSegment StartX=0 StartY=6.5 StartZ=0 EndX=0 EndY=8.5 EndZ=0
  constraints (12):
    c: Coincident(g0,g1)
    c: Coincident(g1,g2)
    c: Coincident(g2,g3)
    c: Coincident(g3,g0)
    c: Horizontal(g0)
    c: Horizontal(g2)
    c: Vertical(g1)
    c: Vertical(g3)
    c: PointOnObject(g0,g-2)
    c: DistanceX(g0,g0) = 0.1
    c: DistanceY(g0) = 8.5
    c: DistanceY(g1) = 6.5
FEATURE [PartDesign::Revolution] Revolution034
  Angle = 360
  Axis = (1,0,0)
  Base = (0,0,0)
  Placement = pos=(0,0,0) rot=(1,0,0;1.5708rad)
  Profile = -> Sketch108
  ReferenceAxis = -> Sketch108 [H_Axis]
FEATURE [Sketcher::SketchObject] Sketch109
  FullyConstrained = true
  MapMode = 5
  Placement = pos=(0,0,0) rot=(0.57735,0.57735,0.57735;2.0944rad)
  Support = -> [YZ_Plane124]
  sketch-geometry (5):
    g0: ArcOfCircle CenterX=0 CenterY=7.5 CenterZ=0 NormalX=0 NormalY=0 NormalZ=1 AngleXU=0 Radius=2.11 StartAngle=5.66076 EndAngle=6.65667
    g1: LineSegment StartX=5e-16 StartY=8.5 StartZ=0 EndX=0 EndY=6.26986 EndZ=0
    g2: ArcOfCircle CenterX=0 CenterY=0 CenterZ=0 NormalX=0 NormalY=0 NormalZ=1 AngleXU=0 Radius=6.5 StartAngle=1.3039 EndAngle=1.5708
    g3: LineSegment StartX=1.71431 StartY=6.26986 StartZ=0 EndX=0 EndY=6.26986 EndZ=0
    g4: ArcOfCircle CenterX=0 CenterY=0 CenterZ=0 NormalX=0 NormalY=0 NormalZ=1 AngleXU=0 Radius=8.5 StartAngle=1.33757 EndAngle=1.5708
  constraints (16):
    c: PointOnObject(g0,g-2)
    c: DistanceY(g0) = 7.5
    c: Radius(g0) = 2.11
    c: PointOnObject(g2,g1)
    c: DistanceY(g2) = 6.5
    c: Coincident(g2,g-1)
    c: Coincident(g3,g2)
    c: Horizontal(g3)
    c: Coincident(g0,g2)
    c: Coincident(g1,g3)
    c: PointOnObject(g1,g-2)
    c: PointOnObject(g1,g-2)
    c: Coincident(g4,g-1)
    c: Coincident(g4,g1)
    c: DistanceY(g1) = 8.5
    c: Coincident(g0,g4)
FEATURE [PartDesign::Revolution] Revolution035
  Angle = 180
  Axis = (-2e-16,3e-16,1)
  Base = (0,0,0)
  BaseFeature = -> Revolution034
  Placement = pos=(0,0,0) rot=(1,0,0;1.5708rad)
  Profile = -> Sketch109
  ReferenceAxis = -> Sketch109 [V_Axis]
  Reversed = true
FEATURE [PartDesign::PolarPattern] PolarPattern016
  Angle = 360
  Axis = -> Sketch109 [N_Axis]
  BaseFeature = -> Revolution035
  Occurrences = 3
  Originals = -> [Revolution035]
  Placement = pos=(0,0,0) rot=(1,0,0;1.5708rad)
  Refine = true
FEATURE [Sketcher::SketchObject] Sketch110
  FullyConstrained = true
  MapMode = 5
  Placement = pos=(0,0,0) rot=(0.57735,0.57735,0.57735;2.0944rad)
  Support = -> [YZ_Plane124]
  sketch-geometry (4):
    g0: ArcOfCircle CenterX=0 CenterY=7.5 CenterZ=0 NormalX=0 NormalY=0 NormalZ=1 AngleXU=0 Radius=2.01 StartAngle=5.57985 EndAngle=6.86228
    g1: LineSegment StartX=0 StartY=6.2 StartZ=0 EndX=1.533 EndY=6.2 EndZ=0
    g2: LineSegment StartX=0 StartY=8.6 StartZ=0 EndX=0 EndY=6.2 EndZ=0
    g3: LineSegment StartX=0 StartY=8.6 StartZ=0 EndX=1.68229 EndY=8.6 EndZ=0
  constraints (13):
    c: PointOnObject(g0,g-2)
    c: DistanceY(g0) = 7.5
    c: Radius(g0) = 2.01
    c: PointOnObject(g1,g-2)
    c: Horizontal(g1)
    c: Coincident(g0,g1)
    c: DistanceY(g1) = 6.2
    c: DistanceY(g2) = 8.6
    c: Coincident(g2,g1)
    c: PointOnObject(g2,g-2)
    c: Coincident(g3,g2)
    c: Horizontal(g3)
    c: Coincident(g0,g3)
FEATURE [PartDesign::Groove] Groove004
  Angle = 360
  Axis = (-2e-16,3e-16,1)
  Base = (0,0,0)
  BaseFeature = -> PolarPattern016
  Placement = pos=(0,0,0) rot=(1,0,0;1.5708rad)
  Profile = -> Sketch110
  ReferenceAxis = -> Sketch110 [V_Axis]
FEATURE [PartDesign::PolarPattern] PolarPattern017
  Angle = 360
  Axis = -> Sketch110 [N_Axis]
  BaseFeature = -> Groove004
  Occurrences = 3
  Originals = -> [Groove004]
  Placement = pos=(0,0,0) rot=(1,0,0;1.5708rad)
FEATURE [PartDesign::Pocket] Pocket044
  BaseFeature = -> PolarPattern017
  Length = 5
  Length2 = 100
  Placement = pos=(0,0,0) rot=(1,0,0;1.5708rad)
  Profile = -> Sketch105
  Type = 1
FEATURE [PartDesign::PolarPattern] PolarPattern018
  Angle = 360
  Axis = -> Sketch105 [N_Axis]
  BaseFeature = -> Pocket044
  Occurrences = 3
  Originals = -> [Pocket044]
  Placement = pos=(0,0,0) rot=(1,0,0;1.5708rad)
FEATURE [PartDesign::Body] Body110  label="Cage 009"
  Group = -> [Sketch108,Revolution034,Sketch109,Revolution035,PolarPattern016,Sketch110,Groove004,PolarPattern017,Sketch105,Pocket044,PolarPattern018]
  Origin = -> Origin128
  Placement = pos=(0,0,0) rot=(-1,0,0;1.5708rad)
  Tip = -> PolarPattern018
FEATURE [PartDesign::FeatureBase] Clone062
  BaseFeature = -> Body110
  Placement = pos=(0,0,0) rot=(-1,0,0;1.5708rad)
FEATURE [PartDesign::Body] Body111  label="Cage 010"
  BaseFeature = -> Body110
  Group = -> [Clone062]
  Origin = -> Origin129
  Placement = pos=(0,0,0) rot=(0,1,0;3.14159rad)
  Tip = -> Clone062
FEATURE [App::DocumentObjectGroup] Group029  label="Cages004"
  Group = -> [Body110,Body111]
FEATURE [Sketcher::SketchObject] Sketch111
  FullyConstrained = true
  MapMode = 5
  Support = -> [XY_Plane133]
  sketch-geometry (14):
    g0: ArcOfCircle CenterX=-1e-16 CenterY=7.5 CenterZ=0 NormalX=0 NormalY=0 NormalZ=1 AngleXU=0 Radius=2 StartAngle=0.848062 EndAngle=2.29353
    g1: LineSegment StartX=-3.5 StartY=11 StartZ=0 EndX=3.5 EndY=11 EndZ=0
    g2: LineSegment StartX=3.5 StartY=11 StartZ=0 EndX=3.5 EndY=9.2 EndZ=0
    g3: LineSegment StartX=2.9 StartY=9 StartZ=0 EndX=1.32288 EndY=9 EndZ=0
    g4: LineSegment StartX=-3.5 StartY=9.2 StartZ=0 EndX=-3.5 EndY=11 EndZ=0
    g5: LineSegment StartX=-1.32288 StartY=9 StartZ=0 EndX=-2.9 EndY=9 EndZ=0
    g6: LineSegment StartX=2.9 StartY=9 StartZ=0 EndX=2.9 EndY=9.5 EndZ=0
    g7: LineSegment StartX=2.9 StartY=9.5 StartZ=0 EndX=3.2 EndY=9.5 EndZ=0
    g8: LineSegment StartX=3.2 StartY=9.5 StartZ=0 EndX=3.2 EndY=9.2 EndZ=0
    g9: LineSegment StartX=3.2 StartY=9.2 StartZ=0 EndX=3.5 EndY=9.2 EndZ=0
    g10: LineSegment StartX=-3.5 StartY=9.2 StartZ=0 EndX=-3.2 EndY=9.2 EndZ=0
    g11: LineSegment StartX=-3.2 StartY=9.2 StartZ=0 EndX=-3.2 EndY=9.5 EndZ=0
    g12: LineSegment StartX=-3.2 StartY=9.5 StartZ=0 EndX=-2.9 EndY=9.5 EndZ=0
    g13: LineSegment StartX=-2.9 StartY=9.5 StartZ=0 EndX=-2.9 EndY=9 EndZ=0
  constraints (41):
    c: Coincident(g1,g2)
    c: Coincident(g4,g1)
    c: Horizontal(g3)
    c: Vertical(g2)
    c: Vertical(g4)
    c: Coincident(g0,g5)
    c: Coincident(g0,g3)
    c: DistanceY(g-1,g0) = 7.5
    c: Radius(g0) = 2
    c: Symmetric(g1,g1,g-2)
    c: Symmetric(g0,g0,g-2)
    c: DistanceY(g1) = 11
    c: DistanceX(g1,g1) = 7
    c: Vertical(g6)
    c: Coincident(g6,g7)
    c: Horizontal(g7)
    c: Coincident(g7,g8)
    c: Vertical(g8)
    c: Coincident(g8,g9)
    c: Coincident(g3,g6)
    c: Coincident(g2,g9)
    c: Horizontal(g10)
    c: Coincident(g10,g11)
    c: Coincident(g11,g12)
    c: Horizontal(g12)
    c: Coincident(g12,g13)
    c: Vertical(g13)
    c: Vertical(g11)
    c: Coincident(g4,g10)
    c: Coincident(g5,g13)
    c: DistanceY(g13,g13) = 0.5
    c: DistanceX(g12,g12) = 0.3
    c: DistanceY(g5,g10) = 0.2
    c: Symmetric(g5,g3,g-2)
    c: DistanceY(g3) = 9
    c: DistanceY(g6) = 9.5
    c: Equal(g7,g12)
    c: Equal(g13,g6)
    c: Horizontal(g9)
    c: Horizontal(g8,g10)
    c: Equal(g12,g10)
FEATURE [PartDesign::Revolution] Revolution036
  Angle = 360
  Axis = (1,0,0)
  Base = (0,0,0)
  Profile = -> Sketch111
  ReferenceAxis = -> X_Axis133
FEATURE [PartDesign::Fillet] Fillet167
  Base = -> Revolution036 [Edge14,Edge15]
  BaseFeature = -> Revolution036
  Radius = 0.3
  SupportTransform = false
FEATURE [PartDesign::Body] Body119  label="Outer Ring005"
  Group = -> [Sketch111,Revolution036,Fillet167]
  Origin = -> Origin137
  Tip = -> Fillet167
FEATURE [Sketcher::SketchObject] Sketch112
  FullyConstrained = true
  MapMode = 5
  Support = -> [XY_Plane134]
  sketch-geometry (14):
    g0: LineSegment StartX=-2.9 StartY=6 StartZ=0 EndX=-1.32288 EndY=6 EndZ=0
    g1: LineSegment StartX=-3.5 StartY=4 StartZ=0 EndX=-3.5 EndY=5.7 EndZ=0
    g2: ArcOfCircle CenterX=1e-16 CenterY=7.5 CenterZ=0 NormalX=0 NormalY=0 NormalZ=1 AngleXU=0 Radius=2 StartAngle=3.98965 EndAngle=5.43512
    g3: LineSegment StartX=1.32288 StartY=6 StartZ=0 EndX=2.9 EndY=6 EndZ=0
    g4: LineSegment StartX=-3.5 StartY=5.7 StartZ=0 EndX=-3.2 EndY=5.7 EndZ=0
    g5: LineSegment StartX=-3.2 StartY=5.7 StartZ=0 EndX=-3.2 EndY=5.5 EndZ=0
    g6: LineSegment StartX=-3.2 StartY=5.5 StartZ=0 EndX=-2.9 EndY=5.5 EndZ=0
    g7: LineSegment StartX=-2.9 StartY=5.5 StartZ=0 EndX=-2.9 EndY=6 EndZ=0
    g8: LineSegment StartX=8.5 StartY=5.7 StartZ=0 EndX=3.2 EndY=5.7 EndZ=0
    g9: LineSegment StartX=3.2 StartY=5.7 StartZ=0 EndX=3.2 EndY=5.5 EndZ=0
    g10: LineSegment StartX=3.2 StartY=5.5 StartZ=0 EndX=2.9 EndY=5.5 EndZ=0
    g11: LineSegment StartX=2.9 StartY=5.5 StartZ=0 EndX=2.9 EndY=6 EndZ=0
    g12: LineSegment StartX=8.5 StartY=4 StartZ=0 EndX=8.5 EndY=5.7 EndZ=0
    g13: LineSegment StartX=-3.5 StartY=4 StartZ=0 EndX=8.5 EndY=4 EndZ=0
  constraints (43):
    c: Horizontal(g0)
    c: Vertical(g1)
    c: DistanceY(g1) = 4
    c: Coincident(g2,g0)
    c: Coincident(g2,g3)
    c: Horizontal(g3)
    c: Radius(g2) = 2
    c: DistanceY(g2) = 7.5
    c: Symmetric(g0,g2,g-2)
    c: Horizontal(g4)
    c: Coincident(g4,g5)
    c: Vertical(g5)
    c: Coincident(g5,g6)
    c: Horizontal(g6)
    c: Coincident(g6,g7)
    c: Vertical(g7)
    c: Horizontal(g8)
    c: Coincident(g8,g9)
    c: Vertical(g9)
    c: Coincident(g9,g10)
    c: Horizontal(g10)
    c: Coincident(g10,g11)
    c: Vertical(g11)
    c: Coincident(g3,g11)
    c: Coincident(g0,g7)
    c: Coincident(g1,g4)
    c: DistanceY(g3) = 6
    c: DistanceY(g6,g0) = 0.5
    c: DistanceX(g4,g4) = 0.3
    c: DistanceX(g6,g6) = 0.3
    c: DistanceY(g5,g4) = 0.2
    c: Vertical(g12)
    c: Equal(g11,g7)
    c: Equal(g5,g9)
    c: DistanceY(g1,g0) = 2
    c: Coincident(g13,g1)
    c: Coincident(g13,g12)
    c: Horizontal(g13)
    c: DistanceX(g13,g13) = 12
    c: DistanceX(g1,g2) = 3.5
    c: Coincident(g8,g12)
    c: DistanceX(g8,g8) = 5.3
    c: Equal(g6,g10)
FEATURE [PartDesign::Revolution] Revolution037
  Angle = 360
  Axis = (1,0,0)
  Base = (0,0,0)
  Profile = -> Sketch112
  ReferenceAxis = -> X_Axis134
FEATURE [PartDesign::Fillet] Fillet168
  Base = -> Revolution037 [Edge13,Edge11]
  BaseFeature = -> Revolution037
  Radius = 0.2
  SupportTransform = false
FEATURE [PartDesign::Body] Body120  label="Inner Ring005"
  Group = -> [Sketch112,Revolution037,Fillet168]
  Origin = -> Origin138
  Tip = -> Fillet168
FEATURE [App::DocumentObjectGroup] Group032  label="Rings004"
  Group = -> [Body119,Body120]
FEATURE [Sketcher::SketchObject] Sketch113
  FullyConstrained = true
  MapMode = 5
  Placement = pos=(0,0,0) rot=(1,0,0;1.5708rad)
  Support = -> [XZ_Plane135]
  sketch-geometry (12):
    g0: LineSegment StartX=2.9 StartY=9.5 StartZ=0 EndX=2.9 EndY=8.5 EndZ=0
    g1: LineSegment StartX=2.9 StartY=8.5 StartZ=0 EndX=3.2 EndY=8.5 EndZ=0
    g2: LineSegment StartX=3.2 StartY=8.5 StartZ=0 EndX=3.2 EndY=6.5 EndZ=0
    g3: LineSegment StartX=3.2 StartY=6.5 StartZ=0 EndX=2.9 EndY=6.5 EndZ=0
    g4: LineSegment StartX=2.9 StartY=6.5 StartZ=0 EndX=2.9 EndY=5.5 EndZ=0
    g5: LineSegment StartX=2.9 StartY=5.5 StartZ=0 EndX=3.2 EndY=5.5 EndZ=0
    g6: LineSegment StartX=3.2 StartY=5.5 StartZ=0 EndX=3.2 EndY=6 EndZ=0
    g7: LineSegment StartX=3.2 StartY=6 StartZ=0 EndX=3.5 EndY=6 EndZ=0
    g8: LineSegment StartX=3.5 StartY=6 StartZ=0 EndX=3.5 EndY=9 EndZ=0
    g9: LineSegment StartX=3.5 StartY=9 StartZ=0 EndX=3.2 EndY=9 EndZ=0
    g10: LineSegment StartX=3.2 StartY=9 StartZ=0 EndX=3.2 EndY=9.5 EndZ=0
    g11: LineSegment StartX=3.2 StartY=9.5 StartZ=0 EndX=2.9 EndY=9.5 EndZ=0
  constraints (36):
    c: Vertical(g0)
    c: Coincident(g0,g1)
    c: Horizontal(g1)
    c: Coincident(g1,g2)
    c: Vertical(g2)
    c: Coincident(g2,g3)
    c: Horizontal(g3)
    c: Coincident(g3,g4)
    c: Vertical(g4)
    c: Coincident(g4,g5)
    c: Horizontal(g5)
    c: Coincident(g5,g6)
    c: Vertical(g6)
    c: Coincident(g6,g7)
    c: Horizontal(g7)
    c: Coincident(g7,g8)
    c: Vertical(g8)
    c: Coincident(g8,g9)
    c: Horizontal(g9)
    c: Coincident(g9,g10)
    c: Vertical(g10)
    c: Coincident(g10,g11)
    c: Coincident(g11,g0)
    c: Horizontal(g11)
    c: DistanceY(g4) = 5.5
    c: DistanceX(g4) = 2.9
    c: DistanceY(g5,g6) = 0.5
    c: DistanceY(g6,g2) = 0.5
    c: DistanceX(g5,g5) = 0.3
    c: Equal(g5,g7)
    c: Equal(g7,g3)
    c: Equal(g3,g1)
    c: Equal(g1,g9)
    c: Equal(g4,g0)
    c: Equal(g6,g10)
    c: DistanceY(g4,g0) = 4
FEATURE [PartDesign::Revolution] Revolution038
  Angle = 360
  Axis = (1,0,0)
  Base = (0,0,0)
  Placement = pos=(0,0,0) rot=(1,0,0;1.5708rad)
  Profile = -> Sketch113
  ReferenceAxis = -> Sketch113 [H_Axis]
FEATURE [PartDesign::Fillet] Fillet169
  Base = -> Revolution038 [Edge14,Edge12]
  BaseFeature = -> Revolution038
  Placement = pos=(0,0,0) rot=(1,0,0;1.5708rad)
  Radius = 0.2
  SupportTransform = false
FEATURE [PartDesign::Body] Body121  label="Seal 009"
  Group = -> [Sketch113,Revolution038,Fillet169]
  Origin = -> Origin139
  Tip = -> Fillet169
FEATURE [PartDesign::FeatureBase] Clone069
  BaseFeature = -> Body121
FEATURE [PartDesign::Body] Body122  label="Seal 010"
  BaseFeature = -> Body121
  Group = -> [Clone069]
  Origin = -> Origin140
  Placement = pos=(0,0,0) rot=(0,1,0;3.14159rad)
  Tip = -> Clone069
FEATURE [App::DocumentObjectGroup] Group031  label="Seals004"
  Group = -> [Body121,Body122]
FEATURE [Sketcher::SketchObject] Sketch114
  AttachmentOffset = pos=(0,0,4) rot=(0,0,1;0rad)
  FullyConstrained = true
  MapMode = 5
  Placement = pos=(0,0,4) rot=(0,0,1;0rad)
  Support = -> [XY_Plane116]
  sketch-geometry (1):
    g0: Circle CenterX=6 CenterY=0 CenterZ=0 NormalX=0 NormalY=0 NormalZ=1 AngleXU=0 Radius=1.5
  constraints (3):
    c: PointOnObject(g0,g-1)
    c: Diameter(g0) = 3
    c: DistanceX(g0,g-3) = 2.5
FEATURE [PartDesign::Pad] Pad022
  Direction = (0,0,1)
  Length = 3
  Length2 = 100
  Profile = -> Sketch114
  Type = 0
FEATURE [Sketcher::SketchObject] Sketch115
  ExternalGeometry = -> [Pad022]
  FullyConstrained = true
  MapMode = 5
  Placement = pos=(0,0,7) rot=(0,0,1;0rad)
  Support = -> [Pad022]
  sketch-geometry (7):
    g0: LineSegment StartX=6.43301 StartY=-0.75 StartZ=0 EndX=6.86603 EndY=-5.43e-14 EndZ=0
    g1: LineSegment StartX=6.86603 StartY=-5.43e-14 StartZ=0 EndX=6.43301 EndY=0.75 EndZ=0
    g2: LineSegment StartX=6.43301 StartY=0.75 StartZ=0 EndX=5.56699 EndY=0.75 EndZ=0
    g3: LineSegment StartX=5.56699 StartY=0.75 StartZ=0 EndX=5.13397 EndY=1.086e-13 EndZ=0
    g4: LineSegment StartX=5.13397 StartY=1.086e-13 StartZ=0 EndX=5.56699 EndY=-0.75 EndZ=0
    g5: LineSegment StartX=5.56699 StartY=-0.75 StartZ=0 EndX=6.43301 EndY=-0.75 EndZ=0
    g6: Circle CenterX=6 CenterY=0 CenterZ=0 NormalX=0 NormalY=0 NormalZ=1 AngleXU=0 Radius=0.866025
  constraints (16):
    c: Coincident(g0,g1)
    c: Coincident(g1,g2)
    c: Coincident(g2,g3)
    c: Coincident(g3,g4)
    c: Coincident(g4,g5)
    c: Coincident(g5,g0)
    c: Equal(g0, g1-g5) x5
    c: PointOnObject(g0,g6)
    c: PointOnObject(g1,g6)
    c: PointOnObject(g2,g6)
    c: PointOnObject(g3,g6)
    c: PointOnObject(g4,g6)
    c: PointOnObject(g5,g6)
    c: Coincident(g6,g-3)
    c: Horizontal(g5)
    c: DistanceY(g4,g2) = 1.5
FEATURE [PartDesign::Pocket] Pocket045
  BaseFeature = -> Pad022
  Length = 1
  Length2 = 100
  Profile = -> Sketch115
  Type = 0
FEATURE [PartDesign::PolarPattern] PolarPattern019
  Angle = 120
  Axis = -> X_Axis116
  BaseFeature = -> Pocket045
  Occurrences = 3
  Originals = -> [Pad022,Pocket045]
FEATURE [PartDesign::Body] Body102
  Group = -> [Sketch114,Pad022,Sketch115,Pocket045,PolarPattern019]
  Origin = -> Origin120
  Tip = -> PolarPattern019
FEATURE [App::DocumentObjectGroup] Group033  label="Set screws004"
  Group = -> [Body102]
FEATURE [Sketcher::SketchObject] Sketch116
  AttachmentOffset = pos=(0,0,-4.1) rot=(0,0,1;0rad)
  FullyConstrained = true
  MapMode = 5
  Placement = pos=(-4.1,9e-16,-9e-16) rot=(0.57735,0.57735,0.57735;2.0944rad)
  Support = -> [YZ_Plane137]
  sketch-geometry (13):
    g0: ArcOfCircle CenterX=0 CenterY=0 CenterZ=0 NormalX=0 NormalY=0 NormalZ=1 AngleXU=0 Radius=13.5 StartAngle=1.12361 EndAngle=2.01799
    g1: ArcOfCircle CenterX=-18.5 CenterY=0 CenterZ=0 NormalX=0 NormalY=0 NormalZ=1 AngleXU=0 Radius=5.5 StartAngle=2.01799 EndAngle=4.2652
    g2: Circle CenterX=-18.5 CenterY=0 CenterZ=0 NormalX=0 NormalY=0 NormalZ=1 AngleXU=0 Radius=2.75
    g3: ArcOfCircle CenterX=18.5 CenterY=0 CenterZ=0 NormalX=0 NormalY=0 NormalZ=1 AngleXU=0 Radius=5.5 StartAngle=5.15958 EndAngle=7.40679
    g4: Circle CenterX=18.5 CenterY=0 CenterZ=0 NormalX=0 NormalY=0 NormalZ=1 AngleXU=0 Radius=2.75
    g5: Circle CenterX=0 CenterY=0 CenterZ=0 NormalX=0 NormalY=0 NormalZ=1 AngleXU=0 Radius=11
    g6: GeomPoint X=-24 Y=0 Z=0
    g7: GeomPoint X=24 Y=0 Z=0
    g8: LineSegment StartX=-20.8784 StartY=4.95916 StartZ=0 EndX=-5.83784 EndY=12.1725 EndZ=0
    g9: LineSegment StartX=-20.8784 StartY=-4.95916 StartZ=0 EndX=-5.83784 EndY=-12.1725 EndZ=0
    g10: LineSegment StartX=5.83784 StartY=-12.1725 StartZ=0 EndX=20.8784 EndY=-4.95916 EndZ=0
    g11: LineSegment StartX=20.8784 StartY=4.95916 StartZ=0 EndX=5.83784 EndY=12.1725 EndZ=0
    g12: ArcOfCircle CenterX=0 CenterY=0 CenterZ=0 NormalX=0 NormalY=0 NormalZ=1 AngleXU=0 Radius=13.5 StartAngle=4.2652 EndAngle=5.15958
  constraints (27):
    c: Coincident(g0,g-1)
    c: PointOnObject(g1,g-1)
    c: Coincident(g2,g1)
    c: Coincident(g4,g3)
    c: Equal(g2,g4)
    c: Equal(g1,g3)
    c: Coincident(g5,g0)
    c: Diameter(g0) = 27
    c: Diameter(g5) = 22
    c: Diameter(g4) = 5.5
    c: Symmetric(g3,g1,g0)
    c: DistanceX(g1,g3) = 37
    c: PointOnObject(g6,g1)
    c: PointOnObject(g7,g3)
    c: PointOnObject(g7,g-1)
    c: PointOnObject(g6,g-1)
    c: DistanceX(g6,g7) = 48
    c: Tangent(g3,g11) = -1.5708
    c: Tangent(g0,g11) = -1.5708
    c: Tangent(g3,g10) = -1.5708
    c: Tangent(g1,g9) = -1.5708
    c: Equal(g0,g12)
    c: Tangent(g12,g9) = -1.5708
    c: Coincident(g0,g12)
    c: Tangent(g0,g8) = 1.5708
    c: Tangent(g1,g8) = 1.5708
    c: Tangent(g12,g10) = -1.5708
FEATURE [PartDesign::Pad] Pad023
  Direction = (1,-2e-16,3e-16)
  Length = 3.3
  Length2 = 100
  Placement = pos=(0,0,0) rot=(0.57735,0.57735,0.57735;2.0944rad)
  Profile = -> Sketch116
  Type = 0
FEATURE [Sketcher::SketchObject] Sketch117
  ExternalGeometry = -> [Pad023]
  FullyConstrained = true
  MapMode = 5
  Placement = pos=(-4.1,9e-16,-1e-15) rot=(0.57735,0.57735,-0.57735;4.18879rad)
  Support = -> [Pad023]
  sketch-geometry (12):
    g0: ArcOfCircle CenterX=0 CenterY=0 CenterZ=0 NormalX=0 NormalY=0 NormalZ=1 AngleXU=0 Radius=12.3 StartAngle=4.2652 EndAngle=5.15958
    g1: ArcOfCircle CenterX=-18.5 CenterY=-1.04e-14 CenterZ=0 NormalX=0 NormalY=0 NormalZ=1 AngleXU=0 Radius=4.55 StartAngle=4.98418 EndAngle=7.58219
    g2: ArcOfCircle CenterX=18.5 CenterY=1.02e-14 CenterZ=0 NormalX=0 NormalY=0 NormalZ=1 AngleXU=0 Radius=4.55 StartAngle=1.84259 EndAngle=4.44059
    g3: LineSegment StartX=-17.3605 StartY=5.31545 StartZ=0 EndX=-5.31892 EndY=11.0905 EndZ=0
    g4: LineSegment StartX=-17.3605 StartY=-5.31545 StartZ=0 EndX=-5.31892 EndY=-11.0905 EndZ=0
    g5: LineSegment StartX=5.31892 StartY=-11.0905 StartZ=0 EndX=17.3605 EndY=-5.31545 EndZ=0
    g6: LineSegment StartX=17.3605 StartY=5.31545 StartZ=0 EndX=5.31892 EndY=11.0905 EndZ=0
    g7: ArcOfCircle CenterX=0 CenterY=0 CenterZ=0 NormalX=0 NormalY=0 NormalZ=1 AngleXU=0 Radius=12.3 StartAngle=1.12361 EndAngle=2.01799
    g8: ArcOfCircle CenterX=-17.1443 CenterY=4.86462 CenterZ=0 NormalX=0 NormalY=0 NormalZ=1 AngleXU=0 Radius=0.5 StartAngle=2.01799 EndAngle=4.44059
    g9: ArcOfCircle CenterX=-17.1443 CenterY=-4.86462 CenterZ=0 NormalX=0 NormalY=0 NormalZ=1 AngleXU=0 Radius=0.5 StartAngle=1.84259 EndAngle=4.2652
    g10: ArcOfCircle CenterX=17.1443 CenterY=-4.86462 CenterZ=0 NormalX=0 NormalY=0 NormalZ=1 AngleXU=0 Radius=0.5 StartAngle=5.15958 EndAngle=7.58219
    g11: ArcOfCircle CenterX=17.1443 CenterY=4.86462 CenterZ=0 NormalX=0 NormalY=0 NormalZ=1 AngleXU=0 Radius=0.5 StartAngle=4.98418 EndAngle=7.40679
  constraints (30):
    c: Coincident(g0,g-1)
    c: Coincident(g1,g-3)
    c: Coincident(g2,g-4)
    c: Equal(g2,g1)
    c: Parallel(g3,g-5)
    c: Distance(g3,g-5) = 1.2
    c: Coincident(g7,g3) = 1.5708
    c: Tangent(g0,g4) = -1.5708
    c: Equal(g0,g7)
    c: Tangent(g0,g5) = -1.5708
    c: Tangent(g7,g6) = -1.5708
    c: Coincident(g0,g7)
    c: Vertical(g0,g3)
    c: Tangent(g1,g8) = 1.5708
    c: Tangent(g3,g8) = 1.5708
    c: Tangent(g4,g9) = -1.5708
    c: Tangent(g1,g9) = 1.5708
    c: Tangent(g2,g10) = 1.5708
    c: Tangent(g5,g10) = -1.5708
    c: Tangent(g6,g11) = -1.5708
    c: Tangent(g2,g11) = 1.5708
    c: Equal(g8,g9)
    c: Equal(g9,g10)
    c: Equal(g10,g11)
    c: Parallel(g-6,g6)
    c: Parallel(g5,g3)
    c: Parallel(g4,g6)
    c: Radius(g-4) = 2.75
    c: Radius(g2) = 4.55
    c: Radius(g11) = 0.5
FEATURE [PartDesign::Pocket] Pocket046
  BaseFeature = -> Pad023
  Length = 0.6
  Length2 = 100
  Placement = pos=(0,0,0) rot=(0.57735,0.57735,0.57735;2.0944rad)
  Profile = -> Sketch117
  Type = 0
FEATURE [Sketcher::SketchObject] Sketch118
  ExternalGeometry = -> [Pocket046]
  FullyConstrained = true
  MapMode = 5
  Placement = pos=(-0.8,2e-16,-2e-16) rot=(0.57735,0.57735,0.57735;2.0944rad)
  Support = -> [Pocket046]
  sketch-geometry (7):
    g0: Circle CenterX=-18.5 CenterY=1.66e-14 CenterZ=0 NormalX=0 NormalY=0 NormalZ=1 AngleXU=0 Radius=2.75
    g1: LineSegment StartX=-20.8784 StartY=4.95916 StartZ=0 EndX=-14.8432 EndY=7.85358 EndZ=0
    g2: LineSegment StartX=-20.8784 StartY=-4.95916 StartZ=0 EndX=-14.8432 EndY=-7.85358 EndZ=0
    g3: ArcOfCircle CenterX=-18.5 CenterY=1.66e-14 CenterZ=0 NormalX=0 NormalY=0 NormalZ=1 AngleXU=0 Radius=5.5 StartAngle=2.01799 EndAngle=4.2652
    g4: ArcOfCircle CenterX=0 CenterY=0 CenterZ=0 NormalX=0 NormalY=0 NormalZ=1 AngleXU=0 Radius=15 StartAngle=2.69212 EndAngle=3.59107
    g5: ArcOfCircle CenterX=-14.4108 CenterY=6.95191 CenterZ=0 NormalX=0 NormalY=0 NormalZ=1 AngleXU=0 Radius=1 StartAngle=5.83371 EndAngle=8.30117
    g6: ArcOfCircle CenterX=-14.4108 CenterY=-6.95191 CenterZ=0 NormalX=0 NormalY=0 NormalZ=1 AngleXU=0 Radius=1 StartAngle=4.2652 EndAngle=6.73266
  constraints (17):
    c: Coincident(g0,g-6)
    c: Equal(g-5,g0)
    c: Coincident(g1,g-6)
    c: Coincident(g2,g-6)
    c: Coincident(g3,g0)
    c: Coincident(g3,g1)
    c: Coincident(g3,g2)
    c: Coincident(g4,g-1)
    c: Radius(g4) = 15
    c: Tangent(g1,g5) = 1.5708
    c: Tangent(g4,g5) = 1.5708
    c: Tangent(g2,g6) = -1.5708
    c: Tangent(g4,g6) = 1.5708
    c: Radius(g6) = 1
    c: PointOnObject(g2,g-4)
    c: Equal(g5,g6)
    c: PointOnObject(g1,g-3)
FEATURE [PartDesign::Pad] Pad024
  BaseFeature = -> Pocket046
  Direction = (1,-9e-16,6e-16)
  Length = 0.7
  Length2 = 100
  Placement = pos=(0,0,0) rot=(0.57735,0.57735,0.57735;2.0944rad)
  Profile = -> Sketch118
  Type = 0
FEATURE [PartDesign::Mirrored] Mirrored004
  BaseFeature = -> Pad024
  MirrorPlane = -> Sketch118 [V_Axis]
  Originals = -> [Pad024,XZ_Plane137]
  Placement = pos=(0,0,0) rot=(0.57735,0.57735,0.57735;2.0944rad)
FEATURE [Sketcher::SketchObject] Sketch119
  FullyConstrained = true
  MapMode = 5
  Placement = pos=(-0.8,2e-16,-2e-16) rot=(0.57735,0.57735,0.57735;2.0944rad)
  Support = -> [Mirrored004]
  sketch-geometry (2):
    g0: Circle CenterX=0 CenterY=0 CenterZ=0 NormalX=0 NormalY=0 NormalZ=1 AngleXU=0 Radius=11
    g1: Circle CenterX=0 CenterY=0 CenterZ=0 NormalX=0 NormalY=0 NormalZ=1 AngleXU=0 Radius=13.5
  constraints (4):
    c: Coincident(g0,g-1)
    c: Coincident(g1,g0)
    c: Diameter(g1) = 27
    c: Diameter(g0) = 22
FEATURE [PartDesign::Pad] Pad025
  BaseFeature = -> Mirrored004
  Direction = (1,-8e-16,6e-16)
  Length = 4.2
  Length2 = 100
  Placement = pos=(0,0,0) rot=(0.57735,0.57735,0.57735;2.0944rad)
  Profile = -> Sketch119
  Type = 0
FEATURE [Sketcher::SketchObject] Sketch120
  FullyConstrained = true
  MapMode = 5
  Placement = pos=(-3.5,1.5e-15,-1.5e-15) rot=(0.57735,0.57735,-0.57735;4.18879rad)
  Support = -> [Pad025]
  sketch-geometry (13):
    g0: Ellipse CenterX=0 CenterY=0 CenterZ=0 NormalX=0 NormalY=0 NormalZ=1 MajorRadius=15 MinorRadius=6.38796 AngleXU=0
    g1: LineSegment StartX=15 StartY=0 StartZ=0 EndX=-15 EndY=0 EndZ=0
    g2: LineSegment StartX=0 StartY=6.38796 StartZ=0 EndX=0 EndY=-6.38796 EndZ=0
    g3: GeomPoint X=13.5718 Y=0 Z=0
    g4: GeomPoint X=-13.5718 Y=0 Z=0
    g5: ArcOfCircle CenterX=0 CenterY=0 CenterZ=0 NormalX=0 NormalY=0 NormalZ=1 AngleXU=0 Radius=11 StartAngle=2.69004 EndAngle=3.59315
    g6: ArcOfCircle CenterX=0 CenterY=0 CenterZ=0 NormalX=0 NormalY=0 NormalZ=1 AngleXU=0 Radius=11.5 StartAngle=2.73643 EndAngle=3.54676
    g7: ArcOfCircle CenterX=0 CenterY=0 CenterZ=0 NormalX=0 NormalY=0 NormalZ=1 AngleXU=0 Radius=11 StartAngle=5.83163 EndAngle=6.73474
    g8: ArcOfCircle CenterX=0 CenterY=0 CenterZ=0 NormalX=0 NormalY=0 NormalZ=1 AngleXU=0 Radius=11.5 StartAngle=5.87802 EndAngle=6.68835
    g9: LineSegment StartX=10.5689 StartY=4.53296 StartZ=0 EndX=9.89747 EndY=4.8 EndZ=0
    g10: LineSegment StartX=9.89747 StartY=-4.8 StartZ=0 EndX=10.5689 EndY=-4.53296 EndZ=0
    g11: LineSegment StartX=-10.5689 StartY=4.53296 StartZ=0 EndX=-9.89747 EndY=4.8 EndZ=0
    g12: LineSegment StartX=-9.89747 StartY=-4.8 StartZ=0 EndX=-10.5689 EndY=-4.53296 EndZ=0
  constraints (29):
    c: InternalAlignment(g1-g4 -> g0) x4
    c: Coincident(g0,g-1)
    c: Coincident(g5,g0)
    c: PointOnObject(g5,g0)
    c: PointOnObject(g5,g0)
    c: Coincident(g6,g5)
    c: PointOnObject(g6,g0)
    c: PointOnObject(g6,g0)
    c: Coincident(g7,g5)
    c: PointOnObject(g7,g0)
    c: PointOnObject(g7,g0)
    c: Coincident(g8,g5)
    c: PointOnObject(g8,g0)
    c: PointOnObject(g8,g0)
    c: Radius(g7) = 11
    c: Radius(g8) = 11.5
    c: PointOnObject(g1,g-1)
    c: Radius(g5) = 11
    c: Radius(g6) = 11.5
    c: DistanceY(g5,g5) = 9.6
    c: DistanceX(g1) = 15
    c: Coincident(g9,g8)
    c: Coincident(g9,g7)
    c: Coincident(g10,g7)
    c: Coincident(g10,g8)
    c: Coincident(g11,g6)
    c: Coincident(g5,g11)
    c: Coincident(g12,g5)
    c: Coincident(g12,g6)
FEATURE [PartDesign::Pocket] Pocket047
  BaseFeature = -> Pad025
  Length = 3.3
  Length2 = 100
  Placement = pos=(0,0,0) rot=(0.57735,0.57735,0.57735;2.0944rad)
  Profile = -> Sketch120
  Type = 0
FEATURE [PartDesign::Fillet] Fillet166
  Base = -> Pocket047 [Edge13,Edge14,Edge10,Edge6,Edge3,Edge15,Edge17,Edge16,Edge37,Edge104,Edge94]
  BaseFeature = -> Pocket047
  Placement = pos=(0,0,0) rot=(0.57735,0.57735,0.57735;2.0944rad)
  Radius = 0.2
  SupportTransform = false
FEATURE [PartDesign::Body] Body123  label="Case004"
  Group = -> [Sketch116,Pad023,Sketch117,Pocket046,Sketch118,Pad024,Mirrored004,Sketch119,Pad025,Sketch120,Pocket047,Fillet166]
  Origin = -> Origin141
  Tip = -> Fillet166
FEATURE [App::DocumentObjectGroup] Group034  label="Case005"
  Group = -> [Body123]
FEATURE [App::Part] Part018  label="KFL08-001"
  Group = -> [Group028,Body103,Body104,Body105,Body106,Body107,Body108,Body109,Group029,Body110,Body111,Group030,Body112,Body113,Body114,Body115,Body116,Body117,Body118,Group031,Body121,Body122,Group032,Body119,Body120,Group033,Body102,Group034,Body123]
  Origin = -> Origin142
  Placement = pos=(316,120,80) rot=(0,0,1;3.14159rad)
FEATURE [Sketcher::SketchObject] Sketch121
  FullyConstrained = true
  MapMode = 5
  Placement = pos=(0,0,0) rot=(-0.57735,0.57735,0.57735;4.18879rad)
  Support = -> [YZ_Plane146]
  sketch-geometry (1):
    g0: Circle CenterX=0 CenterY=-7.5 CenterZ=0 NormalX=0 NormalY=0 NormalZ=1 AngleXU=0 Radius=0.25
  constraints (3):
    c: PointOnObject(g0,g-2)
    c: DistanceY(g0) = -7.5
    c: Diameter(g0) = 0.5
FEATURE [Sketcher::SketchObject] Sketch122
  FullyConstrained = true
  MapMode = 5
  Support = -> [XY_Plane139]
  sketch-geometry (2):
    g0: LineSegment StartX=0 StartY=5.5 StartZ=0 EndX=6e-16 EndY=9.5 EndZ=0
    g1: ArcOfCircle CenterX=0 CenterY=7.5 CenterZ=0 NormalX=0 NormalY=0 NormalZ=1 AngleXU=0 Radius=2 StartAngle=4.71239 EndAngle=7.85398
  constraints (7):
    c: PointOnObject(g0,g-2)
    c: PointOnObject(g0,g-2)
    c: PointOnObject(g1,g0)
    c: Coincident(g1,g0)
    c: Coincident(g1,g0)
    c: Radius(g1) = 2
    c: DistanceY(g1) = 7.5
FEATURE [PartDesign::Revolution] Revolution039
  Angle = 360
  Axis = (0,1,0)
  Base = (0,0,0)
  Profile = -> Sketch122
  ReferenceAxis = -> Sketch122 [V_Axis]
  Reversed = true
FEATURE [PartDesign::Body] Body125  label="Ball 036"
  Group = -> [Sketch122,Revolution039]
  Origin = -> Origin144
  Tip = -> Revolution039
FEATURE [PartDesign::FeatureBase] Clone070
  BaseFeature = -> Body125
FEATURE [PartDesign::Body] Body126  label="Ball 037"
  BaseFeature = -> Body125
  Group = -> [Clone070]
  Origin = -> Origin145
  Placement = pos=(0,0,0) rot=(-1,0,0;0.897598rad)
  Tip = -> Clone070
FEATURE [PartDesign::FeatureBase] Clone071
  BaseFeature = -> Body125
FEATURE [PartDesign::Body] Body127  label="Ball 038"
  BaseFeature = -> Body125
  Group = -> [Clone071]
  Origin = -> Origin146
  Placement = pos=(0,0,0) rot=(-1,0,0;1.7952rad)
  Tip = -> Clone071
FEATURE [PartDesign::FeatureBase] Clone072
  BaseFeature = -> Body125
FEATURE [PartDesign::Body] Body128  label="Ball 039"
  BaseFeature = -> Body125
  Group = -> [Clone072]
  Origin = -> Origin147
  Placement = pos=(0,0,0) rot=(1,0,0;3.59039rad)
  Tip = -> Clone072
FEATURE [PartDesign::FeatureBase] Clone073
  BaseFeature = -> Body125
FEATURE [PartDesign::Body] Body129  label="Ball 040"
  BaseFeature = -> Body125
  Group = -> [Clone073]
  Origin = -> Origin148
  Placement = pos=(0,0,0) rot=(1,0,0;2.69279rad)
  Tip = -> Clone073
FEATURE [PartDesign::FeatureBase] Clone074
  BaseFeature = -> Body125
FEATURE [PartDesign::Body] Body130  label="Ball 041"
  BaseFeature = -> Body125
  Group = -> [Clone074]
  Origin = -> Origin149
  Placement = pos=(0,0,0) rot=(1,0,0;1.7952rad)
  Tip = -> Clone074
FEATURE [PartDesign::FeatureBase] Clone075
  BaseFeature = -> Body125
FEATURE [PartDesign::Body] Body131  label="Ball 042"
  BaseFeature = -> Body125
  Group = -> [Clone075]
  Origin = -> Origin150
  Placement = pos=(0,0,0) rot=(1,0,0;0.897598rad)
  Tip = -> Clone075
FEATURE [App::DocumentObjectGroup] Group035  label="Balls005"
  Group = -> [Body125,Body126,Body127,Body128,Body129,Body130,Body131]
FEATURE [Sketcher::SketchObject] Sketch123
  FullyConstrained = true
  MapMode = 5
  Support = -> [XY_Plane148]
  sketch-geometry (7):
    g0: LineSegment StartX=-5 StartY=7.5 StartZ=0 EndX=5 EndY=7.5 EndZ=0
    g1: LineSegment StartX=-0.210977 StartY=7.5 StartZ=0 EndX=0.210977 EndY=7.5 EndZ=0
    g2: ArcOfCircle CenterX=0.25 CenterY=7.5 CenterZ=0 NormalX=0 NormalY=0 NormalZ=1 AngleXU=0 Radius=0.460977 StartAngle=2.43297 EndAngle=3.14159
    g3: ArcOfCircle CenterX=-0.25 CenterY=7.5 CenterZ=0 NormalX=0 NormalY=0 NormalZ=1 AngleXU=0 Radius=0.460977 StartAngle=9.792e-13 EndAngle=0.708626
    g4: LineSegment StartX=-0.1 StartY=7.8 StartZ=0 EndX=-0.1 EndY=7.75 EndZ=0
    g5: LineSegment StartX=-0.1 StartY=7.75 StartZ=0 EndX=0.1 EndY=7.75 EndZ=0
    g6: LineSegment StartX=0.1 StartY=7.75 StartZ=0 EndX=0.1 EndY=7.8 EndZ=0
  constraints (22):
    c: DistanceY(g-1,g0) = 7.5
    c: Symmetric(g0,g0,g-2)
    c: DistanceX(g0,g0) = 10
    c: PointOnObject(g1,g0)
    c: PointOnObject(g1,g0)
    c: Coincident(g3,g1)
    c: Coincident(g2,g1)
    c: Coincident(g2,g4)
    c: Coincident(g4,g5)
    c: Horizontal(g5)
    c: Coincident(g5,g6)
    c: Coincident(g6,g3)
    c: Vertical(g6)
    c: Equal(g3,g2)
    c: Vertical(g4)
    c: Symmetric(g2,g3,g-2)
    c: DistanceX(g5,g5) = 0.2
    c: Distance(g5,g1) = 0.25
    c: DistanceX(g3,g-1) = 0.25
    c: PointOnObject(g3,g1)
    c: PointOnObject(g2,g1)
    c: Distance(g3,g1) = 0.3
FEATURE [PartDesign::Revolution] Revolution040
  Angle = 360
  Axis = (10,0,0)
  Base = (-5,7.5,0)
  Profile = -> Sketch123
  ReferenceAxis = -> Sketch123 [Axis]
FEATURE [PartDesign::Body] Body134  label="Rivet 036"
  Group = -> [Sketch123,Revolution040]
  Origin = -> Origin153
  Placement = pos=(0,0,0) rot=(1,0,0;0.448799rad)
  Tip = -> Revolution040
FEATURE [PartDesign::FeatureBase] Clone077
  BaseFeature = -> Body134
  Placement = pos=(0,0,0) rot=(1,0,0;0.448799rad)
FEATURE [PartDesign::Body] Body135  label="Rivet 037"
  BaseFeature = -> Body134
  Group = -> [Clone077]
  Origin = -> Origin154
  Placement = pos=(0,0,0) rot=(1,0,0;0.897598rad)
  Tip = -> Clone077
FEATURE [PartDesign::FeatureBase] Clone078
  BaseFeature = -> Body134
  Placement = pos=(0,0,0) rot=(1,0,0;0.448799rad)
FEATURE [PartDesign::Body] Body136  label="Rivet 038"
  BaseFeature = -> Body134
  Group = -> [Clone078]
  Origin = -> Origin155
  Placement = pos=(0,0,0) rot=(1,0,0;1.7952rad)
  Tip = -> Clone078
FEATURE [PartDesign::FeatureBase] Clone079
  BaseFeature = -> Body134
  Placement = pos=(0,0,0) rot=(1,0,0;0.448799rad)
FEATURE [PartDesign::Body] Body137  label="Rivet 039"
  BaseFeature = -> Body134
  Group = -> [Clone079]
  Origin = -> Origin156
  Placement = pos=(0,0,0) rot=(1,0,0;2.69279rad)
  Tip = -> Clone079
FEATURE [PartDesign::FeatureBase] Clone080
  BaseFeature = -> Body134
  Placement = pos=(0,0,0) rot=(1,0,0;0.448799rad)
FEATURE [PartDesign::Body] Body138  label="Rivet 040"
  BaseFeature = -> Body134
  Group = -> [Clone080]
  Origin = -> Origin157
  Placement = pos=(0,0,0) rot=(1,0,0;3.59039rad)
  Tip = -> Clone080
FEATURE [PartDesign::FeatureBase] Clone081
  BaseFeature = -> Body134
  Placement = pos=(0,0,0) rot=(1,0,0;0.448799rad)
FEATURE [PartDesign::Body] Body139  label="Rivet 041"
  BaseFeature = -> Body134
  Group = -> [Clone081]
  Origin = -> Origin158
  Placement = pos=(0,0,0) rot=(-1,0,0;1.7952rad)
  Tip = -> Clone081
FEATURE [PartDesign::FeatureBase] Clone082
  BaseFeature = -> Body134
  Placement = pos=(0,0,0) rot=(1,0,0;0.448799rad)
FEATURE [PartDesign::Body] Body140  label="Rivet 042"
  BaseFeature = -> Body134
  Group = -> [Clone082]
  Origin = -> Origin159
  Placement = pos=(0,0,0) rot=(-1,0,0;0.897598rad)
  Tip = -> Clone082
FEATURE [App::DocumentObjectGroup] Group037  label="Rivets005"
  Group = -> [Body134,Body135,Body136,Body137,Body138,Body139,Body140]
FEATURE [Sketcher::SketchObject] Sketch124
  FullyConstrained = true
  MapMode = 5
  Placement = pos=(0,0,0) rot=(1,0,0;1.5708rad)
  Support = -> [XZ_Plane146]
  sketch-geometry (4):
    g0: LineSegment StartX=0 StartY=8.5 StartZ=0 EndX=0.1 EndY=8.5 EndZ=0
    g1: LineSegment StartX=0.1 StartY=8.5 StartZ=0 EndX=0.1 EndY=6.5 EndZ=0
    g2: LineSegment StartX=0.1 StartY=6.5 StartZ=0 EndX=0 EndY=6.5 EndZ=0
    g3: LineSegment StartX=0 StartY=6.5 StartZ=0 EndX=0 EndY=8.5 EndZ=0
  constraints (12):
    c: Coincident(g0,g1)
    c: Coincident(g1,g2)
    c: Coincident(g2,g3)
    c: Coincident(g3,g0)
    c: Horizontal(g0)
    c: Horizontal(g2)
    c: Vertical(g1)
    c: Vertical(g3)
    c: PointOnObject(g0,g-2)
    c: DistanceX(g0,g0) = 0.1
    c: DistanceY(g0) = 8.5
    c: DistanceY(g1) = 6.5
FEATURE [PartDesign::Revolution] Revolution041
  Angle = 360
  Axis = (1,0,0)
  Base = (0,0,0)
  Placement = pos=(0,0,0) rot=(1,0,0;1.5708rad)
  Profile = -> Sketch124
  ReferenceAxis = -> Sketch124 [H_Axis]
FEATURE [Sketcher::SketchObject] Sketch125
  FullyConstrained = true
  MapMode = 5
  Placement = pos=(0,0,0) rot=(0.57735,0.57735,0.57735;2.0944rad)
  Support = -> [YZ_Plane146]
  sketch-geometry (5):
    g0: ArcOfCircle CenterX=0 CenterY=7.5 CenterZ=0 NormalX=0 NormalY=0 NormalZ=1 AngleXU=0 Radius=2.11 StartAngle=5.66076 EndAngle=6.65667
    g1: LineSegment StartX=5e-16 StartY=8.5 StartZ=0 EndX=0 EndY=6.26986 EndZ=0
    g2: ArcOfCircle CenterX=0 CenterY=0 CenterZ=0 NormalX=0 NormalY=0 NormalZ=1 AngleXU=0 Radius=6.5 StartAngle=1.3039 EndAngle=1.5708
    g3: LineSegment StartX=1.71431 StartY=6.26986 StartZ=0 EndX=0 EndY=6.26986 EndZ=0
    g4: ArcOfCircle CenterX=0 CenterY=0 CenterZ=0 NormalX=0 NormalY=0 NormalZ=1 AngleXU=0 Radius=8.5 StartAngle=1.33757 EndAngle=1.5708
  constraints (16):
    c: PointOnObject(g0,g-2)
    c: DistanceY(g0) = 7.5
    c: Radius(g0) = 2.11
    c: PointOnObject(g2,g1)
    c: DistanceY(g2) = 6.5
    c: Coincident(g2,g-1)
    c: Coincident(g3,g2)
    c: Horizontal(g3)
    c: Coincident(g0,g2)
    c: Coincident(g1,g3)
    c: PointOnObject(g1,g-2)
    c: PointOnObject(g1,g-2)
    c: Coincident(g4,g-1)
    c: Coincident(g4,g1)
    c: DistanceY(g1) = 8.5
    c: Coincident(g0,g4)
FEATURE [PartDesign::Revolution] Revolution042
  Angle = 180
  Axis = (-2e-16,3e-16,1)
  Base = (0,0,0)
  BaseFeature = -> Revolution041
  Placement = pos=(0,0,0) rot=(1,0,0;1.5708rad)
  Profile = -> Sketch125
  ReferenceAxis = -> Sketch125 [V_Axis]
  Reversed = true
FEATURE [PartDesign::PolarPattern] PolarPattern020
  Angle = 360
  Axis = -> Sketch125 [N_Axis]
  BaseFeature = -> Revolution042
  Occurrences = 3
  Originals = -> [Revolution042]
  Placement = pos=(0,0,0) rot=(1,0,0;1.5708rad)
  Refine = true
FEATURE [Sketcher::SketchObject] Sketch126
  FullyConstrained = true
  MapMode = 5
  Placement = pos=(0,0,0) rot=(0.57735,0.57735,0.57735;2.0944rad)
  Support = -> [YZ_Plane146]
  sketch-geometry (4):
    g0: ArcOfCircle CenterX=0 CenterY=7.5 CenterZ=0 NormalX=0 NormalY=0 NormalZ=1 AngleXU=0 Radius=2.01 StartAngle=5.57985 EndAngle=6.86228
    g1: LineSegment StartX=0 StartY=6.2 StartZ=0 EndX=1.533 EndY=6.2 EndZ=0
    g2: LineSegment StartX=0 StartY=8.6 StartZ=0 EndX=0 EndY=6.2 EndZ=0
    g3: LineSegment StartX=0 StartY=8.6 StartZ=0 EndX=1.68229 EndY=8.6 EndZ=0
  constraints (13):
    c: PointOnObject(g0,g-2)
    c: DistanceY(g0) = 7.5
    c: Radius(g0) = 2.01
    c: PointOnObject(g1,g-2)
    c: Horizontal(g1)
    c: Coincident(g0,g1)
    c: DistanceY(g1) = 6.2
    c: DistanceY(g2) = 8.6
    c: Coincident(g2,g1)
    c: PointOnObject(g2,g-2)
    c: Coincident(g3,g2)
    c: Horizontal(g3)
    c: Coincident(g0,g3)
FEATURE [PartDesign::Groove] Groove005
  Angle = 360
  Axis = (-2e-16,3e-16,1)
  Base = (0,0,0)
  BaseFeature = -> PolarPattern020
  Placement = pos=(0,0,0) rot=(1,0,0;1.5708rad)
  Profile = -> Sketch126
  ReferenceAxis = -> Sketch126 [V_Axis]
FEATURE [PartDesign::PolarPattern] PolarPattern021
  Angle = 360
  Axis = -> Sketch126 [N_Axis]
  BaseFeature = -> Groove005
  Occurrences = 3
  Originals = -> [Groove005]
  Placement = pos=(0,0,0) rot=(1,0,0;1.5708rad)
FEATURE [PartDesign::Pocket] Pocket048
  BaseFeature = -> PolarPattern021
  Length = 5
  Length2 = 100
  Placement = pos=(0,0,0) rot=(1,0,0;1.5708rad)
  Profile = -> Sketch121
  Type = 1
FEATURE [PartDesign::PolarPattern] PolarPattern022
  Angle = 360
  Axis = -> Sketch121 [N_Axis]
  BaseFeature = -> Pocket048
  Occurrences = 3
  Originals = -> [Pocket048]
  Placement = pos=(0,0,0) rot=(1,0,0;1.5708rad)
FEATURE [PartDesign::Body] Body132  label="Cage 011"
  Group = -> [Sketch124,Revolution041,Sketch125,Revolution042,PolarPattern020,Sketch126,Groove005,PolarPattern021,Sketch121,Pocket048,PolarPattern022]
  Origin = -> Origin151
  Placement = pos=(0,0,0) rot=(-1,0,0;1.5708rad)
  Tip = -> PolarPattern022
FEATURE [PartDesign::FeatureBase] Clone076
  BaseFeature = -> Body132
  Placement = pos=(0,0,0) rot=(-1,0,0;1.5708rad)
FEATURE [PartDesign::Body] Body133  label="Cage 012"
  BaseFeature = -> Body132
  Group = -> [Clone076]
  Origin = -> Origin152
  Placement = pos=(0,0,0) rot=(0,1,0;3.14159rad)
  Tip = -> Clone076
FEATURE [App::DocumentObjectGroup] Group036  label="Cages005"
  Group = -> [Body132,Body133]
FEATURE [Sketcher::SketchObject] Sketch127
  FullyConstrained = true
  MapMode = 5
  Support = -> [XY_Plane155]
  sketch-geometry (14):
    g0: ArcOfCircle CenterX=-1e-16 CenterY=7.5 CenterZ=0 NormalX=0 NormalY=0 NormalZ=1 AngleXU=0 Radius=2 StartAngle=0.848062 EndAngle=2.29353
    g1: LineSegment StartX=-3.5 StartY=11 StartZ=0 EndX=3.5 EndY=11 EndZ=0
    g2: LineSegment StartX=3.5 StartY=11 StartZ=0 EndX=3.5 EndY=9.2 EndZ=0
    g3: LineSegment StartX=2.9 StartY=9 StartZ=0 EndX=1.32288 EndY=9 EndZ=0
    g4: LineSegment StartX=-3.5 StartY=9.2 StartZ=0 EndX=-3.5 EndY=11 EndZ=0
    g5: LineSegment StartX=-1.32288 StartY=9 StartZ=0 EndX=-2.9 EndY=9 EndZ=0
    g6: LineSegment StartX=2.9 StartY=9 StartZ=0 EndX=2.9 EndY=9.5 EndZ=0
    g7: LineSegment StartX=2.9 StartY=9.5 StartZ=0 EndX=3.2 EndY=9.5 EndZ=0
    g8: LineSegment StartX=3.2 StartY=9.5 StartZ=0 EndX=3.2 EndY=9.2 EndZ=0
    g9: LineSegment StartX=3.2 StartY=9.2 StartZ=0 EndX=3.5 EndY=9.2 EndZ=0
    g10: LineSegment StartX=-3.5 StartY=9.2 StartZ=0 EndX=-3.2 EndY=9.2 EndZ=0
    g11: LineSegment StartX=-3.2 StartY=9.2 StartZ=0 EndX=-3.2 EndY=9.5 EndZ=0
    g12: LineSegment StartX=-3.2 StartY=9.5 StartZ=0 EndX=-2.9 EndY=9.5 EndZ=0
    g13: LineSegment StartX=-2.9 StartY=9.5 StartZ=0 EndX=-2.9 EndY=9 EndZ=0
  constraints (41):
    c: Coincident(g1,g2)
    c: Coincident(g4,g1)
    c: Horizontal(g3)
    c: Vertical(g2)
    c: Vertical(g4)
    c: Coincident(g0,g5)
    c: Coincident(g0,g3)
    c: DistanceY(g-1,g0) = 7.5
    c: Radius(g0) = 2
    c: Symmetric(g1,g1,g-2)
    c: Symmetric(g0,g0,g-2)
    c: DistanceY(g1) = 11
    c: DistanceX(g1,g1) = 7
    c: Vertical(g6)
    c: Coincident(g6,g7)
    c: Horizontal(g7)
    c: Coincident(g7,g8)
    c: Vertical(g8)
    c: Coincident(g8,g9)
    c: Coincident(g3,g6)
    c: Coincident(g2,g9)
    c: Horizontal(g10)
    c: Coincident(g10,g11)
    c: Coincident(g11,g12)
    c: Horizontal(g12)
    c: Coincident(g12,g13)
    c: Vertical(g13)
    c: Vertical(g11)
    c: Coincident(g4,g10)
    c: Coincident(g5,g13)
    c: DistanceY(g13,g13) = 0.5
    c: DistanceX(g12,g12) = 0.3
    c: DistanceY(g5,g10) = 0.2
    c: Symmetric(g5,g3,g-2)
    c: DistanceY(g3) = 9
    c: DistanceY(g6) = 9.5
    c: Equal(g7,g12)
    c: Equal(g13,g6)
    c: Horizontal(g9)
    c: Horizontal(g8,g10)
    c: Equal(g12,g10)
FEATURE [PartDesign::Revolution] Revolution043
  Angle = 360
  Axis = (1,0,0)
  Base = (0,0,0)
  Profile = -> Sketch127
  ReferenceAxis = -> X_Axis155
FEATURE [PartDesign::Fillet] Fillet171
  Base = -> Revolution043 [Edge14,Edge15]
  BaseFeature = -> Revolution043
  Radius = 0.3
  SupportTransform = false
FEATURE [PartDesign::Body] Body141  label="Outer Ring006"
  Group = -> [Sketch127,Revolution043,Fillet171]
  Origin = -> Origin160
  Tip = -> Fillet171
FEATURE [Sketcher::SketchObject] Sketch128
  FullyConstrained = true
  MapMode = 5
  Support = -> [XY_Plane156]
  sketch-geometry (14):
    g0: LineSegment StartX=-2.9 StartY=6 StartZ=0 EndX=-1.32288 EndY=6 EndZ=0
    g1: LineSegment StartX=-3.5 StartY=4 StartZ=0 EndX=-3.5 EndY=5.7 EndZ=0
    g2: ArcOfCircle CenterX=1e-16 CenterY=7.5 CenterZ=0 NormalX=0 NormalY=0 NormalZ=1 AngleXU=0 Radius=2 StartAngle=3.98965 EndAngle=5.43512
    g3: LineSegment StartX=1.32288 StartY=6 StartZ=0 EndX=2.9 EndY=6 EndZ=0
    g4: LineSegment StartX=-3.5 StartY=5.7 StartZ=0 EndX=-3.2 EndY=5.7 EndZ=0
    g5: LineSegment StartX=-3.2 StartY=5.7 StartZ=0 EndX=-3.2 EndY=5.5 EndZ=0
    g6: LineSegment StartX=-3.2 StartY=5.5 StartZ=0 EndX=-2.9 EndY=5.5 EndZ=0
    g7: LineSegment StartX=-2.9 StartY=5.5 StartZ=0 EndX=-2.9 EndY=6 EndZ=0
    g8: LineSegment StartX=8.5 StartY=5.7 StartZ=0 EndX=3.2 EndY=5.7 EndZ=0
    g9: LineSegment StartX=3.2 StartY=5.7 StartZ=0 EndX=3.2 EndY=5.5 EndZ=0
    g10: LineSegment StartX=3.2 StartY=5.5 StartZ=0 EndX=2.9 EndY=5.5 EndZ=0
    g11: LineSegment StartX=2.9 StartY=5.5 StartZ=0 EndX=2.9 EndY=6 EndZ=0
    g12: LineSegment StartX=8.5 StartY=4 StartZ=0 EndX=8.5 EndY=5.7 EndZ=0
    g13: LineSegment StartX=-3.5 StartY=4 StartZ=0 EndX=8.5 EndY=4 EndZ=0
  constraints (43):
    c: Horizontal(g0)
    c: Vertical(g1)
    c: DistanceY(g1) = 4
    c: Coincident(g2,g0)
    c: Coincident(g2,g3)
    c: Horizontal(g3)
    c: Radius(g2) = 2
    c: DistanceY(g2) = 7.5
    c: Symmetric(g0,g2,g-2)
    c: Horizontal(g4)
    c: Coincident(g4,g5)
    c: Vertical(g5)
    c: Coincident(g5,g6)
    c: Horizontal(g6)
    c: Coincident(g6,g7)
    c: Vertical(g7)
    c: Horizontal(g8)
    c: Coincident(g8,g9)
    c: Vertical(g9)
    c: Coincident(g9,g10)
    c: Horizontal(g10)
    c: Coincident(g10,g11)
    c: Vertical(g11)
    c: Coincident(g3,g11)
    c: Coincident(g0,g7)
    c: Coincident(g1,g4)
    c: DistanceY(g3) = 6
    c: DistanceY(g6,g0) = 0.5
    c: DistanceX(g4,g4) = 0.3
    c: DistanceX(g6,g6) = 0.3
    c: DistanceY(g5,g4) = 0.2
    c: Vertical(g12)
    c: Equal(g11,g7)
    c: Equal(g5,g9)
    c: DistanceY(g1,g0) = 2
    c: Coincident(g13,g1)
    c: Coincident(g13,g12)
    c: Horizontal(g13)
    c: DistanceX(g13,g13) = 12
    c: DistanceX(g1,g2) = 3.5
    c: Coincident(g8,g12)
    c: DistanceX(g8,g8) = 5.3
    c: Equal(g6,g10)
FEATURE [PartDesign::Revolution] Revolution044
  Angle = 360
  Axis = (1,0,0)
  Base = (0,0,0)
  Profile = -> Sketch128
  ReferenceAxis = -> X_Axis156
FEATURE [PartDesign::Fillet] Fillet172
  Base = -> Revolution044 [Edge13,Edge11]
  BaseFeature = -> Revolution044
  Radius = 0.2
  SupportTransform = false
FEATURE [PartDesign::Body] Body142  label="Inner Ring006"
  Group = -> [Sketch128,Revolution044,Fillet172]
  Origin = -> Origin161
  Tip = -> Fillet172
FEATURE [App::DocumentObjectGroup] Group039  label="Rings005"
  Group = -> [Body141,Body142]
FEATURE [Sketcher::SketchObject] Sketch129
  FullyConstrained = true
  MapMode = 5
  Placement = pos=(0,0,0) rot=(1,0,0;1.5708rad)
  Support = -> [XZ_Plane157]
  sketch-geometry (12):
    g0: LineSegment StartX=2.9 StartY=9.5 StartZ=0 EndX=2.9 EndY=8.5 EndZ=0
    g1: LineSegment StartX=2.9 StartY=8.5 StartZ=0 EndX=3.2 EndY=8.5 EndZ=0
    g2: LineSegment StartX=3.2 StartY=8.5 StartZ=0 EndX=3.2 EndY=6.5 EndZ=0
    g3: LineSegment StartX=3.2 StartY=6.5 StartZ=0 EndX=2.9 EndY=6.5 EndZ=0
    g4: LineSegment StartX=2.9 StartY=6.5 StartZ=0 EndX=2.9 EndY=5.5 EndZ=0
    g5: LineSegment StartX=2.9 StartY=5.5 StartZ=0 EndX=3.2 EndY=5.5 EndZ=0
    g6: LineSegment StartX=3.2 StartY=5.5 StartZ=0 EndX=3.2 EndY=6 EndZ=0
    g7: LineSegment StartX=3.2 StartY=6 StartZ=0 EndX=3.5 EndY=6 EndZ=0
    g8: LineSegment StartX=3.5 StartY=6 StartZ=0 EndX=3.5 EndY=9 EndZ=0
    g9: LineSegment StartX=3.5 StartY=9 StartZ=0 EndX=3.2 EndY=9 EndZ=0
    g10: LineSegment StartX=3.2 StartY=9 StartZ=0 EndX=3.2 EndY=9.5 EndZ=0
    g11: LineSegment StartX=3.2 StartY=9.5 StartZ=0 EndX=2.9 EndY=9.5 EndZ=0
  constraints (36):
    c: Vertical(g0)
    c: Coincident(g0,g1)
    c: Horizontal(g1)
    c: Coincident(g1,g2)
    c: Vertical(g2)
    c: Coincident(g2,g3)
    c: Horizontal(g3)
    c: Coincident(g3,g4)
    c: Vertical(g4)
    c: Coincident(g4,g5)
    c: Horizontal(g5)
    c: Coincident(g5,g6)
    c: Vertical(g6)
    c: Coincident(g6,g7)
    c: Horizontal(g7)
    c: Coincident(g7,g8)
    c: Vertical(g8)
    c: Coincident(g8,g9)
    c: Horizontal(g9)
    c: Coincident(g9,g10)
    c: Vertical(g10)
    c: Coincident(g10,g11)
    c: Coincident(g11,g0)
    c: Horizontal(g11)
    c: DistanceY(g4) = 5.5
    c: DistanceX(g4) = 2.9
    c: DistanceY(g5,g6) = 0.5
    c: DistanceY(g6,g2) = 0.5
    c: DistanceX(g5,g5) = 0.3
    c: Equal(g5,g7)
    c: Equal(g7,g3)
    c: Equal(g3,g1)
    c: Equal(g1,g9)
    c: Equal(g4,g0)
    c: Equal(g6,g10)
    c: DistanceY(g4,g0) = 4
FEATURE [PartDesign::Revolution] Revolution045
  Angle = 360
  Axis = (1,0,0)
  Base = (0,0,0)
  Placement = pos=(0,0,0) rot=(1,0,0;1.5708rad)
  Profile = -> Sketch129
  ReferenceAxis = -> Sketch129 [H_Axis]
FEATURE [PartDesign::Fillet] Fillet173
  Base = -> Revolution045 [Edge14,Edge12]
  BaseFeature = -> Revolution045
  Placement = pos=(0,0,0) rot=(1,0,0;1.5708rad)
  Radius = 0.2
  SupportTransform = false
FEATURE [PartDesign::Body] Body143  label="Seal 011"
  Group = -> [Sketch129,Revolution045,Fillet173]
  Origin = -> Origin162
  Tip = -> Fillet173
FEATURE [PartDesign::FeatureBase] Clone083
  BaseFeature = -> Body143
FEATURE [PartDesign::Body] Body144  label="Seal 012"
  BaseFeature = -> Body143
  Group = -> [Clone083]
  Origin = -> Origin163
  Placement = pos=(0,0,0) rot=(0,1,0;3.14159rad)
  Tip = -> Clone083
FEATURE [App::DocumentObjectGroup] Group038  label="Seals005"
  Group = -> [Body143,Body144]
FEATURE [Sketcher::SketchObject] Sketch130
  AttachmentOffset = pos=(0,0,4) rot=(0,0,1;0rad)
  FullyConstrained = true
  MapMode = 5
  Placement = pos=(0,0,4) rot=(0,0,1;0rad)
  Support = -> [XY_Plane138]
  sketch-geometry (1):
    g0: Circle CenterX=6 CenterY=0 CenterZ=0 NormalX=0 NormalY=0 NormalZ=1 AngleXU=0 Radius=1.5
  constraints (3):
    c: PointOnObject(g0,g-1)
    c: Diameter(g0) = 3
    c: DistanceX(g0,g-3) = 2.5
FEATURE [PartDesign::Pad] Pad026
  Direction = (0,0,1)
  Length = 3
  Length2 = 100
  Profile = -> Sketch130
  Type = 0
FEATURE [Sketcher::SketchObject] Sketch131
  ExternalGeometry = -> [Pad026]
  FullyConstrained = true
  MapMode = 5
  Placement = pos=(0,0,7) rot=(0,0,1;0rad)
  Support = -> [Pad026]
  sketch-geometry (7):
    g0: LineSegment StartX=6.43301 StartY=-0.75 StartZ=0 EndX=6.86603 EndY=-5.43e-14 EndZ=0
    g1: LineSegment StartX=6.86603 StartY=-5.43e-14 StartZ=0 EndX=6.43301 EndY=0.75 EndZ=0
    g2: LineSegment StartX=6.43301 StartY=0.75 StartZ=0 EndX=5.56699 EndY=0.75 EndZ=0
    g3: LineSegment StartX=5.56699 StartY=0.75 StartZ=0 EndX=5.13397 EndY=1.086e-13 EndZ=0
    g4: LineSegment StartX=5.13397 StartY=1.086e-13 StartZ=0 EndX=5.56699 EndY=-0.75 EndZ=0
    g5: LineSegment StartX=5.56699 StartY=-0.75 StartZ=0 EndX=6.43301 EndY=-0.75 EndZ=0
    g6: Circle CenterX=6 CenterY=0 CenterZ=0 NormalX=0 NormalY=0 NormalZ=1 AngleXU=0 Radius=0.866025
  constraints (16):
    c: Coincident(g0,g1)
    c: Coincident(g1,g2)
    c: Coincident(g2,g3)
    c: Coincident(g3,g4)
    c: Coincident(g4,g5)
    c: Coincident(g5,g0)
    c: Equal(g0, g1-g5) x5
    c: PointOnObject(g0,g6)
    c: PointOnObject(g1,g6)
    c: PointOnObject(g2,g6)
    c: PointOnObject(g3,g6)
    c: PointOnObject(g4,g6)
    c: PointOnObject(g5,g6)
    c: Coincident(g6,g-3)
    c: Horizontal(g5)
    c: DistanceY(g4,g2) = 1.5
FEATURE [PartDesign::Pocket] Pocket049
  BaseFeature = -> Pad026
  Length = 1
  Length2 = 100
  Profile = -> Sketch131
  Type = 0
FEATURE [PartDesign::PolarPattern] PolarPattern023
  Angle = 120
  Axis = -> X_Axis138
  BaseFeature = -> Pocket049
  Occurrences = 3
  Originals = -> [Pad026,Pocket049]
FEATURE [PartDesign::Body] Body124
  Group = -> [Sketch130,Pad026,Sketch131,Pocket049,PolarPattern023]
  Origin = -> Origin143
  Tip = -> PolarPattern023
FEATURE [App::DocumentObjectGroup] Group040  label="Set screws005"
  Group = -> [Body124]
FEATURE [Sketcher::SketchObject] Sketch132
  AttachmentOffset = pos=(0,0,-4.1) rot=(0,0,1;0rad)
  FullyConstrained = true
  MapMode = 5
  Placement = pos=(-4.1,9e-16,-9e-16) rot=(0.57735,0.57735,0.57735;2.0944rad)
  Support = -> [YZ_Plane159]
  sketch-geometry (13):
    g0: ArcOfCircle CenterX=0 CenterY=0 CenterZ=0 NormalX=0 NormalY=0 NormalZ=1 AngleXU=0 Radius=13.5 StartAngle=1.12361 EndAngle=2.01799
    g1: ArcOfCircle CenterX=-18.5 CenterY=0 CenterZ=0 NormalX=0 NormalY=0 NormalZ=1 AngleXU=0 Radius=5.5 StartAngle=2.01799 EndAngle=4.2652
    g2: Circle CenterX=-18.5 CenterY=0 CenterZ=0 NormalX=0 NormalY=0 NormalZ=1 AngleXU=0 Radius=2.75
    g3: ArcOfCircle CenterX=18.5 CenterY=0 CenterZ=0 NormalX=0 NormalY=0 NormalZ=1 AngleXU=0 Radius=5.5 StartAngle=5.15958 EndAngle=7.40679
    g4: Circle CenterX=18.5 CenterY=0 CenterZ=0 NormalX=0 NormalY=0 NormalZ=1 AngleXU=0 Radius=2.75
    g5: Circle CenterX=0 CenterY=0 CenterZ=0 NormalX=0 NormalY=0 NormalZ=1 AngleXU=0 Radius=11
    g6: GeomPoint X=-24 Y=0 Z=0
    g7: GeomPoint X=24 Y=0 Z=0
    g8: LineSegment StartX=-20.8784 StartY=4.95916 StartZ=0 EndX=-5.83784 EndY=12.1725 EndZ=0
    g9: LineSegment StartX=-20.8784 StartY=-4.95916 StartZ=0 EndX=-5.83784 EndY=-12.1725 EndZ=0
    g10: LineSegment StartX=5.83784 StartY=-12.1725 StartZ=0 EndX=20.8784 EndY=-4.95916 EndZ=0
    g11: LineSegment StartX=20.8784 StartY=4.95916 StartZ=0 EndX=5.83784 EndY=12.1725 EndZ=0
    g12: ArcOfCircle CenterX=0 CenterY=0 CenterZ=0 NormalX=0 NormalY=0 NormalZ=1 AngleXU=0 Radius=13.5 StartAngle=4.2652 EndAngle=5.15958
  constraints (27):
    c: Coincident(g0,g-1)
    c: PointOnObject(g1,g-1)
    c: Coincident(g2,g1)
    c: Coincident(g4,g3)
    c: Equal(g2,g4)
    c: Equal(g1,g3)
    c: Coincident(g5,g0)
    c: Diameter(g0) = 27
    c: Diameter(g5) = 22
    c: Diameter(g4) = 5.5
    c: Symmetric(g3,g1,g0)
    c: DistanceX(g1,g3) = 37
    c: PointOnObject(g6,g1)
    c: PointOnObject(g7,g3)
    c: PointOnObject(g7,g-1)
    c: PointOnObject(g6,g-1)
    c: DistanceX(g6,g7) = 48
    c: Tangent(g3,g11) = -1.5708
    c: Tangent(g0,g11) = -1.5708
    c: Tangent(g3,g10) = -1.5708
    c: Tangent(g1,g9) = -1.5708
    c: Equal(g0,g12)
    c: Tangent(g12,g9) = -1.5708
    c: Coincident(g0,g12)
    c: Tangent(g0,g8) = 1.5708
    c: Tangent(g1,g8) = 1.5708
    c: Tangent(g12,g10) = -1.5708
FEATURE [PartDesign::Pad] Pad027
  Direction = (1,-2e-16,3e-16)
  Length = 3.3
  Length2 = 100
  Placement = pos=(0,0,0) rot=(0.57735,0.57735,0.57735;2.0944rad)
  Profile = -> Sketch132
  Type = 0
FEATURE [Sketcher::SketchObject] Sketch133
  ExternalGeometry = -> [Pad027]
  FullyConstrained = true
  MapMode = 5
  Placement = pos=(-4.1,9e-16,-1e-15) rot=(0.57735,0.57735,-0.57735;4.18879rad)
  Support = -> [Pad027]
  sketch-geometry (12):
    g0: ArcOfCircle CenterX=0 CenterY=0 CenterZ=0 NormalX=0 NormalY=0 NormalZ=1 AngleXU=0 Radius=12.3 StartAngle=4.2652 EndAngle=5.15958
    g1: ArcOfCircle CenterX=-18.5 CenterY=-1.04e-14 CenterZ=0 NormalX=0 NormalY=0 NormalZ=1 AngleXU=0 Radius=4.55 StartAngle=4.98418 EndAngle=7.58219
    g2: ArcOfCircle CenterX=18.5 CenterY=1.02e-14 CenterZ=0 NormalX=0 NormalY=0 NormalZ=1 AngleXU=0 Radius=4.55 StartAngle=1.84259 EndAngle=4.44059
    g3: LineSegment StartX=-17.3605 StartY=5.31545 StartZ=0 EndX=-5.31892 EndY=11.0905 EndZ=0
    g4: LineSegment StartX=-17.3605 StartY=-5.31545 StartZ=0 EndX=-5.31892 EndY=-11.0905 EndZ=0
    g5: LineSegment StartX=5.31892 StartY=-11.0905 StartZ=0 EndX=17.3605 EndY=-5.31545 EndZ=0
    g6: LineSegment StartX=17.3605 StartY=5.31545 StartZ=0 EndX=5.31892 EndY=11.0905 EndZ=0
    g7: ArcOfCircle CenterX=0 CenterY=0 CenterZ=0 NormalX=0 NormalY=0 NormalZ=1 AngleXU=0 Radius=12.3 StartAngle=1.12361 EndAngle=2.01799
    g8: ArcOfCircle CenterX=-17.1443 CenterY=4.86462 CenterZ=0 NormalX=0 NormalY=0 NormalZ=1 AngleXU=0 Radius=0.5 StartAngle=2.01799 EndAngle=4.44059
    g9: ArcOfCircle CenterX=-17.1443 CenterY=-4.86462 CenterZ=0 NormalX=0 NormalY=0 NormalZ=1 AngleXU=0 Radius=0.5 StartAngle=1.84259 EndAngle=4.2652
    g10: ArcOfCircle CenterX=17.1443 CenterY=-4.86462 CenterZ=0 NormalX=0 NormalY=0 NormalZ=1 AngleXU=0 Radius=0.5 StartAngle=5.15958 EndAngle=7.58219
    g11: ArcOfCircle CenterX=17.1443 CenterY=4.86462 CenterZ=0 NormalX=0 NormalY=0 NormalZ=1 AngleXU=0 Radius=0.5 StartAngle=4.98418 EndAngle=7.40679
  constraints (30):
    c: Coincident(g0,g-1)
    c: Coincident(g1,g-3)
    c: Coincident(g2,g-4)
    c: Equal(g2,g1)
    c: Parallel(g3,g-5)
    c: Distance(g3,g-5) = 1.2
    c: Coincident(g7,g3) = 1.5708
    c: Tangent(g0,g4) = -1.5708
    c: Equal(g0,g7)
    c: Tangent(g0,g5) = -1.5708
    c: Tangent(g7,g6) = -1.5708
    c: Coincident(g0,g7)
    c: Vertical(g0,g3)
    c: Tangent(g1,g8) = 1.5708
    c: Tangent(g3,g8) = 1.5708
    c: Tangent(g4,g9) = -1.5708
    c: Tangent(g1,g9) = 1.5708
    c: Tangent(g2,g10) = 1.5708
    c: Tangent(g5,g10) = -1.5708
    c: Tangent(g6,g11) = -1.5708
    c: Tangent(g2,g11) = 1.5708
    c: Equal(g8,g9)
    c: Equal(g9,g10)
    c: Equal(g10,g11)
    c: Parallel(g-6,g6)
    c: Parallel(g5,g3)
    c: Parallel(g4,g6)
    c: Radius(g-4) = 2.75
    c: Radius(g2) = 4.55
    c: Radius(g11) = 0.5
FEATURE [PartDesign::Pocket] Pocket050
  BaseFeature = -> Pad027
  Length = 0.6
  Length2 = 100
  Placement = pos=(0,0,0) rot=(0.57735,0.57735,0.57735;2.0944rad)
  Profile = -> Sketch133
  Type = 0
FEATURE [Sketcher::SketchObject] Sketch134
  ExternalGeometry = -> [Pocket050]
  FullyConstrained = true
  MapMode = 5
  Placement = pos=(-0.8,2e-16,-2e-16) rot=(0.57735,0.57735,0.57735;2.0944rad)
  Support = -> [Pocket050]
  sketch-geometry (7):
    g0: Circle CenterX=-18.5 CenterY=1.66e-14 CenterZ=0 NormalX=0 NormalY=0 NormalZ=1 AngleXU=0 Radius=2.75
    g1: LineSegment StartX=-20.8784 StartY=4.95916 StartZ=0 EndX=-14.8432 EndY=7.85358 EndZ=0
    g2: LineSegment StartX=-20.8784 StartY=-4.95916 StartZ=0 EndX=-14.8432 EndY=-7.85358 EndZ=0
    g3: ArcOfCircle CenterX=-18.5 CenterY=1.66e-14 CenterZ=0 NormalX=0 NormalY=0 NormalZ=1 AngleXU=0 Radius=5.5 StartAngle=2.01799 EndAngle=4.2652
    g4: ArcOfCircle CenterX=0 CenterY=0 CenterZ=0 NormalX=0 NormalY=0 NormalZ=1 AngleXU=0 Radius=15 StartAngle=2.69212 EndAngle=3.59107
    g5: ArcOfCircle CenterX=-14.4108 CenterY=6.95191 CenterZ=0 NormalX=0 NormalY=0 NormalZ=1 AngleXU=0 Radius=1 StartAngle=5.83371 EndAngle=8.30117
    g6: ArcOfCircle CenterX=-14.4108 CenterY=-6.95191 CenterZ=0 NormalX=0 NormalY=0 NormalZ=1 AngleXU=0 Radius=1 StartAngle=4.2652 EndAngle=6.73266
  constraints (17):
    c: Coincident(g0,g-6)
    c: Equal(g-5,g0)
    c: Coincident(g1,g-6)
    c: Coincident(g2,g-6)
    c: Coincident(g3,g0)
    c: Coincident(g3,g1)
    c: Coincident(g3,g2)
    c: Coincident(g4,g-1)
    c: Radius(g4) = 15
    c: Tangent(g1,g5) = 1.5708
    c: Tangent(g4,g5) = 1.5708
    c: Tangent(g2,g6) = -1.5708
    c: Tangent(g4,g6) = 1.5708
    c: Radius(g6) = 1
    c: PointOnObject(g2,g-4)
    c: Equal(g5,g6)
    c: PointOnObject(g1,g-3)
FEATURE [PartDesign::Pad] Pad028
  BaseFeature = -> Pocket050
  Direction = (1,-9e-16,6e-16)
  Length = 0.7
  Length2 = 100
  Placement = pos=(0,0,0) rot=(0.57735,0.57735,0.57735;2.0944rad)
  Profile = -> Sketch134
  Type = 0
FEATURE [PartDesign::Mirrored] Mirrored005
  BaseFeature = -> Pad028
  MirrorPlane = -> Sketch134 [V_Axis]
  Originals = -> [Pad028,XZ_Plane159]
  Placement = pos=(0,0,0) rot=(0.57735,0.57735,0.57735;2.0944rad)
FEATURE [Sketcher::SketchObject] Sketch135
  FullyConstrained = true
  MapMode = 5
  Placement = pos=(-0.8,2e-16,-2e-16) rot=(0.57735,0.57735,0.57735;2.0944rad)
  Support = -> [Mirrored005]
  sketch-geometry (2):
    g0: Circle CenterX=0 CenterY=0 CenterZ=0 NormalX=0 NormalY=0 NormalZ=1 AngleXU=0 Radius=11
    g1: Circle CenterX=0 CenterY=0 CenterZ=0 NormalX=0 NormalY=0 NormalZ=1 AngleXU=0 Radius=13.5
  constraints (4):
    c: Coincident(g0,g-1)
    c: Coincident(g1,g0)
    c: Diameter(g1) = 27
    c: Diameter(g0) = 22
FEATURE [PartDesign::Pad] Pad029
  BaseFeature = -> Mirrored005
  Direction = (1,-8e-16,6e-16)
  Length = 4.2
  Length2 = 100
  Placement = pos=(0,0,0) rot=(0.57735,0.57735,0.57735;2.0944rad)
  Profile = -> Sketch135
  Type = 0
FEATURE [Sketcher::SketchObject] Sketch136
  FullyConstrained = true
  MapMode = 5
  Placement = pos=(-3.5,1.5e-15,-1.5e-15) rot=(0.57735,0.57735,-0.57735;4.18879rad)
  Support = -> [Pad029]
  sketch-geometry (13):
    g0: Ellipse CenterX=0 CenterY=0 CenterZ=0 NormalX=0 NormalY=0 NormalZ=1 MajorRadius=15 MinorRadius=6.38796 AngleXU=0
    g1: LineSegment StartX=15 StartY=0 StartZ=0 EndX=-15 EndY=0 EndZ=0
    g2: LineSegment StartX=0 StartY=6.38796 StartZ=0 EndX=0 EndY=-6.38796 EndZ=0
    g3: GeomPoint X=13.5718 Y=0 Z=0
    g4: GeomPoint X=-13.5718 Y=0 Z=0
    g5: ArcOfCircle CenterX=0 CenterY=0 CenterZ=0 NormalX=0 NormalY=0 NormalZ=1 AngleXU=0 Radius=11 StartAngle=2.69004 EndAngle=3.59315
    g6: ArcOfCircle CenterX=0 CenterY=0 CenterZ=0 NormalX=0 NormalY=0 NormalZ=1 AngleXU=0 Radius=11.5 StartAngle=2.73643 EndAngle=3.54676
    g7: ArcOfCircle CenterX=0 CenterY=0 CenterZ=0 NormalX=0 NormalY=0 NormalZ=1 AngleXU=0 Radius=11 StartAngle=5.83163 EndAngle=6.73474
    g8: ArcOfCircle CenterX=0 CenterY=0 CenterZ=0 NormalX=0 NormalY=0 NormalZ=1 AngleXU=0 Radius=11.5 StartAngle=5.87802 EndAngle=6.68835
    g9: LineSegment StartX=10.5689 StartY=4.53296 StartZ=0 EndX=9.89747 EndY=4.8 EndZ=0
    g10: LineSegment StartX=9.89747 StartY=-4.8 StartZ=0 EndX=10.5689 EndY=-4.53296 EndZ=0
    g11: LineSegment StartX=-10.5689 StartY=4.53296 StartZ=0 EndX=-9.89747 EndY=4.8 EndZ=0
    g12: LineSegment StartX=-9.89747 StartY=-4.8 StartZ=0 EndX=-10.5689 EndY=-4.53296 EndZ=0
  constraints (29):
    c: InternalAlignment(g1-g4 -> g0) x4
    c: Coincident(g0,g-1)
    c: Coincident(g5,g0)
    c: PointOnObject(g5,g0)
    c: PointOnObject(g5,g0)
    c: Coincident(g6,g5)
    c: PointOnObject(g6,g0)
    c: PointOnObject(g6,g0)
    c: Coincident(g7,g5)
    c: PointOnObject(g7,g0)
    c: PointOnObject(g7,g0)
    c: Coincident(g8,g5)
    c: PointOnObject(g8,g0)
    c: PointOnObject(g8,g0)
    c: Radius(g7) = 11
    c: Radius(g8) = 11.5
    c: PointOnObject(g1,g-1)
    c: Radius(g5) = 11
    c: Radius(g6) = 11.5
    c: DistanceY(g5,g5) = 9.6
    c: DistanceX(g1) = 15
    c: Coincident(g9,g8)
    c: Coincident(g9,g7)
    c: Coincident(g10,g7)
    c: Coincident(g10,g8)
    c: Coincident(g11,g6)
    c: Coincident(g5,g11)
    c: Coincident(g12,g5)
    c: Coincident(g12,g6)
FEATURE [PartDesign::Pocket] Pocket051
  BaseFeature = -> Pad029
  Length = 3.3
  Length2 = 100
  Placement = pos=(0,0,0) rot=(0.57735,0.57735,0.57735;2.0944rad)
  Profile = -> Sketch136
  Type = 0
FEATURE [PartDesign::Fillet] Fillet170
  Base = -> Pocket051 [Edge13,Edge14,Edge10,Edge6,Edge3,Edge15,Edge17,Edge16,Edge37,Edge104,Edge94]
  BaseFeature = -> Pocket051
  Placement = pos=(0,0,0) rot=(0.57735,0.57735,0.57735;2.0944rad)
  Radius = 0.2
  SupportTransform = false
FEATURE [PartDesign::Body] Body145  label="Case006"
  Group = -> [Sketch132,Pad027,Sketch133,Pocket050,Sketch134,Pad028,Mirrored005,Sketch135,Pad029,Sketch136,Pocket051,Fillet170]
  Origin = -> Origin164
  Tip = -> Fillet170
FEATURE [App::DocumentObjectGroup] Group041  label="Case007"
  Group = -> [Body145]
FEATURE [App::Part] Part019  label="KFL08-002"
  Group = -> [Group035,Body125,Body126,Body127,Body128,Body129,Body130,Body131,Group036,Body132,Body133,Group037,Body134,Body135,Body136,Body137,Body138,Body139,Body140,Group038,Body143,Body144,Group039,Body141,Body142,Group040,Body124,Group041,Body145]
  Origin = -> Origin165
  Placement = pos=(24,120,80) rot=(0,0,1;0rad)
FEATURE [PartDesign::Body] Body150  label="Stator"
  Origin = -> Origin176
FEATURE [Part::FeaturePython] Screw  label="M2.5x25-Screw"  # Fasteners workbench fastener (typed FeaturePython)
  Placement = pos=(15.5,15.5,4) rot=(0,1,0;3.14159rad)
  diameter = 3
  invert = true
  length = 10
  matchOuter = true
  offset = 1
  thread = true
  type = 16
FEATURE [Part::FeaturePython] Screw001  label="M2.5x25-Screw006"  # Fasteners workbench fastener (typed FeaturePython)
  Placement = pos=(-15.5,-15.5,4) rot=(0,1,0;3.14159rad)
  diameter = 3
  invert = true
  length = 10
  matchOuter = true
  offset = 1
  thread = true
  type = 16
FEATURE [Part::FeaturePython] Screw002  label="M2.5x25-Screw005"  # Fasteners workbench fastener (typed FeaturePython)
  Placement = pos=(15.5,-15.5,4) rot=(0,1,0;3.14159rad)
  diameter = 3
  invert = true
  length = 10
  matchOuter = true
  offset = 1
  thread = true
  type = 16
FEATURE [Part::FeaturePython] Screw003  label="M2.5x25-Screw007"  # Fasteners workbench fastener (typed FeaturePython)
  Placement = pos=(-15.5,15.5,4) rot=(0,1,0;3.14159rad)
  diameter = 3
  invert = true
  length = 10
  matchOuter = true
  offset = 1
  thread = true
  type = 16
FEATURE [App::Part] Part025  label="Screw"
  Group = -> [Screw,Screw001,Screw002,Screw003]
  Origin = -> Origin175
FEATURE [Sketcher::SketchObject] Sketch137
  FullyConstrained = false
  MapMode = 5
  Support = -> [XY_Plane161]
  sketch-geometry (4):
    g0: LineSegment StartX=-21.15 StartY=21.15 StartZ=0 EndX=21.15 EndY=21.15 EndZ=0
    g1: LineSegment StartX=21.15 StartY=21.15 StartZ=0 EndX=21.15 EndY=-21.15 EndZ=0
    g2: LineSegment StartX=21.15 StartY=-21.15 StartZ=0 EndX=-21.15 EndY=-21.15 EndZ=0
    g3: LineSegment StartX=-21.15 StartY=-21.15 StartZ=0 EndX=-21.15 EndY=21.15 EndZ=0
  constraints (11):
    c: Coincident(g0,g1)
    c: Coincident(g1,g2)
    c: Coincident(g2,g3)
    c: Coincident(g3,g0)
    c: Horizontal(g0)
    c: Horizontal(g2)
    c: Vertical(g1)
    c: Vertical(g3)
    c: Symmetric(g0,g1,g-1)
    c: DistanceX(g0,g0) = 42.3
    c: Equal(g0,g3)
FEATURE [PartDesign::Pad] Pad030
  AllowMultiFace = false
  Direction = (1,1,1)
  Length = 9.6
  Length2 = 100
  Profile = -> Sketch137
  Refine = true
  Type = 0
FEATURE [Sketcher::SketchObject] Sketch138
  ExternalGeometry = -> [Pad030]
  FullyConstrained = false
  MapMode = 5
  Support = -> [XY_Plane161]
  sketch-geometry (4):
    g0: LineSegment StartX=21.15 StartY=8.2 StartZ=0 EndX=25.45 EndY=8.2 EndZ=0
    g1: LineSegment StartX=25.45 StartY=8.2 StartZ=0 EndX=25.45 EndY=-8.2 EndZ=0
    g2: LineSegment StartX=25.45 StartY=-8.2 StartZ=0 EndX=21.15 EndY=-8.2 EndZ=0
    g3: LineSegment StartX=21.15 StartY=-8.2 StartZ=0 EndX=21.15 EndY=8.2 EndZ=0
  constraints (11):
    c: Coincident(g0,g1)
    c: Coincident(g1,g2)
    c: Coincident(g2,g3)
    c: Coincident(g3,g0)
    c: Horizontal(g0)
    c: Horizontal(g2)
    c: Vertical(g3)
    c: PointOnObject(g0,g-3)
    c: Symmetric(g1,g0,g-1)
    c: DistanceX(g0,g0) = 4.3
    c: DistanceY(g1,g1) = 16.4
FEATURE [PartDesign::Pad] Pad031
  AllowMultiFace = false
  BaseFeature = -> Pad030
  Direction = (1,1,1)
  Length = 3.6
  Length2 = 100
  Profile = -> Sketch138
  Refine = true
  Type = 0
FEATURE [PartDesign::Chamfer] Chamfer004
  Angle = 45
  Base = -> Pad031 [Edge13,Edge5,Edge1,Edge2]
  BaseFeature = -> Pad031
  ChamferType = 0
  FlipDirection = false
  Size = 5
  Size2 = 1
  SupportTransform = false
FEATURE [PartDesign::Fillet] Fillet174
  Base = -> Chamfer004 [Edge33,Edge28,Edge18,Edge3,Edge2,Edge16,Edge30,Edge25]
  BaseFeature = -> Chamfer004
  Radius = 2
  SupportTransform = false
FEATURE [Sketcher::SketchObject] Sketch139
  FullyConstrained = false
  MapMode = 5
  Support = -> [XY_Plane162]
  sketch-geometry (4):
    g0: LineSegment StartX=-21 StartY=21 StartZ=0 EndX=21 EndY=21 EndZ=0
    g1: LineSegment StartX=21 StartY=21 StartZ=0 EndX=21 EndY=-21 EndZ=0
    g2: LineSegment StartX=21 StartY=-21 StartZ=0 EndX=-21 EndY=-21 EndZ=0
    g3: LineSegment StartX=-21 StartY=-21 StartZ=0 EndX=-21 EndY=21 EndZ=0
  constraints (11):
    c: Coincident(g0,g1)
    c: Coincident(g1,g2)
    c: Coincident(g2,g3)
    c: Coincident(g3,g0)
    c: Horizontal(g0)
    c: Horizontal(g2)
    c: Vertical(g1)
    c: Vertical(g3)
    c: DistanceX(g0,g0) = 42
    c: Symmetric(g0,g1,g-1)
    c: Equal(g0,g3)
FEATURE [PartDesign::Pad] Pad032
  AllowMultiFace = false
  Direction = (1,1,1)
  Length = 22.75
  Length2 = 100
  Profile = -> Sketch139
  Refine = true
  Type = 0
FEATURE [PartDesign::Chamfer] Chamfer005
  Angle = 45
  Base = -> Pad032 [Edge8,Edge1,Edge5,Edge2]
  BaseFeature = -> Pad032
  ChamferType = 0
  FlipDirection = false
  Size = 7.5
  Size2 = 1
  SupportTransform = false
FEATURE [Sketcher::SketchObject] Sketch140
  FullyConstrained = false
  MapMode = 5
  Support = -> [XY_Plane163]
  sketch-geometry (4):
    g0: LineSegment StartX=-21.15 StartY=21.15 StartZ=0 EndX=21.15 EndY=21.15 EndZ=0
    g1: LineSegment StartX=21.15 StartY=21.15 StartZ=0 EndX=21.15 EndY=-21.15 EndZ=0
    g2: LineSegment StartX=21.15 StartY=-21.15 StartZ=0 EndX=-21.15 EndY=-21.15 EndZ=0
    g3: LineSegment StartX=-21.15 StartY=-21.15 StartZ=0 EndX=-21.15 EndY=21.15 EndZ=0
  constraints (11):
    c: Coincident(g0,g1)
    c: Coincident(g1,g2)
    c: Coincident(g2,g3)
    c: Coincident(g3,g0)
    c: Horizontal(g0)
    c: Horizontal(g2)
    c: Vertical(g1)
    c: Vertical(g3)
    c: Symmetric(g0,g1,g-1)
    c: DistanceX(g0,g0) = 42.3
    c: Equal(g0,g3)
FEATURE [PartDesign::Pad] Pad033
  AllowMultiFace = false
  Direction = (1,1,1)
  Length = 7.75
  Length2 = 100
  Profile = -> Sketch140
  Refine = true
  Type = 0
FEATURE [PartDesign::Chamfer] Chamfer006
  Angle = 45
  Base = -> Pad033 [Edge8,Edge5,Edge2,Edge1]
  BaseFeature = -> Pad033
  ChamferType = 0
  FlipDirection = false
  Size = 5
  Size2 = 1
  SupportTransform = false
FEATURE [PartDesign::Fillet] Fillet175
  Base = -> Chamfer006 [Edge22,Edge24,Edge23,Edge21,Edge12,Edge2,Edge3,Edge14]
  BaseFeature = -> Chamfer006
  Radius = 2
  SupportTransform = false
FEATURE [Sketcher::SketchObject] Sketch141
  FullyConstrained = false
  MapMode = 5
  Placement = pos=(0,0,0) rot=(1,0,0;3.14159rad)
  Support = -> [Fillet174]
  sketch-geometry (8):
    g0: LineSegment StartX=-15.5 StartY=15.5 StartZ=0 EndX=15.5 EndY=15.5 EndZ=0
    g1: LineSegment StartX=15.5 StartY=15.5 StartZ=0 EndX=15.5 EndY=-15.5 EndZ=0
    g2: LineSegment StartX=15.5 StartY=-15.5 StartZ=0 EndX=-15.5 EndY=-15.5 EndZ=0
    g3: LineSegment StartX=-15.5 StartY=-15.5 StartZ=0 EndX=-15.5 EndY=15.5 EndZ=0
    g4: Circle CenterX=-15.5 CenterY=15.5 CenterZ=0 NormalX=0 NormalY=0 NormalZ=1 AngleXU=0 Radius=1.225
    g5: Circle CenterX=15.5 CenterY=15.5 CenterZ=0 NormalX=0 NormalY=0 NormalZ=1 AngleXU=0 Radius=1.225
    g6: Circle CenterX=15.5 CenterY=-15.5 CenterZ=0 NormalX=0 NormalY=0 NormalZ=1 AngleXU=0 Radius=1.225
    g7: Circle CenterX=-15.5 CenterY=-15.5 CenterZ=0 NormalX=0 NormalY=0 NormalZ=1 AngleXU=0 Radius=1.225
  constraints (19):
    c: Coincident(g0,g1)
    c: Coincident(g1,g2)
    c: Coincident(g2,g3)
    c: Coincident(g3,g0)
    c: Horizontal(g0)
    c: Horizontal(g2)
    c: Vertical(g1)
    c: Vertical(g3)
    c: Symmetric(g0,g1,g-1)
    c: DistanceX(g0,g0) = 31
    c: Equal(g3,g0)
    c: Coincident(g4,g0)
    c: Coincident(g5,g0)
    c: Coincident(g6,g1)
    c: Coincident(g7,g2)
    c: Equal(g6,g5)
    c: Equal(g5,g4)
    c: Equal(g4,g7)
    c: Radius(g4) = 1.225
FEATURE [PartDesign::Hole] Hole
  AllowMultiFace = false
  BaseFeature = -> Fillet174
  Depth = 25
  DepthType = 0
  Diameter = 3
  DrillForDepth = false
  DrillPoint = 1
  DrillPointAngle = 118
  HoleCutCountersinkAngle = 90
  HoleCutCustomValues = false
  HoleCutDepth = 5
  HoleCutDiameter = 5
  HoleCutType = 1
  ModelActualThread = false
  Profile = -> Sketch141
  Refine = true
  Tapered = false
  TaperedAngle = 90
  ThreadAngle = 0
  ThreadClass = 0
  ThreadCutOffInner = 0
  ThreadCutOffOuter = 0
  ThreadDirection = 0
  ThreadFit = 0
  ThreadPitch = 0
  ThreadSize = 0
  ThreadType = 0
  Threaded = false
FEATURE [Sketcher::SketchObject] Sketch142
  FullyConstrained = false
  MapMode = 5
  Placement = pos=(0,0,0) rot=(1,0,0;3.14159rad)
  Support = -> [Chamfer005]
  sketch-geometry (8):
    g0: LineSegment StartX=-15.5 StartY=15.5 StartZ=0 EndX=15.5 EndY=15.5 EndZ=0
    g1: LineSegment StartX=15.5 StartY=15.5 StartZ=0 EndX=15.5 EndY=-15.5 EndZ=0
    g2: LineSegment StartX=15.5 StartY=-15.5 StartZ=0 EndX=-15.5 EndY=-15.5 EndZ=0
    g3: LineSegment StartX=-15.5 StartY=-15.5 StartZ=0 EndX=-15.5 EndY=15.5 EndZ=0
    g4: Circle CenterX=-15.5 CenterY=15.5 CenterZ=0 NormalX=0 NormalY=0 NormalZ=1 AngleXU=0 Radius=1.22
    g5: Circle CenterX=15.5 CenterY=15.5 CenterZ=0 NormalX=0 NormalY=0 NormalZ=1 AngleXU=0 Radius=1.22
    g6: Circle CenterX=15.5 CenterY=-15.5 CenterZ=0 NormalX=0 NormalY=0 NormalZ=1 AngleXU=0 Radius=1.22
    g7: Circle CenterX=-15.5 CenterY=-15.5 CenterZ=0 NormalX=0 NormalY=0 NormalZ=1 AngleXU=0 Radius=1.22
  constraints (19):
    c: Coincident(g0,g1)
    c: Coincident(g1,g2)
    c: Coincident(g2,g3)
    c: Coincident(g3,g0)
    c: Horizontal(g0)
    c: Horizontal(g2)
    c: Vertical(g1)
    c: Vertical(g3)
    c: Equal(g0,g3)
    c: Symmetric(g0,g1,g-1)
    c: DistanceX(g0,g0) = 31
    c: Coincident(g4,g0)
    c: Coincident(g5,g0)
    c: Coincident(g6,g1)
    c: Coincident(g7,g2)
    c: Equal(g6,g5)
    c: Equal(g5,g4)
    c: Equal(g4,g7)
    c: Radius(g4) = 1.22
FEATURE [PartDesign::Pocket] Pocket053
  AllowMultiFace = false
  BaseFeature = -> Chamfer005
  Length = 5
  Length2 = 100
  Profile = -> Sketch142
  Refine = true
  Type = 1
FEATURE [Sketcher::SketchObject] Sketch143
  FullyConstrained = false
  MapMode = 5
  Placement = pos=(0,0,7.75) rot=(0,0,1;0rad)
  Support = -> [Fillet175]
  sketch-geometry (8):
    g0: LineSegment StartX=-15.5 StartY=15.5 StartZ=0 EndX=15.5 EndY=15.5 EndZ=0
    g1: LineSegment StartX=15.5 StartY=15.5 StartZ=0 EndX=15.5 EndY=-15.5 EndZ=0
    g2: LineSegment StartX=15.5 StartY=-15.5 StartZ=0 EndX=-15.5 EndY=-15.5 EndZ=0
    g3: LineSegment StartX=-15.5 StartY=-15.5 StartZ=0 EndX=-15.5 EndY=15.5 EndZ=0
    g4: Circle CenterX=-15.5 CenterY=15.5 CenterZ=0 NormalX=0 NormalY=0 NormalZ=1 AngleXU=0 Radius=1.225
    g5: Circle CenterX=15.5 CenterY=15.5 CenterZ=0 NormalX=0 NormalY=0 NormalZ=1 AngleXU=0 Radius=1.225
    g6: Circle CenterX=15.5 CenterY=-15.5 CenterZ=0 NormalX=0 NormalY=0 NormalZ=1 AngleXU=0 Radius=1.225
    g7: Circle CenterX=-15.5 CenterY=-15.5 CenterZ=0 NormalX=0 NormalY=0 NormalZ=1 AngleXU=0 Radius=1.225
  constraints (19):
    c: Coincident(g0,g1)
    c: Coincident(g1,g2)
    c: Coincident(g2,g3)
    c: Coincident(g3,g0)
    c: Horizontal(g0)
    c: Horizontal(g2)
    c: Vertical(g1)
    c: Vertical(g3)
    c: Equal(g0,g3)
    c: Symmetric(g0,g1,g-1)
    c: DistanceX(g0,g0) = 31
    c: Coincident(g4,g0)
    c: Coincident(g7,g2)
    c: Coincident(g0,g5)
    c: Coincident(g1,g6)
    c: Equal(g7,g4)
    c: Equal(g4,g5)
    c: Equal(g5,g6)
    c: Radius(g4) = 1.225
FEATURE [PartDesign::Pocket] Pocket054
  AllowMultiFace = false
  BaseFeature = -> Fillet175
  Length = 5
  Length2 = 100
  Profile = -> Sketch143
  Refine = true
  Type = 1
FEATURE [Sketcher::SketchObject] Sketch144
  FullyConstrained = false
  MapMode = 5
  Placement = pos=(0,0,7.75) rot=(0,0,1;0rad)
  Support = -> [Pocket054]
  sketch-geometry (1):
    g0: Circle CenterX=0 CenterY=0 CenterZ=0 NormalX=0 NormalY=0 NormalZ=1 AngleXU=0 Radius=14
  constraints (2):
    c: Coincident(g0,g-1)
    c: Radius(g0) = 14
FEATURE [PartDesign::Pocket] Pocket055
  AllowMultiFace = false
  BaseFeature = -> Pocket054
  Length = 1
  Length2 = 100
  Profile = -> Sketch144
  Refine = true
  Type = 0
FEATURE [Sketcher::SketchObject] Sketch145
  FullyConstrained = false
  MapMode = 5
  Placement = pos=(0,0,6.75) rot=(0,0,1;0rad)
  Support = -> [Pocket055]
  sketch-geometry (1):
    g0: Circle CenterX=0 CenterY=0 CenterZ=0 NormalX=0 NormalY=0 NormalZ=1 AngleXU=0 Radius=11
  constraints (2):
    c: Coincident(g0,g-1)
    c: Radius(g0) = 11
FEATURE [PartDesign::Pad] Pad034
  AllowMultiFace = false
  BaseFeature = -> Pocket055
  Direction = (1,1,1)
  Length = 3
  Length2 = 100
  Profile = -> Sketch145
  Refine = true
  Type = 0
FEATURE [PartDesign::Draft] Draft
  Angle = 10
  Base = -> Pad034 [Face25]
  BaseFeature = -> Pad034
  NeutralPlane = -> Pad034 [Face24]
  SupportTransform = false
FEATURE [Sketcher::SketchObject] Sketch146
  FullyConstrained = false
  MapMode = 5
  Placement = pos=(0,0,9.75) rot=(0,0,1;0rad)
  Support = -> [Draft]
  sketch-geometry (1):
    g0: Circle CenterX=0 CenterY=0 CenterZ=0 NormalX=0 NormalY=0 NormalZ=1 AngleXU=0 Radius=5
  constraints (2):
    c: Coincident(g0,g-1)
    c: Radius(g0) = 5
FEATURE [PartDesign::Pocket] Pocket056
  AllowMultiFace = false
  BaseFeature = -> Draft
  Length = 8
  Length2 = 100
  Profile = -> Sketch146
  Refine = true
  Type = 1
FEATURE [Sketcher::SketchObject] Sketch147
  FullyConstrained = false
  MapMode = 5
  Support = -> [XY_Plane164]
  sketch-geometry (1):
    g0: Circle CenterX=0 CenterY=0 CenterZ=0 NormalX=0 NormalY=0 NormalZ=1 AngleXU=0 Radius=2.5
  constraints (2):
    c: Coincident(g0,g-1)
    c: Radius(g0) = 2.5
FEATURE [PartDesign::Pad] Pad035
  AllowMultiFace = false
  Direction = (1,1,1)
  Length = 60
  Length2 = 100
  Profile = -> Sketch147
  Refine = true
  Type = 0
FEATURE [Sketcher::SketchObject] Sketch148
  FullyConstrained = false
  MapMode = 5
  Placement = pos=(0,0,60) rot=(0,0,1;0rad)
  Support = -> [Pad035]
  sketch-geometry (4):
    g0: LineSegment StartX=2 StartY=2 StartZ=0 EndX=6 EndY=2 EndZ=0
    g1: LineSegment StartX=6 StartY=2 StartZ=0 EndX=6 EndY=-2 EndZ=0
    g2: LineSegment StartX=6 StartY=-2 StartZ=0 EndX=2 EndY=-2 EndZ=0
    g3: LineSegment StartX=2 StartY=-2 StartZ=0 EndX=2 EndY=2 EndZ=0
  constraints (11):
    c: Coincident(g0,g1)
    c: Coincident(g1,g2)
    c: Coincident(g2,g3)
    c: Coincident(g3,g0)
    c: Horizontal(g0)
    c: Horizontal(g2)
    c: Vertical(g1)
    c: Symmetric(g2,g0,g-1)
    c: DistanceX(g-1,g0) = 2
    c: Equal(g0,g3)
    c: DistanceX(g0,g0) = 4
FEATURE [PartDesign::Pocket] Pocket057
  AllowMultiFace = false
  BaseFeature = -> Pad035
  Length = 16
  Length2 = 100
  Profile = -> Sketch148
  Refine = true
  Type = 0
FEATURE [PartDesign::Chamfer] Chamfer007
  Angle = 45
  Base = -> Pocket057 [Edge3,Edge5,Edge9]
  BaseFeature = -> Pocket057
  ChamferType = 0
  FlipDirection = false
  Size = 0.3
  Size2 = 1
  SupportTransform = false
FEATURE [PartDesign::Body] Body149  label="Rotor"
  Group = -> [Sketch147,Pad035,Sketch148,Pocket057,Chamfer007]
  Origin = -> Origin170
  Placement = pos=(0,0,2) rot=(0,0,1;0rad)
  Tip = -> Chamfer007
FEATURE [App::Part] Part024  label="Rotor001"
  Group = -> [Body149]
  Origin = -> Origin174
FEATURE [Sketcher::SketchObject] Sketch149
  FullyConstrained = false
  MapMode = 5
  Placement = pos=(0,0,22.75) rot=(0,0,1;0rad)
  Support = -> [Pocket053]
  sketch-geometry (1):
    g0: Circle CenterX=0 CenterY=0 CenterZ=0 NormalX=0 NormalY=0 NormalZ=1 AngleXU=0 Radius=18
  constraints (2):
    c: Coincident(g0,g-1)
    c: Radius(g0) = 18
FEATURE [PartDesign::Pocket] Pocket052
  AllowMultiFace = false
  BaseFeature = -> Pocket053
  Length = 5
  Length2 = 100
  Profile = -> Sketch149
  Refine = true
  Type = 1
FEATURE [PartDesign::Body] Body147
  Group = -> [Sketch139,Pad032,Chamfer005,Sketch142,Pocket053,Sketch149,Pocket052]
  Origin = -> Origin168
  Placement = pos=(0,0,9.6) rot=(0,0,1;0rad)
  Tip = -> Pocket052
FEATURE [App::Part] Part022  label="Body148"
  Group = -> [Body147,Body150]
  Origin = -> Origin172
FEATURE [Sketcher::SketchObject] Sketch150
  ExternalGeometry = -> [Hole]
  FullyConstrained = false
  MapMode = 5
  Placement = pos=(21.15,0,0) rot=(0.57735,0.57735,0.57735;2.0944rad)
  Support = -> [Hole]
  sketch-geometry (4):
    g0: LineSegment StartX=-8.2 StartY=3.6 StartZ=0 EndX=8.2 EndY=3.6 EndZ=0
    g1: LineSegment StartX=8.2 StartY=3.6 StartZ=0 EndX=8.2 EndY=9.6 EndZ=0
    g2: LineSegment StartX=8.2 StartY=9.6 StartZ=0 EndX=-8.2 EndY=9.6 EndZ=0
    g3: LineSegment StartX=-8.2 StartY=9.6 StartZ=0 EndX=-8.2 EndY=3.6 EndZ=0
  constraints (10):
    c: Coincident(g0,g1)
    c: Coincident(g1,g2)
    c: Coincident(g2,g3)
    c: Coincident(g3,g0)
    c: Horizontal(g0)
    c: Vertical(g1)
    c: Vertical(g3)
    c: Coincident(g0,g-3)
    c: PointOnObject(g1,g-5)
    c: Symmetric(g2,g1,g-2)
FEATURE [PartDesign::Pocket] Pocket058
  AllowMultiFace = false
  BaseFeature = -> Hole
  Length = 4
  Length2 = 100
  Profile = -> Sketch150
  Refine = true
  Type = 0
FEATURE [PartDesign::Body] Body146  label="Aluminium rear001"
  Group = -> [Sketch137,Pad030,Sketch138,Pad031,Chamfer004,Fillet174,Sketch141,Hole,Sketch150,Pocket058]
  Origin = -> Origin167
  Tip = -> Pocket058
FEATURE [App::Part] Part021  label="Aluminium rear"
  Group = -> [Body146]
  Origin = -> Origin171
FEATURE [Sketcher::SketchObject] Sketch151
  FullyConstrained = false
  MapMode = 5
  Placement = pos=(0,0,0) rot=(0.57735,0.57735,0.57735;2.0944rad)
  Support = -> [YZ_Plane172]
  sketch-geometry (4):
    g0: LineSegment StartX=-7.5 StartY=0 StartZ=0 EndX=7.5 EndY=0 EndZ=0
    g1: LineSegment StartX=7.5 StartY=0 StartZ=0 EndX=7.5 EndY=5 EndZ=0
    g2: LineSegment StartX=7.5 StartY=5 StartZ=0 EndX=-7.5 EndY=5 EndZ=0
    g3: LineSegment StartX=-7.5 StartY=5 StartZ=0 EndX=-7.5 EndY=0 EndZ=0
  constraints (11):
    c: Coincident(g0,g1)
    c: Coincident(g1,g2)
    c: Coincident(g2,g3)
    c: Coincident(g3,g0)
    c: Horizontal(g0)
    c: Horizontal(g2)
    c: Vertical(g1)
    c: Vertical(g3)
    c: Symmetric(g0,g0,g-1)
    c: DistanceX(g0,g0) = 15
    c: DistanceY(g3,g3) = 5
FEATURE [PartDesign::Pad] Pad036
  AllowMultiFace = false
  Direction = (1,1,1)
  Length = 10
  Length2 = 100
  Placement = pos=(0,0,0) rot=(0.57735,0.57735,0.57735;2.0944rad)
  Profile = -> Sketch151
  Refine = true
  Type = 0
FEATURE [Sketcher::SketchObject] Sketch152
  ExternalGeometry = -> [Pad036]
  FullyConstrained = false
  MapMode = 5
  Placement = pos=(10,-2.2e-15,2.2e-15) rot=(0.57735,0.57735,0.57735;2.0944rad)
  Support = -> [Pad036]
  sketch-geometry (8):
    g0: LineSegment StartX=-6.5 StartY=4 StartZ=0 EndX=6.5 EndY=4 EndZ=0
    g1: LineSegment StartX=6.5 StartY=4 StartZ=0 EndX=6.5 EndY=1 EndZ=0
    g2: LineSegment StartX=6.5 StartY=1 StartZ=0 EndX=-6.5 EndY=1 EndZ=0
    g3: LineSegment StartX=-6.5 StartY=1 StartZ=0 EndX=-6.5 EndY=4 EndZ=0
    g4: LineSegment StartX=-6.5 StartY=1 StartZ=0 EndX=-7.5 EndY=1 EndZ=0
    g5: LineSegment StartX=-6.5 StartY=1 StartZ=0 EndX=-6.5 EndY=0 EndZ=0
    g6: LineSegment StartX=6.5 StartY=4 StartZ=0 EndX=6.5 EndY=5 EndZ=0
    g7: LineSegment StartX=6.5 StartY=4 StartZ=0 EndX=7.5 EndY=4 EndZ=0
  constraints (23):
    c: Coincident(g0,g1)
    c: Coincident(g1,g2)
    c: Coincident(g2,g3)
    c: Coincident(g3,g0)
    c: Horizontal(g2)
    c: Vertical(g1)
    c: Vertical(g3)
    c: Symmetric(g0,g0,g-2)
    c: Coincident(g4,g2)
    c: PointOnObject(g4,g-4)
    c: Horizontal(g4)
    c: PointOnObject(g5,g-1)
    c: Vertical(g5)
    c: Coincident(g6,g0)
    c: Coincident(g7,g0)
    c: Horizontal(g7)
    c: Vertical(g6)
    c: PointOnObject(g6,g-5)
    c: Equal(g7,g6)
    c: Equal(g6,g4)
    c: Equal(g4,g5)
    c: DistanceX(g4,g4) = 1
    c: Coincident(g5,g2)
FEATURE [PartDesign::Pocket] Pocket059
  AllowMultiFace = false
  BaseFeature = -> Pad036
  Length = 6
  Length2 = 100
  Placement = pos=(0,0,0) rot=(0.57735,0.57735,0.57735;2.0944rad)
  Profile = -> Sketch152
  Refine = true
  Type = 0
FEATURE [Sketcher::SketchObject] Sketch016
  ExternalGeometry = -> [Pocket059]
  FullyConstrained = false
  MapMode = 5
  Placement = pos=(10,-2.2e-15,2.2e-15) rot=(0.57735,0.57735,0.57735;2.0944rad)
  Support = -> [Pocket059]
  sketch-geometry (4):
    g0: LineSegment StartX=-4 StartY=5 StartZ=0 EndX=4 EndY=5 EndZ=0
    g1: LineSegment StartX=4 StartY=5 StartZ=0 EndX=4 EndY=4 EndZ=0
    g2: LineSegment StartX=4 StartY=4 StartZ=0 EndX=-4 EndY=4 EndZ=0
    g3: LineSegment StartX=-4 StartY=4 StartZ=0 EndX=-4 EndY=5 EndZ=0
  constraints (11):
    c: Coincident(g0,g1)
    c: Coincident(g1,g2)
    c: Coincident(g2,g3)
    c: Coincident(g3,g0)
    c: Horizontal(g0)
    c: Vertical(g1)
    c: Vertical(g3)
    c: PointOnObject(g0,g-3)
    c: PointOnObject(g1,g-4)
    c: Symmetric(g1,g2,g-2)
    c: DistanceX(g0,g0) = 8
FEATURE [PartDesign::Pocket] Pocket060
  AllowMultiFace = false
  BaseFeature = -> Pocket059
  Length = 4.5
  Length2 = 100
  Placement = pos=(0,0,0) rot=(0.57735,0.57735,0.57735;2.0944rad)
  Profile = -> Sketch016
  Refine = true
  Type = 0
FEATURE [Sketcher::SketchObject] Sketch017
  ExternalGeometry = -> [Pocket060]
  FullyConstrained = false
  MapMode = 5
  Placement = pos=(-1.4e-15,2.2e-15,5) rot=(0,0,-1;1.5708rad)
  Support = -> [Pocket060]
  sketch-geometry (11):
    g0: LineSegment StartX=-6.49 StartY=8.99 StartZ=0 EndX=-5.01 EndY=8.99 EndZ=0
    g1: LineSegment StartX=-5.01 StartY=8.99 StartZ=0 EndX=-5.01 EndY=4.5 EndZ=0
    g2: LineSegment StartX=-5.01 StartY=4.5 StartZ=0 EndX=-6.49 EndY=4.5 EndZ=0
    g3: LineSegment StartX=-6.49 StartY=4.5 StartZ=0 EndX=-6.49 EndY=8.99 EndZ=0
    g4: LineSegment StartX=5.01 StartY=8.99 StartZ=0 EndX=6.49 EndY=8.99 EndZ=0
    g5: LineSegment StartX=6.49 StartY=8.99 StartZ=0 EndX=6.49 EndY=4.5 EndZ=0
    g6: LineSegment StartX=6.49 StartY=4.5 StartZ=0 EndX=5.01 EndY=4.5 EndZ=0
    g7: LineSegment StartX=5.01 StartY=4.5 StartZ=0 EndX=5.01 EndY=8.99 EndZ=0
    g8: LineSegment StartX=-7.5 StartY=8.99 StartZ=0 EndX=-6.49 EndY=8.99 EndZ=0
    g9: LineSegment StartX=-6.49 StartY=10 StartZ=0 EndX=-6.49 EndY=8.99 EndZ=0
    g10: LineSegment StartX=-5.01 StartY=8.99 StartZ=0 EndX=-4 EndY=8.99 EndZ=0
  constraints (32):
    c: Coincident(g0,g1)
    c: Coincident(g1,g2)
    c: Coincident(g2,g3)
    c: Coincident(g3,g0)
    c: Horizontal(g0)
    c: Horizontal(g2)
    c: Vertical(g1)
    c: Vertical(g3)
    c: Coincident(g4,g5)
    c: Coincident(g5,g6)
    c: Coincident(g6,g7)
    c: Coincident(g7,g4)
    c: Horizontal(g4)
    c: Horizontal(g6)
    c: Vertical(g5)
    c: Vertical(g7)
    c: DistanceX(g4,g4) = 1.48
    c: Equal(g0,g4)
    c: Equal(g7,g1)
    c: PointOnObject(g8,g-4)
    c: Coincident(g8,g0)
    c: Horizontal(g8)
    c: PointOnObject(g9,g-5)
    c: Coincident(g9,g0)
    c: Vertical(g9)
    c: Coincident(g10,g0)
    c: PointOnObject(g10,g-3)
    c: Horizontal(g10)
    c: Symmetric(g4,g0,g-2)
    c: Equal(g10,g9)
    c: Equal(g9,g8)
    c: DistanceY(g3,g3) = 4.49
FEATURE [PartDesign::Pocket] Pocket061
  AllowMultiFace = false
  BaseFeature = -> Pocket060
  Length = 2
  Length2 = 100
  Placement = pos=(0,0,0) rot=(0.57735,0.57735,0.57735;2.0944rad)
  Profile = -> Sketch017
  Refine = true
  Type = 0
FEATURE [PartDesign::Body] Body151  label="conector"
  Group = -> [Sketch151,Pad036,Sketch152,Pocket059,Sketch016,Pocket060,Sketch017,Pocket061]
  Origin = -> Origin178
  Tip = -> Pocket061
FEATURE [Sketcher::SketchObject] Sketch018
  FullyConstrained = false
  MapMode = 5
  Placement = pos=(0,0,0) rot=(0.57735,0.57735,0.57735;2.0944rad)
  Support = -> [YZ_Plane173]
  sketch-geometry (4):
    g0: LineSegment StartX=-5.5 StartY=1 StartZ=0 EndX=5.5 EndY=1 EndZ=0
    g1: LineSegment StartX=5.5 StartY=1 StartZ=0 EndX=5.5 EndY=0 EndZ=0
    g2: LineSegment StartX=5.5 StartY=0 StartZ=0 EndX=-5.5 EndY=0 EndZ=0
    g3: LineSegment StartX=-5.5 StartY=0 StartZ=0 EndX=-5.5 EndY=1 EndZ=0
  constraints (11):
    c: Coincident(g0,g1)
    c: Coincident(g1,g2)
    c: Coincident(g2,g3)
    c: Coincident(g3,g0)
    c: Horizontal(g0)
    c: Vertical(g1)
    c: Vertical(g3)
    c: PointOnObject(g1,g-1)
    c: DistanceY(g3,g3) = 1
    c: DistanceX(g2,g2) = 11
    c: Symmetric(g1,g2,g-2)
FEATURE [PartDesign::Pad] Pad037
  AllowMultiFace = false
  Direction = (1,1,1)
  Length = 1
  Length2 = 100
  Placement = pos=(0,0,0) rot=(0.57735,0.57735,0.57735;2.0944rad)
  Profile = -> Sketch018
  Refine = true
  Type = 0
FEATURE [Sketcher::SketchObject] Sketch153
  ExternalGeometry = -> [Pad037]
  FullyConstrained = false
  MapMode = 5
  Placement = pos=(-3e-16,4e-16,1) rot=(0,0,-1;1.5708rad)
  Support = -> [Pad037]
  sketch-geometry (7):
    g0: LineSegment StartX=-5.5 StartY=1 StartZ=0 EndX=-4.5 EndY=1 EndZ=0
    g1: LineSegment StartX=-4.5 StartY=1 StartZ=0 EndX=-4.5 EndY=8 EndZ=0
    g2: LineSegment StartX=-4.5 StartY=8 StartZ=0 EndX=-5.5 EndY=8 EndZ=0
    g3: LineSegment StartX=-5.5 StartY=8 StartZ=0 EndX=-5.5 EndY=1 EndZ=0
    g4: LineSegment StartX=-5.5 StartY=8 StartZ=0 EndX=-5.25 EndY=8.7 EndZ=0
    g5: LineSegment StartX=-5.25 StartY=8.7 StartZ=0 EndX=-4.75 EndY=8.7 EndZ=0
    g6: LineSegment StartX=-4.75 StartY=8.7 StartZ=0 EndX=-4.5 EndY=8 EndZ=0
  constraints (19):
    c: Coincident(g0,g1)
    c: Coincident(g1,g2)
    c: Coincident(g2,g3)
    c: Coincident(g3,g0)
    c: Horizontal(g0)
    c: Horizontal(g2)
    c: Vertical(g1)
    c: Vertical(g3)
    c: Coincident(g0,g-3)
    c: Coincident(g2,g4)
    c: Coincident(g4,g5)
    c: Horizontal(g5)
    c: Coincident(g5,g6)
    c: Coincident(g6,g1)
    c: DistanceY(g1,g5) = 0.7
    c: DistanceX(g5,g5) = 0.5
    c: Equal(g6,g4)
    c: DistanceX(g0,g0) = 1
    c: DistanceY(g3,g3) = 7
FEATURE [PartDesign::Pad] Pad038
  AllowMultiFace = false
  BaseFeature = -> Pad037
  Direction = (1,1,1)
  Length = 1
  Length2 = 100
  Placement = pos=(0,0,0) rot=(0.57735,0.57735,0.57735;2.0944rad)
  Profile = -> Sketch153
  Refine = true
  Reversed = true
  Type = 0
FEATURE [PartDesign::LinearPattern] LinearPattern
  BaseFeature = -> Pad038
  Direction = -> Pad038 [Edge10]
  Length = 10
  Occurrences = 3
  Originals = -> [Pad038]
  Placement = pos=(0,0,0) rot=(0.57735,0.57735,0.57735;2.0944rad)
  Refine = true
  Reversed = true
FEATURE [PartDesign::Body] Body152  label="pin"
  Group = -> [Sketch018,Pad037,Sketch153,Pad038,LinearPattern]
  Origin = -> Origin179
  Placement = pos=(0,0,2) rot=(0,0,1;0rad)
  Tip = -> LinearPattern
FEATURE [App::Part] Part026  label="Conector"
  Group = -> [Body151,Body152]
  Origin = -> Origin177
  Placement = pos=(17,0,4) rot=(0,0,1;0rad)
FEATURE [Sketcher::SketchObject] Sketch020
  FullyConstrained = false
  MapMode = 5
  Placement = pos=(0,0,0) rot=(1,0,0;3.14159rad)
  Support = -> [Pocket056]
  sketch-geometry (1):
    g0: Circle CenterX=0 CenterY=0 CenterZ=0 NormalX=0 NormalY=0 NormalZ=1 AngleXU=0 Radius=15.35
  constraints (2):
    c: Coincident(g0,g-1)
    c: Radius(g0) = 15.35
FEATURE [PartDesign::Pocket] Pocket062
  AllowMultiFace = false
  BaseFeature = -> Pocket056
  Length = 5
  Length2 = 100
  Profile = -> Sketch020
  Refine = true
  Type = 0
FEATURE [PartDesign::Body] Body148  label="Aluminum front001"
  Group = -> [Sketch140,Pad033,Chamfer006,Fillet175,Sketch143,Pocket054,Sketch144,Pocket055,Sketch145,Pad034,Draft,Sketch146,Pocket056,Sketch020,Pocket062]
  Origin = -> Origin169
  Placement = pos=(0,0,32.35) rot=(0,0,1;0rad)
  Tip = -> Pocket062
FEATURE [App::Part] Part023  label="Aluminum front"
  Group = -> [Body148]
  Origin = -> Origin173
FEATURE [App::Part] Part020  label="Nema 017-001"
  Group = -> [Part021,Part022,Part023,Part024,Part025,Part026]
  Origin = -> Origin166
  Placement = pos=(440,120,104.3) rot=(0,1,0;-1.5708rad)
FEATURE [PartDesign::Body] Body157  label="Stator001"
  Origin = -> Origin190
FEATURE [Part::FeaturePython] Screw004  label="M2.5x25-Screw008"  # Fasteners workbench fastener (typed FeaturePython)
  Placement = pos=(15.5,15.5,4) rot=(0,1,0;3.14159rad)
  diameter = 3
  invert = true
  length = 10
  matchOuter = true
  offset = 1
  thread = true
  type = 16
FEATURE [Part::FeaturePython] Screw005  label="M2.5x25-Screw009"  # Fasteners workbench fastener (typed FeaturePython)
  Placement = pos=(-15.5,-15.5,4) rot=(0,1,0;3.14159rad)
  diameter = 3
  invert = true
  length = 10
  matchOuter = true
  offset = 1
  thread = true
  type = 16
FEATURE [Part::FeaturePython] Screw006  label="M2.5x25-Screw010"  # Fasteners workbench fastener (typed FeaturePython)
  Placement = pos=(15.5,-15.5,4) rot=(0,1,0;3.14159rad)
  diameter = 3
  invert = true
  length = 10
  matchOuter = true
  offset = 1
  thread = true
  type = 16
FEATURE [Part::FeaturePython] Screw007  label="M2.5x25-Screw011"  # Fasteners workbench fastener (typed FeaturePython)
  Placement = pos=(-15.5,15.5,4) rot=(0,1,0;3.14159rad)
  diameter = 3
  invert = true
  length = 10
  matchOuter = true
  offset = 1
  thread = true
  type = 16
FEATURE [App::Part] Part032  label="Screw001"
  Group = -> [Screw004,Screw005,Screw006,Screw007]
  Origin = -> Origin189
FEATURE [Sketcher::SketchObject] Sketch156
  FullyConstrained = false
  MapMode = 5
  Placement = pos=(0,0,0) rot=(0.57735,0.57735,0.57735;2.0944rad)
  Support = -> [YZ_Plane187]
  sketch-geometry (4):
    g0: LineSegment StartX=-5.5 StartY=1 StartZ=0 EndX=5.5 EndY=1 EndZ=0
    g1: LineSegment StartX=5.5 StartY=1 StartZ=0 EndX=5.5 EndY=0 EndZ=0
    g2: LineSegment StartX=5.5 StartY=0 StartZ=0 EndX=-5.5 EndY=0 EndZ=0
    g3: LineSegment StartX=-5.5 StartY=0 StartZ=0 EndX=-5.5 EndY=1 EndZ=0
  constraints (11):
    c: Coincident(g0,g1)
    c: Coincident(g1,g2)
    c: Coincident(g2,g3)
    c: Coincident(g3,g0)
    c: Horizontal(g0)
    c: Vertical(g1)
    c: Vertical(g3)
    c: PointOnObject(g1,g-1)
    c: DistanceY(g3,g3) = 1
    c: DistanceX(g2,g2) = 11
    c: Symmetric(g1,g2,g-2)
FEATURE [PartDesign::Pad] Pad046
  AllowMultiFace = false
  Direction = (1,1,1)
  Length = 1
  Length2 = 100
  Placement = pos=(0,0,0) rot=(0.57735,0.57735,0.57735;2.0944rad)
  Profile = -> Sketch156
  Refine = true
  Type = 0
FEATURE [Sketcher::SketchObject] Sketch158
  FullyConstrained = false
  MapMode = 5
  Support = -> [XY_Plane175]
  sketch-geometry (4):
    g0: LineSegment StartX=-21.15 StartY=21.15 StartZ=0 EndX=21.15 EndY=21.15 EndZ=0
    g1: LineSegment StartX=21.15 StartY=21.15 StartZ=0 EndX=21.15 EndY=-21.15 EndZ=0
    g2: LineSegment StartX=21.15 StartY=-21.15 StartZ=0 EndX=-21.15 EndY=-21.15 EndZ=0
    g3: LineSegment StartX=-21.15 StartY=-21.15 StartZ=0 EndX=-21.15 EndY=21.15 EndZ=0
  constraints (11):
    c: Coincident(g0,g1)
    c: Coincident(g1,g2)
    c: Coincident(g2,g3)
    c: Coincident(g3,g0)
    c: Horizontal(g0)
    c: Horizontal(g2)
    c: Vertical(g1)
    c: Vertical(g3)
    c: Symmetric(g0,g1,g-1)
    c: DistanceX(g0,g0) = 42.3
    c: Equal(g0,g3)
FEATURE [PartDesign::Pad] Pad039
  AllowMultiFace = false
  Direction = (1,1,1)
  Length = 9.6
  Length2 = 100
  Profile = -> Sketch158
  Refine = true
  Type = 0
FEATURE [Sketcher::SketchObject] Sketch159
  ExternalGeometry = -> [Pad039]
  FullyConstrained = false
  MapMode = 5
  Support = -> [XY_Plane175]
  sketch-geometry (4):
    g0: LineSegment StartX=21.15 StartY=8.2 StartZ=0 EndX=25.45 EndY=8.2 EndZ=0
    g1: LineSegment StartX=25.45 StartY=8.2 StartZ=0 EndX=25.45 EndY=-8.2 EndZ=0
    g2: LineSegment StartX=25.45 StartY=-8.2 StartZ=0 EndX=21.15 EndY=-8.2 EndZ=0
    g3: LineSegment StartX=21.15 StartY=-8.2 StartZ=0 EndX=21.15 EndY=8.2 EndZ=0
  constraints (11):
    c: Coincident(g0,g1)
    c: Coincident(g1,g2)
    c: Coincident(g2,g3)
    c: Coincident(g3,g0)
    c: Horizontal(g0)
    c: Horizontal(g2)
    c: Vertical(g3)
    c: PointOnObject(g0,g-3)
    c: Symmetric(g1,g0,g-1)
    c: DistanceX(g0,g0) = 4.3
    c: DistanceY(g1,g1) = 16.4
FEATURE [PartDesign::Pad] Pad040
  AllowMultiFace = false
  BaseFeature = -> Pad039
  Direction = (1,1,1)
  Length = 3.6
  Length2 = 100
  Profile = -> Sketch159
  Refine = true
  Type = 0
FEATURE [PartDesign::Chamfer] Chamfer008
  Angle = 45
  Base = -> Pad040 [Edge13,Edge5,Edge1,Edge2]
  BaseFeature = -> Pad040
  ChamferType = 0
  FlipDirection = false
  Size = 5
  Size2 = 1
  SupportTransform = false
FEATURE [PartDesign::Fillet] Fillet176
  Base = -> Chamfer008 [Edge33,Edge28,Edge18,Edge3,Edge2,Edge16,Edge30,Edge25]
  BaseFeature = -> Chamfer008
  Radius = 2
  SupportTransform = false
FEATURE [Sketcher::SketchObject] Sketch160
  FullyConstrained = false
  MapMode = 5
  Support = -> [XY_Plane176]
  sketch-geometry (4):
    g0: LineSegment StartX=-21 StartY=21 StartZ=0 EndX=21 EndY=21 EndZ=0
    g1: LineSegment StartX=21 StartY=21 StartZ=0 EndX=21 EndY=-21 EndZ=0
    g2: LineSegment StartX=21 StartY=-21 StartZ=0 EndX=-21 EndY=-21 EndZ=0
    g3: LineSegment StartX=-21 StartY=-21 StartZ=0 EndX=-21 EndY=21 EndZ=0
  constraints (11):
    c: Coincident(g0,g1)
    c: Coincident(g1,g2)
    c: Coincident(g2,g3)
    c: Coincident(g3,g0)
    c: Horizontal(g0)
    c: Horizontal(g2)
    c: Vertical(g1)
    c: Vertical(g3)
    c: DistanceX(g0,g0) = 42
    c: Symmetric(g0,g1,g-1)
    c: Equal(g0,g3)
FEATURE [PartDesign::Pad] Pad041
  AllowMultiFace = false
  Direction = (1,1,1)
  Length = 22.75
  Length2 = 100
  Profile = -> Sketch160
  Refine = true
  Type = 0
FEATURE [PartDesign::Chamfer] Chamfer009
  Angle = 45
  Base = -> Pad041 [Edge8,Edge1,Edge5,Edge2]
  BaseFeature = -> Pad041
  ChamferType = 0
  FlipDirection = false
  Size = 7.5
  Size2 = 1
  SupportTransform = false
FEATURE [Sketcher::SketchObject] Sketch161
  FullyConstrained = false
  MapMode = 5
  Support = -> [XY_Plane177]
  sketch-geometry (4):
    g0: LineSegment StartX=-21.15 StartY=21.15 StartZ=0 EndX=21.15 EndY=21.15 EndZ=0
    g1: LineSegment StartX=21.15 StartY=21.15 StartZ=0 EndX=21.15 EndY=-21.15 EndZ=0
    g2: LineSegment StartX=21.15 StartY=-21.15 StartZ=0 EndX=-21.15 EndY=-21.15 EndZ=0
    g3: LineSegment StartX=-21.15 StartY=-21.15 StartZ=0 EndX=-21.15 EndY=21.15 EndZ=0
  constraints (11):
    c: Coincident(g0,g1)
    c: Coincident(g1,g2)
    c: Coincident(g2,g3)
    c: Coincident(g3,g0)
    c: Horizontal(g0)
    c: Horizontal(g2)
    c: Vertical(g1)
    c: Vertical(g3)
    c: Symmetric(g0,g1,g-1)
    c: DistanceX(g0,g0) = 42.3
    c: Equal(g0,g3)
FEATURE [PartDesign::Pad] Pad042
  AllowMultiFace = false
  Direction = (1,1,1)
  Length = 7.75
  Length2 = 100
  Profile = -> Sketch161
  Refine = true
  Type = 0
FEATURE [PartDesign::Chamfer] Chamfer010
  Angle = 45
  Base = -> Pad042 [Edge8,Edge5,Edge2,Edge1]
  BaseFeature = -> Pad042
  ChamferType = 0
  FlipDirection = false
  Size = 5
  Size2 = 1
  SupportTransform = false
FEATURE [PartDesign::Fillet] Fillet177
  Base = -> Chamfer010 [Edge22,Edge24,Edge23,Edge21,Edge12,Edge2,Edge3,Edge14]
  BaseFeature = -> Chamfer010
  Radius = 2
  SupportTransform = false
FEATURE [Sketcher::SketchObject] Sketch162
  FullyConstrained = false
  MapMode = 5
  Placement = pos=(0,0,0) rot=(1,0,0;3.14159rad)
  Support = -> [Fillet176]
  sketch-geometry (8):
    g0: LineSegment StartX=-15.5 StartY=15.5 StartZ=0 EndX=15.5 EndY=15.5 EndZ=0
    g1: LineSegment StartX=15.5 StartY=15.5 StartZ=0 EndX=15.5 EndY=-15.5 EndZ=0
    g2: LineSegment StartX=15.5 StartY=-15.5 StartZ=0 EndX=-15.5 EndY=-15.5 EndZ=0
    g3: LineSegment StartX=-15.5 StartY=-15.5 StartZ=0 EndX=-15.5 EndY=15.5 EndZ=0
    g4: Circle CenterX=-15.5 CenterY=15.5 CenterZ=0 NormalX=0 NormalY=0 NormalZ=1 AngleXU=0 Radius=1.225
    g5: Circle CenterX=15.5 CenterY=15.5 CenterZ=0 NormalX=0 NormalY=0 NormalZ=1 AngleXU=0 Radius=1.225
    g6: Circle CenterX=15.5 CenterY=-15.5 CenterZ=0 NormalX=0 NormalY=0 NormalZ=1 AngleXU=0 Radius=1.225
    g7: Circle CenterX=-15.5 CenterY=-15.5 CenterZ=0 NormalX=0 NormalY=0 NormalZ=1 AngleXU=0 Radius=1.225
  constraints (19):
    c: Coincident(g0,g1)
    c: Coincident(g1,g2)
    c: Coincident(g2,g3)
    c: Coincident(g3,g0)
    c: Horizontal(g0)
    c: Horizontal(g2)
    c: Vertical(g1)
    c: Vertical(g3)
    c: Symmetric(g0,g1,g-1)
    c: DistanceX(g0,g0) = 31
    c: Equal(g3,g0)
    c: Coincident(g4,g0)
    c: Coincident(g5,g0)
    c: Coincident(g6,g1)
    c: Coincident(g7,g2)
    c: Equal(g6,g5)
    c: Equal(g5,g4)
    c: Equal(g4,g7)
    c: Radius(g4) = 1.225
FEATURE [PartDesign::Hole] Hole001
  AllowMultiFace = false
  BaseFeature = -> Fillet176
  Depth = 25
  DepthType = 0
  Diameter = 3
  DrillForDepth = false
  DrillPoint = 1
  DrillPointAngle = 118
  HoleCutCountersinkAngle = 90
  HoleCutCustomValues = false
  HoleCutDepth = 5
  HoleCutDiameter = 5
  HoleCutType = 1
  ModelActualThread = false
  Profile = -> Sketch162
  Refine = true
  Tapered = false
  TaperedAngle = 90
  ThreadAngle = 0
  ThreadClass = 0
  ThreadCutOffInner = 0
  ThreadCutOffOuter = 0
  ThreadDirection = 0
  ThreadFit = 0
  ThreadPitch = 0
  ThreadSize = 0
  ThreadType = 0
  Threaded = false
FEATURE [Sketcher::SketchObject] Sketch163
  FullyConstrained = false
  MapMode = 5
  Placement = pos=(0,0,0) rot=(1,0,0;3.14159rad)
  Support = -> [Chamfer009]
  sketch-geometry (8):
    g0: LineSegment StartX=-15.5 StartY=15.5 StartZ=0 EndX=15.5 EndY=15.5 EndZ=0
    g1: LineSegment StartX=15.5 StartY=15.5 StartZ=0 EndX=15.5 EndY=-15.5 EndZ=0
    g2: LineSegment StartX=15.5 StartY=-15.5 StartZ=0 EndX=-15.5 EndY=-15.5 EndZ=0
    g3: LineSegment StartX=-15.5 StartY=-15.5 StartZ=0 EndX=-15.5 EndY=15.5 EndZ=0
    g4: Circle CenterX=-15.5 CenterY=15.5 CenterZ=0 NormalX=0 NormalY=0 NormalZ=1 AngleXU=0 Radius=1.22
    g5: Circle CenterX=15.5 CenterY=15.5 CenterZ=0 NormalX=0 NormalY=0 NormalZ=1 AngleXU=0 Radius=1.22
    g6: Circle CenterX=15.5 CenterY=-15.5 CenterZ=0 NormalX=0 NormalY=0 NormalZ=1 AngleXU=0 Radius=1.22
    g7: Circle CenterX=-15.5 CenterY=-15.5 CenterZ=0 NormalX=0 NormalY=0 NormalZ=1 AngleXU=0 Radius=1.22
  constraints (19):
    c: Coincident(g0,g1)
    c: Coincident(g1,g2)
    c: Coincident(g2,g3)
    c: Coincident(g3,g0)
    c: Horizontal(g0)
    c: Horizontal(g2)
    c: Vertical(g1)
    c: Vertical(g3)
    c: Equal(g0,g3)
    c: Symmetric(g0,g1,g-1)
    c: DistanceX(g0,g0) = 31
    c: Coincident(g4,g0)
    c: Coincident(g5,g0)
    c: Coincident(g6,g1)
    c: Coincident(g7,g2)
    c: Equal(g6,g5)
    c: Equal(g5,g4)
    c: Equal(g4,g7)
    c: Radius(g4) = 1.22
FEATURE [PartDesign::Pocket] Pocket064
  AllowMultiFace = false
  BaseFeature = -> Chamfer009
  Length = 5
  Length2 = 100
  Profile = -> Sketch163
  Refine = true
  Type = 1
FEATURE [Sketcher::SketchObject] Sketch164
  FullyConstrained = false
  MapMode = 5
  Placement = pos=(0,0,7.75) rot=(0,0,1;0rad)
  Support = -> [Fillet177]
  sketch-geometry (8):
    g0: LineSegment StartX=-15.5 StartY=15.5 StartZ=0 EndX=15.5 EndY=15.5 EndZ=0
    g1: LineSegment StartX=15.5 StartY=15.5 StartZ=0 EndX=15.5 EndY=-15.5 EndZ=0
    g2: LineSegment StartX=15.5 StartY=-15.5 StartZ=0 EndX=-15.5 EndY=-15.5 EndZ=0
    g3: LineSegment StartX=-15.5 StartY=-15.5 StartZ=0 EndX=-15.5 EndY=15.5 EndZ=0
    g4: Circle CenterX=-15.5 CenterY=15.5 CenterZ=0 NormalX=0 NormalY=0 NormalZ=1 AngleXU=0 Radius=1.225
    g5: Circle CenterX=15.5 CenterY=15.5 CenterZ=0 NormalX=0 NormalY=0 NormalZ=1 AngleXU=0 Radius=1.225
    g6: Circle CenterX=15.5 CenterY=-15.5 CenterZ=0 NormalX=0 NormalY=0 NormalZ=1 AngleXU=0 Radius=1.225
    g7: Circle CenterX=-15.5 CenterY=-15.5 CenterZ=0 NormalX=0 NormalY=0 NormalZ=1 AngleXU=0 Radius=1.225
  constraints (19):
    c: Coincident(g0,g1)
    c: Coincident(g1,g2)
    c: Coincident(g2,g3)
    c: Coincident(g3,g0)
    c: Horizontal(g0)
    c: Horizontal(g2)
    c: Vertical(g1)
    c: Vertical(g3)
    c: Equal(g0,g3)
    c: Symmetric(g0,g1,g-1)
    c: DistanceX(g0,g0) = 31
    c: Coincident(g4,g0)
    c: Coincident(g7,g2)
    c: Coincident(g0,g5)
    c: Coincident(g1,g6)
    c: Equal(g7,g4)
    c: Equal(g4,g5)
    c: Equal(g5,g6)
    c: Radius(g4) = 1.225
FEATURE [PartDesign::Pocket] Pocket065
  AllowMultiFace = false
  BaseFeature = -> Fillet177
  Length = 5
  Length2 = 100
  Profile = -> Sketch164
  Refine = true
  Type = 1
FEATURE [Sketcher::SketchObject] Sketch165
  FullyConstrained = false
  MapMode = 5
  Placement = pos=(0,0,7.75) rot=(0,0,1;0rad)
  Support = -> [Pocket065]
  sketch-geometry (1):
    g0: Circle CenterX=0 CenterY=0 CenterZ=0 NormalX=0 NormalY=0 NormalZ=1 AngleXU=0 Radius=14
  constraints (2):
    c: Coincident(g0,g-1)
    c: Radius(g0) = 14
FEATURE [PartDesign::Pocket] Pocket066
  AllowMultiFace = false
  BaseFeature = -> Pocket065
  Length = 1
  Length2 = 100
  Profile = -> Sketch165
  Refine = true
  Type = 0
FEATURE [Sketcher::SketchObject] Sketch166
  FullyConstrained = false
  MapMode = 5
  Placement = pos=(0,0,6.75) rot=(0,0,1;0rad)
  Support = -> [Pocket066]
  sketch-geometry (1):
    g0: Circle CenterX=0 CenterY=0 CenterZ=0 NormalX=0 NormalY=0 NormalZ=1 AngleXU=0 Radius=11
  constraints (2):
    c: Coincident(g0,g-1)
    c: Radius(g0) = 11
FEATURE [PartDesign::Pad] Pad043
  AllowMultiFace = false
  BaseFeature = -> Pocket066
  Direction = (1,1,1)
  Length = 3
  Length2 = 100
  Profile = -> Sketch166
  Refine = true
  Type = 0
FEATURE [PartDesign::Draft] Draft001
  Angle = 10
  Base = -> Pad043 [Face25]
  BaseFeature = -> Pad043
  NeutralPlane = -> Pad043 [Face24]
  SupportTransform = false
FEATURE [Sketcher::SketchObject] Sketch167
  FullyConstrained = false
  MapMode = 5
  Placement = pos=(0,0,9.75) rot=(0,0,1;0rad)
  Support = -> [Draft001]
  sketch-geometry (1):
    g0: Circle CenterX=0 CenterY=0 CenterZ=0 NormalX=0 NormalY=0 NormalZ=1 AngleXU=0 Radius=5
  constraints (2):
    c: Coincident(g0,g-1)
    c: Radius(g0) = 5
FEATURE [PartDesign::Pocket] Pocket067
  AllowMultiFace = false
  BaseFeature = -> Draft001
  Length = 8
  Length2 = 100
  Profile = -> Sketch167
  Refine = true
  Type = 1
FEATURE [Sketcher::SketchObject] Sketch157
  FullyConstrained = false
  MapMode = 5
  Placement = pos=(0,0,0) rot=(1,0,0;3.14159rad)
  Support = -> [Pocket067]
  sketch-geometry (1):
    g0: Circle CenterX=0 CenterY=0 CenterZ=0 NormalX=0 NormalY=0 NormalZ=1 AngleXU=0 Radius=15.35
  constraints (2):
    c: Coincident(g0,g-1)
    c: Radius(g0) = 15.35
FEATURE [PartDesign::Pocket] Pocket073
  AllowMultiFace = false
  BaseFeature = -> Pocket067
  Length = 5
  Length2 = 100
  Profile = -> Sketch157
  Refine = true
  Type = 0
FEATURE [PartDesign::Body] Body155  label="Aluminum front002"
  Group = -> [Sketch161,Pad042,Chamfer010,Fillet177,Sketch164,Pocket065,Sketch165,Pocket066,Sketch166,Pad043,Draft001,Sketch167,Pocket067,Sketch157,Pocket073]
  Origin = -> Origin183
  Placement = pos=(0,0,32.35) rot=(0,0,1;0rad)
  Tip = -> Pocket073
FEATURE [App::Part] Part030  label="Aluminum front003"
  Group = -> [Body155]
  Origin = -> Origin187
FEATURE [Sketcher::SketchObject] Sketch168
  FullyConstrained = false
  MapMode = 5
  Support = -> [XY_Plane178]
  sketch-geometry (1):
    g0: Circle CenterX=0 CenterY=0 CenterZ=0 NormalX=0 NormalY=0 NormalZ=1 AngleXU=0 Radius=2.5
  constraints (2):
    c: Coincident(g0,g-1)
    c: Radius(g0) = 2.5
FEATURE [PartDesign::Pad] Pad044
  AllowMultiFace = false
  Direction = (1,1,1)
  Length = 60
  Length2 = 100
  Profile = -> Sketch168
  Refine = true
  Type = 0
FEATURE [Sketcher::SketchObject] Sketch169
  FullyConstrained = false
  MapMode = 5
  Placement = pos=(0,0,60) rot=(0,0,1;0rad)
  Support = -> [Pad044]
  sketch-geometry (4):
    g0: LineSegment StartX=2 StartY=2 StartZ=0 EndX=6 EndY=2 EndZ=0
    g1: LineSegment StartX=6 StartY=2 StartZ=0 EndX=6 EndY=-2 EndZ=0
    g2: LineSegment StartX=6 StartY=-2 StartZ=0 EndX=2 EndY=-2 EndZ=0
    g3: LineSegment StartX=2 StartY=-2 StartZ=0 EndX=2 EndY=2 EndZ=0
  constraints (11):
    c: Coincident(g0,g1)
    c: Coincident(g1,g2)
    c: Coincident(g2,g3)
    c: Coincident(g3,g0)
    c: Horizontal(g0)
    c: Horizontal(g2)
    c: Vertical(g1)
    c: Symmetric(g2,g0,g-1)
    c: DistanceX(g-1,g0) = 2
    c: Equal(g0,g3)
    c: DistanceX(g0,g0) = 4
FEATURE [PartDesign::Pocket] Pocket068
  AllowMultiFace = false
  BaseFeature = -> Pad044
  Length = 16
  Length2 = 100
  Profile = -> Sketch169
  Refine = true
  Type = 0
FEATURE [PartDesign::Chamfer] Chamfer011
  Angle = 45
  Base = -> Pocket068 [Edge3,Edge5,Edge9]
  BaseFeature = -> Pocket068
  ChamferType = 0
  FlipDirection = false
  Size = 0.3
  Size2 = 1
  SupportTransform = false
FEATURE [PartDesign::Body] Body156  label="Rotor002"
  Group = -> [Sketch168,Pad044,Sketch169,Pocket068,Chamfer011]
  Origin = -> Origin184
  Placement = pos=(0,0,2) rot=(0,0,1;0rad)
  Tip = -> Chamfer011
FEATURE [App::Part] Part031  label="Rotor003"
  Group = -> [Body156]
  Origin = -> Origin188
FEATURE [Sketcher::SketchObject] Sketch170
  FullyConstrained = false
  MapMode = 5
  Placement = pos=(0,0,22.75) rot=(0,0,1;0rad)
  Support = -> [Pocket064]
  sketch-geometry (1):
    g0: Circle CenterX=0 CenterY=0 CenterZ=0 NormalX=0 NormalY=0 NormalZ=1 AngleXU=0 Radius=18
  constraints (2):
    c: Coincident(g0,g-1)
    c: Radius(g0) = 18
FEATURE [PartDesign::Pocket] Pocket063
  AllowMultiFace = false
  BaseFeature = -> Pocket064
  Length = 5
  Length2 = 100
  Profile = -> Sketch170
  Refine = true
  Type = 1
FEATURE [PartDesign::Body] Body154
  Group = -> [Sketch160,Pad041,Chamfer009,Sketch163,Pocket064,Sketch170,Pocket063]
  Origin = -> Origin182
  Placement = pos=(0,0,9.6) rot=(0,0,1;0rad)
  Tip = -> Pocket063
FEATURE [App::Part] Part029  label="Body155"
  Group = -> [Body154,Body157]
  Origin = -> Origin186
FEATURE [Sketcher::SketchObject] Sketch171
  ExternalGeometry = -> [Hole001]
  FullyConstrained = false
  MapMode = 5
  Placement = pos=(21.15,0,0) rot=(0.57735,0.57735,0.57735;2.0944rad)
  Support = -> [Hole001]
  sketch-geometry (4):
    g0: LineSegment StartX=-8.2 StartY=3.6 StartZ=0 EndX=8.2 EndY=3.6 EndZ=0
    g1: LineSegment StartX=8.2 StartY=3.6 StartZ=0 EndX=8.2 EndY=9.6 EndZ=0
    g2: LineSegment StartX=8.2 StartY=9.6 StartZ=0 EndX=-8.2 EndY=9.6 EndZ=0
    g3: LineSegment StartX=-8.2 StartY=9.6 StartZ=0 EndX=-8.2 EndY=3.6 EndZ=0
  constraints (10):
    c: Coincident(g0,g1)
    c: Coincident(g1,g2)
    c: Coincident(g2,g3)
    c: Coincident(g3,g0)
    c: Horizontal(g0)
    c: Vertical(g1)
    c: Vertical(g3)
    c: Coincident(g0,g-3)
    c: PointOnObject(g1,g-5)
    c: Symmetric(g2,g1,g-2)
FEATURE [PartDesign::Pocket] Pocket069
  AllowMultiFace = false
  BaseFeature = -> Hole001
  Length = 4
  Length2 = 100
  Profile = -> Sketch171
  Refine = true
  Type = 0
FEATURE [PartDesign::Body] Body153  label="Aluminium rear002"
  Group = -> [Sketch158,Pad039,Sketch159,Pad040,Chamfer008,Fillet176,Sketch162,Hole001,Sketch171,Pocket069]
  Origin = -> Origin181
  Tip = -> Pocket069
FEATURE [App::Part] Part028  label="Aluminium rear003"
  Group = -> [Body153]
  Origin = -> Origin185
FEATURE [Sketcher::SketchObject] Sketch172
  FullyConstrained = false
  MapMode = 5
  Placement = pos=(0,0,0) rot=(0.57735,0.57735,0.57735;2.0944rad)
  Support = -> [YZ_Plane186]
  sketch-geometry (4):
    g0: LineSegment StartX=-7.5 StartY=0 StartZ=0 EndX=7.5 EndY=0 EndZ=0
    g1: LineSegment StartX=7.5 StartY=0 StartZ=0 EndX=7.5 EndY=5 EndZ=0
    g2: LineSegment StartX=7.5 StartY=5 StartZ=0 EndX=-7.5 EndY=5 EndZ=0
    g3: LineSegment StartX=-7.5 StartY=5 StartZ=0 EndX=-7.5 EndY=0 EndZ=0
  constraints (11):
    c: Coincident(g0,g1)
    c: Coincident(g1,g2)
    c: Coincident(g2,g3)
    c: Coincident(g3,g0)
    c: Horizontal(g0)
    c: Horizontal(g2)
    c: Vertical(g1)
    c: Vertical(g3)
    c: Symmetric(g0,g0,g-1)
    c: DistanceX(g0,g0) = 15
    c: DistanceY(g3,g3) = 5
FEATURE [PartDesign::Pad] Pad045
  AllowMultiFace = false
  Direction = (1,1,1)
  Length = 10
  Length2 = 100
  Placement = pos=(0,0,0) rot=(0.57735,0.57735,0.57735;2.0944rad)
  Profile = -> Sketch172
  Refine = true
  Type = 0
FEATURE [Sketcher::SketchObject] Sketch173
  ExternalGeometry = -> [Pad045]
  FullyConstrained = false
  MapMode = 5
  Placement = pos=(10,-2.2e-15,2.2e-15) rot=(0.57735,0.57735,0.57735;2.0944rad)
  Support = -> [Pad045]
  sketch-geometry (8):
    g0: LineSegment StartX=-6.5 StartY=4 StartZ=0 EndX=6.5 EndY=4 EndZ=0
    g1: LineSegment StartX=6.5 StartY=4 StartZ=0 EndX=6.5 EndY=1 EndZ=0
    g2: LineSegment StartX=6.5 StartY=1 StartZ=0 EndX=-6.5 EndY=1 EndZ=0
    g3: LineSegment StartX=-6.5 StartY=1 StartZ=0 EndX=-6.5 EndY=4 EndZ=0
    g4: LineSegment StartX=-6.5 StartY=1 StartZ=0 EndX=-7.5 EndY=1 EndZ=0
    g5: LineSegment StartX=-6.5 StartY=1 StartZ=0 EndX=-6.5 EndY=0 EndZ=0
    g6: LineSegment StartX=6.5 StartY=4 StartZ=0 EndX=6.5 EndY=5 EndZ=0
    g7: LineSegment StartX=6.5 StartY=4 StartZ=0 EndX=7.5 EndY=4 EndZ=0
  constraints (23):
    c: Coincident(g0,g1)
    c: Coincident(g1,g2)
    c: Coincident(g2,g3)
    c: Coincident(g3,g0)
    c: Horizontal(g2)
    c: Vertical(g1)
    c: Vertical(g3)
    c: Symmetric(g0,g0,g-2)
    c: Coincident(g4,g2)
    c: PointOnObject(g4,g-4)
    c: Horizontal(g4)
    c: PointOnObject(g5,g-1)
    c: Vertical(g5)
    c: Coincident(g6,g0)
    c: Coincident(g7,g0)
    c: Horizontal(g7)
    c: Vertical(g6)
    c: PointOnObject(g6,g-5)
    c: Equal(g7,g6)
    c: Equal(g6,g4)
    c: Equal(g4,g5)
    c: DistanceX(g4,g4) = 1
    c: Coincident(g5,g2)
FEATURE [PartDesign::Pocket] Pocket070
  AllowMultiFace = false
  BaseFeature = -> Pad045
  Length = 6
  Length2 = 100
  Placement = pos=(0,0,0) rot=(0.57735,0.57735,0.57735;2.0944rad)
  Profile = -> Sketch173
  Refine = true
  Type = 0
FEATURE [Sketcher::SketchObject] Sketch154
  ExternalGeometry = -> [Pocket070]
  FullyConstrained = false
  MapMode = 5
  Placement = pos=(10,-2.2e-15,2.2e-15) rot=(0.57735,0.57735,0.57735;2.0944rad)
  Support = -> [Pocket070]
  sketch-geometry (4):
    g0: LineSegment StartX=-4 StartY=5 StartZ=0 EndX=4 EndY=5 EndZ=0
    g1: LineSegment StartX=4 StartY=5 StartZ=0 EndX=4 EndY=4 EndZ=0
    g2: LineSegment StartX=4 StartY=4 StartZ=0 EndX=-4 EndY=4 EndZ=0
    g3: LineSegment StartX=-4 StartY=4 StartZ=0 EndX=-4 EndY=5 EndZ=0
  constraints (11):
    c: Coincident(g0,g1)
    c: Coincident(g1,g2)
    c: Coincident(g2,g3)
    c: Coincident(g3,g0)
    c: Horizontal(g0)
    c: Vertical(g1)
    c: Vertical(g3)
    c: PointOnObject(g0,g-3)
    c: PointOnObject(g1,g-4)
    c: Symmetric(g1,g2,g-2)
    c: DistanceX(g0,g0) = 8
FEATURE [PartDesign::Pocket] Pocket071
  AllowMultiFace = false
  BaseFeature = -> Pocket070
  Length = 4.5
  Length2 = 100
  Placement = pos=(0,0,0) rot=(0.57735,0.57735,0.57735;2.0944rad)
  Profile = -> Sketch154
  Refine = true
  Type = 0
FEATURE [Sketcher::SketchObject] Sketch155
  ExternalGeometry = -> [Pocket071]
  FullyConstrained = false
  MapMode = 5
  Placement = pos=(-1.4e-15,2.2e-15,5) rot=(0,0,-1;1.5708rad)
  Support = -> [Pocket071]
  sketch-geometry (11):
    g0: LineSegment StartX=-6.49 StartY=8.99 StartZ=0 EndX=-5.01 EndY=8.99 EndZ=0
    g1: LineSegment StartX=-5.01 StartY=8.99 StartZ=0 EndX=-5.01 EndY=4.5 EndZ=0
    g2: LineSegment StartX=-5.01 StartY=4.5 StartZ=0 EndX=-6.49 EndY=4.5 EndZ=0
    g3: LineSegment StartX=-6.49 StartY=4.5 StartZ=0 EndX=-6.49 EndY=8.99 EndZ=0
    g4: LineSegment StartX=5.01 StartY=8.99 StartZ=0 EndX=6.49 EndY=8.99 EndZ=0
    g5: LineSegment StartX=6.49 StartY=8.99 StartZ=0 EndX=6.49 EndY=4.5 EndZ=0
    g6: LineSegment StartX=6.49 StartY=4.5 StartZ=0 EndX=5.01 EndY=4.5 EndZ=0
    g7: LineSegment StartX=5.01 StartY=4.5 StartZ=0 EndX=5.01 EndY=8.99 EndZ=0
    g8: LineSegment StartX=-7.5 StartY=8.99 StartZ=0 EndX=-6.49 EndY=8.99 EndZ=0
    g9: LineSegment StartX=-6.49 StartY=10 StartZ=0 EndX=-6.49 EndY=8.99 EndZ=0
    g10: LineSegment StartX=-5.01 StartY=8.99 StartZ=0 EndX=-4 EndY=8.99 EndZ=0
  constraints (32):
    c: Coincident(g0,g1)
    c: Coincident(g1,g2)
    c: Coincident(g2,g3)
    c: Coincident(g3,g0)
    c: Horizontal(g0)
    c: Horizontal(g2)
    c: Vertical(g1)
    c: Vertical(g3)
    c: Coincident(g4,g5)
    c: Coincident(g5,g6)
    c: Coincident(g6,g7)
    c: Coincident(g7,g4)
    c: Horizontal(g4)
    c: Horizontal(g6)
    c: Vertical(g5)
    c: Vertical(g7)
    c: DistanceX(g4,g4) = 1.48
    c: Equal(g0,g4)
    c: Equal(g7,g1)
    c: PointOnObject(g8,g-4)
    c: Coincident(g8,g0)
    c: Horizontal(g8)
    c: PointOnObject(g9,g-5)
    c: Coincident(g9,g0)
    c: Vertical(g9)
    c: Coincident(g10,g0)
    c: PointOnObject(g10,g-3)
    c: Horizontal(g10)
    c: Symmetric(g4,g0,g-2)
    c: Equal(g10,g9)
    c: Equal(g9,g8)
    c: DistanceY(g3,g3) = 4.49
FEATURE [PartDesign::Pocket] Pocket072
  AllowMultiFace = false
  BaseFeature = -> Pocket071
  Length = 2
  Length2 = 100
  Placement = pos=(0,0,0) rot=(0.57735,0.57735,0.57735;2.0944rad)
  Profile = -> Sketch155
  Refine = true
  Type = 0
FEATURE [PartDesign::Body] Body158  label="conector001"
  Group = -> [Sketch172,Pad045,Sketch173,Pocket070,Sketch154,Pocket071,Sketch155,Pocket072]
  Origin = -> Origin192
  Tip = -> Pocket072
FEATURE [Sketcher::SketchObject] Sketch174
  ExternalGeometry = -> [Pad046]
  FullyConstrained = false
  MapMode = 5
  Placement = pos=(-3e-16,4e-16,1) rot=(0,0,-1;1.5708rad)
  Support = -> [Pad046]
  sketch-geometry (7):
    g0: LineSegment StartX=-5.5 StartY=1 StartZ=0 EndX=-4.5 EndY=1 EndZ=0
    g1: LineSegment StartX=-4.5 StartY=1 StartZ=0 EndX=-4.5 EndY=8 EndZ=0
    g2: LineSegment StartX=-4.5 StartY=8 StartZ=0 EndX=-5.5 EndY=8 EndZ=0
    g3: LineSegment StartX=-5.5 StartY=8 StartZ=0 EndX=-5.5 EndY=1 EndZ=0
    g4: LineSegment StartX=-5.5 StartY=8 StartZ=0 EndX=-5.25 EndY=8.7 EndZ=0
    g5: LineSegment StartX=-5.25 StartY=8.7 StartZ=0 EndX=-4.75 EndY=8.7 EndZ=0
    g6: LineSegment StartX=-4.75 StartY=8.7 StartZ=0 EndX=-4.5 EndY=8 EndZ=0
  constraints (19):
    c: Coincident(g0,g1)
    c: Coincident(g1,g2)
    c: Coincident(g2,g3)
    c: Coincident(g3,g0)
    c: Horizontal(g0)
    c: Horizontal(g2)
    c: Vertical(g1)
    c: Vertical(g3)
    c: Coincident(g0,g-3)
    c: Coincident(g2,g4)
    c: Coincident(g4,g5)
    c: Horizontal(g5)
    c: Coincident(g5,g6)
    c: Coincident(g6,g1)
    c: DistanceY(g1,g5) = 0.7
    c: DistanceX(g5,g5) = 0.5
    c: Equal(g6,g4)
    c: DistanceX(g0,g0) = 1
    c: DistanceY(g3,g3) = 7
FEATURE [PartDesign::Pad] Pad047
  AllowMultiFace = false
  BaseFeature = -> Pad046
  Direction = (1,1,1)
  Length = 1
  Length2 = 100
  Placement = pos=(0,0,0) rot=(0.57735,0.57735,0.57735;2.0944rad)
  Profile = -> Sketch174
  Refine = true
  Reversed = true
  Type = 0
FEATURE [PartDesign::LinearPattern] LinearPattern001
  BaseFeature = -> Pad047
  Direction = -> Pad047 [Edge10]
  Length = 10
  Occurrences = 3
  Originals = -> [Pad047]
  Placement = pos=(0,0,0) rot=(0.57735,0.57735,0.57735;2.0944rad)
  Refine = true
  Reversed = true
FEATURE [PartDesign::Body] Body159  label="pin001"
  Group = -> [Sketch156,Pad046,Sketch174,Pad047,LinearPattern001]
  Origin = -> Origin193
  Placement = pos=(0,0,2) rot=(0,0,1;0rad)
  Tip = -> LinearPattern001
FEATURE [App::Part] Part033  label="Conector001"
  Group = -> [Body158,Body159]
  Origin = -> Origin191
  Placement = pos=(17,0,4) rot=(0,0,1;0rad)
FEATURE [App::Part] Part027  label="Nema 017-002"
  Group = -> [Part028,Part029,Part030,Part031,Part032,Part033]
  Origin = -> Origin180
  Placement = pos=(440,247,106) rot=(0,1,0;-1.5708rad)
FEATURE [Sketcher::SketchObject] Sketch175
  FullyConstrained = true
  MapMode = 5
  Placement = pos=(0,0,0) rot=(0.57735,0.57735,0.57735;2.0944rad)
  Support = -> [YZ_Plane189]
  sketch-geometry (1):
    g0: Circle CenterX=0 CenterY=0 CenterZ=0 NormalX=0 NormalY=0 NormalZ=1 AngleXU=0 Radius=4
  constraints (2):
    c: Coincident(g0,g-1)
    c: Radius(g0) = 4
FEATURE [PartDesign::Pad] Pad048
  Direction = (1,-2e-16,3e-16)
  Length = 350
  Length2 = 10
  Placement = pos=(0,0,0) rot=(0.57735,0.57735,0.57735;2.0944rad)
  Profile = -> Sketch175
  Type = 0
FEATURE [PartDesign::Body] Body160
  Group = -> [Sketch175,Pad048]
  Origin = -> Origin195
  Tip = -> Pad048
FEATURE [App::Part] Part034  label="eje-001"
  Group = -> [Body160]
  Origin = -> Origin194
FEATURE [Sketcher::SketchObject] Sketch176
  FullyConstrained = true
  MapMode = 5
  Placement = pos=(0,0,0) rot=(0.57735,0.57735,0.57735;2.0944rad)
  Support = -> [YZ_Plane191]
  sketch-geometry (1):
    g0: Circle CenterX=0 CenterY=0 CenterZ=0 NormalX=0 NormalY=0 NormalZ=1 AngleXU=0 Radius=4
  constraints (2):
    c: Coincident(g0,g-1)
    c: Radius(g0) = 4
FEATURE [PartDesign::Pad] Pad049
  Direction = (1,-2e-16,3e-16)
  Length = 350
  Length2 = 10
  Placement = pos=(0,0,0) rot=(0.57735,0.57735,0.57735;2.0944rad)
  Profile = -> Sketch176
  Type = 0
FEATURE [PartDesign::Body] Body161
  Group = -> [Sketch176,Pad049]
  Origin = -> Origin197
  Tip = -> Pad049
FEATURE [App::Part] Part035  label="eje-002"
  Group = -> [Body161]
  Origin = -> Origin196
  Placement = pos=(-31,120,80) rot=(0,0,1;0rad)
FEATURE [Sketcher::SketchObject] Sketch177
  FullyConstrained = true
  MapMode = 5
  Placement = pos=(0,0,0) rot=(0.57735,0.57735,0.57735;2.0944rad)
  Support = -> [YZ_Plane193]
  sketch-geometry (1):
    g0: Circle CenterX=0 CenterY=0 CenterZ=0 NormalX=0 NormalY=0 NormalZ=1 AngleXU=0 Radius=4
  constraints (2):
    c: Coincident(g0,g-1)
    c: Radius(g0) = 4
FEATURE [PartDesign::Pad] Pad050
  Direction = (1,-2e-16,3e-16)
  Length = 350
  Length2 = 10
  Placement = pos=(0,0,0) rot=(0.57735,0.57735,0.57735;2.0944rad)
  Profile = -> Sketch177
  Type = 0
FEATURE [PartDesign::Body] Body162
  Group = -> [Sketch177,Pad050]
  Origin = -> Origin199
  Tip = -> Pad050
FEATURE [App::Part] Part036  label="eje-003"
  Group = -> [Body162]
  Origin = -> Origin198
FEATURE [Sketcher::SketchObject] Sketch178
  FullyConstrained = true
  MapMode = 5
  Placement = pos=(0,0,0) rot=(0.57735,0.57735,0.57735;2.0944rad)
  Support = -> [YZ_Plane195]
  sketch-geometry (1):
    g0: Circle CenterX=0 CenterY=0 CenterZ=0 NormalX=0 NormalY=0 NormalZ=1 AngleXU=0 Radius=60
  constraints (2):
    c: Coincident(g0,g-1)
    c: Radius(g0) = 60
FEATURE [PartDesign::Pad] Pad051
  Direction = (1,-2e-16,3e-16)
  Length = 8
  Length2 = 10
  Placement = pos=(0,0,0) rot=(0.57735,0.57735,0.57735;2.0944rad)
  Profile = -> Sketch178
  Type = 0
FEATURE [PartDesign::Body] Body163
  Group = -> [Sketch178,Pad051]
  Origin = -> Origin201
  Tip = -> Pad051
FEATURE [App::Part] Part037  label="rueda-001"
  Group = -> [Body163]
  Origin = -> Origin200
FEATURE [Sketcher::SketchObject] Sketch179
  FullyConstrained = false
  MapMode = 5
  Placement = pos=(0,0,0) rot=(0.57735,0.57735,0.57735;2.0944rad)
  Support = -> [YZ_Plane197]
  sketch-geometry (8):
    g0: LineSegment StartX=3.44519 StartY=-3.62363 StartZ=0 EndX=4.86075 EndY=1.17181 EndZ=0
    g1: LineSegment StartX=4.86075 StartY=1.17181 StartZ=0 EndX=1.41556 EndY=4.79544 EndZ=0
    g2: LineSegment StartX=1.41556 StartY=4.79544 StartZ=0 EndX=-3.44519 EndY=3.62363 EndZ=0
    g3: LineSegment StartX=-3.44519 StartY=3.62363 StartZ=0 EndX=-4.86075 EndY=-1.17181 EndZ=0
    g4: LineSegment StartX=-4.86075 StartY=-1.17181 StartZ=0 EndX=-1.41556 EndY=-4.79544 EndZ=0
    g5: LineSegment StartX=-1.41556 StartY=-4.79544 StartZ=0 EndX=3.44519 EndY=-3.62363 EndZ=0
    g6: Circle CenterX=0 CenterY=0 CenterZ=0 NormalX=0 NormalY=0 NormalZ=1 AngleXU=0 Radius=5
    g7: Circle CenterX=0 CenterY=0 CenterZ=0 NormalX=0 NormalY=0 NormalZ=1 AngleXU=0 Radius=3
  constraints (17):
    c: Coincident(g0,g1)
    c: Coincident(g1,g2)
    c: Coincident(g2,g3)
    c: Coincident(g3,g4)
    c: Coincident(g4,g5)
    c: Coincident(g5,g0)
    c: Equal(g0, g1-g5) x5
    c: PointOnObject(g0,g6)
    c: PointOnObject(g1,g6)
    c: PointOnObject(g2,g6)
    c: PointOnObject(g3,g6)
    c: PointOnObject(g4,g6)
    c: PointOnObject(g5,g6)
    c: Coincident(g6,g-1)
    c: Coincident(g7,g6)
    c: Radius(g7) = 3
    c: Radius(g6) = 5
FEATURE [PartDesign::Pad] Pad052
  Direction = (1,-2e-16,3e-16)
  Length = 3
  Length2 = 10
  Placement = pos=(0,0,0) rot=(0.57735,0.57735,0.57735;2.0944rad)
  Profile = -> Sketch179
  Type = 0
FEATURE [PartDesign::Pad] Pad053
  BaseFeature = -> Pad052
  Direction = (1,-2e-16,6e-16)
  Length = 50
  Length2 = 10
  Placement = pos=(0,0,0) rot=(0.57735,0.57735,0.57735;2.0944rad)
  Profile = -> Pad052 [Edge20]
  Type = 0
FEATURE [PartDesign::Body] Body164
  Group = -> [Sketch179,Pad052,Pad053]
  Origin = -> Origin203
  Tip = -> Pad053
FEATURE [App::Part] Part038  label="tornillo M6-30-001"
  Group = -> [Body164]
  Origin = -> Origin202
  Placement = pos=(10,-4,181) rot=(0,0,1;1.5708rad)
FEATURE [Sketcher::SketchObject] Sketch180
  FullyConstrained = false
  MapMode = 5
  Placement = pos=(0,0,0) rot=(0.57735,0.57735,0.57735;2.0944rad)
  Support = -> [YZ_Plane199]
  sketch-geometry (8):
    g0: LineSegment StartX=3.44519 StartY=-3.62363 StartZ=0 EndX=4.86075 EndY=1.17181 EndZ=0
    g1: LineSegment StartX=4.86075 StartY=1.17181 StartZ=0 EndX=1.41556 EndY=4.79544 EndZ=0
    g2: LineSegment StartX=1.41556 StartY=4.79544 StartZ=0 EndX=-3.44519 EndY=3.62363 EndZ=0
    g3: LineSegment StartX=-3.44519 StartY=3.62363 StartZ=0 EndX=-4.86075 EndY=-1.17181 EndZ=0
    g4: LineSegment StartX=-4.86075 StartY=-1.17181 StartZ=0 EndX=-1.41556 EndY=-4.79544 EndZ=0
    g5: LineSegment StartX=-1.41556 StartY=-4.79544 StartZ=0 EndX=3.44519 EndY=-3.62363 EndZ=0
    g6: Circle CenterX=0 CenterY=0 CenterZ=0 NormalX=0 NormalY=0 NormalZ=1 AngleXU=0 Radius=5
    g7: Circle CenterX=0 CenterY=0 CenterZ=0 NormalX=0 NormalY=0 NormalZ=1 AngleXU=0 Radius=3
  constraints (17):
    c: Coincident(g0,g1)
    c: Coincident(g1,g2)
    c: Coincident(g2,g3)
    c: Coincident(g3,g4)
    c: Coincident(g4,g5)
    c: Coincident(g5,g0)
    c: Equal(g0, g1-g5) x5
    c: PointOnObject(g0,g6)
    c: PointOnObject(g1,g6)
    c: PointOnObject(g2,g6)
    c: PointOnObject(g3,g6)
    c: PointOnObject(g4,g6)
    c: PointOnObject(g5,g6)
    c: Coincident(g6,g-1)
    c: Coincident(g7,g6)
    c: Radius(g7) = 3
    c: Radius(g6) = 5
FEATURE [PartDesign::Pad] Pad054
  Direction = (1,-2e-16,3e-16)
  Length = 3
  Length2 = 10
  Placement = pos=(0,0,0) rot=(0.57735,0.57735,0.57735;2.0944rad)
  Profile = -> Sketch180
  Type = 0
FEATURE [PartDesign::Pad] Pad055
  BaseFeature = -> Pad054
  Direction = (1,-2e-16,6e-16)
  Length = 50
  Length2 = 10
  Placement = pos=(0,0,0) rot=(0.57735,0.57735,0.57735;2.0944rad)
  Profile = -> Pad054 [Edge20]
  Type = 0
FEATURE [PartDesign::Body] Body165
  Group = -> [Sketch180,Pad054,Pad055]
  Origin = -> Origin205
  Tip = -> Pad055
FEATURE [App::Part] Part039  label="tornillo M6-30-002"
  Group = -> [Body165]
  Origin = -> Origin204
  Placement = pos=(10,-4,10) rot=(0,0,1;1.5708rad)
FEATURE [Sketcher::SketchObject] Sketch181
  FullyConstrained = false
  MapMode = 5
  Placement = pos=(0,0,0) rot=(0.57735,0.57735,0.57735;2.0944rad)
  Support = -> [YZ_Plane201]
  sketch-geometry (8):
    g0: LineSegment StartX=3.44519 StartY=-3.62363 StartZ=0 EndX=4.86075 EndY=1.17181 EndZ=0
    g1: LineSegment StartX=4.86075 StartY=1.17181 StartZ=0 EndX=1.41556 EndY=4.79544 EndZ=0
    g2: LineSegment StartX=1.41556 StartY=4.79544 StartZ=0 EndX=-3.44519 EndY=3.62363 EndZ=0
    g3: LineSegment StartX=-3.44519 StartY=3.62363 StartZ=0 EndX=-4.86075 EndY=-1.17181 EndZ=0
    g4: LineSegment StartX=-4.86075 StartY=-1.17181 StartZ=0 EndX=-1.41556 EndY=-4.79544 EndZ=0
    g5: LineSegment StartX=-1.41556 StartY=-4.79544 StartZ=0 EndX=3.44519 EndY=-3.62363 EndZ=0
    g6: Circle CenterX=0 CenterY=0 CenterZ=0 NormalX=0 NormalY=0 NormalZ=1 AngleXU=0 Radius=5
    g7: Circle CenterX=0 CenterY=0 CenterZ=0 NormalX=0 NormalY=0 NormalZ=1 AngleXU=0 Radius=3
  constraints (17):
    c: Coincident(g0,g1)
    c: Coincident(g1,g2)
    c: Coincident(g2,g3)
    c: Coincident(g3,g4)
    c: Coincident(g4,g5)
    c: Coincident(g5,g0)
    c: Equal(g0, g1-g5) x5
    c: PointOnObject(g0,g6)
    c: PointOnObject(g1,g6)
    c: PointOnObject(g2,g6)
    c: PointOnObject(g3,g6)
    c: PointOnObject(g4,g6)
    c: PointOnObject(g5,g6)
    c: Coincident(g6,g-1)
    c: Coincident(g7,g6)
    c: Radius(g7) = 3
    c: Radius(g6) = 5
FEATURE [PartDesign::Pad] Pad056
  Direction = (1,-2e-16,3e-16)
  Length = 3
  Length2 = 10
  Placement = pos=(0,0,0) rot=(0.57735,0.57735,0.57735;2.0944rad)
  Profile = -> Sketch181
  Type = 0
FEATURE [PartDesign::Pad] Pad057
  BaseFeature = -> Pad056
  Direction = (1,-2e-16,6e-16)
  Length = 50
  Length2 = 10
  Placement = pos=(0,0,0) rot=(0.57735,0.57735,0.57735;2.0944rad)
  Profile = -> Pad056 [Edge20]
  Type = 0
FEATURE [PartDesign::Body] Body166
  Group = -> [Sketch181,Pad056,Pad057]
  Origin = -> Origin207
  Tip = -> Pad057
FEATURE [App::Part] Part040  label="tornillo M6-30-003"
  Group = -> [Body166]
  Origin = -> Origin206
  Placement = pos=(330,-4,9) rot=(0,0,1;1.5708rad)
FEATURE [Sketcher::SketchObject] Sketch182
  FullyConstrained = false
  MapMode = 5
  Placement = pos=(0,0,0) rot=(0.57735,0.57735,0.57735;2.0944rad)
  Support = -> [YZ_Plane203]
  sketch-geometry (8):
    g0: LineSegment StartX=3.44519 StartY=-3.62363 StartZ=0 EndX=4.86075 EndY=1.17181 EndZ=0
    g1: LineSegment StartX=4.86075 StartY=1.17181 StartZ=0 EndX=1.41556 EndY=4.79544 EndZ=0
    g2: LineSegment StartX=1.41556 StartY=4.79544 StartZ=0 EndX=-3.44519 EndY=3.62363 EndZ=0
    g3: LineSegment StartX=-3.44519 StartY=3.62363 StartZ=0 EndX=-4.86075 EndY=-1.17181 EndZ=0
    g4: LineSegment StartX=-4.86075 StartY=-1.17181 StartZ=0 EndX=-1.41556 EndY=-4.79544 EndZ=0
    g5: LineSegment StartX=-1.41556 StartY=-4.79544 StartZ=0 EndX=3.44519 EndY=-3.62363 EndZ=0
    g6: Circle CenterX=0 CenterY=0 CenterZ=0 NormalX=0 NormalY=0 NormalZ=1 AngleXU=0 Radius=5
    g7: Circle CenterX=0 CenterY=0 CenterZ=0 NormalX=0 NormalY=0 NormalZ=1 AngleXU=0 Radius=3
  constraints (17):
    c: Coincident(g0,g1)
    c: Coincident(g1,g2)
    c: Coincident(g2,g3)
    c: Coincident(g3,g4)
    c: Coincident(g4,g5)
    c: Coincident(g5,g0)
    c: Equal(g0, g1-g5) x5
    c: PointOnObject(g0,g6)
    c: PointOnObject(g1,g6)
    c: PointOnObject(g2,g6)
    c: PointOnObject(g3,g6)
    c: PointOnObject(g4,g6)
    c: PointOnObject(g5,g6)
    c: Coincident(g6,g-1)
    c: Coincident(g7,g6)
    c: Radius(g7) = 3
    c: Radius(g6) = 5
FEATURE [PartDesign::Pad] Pad058
  Direction = (1,-2e-16,3e-16)
  Length = 3
  Length2 = 10
  Placement = pos=(0,0,0) rot=(0.57735,0.57735,0.57735;2.0944rad)
  Profile = -> Sketch182
  Type = 0
FEATURE [PartDesign::Pad] Pad059
  BaseFeature = -> Pad058
  Direction = (1,-2e-16,6e-16)
  Length = 50
  Length2 = 10
  Placement = pos=(0,0,0) rot=(0.57735,0.57735,0.57735;2.0944rad)
  Profile = -> Pad058 [Edge20]
  Type = 0
FEATURE [PartDesign::Body] Body167
  Group = -> [Sketch182,Pad058,Pad059]
  Origin = -> Origin209
  Tip = -> Pad059
FEATURE [App::Part] Part041  label="tornillo M6-30-004"
  Group = -> [Body167]
  Origin = -> Origin208
  Placement = pos=(330,-4,181) rot=(0,0,1;1.5708rad)
FEATURE [Sketcher::SketchObject] Sketch183
  FullyConstrained = false
  MapMode = 5
  Placement = pos=(0,0,0) rot=(0.57735,0.57735,0.57735;2.0944rad)
  Support = -> [YZ_Plane205]
  sketch-geometry (8):
    g0: LineSegment StartX=3.44519 StartY=-3.62363 StartZ=0 EndX=4.86075 EndY=1.17181 EndZ=0
    g1: LineSegment StartX=4.86075 StartY=1.17181 StartZ=0 EndX=1.41556 EndY=4.79544 EndZ=0
    g2: LineSegment StartX=1.41556 StartY=4.79544 StartZ=0 EndX=-3.44519 EndY=3.62363 EndZ=0
    g3: LineSegment StartX=-3.44519 StartY=3.62363 StartZ=0 EndX=-4.86075 EndY=-1.17181 EndZ=0
    g4: LineSegment StartX=-4.86075 StartY=-1.17181 StartZ=0 EndX=-1.41556 EndY=-4.79544 EndZ=0
    g5: LineSegment StartX=-1.41556 StartY=-4.79544 StartZ=0 EndX=3.44519 EndY=-3.62363 EndZ=0
    g6: Circle CenterX=0 CenterY=0 CenterZ=0 NormalX=0 NormalY=0 NormalZ=1 AngleXU=0 Radius=5
    g7: Circle CenterX=0 CenterY=0 CenterZ=0 NormalX=0 NormalY=0 NormalZ=1 AngleXU=0 Radius=3
  constraints (17):
    c: Coincident(g0,g1)
    c: Coincident(g1,g2)
    c: Coincident(g2,g3)
    c: Coincident(g3,g4)
    c: Coincident(g4,g5)
    c: Coincident(g5,g0)
    c: Equal(g0, g1-g5) x5
    c: PointOnObject(g0,g6)
    c: PointOnObject(g1,g6)
    c: PointOnObject(g2,g6)
    c: PointOnObject(g3,g6)
    c: PointOnObject(g4,g6)
    c: PointOnObject(g5,g6)
    c: Coincident(g6,g-1)
    c: Coincident(g7,g6)
    c: Radius(g7) = 3
    c: Radius(g6) = 5
FEATURE [PartDesign::Pad] Pad060
  Direction = (1,-2e-16,3e-16)
  Length = 3
  Length2 = 10
  Placement = pos=(0,0,0) rot=(0.57735,0.57735,0.57735;2.0944rad)
  Profile = -> Sketch183
  Type = 0
FEATURE [PartDesign::Pad] Pad061
  BaseFeature = -> Pad060
  Direction = (1,-2e-16,6e-16)
  Length = 50
  Length2 = 10
  Placement = pos=(0,0,0) rot=(0.57735,0.57735,0.57735;2.0944rad)
  Profile = -> Pad060 [Edge20]
  Type = 0
FEATURE [PartDesign::Body] Body168
  Group = -> [Sketch183,Pad060,Pad061]
  Origin = -> Origin211
  Tip = -> Pad061
FEATURE [App::Part] Part042  label="tornillo M6-30-005"
  Group = -> [Body168]
  Origin = -> Origin210
  Placement = pos=(330,344,180) rot=(0,0,1;-1.5708rad)
FEATURE [Sketcher::SketchObject] Sketch184
  FullyConstrained = false
  MapMode = 5
  Placement = pos=(0,0,0) rot=(0.57735,0.57735,0.57735;2.0944rad)
  Support = -> [YZ_Plane207]
  sketch-geometry (8):
    g0: LineSegment StartX=3.44519 StartY=-3.62363 StartZ=0 EndX=4.86075 EndY=1.17181 EndZ=0
    g1: LineSegment StartX=4.86075 StartY=1.17181 StartZ=0 EndX=1.41556 EndY=4.79544 EndZ=0
    g2: LineSegment StartX=1.41556 StartY=4.79544 StartZ=0 EndX=-3.44519 EndY=3.62363 EndZ=0
    g3: LineSegment StartX=-3.44519 StartY=3.62363 StartZ=0 EndX=-4.86075 EndY=-1.17181 EndZ=0
    g4: LineSegment StartX=-4.86075 StartY=-1.17181 StartZ=0 EndX=-1.41556 EndY=-4.79544 EndZ=0
    g5: LineSegment StartX=-1.41556 StartY=-4.79544 StartZ=0 EndX=3.44519 EndY=-3.62363 EndZ=0
    g6: Circle CenterX=0 CenterY=0 CenterZ=0 NormalX=0 NormalY=0 NormalZ=1 AngleXU=0 Radius=5
    g7: Circle CenterX=0 CenterY=0 CenterZ=0 NormalX=0 NormalY=0 NormalZ=1 AngleXU=0 Radius=3
  constraints (17):
    c: Coincident(g0,g1)
    c: Coincident(g1,g2)
    c: Coincident(g2,g3)
    c: Coincident(g3,g4)
    c: Coincident(g4,g5)
    c: Coincident(g5,g0)
    c: Equal(g0, g1-g5) x5
    c: PointOnObject(g0,g6)
    c: PointOnObject(g1,g6)
    c: PointOnObject(g2,g6)
    c: PointOnObject(g3,g6)
    c: PointOnObject(g4,g6)
    c: PointOnObject(g5,g6)
    c: Coincident(g6,g-1)
    c: Coincident(g7,g6)
    c: Radius(g7) = 3
    c: Radius(g6) = 5
FEATURE [PartDesign::Pad] Pad062
  Direction = (1,-2e-16,3e-16)
  Length = 3
  Length2 = 10
  Placement = pos=(0,0,0) rot=(0.57735,0.57735,0.57735;2.0944rad)
  Profile = -> Sketch184
  Type = 0
FEATURE [PartDesign::Pad] Pad063
  BaseFeature = -> Pad062
  Direction = (1,-2e-16,6e-16)
  Length = 50
  Length2 = 10
  Placement = pos=(0,0,0) rot=(0.57735,0.57735,0.57735;2.0944rad)
  Profile = -> Pad062 [Edge20]
  Type = 0
FEATURE [PartDesign::Body] Body169
  Group = -> [Sketch184,Pad062,Pad063]
  Origin = -> Origin213
  Tip = -> Pad063
FEATURE [App::Part] Part043  label="tornillo M6-30-006"
  Group = -> [Body169]
  Origin = -> Origin212
  Placement = pos=(330,344,9) rot=(0,0,1;-1.5708rad)
FEATURE [Sketcher::SketchObject] Sketch185
  FullyConstrained = false
  MapMode = 5
  Placement = pos=(0,0,0) rot=(0.57735,0.57735,0.57735;2.0944rad)
  Support = -> [YZ_Plane209]
  sketch-geometry (8):
    g0: LineSegment StartX=3.44519 StartY=-3.62363 StartZ=0 EndX=4.86075 EndY=1.17181 EndZ=0
    g1: LineSegment StartX=4.86075 StartY=1.17181 StartZ=0 EndX=1.41556 EndY=4.79544 EndZ=0
    g2: LineSegment StartX=1.41556 StartY=4.79544 StartZ=0 EndX=-3.44519 EndY=3.62363 EndZ=0
    g3: LineSegment StartX=-3.44519 StartY=3.62363 StartZ=0 EndX=-4.86075 EndY=-1.17181 EndZ=0
    g4: LineSegment StartX=-4.86075 StartY=-1.17181 StartZ=0 EndX=-1.41556 EndY=-4.79544 EndZ=0
    g5: LineSegment StartX=-1.41556 StartY=-4.79544 StartZ=0 EndX=3.44519 EndY=-3.62363 EndZ=0
    g6: Circle CenterX=0 CenterY=0 CenterZ=0 NormalX=0 NormalY=0 NormalZ=1 AngleXU=0 Radius=5
    g7: Circle CenterX=0 CenterY=0 CenterZ=0 NormalX=0 NormalY=0 NormalZ=1 AngleXU=0 Radius=3
  constraints (17):
    c: Coincident(g0,g1)
    c: Coincident(g1,g2)
    c: Coincident(g2,g3)
    c: Coincident(g3,g4)
    c: Coincident(g4,g5)
    c: Coincident(g5,g0)
    c: Equal(g0, g1-g5) x5
    c: PointOnObject(g0,g6)
    c: PointOnObject(g1,g6)
    c: PointOnObject(g2,g6)
    c: PointOnObject(g3,g6)
    c: PointOnObject(g4,g6)
    c: PointOnObject(g5,g6)
    c: Coincident(g6,g-1)
    c: Coincident(g7,g6)
    c: Radius(g7) = 3
    c: Radius(g6) = 5
FEATURE [PartDesign::Pad] Pad064
  Direction = (1,-2e-16,3e-16)
  Length = 3
  Length2 = 10
  Placement = pos=(0,0,0) rot=(0.57735,0.57735,0.57735;2.0944rad)
  Profile = -> Sketch185
  Type = 0
FEATURE [PartDesign::Pad] Pad065
  BaseFeature = -> Pad064
  Direction = (1,-2e-16,6e-16)
  Length = 50
  Length2 = 10
  Placement = pos=(0,0,0) rot=(0.57735,0.57735,0.57735;2.0944rad)
  Profile = -> Pad064 [Edge20]
  Type = 0
FEATURE [PartDesign::Body] Body170
  Group = -> [Sketch185,Pad064,Pad065]
  Origin = -> Origin215
  Tip = -> Pad065
FEATURE [App::Part] Part044  label="tornillo M6-30-007"
  Group = -> [Body170]
  Origin = -> Origin214
  Placement = pos=(10,344,10) rot=(0,0,1;-1.5708rad)
FEATURE [Sketcher::SketchObject] Sketch186
  FullyConstrained = false
  MapMode = 5
  Placement = pos=(0,0,0) rot=(0.57735,0.57735,0.57735;2.0944rad)
  Support = -> [YZ_Plane211]
  sketch-geometry (8):
    g0: LineSegment StartX=3.44519 StartY=-3.62363 StartZ=0 EndX=4.86075 EndY=1.17181 EndZ=0
    g1: LineSegment StartX=4.86075 StartY=1.17181 StartZ=0 EndX=1.41556 EndY=4.79544 EndZ=0
    g2: LineSegment StartX=1.41556 StartY=4.79544 StartZ=0 EndX=-3.44519 EndY=3.62363 EndZ=0
    g3: LineSegment StartX=-3.44519 StartY=3.62363 StartZ=0 EndX=-4.86075 EndY=-1.17181 EndZ=0
    g4: LineSegment StartX=-4.86075 StartY=-1.17181 StartZ=0 EndX=-1.41556 EndY=-4.79544 EndZ=0
    g5: LineSegment StartX=-1.41556 StartY=-4.79544 StartZ=0 EndX=3.44519 EndY=-3.62363 EndZ=0
    g6: Circle CenterX=0 CenterY=0 CenterZ=0 NormalX=0 NormalY=0 NormalZ=1 AngleXU=0 Radius=5
    g7: Circle CenterX=0 CenterY=0 CenterZ=0 NormalX=0 NormalY=0 NormalZ=1 AngleXU=0 Radius=3
  constraints (17):
    c: Coincident(g0,g1)
    c: Coincident(g1,g2)
    c: Coincident(g2,g3)
    c: Coincident(g3,g4)
    c: Coincident(g4,g5)
    c: Coincident(g5,g0)
    c: Equal(g0, g1-g5) x5
    c: PointOnObject(g0,g6)
    c: PointOnObject(g1,g6)
    c: PointOnObject(g2,g6)
    c: PointOnObject(g3,g6)
    c: PointOnObject(g4,g6)
    c: PointOnObject(g5,g6)
    c: Coincident(g6,g-1)
    c: Coincident(g7,g6)
    c: Radius(g7) = 3
    c: Radius(g6) = 5
FEATURE [PartDesign::Pad] Pad066
  Direction = (1,-2e-16,3e-16)
  Length = 3
  Length2 = 10
  Placement = pos=(0,0,0) rot=(0.57735,0.57735,0.57735;2.0944rad)
  Profile = -> Sketch186
  Type = 0
FEATURE [PartDesign::Pad] Pad067
  BaseFeature = -> Pad066
  Direction = (1,-2e-16,6e-16)
  Length = 50
  Length2 = 10
  Placement = pos=(0,0,0) rot=(0.57735,0.57735,0.57735;2.0944rad)
  Profile = -> Pad066 [Edge20]
  Type = 0
FEATURE [PartDesign::Body] Body171
  Group = -> [Sketch186,Pad066,Pad067]
  Origin = -> Origin217
  Tip = -> Pad067
FEATURE [App::Part] Part045  label="tornillo M6-30-008"
  Group = -> [Body171]
  Origin = -> Origin216
  Placement = pos=(10,344,180) rot=(0,0,1;-1.5708rad)
FEATURE [Sketcher::SketchObject] Sketch187
  FullyConstrained = false
  MapMode = 5
  Placement = pos=(0,0,0) rot=(0.57735,0.57735,0.57735;2.0944rad)
  Support = -> [YZ_Plane213]
  sketch-geometry (8):
    g0: LineSegment StartX=2.8963 StartY=-2.75889 StartZ=0 EndX=3.83742 EndY=1.12882 EndZ=0
    g1: LineSegment StartX=3.83742 StartY=1.12882 StartZ=0 EndX=0.941117 EndY=3.88771 EndZ=0
    g2: LineSegment StartX=0.941117 StartY=3.88771 StartZ=0 EndX=-2.8963 EndY=2.75889 EndZ=0
    g3: LineSegment StartX=-2.8963 StartY=2.75889 StartZ=0 EndX=-3.83742 EndY=-1.12882 EndZ=0
    g4: LineSegment StartX=-3.83742 StartY=-1.12882 StartZ=0 EndX=-0.941117 EndY=-3.88771 EndZ=0
    g5: LineSegment StartX=-0.941117 StartY=-3.88771 StartZ=0 EndX=2.8963 EndY=-2.75889 EndZ=0
    g6: Circle CenterX=0 CenterY=0 CenterZ=0 NormalX=0 NormalY=0 NormalZ=1 AngleXU=0 Radius=4
    g7: Circle CenterX=0 CenterY=0 CenterZ=0 NormalX=0 NormalY=0 NormalZ=1 AngleXU=0 Radius=2.5
  constraints (17):
    c: Coincident(g0,g1)
    c: Coincident(g1,g2)
    c: Coincident(g2,g3)
    c: Coincident(g3,g4)
    c: Coincident(g4,g5)
    c: Coincident(g5,g0)
    c: Equal(g0, g1-g5) x5
    c: PointOnObject(g0,g6)
    c: PointOnObject(g1,g6)
    c: PointOnObject(g2,g6)
    c: PointOnObject(g3,g6)
    c: PointOnObject(g4,g6)
    c: PointOnObject(g5,g6)
    c: Coincident(g6,g-1)
    c: Coincident(g7,g6)
    c: Radius(g7) = 2.5
    c: Radius(g6) = 4
FEATURE [PartDesign::Pad] Pad068
  Direction = (1,-2e-16,3e-16)
  Length = 3
  Length2 = 10
  Placement = pos=(0,0,0) rot=(0.57735,0.57735,0.57735;2.0944rad)
  Profile = -> Sketch187
  Type = 0
FEATURE [PartDesign::Pad] Pad069
  BaseFeature = -> Pad068
  Direction = (1,-2e-16,6e-16)
  Length = 15
  Length2 = 10
  Placement = pos=(0,0,0) rot=(0.57735,0.57735,0.57735;2.0944rad)
  Profile = -> Pad068 [Edge20]
  Type = 0
FEATURE [PartDesign::Body] Body172
  Group = -> [Sketch187,Pad068,Pad069]
  Origin = -> Origin219
  Tip = -> Pad069
FEATURE [App::Part] Part046  label="tornillo M5-15-001"
  Group = -> [Body172]
  Origin = -> Origin218
  Placement = pos=(10,267,98) rot=(0,1,0;1.5708rad)
FEATURE [Sketcher::SketchObject] Sketch188
  FullyConstrained = false
  MapMode = 5
  Placement = pos=(0,0,0) rot=(0.57735,0.57735,0.57735;2.0944rad)
  Support = -> [YZ_Plane215]
  sketch-geometry (8):
    g0: LineSegment StartX=2.8963 StartY=-2.75889 StartZ=0 EndX=3.83742 EndY=1.12882 EndZ=0
    g1: LineSegment StartX=3.83742 StartY=1.12882 StartZ=0 EndX=0.941117 EndY=3.88771 EndZ=0
    g2: LineSegment StartX=0.941117 StartY=3.88771 StartZ=0 EndX=-2.8963 EndY=2.75889 EndZ=0
    g3: LineSegment StartX=-2.8963 StartY=2.75889 StartZ=0 EndX=-3.83742 EndY=-1.12882 EndZ=0
    g4: LineSegment StartX=-3.83742 StartY=-1.12882 StartZ=0 EndX=-0.941117 EndY=-3.88771 EndZ=0
    g5: LineSegment StartX=-0.941117 StartY=-3.88771 StartZ=0 EndX=2.8963 EndY=-2.75889 EndZ=0
    g6: Circle CenterX=0 CenterY=0 CenterZ=0 NormalX=0 NormalY=0 NormalZ=1 AngleXU=0 Radius=4
    g7: Circle CenterX=0 CenterY=0 CenterZ=0 NormalX=0 NormalY=0 NormalZ=1 AngleXU=0 Radius=2.5
  constraints (17):
    c: Coincident(g0,g1)
    c: Coincident(g1,g2)
    c: Coincident(g2,g3)
    c: Coincident(g3,g4)
    c: Coincident(g4,g5)
    c: Coincident(g5,g0)
    c: Equal(g0, g1-g5) x5
    c: PointOnObject(g0,g6)
    c: PointOnObject(g1,g6)
    c: PointOnObject(g2,g6)
    c: PointOnObject(g3,g6)
    c: PointOnObject(g4,g6)
    c: PointOnObject(g5,g6)
    c: Coincident(g6,g-1)
    c: Coincident(g7,g6)
    c: Radius(g7) = 2.5
    c: Radius(g6) = 4
FEATURE [PartDesign::Pad] Pad070
  Direction = (1,-2e-16,3e-16)
  Length = 3
  Length2 = 10
  Placement = pos=(0,0,0) rot=(0.57735,0.57735,0.57735;2.0944rad)
  Profile = -> Sketch188
  Type = 0
FEATURE [PartDesign::Pad] Pad071
  BaseFeature = -> Pad070
  Direction = (1,-2e-16,6e-16)
  Length = 15
  Length2 = 10
  Placement = pos=(0,0,0) rot=(0.57735,0.57735,0.57735;2.0944rad)
  Profile = -> Pad070 [Edge20]
  Type = 0
FEATURE [PartDesign::Body] Body173
  Group = -> [Sketch188,Pad070,Pad071]
  Origin = -> Origin221
  Tip = -> Pad071
FEATURE [App::Part] Part047  label="tornillo M5-15-002"
  Group = -> [Body173]
  Origin = -> Origin220
  Placement = pos=(10,99,98) rot=(0,1,0;1.5708rad)
FEATURE [Sketcher::SketchObject] Sketch189
  FullyConstrained = false
  MapMode = 5
  Placement = pos=(0,0,0) rot=(0.57735,0.57735,0.57735;2.0944rad)
  Support = -> [YZ_Plane217]
  sketch-geometry (8):
    g0: LineSegment StartX=2.8963 StartY=-2.75889 StartZ=0 EndX=3.83742 EndY=1.12882 EndZ=0
    g1: LineSegment StartX=3.83742 StartY=1.12882 StartZ=0 EndX=0.941117 EndY=3.88771 EndZ=0
    g2: LineSegment StartX=0.941117 StartY=3.88771 StartZ=0 EndX=-2.8963 EndY=2.75889 EndZ=0
    g3: LineSegment StartX=-2.8963 StartY=2.75889 StartZ=0 EndX=-3.83742 EndY=-1.12882 EndZ=0
    g4: LineSegment StartX=-3.83742 StartY=-1.12882 StartZ=0 EndX=-0.941117 EndY=-3.88771 EndZ=0
    g5: LineSegment StartX=-0.941117 StartY=-3.88771 StartZ=0 EndX=2.8963 EndY=-2.75889 EndZ=0
    g6: Circle CenterX=0 CenterY=0 CenterZ=0 NormalX=0 NormalY=0 NormalZ=1 AngleXU=0 Radius=4
    g7: Circle CenterX=0 CenterY=0 CenterZ=0 NormalX=0 NormalY=0 NormalZ=1 AngleXU=0 Radius=2.5
  constraints (17):
    c: Coincident(g0,g1)
    c: Coincident(g1,g2)
    c: Coincident(g2,g3)
    c: Coincident(g3,g4)
    c: Coincident(g4,g5)
    c: Coincident(g5,g0)
    c: Equal(g0, g1-g5) x5
    c: PointOnObject(g0,g6)
    c: PointOnObject(g1,g6)
    c: PointOnObject(g2,g6)
    c: PointOnObject(g3,g6)
    c: PointOnObject(g4,g6)
    c: PointOnObject(g5,g6)
    c: Coincident(g6,g-1)
    c: Coincident(g7,g6)
    c: Radius(g7) = 2.5
    c: Radius(g6) = 4
FEATURE [PartDesign::Pad] Pad072
  Direction = (1,-2e-16,3e-16)
  Length = 3
  Length2 = 10
  Placement = pos=(0,0,0) rot=(0.57735,0.57735,0.57735;2.0944rad)
  Profile = -> Sketch189
  Type = 0
FEATURE [PartDesign::Pad] Pad073
  BaseFeature = -> Pad072
  Direction = (1,-2e-16,6e-16)
  Length = 15
  Length2 = 10
  Placement = pos=(0,0,0) rot=(0.57735,0.57735,0.57735;2.0944rad)
  Profile = -> Pad072 [Edge20]
  Type = 0
FEATURE [PartDesign::Body] Body174
  Group = -> [Sketch189,Pad072,Pad073]
  Origin = -> Origin223
  Tip = -> Pad073
FEATURE [App::Part] Part048  label="tornillo M5-15-003"
  Group = -> [Body174]
  Origin = -> Origin222
  Placement = pos=(10,225,98) rot=(0,1,0;1.5708rad)
FEATURE [Sketcher::SketchObject] Sketch190
  FullyConstrained = false
  MapMode = 5
  Placement = pos=(0,0,0) rot=(0.57735,0.57735,0.57735;2.0944rad)
  Support = -> [YZ_Plane219]
  sketch-geometry (8):
    g0: LineSegment StartX=2.8963 StartY=-2.75889 StartZ=0 EndX=3.83742 EndY=1.12882 EndZ=0
    g1: LineSegment StartX=3.83742 StartY=1.12882 StartZ=0 EndX=0.941117 EndY=3.88771 EndZ=0
    g2: LineSegment StartX=0.941117 StartY=3.88771 StartZ=0 EndX=-2.8963 EndY=2.75889 EndZ=0
    g3: LineSegment StartX=-2.8963 StartY=2.75889 StartZ=0 EndX=-3.83742 EndY=-1.12882 EndZ=0
    g4: LineSegment StartX=-3.83742 StartY=-1.12882 StartZ=0 EndX=-0.941117 EndY=-3.88771 EndZ=0
    g5: LineSegment StartX=-0.941117 StartY=-3.88771 StartZ=0 EndX=2.8963 EndY=-2.75889 EndZ=0
    g6: Circle CenterX=0 CenterY=0 CenterZ=0 NormalX=0 NormalY=0 NormalZ=1 AngleXU=0 Radius=4
    g7: Circle CenterX=0 CenterY=0 CenterZ=0 NormalX=0 NormalY=0 NormalZ=1 AngleXU=0 Radius=2.5
  constraints (17):
    c: Coincident(g0,g1)
    c: Coincident(g1,g2)
    c: Coincident(g2,g3)
    c: Coincident(g3,g4)
    c: Coincident(g4,g5)
    c: Coincident(g5,g0)
    c: Equal(g0, g1-g5) x5
    c: PointOnObject(g0,g6)
    c: PointOnObject(g1,g6)
    c: PointOnObject(g2,g6)
    c: PointOnObject(g3,g6)
    c: PointOnObject(g4,g6)
    c: PointOnObject(g5,g6)
    c: Coincident(g6,g-1)
    c: Coincident(g7,g6)
    c: Radius(g7) = 2.5
    c: Radius(g6) = 4
FEATURE [PartDesign::Pad] Pad074
  Direction = (1,-2e-16,3e-16)
  Length = 3
  Length2 = 10
  Placement = pos=(0,0,0) rot=(0.57735,0.57735,0.57735;2.0944rad)
  Profile = -> Sketch190
  Type = 0
FEATURE [PartDesign::Pad] Pad075
  BaseFeature = -> Pad074
  Direction = (1,-2e-16,6e-16)
  Length = 15
  Length2 = 10
  Placement = pos=(0,0,0) rot=(0.57735,0.57735,0.57735;2.0944rad)
  Profile = -> Pad074 [Edge20]
  Type = 0
FEATURE [PartDesign::Body] Body175
  Group = -> [Sketch190,Pad074,Pad075]
  Origin = -> Origin225
  Tip = -> Pad075
FEATURE [App::Part] Part049  label="tornillo M5-15-004"
  Group = -> [Body175]
  Origin = -> Origin224
  Placement = pos=(10,141,98) rot=(0,1,0;1.5708rad)
FEATURE [Sketcher::SketchObject] Sketch191
  FullyConstrained = false
  MapMode = 5
  Placement = pos=(0,0,0) rot=(0.57735,0.57735,0.57735;2.0944rad)
  Support = -> [YZ_Plane221]
  sketch-geometry (8):
    g0: LineSegment StartX=2.8963 StartY=-2.75889 StartZ=0 EndX=3.83742 EndY=1.12882 EndZ=0
    g1: LineSegment StartX=3.83742 StartY=1.12882 StartZ=0 EndX=0.941117 EndY=3.88771 EndZ=0
    g2: LineSegment StartX=0.941117 StartY=3.88771 StartZ=0 EndX=-2.8963 EndY=2.75889 EndZ=0
    g3: LineSegment StartX=-2.8963 StartY=2.75889 StartZ=0 EndX=-3.83742 EndY=-1.12882 EndZ=0
    g4: LineSegment StartX=-3.83742 StartY=-1.12882 StartZ=0 EndX=-0.941117 EndY=-3.88771 EndZ=0
    g5: LineSegment StartX=-0.941117 StartY=-3.88771 StartZ=0 EndX=2.8963 EndY=-2.75889 EndZ=0
    g6: Circle CenterX=0 CenterY=0 CenterZ=0 NormalX=0 NormalY=0 NormalZ=1 AngleXU=0 Radius=4
    g7: Circle CenterX=0 CenterY=0 CenterZ=0 NormalX=0 NormalY=0 NormalZ=1 AngleXU=0 Radius=2.5
  constraints (17):
    c: Coincident(g0,g1)
    c: Coincident(g1,g2)
    c: Coincident(g2,g3)
    c: Coincident(g3,g4)
    c: Coincident(g4,g5)
    c: Coincident(g5,g0)
    c: Equal(g0, g1-g5) x5
    c: PointOnObject(g0,g6)
    c: PointOnObject(g1,g6)
    c: PointOnObject(g2,g6)
    c: PointOnObject(g3,g6)
    c: PointOnObject(g4,g6)
    c: PointOnObject(g5,g6)
    c: Coincident(g6,g-1)
    c: Coincident(g7,g6)
    c: Radius(g7) = 2.5
    c: Radius(g6) = 4
FEATURE [PartDesign::Pad] Pad076
  Direction = (1,-2e-16,3e-16)
  Length = 3
  Length2 = 10
  Placement = pos=(0,0,0) rot=(0.57735,0.57735,0.57735;2.0944rad)
  Profile = -> Sketch191
  Type = 0
FEATURE [PartDesign::Pad] Pad077
  BaseFeature = -> Pad076
  Direction = (1,-2e-16,6e-16)
  Length = 15
  Length2 = 10
  Placement = pos=(0,0,0) rot=(0.57735,0.57735,0.57735;2.0944rad)
  Profile = -> Pad076 [Edge20]
  Type = 0
FEATURE [PartDesign::Body] Body176
  Group = -> [Sketch191,Pad076,Pad077]
  Origin = -> Origin227
  Tip = -> Pad077
FEATURE [App::Part] Part050  label="tornillo M5-15-005"
  Group = -> [Body176]
  Origin = -> Origin226
  Placement = pos=(332,267,98) rot=(0,1,0;1.5708rad)
FEATURE [Sketcher::SketchObject] Sketch192
  FullyConstrained = false
  MapMode = 5
  Placement = pos=(0,0,0) rot=(0.57735,0.57735,0.57735;2.0944rad)
  Support = -> [YZ_Plane223]
  sketch-geometry (8):
    g0: LineSegment StartX=2.8963 StartY=-2.75889 StartZ=0 EndX=3.83742 EndY=1.12882 EndZ=0
    g1: LineSegment StartX=3.83742 StartY=1.12882 StartZ=0 EndX=0.941117 EndY=3.88771 EndZ=0
    g2: LineSegment StartX=0.941117 StartY=3.88771 StartZ=0 EndX=-2.8963 EndY=2.75889 EndZ=0
    g3: LineSegment StartX=-2.8963 StartY=2.75889 StartZ=0 EndX=-3.83742 EndY=-1.12882 EndZ=0
    g4: LineSegment StartX=-3.83742 StartY=-1.12882 StartZ=0 EndX=-0.941117 EndY=-3.88771 EndZ=0
    g5: LineSegment StartX=-0.941117 StartY=-3.88771 StartZ=0 EndX=2.8963 EndY=-2.75889 EndZ=0
    g6: Circle CenterX=0 CenterY=0 CenterZ=0 NormalX=0 NormalY=0 NormalZ=1 AngleXU=0 Radius=4
    g7: Circle CenterX=0 CenterY=0 CenterZ=0 NormalX=0 NormalY=0 NormalZ=1 AngleXU=0 Radius=2.5
  constraints (17):
    c: Coincident(g0,g1)
    c: Coincident(g1,g2)
    c: Coincident(g2,g3)
    c: Coincident(g3,g4)
    c: Coincident(g4,g5)
    c: Coincident(g5,g0)
    c: Equal(g0, g1-g5) x5
    c: PointOnObject(g0,g6)
    c: PointOnObject(g1,g6)
    c: PointOnObject(g2,g6)
    c: PointOnObject(g3,g6)
    c: PointOnObject(g4,g6)
    c: PointOnObject(g5,g6)
    c: Coincident(g6,g-1)
    c: Coincident(g7,g6)
    c: Radius(g7) = 2.5
    c: Radius(g6) = 4
FEATURE [PartDesign::Pad] Pad078
  Direction = (1,-2e-16,3e-16)
  Length = 3
  Length2 = 10
  Placement = pos=(0,0,0) rot=(0.57735,0.57735,0.57735;2.0944rad)
  Profile = -> Sketch192
  Type = 0
FEATURE [PartDesign::Pad] Pad079
  BaseFeature = -> Pad078
  Direction = (1,-2e-16,6e-16)
  Length = 15
  Length2 = 10
  Placement = pos=(0,0,0) rot=(0.57735,0.57735,0.57735;2.0944rad)
  Profile = -> Pad078 [Edge20]
  Type = 0
FEATURE [PartDesign::Body] Body177
  Group = -> [Sketch192,Pad078,Pad079]
  Origin = -> Origin229
  Tip = -> Pad079
FEATURE [App::Part] Part051  label="tornillo M5-15-006"
  Group = -> [Body177]
  Origin = -> Origin228
  Placement = pos=(332,225,98) rot=(0,1,0;1.5708rad)
FEATURE [Sketcher::SketchObject] Sketch193
  FullyConstrained = false
  MapMode = 5
  Placement = pos=(0,0,0) rot=(0.57735,0.57735,0.57735;2.0944rad)
  Support = -> [YZ_Plane225]
  sketch-geometry (8):
    g0: LineSegment StartX=2.8963 StartY=-2.75889 StartZ=0 EndX=3.83742 EndY=1.12882 EndZ=0
    g1: LineSegment StartX=3.83742 StartY=1.12882 StartZ=0 EndX=0.941117 EndY=3.88771 EndZ=0
    g2: LineSegment StartX=0.941117 StartY=3.88771 StartZ=0 EndX=-2.8963 EndY=2.75889 EndZ=0
    g3: LineSegment StartX=-2.8963 StartY=2.75889 StartZ=0 EndX=-3.83742 EndY=-1.12882 EndZ=0
    g4: LineSegment StartX=-3.83742 StartY=-1.12882 StartZ=0 EndX=-0.941117 EndY=-3.88771 EndZ=0
    g5: LineSegment StartX=-0.941117 StartY=-3.88771 StartZ=0 EndX=2.8963 EndY=-2.75889 EndZ=0
    g6: Circle CenterX=0 CenterY=0 CenterZ=0 NormalX=0 NormalY=0 NormalZ=1 AngleXU=0 Radius=4
    g7: Circle CenterX=0 CenterY=0 CenterZ=0 NormalX=0 NormalY=0 NormalZ=1 AngleXU=0 Radius=2.5
  constraints (17):
    c: Coincident(g0,g1)
    c: Coincident(g1,g2)
    c: Coincident(g2,g3)
    c: Coincident(g3,g4)
    c: Coincident(g4,g5)
    c: Coincident(g5,g0)
    c: Equal(g0, g1-g5) x5
    c: PointOnObject(g0,g6)
    c: PointOnObject(g1,g6)
    c: PointOnObject(g2,g6)
    c: PointOnObject(g3,g6)
    c: PointOnObject(g4,g6)
    c: PointOnObject(g5,g6)
    c: Coincident(g6,g-1)
    c: Coincident(g7,g6)
    c: Radius(g7) = 2.5
    c: Radius(g6) = 4
FEATURE [PartDesign::Pad] Pad080
  Direction = (1,-2e-16,3e-16)
  Length = 3
  Length2 = 10
  Placement = pos=(0,0,0) rot=(0.57735,0.57735,0.57735;2.0944rad)
  Profile = -> Sketch193
  Type = 0
FEATURE [PartDesign::Pad] Pad081
  BaseFeature = -> Pad080
  Direction = (1,-2e-16,6e-16)
  Length = 15
  Length2 = 10
  Placement = pos=(0,0,0) rot=(0.57735,0.57735,0.57735;2.0944rad)
  Profile = -> Pad080 [Edge20]
  Type = 0
FEATURE [PartDesign::Body] Body178
  Group = -> [Sketch193,Pad080,Pad081]
  Origin = -> Origin231
  Tip = -> Pad081
FEATURE [App::Part] Part052  label="tornillo M5-15-007"
  Group = -> [Body178]
  Origin = -> Origin230
  Placement = pos=(332,99,98) rot=(0,1,0;1.5708rad)
FEATURE [Sketcher::SketchObject] Sketch194
  FullyConstrained = false
  MapMode = 5
  Placement = pos=(0,0,0) rot=(0.57735,0.57735,0.57735;2.0944rad)
  Support = -> [YZ_Plane227]
  sketch-geometry (8):
    g0: LineSegment StartX=2.8963 StartY=-2.75889 StartZ=0 EndX=3.83742 EndY=1.12882 EndZ=0
    g1: LineSegment StartX=3.83742 StartY=1.12882 StartZ=0 EndX=0.941117 EndY=3.88771 EndZ=0
    g2: LineSegment StartX=0.941117 StartY=3.88771 StartZ=0 EndX=-2.8963 EndY=2.75889 EndZ=0
    g3: LineSegment StartX=-2.8963 StartY=2.75889 StartZ=0 EndX=-3.83742 EndY=-1.12882 EndZ=0
    g4: LineSegment StartX=-3.83742 StartY=-1.12882 StartZ=0 EndX=-0.941117 EndY=-3.88771 EndZ=0
    g5: LineSegment StartX=-0.941117 StartY=-3.88771 StartZ=0 EndX=2.8963 EndY=-2.75889 EndZ=0
    g6: Circle CenterX=0 CenterY=0 CenterZ=0 NormalX=0 NormalY=0 NormalZ=1 AngleXU=0 Radius=4
    g7: Circle CenterX=0 CenterY=0 CenterZ=0 NormalX=0 NormalY=0 NormalZ=1 AngleXU=0 Radius=2.5
  constraints (17):
    c: Coincident(g0,g1)
    c: Coincident(g1,g2)
    c: Coincident(g2,g3)
    c: Coincident(g3,g4)
    c: Coincident(g4,g5)
    c: Coincident(g5,g0)
    c: Equal(g0, g1-g5) x5
    c: PointOnObject(g0,g6)
    c: PointOnObject(g1,g6)
    c: PointOnObject(g2,g6)
    c: PointOnObject(g3,g6)
    c: PointOnObject(g4,g6)
    c: PointOnObject(g5,g6)
    c: Coincident(g6,g-1)
    c: Coincident(g7,g6)
    c: Radius(g7) = 2.5
    c: Radius(g6) = 4
FEATURE [PartDesign::Pad] Pad082
  Direction = (1,-2e-16,3e-16)
  Length = 3
  Length2 = 10
  Placement = pos=(0,0,0) rot=(0.57735,0.57735,0.57735;2.0944rad)
  Profile = -> Sketch194
  Type = 0
FEATURE [PartDesign::Pad] Pad083
  BaseFeature = -> Pad082
  Direction = (1,-2e-16,6e-16)
  Length = 15
  Length2 = 10
  Placement = pos=(0,0,0) rot=(0.57735,0.57735,0.57735;2.0944rad)
  Profile = -> Pad082 [Edge20]
  Type = 0
FEATURE [PartDesign::Body] Body179
  Group = -> [Sketch194,Pad082,Pad083]
  Origin = -> Origin233
  Tip = -> Pad083
FEATURE [App::Part] Part053  label="tornillo M5-15-008"
  Group = -> [Body179]
  Origin = -> Origin232
  Placement = pos=(332,141,98) rot=(0,1,0;1.5708rad)
FEATURE [Sketcher::SketchObject] Sketch195
  FullyConstrained = false
  MapMode = 5
  Placement = pos=(0,0,0) rot=(0.57735,0.57735,0.57735;2.0944rad)
  Support = -> [YZ_Plane229]
  sketch-geometry (8):
    g0: LineSegment StartX=2.8963 StartY=-2.75889 StartZ=0 EndX=3.83742 EndY=1.12882 EndZ=0
    g1: LineSegment StartX=3.83742 StartY=1.12882 StartZ=0 EndX=0.941117 EndY=3.88771 EndZ=0
    g2: LineSegment StartX=0.941117 StartY=3.88771 StartZ=0 EndX=-2.8963 EndY=2.75889 EndZ=0
    g3: LineSegment StartX=-2.8963 StartY=2.75889 StartZ=0 EndX=-3.83742 EndY=-1.12882 EndZ=0
    g4: LineSegment StartX=-3.83742 StartY=-1.12882 StartZ=0 EndX=-0.941117 EndY=-3.88771 EndZ=0
    g5: LineSegment StartX=-0.941117 StartY=-3.88771 StartZ=0 EndX=2.8963 EndY=-2.75889 EndZ=0
    g6: Circle CenterX=0 CenterY=0 CenterZ=0 NormalX=0 NormalY=0 NormalZ=1 AngleXU=0 Radius=4
    g7: Circle CenterX=0 CenterY=0 CenterZ=0 NormalX=0 NormalY=0 NormalZ=1 AngleXU=0 Radius=2.5
  constraints (17):
    c: Coincident(g0,g1)
    c: Coincident(g1,g2)
    c: Coincident(g2,g3)
    c: Coincident(g3,g4)
    c: Coincident(g4,g5)
    c: Coincident(g5,g0)
    c: Equal(g0, g1-g5) x5
    c: PointOnObject(g0,g6)
    c: PointOnObject(g1,g6)
    c: PointOnObject(g2,g6)
    c: PointOnObject(g3,g6)
    c: PointOnObject(g4,g6)
    c: PointOnObject(g5,g6)
    c: Coincident(g6,g-1)
    c: Coincident(g7,g6)
    c: Radius(g7) = 2.5
    c: Radius(g6) = 4
FEATURE [PartDesign::Pad] Pad084
  Direction = (1,-2e-16,3e-16)
  Length = 3
  Length2 = 10
  Placement = pos=(0,0,0) rot=(0.57735,0.57735,0.57735;2.0944rad)
  Profile = -> Sketch195
  Type = 0
FEATURE [PartDesign::Pad] Pad085
  BaseFeature = -> Pad084
  Direction = (1,-2e-16,6e-16)
  Length = 15
  Length2 = 10
  Placement = pos=(0,0,0) rot=(0.57735,0.57735,0.57735;2.0944rad)
  Profile = -> Pad084 [Edge20]
  Type = 0
FEATURE [PartDesign::Body] Body180
  Group = -> [Sketch195,Pad084,Pad085]
  Origin = -> Origin235
  Tip = -> Pad085
FEATURE [App::Part] Part054  label="tornillo M5-15-009"
  Group = -> [Body180]
  Origin = -> Origin234
  Placement = pos=(313,101,79) rot=(0,0,1;0rad)
FEATURE [Sketcher::SketchObject] Sketch196
  FullyConstrained = false
  MapMode = 5
  Placement = pos=(0,0,0) rot=(0.57735,0.57735,0.57735;2.0944rad)
  Support = -> [YZ_Plane231]
  sketch-geometry (8):
    g0: LineSegment StartX=2.8963 StartY=-2.75889 StartZ=0 EndX=3.83742 EndY=1.12882 EndZ=0
    g1: LineSegment StartX=3.83742 StartY=1.12882 StartZ=0 EndX=0.941117 EndY=3.88771 EndZ=0
    g2: LineSegment StartX=0.941117 StartY=3.88771 StartZ=0 EndX=-2.8963 EndY=2.75889 EndZ=0
    g3: LineSegment StartX=-2.8963 StartY=2.75889 StartZ=0 EndX=-3.83742 EndY=-1.12882 EndZ=0
    g4: LineSegment StartX=-3.83742 StartY=-1.12882 StartZ=0 EndX=-0.941117 EndY=-3.88771 EndZ=0
    g5: LineSegment StartX=-0.941117 StartY=-3.88771 StartZ=0 EndX=2.8963 EndY=-2.75889 EndZ=0
    g6: Circle CenterX=0 CenterY=0 CenterZ=0 NormalX=0 NormalY=0 NormalZ=1 AngleXU=0 Radius=4
    g7: Circle CenterX=0 CenterY=0 CenterZ=0 NormalX=0 NormalY=0 NormalZ=1 AngleXU=0 Radius=2.5
  constraints (17):
    c: Coincident(g0,g1)
    c: Coincident(g1,g2)
    c: Coincident(g2,g3)
    c: Coincident(g3,g4)
    c: Coincident(g4,g5)
    c: Coincident(g5,g0)
    c: Equal(g0, g1-g5) x5
    c: PointOnObject(g0,g6)
    c: PointOnObject(g1,g6)
    c: PointOnObject(g2,g6)
    c: PointOnObject(g3,g6)
    c: PointOnObject(g4,g6)
    c: PointOnObject(g5,g6)
    c: Coincident(g6,g-1)
    c: Coincident(g7,g6)
    c: Radius(g7) = 2.5
    c: Radius(g6) = 4
FEATURE [PartDesign::Pad] Pad086
  Direction = (1,-2e-16,3e-16)
  Length = 3
  Length2 = 10
  Placement = pos=(0,0,0) rot=(0.57735,0.57735,0.57735;2.0944rad)
  Profile = -> Sketch196
  Type = 0
FEATURE [PartDesign::Pad] Pad087
  BaseFeature = -> Pad086
  Direction = (1,-2e-16,6e-16)
  Length = 15
  Length2 = 10
  Placement = pos=(0,0,0) rot=(0.57735,0.57735,0.57735;2.0944rad)
  Profile = -> Pad086 [Edge20]
  Type = 0
FEATURE [PartDesign::Body] Body181
  Group = -> [Sketch196,Pad086,Pad087]
  Origin = -> Origin237
  Tip = -> Pad087
FEATURE [App::Part] Part055  label="tornillo M5-15-010"
  Group = -> [Body181]
  Origin = -> Origin236
  Placement = pos=(26,101,79) rot=(0,0,1;3.14159rad)
FEATURE [Sketcher::SketchObject] Sketch197
  FullyConstrained = false
  MapMode = 5
  Placement = pos=(0,0,0) rot=(0.57735,0.57735,0.57735;2.0944rad)
  Support = -> [YZ_Plane233]
  sketch-geometry (8):
    g0: LineSegment StartX=2.8963 StartY=-2.75889 StartZ=0 EndX=3.83742 EndY=1.12882 EndZ=0
    g1: LineSegment StartX=3.83742 StartY=1.12882 StartZ=0 EndX=0.941117 EndY=3.88771 EndZ=0
    g2: LineSegment StartX=0.941117 StartY=3.88771 StartZ=0 EndX=-2.8963 EndY=2.75889 EndZ=0
    g3: LineSegment StartX=-2.8963 StartY=2.75889 StartZ=0 EndX=-3.83742 EndY=-1.12882 EndZ=0
    g4: LineSegment StartX=-3.83742 StartY=-1.12882 StartZ=0 EndX=-0.941117 EndY=-3.88771 EndZ=0
    g5: LineSegment StartX=-0.941117 StartY=-3.88771 StartZ=0 EndX=2.8963 EndY=-2.75889 EndZ=0
    g6: Circle CenterX=0 CenterY=0 CenterZ=0 NormalX=0 NormalY=0 NormalZ=1 AngleXU=0 Radius=4
    g7: Circle CenterX=0 CenterY=0 CenterZ=0 NormalX=0 NormalY=0 NormalZ=1 AngleXU=0 Radius=2.5
  constraints (17):
    c: Coincident(g0,g1)
    c: Coincident(g1,g2)
    c: Coincident(g2,g3)
    c: Coincident(g3,g4)
    c: Coincident(g4,g5)
    c: Coincident(g5,g0)
    c: Equal(g0, g1-g5) x5
    c: PointOnObject(g0,g6)
    c: PointOnObject(g1,g6)
    c: PointOnObject(g2,g6)
    c: PointOnObject(g3,g6)
    c: PointOnObject(g4,g6)
    c: PointOnObject(g5,g6)
    c: Coincident(g6,g-1)
    c: Coincident(g7,g6)
    c: Radius(g7) = 2.5
    c: Radius(g6) = 4
FEATURE [PartDesign::Pad] Pad088
  Direction = (1,-2e-16,3e-16)
  Length = 3
  Length2 = 10
  Placement = pos=(0,0,0) rot=(0.57735,0.57735,0.57735;2.0944rad)
  Profile = -> Sketch197
  Type = 0
FEATURE [PartDesign::Pad] Pad089
  BaseFeature = -> Pad088
  Direction = (1,-2e-16,6e-16)
  Length = 15
  Length2 = 10
  Placement = pos=(0,0,0) rot=(0.57735,0.57735,0.57735;2.0944rad)
  Profile = -> Pad088 [Edge20]
  Type = 0
FEATURE [PartDesign::Body] Body182
  Group = -> [Sketch197,Pad088,Pad089]
  Origin = -> Origin239
  Tip = -> Pad089
FEATURE [App::Part] Part056  label="tornillo M5-15-011"
  Group = -> [Body182]
  Origin = -> Origin238
  Placement = pos=(26,139,79) rot=(0,0,1;3.14159rad)
FEATURE [Sketcher::SketchObject] Sketch198
  FullyConstrained = false
  MapMode = 5
  Placement = pos=(0,0,0) rot=(0.57735,0.57735,0.57735;2.0944rad)
  Support = -> [YZ_Plane235]
  sketch-geometry (8):
    g0: LineSegment StartX=2.8963 StartY=-2.75889 StartZ=0 EndX=3.83742 EndY=1.12882 EndZ=0
    g1: LineSegment StartX=3.83742 StartY=1.12882 StartZ=0 EndX=0.941117 EndY=3.88771 EndZ=0
    g2: LineSegment StartX=0.941117 StartY=3.88771 StartZ=0 EndX=-2.8963 EndY=2.75889 EndZ=0
    g3: LineSegment StartX=-2.8963 StartY=2.75889 StartZ=0 EndX=-3.83742 EndY=-1.12882 EndZ=0
    g4: LineSegment StartX=-3.83742 StartY=-1.12882 StartZ=0 EndX=-0.941117 EndY=-3.88771 EndZ=0
    g5: LineSegment StartX=-0.941117 StartY=-3.88771 StartZ=0 EndX=2.8963 EndY=-2.75889 EndZ=0
    g6: Circle CenterX=0 CenterY=0 CenterZ=0 NormalX=0 NormalY=0 NormalZ=1 AngleXU=0 Radius=4
    g7: Circle CenterX=0 CenterY=0 CenterZ=0 NormalX=0 NormalY=0 NormalZ=1 AngleXU=0 Radius=2.5
  constraints (17):
    c: Coincident(g0,g1)
    c: Coincident(g1,g2)
    c: Coincident(g2,g3)
    c: Coincident(g3,g4)
    c: Coincident(g4,g5)
    c: Coincident(g5,g0)
    c: Equal(g0, g1-g5) x5
    c: PointOnObject(g0,g6)
    c: PointOnObject(g1,g6)
    c: PointOnObject(g2,g6)
    c: PointOnObject(g3,g6)
    c: PointOnObject(g4,g6)
    c: PointOnObject(g5,g6)
    c: Coincident(g6,g-1)
    c: Coincident(g7,g6)
    c: Radius(g7) = 2.5
    c: Radius(g6) = 4
FEATURE [PartDesign::Pad] Pad090
  Direction = (1,-2e-16,3e-16)
  Length = 3
  Length2 = 10
  Placement = pos=(0,0,0) rot=(0.57735,0.57735,0.57735;2.0944rad)
  Profile = -> Sketch198
  Type = 0
FEATURE [PartDesign::Pad] Pad091
  BaseFeature = -> Pad090
  Direction = (1,-2e-16,6e-16)
  Length = 15
  Length2 = 10
  Placement = pos=(0,0,0) rot=(0.57735,0.57735,0.57735;2.0944rad)
  Profile = -> Pad090 [Edge20]
  Type = 0
FEATURE [PartDesign::Body] Body183
  Group = -> [Sketch198,Pad090,Pad091]
  Origin = -> Origin241
  Tip = -> Pad091
FEATURE [App::Part] Part057  label="tornillo M5-15-012"
  Group = -> [Body183]
  Origin = -> Origin240
  Placement = pos=(313,139,79) rot=(0,0,1;0rad)
FEATURE [Sketcher::SketchObject] Sketch199
  FullyConstrained = true
  MapMode = 5
  Placement = pos=(0,0,0) rot=(1,0,0;1.5708rad)
  Support = -> [XZ_Plane237]
  sketch-geometry (2):
    g0: Circle CenterX=0 CenterY=0 CenterZ=0 NormalX=0 NormalY=0 NormalZ=1 AngleXU=0 Radius=3
    g1: Circle CenterX=0 CenterY=0 CenterZ=0 NormalX=0 NormalY=0 NormalZ=1 AngleXU=0 Radius=9
  constraints (4):
    c: Coincident(g0,g-1)
    c: Coincident(g1,g0)
    c: Radius(g1) = 9
    c: Diameter(g0) = 6
FEATURE [PartDesign::Pad] Pad092
  Direction = (0,-1,2e-16)
  Length = 1
  Length2 = 10
  Placement = pos=(0,0,0) rot=(1,0,0;1.5708rad)
  Profile = -> Sketch199
  Type = 0
FEATURE [PartDesign::Body] Body184
  Group = -> [Sketch199,Pad092]
  Origin = -> Origin243
  Tip = -> Pad092
FEATURE [App::Part] Part058  label="Arandela M6-001"
  Group = -> [Body184]
  Origin = -> Origin242
  Placement = pos=(10,0,10) rot=(0,0,1;0rad)
FEATURE [Sketcher::SketchObject] Sketch200
  FullyConstrained = true
  MapMode = 5
  Placement = pos=(0,0,0) rot=(1,0,0;1.5708rad)
  Support = -> [XZ_Plane239]
  sketch-geometry (2):
    g0: Circle CenterX=0 CenterY=0 CenterZ=0 NormalX=0 NormalY=0 NormalZ=1 AngleXU=0 Radius=3
    g1: Circle CenterX=0 CenterY=0 CenterZ=0 NormalX=0 NormalY=0 NormalZ=1 AngleXU=0 Radius=9
  constraints (4):
    c: Coincident(g0,g-1)
    c: Coincident(g1,g0)
    c: Radius(g1) = 9
    c: Diameter(g0) = 6
FEATURE [PartDesign::Pad] Pad093
  Direction = (0,-1,2e-16)
  Length = 1
  Length2 = 10
  Placement = pos=(0,0,0) rot=(1,0,0;1.5708rad)
  Profile = -> Sketch200
  Type = 0
FEATURE [PartDesign::Body] Body185
  Group = -> [Sketch200,Pad093]
  Origin = -> Origin245
  Tip = -> Pad093
FEATURE [App::Part] Part059  label="Arandela M6-002"
  Group = -> [Body185]
  Origin = -> Origin244
  Placement = pos=(10,0,181) rot=(0,0,1;0rad)
FEATURE [Sketcher::SketchObject] Sketch201
  FullyConstrained = true
  MapMode = 5
  Placement = pos=(0,0,0) rot=(1,0,0;1.5708rad)
  Support = -> [XZ_Plane241]
  sketch-geometry (2):
    g0: Circle CenterX=0 CenterY=0 CenterZ=0 NormalX=0 NormalY=0 NormalZ=1 AngleXU=0 Radius=3
    g1: Circle CenterX=0 CenterY=0 CenterZ=0 NormalX=0 NormalY=0 NormalZ=1 AngleXU=0 Radius=9
  constraints (4):
    c: Coincident(g0,g-1)
    c: Coincident(g1,g0)
    c: Radius(g1) = 9
    c: Diameter(g0) = 6
FEATURE [PartDesign::Pad] Pad094
  Direction = (0,-1,2e-16)
  Length = 1
  Length2 = 10
  Placement = pos=(0,0,0) rot=(1,0,0;1.5708rad)
  Profile = -> Sketch201
  Type = 0
FEATURE [PartDesign::Body] Body186
  Group = -> [Sketch201,Pad094]
  Origin = -> Origin247
  Tip = -> Pad094
FEATURE [App::Part] Part060  label="Arandela M6-003"
  Group = -> [Body186]
  Origin = -> Origin246
  Placement = pos=(330,0,181) rot=(0,0,1;0rad)
FEATURE [Sketcher::SketchObject] Sketch202
  FullyConstrained = true
  MapMode = 5
  Placement = pos=(0,0,0) rot=(1,0,0;1.5708rad)
  Support = -> [XZ_Plane243]
  sketch-geometry (2):
    g0: Circle CenterX=0 CenterY=0 CenterZ=0 NormalX=0 NormalY=0 NormalZ=1 AngleXU=0 Radius=3
    g1: Circle CenterX=0 CenterY=0 CenterZ=0 NormalX=0 NormalY=0 NormalZ=1 AngleXU=0 Radius=9
  constraints (4):
    c: Coincident(g0,g-1)
    c: Coincident(g1,g0)
    c: Radius(g1) = 9
    c: Diameter(g0) = 6
FEATURE [PartDesign::Pad] Pad095
  Direction = (0,-1,2e-16)
  Length = 1
  Length2 = 10
  Placement = pos=(0,0,0) rot=(1,0,0;1.5708rad)
  Profile = -> Sketch202
  Type = 0
FEATURE [PartDesign::Body] Body187
  Group = -> [Sketch202,Pad095]
  Origin = -> Origin249
  Tip = -> Pad095
FEATURE [App::Part] Part061  label="Arandela M6-004"
  Group = -> [Body187]
  Origin = -> Origin248
  Placement = pos=(330,0,9) rot=(0,0,1;0rad)
FEATURE [Sketcher::SketchObject] Sketch203
  FullyConstrained = true
  MapMode = 5
  Placement = pos=(0,0,0) rot=(1,0,0;1.5708rad)
  Support = -> [XZ_Plane245]
  sketch-geometry (2):
    g0: Circle CenterX=0 CenterY=0 CenterZ=0 NormalX=0 NormalY=0 NormalZ=1 AngleXU=0 Radius=3
    g1: Circle CenterX=0 CenterY=0 CenterZ=0 NormalX=0 NormalY=0 NormalZ=1 AngleXU=0 Radius=9
  constraints (4):
    c: Coincident(g0,g-1)
    c: Coincident(g1,g0)
    c: Radius(g1) = 9
    c: Diameter(g0) = 6
FEATURE [PartDesign::Pad] Pad096
  Direction = (0,-1,2e-16)
  Length = 1
  Length2 = 10
  Placement = pos=(0,0,0) rot=(1,0,0;1.5708rad)
  Profile = -> Sketch203
  Type = 0
FEATURE [PartDesign::Body] Body188
  Group = -> [Sketch203,Pad096]
  Origin = -> Origin251
  Tip = -> Pad096
FEATURE [App::Part] Part062  label="Arandela M6-005"
  Group = -> [Body188]
  Origin = -> Origin250
  Placement = pos=(330,341,9) rot=(0,0,1;0rad)
FEATURE [Sketcher::SketchObject] Sketch204
  FullyConstrained = true
  MapMode = 5
  Placement = pos=(0,0,0) rot=(1,0,0;1.5708rad)
  Support = -> [XZ_Plane247]
  sketch-geometry (2):
    g0: Circle CenterX=0 CenterY=0 CenterZ=0 NormalX=0 NormalY=0 NormalZ=1 AngleXU=0 Radius=3
    g1: Circle CenterX=0 CenterY=0 CenterZ=0 NormalX=0 NormalY=0 NormalZ=1 AngleXU=0 Radius=9
  constraints (4):
    c: Coincident(g0,g-1)
    c: Coincident(g1,g0)
    c: Radius(g1) = 9
    c: Diameter(g0) = 6
FEATURE [PartDesign::Pad] Pad097
  Direction = (0,-1,2e-16)
  Length = 1
  Length2 = 10
  Placement = pos=(0,0,0) rot=(1,0,0;1.5708rad)
  Profile = -> Sketch204
  Type = 0
FEATURE [PartDesign::Body] Body189
  Group = -> [Sketch204,Pad097]
  Origin = -> Origin253
  Tip = -> Pad097
FEATURE [App::Part] Part063  label="Arandela M6-006"
  Group = -> [Body189]
  Origin = -> Origin252
  Placement = pos=(10,341,180) rot=(0,0,1;0rad)
FEATURE [Sketcher::SketchObject] Sketch205
  FullyConstrained = true
  MapMode = 5
  Placement = pos=(0,0,0) rot=(1,0,0;1.5708rad)
  Support = -> [XZ_Plane249]
  sketch-geometry (2):
    g0: Circle CenterX=0 CenterY=0 CenterZ=0 NormalX=0 NormalY=0 NormalZ=1 AngleXU=0 Radius=3
    g1: Circle CenterX=0 CenterY=0 CenterZ=0 NormalX=0 NormalY=0 NormalZ=1 AngleXU=0 Radius=9
  constraints (4):
    c: Coincident(g0,g-1)
    c: Coincident(g1,g0)
    c: Radius(g1) = 9
    c: Diameter(g0) = 6
FEATURE [PartDesign::Pad] Pad098
  Direction = (0,-1,2e-16)
  Length = 1
  Length2 = 10
  Placement = pos=(0,0,0) rot=(1,0,0;1.5708rad)
  Profile = -> Sketch205
  Type = 0
FEATURE [PartDesign::Body] Body190
  Group = -> [Sketch205,Pad098]
  Origin = -> Origin255
  Tip = -> Pad098
FEATURE [App::Part] Part064  label="Arandela M6-007"
  Group = -> [Body190]
  Origin = -> Origin254
  Placement = pos=(330,341,180) rot=(0,0,1;0rad)
FEATURE [Sketcher::SketchObject] Sketch206
  FullyConstrained = true
  MapMode = 5
  Placement = pos=(0,0,0) rot=(1,0,0;1.5708rad)
  Support = -> [XZ_Plane251]
  sketch-geometry (2):
    g0: Circle CenterX=0 CenterY=0 CenterZ=0 NormalX=0 NormalY=0 NormalZ=1 AngleXU=0 Radius=3
    g1: Circle CenterX=0 CenterY=0 CenterZ=0 NormalX=0 NormalY=0 NormalZ=1 AngleXU=0 Radius=9
  constraints (4):
    c: Coincident(g0,g-1)
    c: Coincident(g1,g0)
    c: Radius(g1) = 9
    c: Diameter(g0) = 6
FEATURE [PartDesign::Pad] Pad099
  Direction = (0,-1,2e-16)
  Length = 1
  Length2 = 10
  Placement = pos=(0,0,0) rot=(1,0,0;1.5708rad)
  Profile = -> Sketch206
  Type = 0
FEATURE [PartDesign::Body] Body191
  Group = -> [Sketch206,Pad099]
  Origin = -> Origin257
  Tip = -> Pad099
FEATURE [App::Part] Part065  label="Arandela M6-008"
  Group = -> [Body191]
  Origin = -> Origin256
  Placement = pos=(10,341,10) rot=(0,0,1;0rad)
FEATURE [Sketcher::SketchObject] Sketch207
  FullyConstrained = true
  MapMode = 5
  Placement = pos=(0,0,0) rot=(0.57735,0.57735,0.57735;2.0944rad)
  Support = -> [YZ_Plane253]
  sketch-geometry (4):
    g0: LineSegment StartX=0 StartY=0 StartZ=0 EndX=340 EndY=0 EndZ=0
    g1: LineSegment StartX=340 StartY=0 StartZ=0 EndX=340 EndY=-30 EndZ=0
    g2: LineSegment StartX=340 StartY=-30 StartZ=0 EndX=0 EndY=-30 EndZ=0
    g3: LineSegment StartX=0 StartY=-30 StartZ=0 EndX=0 EndY=0 EndZ=0
  constraints (11):
    c: Coincident(g0,g1)
    c: Coincident(g1,g2)
    c: Coincident(g2,g3)
    c: Coincident(g3,g0)
    c: Horizontal(g0)
    c: Horizontal(g2)
    c: Vertical(g1)
    c: Vertical(g3)
    c: Coincident(g0,g-1)
    c: DistanceY(g2,g0) = 30
    c: DistanceX(g2,g1) = 340
FEATURE [PartDesign::Pad] Pad100
  Direction = (1,-2e-16,3e-16)
  Length = 2
  Length2 = 10
  Placement = pos=(0,0,0) rot=(0.57735,0.57735,0.57735;2.0944rad)
  Profile = -> Sketch207
  Type = 0
FEATURE [PartDesign::Body] Body192
  Group = -> [Sketch207,Pad100]
  Origin = -> Origin259
  Tip = -> Pad100
FEATURE [Sketcher::SketchObject] Sketch208
  FullyConstrained = false
  MapMode = 5
  Support = -> [XY_Plane254]
  sketch-geometry (9):
    g0: LineSegment StartX=-50 StartY=12 StartZ=0 EndX=-50 EndY=328 EndZ=0
    g1: LineSegment StartX=2 StartY=339.974 StartZ=0 EndX=2 EndY=0 EndZ=0
    g2: GeomPoint X=-50 Y=328 Z=0
    g3: LineSegment StartX=-50 StartY=328 StartZ=0 EndX=2 EndY=340 EndZ=0
    g4: GeomPoint X=-50 Y=12 Z=0
    g5: LineSegment StartX=2 StartY=0 StartZ=0 EndX=-50 EndY=12 EndZ=0
    g6: GeomPoint X=2 Y=0 Z=0
    g7: GeomPoint X=2 Y=340 Z=0
    g8: LineSegment StartX=2 StartY=340 StartZ=0 EndX=2 EndY=339.974 EndZ=0
  constraints (18):
    c: Vertical(g0)
    c: Vertical(g1)
    c: PointOnObject(g2,g0)
    c: Coincident(g3,g2)
    c: PointOnObject(g0,g3)
    c: PointOnObject(g4,g0)
    c: Coincident(g5,g4)
    c: PointOnObject(g0,g5)
    c: PointOnObject(g6,g-1)
    c: DistanceX(g-1,g6) = 2
    c: Coincident(g5,g6)
    c: Coincident(g5,g1)
    c: DistanceX(g-1,g7) = 2
    c: DistanceY(g-1,g7) = 340
    c: Coincident(g8,g7)
    c: Coincident(g8,g1)
    c: Vertical(g8)
    c: Coincident(g3,g8)
FEATURE [PartDesign::Pad] Pad101
  Direction = (1,1,1)
  Length = 2
  Length2 = 10
  Profile = -> Sketch208
  Type = 0
FEATURE [PartDesign::Body] Body193
  Group = -> [Sketch208,Pad101]
  Origin = -> Origin260
  Placement = pos=(2,0,0) rot=(0,0,1;0rad)
  Tip = -> Pad101
FEATURE [App::Part] Part066  label="baseMotores"
  Group = -> [Body192,Body193]
  Origin = -> Origin258
  Placement = pos=(342,340,81) rot=(0,0,1;3.14159rad)
FEATURE [Sketcher::SketchObject] Sketch209
  FullyConstrained = false
  MapMode = 5
  Support = -> [XY_Plane256]
  sketch-geometry (8):
    g0: ArcOfCircle CenterX=0 CenterY=0 CenterZ=0 NormalX=0 NormalY=0 NormalZ=1 AngleXU=0 Radius=60 StartAngle=3.30904 EndAngle=6.11574
    g1: LineSegment StartX=-59.1608 StartY=10 StartZ=0 EndX=-48 EndY=10 EndZ=0
    g2: LineSegment StartX=-59.1608 StartY=-10 StartZ=0 EndX=-48 EndY=-10 EndZ=0
    g3: LineSegment StartX=-48 StartY=10 StartZ=0 EndX=-48 EndY=-10 EndZ=0
    g4: LineSegment StartX=48 StartY=10 StartZ=0 EndX=48 EndY=-10 EndZ=0
    g5: ArcOfCircle CenterX=0 CenterY=0 CenterZ=0 NormalX=0 NormalY=0 NormalZ=1 AngleXU=0 Radius=60 StartAngle=0.167448 EndAngle=2.97414
    g6: LineSegment StartX=48 StartY=10 StartZ=0 EndX=59.1608 EndY=10 EndZ=0
    g7: LineSegment StartX=48 StartY=-10 StartZ=0 EndX=59.1608 EndY=-10 EndZ=0
  constraints (16):
    c: Coincident(g0,g-1)
    c: Diameter(g0) = 120
    c: Horizontal(g1)
    c: Horizontal(g2)
    c: Vertical(g3)
    c: Vertical(g4)
    c: Coincident(g1,g5)
    c: Coincident(g2,g0)
    c: Equal(g0,g5)
    c: Coincident(g0,g5)
    c: Coincident(g6,g5)
    c: Coincident(g7,g0)
    c: Coincident(g1,g3)
    c: Coincident(g6,g4)
    c: Coincident(g2,g3)
    c: Coincident(g7,g4)
FEATURE [PartDesign::Pad] Pad102
  Direction = (0,0,1)
  Length = 8
  Length2 = 10
  Profile = -> Sketch209
  Type = 0
FEATURE [PartDesign::Body] Body194
  Group = -> [Sketch209,Pad102]
  Origin = -> Origin262
  Tip = -> Pad102
FEATURE [App::Part] Part067  label="rueda-002"
  Group = -> [Body194]
  Origin = -> Origin261
  Placement = pos=(0,0,0) rot=(0,1,0;1.5708rad)
FEATURE [Sketcher::SketchObject] Sketch211
  FullyConstrained = true
  MapMode = 5
  Support = -> [XY_Plane260]
  sketch-geometry (12):
    g0: ArcOfCircle CenterX=0 CenterY=0 CenterZ=0 NormalX=0 NormalY=0 NormalZ=1 AngleXU=0 Radius=60 StartAngle=1.77951 EndAngle=2.93288
    g1: GeomPoint X=0 Y=60 Z=0
    g2: GeomPoint X=0 Y=-60 Z=0
    g3: GeomPoint X=-60 Y=0 Z=0
    g4: GeomPoint X=60 Y=0 Z=0
    g5: ArcOfCircle CenterX=-60 CenterY=0 CenterZ=0 NormalX=0 NormalY=0 NormalZ=1 AngleXU=0 Radius=12.5 StartAngle=4.81674 EndAngle=7.74963
    g6: ArcOfCircle CenterX=0 CenterY=60 CenterZ=0 NormalX=0 NormalY=0 NormalZ=1 AngleXU=0 Radius=12.5 StartAngle=3.24595 EndAngle=6.17883
    g7: ArcOfCircle CenterX=60 CenterY=0 CenterZ=0 NormalX=0 NormalY=0 NormalZ=1 AngleXU=0 Radius=12.5 StartAngle=1.67515 EndAngle=4.60803
    g8: ArcOfCircle CenterX=0 CenterY=-60 CenterZ=0 NormalX=0 NormalY=0 NormalZ=1 AngleXU=0 Radius=12.5 StartAngle=0.104356 EndAngle=3.03724
    g9: ArcOfCircle CenterX=0 CenterY=0 CenterZ=0 NormalX=0 NormalY=0 NormalZ=1 AngleXU=0 Radius=60 StartAngle=3.3503 EndAngle=4.50368
    g10: ArcOfCircle CenterX=0 CenterY=0 CenterZ=0 NormalX=0 NormalY=0 NormalZ=1 AngleXU=0 Radius=60 StartAngle=4.9211 EndAngle=6.07447
    g11: ArcOfCircle CenterX=0 CenterY=0 CenterZ=0 NormalX=0 NormalY=0 NormalZ=1 AngleXU=0 Radius=60 StartAngle=0.208712 EndAngle=1.36208
  constraints (32):
    c: Coincident(g0,g-1)
    c: PointOnObject(g1,g0)
    c: PointOnObject(g2,g0)
    c: PointOnObject(g3,g0)
    c: PointOnObject(g4,g0)
    c: DistanceY(g-1,g3) = 0
    c: DistanceY(g-1,g4) = 0
    c: DistanceX(g1,g-1) = 0
    c: DistanceX(g2,g-1) = 0
    c: Coincident(g5,g3)
    c: Diameter(g5) = 25
    c: Coincident(g6,g1)
    c: Coincident(g7,g4)
    c: Coincident(g8,g2)
    c: Equal(g7,g6)
    c: Equal(g7,g8)
    c: Diameter(g7) = 25
    c: Coincident(g11,g6)
    c: Coincident(g0,g6)
    c: Equal(g0,g9)
    c: Coincident(g0,g5)
    c: Coincident(g9,g5)
    c: Coincident(g0,g9)
    c: Equal(g9,g10)
    c: Coincident(g9,g10)
    c: Coincident(g8,g9)
    c: Coincident(g8,g10)
    c: Equal(g10,g11)
    c: Coincident(g10,g11)
    c: Coincident(g7,g10)
    c: Coincident(g7,g11)
    c: Diameter(g0) = 120
FEATURE [PartDesign::Pad] Pad104
  Direction = (0,0,1)
  Length = 8
  Length2 = 10
  Profile = -> Sketch211
  Type = 0
FEATURE [PartDesign::Body] Body196
  Group = -> [Sketch211,Pad104]
  Origin = -> Origin266
  Tip = -> Pad104
FEATURE [App::Part] Part069  label="rueda-003"
  Group = -> [Body196]
  Origin = -> Origin265
  Placement = pos=(0,0,0) rot=(0,1,0;1.5708rad)
FEATURE [App::LinkGroup] LinkGroup  label="2020-base"
  ElementList = -> [Part003,Part002,Part001,Part]
  LinkMode = 0
FEATURE [App::LinkGroup] LinkGroup001  label="2020-columnas"
  ElementList = -> [Part004,Part005,Part006,Part007]
  LinkMode = 0
FEATURE [App::LinkGroup] LinkGroup002  label="2020-techo"
  ElementList = -> [Part008,Part009,Part010,Part011]
  LinkMode = 0
FEATURE [App::LinkGroup] LinkGroup003  label="2020-bases de ejes"
  ElementList = -> [Part012,Part013]
  LinkMode = 0
FEATURE [App::LinkGroup] LinkGroup004  label="soportes rulemanes"
  ElementList = -> [Part014,Part015,Part016,Part017,Part018,Part019]
  LinkMode = 0
FEATURE [App::LinkGroup] LinkGroup005  label="Motores"
  ElementList = -> [Part020,Part027]
  LinkMode = 0
FEATURE [App::LinkGroup] LinkGroup006  label="ejes"
  ElementList = -> [Part034,Part035,Part036]
  LinkMode = 0
  Placement = pos=(31,4.57764e-05,0) rot=(0,0,1;0rad)
FEATURE [App::LinkGroup] LinkGroup007  label="tornillos M6 estructura"
  ElementList = -> [Part038,Part039,Part040,Part041,Part042,Part043,Part044,Part045]
  LinkMode = 0
FEATURE [App::LinkGroup] LinkGroup008  label="tornillos M5 rulemanes"
  ElementList = -> [Part046,Part047,Part048,Part049,Part050,Part051,Part052,Part053,Part054,Part055,Part056,Part057]
  LinkMode = 0
FEATURE [App::LinkGroup] LinkGroup009  label="arandelas M6 estructura"
  ElementList = -> [Part046,Part047,Part048,Part049,Part050,Part051,Part052,Part053,Part054,Part055,Part056,Part057,Part058,Part059,Part060,Part061,Part062,Part063,Part064,Part065]
  LinkMode = 0
FEATURE [Sketcher::SketchObject] Sketch212
  FullyConstrained = true
  MapMode = 5
  Placement = pos=(0,0,0) rot=(0.57735,0.57735,0.57735;2.0944rad)
  Support = -> [YZ_Plane261]
  sketch-geometry (5):
    g0: LineSegment StartX=0 StartY=0 StartZ=0 EndX=0 EndY=20 EndZ=0
    g1: LineSegment StartX=0 StartY=20 StartZ=0 EndX=-3 EndY=20 EndZ=0
    g2: LineSegment StartX=-3 StartY=20 StartZ=0 EndX=-20 EndY=3 EndZ=0
    g3: LineSegment StartX=-20 StartY=3 StartZ=0 EndX=-20 EndY=0 EndZ=0
    g4: LineSegment StartX=-20 StartY=0 StartZ=0 EndX=0 EndY=0 EndZ=0
  constraints (14):
    c: Coincident(g-1,g0)
    c: PointOnObject(g0,g-2)
    c: Coincident(g0,g1)
    c: Horizontal(g1)
    c: Coincident(g1,g2)
    c: Coincident(g2,g3)
    c: PointOnObject(g3,g-1)
    c: Vertical(g3)
    c: Coincident(g3,g4)
    c: Coincident(g4,g0)
    c: DistanceY(g0,g0) = 20
    c: DistanceY(g3,g3) = 3
    c: DistanceX(g1,g1) = 3
    c: DistanceX(g4,g4) = 20
FEATURE [PartDesign::Pad] Pad105
  Direction = (1,1,1)
  Length = 17
  Length2 = 100
  Placement = pos=(0,0,0) rot=(0.57735,0.57735,0.57735;2.0944rad)
  Profile = -> Sketch212
  Type = 0
FEATURE [Sketcher::SketchObject] Sketch213
  ExternalGeometry = -> [Pad105]
  FullyConstrained = true
  MapMode = 5
  Placement = pos=(-8.8e-15,-20,4.4e-15) rot=(-0.57735,-0.57735,0.57735;4.18879rad)
  Support = -> [Pad105]
  sketch-geometry (4):
    g0: LineSegment StartX=-3 StartY=2 StartZ=0 EndX=-20 EndY=2 EndZ=0
    g1: LineSegment StartX=-20 StartY=2 StartZ=0 EndX=-20 EndY=15 EndZ=0
    g2: LineSegment StartX=-20 StartY=15 StartZ=0 EndX=-3 EndY=15 EndZ=0
    g3: LineSegment StartX=-3 StartY=15 StartZ=0 EndX=-3 EndY=2 EndZ=0
  constraints (12):
    c: Coincident(g0,g1)
    c: Coincident(g1,g2)
    c: Coincident(g2,g3)
    c: Coincident(g3,g0)
    c: Horizontal(g0)
    c: Horizontal(g2)
    c: Vertical(g1)
    c: Vertical(g3)
    c: PointOnObject(g0,g-3)
    c: DistanceY(g1,g-6) = 2
    c: DistanceY(g-6,g0) = 2
    c: PointOnObject(g1,g-6)
FEATURE [PartDesign::Pocket] Pocket074
  BaseFeature = -> Pad105
  Length = 17
  Length2 = 100
  Placement = pos=(0,0,0) rot=(0.57735,0.57735,0.57735;2.0944rad)
  Profile = -> Sketch213
  Type = 0
FEATURE [Sketcher::SketchObject] Sketch214
  ExternalGeometry = -> [Pocket074]
  FullyConstrained = true
  MapMode = 5
  Placement = pos=(-1.7e-15,-3,6e-16) rot=(-0.57735,-0.57735,0.57735;4.18879rad)
  Support = -> [Pocket074]
  sketch-geometry (5):
    g0: LineSegment StartX=-20 StartY=8.5 StartZ=0 EndX=-3 EndY=8.5 EndZ=0
    g1: ArcOfCircle CenterX=-10 CenterY=8.5 CenterZ=0 NormalX=0 NormalY=0 NormalZ=1 AngleXU=0 Radius=3 StartAngle=4.71239 EndAngle=7.85398
    g2: ArcOfCircle CenterX=-13 CenterY=8.5 CenterZ=0 NormalX=0 NormalY=0 NormalZ=1 AngleXU=0 Radius=3 StartAngle=1.5708 EndAngle=4.71239
    g3: LineSegment StartX=-10 StartY=11.5 StartZ=0 EndX=-13 EndY=11.5 EndZ=0
    g4: LineSegment StartX=-10 StartY=5.5 StartZ=0 EndX=-13 EndY=5.5 EndZ=0
  constraints (14):
    c: PointOnObject(g0,g-6)
    c: PointOnObject(g0,g-4)
    c: Horizontal(g0)
    c: DistanceY(g0,g-4) = 6.5
    c: Tangent(g1,g4) = 1.5708
    c: Tangent(g1,g3) = -1.5708
    c: Tangent(g3,g2) = -1.5708
    c: Tangent(g4,g2) = 1.5708
    c: Horizontal(g3)
    c: Equal(g1,g2)
    c: PointOnObject(g1,g0)
    c: Radius(g1) = 3
    c: DistanceX(g3,g3) = 3
    c: DistanceX(g0,g2) = 7
FEATURE [PartDesign::Pocket] Pocket075
  BaseFeature = -> Pocket074
  Length = 5
  Length2 = 100
  Placement = pos=(0,0,0) rot=(0.57735,0.57735,0.57735;2.0944rad)
  Profile = -> Sketch214
  Type = 2
FEATURE [Sketcher::SketchObject] Sketch215
  ExternalGeometry = -> [Pocket075]
  FullyConstrained = true
  MapMode = 5
  Placement = pos=(-3e-16,1.2e-15,3) rot=(0,0,-1;1.5708rad)
  Support = -> [Pocket075]
  sketch-geometry (5):
    g0: LineSegment StartX=3 StartY=8.5 StartZ=0 EndX=20 EndY=8.5 EndZ=0
    g1: ArcOfCircle CenterX=10 CenterY=8.5 CenterZ=0 NormalX=0 NormalY=0 NormalZ=1 AngleXU=0 Radius=3 StartAngle=1.5708 EndAngle=4.71239
    g2: ArcOfCircle CenterX=13 CenterY=8.5 CenterZ=0 NormalX=0 NormalY=0 NormalZ=1 AngleXU=0 Radius=3 StartAngle=4.71239 EndAngle=7.85398
    g3: LineSegment StartX=10 StartY=5.5 StartZ=0 EndX=13 EndY=5.5 EndZ=0
    g4: LineSegment StartX=10 StartY=11.5 StartZ=0 EndX=13 EndY=11.5 EndZ=0
  constraints (14):
    c: PointOnObject(g0,g-4)
    c: PointOnObject(g0,g-5)
    c: Horizontal(g0)
    c: DistanceY(g0,g-4) = 6.5
    c: Tangent(g1,g4) = 1.5708
    c: Tangent(g1,g3) = -1.5708
    c: Tangent(g3,g2) = -1.5708
    c: Tangent(g4,g2) = 1.5708
    c: Horizontal(g3)
    c: Equal(g1,g2)
    c: PointOnObject(g1,g0)
    c: Radius(g2) = 3
    c: DistanceX(g4,g4) = 3
    c: DistanceX(g2,g0) = 7
FEATURE [PartDesign::Pocket] Pocket076
  BaseFeature = -> Pocket075
  Length = 5
  Length2 = 100
  Placement = pos=(0,0,0) rot=(0.57735,0.57735,0.57735;2.0944rad)
  Profile = -> Sketch215
  Type = 2
FEATURE [Sketcher::SketchObject] Sketch216
  ExternalGeometry = -> [Pocket076]
  FullyConstrained = true
  MapMode = 5
  Placement = pos=(0,0,0) rot=(0.57735,0.57735,0.57735;4.18879rad)
  Support = -> [Pocket076]
  sketch-geometry (9):
    g0: LineSegment StartX=0 StartY=8.5 StartZ=0 EndX=20 EndY=8.5 EndZ=0
    g1: ArcOfCircle CenterX=3 CenterY=9.5 CenterZ=0 NormalX=0 NormalY=0 NormalZ=1 AngleXU=0 Radius=1 StartAngle=0 EndAngle=3.14159
    g2: ArcOfCircle CenterX=3 CenterY=7.5 CenterZ=0 NormalX=0 NormalY=0 NormalZ=1 AngleXU=0 Radius=1 StartAngle=3.14159 EndAngle=6.28319
    g3: LineSegment StartX=2 StartY=9.5 StartZ=0 EndX=2 EndY=7.5 EndZ=0
    g4: LineSegment StartX=4 StartY=9.5 StartZ=0 EndX=4 EndY=7.5 EndZ=0
    g5: ArcOfCircle CenterX=18 CenterY=9.5 CenterZ=0 NormalX=0 NormalY=0 NormalZ=1 AngleXU=0 Radius=1 StartAngle=-9e-16 EndAngle=3.14159
    g6: ArcOfCircle CenterX=18 CenterY=7.5 CenterZ=0 NormalX=0 NormalY=0 NormalZ=1 AngleXU=0 Radius=1 StartAngle=3.14159 EndAngle=6.28319
    g7: LineSegment StartX=17 StartY=9.5 StartZ=0 EndX=17 EndY=7.5 EndZ=0
    g8: LineSegment StartX=19 StartY=9.5 StartZ=0 EndX=19 EndY=7.5 EndZ=0
  constraints (24):
    c: PointOnObject(g0,g-2)
    c: PointOnObject(g0,g-5)
    c: Horizontal(g0)
    c: DistanceY(g0,g-3) = 8.5
    c: Tangent(g1,g4) = 1.5708
    c: Tangent(g1,g3) = -1.5708
    c: Tangent(g3,g2) = -1.5708
    c: Tangent(g4,g2) = 1.5708
    c: Vertical(g3)
    c: Equal(g1,g2)
    c: Tangent(g5,g8) = 1.5708
    c: Tangent(g5,g7) = -1.5708
    c: Tangent(g7,g6) = -1.5708
    c: Tangent(g8,g6) = 1.5708
    c: Vertical(g7)
    c: Equal(g5,g6)
    c: Equal(g1,g5)
    c: Equal(g4,g7)
    c: DistanceY(g4,g4) = 2
    c: Radius(g1) = 1
    c: Horizontal(g5,g1)
    c: DistanceX(g0,g1) = 3
    c: DistanceX(g5,g0) = 2
    c: DistanceY(g0,g1) = 1
FEATURE [PartDesign::Pad] Pad106
  BaseFeature = -> Pocket076
  Direction = (1,1,1)
  Length = 1
  Length2 = 100
  Placement = pos=(0,0,0) rot=(0.57735,0.57735,0.57735;2.0944rad)
  Profile = -> Sketch216
  Type = 0
FEATURE [Sketcher::SketchObject] Sketch217
  ExternalGeometry = -> [Pad106]
  FullyConstrained = true
  MapMode = 5
  Placement = pos=(0,0,1e-16) rot=(0.707107,0.707107,0;3.14159rad)
  Support = -> [Pad106]
  sketch-geometry (9):
    g0: LineSegment StartX=0 StartY=8.5 StartZ=0 EndX=-20 EndY=8.5 EndZ=0
    g1: ArcOfCircle CenterX=-3 CenterY=7.5 CenterZ=0 NormalX=0 NormalY=0 NormalZ=1 AngleXU=0 Radius=1 StartAngle=3.14159 EndAngle=6.28319
    g2: ArcOfCircle CenterX=-3 CenterY=9.5 CenterZ=0 NormalX=0 NormalY=0 NormalZ=1 AngleXU=0 Radius=1 StartAngle=3e-16 EndAngle=3.14159
    g3: LineSegment StartX=-2 StartY=7.5 StartZ=0 EndX=-2 EndY=9.5 EndZ=0
    g4: LineSegment StartX=-4 StartY=7.5 StartZ=0 EndX=-4 EndY=9.5 EndZ=0
    g5: ArcOfCircle CenterX=-18 CenterY=9.5 CenterZ=0 NormalX=0 NormalY=0 NormalZ=1 AngleXU=0 Radius=1 StartAngle=0 EndAngle=3.14159
    g6: ArcOfCircle CenterX=-18 CenterY=7.5 CenterZ=0 NormalX=0 NormalY=0 NormalZ=1 AngleXU=0 Radius=1 StartAngle=3.14159 EndAngle=6.28319
    g7: LineSegment StartX=-19 StartY=9.5 StartZ=0 EndX=-19 EndY=7.5 EndZ=0
    g8: LineSegment StartX=-17 StartY=9.5 StartZ=0 EndX=-17 EndY=7.5 EndZ=0
  constraints (24):
    c: PointOnObject(g0,g-2)
    c: PointOnObject(g0,g-4)
    c: Horizontal(g0)
    c: DistanceY(g0,g-3) = 8.5
    c: Tangent(g1,g4) = 1.5708
    c: Tangent(g1,g3) = -1.5708
    c: Tangent(g3,g2) = -1.5708
    c: Tangent(g4,g2) = 1.5708
    c: Vertical(g3)
    c: Equal(g1,g2)
    c: Radius(g2) = 1
    c: DistanceY(g4,g4) = 2
    c: DistanceY(g0,g2) = 1
    c: DistanceX(g2,g0) = 3
    c: Tangent(g5,g8) = 1.5708
    c: Tangent(g5,g7) = -1.5708
    c: Tangent(g7,g6) = -1.5708
    c: Tangent(g8,g6) = 1.5708
    c: Vertical(g7)
    c: Equal(g5,g6)
    c: Equal(g5,g2)
    c: Equal(g8,g4)
    c: Horizontal(g5,g2)
    c: DistanceX(g0,g5) = 2
FEATURE [PartDesign::Pad] Pad107
  BaseFeature = -> Pad106
  Direction = (1,1,1)
  Length = 1
  Length2 = 100
  Placement = pos=(0,0,0) rot=(0.57735,0.57735,0.57735;2.0944rad)
  Profile = -> Sketch217
  Type = 0
FEATURE [PartDesign::Body] Body197  label="Corner"
  Group = -> [Sketch212,Pad105,Sketch213,Pocket074,Sketch214,Pocket075,Sketch215,Pocket076,Sketch216,Pad106,Sketch217,Pad107]
  Origin = -> Origin267
  Tip = -> Pad107
FEATURE [App::Part] Part070  label="soporte90-001"
  Group = -> [Body197]
  Origin = -> Origin268
  Placement = pos=(20,18,170) rot=(0.707107,-0.707107,0;3.14159rad)
FEATURE [Sketcher::SketchObject] Sketch218
  FullyConstrained = true
  MapMode = 5
  Placement = pos=(0,0,0) rot=(0.57735,0.57735,0.57735;2.0944rad)
  Support = -> [YZ_Plane263]
  sketch-geometry (5):
    g0: LineSegment StartX=0 StartY=0 StartZ=0 EndX=0 EndY=20 EndZ=0
    g1: LineSegment StartX=0 StartY=20 StartZ=0 EndX=-3 EndY=20 EndZ=0
    g2: LineSegment StartX=-3 StartY=20 StartZ=0 EndX=-20 EndY=3 EndZ=0
    g3: LineSegment StartX=-20 StartY=3 StartZ=0 EndX=-20 EndY=0 EndZ=0
    g4: LineSegment StartX=-20 StartY=0 StartZ=0 EndX=0 EndY=0 EndZ=0
  constraints (14):
    c: Coincident(g-1,g0)
    c: PointOnObject(g0,g-2)
    c: Coincident(g0,g1)
    c: Horizontal(g1)
    c: Coincident(g1,g2)
    c: Coincident(g2,g3)
    c: PointOnObject(g3,g-1)
    c: Vertical(g3)
    c: Coincident(g3,g4)
    c: Coincident(g4,g0)
    c: DistanceY(g0,g0) = 20
    c: DistanceY(g3,g3) = 3
    c: DistanceX(g1,g1) = 3
    c: DistanceX(g4,g4) = 20
FEATURE [PartDesign::Pad] Pad108
  Direction = (1,1,1)
  Length = 17
  Length2 = 100
  Placement = pos=(0,0,0) rot=(0.57735,0.57735,0.57735;2.0944rad)
  Profile = -> Sketch218
  Type = 0
FEATURE [Sketcher::SketchObject] Sketch219
  ExternalGeometry = -> [Pad108]
  FullyConstrained = true
  MapMode = 5
  Placement = pos=(-8.8e-15,-20,4.4e-15) rot=(-0.57735,-0.57735,0.57735;4.18879rad)
  Support = -> [Pad108]
  sketch-geometry (4):
    g0: LineSegment StartX=-3 StartY=2 StartZ=0 EndX=-20 EndY=2 EndZ=0
    g1: LineSegment StartX=-20 StartY=2 StartZ=0 EndX=-20 EndY=15 EndZ=0
    g2: LineSegment StartX=-20 StartY=15 StartZ=0 EndX=-3 EndY=15 EndZ=0
    g3: LineSegment StartX=-3 StartY=15 StartZ=0 EndX=-3 EndY=2 EndZ=0
  constraints (12):
    c: Coincident(g0,g1)
    c: Coincident(g1,g2)
    c: Coincident(g2,g3)
    c: Coincident(g3,g0)
    c: Horizontal(g0)
    c: Horizontal(g2)
    c: Vertical(g1)
    c: Vertical(g3)
    c: PointOnObject(g0,g-3)
    c: DistanceY(g1,g-6) = 2
    c: DistanceY(g-6,g0) = 2
    c: PointOnObject(g1,g-6)
FEATURE [PartDesign::Pocket] Pocket077
  BaseFeature = -> Pad108
  Length = 17
  Length2 = 100
  Placement = pos=(0,0,0) rot=(0.57735,0.57735,0.57735;2.0944rad)
  Profile = -> Sketch219
  Type = 0
FEATURE [Sketcher::SketchObject] Sketch220
  ExternalGeometry = -> [Pocket077]
  FullyConstrained = true
  MapMode = 5
  Placement = pos=(-1.7e-15,-3,6e-16) rot=(-0.57735,-0.57735,0.57735;4.18879rad)
  Support = -> [Pocket077]
  sketch-geometry (5):
    g0: LineSegment StartX=-20 StartY=8.5 StartZ=0 EndX=-3 EndY=8.5 EndZ=0
    g1: ArcOfCircle CenterX=-10 CenterY=8.5 CenterZ=0 NormalX=0 NormalY=0 NormalZ=1 AngleXU=0 Radius=3 StartAngle=4.71239 EndAngle=7.85398
    g2: ArcOfCircle CenterX=-13 CenterY=8.5 CenterZ=0 NormalX=0 NormalY=0 NormalZ=1 AngleXU=0 Radius=3 StartAngle=1.5708 EndAngle=4.71239
    g3: LineSegment StartX=-10 StartY=11.5 StartZ=0 EndX=-13 EndY=11.5 EndZ=0
    g4: LineSegment StartX=-10 StartY=5.5 StartZ=0 EndX=-13 EndY=5.5 EndZ=0
  constraints (14):
    c: PointOnObject(g0,g-6)
    c: PointOnObject(g0,g-4)
    c: Horizontal(g0)
    c: DistanceY(g0,g-4) = 6.5
    c: Tangent(g1,g4) = 1.5708
    c: Tangent(g1,g3) = -1.5708
    c: Tangent(g3,g2) = -1.5708
    c: Tangent(g4,g2) = 1.5708
    c: Horizontal(g3)
    c: Equal(g1,g2)
    c: PointOnObject(g1,g0)
    c: Radius(g1) = 3
    c: DistanceX(g3,g3) = 3
    c: DistanceX(g0,g2) = 7
FEATURE [PartDesign::Pocket] Pocket078
  BaseFeature = -> Pocket077
  Length = 5
  Length2 = 100
  Placement = pos=(0,0,0) rot=(0.57735,0.57735,0.57735;2.0944rad)
  Profile = -> Sketch220
  Type = 2
FEATURE [Sketcher::SketchObject] Sketch221
  ExternalGeometry = -> [Pocket078]
  FullyConstrained = true
  MapMode = 5
  Placement = pos=(-3e-16,1.2e-15,3) rot=(0,0,-1;1.5708rad)
  Support = -> [Pocket078]
  sketch-geometry (5):
    g0: LineSegment StartX=3 StartY=8.5 StartZ=0 EndX=20 EndY=8.5 EndZ=0
    g1: ArcOfCircle CenterX=10 CenterY=8.5 CenterZ=0 NormalX=0 NormalY=0 NormalZ=1 AngleXU=0 Radius=3 StartAngle=1.5708 EndAngle=4.71239
    g2: ArcOfCircle CenterX=13 CenterY=8.5 CenterZ=0 NormalX=0 NormalY=0 NormalZ=1 AngleXU=0 Radius=3 StartAngle=4.71239 EndAngle=7.85398
    g3: LineSegment StartX=10 StartY=5.5 StartZ=0 EndX=13 EndY=5.5 EndZ=0
    g4: LineSegment StartX=10 StartY=11.5 StartZ=0 EndX=13 EndY=11.5 EndZ=0
  constraints (14):
    c: PointOnObject(g0,g-4)
    c: PointOnObject(g0,g-5)
    c: Horizontal(g0)
    c: DistanceY(g0,g-4) = 6.5
    c: Tangent(g1,g4) = 1.5708
    c: Tangent(g1,g3) = -1.5708
    c: Tangent(g3,g2) = -1.5708
    c: Tangent(g4,g2) = 1.5708
    c: Horizontal(g3)
    c: Equal(g1,g2)
    c: PointOnObject(g1,g0)
    c: Radius(g2) = 3
    c: DistanceX(g4,g4) = 3
    c: DistanceX(g2,g0) = 7
FEATURE [PartDesign::Pocket] Pocket079
  BaseFeature = -> Pocket078
  Length = 5
  Length2 = 100
  Placement = pos=(0,0,0) rot=(0.57735,0.57735,0.57735;2.0944rad)
  Profile = -> Sketch221
  Type = 2
FEATURE [Sketcher::SketchObject] Sketch222
  ExternalGeometry = -> [Pocket079]
  FullyConstrained = true
  MapMode = 5
  Placement = pos=(0,0,0) rot=(0.57735,0.57735,0.57735;4.18879rad)
  Support = -> [Pocket079]
  sketch-geometry (9):
    g0: LineSegment StartX=0 StartY=8.5 StartZ=0 EndX=20 EndY=8.5 EndZ=0
    g1: ArcOfCircle CenterX=3 CenterY=9.5 CenterZ=0 NormalX=0 NormalY=0 NormalZ=1 AngleXU=0 Radius=1 StartAngle=0 EndAngle=3.14159
    g2: ArcOfCircle CenterX=3 CenterY=7.5 CenterZ=0 NormalX=0 NormalY=0 NormalZ=1 AngleXU=0 Radius=1 StartAngle=3.14159 EndAngle=6.28319
    g3: LineSegment StartX=2 StartY=9.5 StartZ=0 EndX=2 EndY=7.5 EndZ=0
    g4: LineSegment StartX=4 StartY=9.5 StartZ=0 EndX=4 EndY=7.5 EndZ=0
    g5: ArcOfCircle CenterX=18 CenterY=9.5 CenterZ=0 NormalX=0 NormalY=0 NormalZ=1 AngleXU=0 Radius=1 StartAngle=-9e-16 EndAngle=3.14159
    g6: ArcOfCircle CenterX=18 CenterY=7.5 CenterZ=0 NormalX=0 NormalY=0 NormalZ=1 AngleXU=0 Radius=1 StartAngle=3.14159 EndAngle=6.28319
    g7: LineSegment StartX=17 StartY=9.5 StartZ=0 EndX=17 EndY=7.5 EndZ=0
    g8: LineSegment StartX=19 StartY=9.5 StartZ=0 EndX=19 EndY=7.5 EndZ=0
  constraints (24):
    c: PointOnObject(g0,g-2)
    c: PointOnObject(g0,g-5)
    c: Horizontal(g0)
    c: DistanceY(g0,g-3) = 8.5
    c: Tangent(g1,g4) = 1.5708
    c: Tangent(g1,g3) = -1.5708
    c: Tangent(g3,g2) = -1.5708
    c: Tangent(g4,g2) = 1.5708
    c: Vertical(g3)
    c: Equal(g1,g2)
    c: Tangent(g5,g8) = 1.5708
    c: Tangent(g5,g7) = -1.5708
    c: Tangent(g7,g6) = -1.5708
    c: Tangent(g8,g6) = 1.5708
    c: Vertical(g7)
    c: Equal(g5,g6)
    c: Equal(g1,g5)
    c: Equal(g4,g7)
    c: DistanceY(g4,g4) = 2
    c: Radius(g1) = 1
    c: Horizontal(g5,g1)
    c: DistanceX(g0,g1) = 3
    c: DistanceX(g5,g0) = 2
    c: DistanceY(g0,g1) = 1
FEATURE [PartDesign::Pad] Pad109
  BaseFeature = -> Pocket079
  Direction = (1,1,1)
  Length = 1
  Length2 = 100
  Placement = pos=(0,0,0) rot=(0.57735,0.57735,0.57735;2.0944rad)
  Profile = -> Sketch222
  Type = 0
FEATURE [Sketcher::SketchObject] Sketch223
  ExternalGeometry = -> [Pad109]
  FullyConstrained = true
  MapMode = 5
  Placement = pos=(0,0,1e-16) rot=(0.707107,0.707107,0;3.14159rad)
  Support = -> [Pad109]
  sketch-geometry (9):
    g0: LineSegment StartX=0 StartY=8.5 StartZ=0 EndX=-20 EndY=8.5 EndZ=0
    g1: ArcOfCircle CenterX=-3 CenterY=7.5 CenterZ=0 NormalX=0 NormalY=0 NormalZ=1 AngleXU=0 Radius=1 StartAngle=3.14159 EndAngle=6.28319
    g2: ArcOfCircle CenterX=-3 CenterY=9.5 CenterZ=0 NormalX=0 NormalY=0 NormalZ=1 AngleXU=0 Radius=1 StartAngle=3e-16 EndAngle=3.14159
    g3: LineSegment StartX=-2 StartY=7.5 StartZ=0 EndX=-2 EndY=9.5 EndZ=0
    g4: LineSegment StartX=-4 StartY=7.5 StartZ=0 EndX=-4 EndY=9.5 EndZ=0
    g5: ArcOfCircle CenterX=-18 CenterY=9.5 CenterZ=0 NormalX=0 NormalY=0 NormalZ=1 AngleXU=0 Radius=1 StartAngle=0 EndAngle=3.14159
    g6: ArcOfCircle CenterX=-18 CenterY=7.5 CenterZ=0 NormalX=0 NormalY=0 NormalZ=1 AngleXU=0 Radius=1 StartAngle=3.14159 EndAngle=6.28319
    g7: LineSegment StartX=-19 StartY=9.5 StartZ=0 EndX=-19 EndY=7.5 EndZ=0
    g8: LineSegment StartX=-17 StartY=9.5 StartZ=0 EndX=-17 EndY=7.5 EndZ=0
  constraints (24):
    c: PointOnObject(g0,g-2)
    c: PointOnObject(g0,g-4)
    c: Horizontal(g0)
    c: DistanceY(g0,g-3) = 8.5
    c: Tangent(g1,g4) = 1.5708
    c: Tangent(g1,g3) = -1.5708
    c: Tangent(g3,g2) = -1.5708
    c: Tangent(g4,g2) = 1.5708
    c: Vertical(g3)
    c: Equal(g1,g2)
    c: Radius(g2) = 1
    c: DistanceY(g4,g4) = 2
    c: DistanceY(g0,g2) = 1
    c: DistanceX(g2,g0) = 3
    c: Tangent(g5,g8) = 1.5708
    c: Tangent(g5,g7) = -1.5708
    c: Tangent(g7,g6) = -1.5708
    c: Tangent(g8,g6) = 1.5708
    c: Vertical(g7)
    c: Equal(g5,g6)
    c: Equal(g5,g2)
    c: Equal(g8,g4)
    c: Horizontal(g5,g2)
    c: DistanceX(g0,g5) = 2
FEATURE [PartDesign::Pad] Pad110
  BaseFeature = -> Pad109
  Direction = (1,1,1)
  Length = 1
  Length2 = 100
  Placement = pos=(0,0,0) rot=(0.57735,0.57735,0.57735;2.0944rad)
  Profile = -> Sketch223
  Type = 0
FEATURE [PartDesign::Body] Body198  label="Corner001"
  Group = -> [Sketch218,Pad108,Sketch219,Pocket077,Sketch220,Pocket078,Sketch221,Pocket079,Sketch222,Pad109,Sketch223,Pad110]
  Origin = -> Origin269
  Tip = -> Pad110
FEATURE [App::Part] Part071  label="soporte90-002"
  Group = -> [Body198]
  Origin = -> Origin270
  Placement = pos=(20,321,20) rot=(0,0,1;1.5708rad)
FEATURE [Sketcher::SketchObject] Sketch224
  FullyConstrained = true
  MapMode = 5
  Placement = pos=(0,0,0) rot=(0.57735,0.57735,0.57735;2.0944rad)
  Support = -> [YZ_Plane265]
  sketch-geometry (5):
    g0: LineSegment StartX=0 StartY=0 StartZ=0 EndX=0 EndY=20 EndZ=0
    g1: LineSegment StartX=0 StartY=20 StartZ=0 EndX=-3 EndY=20 EndZ=0
    g2: LineSegment StartX=-3 StartY=20 StartZ=0 EndX=-20 EndY=3 EndZ=0
    g3: LineSegment StartX=-20 StartY=3 StartZ=0 EndX=-20 EndY=0 EndZ=0
    g4: LineSegment StartX=-20 StartY=0 StartZ=0 EndX=0 EndY=0 EndZ=0
  constraints (14):
    c: Coincident(g-1,g0)
    c: PointOnObject(g0,g-2)
    c: Coincident(g0,g1)
    c: Horizontal(g1)
    c: Coincident(g1,g2)
    c: Coincident(g2,g3)
    c: PointOnObject(g3,g-1)
    c: Vertical(g3)
    c: Coincident(g3,g4)
    c: Coincident(g4,g0)
    c: DistanceY(g0,g0) = 20
    c: DistanceY(g3,g3) = 3
    c: DistanceX(g1,g1) = 3
    c: DistanceX(g4,g4) = 20
FEATURE [PartDesign::Pad] Pad111
  Direction = (1,1,1)
  Length = 17
  Length2 = 100
  Placement = pos=(0,0,0) rot=(0.57735,0.57735,0.57735;2.0944rad)
  Profile = -> Sketch224
  Type = 0
FEATURE [Sketcher::SketchObject] Sketch225
  ExternalGeometry = -> [Pad111]
  FullyConstrained = true
  MapMode = 5
  Placement = pos=(-8.8e-15,-20,4.4e-15) rot=(-0.57735,-0.57735,0.57735;4.18879rad)
  Support = -> [Pad111]
  sketch-geometry (4):
    g0: LineSegment StartX=-3 StartY=2 StartZ=0 EndX=-20 EndY=2 EndZ=0
    g1: LineSegment StartX=-20 StartY=2 StartZ=0 EndX=-20 EndY=15 EndZ=0
    g2: LineSegment StartX=-20 StartY=15 StartZ=0 EndX=-3 EndY=15 EndZ=0
    g3: LineSegment StartX=-3 StartY=15 StartZ=0 EndX=-3 EndY=2 EndZ=0
  constraints (12):
    c: Coincident(g0,g1)
    c: Coincident(g1,g2)
    c: Coincident(g2,g3)
    c: Coincident(g3,g0)
    c: Horizontal(g0)
    c: Horizontal(g2)
    c: Vertical(g1)
    c: Vertical(g3)
    c: PointOnObject(g0,g-3)
    c: DistanceY(g1,g-6) = 2
    c: DistanceY(g-6,g0) = 2
    c: PointOnObject(g1,g-6)
FEATURE [PartDesign::Pocket] Pocket080
  BaseFeature = -> Pad111
  Length = 17
  Length2 = 100
  Placement = pos=(0,0,0) rot=(0.57735,0.57735,0.57735;2.0944rad)
  Profile = -> Sketch225
  Type = 0
FEATURE [Sketcher::SketchObject] Sketch226
  ExternalGeometry = -> [Pocket080]
  FullyConstrained = true
  MapMode = 5
  Placement = pos=(-1.7e-15,-3,6e-16) rot=(-0.57735,-0.57735,0.57735;4.18879rad)
  Support = -> [Pocket080]
  sketch-geometry (5):
    g0: LineSegment StartX=-20 StartY=8.5 StartZ=0 EndX=-3 EndY=8.5 EndZ=0
    g1: ArcOfCircle CenterX=-10 CenterY=8.5 CenterZ=0 NormalX=0 NormalY=0 NormalZ=1 AngleXU=0 Radius=3 StartAngle=4.71239 EndAngle=7.85398
    g2: ArcOfCircle CenterX=-13 CenterY=8.5 CenterZ=0 NormalX=0 NormalY=0 NormalZ=1 AngleXU=0 Radius=3 StartAngle=1.5708 EndAngle=4.71239
    g3: LineSegment StartX=-10 StartY=11.5 StartZ=0 EndX=-13 EndY=11.5 EndZ=0
    g4: LineSegment StartX=-10 StartY=5.5 StartZ=0 EndX=-13 EndY=5.5 EndZ=0
  constraints (14):
    c: PointOnObject(g0,g-6)
    c: PointOnObject(g0,g-4)
    c: Horizontal(g0)
    c: DistanceY(g0,g-4) = 6.5
    c: Tangent(g1,g4) = 1.5708
    c: Tangent(g1,g3) = -1.5708
    c: Tangent(g3,g2) = -1.5708
    c: Tangent(g4,g2) = 1.5708
    c: Horizontal(g3)
    c: Equal(g1,g2)
    c: PointOnObject(g1,g0)
    c: Radius(g1) = 3
    c: DistanceX(g3,g3) = 3
    c: DistanceX(g0,g2) = 7
FEATURE [PartDesign::Pocket] Pocket081
  BaseFeature = -> Pocket080
  Length = 5
  Length2 = 100
  Placement = pos=(0,0,0) rot=(0.57735,0.57735,0.57735;2.0944rad)
  Profile = -> Sketch226
  Type = 2
FEATURE [Sketcher::SketchObject] Sketch227
  ExternalGeometry = -> [Pocket081]
  FullyConstrained = true
  MapMode = 5
  Placement = pos=(-3e-16,1.2e-15,3) rot=(0,0,-1;1.5708rad)
  Support = -> [Pocket081]
  sketch-geometry (5):
    g0: LineSegment StartX=3 StartY=8.5 StartZ=0 EndX=20 EndY=8.5 EndZ=0
    g1: ArcOfCircle CenterX=10 CenterY=8.5 CenterZ=0 NormalX=0 NormalY=0 NormalZ=1 AngleXU=0 Radius=3 StartAngle=1.5708 EndAngle=4.71239
    g2: ArcOfCircle CenterX=13 CenterY=8.5 CenterZ=0 NormalX=0 NormalY=0 NormalZ=1 AngleXU=0 Radius=3 StartAngle=4.71239 EndAngle=7.85398
    g3: LineSegment StartX=10 StartY=5.5 StartZ=0 EndX=13 EndY=5.5 EndZ=0
    g4: LineSegment StartX=10 StartY=11.5 StartZ=0 EndX=13 EndY=11.5 EndZ=0
  constraints (14):
    c: PointOnObject(g0,g-4)
    c: PointOnObject(g0,g-5)
    c: Horizontal(g0)
    c: DistanceY(g0,g-4) = 6.5
    c: Tangent(g1,g4) = 1.5708
    c: Tangent(g1,g3) = -1.5708
    c: Tangent(g3,g2) = -1.5708
    c: Tangent(g4,g2) = 1.5708
    c: Horizontal(g3)
    c: Equal(g1,g2)
    c: PointOnObject(g1,g0)
    c: Radius(g2) = 3
    c: DistanceX(g4,g4) = 3
    c: DistanceX(g2,g0) = 7
FEATURE [PartDesign::Pocket] Pocket082
  BaseFeature = -> Pocket081
  Length = 5
  Length2 = 100
  Placement = pos=(0,0,0) rot=(0.57735,0.57735,0.57735;2.0944rad)
  Profile = -> Sketch227
  Type = 2
FEATURE [Sketcher::SketchObject] Sketch228
  ExternalGeometry = -> [Pocket082]
  FullyConstrained = true
  MapMode = 5
  Placement = pos=(0,0,0) rot=(0.57735,0.57735,0.57735;4.18879rad)
  Support = -> [Pocket082]
  sketch-geometry (9):
    g0: LineSegment StartX=0 StartY=8.5 StartZ=0 EndX=20 EndY=8.5 EndZ=0
    g1: ArcOfCircle CenterX=3 CenterY=9.5 CenterZ=0 NormalX=0 NormalY=0 NormalZ=1 AngleXU=0 Radius=1 StartAngle=0 EndAngle=3.14159
    g2: ArcOfCircle CenterX=3 CenterY=7.5 CenterZ=0 NormalX=0 NormalY=0 NormalZ=1 AngleXU=0 Radius=1 StartAngle=3.14159 EndAngle=6.28319
    g3: LineSegment StartX=2 StartY=9.5 StartZ=0 EndX=2 EndY=7.5 EndZ=0
    g4: LineSegment StartX=4 StartY=9.5 StartZ=0 EndX=4 EndY=7.5 EndZ=0
    g5: ArcOfCircle CenterX=18 CenterY=9.5 CenterZ=0 NormalX=0 NormalY=0 NormalZ=1 AngleXU=0 Radius=1 StartAngle=-9e-16 EndAngle=3.14159
    g6: ArcOfCircle CenterX=18 CenterY=7.5 CenterZ=0 NormalX=0 NormalY=0 NormalZ=1 AngleXU=0 Radius=1 StartAngle=3.14159 EndAngle=6.28319
    g7: LineSegment StartX=17 StartY=9.5 StartZ=0 EndX=17 EndY=7.5 EndZ=0
    g8: LineSegment StartX=19 StartY=9.5 StartZ=0 EndX=19 EndY=7.5 EndZ=0
  constraints (24):
    c: PointOnObject(g0,g-2)
    c: PointOnObject(g0,g-5)
    c: Horizontal(g0)
    c: DistanceY(g0,g-3) = 8.5
    c: Tangent(g1,g4) = 1.5708
    c: Tangent(g1,g3) = -1.5708
    c: Tangent(g3,g2) = -1.5708
    c: Tangent(g4,g2) = 1.5708
    c: Vertical(g3)
    c: Equal(g1,g2)
    c: Tangent(g5,g8) = 1.5708
    c: Tangent(g5,g7) = -1.5708
    c: Tangent(g7,g6) = -1.5708
    c: Tangent(g8,g6) = 1.5708
    c: Vertical(g7)
    c: Equal(g5,g6)
    c: Equal(g1,g5)
    c: Equal(g4,g7)
    c: DistanceY(g4,g4) = 2
    c: Radius(g1) = 1
    c: Horizontal(g5,g1)
    c: DistanceX(g0,g1) = 3
    c: DistanceX(g5,g0) = 2
    c: DistanceY(g0,g1) = 1
FEATURE [PartDesign::Pad] Pad112
  BaseFeature = -> Pocket082
  Direction = (1,1,1)
  Length = 1
  Length2 = 100
  Placement = pos=(0,0,0) rot=(0.57735,0.57735,0.57735;2.0944rad)
  Profile = -> Sketch228
  Type = 0
FEATURE [Sketcher::SketchObject] Sketch229
  ExternalGeometry = -> [Pad112]
  FullyConstrained = true
  MapMode = 5
  Placement = pos=(0,0,1e-16) rot=(0.707107,0.707107,0;3.14159rad)
  Support = -> [Pad112]
  sketch-geometry (9):
    g0: LineSegment StartX=0 StartY=8.5 StartZ=0 EndX=-20 EndY=8.5 EndZ=0
    g1: ArcOfCircle CenterX=-3 CenterY=7.5 CenterZ=0 NormalX=0 NormalY=0 NormalZ=1 AngleXU=0 Radius=1 StartAngle=3.14159 EndAngle=6.28319
    g2: ArcOfCircle CenterX=-3 CenterY=9.5 CenterZ=0 NormalX=0 NormalY=0 NormalZ=1 AngleXU=0 Radius=1 StartAngle=3e-16 EndAngle=3.14159
    g3: LineSegment StartX=-2 StartY=7.5 StartZ=0 EndX=-2 EndY=9.5 EndZ=0
    g4: LineSegment StartX=-4 StartY=7.5 StartZ=0 EndX=-4 EndY=9.5 EndZ=0
    g5: ArcOfCircle CenterX=-18 CenterY=9.5 CenterZ=0 NormalX=0 NormalY=0 NormalZ=1 AngleXU=0 Radius=1 StartAngle=0 EndAngle=3.14159
    g6: ArcOfCircle CenterX=-18 CenterY=7.5 CenterZ=0 NormalX=0 NormalY=0 NormalZ=1 AngleXU=0 Radius=1 StartAngle=3.14159 EndAngle=6.28319
    g7: LineSegment StartX=-19 StartY=9.5 StartZ=0 EndX=-19 EndY=7.5 EndZ=0
    g8: LineSegment StartX=-17 StartY=9.5 StartZ=0 EndX=-17 EndY=7.5 EndZ=0
  constraints (24):
    c: PointOnObject(g0,g-2)
    c: PointOnObject(g0,g-4)
    c: Horizontal(g0)
    c: DistanceY(g0,g-3) = 8.5
    c: Tangent(g1,g4) = 1.5708
    c: Tangent(g1,g3) = -1.5708
    c: Tangent(g3,g2) = -1.5708
    c: Tangent(g4,g2) = 1.5708
    c: Vertical(g3)
    c: Equal(g1,g2)
    c: Radius(g2) = 1
    c: DistanceY(g4,g4) = 2
    c: DistanceY(g0,g2) = 1
    c: DistanceX(g2,g0) = 3
    c: Tangent(g5,g8) = 1.5708
    c: Tangent(g5,g7) = -1.5708
    c: Tangent(g7,g6) = -1.5708
    c: Tangent(g8,g6) = 1.5708
    c: Vertical(g7)
    c: Equal(g5,g6)
    c: Equal(g5,g2)
    c: Equal(g8,g4)
    c: Horizontal(g5,g2)
    c: DistanceX(g0,g5) = 2
FEATURE [PartDesign::Pad] Pad113
  BaseFeature = -> Pad112
  Direction = (1,1,1)
  Length = 1
  Length2 = 100
  Placement = pos=(0,0,0) rot=(0.57735,0.57735,0.57735;2.0944rad)
  Profile = -> Sketch229
  Type = 0
FEATURE [PartDesign::Body] Body199  label="Corner002"
  Group = -> [Sketch224,Pad111,Sketch225,Pocket080,Sketch226,Pocket081,Sketch227,Pocket082,Sketch228,Pad112,Sketch229,Pad113]
  Origin = -> Origin271
  Tip = -> Pad113
FEATURE [App::Part] Part072  label="soporte90-003"
  Group = -> [Body199]
  Origin = -> Origin272
  Placement = pos=(321,339,20) rot=(0,0,1;-1.5708rad)
FEATURE [Sketcher::SketchObject] Sketch230
  FullyConstrained = true
  MapMode = 5
  Placement = pos=(0,0,0) rot=(0.57735,0.57735,0.57735;2.0944rad)
  Support = -> [YZ_Plane267]
  sketch-geometry (5):
    g0: LineSegment StartX=0 StartY=0 StartZ=0 EndX=0 EndY=20 EndZ=0
    g1: LineSegment StartX=0 StartY=20 StartZ=0 EndX=-3 EndY=20 EndZ=0
    g2: LineSegment StartX=-3 StartY=20 StartZ=0 EndX=-20 EndY=3 EndZ=0
    g3: LineSegment StartX=-20 StartY=3 StartZ=0 EndX=-20 EndY=0 EndZ=0
    g4: LineSegment StartX=-20 StartY=0 StartZ=0 EndX=0 EndY=0 EndZ=0
  constraints (14):
    c: Coincident(g-1,g0)
    c: PointOnObject(g0,g-2)
    c: Coincident(g0,g1)
    c: Horizontal(g1)
    c: Coincident(g1,g2)
    c: Coincident(g2,g3)
    c: PointOnObject(g3,g-1)
    c: Vertical(g3)
    c: Coincident(g3,g4)
    c: Coincident(g4,g0)
    c: DistanceY(g0,g0) = 20
    c: DistanceY(g3,g3) = 3
    c: DistanceX(g1,g1) = 3
    c: DistanceX(g4,g4) = 20
FEATURE [PartDesign::Pad] Pad114
  Direction = (1,1,1)
  Length = 17
  Length2 = 100
  Placement = pos=(0,0,0) rot=(0.57735,0.57735,0.57735;2.0944rad)
  Profile = -> Sketch230
  Type = 0
FEATURE [Sketcher::SketchObject] Sketch231
  ExternalGeometry = -> [Pad114]
  FullyConstrained = true
  MapMode = 5
  Placement = pos=(-8.8e-15,-20,4.4e-15) rot=(-0.57735,-0.57735,0.57735;4.18879rad)
  Support = -> [Pad114]
  sketch-geometry (4):
    g0: LineSegment StartX=-3 StartY=2 StartZ=0 EndX=-20 EndY=2 EndZ=0
    g1: LineSegment StartX=-20 StartY=2 StartZ=0 EndX=-20 EndY=15 EndZ=0
    g2: LineSegment StartX=-20 StartY=15 StartZ=0 EndX=-3 EndY=15 EndZ=0
    g3: LineSegment StartX=-3 StartY=15 StartZ=0 EndX=-3 EndY=2 EndZ=0
  constraints (12):
    c: Coincident(g0,g1)
    c: Coincident(g1,g2)
    c: Coincident(g2,g3)
    c: Coincident(g3,g0)
    c: Horizontal(g0)
    c: Horizontal(g2)
    c: Vertical(g1)
    c: Vertical(g3)
    c: PointOnObject(g0,g-3)
    c: DistanceY(g1,g-6) = 2
    c: DistanceY(g-6,g0) = 2
    c: PointOnObject(g1,g-6)
FEATURE [PartDesign::Pocket] Pocket083
  BaseFeature = -> Pad114
  Length = 17
  Length2 = 100
  Placement = pos=(0,0,0) rot=(0.57735,0.57735,0.57735;2.0944rad)
  Profile = -> Sketch231
  Type = 0
FEATURE [Sketcher::SketchObject] Sketch232
  ExternalGeometry = -> [Pocket083]
  FullyConstrained = true
  MapMode = 5
  Placement = pos=(-1.7e-15,-3,6e-16) rot=(-0.57735,-0.57735,0.57735;4.18879rad)
  Support = -> [Pocket083]
  sketch-geometry (5):
    g0: LineSegment StartX=-20 StartY=8.5 StartZ=0 EndX=-3 EndY=8.5 EndZ=0
    g1: ArcOfCircle CenterX=-10 CenterY=8.5 CenterZ=0 NormalX=0 NormalY=0 NormalZ=1 AngleXU=0 Radius=3 StartAngle=4.71239 EndAngle=7.85398
    g2: ArcOfCircle CenterX=-13 CenterY=8.5 CenterZ=0 NormalX=0 NormalY=0 NormalZ=1 AngleXU=0 Radius=3 StartAngle=1.5708 EndAngle=4.71239
    g3: LineSegment StartX=-10 StartY=11.5 StartZ=0 EndX=-13 EndY=11.5 EndZ=0
    g4: LineSegment StartX=-10 StartY=5.5 StartZ=0 EndX=-13 EndY=5.5 EndZ=0
  constraints (14):
    c: PointOnObject(g0,g-6)
    c: PointOnObject(g0,g-4)
    c: Horizontal(g0)
    c: DistanceY(g0,g-4) = 6.5
    c: Tangent(g1,g4) = 1.5708
    c: Tangent(g1,g3) = -1.5708
    c: Tangent(g3,g2) = -1.5708
    c: Tangent(g4,g2) = 1.5708
    c: Horizontal(g3)
    c: Equal(g1,g2)
    c: PointOnObject(g1,g0)
    c: Radius(g1) = 3
    c: DistanceX(g3,g3) = 3
    c: DistanceX(g0,g2) = 7
FEATURE [PartDesign::Pocket] Pocket084
  BaseFeature = -> Pocket083
  Length = 5
  Length2 = 100
  Placement = pos=(0,0,0) rot=(0.57735,0.57735,0.57735;2.0944rad)
  Profile = -> Sketch232
  Type = 2
FEATURE [Sketcher::SketchObject] Sketch233
  ExternalGeometry = -> [Pocket084]
  FullyConstrained = true
  MapMode = 5
  Placement = pos=(-3e-16,1.2e-15,3) rot=(0,0,-1;1.5708rad)
  Support = -> [Pocket084]
  sketch-geometry (5):
    g0: LineSegment StartX=3 StartY=8.5 StartZ=0 EndX=20 EndY=8.5 EndZ=0
    g1: ArcOfCircle CenterX=10 CenterY=8.5 CenterZ=0 NormalX=0 NormalY=0 NormalZ=1 AngleXU=0 Radius=3 StartAngle=1.5708 EndAngle=4.71239
    g2: ArcOfCircle CenterX=13 CenterY=8.5 CenterZ=0 NormalX=0 NormalY=0 NormalZ=1 AngleXU=0 Radius=3 StartAngle=4.71239 EndAngle=7.85398
    g3: LineSegment StartX=10 StartY=5.5 StartZ=0 EndX=13 EndY=5.5 EndZ=0
    g4: LineSegment StartX=10 StartY=11.5 StartZ=0 EndX=13 EndY=11.5 EndZ=0
  constraints (14):
    c: PointOnObject(g0,g-4)
    c: PointOnObject(g0,g-5)
    c: Horizontal(g0)
    c: DistanceY(g0,g-4) = 6.5
    c: Tangent(g1,g4) = 1.5708
    c: Tangent(g1,g3) = -1.5708
    c: Tangent(g3,g2) = -1.5708
    c: Tangent(g4,g2) = 1.5708
    c: Horizontal(g3)
    c: Equal(g1,g2)
    c: PointOnObject(g1,g0)
    c: Radius(g2) = 3
    c: DistanceX(g4,g4) = 3
    c: DistanceX(g2,g0) = 7
FEATURE [PartDesign::Pocket] Pocket085
  BaseFeature = -> Pocket084
  Length = 5
  Length2 = 100
  Placement = pos=(0,0,0) rot=(0.57735,0.57735,0.57735;2.0944rad)
  Profile = -> Sketch233
  Type = 2
FEATURE [Sketcher::SketchObject] Sketch234
  ExternalGeometry = -> [Pocket085]
  FullyConstrained = true
  MapMode = 5
  Placement = pos=(0,0,0) rot=(0.57735,0.57735,0.57735;4.18879rad)
  Support = -> [Pocket085]
  sketch-geometry (9):
    g0: LineSegment StartX=0 StartY=8.5 StartZ=0 EndX=20 EndY=8.5 EndZ=0
    g1: ArcOfCircle CenterX=3 CenterY=9.5 CenterZ=0 NormalX=0 NormalY=0 NormalZ=1 AngleXU=0 Radius=1 StartAngle=0 EndAngle=3.14159
    g2: ArcOfCircle CenterX=3 CenterY=7.5 CenterZ=0 NormalX=0 NormalY=0 NormalZ=1 AngleXU=0 Radius=1 StartAngle=3.14159 EndAngle=6.28319
    g3: LineSegment StartX=2 StartY=9.5 StartZ=0 EndX=2 EndY=7.5 EndZ=0
    g4: LineSegment StartX=4 StartY=9.5 StartZ=0 EndX=4 EndY=7.5 EndZ=0
    g5: ArcOfCircle CenterX=18 CenterY=9.5 CenterZ=0 NormalX=0 NormalY=0 NormalZ=1 AngleXU=0 Radius=1 StartAngle=-9e-16 EndAngle=3.14159
    g6: ArcOfCircle CenterX=18 CenterY=7.5 CenterZ=0 NormalX=0 NormalY=0 NormalZ=1 AngleXU=0 Radius=1 StartAngle=3.14159 EndAngle=6.28319
    g7: LineSegment StartX=17 StartY=9.5 StartZ=0 EndX=17 EndY=7.5 EndZ=0
    g8: LineSegment StartX=19 StartY=9.5 StartZ=0 EndX=19 EndY=7.5 EndZ=0
  constraints (24):
    c: PointOnObject(g0,g-2)
    c: PointOnObject(g0,g-5)
    c: Horizontal(g0)
    c: DistanceY(g0,g-3) = 8.5
    c: Tangent(g1,g4) = 1.5708
    c: Tangent(g1,g3) = -1.5708
    c: Tangent(g3,g2) = -1.5708
    c: Tangent(g4,g2) = 1.5708
    c: Vertical(g3)
    c: Equal(g1,g2)
    c: Tangent(g5,g8) = 1.5708
    c: Tangent(g5,g7) = -1.5708
    c: Tangent(g7,g6) = -1.5708
    c: Tangent(g8,g6) = 1.5708
    c: Vertical(g7)
    c: Equal(g5,g6)
    c: Equal(g1,g5)
    c: Equal(g4,g7)
    c: DistanceY(g4,g4) = 2
    c: Radius(g1) = 1
    c: Horizontal(g5,g1)
    c: DistanceX(g0,g1) = 3
    c: DistanceX(g5,g0) = 2
    c: DistanceY(g0,g1) = 1
FEATURE [PartDesign::Pad] Pad115
  BaseFeature = -> Pocket085
  Direction = (1,1,1)
  Length = 1
  Length2 = 100
  Placement = pos=(0,0,0) rot=(0.57735,0.57735,0.57735;2.0944rad)
  Profile = -> Sketch234
  Type = 0
FEATURE [Sketcher::SketchObject] Sketch235
  ExternalGeometry = -> [Pad115]
  FullyConstrained = true
  MapMode = 5
  Placement = pos=(0,0,1e-16) rot=(0.707107,0.707107,0;3.14159rad)
  Support = -> [Pad115]
  sketch-geometry (9):
    g0: LineSegment StartX=0 StartY=8.5 StartZ=0 EndX=-20 EndY=8.5 EndZ=0
    g1: ArcOfCircle CenterX=-3 CenterY=7.5 CenterZ=0 NormalX=0 NormalY=0 NormalZ=1 AngleXU=0 Radius=1 StartAngle=3.14159 EndAngle=6.28319
    g2: ArcOfCircle CenterX=-3 CenterY=9.5 CenterZ=0 NormalX=0 NormalY=0 NormalZ=1 AngleXU=0 Radius=1 StartAngle=3e-16 EndAngle=3.14159
    g3: LineSegment StartX=-2 StartY=7.5 StartZ=0 EndX=-2 EndY=9.5 EndZ=0
    g4: LineSegment StartX=-4 StartY=7.5 StartZ=0 EndX=-4 EndY=9.5 EndZ=0
    g5: ArcOfCircle CenterX=-18 CenterY=9.5 CenterZ=0 NormalX=0 NormalY=0 NormalZ=1 AngleXU=0 Radius=1 StartAngle=0 EndAngle=3.14159
    g6: ArcOfCircle CenterX=-18 CenterY=7.5 CenterZ=0 NormalX=0 NormalY=0 NormalZ=1 AngleXU=0 Radius=1 StartAngle=3.14159 EndAngle=6.28319
    g7: LineSegment StartX=-19 StartY=9.5 StartZ=0 EndX=-19 EndY=7.5 EndZ=0
    g8: LineSegment StartX=-17 StartY=9.5 StartZ=0 EndX=-17 EndY=7.5 EndZ=0
  constraints (24):
    c: PointOnObject(g0,g-2)
    c: PointOnObject(g0,g-4)
    c: Horizontal(g0)
    c: DistanceY(g0,g-3) = 8.5
    c: Tangent(g1,g4) = 1.5708
    c: Tangent(g1,g3) = -1.5708
    c: Tangent(g3,g2) = -1.5708
    c: Tangent(g4,g2) = 1.5708
    c: Vertical(g3)
    c: Equal(g1,g2)
    c: Radius(g2) = 1
    c: DistanceY(g4,g4) = 2
    c: DistanceY(g0,g2) = 1
    c: DistanceX(g2,g0) = 3
    c: Tangent(g5,g8) = 1.5708
    c: Tangent(g5,g7) = -1.5708
    c: Tangent(g7,g6) = -1.5708
    c: Tangent(g8,g6) = 1.5708
    c: Vertical(g7)
    c: Equal(g5,g6)
    c: Equal(g5,g2)
    c: Equal(g8,g4)
    c: Horizontal(g5,g2)
    c: DistanceX(g0,g5) = 2
FEATURE [PartDesign::Pad] Pad116
  BaseFeature = -> Pad115
  Direction = (1,1,1)
  Length = 1
  Length2 = 100
  Placement = pos=(0,0,0) rot=(0.57735,0.57735,0.57735;2.0944rad)
  Profile = -> Sketch235
  Type = 0
FEATURE [PartDesign::Body] Body200  label="Corner003"
  Group = -> [Sketch230,Pad114,Sketch231,Pocket083,Sketch232,Pocket084,Sketch233,Pocket085,Sketch234,Pad115,Sketch235,Pad116]
  Origin = -> Origin273
  Tip = -> Pad116
FEATURE [App::Part] Part073  label="soporte90-004"
  Group = -> [Body200]
  Origin = -> Origin274
  Placement = pos=(20,1,20) rot=(0,0,1;1.5708rad)
FEATURE [Sketcher::SketchObject] Sketch236
  FullyConstrained = true
  MapMode = 5
  Placement = pos=(0,0,0) rot=(0.57735,0.57735,0.57735;2.0944rad)
  Support = -> [YZ_Plane269]
  sketch-geometry (5):
    g0: LineSegment StartX=0 StartY=0 StartZ=0 EndX=0 EndY=20 EndZ=0
    g1: LineSegment StartX=0 StartY=20 StartZ=0 EndX=-3 EndY=20 EndZ=0
    g2: LineSegment StartX=-3 StartY=20 StartZ=0 EndX=-20 EndY=3 EndZ=0
    g3: LineSegment StartX=-20 StartY=3 StartZ=0 EndX=-20 EndY=0 EndZ=0
    g4: LineSegment StartX=-20 StartY=0 StartZ=0 EndX=0 EndY=0 EndZ=0
  constraints (14):
    c: Coincident(g-1,g0)
    c: PointOnObject(g0,g-2)
    c: Coincident(g0,g1)
    c: Horizontal(g1)
    c: Coincident(g1,g2)
    c: Coincident(g2,g3)
    c: PointOnObject(g3,g-1)
    c: Vertical(g3)
    c: Coincident(g3,g4)
    c: Coincident(g4,g0)
    c: DistanceY(g0,g0) = 20
    c: DistanceY(g3,g3) = 3
    c: DistanceX(g1,g1) = 3
    c: DistanceX(g4,g4) = 20
FEATURE [PartDesign::Pad] Pad117
  Direction = (1,1,1)
  Length = 17
  Length2 = 100
  Placement = pos=(0,0,0) rot=(0.57735,0.57735,0.57735;2.0944rad)
  Profile = -> Sketch236
  Type = 0
FEATURE [Sketcher::SketchObject] Sketch237
  ExternalGeometry = -> [Pad117]
  FullyConstrained = true
  MapMode = 5
  Placement = pos=(-8.8e-15,-20,4.4e-15) rot=(-0.57735,-0.57735,0.57735;4.18879rad)
  Support = -> [Pad117]
  sketch-geometry (4):
    g0: LineSegment StartX=-3 StartY=2 StartZ=0 EndX=-20 EndY=2 EndZ=0
    g1: LineSegment StartX=-20 StartY=2 StartZ=0 EndX=-20 EndY=15 EndZ=0
    g2: LineSegment StartX=-20 StartY=15 StartZ=0 EndX=-3 EndY=15 EndZ=0
    g3: LineSegment StartX=-3 StartY=15 StartZ=0 EndX=-3 EndY=2 EndZ=0
  constraints (12):
    c: Coincident(g0,g1)
    c: Coincident(g1,g2)
    c: Coincident(g2,g3)
    c: Coincident(g3,g0)
    c: Horizontal(g0)
    c: Horizontal(g2)
    c: Vertical(g1)
    c: Vertical(g3)
    c: PointOnObject(g0,g-3)
    c: DistanceY(g1,g-6) = 2
    c: DistanceY(g-6,g0) = 2
    c: PointOnObject(g1,g-6)
FEATURE [PartDesign::Pocket] Pocket086
  BaseFeature = -> Pad117
  Length = 17
  Length2 = 100
  Placement = pos=(0,0,0) rot=(0.57735,0.57735,0.57735;2.0944rad)
  Profile = -> Sketch237
  Type = 0
FEATURE [Sketcher::SketchObject] Sketch238
  ExternalGeometry = -> [Pocket086]
  FullyConstrained = true
  MapMode = 5
  Placement = pos=(-1.7e-15,-3,6e-16) rot=(-0.57735,-0.57735,0.57735;4.18879rad)
  Support = -> [Pocket086]
  sketch-geometry (5):
    g0: LineSegment StartX=-20 StartY=8.5 StartZ=0 EndX=-3 EndY=8.5 EndZ=0
    g1: ArcOfCircle CenterX=-10 CenterY=8.5 CenterZ=0 NormalX=0 NormalY=0 NormalZ=1 AngleXU=0 Radius=3 StartAngle=4.71239 EndAngle=7.85398
    g2: ArcOfCircle CenterX=-13 CenterY=8.5 CenterZ=0 NormalX=0 NormalY=0 NormalZ=1 AngleXU=0 Radius=3 StartAngle=1.5708 EndAngle=4.71239
    g3: LineSegment StartX=-10 StartY=11.5 StartZ=0 EndX=-13 EndY=11.5 EndZ=0
    g4: LineSegment StartX=-10 StartY=5.5 StartZ=0 EndX=-13 EndY=5.5 EndZ=0
  constraints (14):
    c: PointOnObject(g0,g-6)
    c: PointOnObject(g0,g-4)
    c: Horizontal(g0)
    c: DistanceY(g0,g-4) = 6.5
    c: Tangent(g1,g4) = 1.5708
    c: Tangent(g1,g3) = -1.5708
    c: Tangent(g3,g2) = -1.5708
    c: Tangent(g4,g2) = 1.5708
    c: Horizontal(g3)
    c: Equal(g1,g2)
    c: PointOnObject(g1,g0)
    c: Radius(g1) = 3
    c: DistanceX(g3,g3) = 3
    c: DistanceX(g0,g2) = 7
FEATURE [PartDesign::Pocket] Pocket087
  BaseFeature = -> Pocket086
  Length = 5
  Length2 = 100
  Placement = pos=(0,0,0) rot=(0.57735,0.57735,0.57735;2.0944rad)
  Profile = -> Sketch238
  Type = 2
FEATURE [Sketcher::SketchObject] Sketch239
  ExternalGeometry = -> [Pocket087]
  FullyConstrained = true
  MapMode = 5
  Placement = pos=(-3e-16,1.2e-15,3) rot=(0,0,-1;1.5708rad)
  Support = -> [Pocket087]
  sketch-geometry (5):
    g0: LineSegment StartX=3 StartY=8.5 StartZ=0 EndX=20 EndY=8.5 EndZ=0
    g1: ArcOfCircle CenterX=10 CenterY=8.5 CenterZ=0 NormalX=0 NormalY=0 NormalZ=1 AngleXU=0 Radius=3 StartAngle=1.5708 EndAngle=4.71239
    g2: ArcOfCircle CenterX=13 CenterY=8.5 CenterZ=0 NormalX=0 NormalY=0 NormalZ=1 AngleXU=0 Radius=3 StartAngle=4.71239 EndAngle=7.85398
    g3: LineSegment StartX=10 StartY=5.5 StartZ=0 EndX=13 EndY=5.5 EndZ=0
    g4: LineSegment StartX=10 StartY=11.5 StartZ=0 EndX=13 EndY=11.5 EndZ=0
  constraints (14):
    c: PointOnObject(g0,g-4)
    c: PointOnObject(g0,g-5)
    c: Horizontal(g0)
    c: DistanceY(g0,g-4) = 6.5
    c: Tangent(g1,g4) = 1.5708
    c: Tangent(g1,g3) = -1.5708
    c: Tangent(g3,g2) = -1.5708
    c: Tangent(g4,g2) = 1.5708
    c: Horizontal(g3)
    c: Equal(g1,g2)
    c: PointOnObject(g1,g0)
    c: Radius(g2) = 3
    c: DistanceX(g4,g4) = 3
    c: DistanceX(g2,g0) = 7
FEATURE [PartDesign::Pocket] Pocket088
  BaseFeature = -> Pocket087
  Length = 5
  Length2 = 100
  Placement = pos=(0,0,0) rot=(0.57735,0.57735,0.57735;2.0944rad)
  Profile = -> Sketch239
  Type = 2
FEATURE [Sketcher::SketchObject] Sketch240
  ExternalGeometry = -> [Pocket088]
  FullyConstrained = true
  MapMode = 5
  Placement = pos=(0,0,0) rot=(0.57735,0.57735,0.57735;4.18879rad)
  Support = -> [Pocket088]
  sketch-geometry (9):
    g0: LineSegment StartX=0 StartY=8.5 StartZ=0 EndX=20 EndY=8.5 EndZ=0
    g1: ArcOfCircle CenterX=3 CenterY=9.5 CenterZ=0 NormalX=0 NormalY=0 NormalZ=1 AngleXU=0 Radius=1 StartAngle=0 EndAngle=3.14159
    g2: ArcOfCircle CenterX=3 CenterY=7.5 CenterZ=0 NormalX=0 NormalY=0 NormalZ=1 AngleXU=0 Radius=1 StartAngle=3.14159 EndAngle=6.28319
    g3: LineSegment StartX=2 StartY=9.5 StartZ=0 EndX=2 EndY=7.5 EndZ=0
    g4: LineSegment StartX=4 StartY=9.5 StartZ=0 EndX=4 EndY=7.5 EndZ=0
    g5: ArcOfCircle CenterX=18 CenterY=9.5 CenterZ=0 NormalX=0 NormalY=0 NormalZ=1 AngleXU=0 Radius=1 StartAngle=-9e-16 EndAngle=3.14159
    g6: ArcOfCircle CenterX=18 CenterY=7.5 CenterZ=0 NormalX=0 NormalY=0 NormalZ=1 AngleXU=0 Radius=1 StartAngle=3.14159 EndAngle=6.28319
    g7: LineSegment StartX=17 StartY=9.5 StartZ=0 EndX=17 EndY=7.5 EndZ=0
    g8: LineSegment StartX=19 StartY=9.5 StartZ=0 EndX=19 EndY=7.5 EndZ=0
  constraints (24):
    c: PointOnObject(g0,g-2)
    c: PointOnObject(g0,g-5)
    c: Horizontal(g0)
    c: DistanceY(g0,g-3) = 8.5
    c: Tangent(g1,g4) = 1.5708
    c: Tangent(g1,g3) = -1.5708
    c: Tangent(g3,g2) = -1.5708
    c: Tangent(g4,g2) = 1.5708
    c: Vertical(g3)
    c: Equal(g1,g2)
    c: Tangent(g5,g8) = 1.5708
    c: Tangent(g5,g7) = -1.5708
    c: Tangent(g7,g6) = -1.5708
    c: Tangent(g8,g6) = 1.5708
    c: Vertical(g7)
    c: Equal(g5,g6)
    c: Equal(g1,g5)
    c: Equal(g4,g7)
    c: DistanceY(g4,g4) = 2
    c: Radius(g1) = 1
    c: Horizontal(g5,g1)
    c: DistanceX(g0,g1) = 3
    c: DistanceX(g5,g0) = 2
    c: DistanceY(g0,g1) = 1
FEATURE [PartDesign::Pad] Pad118
  BaseFeature = -> Pocket088
  Direction = (1,1,1)
  Length = 1
  Length2 = 100
  Placement = pos=(0,0,0) rot=(0.57735,0.57735,0.57735;2.0944rad)
  Profile = -> Sketch240
  Type = 0
FEATURE [Sketcher::SketchObject] Sketch241
  ExternalGeometry = -> [Pad118]
  FullyConstrained = true
  MapMode = 5
  Placement = pos=(0,0,1e-16) rot=(0.707107,0.707107,0;3.14159rad)
  Support = -> [Pad118]
  sketch-geometry (9):
    g0: LineSegment StartX=0 StartY=8.5 StartZ=0 EndX=-20 EndY=8.5 EndZ=0
    g1: ArcOfCircle CenterX=-3 CenterY=7.5 CenterZ=0 NormalX=0 NormalY=0 NormalZ=1 AngleXU=0 Radius=1 StartAngle=3.14159 EndAngle=6.28319
    g2: ArcOfCircle CenterX=-3 CenterY=9.5 CenterZ=0 NormalX=0 NormalY=0 NormalZ=1 AngleXU=0 Radius=1 StartAngle=3e-16 EndAngle=3.14159
    g3: LineSegment StartX=-2 StartY=7.5 StartZ=0 EndX=-2 EndY=9.5 EndZ=0
    g4: LineSegment StartX=-4 StartY=7.5 StartZ=0 EndX=-4 EndY=9.5 EndZ=0
    g5: ArcOfCircle CenterX=-18 CenterY=9.5 CenterZ=0 NormalX=0 NormalY=0 NormalZ=1 AngleXU=0 Radius=1 StartAngle=0 EndAngle=3.14159
    g6: ArcOfCircle CenterX=-18 CenterY=7.5 CenterZ=0 NormalX=0 NormalY=0 NormalZ=1 AngleXU=0 Radius=1 StartAngle=3.14159 EndAngle=6.28319
    g7: LineSegment StartX=-19 StartY=9.5 StartZ=0 EndX=-19 EndY=7.5 EndZ=0
    g8: LineSegment StartX=-17 StartY=9.5 StartZ=0 EndX=-17 EndY=7.5 EndZ=0
  constraints (24):
    c: PointOnObject(g0,g-2)
    c: PointOnObject(g0,g-4)
    c: Horizontal(g0)
    c: DistanceY(g0,g-3) = 8.5
    c: Tangent(g1,g4) = 1.5708
    c: Tangent(g1,g3) = -1.5708
    c: Tangent(g3,g2) = -1.5708
    c: Tangent(g4,g2) = 1.5708
    c: Vertical(g3)
    c: Equal(g1,g2)
    c: Radius(g2) = 1
    c: DistanceY(g4,g4) = 2
    c: DistanceY(g0,g2) = 1
    c: DistanceX(g2,g0) = 3
    c: Tangent(g5,g8) = 1.5708
    c: Tangent(g5,g7) = -1.5708
    c: Tangent(g7,g6) = -1.5708
    c: Tangent(g8,g6) = 1.5708
    c: Vertical(g7)
    c: Equal(g5,g6)
    c: Equal(g5,g2)
    c: Equal(g8,g4)
    c: Horizontal(g5,g2)
    c: DistanceX(g0,g5) = 2
FEATURE [PartDesign::Pad] Pad119
  BaseFeature = -> Pad118
  Direction = (1,1,1)
  Length = 1
  Length2 = 100
  Placement = pos=(0,0,0) rot=(0.57735,0.57735,0.57735;2.0944rad)
  Profile = -> Sketch241
  Type = 0
FEATURE [PartDesign::Body] Body201  label="Corner004"
  Group = -> [Sketch236,Pad117,Sketch237,Pocket086,Sketch238,Pocket087,Sketch239,Pocket088,Sketch240,Pad118,Sketch241,Pad119]
  Origin = -> Origin275
  Tip = -> Pad119
FEATURE [App::Part] Part074  label="soporte90-005"
  Group = -> [Body201]
  Origin = -> Origin276
  Placement = pos=(20,340,170) rot=(0.707107,-0.707107,0;3.14159rad)
FEATURE [Sketcher::SketchObject] Sketch242
  FullyConstrained = true
  MapMode = 5
  Placement = pos=(0,0,0) rot=(0.57735,0.57735,0.57735;2.0944rad)
  Support = -> [YZ_Plane271]
  sketch-geometry (5):
    g0: LineSegment StartX=0 StartY=0 StartZ=0 EndX=0 EndY=20 EndZ=0
    g1: LineSegment StartX=0 StartY=20 StartZ=0 EndX=-3 EndY=20 EndZ=0
    g2: LineSegment StartX=-3 StartY=20 StartZ=0 EndX=-20 EndY=3 EndZ=0
    g3: LineSegment StartX=-20 StartY=3 StartZ=0 EndX=-20 EndY=0 EndZ=0
    g4: LineSegment StartX=-20 StartY=0 StartZ=0 EndX=0 EndY=0 EndZ=0
  constraints (14):
    c: Coincident(g-1,g0)
    c: PointOnObject(g0,g-2)
    c: Coincident(g0,g1)
    c: Horizontal(g1)
    c: Coincident(g1,g2)
    c: Coincident(g2,g3)
    c: PointOnObject(g3,g-1)
    c: Vertical(g3)
    c: Coincident(g3,g4)
    c: Coincident(g4,g0)
    c: DistanceY(g0,g0) = 20
    c: DistanceY(g3,g3) = 3
    c: DistanceX(g1,g1) = 3
    c: DistanceX(g4,g4) = 20
FEATURE [PartDesign::Pad] Pad120
  Direction = (1,1,1)
  Length = 17
  Length2 = 100
  Placement = pos=(0,0,0) rot=(0.57735,0.57735,0.57735;2.0944rad)
  Profile = -> Sketch242
  Type = 0
FEATURE [Sketcher::SketchObject] Sketch243
  ExternalGeometry = -> [Pad120]
  FullyConstrained = true
  MapMode = 5
  Placement = pos=(-8.8e-15,-20,4.4e-15) rot=(-0.57735,-0.57735,0.57735;4.18879rad)
  Support = -> [Pad120]
  sketch-geometry (4):
    g0: LineSegment StartX=-3 StartY=2 StartZ=0 EndX=-20 EndY=2 EndZ=0
    g1: LineSegment StartX=-20 StartY=2 StartZ=0 EndX=-20 EndY=15 EndZ=0
    g2: LineSegment StartX=-20 StartY=15 StartZ=0 EndX=-3 EndY=15 EndZ=0
    g3: LineSegment StartX=-3 StartY=15 StartZ=0 EndX=-3 EndY=2 EndZ=0
  constraints (12):
    c: Coincident(g0,g1)
    c: Coincident(g1,g2)
    c: Coincident(g2,g3)
    c: Coincident(g3,g0)
    c: Horizontal(g0)
    c: Horizontal(g2)
    c: Vertical(g1)
    c: Vertical(g3)
    c: PointOnObject(g0,g-3)
    c: DistanceY(g1,g-6) = 2
    c: DistanceY(g-6,g0) = 2
    c: PointOnObject(g1,g-6)
FEATURE [PartDesign::Pocket] Pocket089
  BaseFeature = -> Pad120
  Length = 17
  Length2 = 100
  Placement = pos=(0,0,0) rot=(0.57735,0.57735,0.57735;2.0944rad)
  Profile = -> Sketch243
  Type = 0
FEATURE [Sketcher::SketchObject] Sketch244
  ExternalGeometry = -> [Pocket089]
  FullyConstrained = true
  MapMode = 5
  Placement = pos=(-1.7e-15,-3,6e-16) rot=(-0.57735,-0.57735,0.57735;4.18879rad)
  Support = -> [Pocket089]
  sketch-geometry (5):
    g0: LineSegment StartX=-20 StartY=8.5 StartZ=0 EndX=-3 EndY=8.5 EndZ=0
    g1: ArcOfCircle CenterX=-10 CenterY=8.5 CenterZ=0 NormalX=0 NormalY=0 NormalZ=1 AngleXU=0 Radius=3 StartAngle=4.71239 EndAngle=7.85398
    g2: ArcOfCircle CenterX=-13 CenterY=8.5 CenterZ=0 NormalX=0 NormalY=0 NormalZ=1 AngleXU=0 Radius=3 StartAngle=1.5708 EndAngle=4.71239
    g3: LineSegment StartX=-10 StartY=11.5 StartZ=0 EndX=-13 EndY=11.5 EndZ=0
    g4: LineSegment StartX=-10 StartY=5.5 StartZ=0 EndX=-13 EndY=5.5 EndZ=0
  constraints (14):
    c: PointOnObject(g0,g-6)
    c: PointOnObject(g0,g-4)
    c: Horizontal(g0)
    c: DistanceY(g0,g-4) = 6.5
    c: Tangent(g1,g4) = 1.5708
    c: Tangent(g1,g3) = -1.5708
    c: Tangent(g3,g2) = -1.5708
    c: Tangent(g4,g2) = 1.5708
    c: Horizontal(g3)
    c: Equal(g1,g2)
    c: PointOnObject(g1,g0)
    c: Radius(g1) = 3
    c: DistanceX(g3,g3) = 3
    c: DistanceX(g0,g2) = 7
FEATURE [PartDesign::Pocket] Pocket090
  BaseFeature = -> Pocket089
  Length = 5
  Length2 = 100
  Placement = pos=(0,0,0) rot=(0.57735,0.57735,0.57735;2.0944rad)
  Profile = -> Sketch244
  Type = 2
FEATURE [Sketcher::SketchObject] Sketch245
  ExternalGeometry = -> [Pocket090]
  FullyConstrained = true
  MapMode = 5
  Placement = pos=(-3e-16,1.2e-15,3) rot=(0,0,-1;1.5708rad)
  Support = -> [Pocket090]
  sketch-geometry (5):
    g0: LineSegment StartX=3 StartY=8.5 StartZ=0 EndX=20 EndY=8.5 EndZ=0
    g1: ArcOfCircle CenterX=10 CenterY=8.5 CenterZ=0 NormalX=0 NormalY=0 NormalZ=1 AngleXU=0 Radius=3 StartAngle=1.5708 EndAngle=4.71239
    g2: ArcOfCircle CenterX=13 CenterY=8.5 CenterZ=0 NormalX=0 NormalY=0 NormalZ=1 AngleXU=0 Radius=3 StartAngle=4.71239 EndAngle=7.85398
    g3: LineSegment StartX=10 StartY=5.5 StartZ=0 EndX=13 EndY=5.5 EndZ=0
    g4: LineSegment StartX=10 StartY=11.5 StartZ=0 EndX=13 EndY=11.5 EndZ=0
  constraints (14):
    c: PointOnObject(g0,g-4)
    c: PointOnObject(g0,g-5)
    c: Horizontal(g0)
    c: DistanceY(g0,g-4) = 6.5
    c: Tangent(g1,g4) = 1.5708
    c: Tangent(g1,g3) = -1.5708
    c: Tangent(g3,g2) = -1.5708
    c: Tangent(g4,g2) = 1.5708
    c: Horizontal(g3)
    c: Equal(g1,g2)
    c: PointOnObject(g1,g0)
    c: Radius(g2) = 3
    c: DistanceX(g4,g4) = 3
    c: DistanceX(g2,g0) = 7
FEATURE [PartDesign::Pocket] Pocket091
  BaseFeature = -> Pocket090
  Length = 5
  Length2 = 100
  Placement = pos=(0,0,0) rot=(0.57735,0.57735,0.57735;2.0944rad)
  Profile = -> Sketch245
  Type = 2
FEATURE [Sketcher::SketchObject] Sketch246
  ExternalGeometry = -> [Pocket091]
  FullyConstrained = true
  MapMode = 5
  Placement = pos=(0,0,0) rot=(0.57735,0.57735,0.57735;4.18879rad)
  Support = -> [Pocket091]
  sketch-geometry (9):
    g0: LineSegment StartX=0 StartY=8.5 StartZ=0 EndX=20 EndY=8.5 EndZ=0
    g1: ArcOfCircle CenterX=3 CenterY=9.5 CenterZ=0 NormalX=0 NormalY=0 NormalZ=1 AngleXU=0 Radius=1 StartAngle=0 EndAngle=3.14159
    g2: ArcOfCircle CenterX=3 CenterY=7.5 CenterZ=0 NormalX=0 NormalY=0 NormalZ=1 AngleXU=0 Radius=1 StartAngle=3.14159 EndAngle=6.28319
    g3: LineSegment StartX=2 StartY=9.5 StartZ=0 EndX=2 EndY=7.5 EndZ=0
    g4: LineSegment StartX=4 StartY=9.5 StartZ=0 EndX=4 EndY=7.5 EndZ=0
    g5: ArcOfCircle CenterX=18 CenterY=9.5 CenterZ=0 NormalX=0 NormalY=0 NormalZ=1 AngleXU=0 Radius=1 StartAngle=-9e-16 EndAngle=3.14159
    g6: ArcOfCircle CenterX=18 CenterY=7.5 CenterZ=0 NormalX=0 NormalY=0 NormalZ=1 AngleXU=0 Radius=1 StartAngle=3.14159 EndAngle=6.28319
    g7: LineSegment StartX=17 StartY=9.5 StartZ=0 EndX=17 EndY=7.5 EndZ=0
    g8: LineSegment StartX=19 StartY=9.5 StartZ=0 EndX=19 EndY=7.5 EndZ=0
  constraints (24):
    c: PointOnObject(g0,g-2)
    c: PointOnObject(g0,g-5)
    c: Horizontal(g0)
    c: DistanceY(g0,g-3) = 8.5
    c: Tangent(g1,g4) = 1.5708
    c: Tangent(g1,g3) = -1.5708
    c: Tangent(g3,g2) = -1.5708
    c: Tangent(g4,g2) = 1.5708
    c: Vertical(g3)
    c: Equal(g1,g2)
    c: Tangent(g5,g8) = 1.5708
    c: Tangent(g5,g7) = -1.5708
    c: Tangent(g7,g6) = -1.5708
    c: Tangent(g8,g6) = 1.5708
    c: Vertical(g7)
    c: Equal(g5,g6)
    c: Equal(g1,g5)
    c: Equal(g4,g7)
    c: DistanceY(g4,g4) = 2
    c: Radius(g1) = 1
    c: Horizontal(g5,g1)
    c: DistanceX(g0,g1) = 3
    c: DistanceX(g5,g0) = 2
    c: DistanceY(g0,g1) = 1
FEATURE [PartDesign::Pad] Pad121
  BaseFeature = -> Pocket091
  Direction = (1,1,1)
  Length = 1
  Length2 = 100
  Placement = pos=(0,0,0) rot=(0.57735,0.57735,0.57735;2.0944rad)
  Profile = -> Sketch246
  Type = 0
FEATURE [Sketcher::SketchObject] Sketch247
  ExternalGeometry = -> [Pad121]
  FullyConstrained = true
  MapMode = 5
  Placement = pos=(0,0,1e-16) rot=(0.707107,0.707107,0;3.14159rad)
  Support = -> [Pad121]
  sketch-geometry (9):
    g0: LineSegment StartX=0 StartY=8.5 StartZ=0 EndX=-20 EndY=8.5 EndZ=0
    g1: ArcOfCircle CenterX=-3 CenterY=7.5 CenterZ=0 NormalX=0 NormalY=0 NormalZ=1 AngleXU=0 Radius=1 StartAngle=3.14159 EndAngle=6.28319
    g2: ArcOfCircle CenterX=-3 CenterY=9.5 CenterZ=0 NormalX=0 NormalY=0 NormalZ=1 AngleXU=0 Radius=1 StartAngle=3e-16 EndAngle=3.14159
    g3: LineSegment StartX=-2 StartY=7.5 StartZ=0 EndX=-2 EndY=9.5 EndZ=0
    g4: LineSegment StartX=-4 StartY=7.5 StartZ=0 EndX=-4 EndY=9.5 EndZ=0
    g5: ArcOfCircle CenterX=-18 CenterY=9.5 CenterZ=0 NormalX=0 NormalY=0 NormalZ=1 AngleXU=0 Radius=1 StartAngle=0 EndAngle=3.14159
    g6: ArcOfCircle CenterX=-18 CenterY=7.5 CenterZ=0 NormalX=0 NormalY=0 NormalZ=1 AngleXU=0 Radius=1 StartAngle=3.14159 EndAngle=6.28319
    g7: LineSegment StartX=-19 StartY=9.5 StartZ=0 EndX=-19 EndY=7.5 EndZ=0
    g8: LineSegment StartX=-17 StartY=9.5 StartZ=0 EndX=-17 EndY=7.5 EndZ=0
  constraints (24):
    c: PointOnObject(g0,g-2)
    c: PointOnObject(g0,g-4)
    c: Horizontal(g0)
    c: DistanceY(g0,g-3) = 8.5
    c: Tangent(g1,g4) = 1.5708
    c: Tangent(g1,g3) = -1.5708
    c: Tangent(g3,g2) = -1.5708
    c: Tangent(g4,g2) = 1.5708
    c: Vertical(g3)
    c: Equal(g1,g2)
    c: Radius(g2) = 1
    c: DistanceY(g4,g4) = 2
    c: DistanceY(g0,g2) = 1
    c: DistanceX(g2,g0) = 3
    c: Tangent(g5,g8) = 1.5708
    c: Tangent(g5,g7) = -1.5708
    c: Tangent(g7,g6) = -1.5708
    c: Tangent(g8,g6) = 1.5708
    c: Vertical(g7)
    c: Equal(g5,g6)
    c: Equal(g5,g2)
    c: Equal(g8,g4)
    c: Horizontal(g5,g2)
    c: DistanceX(g0,g5) = 2
FEATURE [PartDesign::Pad] Pad122
  BaseFeature = -> Pad121
  Direction = (1,1,1)
  Length = 1
  Length2 = 100
  Placement = pos=(0,0,0) rot=(0.57735,0.57735,0.57735;2.0944rad)
  Profile = -> Sketch247
  Type = 0
FEATURE [PartDesign::Body] Body202  label="Corner005"
  Group = -> [Sketch242,Pad120,Sketch243,Pocket089,Sketch244,Pocket090,Sketch245,Pocket091,Sketch246,Pad121,Sketch247,Pad122]
  Origin = -> Origin277
  Tip = -> Pad122
FEATURE [App::Part] Part075  label="soporte90-006"
  Group = -> [Body202]
  Origin = -> Origin278
  Placement = pos=(320,1,170) rot=(0.707107,0.707107,0;3.14159rad)
FEATURE [Sketcher::SketchObject] Sketch248
  FullyConstrained = true
  MapMode = 5
  Placement = pos=(0,0,0) rot=(0.57735,0.57735,0.57735;2.0944rad)
  Support = -> [YZ_Plane273]
  sketch-geometry (5):
    g0: LineSegment StartX=0 StartY=0 StartZ=0 EndX=0 EndY=20 EndZ=0
    g1: LineSegment StartX=0 StartY=20 StartZ=0 EndX=-3 EndY=20 EndZ=0
    g2: LineSegment StartX=-3 StartY=20 StartZ=0 EndX=-20 EndY=3 EndZ=0
    g3: LineSegment StartX=-20 StartY=3 StartZ=0 EndX=-20 EndY=0 EndZ=0
    g4: LineSegment StartX=-20 StartY=0 StartZ=0 EndX=0 EndY=0 EndZ=0
  constraints (14):
    c: Coincident(g-1,g0)
    c: PointOnObject(g0,g-2)
    c: Coincident(g0,g1)
    c: Horizontal(g1)
    c: Coincident(g1,g2)
    c: Coincident(g2,g3)
    c: PointOnObject(g3,g-1)
    c: Vertical(g3)
    c: Coincident(g3,g4)
    c: Coincident(g4,g0)
    c: DistanceY(g0,g0) = 20
    c: DistanceY(g3,g3) = 3
    c: DistanceX(g1,g1) = 3
    c: DistanceX(g4,g4) = 20
FEATURE [PartDesign::Pad] Pad123
  Direction = (1,1,1)
  Length = 17
  Length2 = 100
  Placement = pos=(0,0,0) rot=(0.57735,0.57735,0.57735;2.0944rad)
  Profile = -> Sketch248
  Type = 0
FEATURE [Sketcher::SketchObject] Sketch249
  ExternalGeometry = -> [Pad123]
  FullyConstrained = true
  MapMode = 5
  Placement = pos=(-8.8e-15,-20,4.4e-15) rot=(-0.57735,-0.57735,0.57735;4.18879rad)
  Support = -> [Pad123]
  sketch-geometry (4):
    g0: LineSegment StartX=-3 StartY=2 StartZ=0 EndX=-20 EndY=2 EndZ=0
    g1: LineSegment StartX=-20 StartY=2 StartZ=0 EndX=-20 EndY=15 EndZ=0
    g2: LineSegment StartX=-20 StartY=15 StartZ=0 EndX=-3 EndY=15 EndZ=0
    g3: LineSegment StartX=-3 StartY=15 StartZ=0 EndX=-3 EndY=2 EndZ=0
  constraints (12):
    c: Coincident(g0,g1)
    c: Coincident(g1,g2)
    c: Coincident(g2,g3)
    c: Coincident(g3,g0)
    c: Horizontal(g0)
    c: Horizontal(g2)
    c: Vertical(g1)
    c: Vertical(g3)
    c: PointOnObject(g0,g-3)
    c: DistanceY(g1,g-6) = 2
    c: DistanceY(g-6,g0) = 2
    c: PointOnObject(g1,g-6)
FEATURE [PartDesign::Pocket] Pocket092
  BaseFeature = -> Pad123
  Length = 17
  Length2 = 100
  Placement = pos=(0,0,0) rot=(0.57735,0.57735,0.57735;2.0944rad)
  Profile = -> Sketch249
  Type = 0
FEATURE [Sketcher::SketchObject] Sketch250
  ExternalGeometry = -> [Pocket092]
  FullyConstrained = true
  MapMode = 5
  Placement = pos=(-1.7e-15,-3,6e-16) rot=(-0.57735,-0.57735,0.57735;4.18879rad)
  Support = -> [Pocket092]
  sketch-geometry (5):
    g0: LineSegment StartX=-20 StartY=8.5 StartZ=0 EndX=-3 EndY=8.5 EndZ=0
    g1: ArcOfCircle CenterX=-10 CenterY=8.5 CenterZ=0 NormalX=0 NormalY=0 NormalZ=1 AngleXU=0 Radius=3 StartAngle=4.71239 EndAngle=7.85398
    g2: ArcOfCircle CenterX=-13 CenterY=8.5 CenterZ=0 NormalX=0 NormalY=0 NormalZ=1 AngleXU=0 Radius=3 StartAngle=1.5708 EndAngle=4.71239
    g3: LineSegment StartX=-10 StartY=11.5 StartZ=0 EndX=-13 EndY=11.5 EndZ=0
    g4: LineSegment StartX=-10 StartY=5.5 StartZ=0 EndX=-13 EndY=5.5 EndZ=0
  constraints (14):
    c: PointOnObject(g0,g-6)
    c: PointOnObject(g0,g-4)
    c: Horizontal(g0)
    c: DistanceY(g0,g-4) = 6.5
    c: Tangent(g1,g4) = 1.5708
    c: Tangent(g1,g3) = -1.5708
    c: Tangent(g3,g2) = -1.5708
    c: Tangent(g4,g2) = 1.5708
    c: Horizontal(g3)
    c: Equal(g1,g2)
    c: PointOnObject(g1,g0)
    c: Radius(g1) = 3
    c: DistanceX(g3,g3) = 3
    c: DistanceX(g0,g2) = 7
FEATURE [PartDesign::Pocket] Pocket093
  BaseFeature = -> Pocket092
  Length = 5
  Length2 = 100
  Placement = pos=(0,0,0) rot=(0.57735,0.57735,0.57735;2.0944rad)
  Profile = -> Sketch250
  Type = 2
FEATURE [Sketcher::SketchObject] Sketch251
  ExternalGeometry = -> [Pocket093]
  FullyConstrained = true
  MapMode = 5
  Placement = pos=(-3e-16,1.2e-15,3) rot=(0,0,-1;1.5708rad)
  Support = -> [Pocket093]
  sketch-geometry (5):
    g0: LineSegment StartX=3 StartY=8.5 StartZ=0 EndX=20 EndY=8.5 EndZ=0
    g1: ArcOfCircle CenterX=10 CenterY=8.5 CenterZ=0 NormalX=0 NormalY=0 NormalZ=1 AngleXU=0 Radius=3 StartAngle=1.5708 EndAngle=4.71239
    g2: ArcOfCircle CenterX=13 CenterY=8.5 CenterZ=0 NormalX=0 NormalY=0 NormalZ=1 AngleXU=0 Radius=3 StartAngle=4.71239 EndAngle=7.85398
    g3: LineSegment StartX=10 StartY=5.5 StartZ=0 EndX=13 EndY=5.5 EndZ=0
    g4: LineSegment StartX=10 StartY=11.5 StartZ=0 EndX=13 EndY=11.5 EndZ=0
  constraints (14):
    c: PointOnObject(g0,g-4)
    c: PointOnObject(g0,g-5)
    c: Horizontal(g0)
    c: DistanceY(g0,g-4) = 6.5
    c: Tangent(g1,g4) = 1.5708
    c: Tangent(g1,g3) = -1.5708
    c: Tangent(g3,g2) = -1.5708
    c: Tangent(g4,g2) = 1.5708
    c: Horizontal(g3)
    c: Equal(g1,g2)
    c: PointOnObject(g1,g0)
    c: Radius(g2) = 3
    c: DistanceX(g4,g4) = 3
    c: DistanceX(g2,g0) = 7
FEATURE [PartDesign::Pocket] Pocket094
  BaseFeature = -> Pocket093
  Length = 5
  Length2 = 100
  Placement = pos=(0,0,0) rot=(0.57735,0.57735,0.57735;2.0944rad)
  Profile = -> Sketch251
  Type = 2
FEATURE [Sketcher::SketchObject] Sketch252
  ExternalGeometry = -> [Pocket094]
  FullyConstrained = true
  MapMode = 5
  Placement = pos=(0,0,0) rot=(0.57735,0.57735,0.57735;4.18879rad)
  Support = -> [Pocket094]
  sketch-geometry (9):
    g0: LineSegment StartX=0 StartY=8.5 StartZ=0 EndX=20 EndY=8.5 EndZ=0
    g1: ArcOfCircle CenterX=3 CenterY=9.5 CenterZ=0 NormalX=0 NormalY=0 NormalZ=1 AngleXU=0 Radius=1 StartAngle=0 EndAngle=3.14159
    g2: ArcOfCircle CenterX=3 CenterY=7.5 CenterZ=0 NormalX=0 NormalY=0 NormalZ=1 AngleXU=0 Radius=1 StartAngle=3.14159 EndAngle=6.28319
    g3: LineSegment StartX=2 StartY=9.5 StartZ=0 EndX=2 EndY=7.5 EndZ=0
    g4: LineSegment StartX=4 StartY=9.5 StartZ=0 EndX=4 EndY=7.5 EndZ=0
    g5: ArcOfCircle CenterX=18 CenterY=9.5 CenterZ=0 NormalX=0 NormalY=0 NormalZ=1 AngleXU=0 Radius=1 StartAngle=-9e-16 EndAngle=3.14159
    g6: ArcOfCircle CenterX=18 CenterY=7.5 CenterZ=0 NormalX=0 NormalY=0 NormalZ=1 AngleXU=0 Radius=1 StartAngle=3.14159 EndAngle=6.28319
    g7: LineSegment StartX=17 StartY=9.5 StartZ=0 EndX=17 EndY=7.5 EndZ=0
    g8: LineSegment StartX=19 StartY=9.5 StartZ=0 EndX=19 EndY=7.5 EndZ=0
  constraints (24):
    c: PointOnObject(g0,g-2)
    c: PointOnObject(g0,g-5)
    c: Horizontal(g0)
    c: DistanceY(g0,g-3) = 8.5
    c: Tangent(g1,g4) = 1.5708
    c: Tangent(g1,g3) = -1.5708
    c: Tangent(g3,g2) = -1.5708
    c: Tangent(g4,g2) = 1.5708
    c: Vertical(g3)
    c: Equal(g1,g2)
    c: Tangent(g5,g8) = 1.5708
    c: Tangent(g5,g7) = -1.5708
    c: Tangent(g7,g6) = -1.5708
    c: Tangent(g8,g6) = 1.5708
    c: Vertical(g7)
    c: Equal(g5,g6)
    c: Equal(g1,g5)
    c: Equal(g4,g7)
    c: DistanceY(g4,g4) = 2
    c: Radius(g1) = 1
    c: Horizontal(g5,g1)
    c: DistanceX(g0,g1) = 3
    c: DistanceX(g5,g0) = 2
    c: DistanceY(g0,g1) = 1
FEATURE [PartDesign::Pad] Pad124
  BaseFeature = -> Pocket094
  Direction = (1,1,1)
  Length = 1
  Length2 = 100
  Placement = pos=(0,0,0) rot=(0.57735,0.57735,0.57735;2.0944rad)
  Profile = -> Sketch252
  Type = 0
FEATURE [Sketcher::SketchObject] Sketch253
  ExternalGeometry = -> [Pad124]
  FullyConstrained = true
  MapMode = 5
  Placement = pos=(0,0,1e-16) rot=(0.707107,0.707107,0;3.14159rad)
  Support = -> [Pad124]
  sketch-geometry (9):
    g0: LineSegment StartX=0 StartY=8.5 StartZ=0 EndX=-20 EndY=8.5 EndZ=0
    g1: ArcOfCircle CenterX=-3 CenterY=7.5 CenterZ=0 NormalX=0 NormalY=0 NormalZ=1 AngleXU=0 Radius=1 StartAngle=3.14159 EndAngle=6.28319
    g2: ArcOfCircle CenterX=-3 CenterY=9.5 CenterZ=0 NormalX=0 NormalY=0 NormalZ=1 AngleXU=0 Radius=1 StartAngle=3e-16 EndAngle=3.14159
    g3: LineSegment StartX=-2 StartY=7.5 StartZ=0 EndX=-2 EndY=9.5 EndZ=0
    g4: LineSegment StartX=-4 StartY=7.5 StartZ=0 EndX=-4 EndY=9.5 EndZ=0
    g5: ArcOfCircle CenterX=-18 CenterY=9.5 CenterZ=0 NormalX=0 NormalY=0 NormalZ=1 AngleXU=0 Radius=1 StartAngle=0 EndAngle=3.14159
    g6: ArcOfCircle CenterX=-18 CenterY=7.5 CenterZ=0 NormalX=0 NormalY=0 NormalZ=1 AngleXU=0 Radius=1 StartAngle=3.14159 EndAngle=6.28319
    g7: LineSegment StartX=-19 StartY=9.5 StartZ=0 EndX=-19 EndY=7.5 EndZ=0
    g8: LineSegment StartX=-17 StartY=9.5 StartZ=0 EndX=-17 EndY=7.5 EndZ=0
  constraints (24):
    c: PointOnObject(g0,g-2)
    c: PointOnObject(g0,g-4)
    c: Horizontal(g0)
    c: DistanceY(g0,g-3) = 8.5
    c: Tangent(g1,g4) = 1.5708
    c: Tangent(g1,g3) = -1.5708
    c: Tangent(g3,g2) = -1.5708
    c: Tangent(g4,g2) = 1.5708
    c: Vertical(g3)
    c: Equal(g1,g2)
    c: Radius(g2) = 1
    c: DistanceY(g4,g4) = 2
    c: DistanceY(g0,g2) = 1
    c: DistanceX(g2,g0) = 3
    c: Tangent(g5,g8) = 1.5708
    c: Tangent(g5,g7) = -1.5708
    c: Tangent(g7,g6) = -1.5708
    c: Tangent(g8,g6) = 1.5708
    c: Vertical(g7)
    c: Equal(g5,g6)
    c: Equal(g5,g2)
    c: Equal(g8,g4)
    c: Horizontal(g5,g2)
    c: DistanceX(g0,g5) = 2
FEATURE [PartDesign::Pad] Pad125
  BaseFeature = -> Pad124
  Direction = (1,1,1)
  Length = 1
  Length2 = 100
  Placement = pos=(0,0,0) rot=(0.57735,0.57735,0.57735;2.0944rad)
  Profile = -> Sketch253
  Type = 0
FEATURE [PartDesign::Body] Body203  label="Corner006"
  Group = -> [Sketch248,Pad123,Sketch249,Pocket092,Sketch250,Pocket093,Sketch251,Pocket094,Sketch252,Pad124,Sketch253,Pad125]
  Origin = -> Origin279
  Tip = -> Pad125
FEATURE [App::Part] Part076  label="soporte90-007"
  Group = -> [Body203]
  Origin = -> Origin280
  Placement = pos=(320,19,20) rot=(0,0,1;-1.5708rad)
FEATURE [Sketcher::SketchObject] Sketch254
  FullyConstrained = true
  MapMode = 5
  Placement = pos=(0,0,0) rot=(0.57735,0.57735,0.57735;2.0944rad)
  Support = -> [YZ_Plane275]
  sketch-geometry (5):
    g0: LineSegment StartX=0 StartY=0 StartZ=0 EndX=0 EndY=20 EndZ=0
    g1: LineSegment StartX=0 StartY=20 StartZ=0 EndX=-3 EndY=20 EndZ=0
    g2: LineSegment StartX=-3 StartY=20 StartZ=0 EndX=-20 EndY=3 EndZ=0
    g3: LineSegment StartX=-20 StartY=3 StartZ=0 EndX=-20 EndY=0 EndZ=0
    g4: LineSegment StartX=-20 StartY=0 StartZ=0 EndX=0 EndY=0 EndZ=0
  constraints (14):
    c: Coincident(g-1,g0)
    c: PointOnObject(g0,g-2)
    c: Coincident(g0,g1)
    c: Horizontal(g1)
    c: Coincident(g1,g2)
    c: Coincident(g2,g3)
    c: PointOnObject(g3,g-1)
    c: Vertical(g3)
    c: Coincident(g3,g4)
    c: Coincident(g4,g0)
    c: DistanceY(g0,g0) = 20
    c: DistanceY(g3,g3) = 3
    c: DistanceX(g1,g1) = 3
    c: DistanceX(g4,g4) = 20
FEATURE [PartDesign::Pad] Pad126
  Direction = (1,1,1)
  Length = 17
  Length2 = 100
  Placement = pos=(0,0,0) rot=(0.57735,0.57735,0.57735;2.0944rad)
  Profile = -> Sketch254
  Type = 0
FEATURE [Sketcher::SketchObject] Sketch255
  ExternalGeometry = -> [Pad126]
  FullyConstrained = true
  MapMode = 5
  Placement = pos=(-8.8e-15,-20,4.4e-15) rot=(-0.57735,-0.57735,0.57735;4.18879rad)
  Support = -> [Pad126]
  sketch-geometry (4):
    g0: LineSegment StartX=-3 StartY=2 StartZ=0 EndX=-20 EndY=2 EndZ=0
    g1: LineSegment StartX=-20 StartY=2 StartZ=0 EndX=-20 EndY=15 EndZ=0
    g2: LineSegment StartX=-20 StartY=15 StartZ=0 EndX=-3 EndY=15 EndZ=0
    g3: LineSegment StartX=-3 StartY=15 StartZ=0 EndX=-3 EndY=2 EndZ=0
  constraints (12):
    c: Coincident(g0,g1)
    c: Coincident(g1,g2)
    c: Coincident(g2,g3)
    c: Coincident(g3,g0)
    c: Horizontal(g0)
    c: Horizontal(g2)
    c: Vertical(g1)
    c: Vertical(g3)
    c: PointOnObject(g0,g-3)
    c: DistanceY(g1,g-6) = 2
    c: DistanceY(g-6,g0) = 2
    c: PointOnObject(g1,g-6)
FEATURE [PartDesign::Pocket] Pocket095
  BaseFeature = -> Pad126
  Length = 17
  Length2 = 100
  Placement = pos=(0,0,0) rot=(0.57735,0.57735,0.57735;2.0944rad)
  Profile = -> Sketch255
  Type = 0
FEATURE [Sketcher::SketchObject] Sketch256
  ExternalGeometry = -> [Pocket095]
  FullyConstrained = true
  MapMode = 5
  Placement = pos=(-1.7e-15,-3,6e-16) rot=(-0.57735,-0.57735,0.57735;4.18879rad)
  Support = -> [Pocket095]
  sketch-geometry (5):
    g0: LineSegment StartX=-20 StartY=8.5 StartZ=0 EndX=-3 EndY=8.5 EndZ=0
    g1: ArcOfCircle CenterX=-10 CenterY=8.5 CenterZ=0 NormalX=0 NormalY=0 NormalZ=1 AngleXU=0 Radius=3 StartAngle=4.71239 EndAngle=7.85398
    g2: ArcOfCircle CenterX=-13 CenterY=8.5 CenterZ=0 NormalX=0 NormalY=0 NormalZ=1 AngleXU=0 Radius=3 StartAngle=1.5708 EndAngle=4.71239
    g3: LineSegment StartX=-10 StartY=11.5 StartZ=0 EndX=-13 EndY=11.5 EndZ=0
    g4: LineSegment StartX=-10 StartY=5.5 StartZ=0 EndX=-13 EndY=5.5 EndZ=0
  constraints (14):
    c: PointOnObject(g0,g-6)
    c: PointOnObject(g0,g-4)
    c: Horizontal(g0)
    c: DistanceY(g0,g-4) = 6.5
    c: Tangent(g1,g4) = 1.5708
    c: Tangent(g1,g3) = -1.5708
    c: Tangent(g3,g2) = -1.5708
    c: Tangent(g4,g2) = 1.5708
    c: Horizontal(g3)
    c: Equal(g1,g2)
    c: PointOnObject(g1,g0)
    c: Radius(g1) = 3
    c: DistanceX(g3,g3) = 3
    c: DistanceX(g0,g2) = 7
FEATURE [PartDesign::Pocket] Pocket096
  BaseFeature = -> Pocket095
  Length = 5
  Length2 = 100
  Placement = pos=(0,0,0) rot=(0.57735,0.57735,0.57735;2.0944rad)
  Profile = -> Sketch256
  Type = 2
FEATURE [Sketcher::SketchObject] Sketch257
  ExternalGeometry = -> [Pocket096]
  FullyConstrained = true
  MapMode = 5
  Placement = pos=(-3e-16,1.2e-15,3) rot=(0,0,-1;1.5708rad)
  Support = -> [Pocket096]
  sketch-geometry (5):
    g0: LineSegment StartX=3 StartY=8.5 StartZ=0 EndX=20 EndY=8.5 EndZ=0
    g1: ArcOfCircle CenterX=10 CenterY=8.5 CenterZ=0 NormalX=0 NormalY=0 NormalZ=1 AngleXU=0 Radius=3 StartAngle=1.5708 EndAngle=4.71239
    g2: ArcOfCircle CenterX=13 CenterY=8.5 CenterZ=0 NormalX=0 NormalY=0 NormalZ=1 AngleXU=0 Radius=3 StartAngle=4.71239 EndAngle=7.85398
    g3: LineSegment StartX=10 StartY=5.5 StartZ=0 EndX=13 EndY=5.5 EndZ=0
    g4: LineSegment StartX=10 StartY=11.5 StartZ=0 EndX=13 EndY=11.5 EndZ=0
  constraints (14):
    c: PointOnObject(g0,g-4)
    c: PointOnObject(g0,g-5)
    c: Horizontal(g0)
    c: DistanceY(g0,g-4) = 6.5
    c: Tangent(g1,g4) = 1.5708
    c: Tangent(g1,g3) = -1.5708
    c: Tangent(g3,g2) = -1.5708
    c: Tangent(g4,g2) = 1.5708
    c: Horizontal(g3)
    c: Equal(g1,g2)
    c: PointOnObject(g1,g0)
    c: Radius(g2) = 3
    c: DistanceX(g4,g4) = 3
    c: DistanceX(g2,g0) = 7
FEATURE [PartDesign::Pocket] Pocket097
  BaseFeature = -> Pocket096
  Length = 5
  Length2 = 100
  Placement = pos=(0,0,0) rot=(0.57735,0.57735,0.57735;2.0944rad)
  Profile = -> Sketch257
  Type = 2
FEATURE [Sketcher::SketchObject] Sketch258
  ExternalGeometry = -> [Pocket097]
  FullyConstrained = true
  MapMode = 5
  Placement = pos=(0,0,0) rot=(0.57735,0.57735,0.57735;4.18879rad)
  Support = -> [Pocket097]
  sketch-geometry (9):
    g0: LineSegment StartX=0 StartY=8.5 StartZ=0 EndX=20 EndY=8.5 EndZ=0
    g1: ArcOfCircle CenterX=3 CenterY=9.5 CenterZ=0 NormalX=0 NormalY=0 NormalZ=1 AngleXU=0 Radius=1 StartAngle=0 EndAngle=3.14159
    g2: ArcOfCircle CenterX=3 CenterY=7.5 CenterZ=0 NormalX=0 NormalY=0 NormalZ=1 AngleXU=0 Radius=1 StartAngle=3.14159 EndAngle=6.28319
    g3: LineSegment StartX=2 StartY=9.5 StartZ=0 EndX=2 EndY=7.5 EndZ=0
    g4: LineSegment StartX=4 StartY=9.5 StartZ=0 EndX=4 EndY=7.5 EndZ=0
    g5: ArcOfCircle CenterX=18 CenterY=9.5 CenterZ=0 NormalX=0 NormalY=0 NormalZ=1 AngleXU=0 Radius=1 StartAngle=-9e-16 EndAngle=3.14159
    g6: ArcOfCircle CenterX=18 CenterY=7.5 CenterZ=0 NormalX=0 NormalY=0 NormalZ=1 AngleXU=0 Radius=1 StartAngle=3.14159 EndAngle=6.28319
    g7: LineSegment StartX=17 StartY=9.5 StartZ=0 EndX=17 EndY=7.5 EndZ=0
    g8: LineSegment StartX=19 StartY=9.5 StartZ=0 EndX=19 EndY=7.5 EndZ=0
  constraints (24):
    c: PointOnObject(g0,g-2)
    c: PointOnObject(g0,g-5)
    c: Horizontal(g0)
    c: DistanceY(g0,g-3) = 8.5
    c: Tangent(g1,g4) = 1.5708
    c: Tangent(g1,g3) = -1.5708
    c: Tangent(g3,g2) = -1.5708
    c: Tangent(g4,g2) = 1.5708
    c: Vertical(g3)
    c: Equal(g1,g2)
    c: Tangent(g5,g8) = 1.5708
    c: Tangent(g5,g7) = -1.5708
    c: Tangent(g7,g6) = -1.5708
    c: Tangent(g8,g6) = 1.5708
    c: Vertical(g7)
    c: Equal(g5,g6)
    c: Equal(g1,g5)
    c: Equal(g4,g7)
    c: DistanceY(g4,g4) = 2
    c: Radius(g1) = 1
    c: Horizontal(g5,g1)
    c: DistanceX(g0,g1) = 3
    c: DistanceX(g5,g0) = 2
    c: DistanceY(g0,g1) = 1
FEATURE [PartDesign::Pad] Pad127
  BaseFeature = -> Pocket097
  Direction = (1,1,1)
  Length = 1
  Length2 = 100
  Placement = pos=(0,0,0) rot=(0.57735,0.57735,0.57735;2.0944rad)
  Profile = -> Sketch258
  Type = 0
FEATURE [Sketcher::SketchObject] Sketch259
  ExternalGeometry = -> [Pad127]
  FullyConstrained = true
  MapMode = 5
  Placement = pos=(0,0,1e-16) rot=(0.707107,0.707107,0;3.14159rad)
  Support = -> [Pad127]
  sketch-geometry (9):
    g0: LineSegment StartX=0 StartY=8.5 StartZ=0 EndX=-20 EndY=8.5 EndZ=0
    g1: ArcOfCircle CenterX=-3 CenterY=7.5 CenterZ=0 NormalX=0 NormalY=0 NormalZ=1 AngleXU=0 Radius=1 StartAngle=3.14159 EndAngle=6.28319
    g2: ArcOfCircle CenterX=-3 CenterY=9.5 CenterZ=0 NormalX=0 NormalY=0 NormalZ=1 AngleXU=0 Radius=1 StartAngle=3e-16 EndAngle=3.14159
    g3: LineSegment StartX=-2 StartY=7.5 StartZ=0 EndX=-2 EndY=9.5 EndZ=0
    g4: LineSegment StartX=-4 StartY=7.5 StartZ=0 EndX=-4 EndY=9.5 EndZ=0
    g5: ArcOfCircle CenterX=-18 CenterY=9.5 CenterZ=0 NormalX=0 NormalY=0 NormalZ=1 AngleXU=0 Radius=1 StartAngle=0 EndAngle=3.14159
    g6: ArcOfCircle CenterX=-18 CenterY=7.5 CenterZ=0 NormalX=0 NormalY=0 NormalZ=1 AngleXU=0 Radius=1 StartAngle=3.14159 EndAngle=6.28319
    g7: LineSegment StartX=-19 StartY=9.5 StartZ=0 EndX=-19 EndY=7.5 EndZ=0
    g8: LineSegment StartX=-17 StartY=9.5 StartZ=0 EndX=-17 EndY=7.5 EndZ=0
  constraints (24):
    c: PointOnObject(g0,g-2)
    c: PointOnObject(g0,g-4)
    c: Horizontal(g0)
    c: DistanceY(g0,g-3) = 8.5
    c: Tangent(g1,g4) = 1.5708
    c: Tangent(g1,g3) = -1.5708
    c: Tangent(g3,g2) = -1.5708
    c: Tangent(g4,g2) = 1.5708
    c: Vertical(g3)
    c: Equal(g1,g2)
    c: Radius(g2) = 1
    c: DistanceY(g4,g4) = 2
    c: DistanceY(g0,g2) = 1
    c: DistanceX(g2,g0) = 3
    c: Tangent(g5,g8) = 1.5708
    c: Tangent(g5,g7) = -1.5708
    c: Tangent(g7,g6) = -1.5708
    c: Tangent(g8,g6) = 1.5708
    c: Vertical(g7)
    c: Equal(g5,g6)
    c: Equal(g5,g2)
    c: Equal(g8,g4)
    c: Horizontal(g5,g2)
    c: DistanceX(g0,g5) = 2
FEATURE [PartDesign::Pad] Pad128
  BaseFeature = -> Pad127
  Direction = (1,1,1)
  Length = 1
  Length2 = 100
  Placement = pos=(0,0,0) rot=(0.57735,0.57735,0.57735;2.0944rad)
  Profile = -> Sketch259
  Type = 0
FEATURE [PartDesign::Body] Body204  label="Corner007"
  Group = -> [Sketch254,Pad126,Sketch255,Pocket095,Sketch256,Pocket096,Sketch257,Pocket097,Sketch258,Pad127,Sketch259,Pad128]
  Origin = -> Origin281
  Tip = -> Pad128
FEATURE [App::Part] Part077  label="soporte90-008"
  Group = -> [Body204]
  Origin = -> Origin282
  Placement = pos=(320,321,170) rot=(0.707107,0.707107,0;3.14159rad)
FEATURE [Sketcher::SketchObject] Sketch260
  FullyConstrained = true
  MapMode = 5
  Placement = pos=(0,0,0) rot=(0.57735,0.57735,0.57735;2.0944rad)
  Support = -> [YZ_Plane277]
  sketch-geometry (5):
    g0: LineSegment StartX=0 StartY=0 StartZ=0 EndX=0 EndY=20 EndZ=0
    g1: LineSegment StartX=0 StartY=20 StartZ=0 EndX=-3 EndY=20 EndZ=0
    g2: LineSegment StartX=-3 StartY=20 StartZ=0 EndX=-20 EndY=3 EndZ=0
    g3: LineSegment StartX=-20 StartY=3 StartZ=0 EndX=-20 EndY=0 EndZ=0
    g4: LineSegment StartX=-20 StartY=0 StartZ=0 EndX=0 EndY=0 EndZ=0
  constraints (14):
    c: Coincident(g-1,g0)
    c: PointOnObject(g0,g-2)
    c: Coincident(g0,g1)
    c: Horizontal(g1)
    c: Coincident(g1,g2)
    c: Coincident(g2,g3)
    c: PointOnObject(g3,g-1)
    c: Vertical(g3)
    c: Coincident(g3,g4)
    c: Coincident(g4,g0)
    c: DistanceY(g0,g0) = 20
    c: DistanceY(g3,g3) = 3
    c: DistanceX(g1,g1) = 3
    c: DistanceX(g4,g4) = 20
FEATURE [PartDesign::Pad] Pad129
  Direction = (1,1,1)
  Length = 17
  Length2 = 100
  Placement = pos=(0,0,0) rot=(0.57735,0.57735,0.57735;2.0944rad)
  Profile = -> Sketch260
  Type = 0
FEATURE [Sketcher::SketchObject] Sketch261
  ExternalGeometry = -> [Pad129]
  FullyConstrained = true
  MapMode = 5
  Placement = pos=(-8.8e-15,-20,4.4e-15) rot=(-0.57735,-0.57735,0.57735;4.18879rad)
  Support = -> [Pad129]
  sketch-geometry (4):
    g0: LineSegment StartX=-3 StartY=2 StartZ=0 EndX=-20 EndY=2 EndZ=0
    g1: LineSegment StartX=-20 StartY=2 StartZ=0 EndX=-20 EndY=15 EndZ=0
    g2: LineSegment StartX=-20 StartY=15 StartZ=0 EndX=-3 EndY=15 EndZ=0
    g3: LineSegment StartX=-3 StartY=15 StartZ=0 EndX=-3 EndY=2 EndZ=0
  constraints (12):
    c: Coincident(g0,g1)
    c: Coincident(g1,g2)
    c: Coincident(g2,g3)
    c: Coincident(g3,g0)
    c: Horizontal(g0)
    c: Horizontal(g2)
    c: Vertical(g1)
    c: Vertical(g3)
    c: PointOnObject(g0,g-3)
    c: DistanceY(g1,g-6) = 2
    c: DistanceY(g-6,g0) = 2
    c: PointOnObject(g1,g-6)
FEATURE [PartDesign::Pocket] Pocket098
  BaseFeature = -> Pad129
  Length = 17
  Length2 = 100
  Placement = pos=(0,0,0) rot=(0.57735,0.57735,0.57735;2.0944rad)
  Profile = -> Sketch261
  Type = 0
FEATURE [Sketcher::SketchObject] Sketch262
  ExternalGeometry = -> [Pocket098]
  FullyConstrained = true
  MapMode = 5
  Placement = pos=(-1.7e-15,-3,6e-16) rot=(-0.57735,-0.57735,0.57735;4.18879rad)
  Support = -> [Pocket098]
  sketch-geometry (5):
    g0: LineSegment StartX=-20 StartY=8.5 StartZ=0 EndX=-3 EndY=8.5 EndZ=0
    g1: ArcOfCircle CenterX=-10 CenterY=8.5 CenterZ=0 NormalX=0 NormalY=0 NormalZ=1 AngleXU=0 Radius=3 StartAngle=4.71239 EndAngle=7.85398
    g2: ArcOfCircle CenterX=-13 CenterY=8.5 CenterZ=0 NormalX=0 NormalY=0 NormalZ=1 AngleXU=0 Radius=3 StartAngle=1.5708 EndAngle=4.71239
    g3: LineSegment StartX=-10 StartY=11.5 StartZ=0 EndX=-13 EndY=11.5 EndZ=0
    g4: LineSegment StartX=-10 StartY=5.5 StartZ=0 EndX=-13 EndY=5.5 EndZ=0
  constraints (14):
    c: PointOnObject(g0,g-6)
    c: PointOnObject(g0,g-4)
    c: Horizontal(g0)
    c: DistanceY(g0,g-4) = 6.5
    c: Tangent(g1,g4) = 1.5708
    c: Tangent(g1,g3) = -1.5708
    c: Tangent(g3,g2) = -1.5708
    c: Tangent(g4,g2) = 1.5708
    c: Horizontal(g3)
    c: Equal(g1,g2)
    c: PointOnObject(g1,g0)
    c: Radius(g1) = 3
    c: DistanceX(g3,g3) = 3
    c: DistanceX(g0,g2) = 7
FEATURE [PartDesign::Pocket] Pocket099
  BaseFeature = -> Pocket098
  Length = 5
  Length2 = 100
  Placement = pos=(0,0,0) rot=(0.57735,0.57735,0.57735;2.0944rad)
  Profile = -> Sketch262
  Type = 2
FEATURE [Sketcher::SketchObject] Sketch263
  ExternalGeometry = -> [Pocket099]
  FullyConstrained = true
  MapMode = 5
  Placement = pos=(-3e-16,1.2e-15,3) rot=(0,0,-1;1.5708rad)
  Support = -> [Pocket099]
  sketch-geometry (5):
    g0: LineSegment StartX=3 StartY=8.5 StartZ=0 EndX=20 EndY=8.5 EndZ=0
    g1: ArcOfCircle CenterX=10 CenterY=8.5 CenterZ=0 NormalX=0 NormalY=0 NormalZ=1 AngleXU=0 Radius=3 StartAngle=1.5708 EndAngle=4.71239
    g2: ArcOfCircle CenterX=13 CenterY=8.5 CenterZ=0 NormalX=0 NormalY=0 NormalZ=1 AngleXU=0 Radius=3 StartAngle=4.71239 EndAngle=7.85398
    g3: LineSegment StartX=10 StartY=5.5 StartZ=0 EndX=13 EndY=5.5 EndZ=0
    g4: LineSegment StartX=10 StartY=11.5 StartZ=0 EndX=13 EndY=11.5 EndZ=0
  constraints (14):
    c: PointOnObject(g0,g-4)
    c: PointOnObject(g0,g-5)
    c: Horizontal(g0)
    c: DistanceY(g0,g-4) = 6.5
    c: Tangent(g1,g4) = 1.5708
    c: Tangent(g1,g3) = -1.5708
    c: Tangent(g3,g2) = -1.5708
    c: Tangent(g4,g2) = 1.5708
    c: Horizontal(g3)
    c: Equal(g1,g2)
    c: PointOnObject(g1,g0)
    c: Radius(g2) = 3
    c: DistanceX(g4,g4) = 3
    c: DistanceX(g2,g0) = 7
FEATURE [PartDesign::Pocket] Pocket100
  BaseFeature = -> Pocket099
  Length = 5
  Length2 = 100
  Placement = pos=(0,0,0) rot=(0.57735,0.57735,0.57735;2.0944rad)
  Profile = -> Sketch263
  Type = 2
FEATURE [Sketcher::SketchObject] Sketch264
  ExternalGeometry = -> [Pocket100]
  FullyConstrained = true
  MapMode = 5
  Placement = pos=(0,0,0) rot=(0.57735,0.57735,0.57735;4.18879rad)
  Support = -> [Pocket100]
  sketch-geometry (9):
    g0: LineSegment StartX=0 StartY=8.5 StartZ=0 EndX=20 EndY=8.5 EndZ=0
    g1: ArcOfCircle CenterX=3 CenterY=9.5 CenterZ=0 NormalX=0 NormalY=0 NormalZ=1 AngleXU=0 Radius=1 StartAngle=0 EndAngle=3.14159
    g2: ArcOfCircle CenterX=3 CenterY=7.5 CenterZ=0 NormalX=0 NormalY=0 NormalZ=1 AngleXU=0 Radius=1 StartAngle=3.14159 EndAngle=6.28319
    g3: LineSegment StartX=2 StartY=9.5 StartZ=0 EndX=2 EndY=7.5 EndZ=0
    g4: LineSegment StartX=4 StartY=9.5 StartZ=0 EndX=4 EndY=7.5 EndZ=0
    g5: ArcOfCircle CenterX=18 CenterY=9.5 CenterZ=0 NormalX=0 NormalY=0 NormalZ=1 AngleXU=0 Radius=1 StartAngle=-9e-16 EndAngle=3.14159
    g6: ArcOfCircle CenterX=18 CenterY=7.5 CenterZ=0 NormalX=0 NormalY=0 NormalZ=1 AngleXU=0 Radius=1 StartAngle=3.14159 EndAngle=6.28319
    g7: LineSegment StartX=17 StartY=9.5 StartZ=0 EndX=17 EndY=7.5 EndZ=0
    g8: LineSegment StartX=19 StartY=9.5 StartZ=0 EndX=19 EndY=7.5 EndZ=0
  constraints (24):
    c: PointOnObject(g0,g-2)
    c: PointOnObject(g0,g-5)
    c: Horizontal(g0)
    c: DistanceY(g0,g-3) = 8.5
    c: Tangent(g1,g4) = 1.5708
    c: Tangent(g1,g3) = -1.5708
    c: Tangent(g3,g2) = -1.5708
    c: Tangent(g4,g2) = 1.5708
    c: Vertical(g3)
    c: Equal(g1,g2)
    c: Tangent(g5,g8) = 1.5708
    c: Tangent(g5,g7) = -1.5708
    c: Tangent(g7,g6) = -1.5708
    c: Tangent(g8,g6) = 1.5708
    c: Vertical(g7)
    c: Equal(g5,g6)
    c: Equal(g1,g5)
    c: Equal(g4,g7)
    c: DistanceY(g4,g4) = 2
    c: Radius(g1) = 1
    c: Horizontal(g5,g1)
    c: DistanceX(g0,g1) = 3
    c: DistanceX(g5,g0) = 2
    c: DistanceY(g0,g1) = 1
FEATURE [PartDesign::Pad] Pad130
  BaseFeature = -> Pocket100
  Direction = (1,1,1)
  Length = 1
  Length2 = 100
  Placement = pos=(0,0,0) rot=(0.57735,0.57735,0.57735;2.0944rad)
  Profile = -> Sketch264
  Type = 0
FEATURE [Sketcher::SketchObject] Sketch265
  ExternalGeometry = -> [Pad130]
  FullyConstrained = true
  MapMode = 5
  Placement = pos=(0,0,1e-16) rot=(0.707107,0.707107,0;3.14159rad)
  Support = -> [Pad130]
  sketch-geometry (9):
    g0: LineSegment StartX=0 StartY=8.5 StartZ=0 EndX=-20 EndY=8.5 EndZ=0
    g1: ArcOfCircle CenterX=-3 CenterY=7.5 CenterZ=0 NormalX=0 NormalY=0 NormalZ=1 AngleXU=0 Radius=1 StartAngle=3.14159 EndAngle=6.28319
    g2: ArcOfCircle CenterX=-3 CenterY=9.5 CenterZ=0 NormalX=0 NormalY=0 NormalZ=1 AngleXU=0 Radius=1 StartAngle=3e-16 EndAngle=3.14159
    g3: LineSegment StartX=-2 StartY=7.5 StartZ=0 EndX=-2 EndY=9.5 EndZ=0
    g4: LineSegment StartX=-4 StartY=7.5 StartZ=0 EndX=-4 EndY=9.5 EndZ=0
    g5: ArcOfCircle CenterX=-18 CenterY=9.5 CenterZ=0 NormalX=0 NormalY=0 NormalZ=1 AngleXU=0 Radius=1 StartAngle=0 EndAngle=3.14159
    g6: ArcOfCircle CenterX=-18 CenterY=7.5 CenterZ=0 NormalX=0 NormalY=0 NormalZ=1 AngleXU=0 Radius=1 StartAngle=3.14159 EndAngle=6.28319
    g7: LineSegment StartX=-19 StartY=9.5 StartZ=0 EndX=-19 EndY=7.5 EndZ=0
    g8: LineSegment StartX=-17 StartY=9.5 StartZ=0 EndX=-17 EndY=7.5 EndZ=0
  constraints (24):
    c: PointOnObject(g0,g-2)
    c: PointOnObject(g0,g-4)
    c: Horizontal(g0)
    c: DistanceY(g0,g-3) = 8.5
    c: Tangent(g1,g4) = 1.5708
    c: Tangent(g1,g3) = -1.5708
    c: Tangent(g3,g2) = -1.5708
    c: Tangent(g4,g2) = 1.5708
    c: Vertical(g3)
    c: Equal(g1,g2)
    c: Radius(g2) = 1
    c: DistanceY(g4,g4) = 2
    c: DistanceY(g0,g2) = 1
    c: DistanceX(g2,g0) = 3
    c: Tangent(g5,g8) = 1.5708
    c: Tangent(g5,g7) = -1.5708
    c: Tangent(g7,g6) = -1.5708
    c: Tangent(g8,g6) = 1.5708
    c: Vertical(g7)
    c: Equal(g5,g6)
    c: Equal(g5,g2)
    c: Equal(g8,g4)
    c: Horizontal(g5,g2)
    c: DistanceX(g0,g5) = 2
FEATURE [PartDesign::Pad] Pad131
  BaseFeature = -> Pad130
  Direction = (1,1,1)
  Length = 1
  Length2 = 100
  Placement = pos=(0,0,0) rot=(0.57735,0.57735,0.57735;2.0944rad)
  Profile = -> Sketch265
  Type = 0
FEATURE [PartDesign::Body] Body205  label="Corner008"
  Group = -> [Sketch260,Pad129,Sketch261,Pocket098,Sketch262,Pocket099,Sketch263,Pocket100,Sketch264,Pad130,Sketch265,Pad131]
  Origin = -> Origin283
  Tip = -> Pad131
FEATURE [App::Part] Part078  label="soporte90-009"
  Group = -> [Body205]
  Origin = -> Origin284
  Placement = pos=(3,20,70) rot=(1,0,0;3.14159rad)
FEATURE [Sketcher::SketchObject] Sketch266
  FullyConstrained = true
  MapMode = 5
  Placement = pos=(0,0,0) rot=(0.57735,0.57735,0.57735;2.0944rad)
  Support = -> [YZ_Plane279]
  sketch-geometry (5):
    g0: LineSegment StartX=0 StartY=0 StartZ=0 EndX=0 EndY=20 EndZ=0
    g1: LineSegment StartX=0 StartY=20 StartZ=0 EndX=-3 EndY=20 EndZ=0
    g2: LineSegment StartX=-3 StartY=20 StartZ=0 EndX=-20 EndY=3 EndZ=0
    g3: LineSegment StartX=-20 StartY=3 StartZ=0 EndX=-20 EndY=0 EndZ=0
    g4: LineSegment StartX=-20 StartY=0 StartZ=0 EndX=0 EndY=0 EndZ=0
  constraints (14):
    c: Coincident(g-1,g0)
    c: PointOnObject(g0,g-2)
    c: Coincident(g0,g1)
    c: Horizontal(g1)
    c: Coincident(g1,g2)
    c: Coincident(g2,g3)
    c: PointOnObject(g3,g-1)
    c: Vertical(g3)
    c: Coincident(g3,g4)
    c: Coincident(g4,g0)
    c: DistanceY(g0,g0) = 20
    c: DistanceY(g3,g3) = 3
    c: DistanceX(g1,g1) = 3
    c: DistanceX(g4,g4) = 20
FEATURE [PartDesign::Pad] Pad132
  Direction = (1,1,1)
  Length = 17
  Length2 = 100
  Placement = pos=(0,0,0) rot=(0.57735,0.57735,0.57735;2.0944rad)
  Profile = -> Sketch266
  Type = 0
FEATURE [Sketcher::SketchObject] Sketch267
  ExternalGeometry = -> [Pad132]
  FullyConstrained = true
  MapMode = 5
  Placement = pos=(-8.8e-15,-20,4.4e-15) rot=(-0.57735,-0.57735,0.57735;4.18879rad)
  Support = -> [Pad132]
  sketch-geometry (4):
    g0: LineSegment StartX=-3 StartY=2 StartZ=0 EndX=-20 EndY=2 EndZ=0
    g1: LineSegment StartX=-20 StartY=2 StartZ=0 EndX=-20 EndY=15 EndZ=0
    g2: LineSegment StartX=-20 StartY=15 StartZ=0 EndX=-3 EndY=15 EndZ=0
    g3: LineSegment StartX=-3 StartY=15 StartZ=0 EndX=-3 EndY=2 EndZ=0
  constraints (12):
    c: Coincident(g0,g1)
    c: Coincident(g1,g2)
    c: Coincident(g2,g3)
    c: Coincident(g3,g0)
    c: Horizontal(g0)
    c: Horizontal(g2)
    c: Vertical(g1)
    c: Vertical(g3)
    c: PointOnObject(g0,g-3)
    c: DistanceY(g1,g-6) = 2
    c: DistanceY(g-6,g0) = 2
    c: PointOnObject(g1,g-6)
FEATURE [PartDesign::Pocket] Pocket101
  BaseFeature = -> Pad132
  Length = 17
  Length2 = 100
  Placement = pos=(0,0,0) rot=(0.57735,0.57735,0.57735;2.0944rad)
  Profile = -> Sketch267
  Type = 0
FEATURE [Sketcher::SketchObject] Sketch268
  ExternalGeometry = -> [Pocket101]
  FullyConstrained = true
  MapMode = 5
  Placement = pos=(-1.7e-15,-3,6e-16) rot=(-0.57735,-0.57735,0.57735;4.18879rad)
  Support = -> [Pocket101]
  sketch-geometry (5):
    g0: LineSegment StartX=-20 StartY=8.5 StartZ=0 EndX=-3 EndY=8.5 EndZ=0
    g1: ArcOfCircle CenterX=-10 CenterY=8.5 CenterZ=0 NormalX=0 NormalY=0 NormalZ=1 AngleXU=0 Radius=3 StartAngle=4.71239 EndAngle=7.85398
    g2: ArcOfCircle CenterX=-13 CenterY=8.5 CenterZ=0 NormalX=0 NormalY=0 NormalZ=1 AngleXU=0 Radius=3 StartAngle=1.5708 EndAngle=4.71239
    g3: LineSegment StartX=-10 StartY=11.5 StartZ=0 EndX=-13 EndY=11.5 EndZ=0
    g4: LineSegment StartX=-10 StartY=5.5 StartZ=0 EndX=-13 EndY=5.5 EndZ=0
  constraints (14):
    c: PointOnObject(g0,g-6)
    c: PointOnObject(g0,g-4)
    c: Horizontal(g0)
    c: DistanceY(g0,g-4) = 6.5
    c: Tangent(g1,g4) = 1.5708
    c: Tangent(g1,g3) = -1.5708
    c: Tangent(g3,g2) = -1.5708
    c: Tangent(g4,g2) = 1.5708
    c: Horizontal(g3)
    c: Equal(g1,g2)
    c: PointOnObject(g1,g0)
    c: Radius(g1) = 3
    c: DistanceX(g3,g3) = 3
    c: DistanceX(g0,g2) = 7
FEATURE [PartDesign::Pocket] Pocket102
  BaseFeature = -> Pocket101
  Length = 5
  Length2 = 100
  Placement = pos=(0,0,0) rot=(0.57735,0.57735,0.57735;2.0944rad)
  Profile = -> Sketch268
  Type = 2
FEATURE [Sketcher::SketchObject] Sketch269
  ExternalGeometry = -> [Pocket102]
  FullyConstrained = true
  MapMode = 5
  Placement = pos=(-3e-16,1.2e-15,3) rot=(0,0,-1;1.5708rad)
  Support = -> [Pocket102]
  sketch-geometry (5):
    g0: LineSegment StartX=3 StartY=8.5 StartZ=0 EndX=20 EndY=8.5 EndZ=0
    g1: ArcOfCircle CenterX=10 CenterY=8.5 CenterZ=0 NormalX=0 NormalY=0 NormalZ=1 AngleXU=0 Radius=3 StartAngle=1.5708 EndAngle=4.71239
    g2: ArcOfCircle CenterX=13 CenterY=8.5 CenterZ=0 NormalX=0 NormalY=0 NormalZ=1 AngleXU=0 Radius=3 StartAngle=4.71239 EndAngle=7.85398
    g3: LineSegment StartX=10 StartY=5.5 StartZ=0 EndX=13 EndY=5.5 EndZ=0
    g4: LineSegment StartX=10 StartY=11.5 StartZ=0 EndX=13 EndY=11.5 EndZ=0
  constraints (14):
    c: PointOnObject(g0,g-4)
    c: PointOnObject(g0,g-5)
    c: Horizontal(g0)
    c: DistanceY(g0,g-4) = 6.5
    c: Tangent(g1,g4) = 1.5708
    c: Tangent(g1,g3) = -1.5708
    c: Tangent(g3,g2) = -1.5708
    c: Tangent(g4,g2) = 1.5708
    c: Horizontal(g3)
    c: Equal(g1,g2)
    c: PointOnObject(g1,g0)
    c: Radius(g2) = 3
    c: DistanceX(g4,g4) = 3
    c: DistanceX(g2,g0) = 7
FEATURE [PartDesign::Pocket] Pocket103
  BaseFeature = -> Pocket102
  Length = 5
  Length2 = 100
  Placement = pos=(0,0,0) rot=(0.57735,0.57735,0.57735;2.0944rad)
  Profile = -> Sketch269
  Type = 2
FEATURE [Sketcher::SketchObject] Sketch270
  ExternalGeometry = -> [Pocket103]
  FullyConstrained = true
  MapMode = 5
  Placement = pos=(0,0,0) rot=(0.57735,0.57735,0.57735;4.18879rad)
  Support = -> [Pocket103]
  sketch-geometry (9):
    g0: LineSegment StartX=0 StartY=8.5 StartZ=0 EndX=20 EndY=8.5 EndZ=0
    g1: ArcOfCircle CenterX=3 CenterY=9.5 CenterZ=0 NormalX=0 NormalY=0 NormalZ=1 AngleXU=0 Radius=1 StartAngle=0 EndAngle=3.14159
    g2: ArcOfCircle CenterX=3 CenterY=7.5 CenterZ=0 NormalX=0 NormalY=0 NormalZ=1 AngleXU=0 Radius=1 StartAngle=3.14159 EndAngle=6.28319
    g3: LineSegment StartX=2 StartY=9.5 StartZ=0 EndX=2 EndY=7.5 EndZ=0
    g4: LineSegment StartX=4 StartY=9.5 StartZ=0 EndX=4 EndY=7.5 EndZ=0
    g5: ArcOfCircle CenterX=18 CenterY=9.5 CenterZ=0 NormalX=0 NormalY=0 NormalZ=1 AngleXU=0 Radius=1 StartAngle=-9e-16 EndAngle=3.14159
    g6: ArcOfCircle CenterX=18 CenterY=7.5 CenterZ=0 NormalX=0 NormalY=0 NormalZ=1 AngleXU=0 Radius=1 StartAngle=3.14159 EndAngle=6.28319
    g7: LineSegment StartX=17 StartY=9.5 StartZ=0 EndX=17 EndY=7.5 EndZ=0
    g8: LineSegment StartX=19 StartY=9.5 StartZ=0 EndX=19 EndY=7.5 EndZ=0
  constraints (24):
    c: PointOnObject(g0,g-2)
    c: PointOnObject(g0,g-5)
    c: Horizontal(g0)
    c: DistanceY(g0,g-3) = 8.5
    c: Tangent(g1,g4) = 1.5708
    c: Tangent(g1,g3) = -1.5708
    c: Tangent(g3,g2) = -1.5708
    c: Tangent(g4,g2) = 1.5708
    c: Vertical(g3)
    c: Equal(g1,g2)
    c: Tangent(g5,g8) = 1.5708
    c: Tangent(g5,g7) = -1.5708
    c: Tangent(g7,g6) = -1.5708
    c: Tangent(g8,g6) = 1.5708
    c: Vertical(g7)
    c: Equal(g5,g6)
    c: Equal(g1,g5)
    c: Equal(g4,g7)
    c: DistanceY(g4,g4) = 2
    c: Radius(g1) = 1
    c: Horizontal(g5,g1)
    c: DistanceX(g0,g1) = 3
    c: DistanceX(g5,g0) = 2
    c: DistanceY(g0,g1) = 1
FEATURE [PartDesign::Pad] Pad133
  BaseFeature = -> Pocket103
  Direction = (1,1,1)
  Length = 1
  Length2 = 100
  Placement = pos=(0,0,0) rot=(0.57735,0.57735,0.57735;2.0944rad)
  Profile = -> Sketch270
  Type = 0
FEATURE [Sketcher::SketchObject] Sketch271
  ExternalGeometry = -> [Pad133]
  FullyConstrained = true
  MapMode = 5
  Placement = pos=(0,0,1e-16) rot=(0.707107,0.707107,0;3.14159rad)
  Support = -> [Pad133]
  sketch-geometry (9):
    g0: LineSegment StartX=0 StartY=8.5 StartZ=0 EndX=-20 EndY=8.5 EndZ=0
    g1: ArcOfCircle CenterX=-3 CenterY=7.5 CenterZ=0 NormalX=0 NormalY=0 NormalZ=1 AngleXU=0 Radius=1 StartAngle=3.14159 EndAngle=6.28319
    g2: ArcOfCircle CenterX=-3 CenterY=9.5 CenterZ=0 NormalX=0 NormalY=0 NormalZ=1 AngleXU=0 Radius=1 StartAngle=3e-16 EndAngle=3.14159
    g3: LineSegment StartX=-2 StartY=7.5 StartZ=0 EndX=-2 EndY=9.5 EndZ=0
    g4: LineSegment StartX=-4 StartY=7.5 StartZ=0 EndX=-4 EndY=9.5 EndZ=0
    g5: ArcOfCircle CenterX=-18 CenterY=9.5 CenterZ=0 NormalX=0 NormalY=0 NormalZ=1 AngleXU=0 Radius=1 StartAngle=0 EndAngle=3.14159
    g6: ArcOfCircle CenterX=-18 CenterY=7.5 CenterZ=0 NormalX=0 NormalY=0 NormalZ=1 AngleXU=0 Radius=1 StartAngle=3.14159 EndAngle=6.28319
    g7: LineSegment StartX=-19 StartY=9.5 StartZ=0 EndX=-19 EndY=7.5 EndZ=0
    g8: LineSegment StartX=-17 StartY=9.5 StartZ=0 EndX=-17 EndY=7.5 EndZ=0
  constraints (24):
    c: PointOnObject(g0,g-2)
    c: PointOnObject(g0,g-4)
    c: Horizontal(g0)
    c: DistanceY(g0,g-3) = 8.5
    c: Tangent(g1,g4) = 1.5708
    c: Tangent(g1,g3) = -1.5708
    c: Tangent(g3,g2) = -1.5708
    c: Tangent(g4,g2) = 1.5708
    c: Vertical(g3)
    c: Equal(g1,g2)
    c: Radius(g2) = 1
    c: DistanceY(g4,g4) = 2
    c: DistanceY(g0,g2) = 1
    c: DistanceX(g2,g0) = 3
    c: Tangent(g5,g8) = 1.5708
    c: Tangent(g5,g7) = -1.5708
    c: Tangent(g7,g6) = -1.5708
    c: Tangent(g8,g6) = 1.5708
    c: Vertical(g7)
    c: Equal(g5,g6)
    c: Equal(g5,g2)
    c: Equal(g8,g4)
    c: Horizontal(g5,g2)
    c: DistanceX(g0,g5) = 2
FEATURE [PartDesign::Pad] Pad134
  BaseFeature = -> Pad133
  Direction = (1,1,1)
  Length = 1
  Length2 = 100
  Placement = pos=(0,0,0) rot=(0.57735,0.57735,0.57735;2.0944rad)
  Profile = -> Sketch271
  Type = 0
FEATURE [PartDesign::Body] Body206  label="Corner009"
  Group = -> [Sketch266,Pad132,Sketch267,Pocket101,Sketch268,Pocket102,Sketch269,Pocket103,Sketch270,Pad133,Sketch271,Pad134]
  Origin = -> Origin285
  Tip = -> Pad134
FEATURE [App::Part] Part079  label="soporte90-010"
  Group = -> [Body206]
  Origin = -> Origin286
  Placement = pos=(3,320,70) rot=(1,0,0;1.5708rad)
FEATURE [Sketcher::SketchObject] Sketch272
  FullyConstrained = true
  MapMode = 5
  Placement = pos=(0,0,0) rot=(0.57735,0.57735,0.57735;2.0944rad)
  Support = -> [YZ_Plane281]
  sketch-geometry (5):
    g0: LineSegment StartX=0 StartY=0 StartZ=0 EndX=0 EndY=20 EndZ=0
    g1: LineSegment StartX=0 StartY=20 StartZ=0 EndX=-3 EndY=20 EndZ=0
    g2: LineSegment StartX=-3 StartY=20 StartZ=0 EndX=-20 EndY=3 EndZ=0
    g3: LineSegment StartX=-20 StartY=3 StartZ=0 EndX=-20 EndY=0 EndZ=0
    g4: LineSegment StartX=-20 StartY=0 StartZ=0 EndX=0 EndY=0 EndZ=0
  constraints (14):
    c: Coincident(g-1,g0)
    c: PointOnObject(g0,g-2)
    c: Coincident(g0,g1)
    c: Horizontal(g1)
    c: Coincident(g1,g2)
    c: Coincident(g2,g3)
    c: PointOnObject(g3,g-1)
    c: Vertical(g3)
    c: Coincident(g3,g4)
    c: Coincident(g4,g0)
    c: DistanceY(g0,g0) = 20
    c: DistanceY(g3,g3) = 3
    c: DistanceX(g1,g1) = 3
    c: DistanceX(g4,g4) = 20
FEATURE [PartDesign::Pad] Pad135
  Direction = (1,1,1)
  Length = 17
  Length2 = 100
  Placement = pos=(0,0,0) rot=(0.57735,0.57735,0.57735;2.0944rad)
  Profile = -> Sketch272
  Type = 0
FEATURE [Sketcher::SketchObject] Sketch273
  ExternalGeometry = -> [Pad135]
  FullyConstrained = true
  MapMode = 5
  Placement = pos=(-8.8e-15,-20,4.4e-15) rot=(-0.57735,-0.57735,0.57735;4.18879rad)
  Support = -> [Pad135]
  sketch-geometry (4):
    g0: LineSegment StartX=-3 StartY=2 StartZ=0 EndX=-20 EndY=2 EndZ=0
    g1: LineSegment StartX=-20 StartY=2 StartZ=0 EndX=-20 EndY=15 EndZ=0
    g2: LineSegment StartX=-20 StartY=15 StartZ=0 EndX=-3 EndY=15 EndZ=0
    g3: LineSegment StartX=-3 StartY=15 StartZ=0 EndX=-3 EndY=2 EndZ=0
  constraints (12):
    c: Coincident(g0,g1)
    c: Coincident(g1,g2)
    c: Coincident(g2,g3)
    c: Coincident(g3,g0)
    c: Horizontal(g0)
    c: Horizontal(g2)
    c: Vertical(g1)
    c: Vertical(g3)
    c: PointOnObject(g0,g-3)
    c: DistanceY(g1,g-6) = 2
    c: DistanceY(g-6,g0) = 2
    c: PointOnObject(g1,g-6)
FEATURE [PartDesign::Pocket] Pocket104
  BaseFeature = -> Pad135
  Length = 17
  Length2 = 100
  Placement = pos=(0,0,0) rot=(0.57735,0.57735,0.57735;2.0944rad)
  Profile = -> Sketch273
  Type = 0
FEATURE [Sketcher::SketchObject] Sketch274
  ExternalGeometry = -> [Pocket104]
  FullyConstrained = true
  MapMode = 5
  Placement = pos=(-1.7e-15,-3,6e-16) rot=(-0.57735,-0.57735,0.57735;4.18879rad)
  Support = -> [Pocket104]
  sketch-geometry (5):
    g0: LineSegment StartX=-20 StartY=8.5 StartZ=0 EndX=-3 EndY=8.5 EndZ=0
    g1: ArcOfCircle CenterX=-10 CenterY=8.5 CenterZ=0 NormalX=0 NormalY=0 NormalZ=1 AngleXU=0 Radius=3 StartAngle=4.71239 EndAngle=7.85398
    g2: ArcOfCircle CenterX=-13 CenterY=8.5 CenterZ=0 NormalX=0 NormalY=0 NormalZ=1 AngleXU=0 Radius=3 StartAngle=1.5708 EndAngle=4.71239
    g3: LineSegment StartX=-10 StartY=11.5 StartZ=0 EndX=-13 EndY=11.5 EndZ=0
    g4: LineSegment StartX=-10 StartY=5.5 StartZ=0 EndX=-13 EndY=5.5 EndZ=0
  constraints (14):
    c: PointOnObject(g0,g-6)
    c: PointOnObject(g0,g-4)
    c: Horizontal(g0)
    c: DistanceY(g0,g-4) = 6.5
    c: Tangent(g1,g4) = 1.5708
    c: Tangent(g1,g3) = -1.5708
    c: Tangent(g3,g2) = -1.5708
    c: Tangent(g4,g2) = 1.5708
    c: Horizontal(g3)
    c: Equal(g1,g2)
    c: PointOnObject(g1,g0)
    c: Radius(g1) = 3
    c: DistanceX(g3,g3) = 3
    c: DistanceX(g0,g2) = 7
FEATURE [PartDesign::Pocket] Pocket105
  BaseFeature = -> Pocket104
  Length = 5
  Length2 = 100
  Placement = pos=(0,0,0) rot=(0.57735,0.57735,0.57735;2.0944rad)
  Profile = -> Sketch274
  Type = 2
FEATURE [Sketcher::SketchObject] Sketch275
  ExternalGeometry = -> [Pocket105]
  FullyConstrained = true
  MapMode = 5
  Placement = pos=(-3e-16,1.2e-15,3) rot=(0,0,-1;1.5708rad)
  Support = -> [Pocket105]
  sketch-geometry (5):
    g0: LineSegment StartX=3 StartY=8.5 StartZ=0 EndX=20 EndY=8.5 EndZ=0
    g1: ArcOfCircle CenterX=10 CenterY=8.5 CenterZ=0 NormalX=0 NormalY=0 NormalZ=1 AngleXU=0 Radius=3 StartAngle=1.5708 EndAngle=4.71239
    g2: ArcOfCircle CenterX=13 CenterY=8.5 CenterZ=0 NormalX=0 NormalY=0 NormalZ=1 AngleXU=0 Radius=3 StartAngle=4.71239 EndAngle=7.85398
    g3: LineSegment StartX=10 StartY=5.5 StartZ=0 EndX=13 EndY=5.5 EndZ=0
    g4: LineSegment StartX=10 StartY=11.5 StartZ=0 EndX=13 EndY=11.5 EndZ=0
  constraints (14):
    c: PointOnObject(g0,g-4)
    c: PointOnObject(g0,g-5)
    c: Horizontal(g0)
    c: DistanceY(g0,g-4) = 6.5
    c: Tangent(g1,g4) = 1.5708
    c: Tangent(g1,g3) = -1.5708
    c: Tangent(g3,g2) = -1.5708
    c: Tangent(g4,g2) = 1.5708
    c: Horizontal(g3)
    c: Equal(g1,g2)
    c: PointOnObject(g1,g0)
    c: Radius(g2) = 3
    c: DistanceX(g4,g4) = 3
    c: DistanceX(g2,g0) = 7
FEATURE [PartDesign::Pocket] Pocket106
  BaseFeature = -> Pocket105
  Length = 5
  Length2 = 100
  Placement = pos=(0,0,0) rot=(0.57735,0.57735,0.57735;2.0944rad)
  Profile = -> Sketch275
  Type = 2
FEATURE [Sketcher::SketchObject] Sketch276
  ExternalGeometry = -> [Pocket106]
  FullyConstrained = true
  MapMode = 5
  Placement = pos=(0,0,0) rot=(0.57735,0.57735,0.57735;4.18879rad)
  Support = -> [Pocket106]
  sketch-geometry (9):
    g0: LineSegment StartX=0 StartY=8.5 StartZ=0 EndX=20 EndY=8.5 EndZ=0
    g1: ArcOfCircle CenterX=3 CenterY=9.5 CenterZ=0 NormalX=0 NormalY=0 NormalZ=1 AngleXU=0 Radius=1 StartAngle=0 EndAngle=3.14159
    g2: ArcOfCircle CenterX=3 CenterY=7.5 CenterZ=0 NormalX=0 NormalY=0 NormalZ=1 AngleXU=0 Radius=1 StartAngle=3.14159 EndAngle=6.28319
    g3: LineSegment StartX=2 StartY=9.5 StartZ=0 EndX=2 EndY=7.5 EndZ=0
    g4: LineSegment StartX=4 StartY=9.5 StartZ=0 EndX=4 EndY=7.5 EndZ=0
    g5: ArcOfCircle CenterX=18 CenterY=9.5 CenterZ=0 NormalX=0 NormalY=0 NormalZ=1 AngleXU=0 Radius=1 StartAngle=-9e-16 EndAngle=3.14159
    g6: ArcOfCircle CenterX=18 CenterY=7.5 CenterZ=0 NormalX=0 NormalY=0 NormalZ=1 AngleXU=0 Radius=1 StartAngle=3.14159 EndAngle=6.28319
    g7: LineSegment StartX=17 StartY=9.5 StartZ=0 EndX=17 EndY=7.5 EndZ=0
    g8: LineSegment StartX=19 StartY=9.5 StartZ=0 EndX=19 EndY=7.5 EndZ=0
  constraints (24):
    c: PointOnObject(g0,g-2)
    c: PointOnObject(g0,g-5)
    c: Horizontal(g0)
    c: DistanceY(g0,g-3) = 8.5
    c: Tangent(g1,g4) = 1.5708
    c: Tangent(g1,g3) = -1.5708
    c: Tangent(g3,g2) = -1.5708
    c: Tangent(g4,g2) = 1.5708
    c: Vertical(g3)
    c: Equal(g1,g2)
    c: Tangent(g5,g8) = 1.5708
    c: Tangent(g5,g7) = -1.5708
    c: Tangent(g7,g6) = -1.5708
    c: Tangent(g8,g6) = 1.5708
    c: Vertical(g7)
    c: Equal(g5,g6)
    c: Equal(g1,g5)
    c: Equal(g4,g7)
    c: DistanceY(g4,g4) = 2
    c: Radius(g1) = 1
    c: Horizontal(g5,g1)
    c: DistanceX(g0,g1) = 3
    c: DistanceX(g5,g0) = 2
    c: DistanceY(g0,g1) = 1
FEATURE [PartDesign::Pad] Pad136
  BaseFeature = -> Pocket106
  Direction = (1,1,1)
  Length = 1
  Length2 = 100
  Placement = pos=(0,0,0) rot=(0.57735,0.57735,0.57735;2.0944rad)
  Profile = -> Sketch276
  Type = 0
FEATURE [Sketcher::SketchObject] Sketch277
  ExternalGeometry = -> [Pad136]
  FullyConstrained = true
  MapMode = 5
  Placement = pos=(0,0,1e-16) rot=(0.707107,0.707107,0;3.14159rad)
  Support = -> [Pad136]
  sketch-geometry (9):
    g0: LineSegment StartX=0 StartY=8.5 StartZ=0 EndX=-20 EndY=8.5 EndZ=0
    g1: ArcOfCircle CenterX=-3 CenterY=7.5 CenterZ=0 NormalX=0 NormalY=0 NormalZ=1 AngleXU=0 Radius=1 StartAngle=3.14159 EndAngle=6.28319
    g2: ArcOfCircle CenterX=-3 CenterY=9.5 CenterZ=0 NormalX=0 NormalY=0 NormalZ=1 AngleXU=0 Radius=1 StartAngle=3e-16 EndAngle=3.14159
    g3: LineSegment StartX=-2 StartY=7.5 StartZ=0 EndX=-2 EndY=9.5 EndZ=0
    g4: LineSegment StartX=-4 StartY=7.5 StartZ=0 EndX=-4 EndY=9.5 EndZ=0
    g5: ArcOfCircle CenterX=-18 CenterY=9.5 CenterZ=0 NormalX=0 NormalY=0 NormalZ=1 AngleXU=0 Radius=1 StartAngle=0 EndAngle=3.14159
    g6: ArcOfCircle CenterX=-18 CenterY=7.5 CenterZ=0 NormalX=0 NormalY=0 NormalZ=1 AngleXU=0 Radius=1 StartAngle=3.14159 EndAngle=6.28319
    g7: LineSegment StartX=-19 StartY=9.5 StartZ=0 EndX=-19 EndY=7.5 EndZ=0
    g8: LineSegment StartX=-17 StartY=9.5 StartZ=0 EndX=-17 EndY=7.5 EndZ=0
  constraints (24):
    c: PointOnObject(g0,g-2)
    c: PointOnObject(g0,g-4)
    c: Horizontal(g0)
    c: DistanceY(g0,g-3) = 8.5
    c: Tangent(g1,g4) = 1.5708
    c: Tangent(g1,g3) = -1.5708
    c: Tangent(g3,g2) = -1.5708
    c: Tangent(g4,g2) = 1.5708
    c: Vertical(g3)
    c: Equal(g1,g2)
    c: Radius(g2) = 1
    c: DistanceY(g4,g4) = 2
    c: DistanceY(g0,g2) = 1
    c: DistanceX(g2,g0) = 3
    c: Tangent(g5,g8) = 1.5708
    c: Tangent(g5,g7) = -1.5708
    c: Tangent(g7,g6) = -1.5708
    c: Tangent(g8,g6) = 1.5708
    c: Vertical(g7)
    c: Equal(g5,g6)
    c: Equal(g5,g2)
    c: Equal(g8,g4)
    c: Horizontal(g5,g2)
    c: DistanceX(g0,g5) = 2
FEATURE [PartDesign::Pad] Pad137
  BaseFeature = -> Pad136
  Direction = (1,1,1)
  Length = 1
  Length2 = 100
  Placement = pos=(0,0,0) rot=(0.57735,0.57735,0.57735;2.0944rad)
  Profile = -> Sketch277
  Type = 0
FEATURE [PartDesign::Body] Body207  label="Corner010"
  Group = -> [Sketch272,Pad135,Sketch273,Pocket104,Sketch274,Pocket105,Sketch275,Pocket106,Sketch276,Pad136,Sketch277,Pad137]
  Origin = -> Origin287
  Tip = -> Pad137
FEATURE [App::Part] Part080  label="soporte90-011"
  Group = -> [Body207]
  Origin = -> Origin288
  Placement = pos=(322,320,70) rot=(1,0,0;1.5708rad)
FEATURE [Sketcher::SketchObject] Sketch278
  FullyConstrained = true
  MapMode = 5
  Placement = pos=(0,0,0) rot=(0.57735,0.57735,0.57735;2.0944rad)
  Support = -> [YZ_Plane283]
  sketch-geometry (5):
    g0: LineSegment StartX=0 StartY=0 StartZ=0 EndX=0 EndY=20 EndZ=0
    g1: LineSegment StartX=0 StartY=20 StartZ=0 EndX=-3 EndY=20 EndZ=0
    g2: LineSegment StartX=-3 StartY=20 StartZ=0 EndX=-20 EndY=3 EndZ=0
    g3: LineSegment StartX=-20 StartY=3 StartZ=0 EndX=-20 EndY=0 EndZ=0
    g4: LineSegment StartX=-20 StartY=0 StartZ=0 EndX=0 EndY=0 EndZ=0
  constraints (14):
    c: Coincident(g-1,g0)
    c: PointOnObject(g0,g-2)
    c: Coincident(g0,g1)
    c: Horizontal(g1)
    c: Coincident(g1,g2)
    c: Coincident(g2,g3)
    c: PointOnObject(g3,g-1)
    c: Vertical(g3)
    c: Coincident(g3,g4)
    c: Coincident(g4,g0)
    c: DistanceY(g0,g0) = 20
    c: DistanceY(g3,g3) = 3
    c: DistanceX(g1,g1) = 3
    c: DistanceX(g4,g4) = 20
FEATURE [PartDesign::Pad] Pad138
  Direction = (1,1,1)
  Length = 17
  Length2 = 100
  Placement = pos=(0,0,0) rot=(0.57735,0.57735,0.57735;2.0944rad)
  Profile = -> Sketch278
  Type = 0
FEATURE [Sketcher::SketchObject] Sketch279
  ExternalGeometry = -> [Pad138]
  FullyConstrained = true
  MapMode = 5
  Placement = pos=(-8.8e-15,-20,4.4e-15) rot=(-0.57735,-0.57735,0.57735;4.18879rad)
  Support = -> [Pad138]
  sketch-geometry (4):
    g0: LineSegment StartX=-3 StartY=2 StartZ=0 EndX=-20 EndY=2 EndZ=0
    g1: LineSegment StartX=-20 StartY=2 StartZ=0 EndX=-20 EndY=15 EndZ=0
    g2: LineSegment StartX=-20 StartY=15 StartZ=0 EndX=-3 EndY=15 EndZ=0
    g3: LineSegment StartX=-3 StartY=15 StartZ=0 EndX=-3 EndY=2 EndZ=0
  constraints (12):
    c: Coincident(g0,g1)
    c: Coincident(g1,g2)
    c: Coincident(g2,g3)
    c: Coincident(g3,g0)
    c: Horizontal(g0)
    c: Horizontal(g2)
    c: Vertical(g1)
    c: Vertical(g3)
    c: PointOnObject(g0,g-3)
    c: DistanceY(g1,g-6) = 2
    c: DistanceY(g-6,g0) = 2
    c: PointOnObject(g1,g-6)
FEATURE [PartDesign::Pocket] Pocket107
  BaseFeature = -> Pad138
  Length = 17
  Length2 = 100
  Placement = pos=(0,0,0) rot=(0.57735,0.57735,0.57735;2.0944rad)
  Profile = -> Sketch279
  Type = 0
FEATURE [Sketcher::SketchObject] Sketch280
  ExternalGeometry = -> [Pocket107]
  FullyConstrained = true
  MapMode = 5
  Placement = pos=(-1.7e-15,-3,6e-16) rot=(-0.57735,-0.57735,0.57735;4.18879rad)
  Support = -> [Pocket107]
  sketch-geometry (5):
    g0: LineSegment StartX=-20 StartY=8.5 StartZ=0 EndX=-3 EndY=8.5 EndZ=0
    g1: ArcOfCircle CenterX=-10 CenterY=8.5 CenterZ=0 NormalX=0 NormalY=0 NormalZ=1 AngleXU=0 Radius=3 StartAngle=4.71239 EndAngle=7.85398
    g2: ArcOfCircle CenterX=-13 CenterY=8.5 CenterZ=0 NormalX=0 NormalY=0 NormalZ=1 AngleXU=0 Radius=3 StartAngle=1.5708 EndAngle=4.71239
    g3: LineSegment StartX=-10 StartY=11.5 StartZ=0 EndX=-13 EndY=11.5 EndZ=0
    g4: LineSegment StartX=-10 StartY=5.5 StartZ=0 EndX=-13 EndY=5.5 EndZ=0
  constraints (14):
    c: PointOnObject(g0,g-6)
    c: PointOnObject(g0,g-4)
    c: Horizontal(g0)
    c: DistanceY(g0,g-4) = 6.5
    c: Tangent(g1,g4) = 1.5708
    c: Tangent(g1,g3) = -1.5708
    c: Tangent(g3,g2) = -1.5708
    c: Tangent(g4,g2) = 1.5708
    c: Horizontal(g3)
    c: Equal(g1,g2)
    c: PointOnObject(g1,g0)
    c: Radius(g1) = 3
    c: DistanceX(g3,g3) = 3
    c: DistanceX(g0,g2) = 7
FEATURE [PartDesign::Pocket] Pocket108
  BaseFeature = -> Pocket107
  Length = 5
  Length2 = 100
  Placement = pos=(0,0,0) rot=(0.57735,0.57735,0.57735;2.0944rad)
  Profile = -> Sketch280
  Type = 2
FEATURE [Sketcher::SketchObject] Sketch281
  ExternalGeometry = -> [Pocket108]
  FullyConstrained = true
  MapMode = 5
  Placement = pos=(-3e-16,1.2e-15,3) rot=(0,0,-1;1.5708rad)
  Support = -> [Pocket108]
  sketch-geometry (5):
    g0: LineSegment StartX=3 StartY=8.5 StartZ=0 EndX=20 EndY=8.5 EndZ=0
    g1: ArcOfCircle CenterX=10 CenterY=8.5 CenterZ=0 NormalX=0 NormalY=0 NormalZ=1 AngleXU=0 Radius=3 StartAngle=1.5708 EndAngle=4.71239
    g2: ArcOfCircle CenterX=13 CenterY=8.5 CenterZ=0 NormalX=0 NormalY=0 NormalZ=1 AngleXU=0 Radius=3 StartAngle=4.71239 EndAngle=7.85398
    g3: LineSegment StartX=10 StartY=5.5 StartZ=0 EndX=13 EndY=5.5 EndZ=0
    g4: LineSegment StartX=10 StartY=11.5 StartZ=0 EndX=13 EndY=11.5 EndZ=0
  constraints (14):
    c: PointOnObject(g0,g-4)
    c: PointOnObject(g0,g-5)
    c: Horizontal(g0)
    c: DistanceY(g0,g-4) = 6.5
    c: Tangent(g1,g4) = 1.5708
    c: Tangent(g1,g3) = -1.5708
    c: Tangent(g3,g2) = -1.5708
    c: Tangent(g4,g2) = 1.5708
    c: Horizontal(g3)
    c: Equal(g1,g2)
    c: PointOnObject(g1,g0)
    c: Radius(g2) = 3
    c: DistanceX(g4,g4) = 3
    c: DistanceX(g2,g0) = 7
FEATURE [PartDesign::Pocket] Pocket109
  BaseFeature = -> Pocket108
  Length = 5
  Length2 = 100
  Placement = pos=(0,0,0) rot=(0.57735,0.57735,0.57735;2.0944rad)
  Profile = -> Sketch281
  Type = 2
FEATURE [Sketcher::SketchObject] Sketch282
  ExternalGeometry = -> [Pocket109]
  FullyConstrained = true
  MapMode = 5
  Placement = pos=(0,0,0) rot=(0.57735,0.57735,0.57735;4.18879rad)
  Support = -> [Pocket109]
  sketch-geometry (9):
    g0: LineSegment StartX=0 StartY=8.5 StartZ=0 EndX=20 EndY=8.5 EndZ=0
    g1: ArcOfCircle CenterX=3 CenterY=9.5 CenterZ=0 NormalX=0 NormalY=0 NormalZ=1 AngleXU=0 Radius=1 StartAngle=0 EndAngle=3.14159
    g2: ArcOfCircle CenterX=3 CenterY=7.5 CenterZ=0 NormalX=0 NormalY=0 NormalZ=1 AngleXU=0 Radius=1 StartAngle=3.14159 EndAngle=6.28319
    g3: LineSegment StartX=2 StartY=9.5 StartZ=0 EndX=2 EndY=7.5 EndZ=0
    g4: LineSegment StartX=4 StartY=9.5 StartZ=0 EndX=4 EndY=7.5 EndZ=0
    g5: ArcOfCircle CenterX=18 CenterY=9.5 CenterZ=0 NormalX=0 NormalY=0 NormalZ=1 AngleXU=0 Radius=1 StartAngle=-9e-16 EndAngle=3.14159
    g6: ArcOfCircle CenterX=18 CenterY=7.5 CenterZ=0 NormalX=0 NormalY=0 NormalZ=1 AngleXU=0 Radius=1 StartAngle=3.14159 EndAngle=6.28319
    g7: LineSegment StartX=17 StartY=9.5 StartZ=0 EndX=17 EndY=7.5 EndZ=0
    g8: LineSegment StartX=19 StartY=9.5 StartZ=0 EndX=19 EndY=7.5 EndZ=0
  constraints (24):
    c: PointOnObject(g0,g-2)
    c: PointOnObject(g0,g-5)
    c: Horizontal(g0)
    c: DistanceY(g0,g-3) = 8.5
    c: Tangent(g1,g4) = 1.5708
    c: Tangent(g1,g3) = -1.5708
    c: Tangent(g3,g2) = -1.5708
    c: Tangent(g4,g2) = 1.5708
    c: Vertical(g3)
    c: Equal(g1,g2)
    c: Tangent(g5,g8) = 1.5708
    c: Tangent(g5,g7) = -1.5708
    c: Tangent(g7,g6) = -1.5708
    c: Tangent(g8,g6) = 1.5708
    c: Vertical(g7)
    c: Equal(g5,g6)
    c: Equal(g1,g5)
    c: Equal(g4,g7)
    c: DistanceY(g4,g4) = 2
    c: Radius(g1) = 1
    c: Horizontal(g5,g1)
    c: DistanceX(g0,g1) = 3
    c: DistanceX(g5,g0) = 2
    c: DistanceY(g0,g1) = 1
FEATURE [PartDesign::Pad] Pad139
  BaseFeature = -> Pocket109
  Direction = (1,1,1)
  Length = 1
  Length2 = 100
  Placement = pos=(0,0,0) rot=(0.57735,0.57735,0.57735;2.0944rad)
  Profile = -> Sketch282
  Type = 0
FEATURE [Sketcher::SketchObject] Sketch283
  ExternalGeometry = -> [Pad139]
  FullyConstrained = true
  MapMode = 5
  Placement = pos=(0,0,1e-16) rot=(0.707107,0.707107,0;3.14159rad)
  Support = -> [Pad139]
  sketch-geometry (9):
    g0: LineSegment StartX=0 StartY=8.5 StartZ=0 EndX=-20 EndY=8.5 EndZ=0
    g1: ArcOfCircle CenterX=-3 CenterY=7.5 CenterZ=0 NormalX=0 NormalY=0 NormalZ=1 AngleXU=0 Radius=1 StartAngle=3.14159 EndAngle=6.28319
    g2: ArcOfCircle CenterX=-3 CenterY=9.5 CenterZ=0 NormalX=0 NormalY=0 NormalZ=1 AngleXU=0 Radius=1 StartAngle=3e-16 EndAngle=3.14159
    g3: LineSegment StartX=-2 StartY=7.5 StartZ=0 EndX=-2 EndY=9.5 EndZ=0
    g4: LineSegment StartX=-4 StartY=7.5 StartZ=0 EndX=-4 EndY=9.5 EndZ=0
    g5: ArcOfCircle CenterX=-18 CenterY=9.5 CenterZ=0 NormalX=0 NormalY=0 NormalZ=1 AngleXU=0 Radius=1 StartAngle=0 EndAngle=3.14159
    g6: ArcOfCircle CenterX=-18 CenterY=7.5 CenterZ=0 NormalX=0 NormalY=0 NormalZ=1 AngleXU=0 Radius=1 StartAngle=3.14159 EndAngle=6.28319
    g7: LineSegment StartX=-19 StartY=9.5 StartZ=0 EndX=-19 EndY=7.5 EndZ=0
    g8: LineSegment StartX=-17 StartY=9.5 StartZ=0 EndX=-17 EndY=7.5 EndZ=0
  constraints (24):
    c: PointOnObject(g0,g-2)
    c: PointOnObject(g0,g-4)
    c: Horizontal(g0)
    c: DistanceY(g0,g-3) = 8.5
    c: Tangent(g1,g4) = 1.5708
    c: Tangent(g1,g3) = -1.5708
    c: Tangent(g3,g2) = -1.5708
    c: Tangent(g4,g2) = 1.5708
    c: Vertical(g3)
    c: Equal(g1,g2)
    c: Radius(g2) = 1
    c: DistanceY(g4,g4) = 2
    c: DistanceY(g0,g2) = 1
    c: DistanceX(g2,g0) = 3
    c: Tangent(g5,g8) = 1.5708
    c: Tangent(g5,g7) = -1.5708
    c: Tangent(g7,g6) = -1.5708
    c: Tangent(g8,g6) = 1.5708
    c: Vertical(g7)
    c: Equal(g5,g6)
    c: Equal(g5,g2)
    c: Equal(g8,g4)
    c: Horizontal(g5,g2)
    c: DistanceX(g0,g5) = 2
FEATURE [PartDesign::Pad] Pad140
  BaseFeature = -> Pad139
  Direction = (1,1,1)
  Length = 1
  Length2 = 100
  Placement = pos=(0,0,0) rot=(0.57735,0.57735,0.57735;2.0944rad)
  Profile = -> Sketch283
  Type = 0
FEATURE [PartDesign::Body] Body208  label="Corner011"
  Group = -> [Sketch278,Pad138,Sketch279,Pocket107,Sketch280,Pocket108,Sketch281,Pocket109,Sketch282,Pad139,Sketch283,Pad140]
  Origin = -> Origin289
  Tip = -> Pad140
FEATURE [App::Part] Part081  label="soporte90-012"
  Group = -> [Body208]
  Origin = -> Origin290
  Placement = pos=(319,20,70) rot=(1,0,0;3.14159rad)
FEATURE [App::LinkGroup] LinkGroup010  label="esquineros estructura"
  ElementList = -> [Part081,Part074,Part070,Part071,Part072,Part073,Part075,Part076,Part080,Part079,Part078,Part077]
  LinkMode = 0
FEATURE [Sketcher::SketchObject] Sketch284
  FullyConstrained = false
  MapMode = 5
  Support = -> [XY_Plane286]
  sketch-geometry (4):
    g0: ArcOfCircle CenterX=0 CenterY=4e-15 CenterZ=0 NormalX=0 NormalY=0 NormalZ=1 AngleXU=0 Radius=11 StartAngle=2.18335 EndAngle=3.14159
    g1: LineSegment StartX=-11 StartY=4e-15 StartZ=0 EndX=0 EndY=4e-15 EndZ=0
    g2: LineSegment StartX=0 StartY=9 StartZ=0 EndX=0 EndY=3.6e-15 EndZ=0
    g3: LineSegment StartX=0 StartY=9 StartZ=0 EndX=-6.32456 EndY=9 EndZ=0
  constraints (10):
    c: Coincident(g0,g-1)
    c: Diameter(g0) = 22
    c: Coincident(g1,g0)
    c: Horizontal(g1)
    c: Coincident(g0,g1)
    c: Coincident(g2,g0)
    c: Vertical(g2)
    c: Horizontal(g3)
    c: Coincident(g3,g2)
    c: Coincident(g3,g0)
FEATURE [PartDesign::Revolution] Revolution046
  Angle = 360
  Axis = (0,1,0)
  Base = (0,0,0)
  Profile = -> Sketch284
  ReferenceAxis = -> Sketch284 [V_Axis]
FEATURE [PartDesign::Body] Body209
  Group = -> [Sketch284,Revolution046]
  Origin = -> Origin292
  Tip = -> Revolution046
FEATURE [App::Part] Part082  label="tacoGoma-002"
  Group = -> [Body209]
  Origin = -> Origin291
  Placement = pos=(10,9,0) rot=(1,0,0;-1.5708rad)
FEATURE [Sketcher::SketchObject] Sketch285
  FullyConstrained = false
  MapMode = 5
  Support = -> [XY_Plane288]
  sketch-geometry (4):
    g0: ArcOfCircle CenterX=0 CenterY=4e-15 CenterZ=0 NormalX=0 NormalY=0 NormalZ=1 AngleXU=0 Radius=11 StartAngle=2.18335 EndAngle=3.14159
    g1: LineSegment StartX=-11 StartY=4e-15 StartZ=0 EndX=0 EndY=4e-15 EndZ=0
    g2: LineSegment StartX=0 StartY=9 StartZ=0 EndX=0 EndY=3.6e-15 EndZ=0
    g3: LineSegment StartX=0 StartY=9 StartZ=0 EndX=-6.32456 EndY=9 EndZ=0
  constraints (10):
    c: Coincident(g0,g-1)
    c: Diameter(g0) = 22
    c: Coincident(g1,g0)
    c: Horizontal(g1)
    c: Coincident(g0,g1)
    c: Coincident(g2,g0)
    c: Vertical(g2)
    c: Horizontal(g3)
    c: Coincident(g3,g2)
    c: Coincident(g3,g0)
FEATURE [PartDesign::Revolution] Revolution047
  Angle = 360
  Axis = (0,1,0)
  Base = (0,0,0)
  Profile = -> Sketch285
  ReferenceAxis = -> Sketch285 [V_Axis]
FEATURE [PartDesign::Body] Body210
  Group = -> [Sketch285,Revolution047]
  Origin = -> Origin294
  Tip = -> Revolution047
FEATURE [App::Part] Part083  label="tacoGoma001"
  Group = -> [Body210]
  Origin = -> Origin293
  Placement = pos=(10,331,0) rot=(1,0,0;-1.5708rad)
FEATURE [Sketcher::SketchObject] Sketch286
  FullyConstrained = false
  MapMode = 5
  Support = -> [XY_Plane290]
  sketch-geometry (4):
    g0: ArcOfCircle CenterX=0 CenterY=4e-15 CenterZ=0 NormalX=0 NormalY=0 NormalZ=1 AngleXU=0 Radius=11 StartAngle=2.18335 EndAngle=3.14159
    g1: LineSegment StartX=-11 StartY=4e-15 StartZ=0 EndX=0 EndY=4e-15 EndZ=0
    g2: LineSegment StartX=0 StartY=9 StartZ=0 EndX=0 EndY=3.6e-15 EndZ=0
    g3: LineSegment StartX=0 StartY=9 StartZ=0 EndX=-6.32456 EndY=9 EndZ=0
  constraints (10):
    c: Coincident(g0,g-1)
    c: Diameter(g0) = 22
    c: Coincident(g1,g0)
    c: Horizontal(g1)
    c: Coincident(g0,g1)
    c: Coincident(g2,g0)
    c: Vertical(g2)
    c: Horizontal(g3)
    c: Coincident(g3,g2)
    c: Coincident(g3,g0)
FEATURE [PartDesign::Revolution] Revolution048
  Angle = 360
  Axis = (0,1,0)
  Base = (0,0,0)
  Profile = -> Sketch286
  ReferenceAxis = -> Sketch286 [V_Axis]
FEATURE [PartDesign::Body] Body211
  Group = -> [Sketch286,Revolution048]
  Origin = -> Origin296
  Tip = -> Revolution048
FEATURE [App::Part] Part084  label="tacoGoma002"
  Group = -> [Body211]
  Origin = -> Origin295
  Placement = pos=(330,330,2e-16) rot=(1,0,0;-1.5708rad)
FEATURE [Sketcher::SketchObject] Sketch287
  FullyConstrained = false
  MapMode = 5
  Support = -> [XY_Plane292]
  sketch-geometry (4):
    g0: ArcOfCircle CenterX=0 CenterY=4e-15 CenterZ=0 NormalX=0 NormalY=0 NormalZ=1 AngleXU=0 Radius=11 StartAngle=2.18335 EndAngle=3.14159
    g1: LineSegment StartX=-11 StartY=4e-15 StartZ=0 EndX=0 EndY=4e-15 EndZ=0
    g2: LineSegment StartX=0 StartY=9 StartZ=0 EndX=0 EndY=3.6e-15 EndZ=0
    g3: LineSegment StartX=0 StartY=9 StartZ=0 EndX=-6.32456 EndY=9 EndZ=0
  constraints (10):
    c: Coincident(g0,g-1)
    c: Diameter(g0) = 22
    c: Coincident(g1,g0)
    c: Horizontal(g1)
    c: Coincident(g0,g1)
    c: Coincident(g2,g0)
    c: Vertical(g2)
    c: Horizontal(g3)
    c: Coincident(g3,g2)
    c: Coincident(g3,g0)
FEATURE [PartDesign::Revolution] Revolution049
  Angle = 360
  Axis = (0,1,0)
  Base = (0,0,0)
  Profile = -> Sketch287
  ReferenceAxis = -> Sketch287 [V_Axis]
FEATURE [PartDesign::Body] Body212
  Group = -> [Sketch287,Revolution049]
  Origin = -> Origin298
  Tip = -> Revolution049
FEATURE [App::Part] Part085  label="tacoGoma003"
  Group = -> [Body212]
  Origin = -> Origin297
  Placement = pos=(330,9,0) rot=(1,0,0;-1.5708rad)
FEATURE [App::LinkGroup] LinkGroup011  label="tacos de madera"
  ElementList = -> [Part082,Part083,Part084,Part085]
  LinkMode = 0
FEATURE [PartDesign::Plane] DatumPlane
  AttachmentOffset = pos=(0,0,0) rot=(0,1,0;0.174533rad)
  Length = 68.686
  MapMode = 5
  Placement = pos=(0,0,0) rot=(0.992433,0.086827,0.086827;1.57839rad)
  ResizeMode = 0
  Support = -> [XZ_Plane296]
  Width = 60.7632
FEATURE [Part::Helix] Helix001  label="Hélice001"
  Angle = 0
  AttacherType = Attacher::AttachEngine3D
  Height = 9.1
  LocalCoord = 0
  Pitch = 1.5
  Placement = pos=(0,0,7.35) rot=(0,0,1;0rad)
  Radius = 10
  Style = 1
FEATURE [PartDesign::ShapeBinder] ShapeBinder001
  Placement = pos=(0,0,7.35) rot=(0,0,1;0rad)
  Support = -> [Helix001]
  TraceSupport = false
FEATURE [Sketcher::SketchObject] Sketch289
  FullyConstrained = false
  MapMode = 5
  Placement = pos=(0,0,0) rot=(1,0,0;1.5708rad)
  Support = -> [XZ_Plane296]
  sketch-geometry (6):
    g0: LineSegment StartX=-9 StartY=25 StartZ=0 EndX=-4 EndY=25 EndZ=0
    g1: LineSegment StartX=-2.5 StartY=8 StartZ=0 EndX=-2.5 EndY=0 EndZ=0
    g2: LineSegment StartX=-2.5 StartY=0 StartZ=0 EndX=-9 EndY=0 EndZ=0
    g3: LineSegment StartX=-9 StartY=0 StartZ=0 EndX=-9 EndY=25 EndZ=0
    g4: LineSegment StartX=-2.5 StartY=8 StartZ=0 EndX=-4 EndY=8 EndZ=0
    g5: LineSegment StartX=-4 StartY=8 StartZ=0 EndX=-4 EndY=25 EndZ=0
  constraints (18):
    c: Coincident(g1,g2)
    c: Coincident(g2,g3)
    c: Coincident(g3,g0)
    c: Horizontal(g0)
    c: Horizontal(g2)
    c: Vertical(g1)
    c: Vertical(g3)
    c: PointOnObject(g1,g-1)
    c: DistanceX(g1,g-1) = 2.5
    c: DistanceX(g2,g-1) = 9
    c: DistanceY(g3,g3) = 25
    c: Horizontal(g4)
    c: Coincident(g5,g4)
    c: Vertical(g5)
    c: Coincident(g1,g4)
    c: Coincident(g0,g5)
    c: DistanceX(g0,g-1) = 4
    c: DistanceY(g5,g5) = 17
FEATURE [PartDesign::Revolution] Revolution050
  AllowMultiFace = false
  Angle = 360
  Axis = (0,-2e-16,1)
  Base = (0,0,0)
  Placement = pos=(0,0,0) rot=(1,0,0;1.5708rad)
  Profile = -> Sketch289
  ReferenceAxis = -> Sketch289 [V_Axis]
  Refine = true
FEATURE [Sketcher::SketchObject] Sketch290
  FullyConstrained = false
  MapMode = 5
  Placement = pos=(0,0,0) rot=(1,0,0;1.5708rad)
  Support = -> [XZ_Plane296]
  sketch-geometry (4):
    g0: LineSegment StartX=0.227639 StartY=16.7629 StartZ=0 EndX=11.1677 EndY=16.7629 EndZ=0
    g1: LineSegment StartX=11.1677 StartY=16.7629 StartZ=0 EndX=11.1677 EndY=16.2629 EndZ=0
    g2: LineSegment StartX=11.1677 StartY=16.2629 StartZ=0 EndX=0.227639 EndY=16.2629 EndZ=0
    g3: LineSegment StartX=0.227639 StartY=16.2629 StartZ=0 EndX=0.227639 EndY=16.7629 EndZ=0
  constraints (9):
    c: Coincident(g0,g1)
    c: Coincident(g1,g2)
    c: Coincident(g2,g3)
    c: Coincident(g3,g0)
    c: Horizontal(g0)
    c: Horizontal(g2)
    c: Vertical(g1)
    c: Vertical(g3)
    c: DistanceY(g1,g1) = 0.5
FEATURE [Sketcher::SketchObject] Sketch292
  FullyConstrained = false
  MapMode = 5
  Placement = pos=(0,0,0) rot=(1,0,0;1.5708rad)
  Support = -> [XZ_Plane297]
  sketch-geometry (4):
    g0: LineSegment StartX=0 StartY=0 StartZ=0 EndX=-2 EndY=0 EndZ=0
    g1: LineSegment StartX=-2 StartY=0 StartZ=0 EndX=-2 EndY=6 EndZ=0
    g2: LineSegment StartX=-2 StartY=6 StartZ=0 EndX=0 EndY=6 EndZ=0
    g3: LineSegment StartX=0 StartY=6 StartZ=0 EndX=0 EndY=0 EndZ=0
  constraints (11):
    c: Coincident(g0,g1)
    c: Coincident(g1,g2)
    c: Coincident(g2,g3)
    c: Coincident(g3,g0)
    c: Horizontal(g0)
    c: Horizontal(g2)
    c: Vertical(g1)
    c: Vertical(g3)
    c: Coincident(g0,g-1)
    c: DistanceX(g2,g2) = 2
    c: DistanceY(g1,g1) = 6
FEATURE [PartDesign::Revolution] Revolution001
  AllowMultiFace = false
  Angle = 360
  Axis = (0,2e-16,1)
  Base = (0,0,0)
  Placement = pos=(0,0,0) rot=(1,0,0;1.5708rad)
  Profile = -> Sketch292
  ReferenceAxis = -> Sketch292 [V_Axis]
  Refine = true
FEATURE [Sketcher::SketchObject] Sketch293
  FullyConstrained = false
  MapMode = 5
  Placement = pos=(0,2.6e-15,6) rot=(0,0,1;3.14159rad)
  Support = -> [Revolution001]
  sketch-geometry (7):
    g0: LineSegment StartX=-0.625 StartY=-1.08253 StartZ=0 EndX=0.625 EndY=-1.08253 EndZ=0
    g1: LineSegment StartX=0.625 StartY=-1.08253 StartZ=0 EndX=1.25 EndY=-1.44e-14 EndZ=0
    g2: LineSegment StartX=1.25 StartY=-1.44e-14 StartZ=0 EndX=0.625 EndY=1.08253 EndZ=0
    g3: LineSegment StartX=0.625 StartY=1.08253 StartZ=0 EndX=-0.625 EndY=1.08253 EndZ=0
    g4: LineSegment StartX=-0.625 StartY=1.08253 StartZ=0 EndX=-1.25 EndY=-1.44e-14 EndZ=0
    g5: LineSegment StartX=-1.25 StartY=-1.44e-14 StartZ=0 EndX=-0.625 EndY=-1.08253 EndZ=0
    g6: Circle CenterX=0 CenterY=0 CenterZ=0 NormalX=0 NormalY=0 NormalZ=1 AngleXU=0 Radius=1.25
  constraints (16):
    c: Coincident(g0,g1)
    c: Coincident(g1,g2)
    c: Coincident(g2,g3)
    c: Coincident(g3,g4)
    c: Coincident(g4,g5)
    c: Coincident(g5,g0)
    c: Equal(g0, g1-g5) x5
    c: PointOnObject(g0,g6)
    c: PointOnObject(g1,g6)
    c: PointOnObject(g2,g6)
    c: PointOnObject(g3,g6)
    c: PointOnObject(g4,g6)
    c: PointOnObject(g5,g6)
    c: Coincident(g6,g-1)
    c: Horizontal(g0)
    c: DistanceX(g4,g1) = 2.5
FEATURE [PartDesign::Pocket] Pocket112
  AllowMultiFace = false
  BaseFeature = -> Revolution001
  Length = 2
  Length2 = 100
  Placement = pos=(0,0,0) rot=(1,0,0;1.5708rad)
  Profile = -> Sketch293
  Refine = true
  Type = 0
FEATURE [PartDesign::Chamfer] Chamfer012
  Angle = 45
  Base = -> Pocket112 [Edge2]
  BaseFeature = -> Pocket112
  ChamferType = 0
  FlipDirection = false
  Placement = pos=(0,0,0) rot=(1,0,0;1.5708rad)
  Size = 0.35
  Size2 = 1
  SupportTransform = false
FEATURE [PartDesign::Chamfer] Chamfer013
  Angle = 45
  Base = -> Chamfer012 [Edge3]
  BaseFeature = -> Chamfer012
  ChamferType = 0
  FlipDirection = false
  Placement = pos=(0,0,0) rot=(1,0,0;1.5708rad)
  Size = 0.75
  Size2 = 1
  SupportTransform = false
FEATURE [PartDesign::Body] Body213  label="Set Screw"
  Group = -> [Sketch292,Revolution001,Sketch293,Pocket112,Chamfer012,Chamfer013]
  Origin = -> Origin303
  Tip = -> Chamfer013
FEATURE [PartDesign::FeatureBase] Clone084
  BaseFeature = -> Body213
FEATURE [PartDesign::Body] Body215  label="Clon1"
  BaseFeature = -> Body213
  Group = -> [Clone084]
  Origin = -> Origin304
  Placement = pos=(0,-3,4) rot=(1,0,0;1.5708rad)
  Tip = -> Clone084
FEATURE [PartDesign::FeatureBase] Clone085
  BaseFeature = -> Body215
  Placement = pos=(0,-4,4) rot=(1,0,0;1.5708rad)
FEATURE [PartDesign::Body] Body216  label="Clon2"
  BaseFeature = -> Body215
  Group = -> [Clone085]
  Origin = -> Origin305
  Placement = pos=(-0.173648,0.984808,17) rot=(0,0,1;0.174533rad)
  Tip = -> Clone085
FEATURE [PartDesign::FeatureBase] Clone086
  BaseFeature = -> Body215
  Placement = pos=(0,-4,4) rot=(1,0,0;1.5708rad)
FEATURE [PartDesign::Body] Body217  label="Clon3"
  BaseFeature = -> Body215
  Group = -> [Clone086]
  Origin = -> Origin306
  Placement = pos=(-1,0,0) rot=(0,0,1;1.5708rad)
  Tip = -> Clone086
FEATURE [PartDesign::FeatureBase] Clone087
  BaseFeature = -> Body216
  Placement = pos=(0,0,17) rot=(0,0,1;0.174533rad)
FEATURE [PartDesign::Body] Body218  label="Clon4"
  BaseFeature = -> Body216
  Group = -> [Clone087]
  Origin = -> Origin307
  Placement = pos=(-1,2e-16,0) rot=(0,0,1;1.5708rad)
  Tip = -> Clone087
FEATURE [App::Part] Part088  label="fastener"
  Group = -> [Body213,Body215,Body216,Body217,Body218]
  Origin = -> Origin301
FEATURE [PartDesign::SubtractivePipe] SubtractivePipe
  AllowMultiFace = false
  AuxilleryCurvelinear = true
  AuxillerySpineTangent = false
  BaseFeature = -> Revolution050
  Binormal = (0,0,0)
  Mode = 2
  Placement = pos=(0,0,0) rot=(1,0,0;1.5708rad)
  Profile = -> Sketch290
  Refine = true
  Spine = -> ShapeBinder001
  SpineTangent = false
  Transformation = 0
  Transition = 0
FEATURE [Sketcher::SketchObject] Sketch291
  ExternalGeometry = -> [SubtractivePipe]
  FullyConstrained = false
  MapMode = 5
  Placement = pos=(0,0,0) rot=(1,0,0;1.5708rad)
  Support = -> [XZ_Plane296]
  sketch-geometry (4):
    g0: Circle CenterX=0 CenterY=4 CenterZ=0 NormalX=0 NormalY=0 NormalZ=1 AngleXU=0 Radius=2
    g1: Circle CenterX=0 CenterY=21 CenterZ=0 NormalX=0 NormalY=0 NormalZ=1 AngleXU=0 Radius=2
    g2: LineSegment StartX=0 StartY=4 StartZ=0 EndX=0 EndY=0 EndZ=0
    g3: LineSegment StartX=0 StartY=21 StartZ=0 EndX=0 EndY=25 EndZ=0
  constraints (9):
    c: PointOnObject(g0,g-2)
    c: PointOnObject(g1,g-2)
    c: Radius(g1) = 2
    c: Equal(g0,g1)
    c: Coincident(g2,g0)
    c: Coincident(g2,g-1)
    c: Coincident(g3,g1)
    c: Vertical(g3)
    c: Equal(g3,g2)
FEATURE [PartDesign::Pocket] Pocket111
  AllowMultiFace = false
  BaseFeature = -> SubtractivePipe
  Length = 10
  Length2 = 100
  Placement = pos=(0,0,0) rot=(1,0,0;1.5708rad)
  Profile = -> Sketch291
  Refine = true
  Reversed = true
  Type = 0
FEATURE [Sketcher::SketchObject] Sketch288
  ExternalGeometry = -> [Pocket111]
  FullyConstrained = false
  MapMode = 5
  Placement = pos=(0,0,0) rot=(0.992433,0.086827,0.086827;1.57839rad)
  Support = -> [DatumPlane]
  sketch-geometry (1):
    g0: Circle CenterX=0 CenterY=21 CenterZ=0 NormalX=0 NormalY=0 NormalZ=1 AngleXU=0 Radius=2
  constraints (3):
    c: PointOnObject(g0,g-2)
    c: Radius(g0) = 2
    c: DistanceY(g0,g-3) = 4
FEATURE [PartDesign::Pocket] Pocket110
  AllowMultiFace = false
  BaseFeature = -> Pocket111
  Length = 10
  Length2 = 100
  Placement = pos=(0,0,0) rot=(1,0,0;1.5708rad)
  Profile = -> Sketch288
  Refine = true
  Reversed = true
  Type = 0
FEATURE [PartDesign::PolarPattern] PolarPattern024
  Angle = 90
  Axis = -> Sketch291 [V_Axis]
  BaseFeature = -> Pocket110
  Occurrences = 3
  Originals = -> [Pocket111,Pocket110]
  Placement = pos=(0,0,0) rot=(1,0,0;1.5708rad)
  Refine = true
FEATURE [PartDesign::Body] Body214  label="Beam coupling"
  Group = -> [Sketch289,Revolution050,ShapeBinder001,Sketch290,SubtractivePipe,Sketch291,Pocket111,DatumPlane,Sketch288,Pocket110,PolarPattern024]
  Origin = -> Origin302
  Tip = -> PolarPattern024
FEATURE [App::Part] Part087  label="Beam coupling "
  Group = -> [Body214,Helix001]
  Origin = -> Origin300
FEATURE [App::Part] Part086  label="Beam-coupling-8mm-5mm-002"
  Group = -> [Part087,Part088]
  Origin = -> Origin299
  Placement = pos=(385,116,105) rot=(0,1,0;-1.5708rad)
FEATURE [PartDesign::Plane] DatumPlane001
  AttachmentOffset = pos=(0,0,0) rot=(0,1,0;0.174533rad)
  Length = 68.686
  MapMode = 5
  Placement = pos=(0,0,0) rot=(0.992433,0.086827,0.086827;1.57839rad)
  ResizeMode = 0
  Support = -> [XZ_Plane305]
  Width = 60.7632
FEATURE [Part::Helix] Helix002  label="Hélice002"
  Angle = 0
  AttacherType = Attacher::AttachEngine3D
  Height = 9.1
  LocalCoord = 0
  Pitch = 1.5
  Placement = pos=(0,0,7.35) rot=(0,0,1;0rad)
  Radius = 10
  Style = 1
FEATURE [PartDesign::ShapeBinder] ShapeBinder002
  Placement = pos=(0,0,7.35) rot=(0,0,1;0rad)
  Support = -> [Helix002]
  TraceSupport = false
FEATURE [Sketcher::SketchObject] Sketch295
  FullyConstrained = false
  MapMode = 5
  Placement = pos=(0,0,0) rot=(1,0,0;1.5708rad)
  Support = -> [XZ_Plane305]
  sketch-geometry (6):
    g0: LineSegment StartX=-9 StartY=25 StartZ=0 EndX=-4 EndY=25 EndZ=0
    g1: LineSegment StartX=-2.5 StartY=8 StartZ=0 EndX=-2.5 EndY=0 EndZ=0
    g2: LineSegment StartX=-2.5 StartY=0 StartZ=0 EndX=-9 EndY=0 EndZ=0
    g3: LineSegment StartX=-9 StartY=0 StartZ=0 EndX=-9 EndY=25 EndZ=0
    g4: LineSegment StartX=-2.5 StartY=8 StartZ=0 EndX=-4 EndY=8 EndZ=0
    g5: LineSegment StartX=-4 StartY=8 StartZ=0 EndX=-4 EndY=25 EndZ=0
  constraints (18):
    c: Coincident(g1,g2)
    c: Coincident(g2,g3)
    c: Coincident(g3,g0)
    c: Horizontal(g0)
    c: Horizontal(g2)
    c: Vertical(g1)
    c: Vertical(g3)
    c: PointOnObject(g1,g-1)
    c: DistanceX(g1,g-1) = 2.5
    c: DistanceX(g2,g-1) = 9
    c: DistanceY(g3,g3) = 25
    c: Horizontal(g4)
    c: Coincident(g5,g4)
    c: Vertical(g5)
    c: Coincident(g1,g4)
    c: Coincident(g0,g5)
    c: DistanceX(g0,g-1) = 4
    c: DistanceY(g5,g5) = 17
FEATURE [PartDesign::Revolution] Revolution052
  AllowMultiFace = false
  Angle = 360
  Axis = (0,-2e-16,1)
  Base = (0,0,0)
  Placement = pos=(0,0,0) rot=(1,0,0;1.5708rad)
  Profile = -> Sketch295
  ReferenceAxis = -> Sketch295 [V_Axis]
  Refine = true
FEATURE [Sketcher::SketchObject] Sketch296
  FullyConstrained = false
  MapMode = 5
  Placement = pos=(0,0,0) rot=(1,0,0;1.5708rad)
  Support = -> [XZ_Plane305]
  sketch-geometry (4):
    g0: LineSegment StartX=0.227639 StartY=16.7629 StartZ=0 EndX=11.1677 EndY=16.7629 EndZ=0
    g1: LineSegment StartX=11.1677 StartY=16.7629 StartZ=0 EndX=11.1677 EndY=16.2629 EndZ=0
    g2: LineSegment StartX=11.1677 StartY=16.2629 StartZ=0 EndX=0.227639 EndY=16.2629 EndZ=0
    g3: LineSegment StartX=0.227639 StartY=16.2629 StartZ=0 EndX=0.227639 EndY=16.7629 EndZ=0
  constraints (9):
    c: Coincident(g0,g1)
    c: Coincident(g1,g2)
    c: Coincident(g2,g3)
    c: Coincident(g3,g0)
    c: Horizontal(g0)
    c: Horizontal(g2)
    c: Vertical(g1)
    c: Vertical(g3)
    c: DistanceY(g1,g1) = 0.5
FEATURE [Sketcher::SketchObject] Sketch298
  FullyConstrained = false
  MapMode = 5
  Placement = pos=(0,0,0) rot=(1,0,0;1.5708rad)
  Support = -> [XZ_Plane306]
  sketch-geometry (4):
    g0: LineSegment StartX=0 StartY=0 StartZ=0 EndX=-2 EndY=0 EndZ=0
    g1: LineSegment StartX=-2 StartY=0 StartZ=0 EndX=-2 EndY=6 EndZ=0
    g2: LineSegment StartX=-2 StartY=6 StartZ=0 EndX=0 EndY=6 EndZ=0
    g3: LineSegment StartX=0 StartY=6 StartZ=0 EndX=0 EndY=0 EndZ=0
  constraints (11):
    c: Coincident(g0,g1)
    c: Coincident(g1,g2)
    c: Coincident(g2,g3)
    c: Coincident(g3,g0)
    c: Horizontal(g0)
    c: Horizontal(g2)
    c: Vertical(g1)
    c: Vertical(g3)
    c: Coincident(g0,g-1)
    c: DistanceX(g2,g2) = 2
    c: DistanceY(g1,g1) = 6
FEATURE [PartDesign::Revolution] Revolution051
  AllowMultiFace = false
  Angle = 360
  Axis = (0,2e-16,1)
  Base = (0,0,0)
  Placement = pos=(0,0,0) rot=(1,0,0;1.5708rad)
  Profile = -> Sketch298
  ReferenceAxis = -> Sketch298 [V_Axis]
  Refine = true
FEATURE [Sketcher::SketchObject] Sketch299
  FullyConstrained = false
  MapMode = 5
  Placement = pos=(0,2.6e-15,6) rot=(0,0,1;3.14159rad)
  Support = -> [Revolution051]
  sketch-geometry (7):
    g0: LineSegment StartX=-0.625 StartY=-1.08253 StartZ=0 EndX=0.625 EndY=-1.08253 EndZ=0
    g1: LineSegment StartX=0.625 StartY=-1.08253 StartZ=0 EndX=1.25 EndY=-1.44e-14 EndZ=0
    g2: LineSegment StartX=1.25 StartY=-1.44e-14 StartZ=0 EndX=0.625 EndY=1.08253 EndZ=0
    g3: LineSegment StartX=0.625 StartY=1.08253 StartZ=0 EndX=-0.625 EndY=1.08253 EndZ=0
    g4: LineSegment StartX=-0.625 StartY=1.08253 StartZ=0 EndX=-1.25 EndY=-1.44e-14 EndZ=0
    g5: LineSegment StartX=-1.25 StartY=-1.44e-14 StartZ=0 EndX=-0.625 EndY=-1.08253 EndZ=0
    g6: Circle CenterX=0 CenterY=0 CenterZ=0 NormalX=0 NormalY=0 NormalZ=1 AngleXU=0 Radius=1.25
  constraints (16):
    c: Coincident(g0,g1)
    c: Coincident(g1,g2)
    c: Coincident(g2,g3)
    c: Coincident(g3,g4)
    c: Coincident(g4,g5)
    c: Coincident(g5,g0)
    c: Equal(g0, g1-g5) x5
    c: PointOnObject(g0,g6)
    c: PointOnObject(g1,g6)
    c: PointOnObject(g2,g6)
    c: PointOnObject(g3,g6)
    c: PointOnObject(g4,g6)
    c: PointOnObject(g5,g6)
    c: Coincident(g6,g-1)
    c: Horizontal(g0)
    c: DistanceX(g4,g1) = 2.5
FEATURE [PartDesign::Pocket] Pocket115
  AllowMultiFace = false
  BaseFeature = -> Revolution051
  Length = 2
  Length2 = 100
  Placement = pos=(0,0,0) rot=(1,0,0;1.5708rad)
  Profile = -> Sketch299
  Refine = true
  Type = 0
FEATURE [PartDesign::Chamfer] Chamfer014
  Angle = 45
  Base = -> Pocket115 [Edge2]
  BaseFeature = -> Pocket115
  ChamferType = 0
  FlipDirection = false
  Placement = pos=(0,0,0) rot=(1,0,0;1.5708rad)
  Size = 0.35
  Size2 = 1
  SupportTransform = false
FEATURE [PartDesign::Chamfer] Chamfer015
  Angle = 45
  Base = -> Chamfer014 [Edge3]
  BaseFeature = -> Chamfer014
  ChamferType = 0
  FlipDirection = false
  Placement = pos=(0,0,0) rot=(1,0,0;1.5708rad)
  Size = 0.75
  Size2 = 1
  SupportTransform = false
FEATURE [PartDesign::Body] Body219  label="Set Screw001"
  Group = -> [Sketch298,Revolution051,Sketch299,Pocket115,Chamfer014,Chamfer015]
  Origin = -> Origin312
  Tip = -> Chamfer015
FEATURE [PartDesign::FeatureBase] Clone088
  BaseFeature = -> Body219
FEATURE [PartDesign::Body] Body221  label="Clon005"
  BaseFeature = -> Body219
  Group = -> [Clone088]
  Origin = -> Origin313
  Placement = pos=(0,-3,4) rot=(1,0,0;1.5708rad)
  Tip = -> Clone088
FEATURE [PartDesign::FeatureBase] Clone089
  BaseFeature = -> Body221
  Placement = pos=(0,-4,4) rot=(1,0,0;1.5708rad)
FEATURE [PartDesign::Body] Body222  label="Clon006"
  BaseFeature = -> Body221
  Group = -> [Clone089]
  Origin = -> Origin314
  Placement = pos=(-0.173648,0.984808,17) rot=(0,0,1;0.174533rad)
  Tip = -> Clone089
FEATURE [PartDesign::FeatureBase] Clone090
  BaseFeature = -> Body221
  Placement = pos=(0,-4,4) rot=(1,0,0;1.5708rad)
FEATURE [PartDesign::Body] Body223  label="Clon007"
  BaseFeature = -> Body221
  Group = -> [Clone090]
  Origin = -> Origin315
  Placement = pos=(-1,0,0) rot=(0,0,1;1.5708rad)
  Tip = -> Clone090
FEATURE [PartDesign::FeatureBase] Clone091
  BaseFeature = -> Body222
  Placement = pos=(0,0,17) rot=(0,0,1;0.174533rad)
FEATURE [PartDesign::Body] Body224  label="Clon008"
  BaseFeature = -> Body222
  Group = -> [Clone091]
  Origin = -> Origin316
  Placement = pos=(-1,2e-16,0) rot=(0,0,1;1.5708rad)
  Tip = -> Clone091
FEATURE [App::Part] Part091  label="fastener001"
  Group = -> [Body219,Body221,Body222,Body223,Body224]
  Origin = -> Origin310
FEATURE [PartDesign::SubtractivePipe] SubtractivePipe001
  AllowMultiFace = false
  AuxilleryCurvelinear = true
  AuxillerySpineTangent = false
  BaseFeature = -> Revolution052
  Binormal = (0,0,0)
  Mode = 2
  Placement = pos=(0,0,0) rot=(1,0,0;1.5708rad)
  Profile = -> Sketch296
  Refine = true
  Spine = -> ShapeBinder002
  SpineTangent = false
  Transformation = 0
  Transition = 0
FEATURE [Sketcher::SketchObject] Sketch297
  ExternalGeometry = -> [SubtractivePipe001]
  FullyConstrained = false
  MapMode = 5
  Placement = pos=(0,0,0) rot=(1,0,0;1.5708rad)
  Support = -> [XZ_Plane305]
  sketch-geometry (4):
    g0: Circle CenterX=0 CenterY=4 CenterZ=0 NormalX=0 NormalY=0 NormalZ=1 AngleXU=0 Radius=2
    g1: Circle CenterX=0 CenterY=21 CenterZ=0 NormalX=0 NormalY=0 NormalZ=1 AngleXU=0 Radius=2
    g2: LineSegment StartX=0 StartY=4 StartZ=0 EndX=0 EndY=0 EndZ=0
    g3: LineSegment StartX=0 StartY=21 StartZ=0 EndX=0 EndY=25 EndZ=0
  constraints (9):
    c: PointOnObject(g0,g-2)
    c: PointOnObject(g1,g-2)
    c: Radius(g1) = 2
    c: Equal(g0,g1)
    c: Coincident(g2,g0)
    c: Coincident(g2,g-1)
    c: Coincident(g3,g1)
    c: Vertical(g3)
    c: Equal(g3,g2)
FEATURE [PartDesign::Pocket] Pocket114
  AllowMultiFace = false
  BaseFeature = -> SubtractivePipe001
  Length = 10
  Length2 = 100
  Placement = pos=(0,0,0) rot=(1,0,0;1.5708rad)
  Profile = -> Sketch297
  Refine = true
  Reversed = true
  Type = 0
FEATURE [Sketcher::SketchObject] Sketch294
  ExternalGeometry = -> [Pocket114]
  FullyConstrained = false
  MapMode = 5
  Placement = pos=(0,0,0) rot=(0.992433,0.086827,0.086827;1.57839rad)
  Support = -> [DatumPlane001]
  sketch-geometry (1):
    g0: Circle CenterX=0 CenterY=21 CenterZ=0 NormalX=0 NormalY=0 NormalZ=1 AngleXU=0 Radius=2
  constraints (3):
    c: PointOnObject(g0,g-2)
    c: Radius(g0) = 2
    c: DistanceY(g0,g-3) = 4
FEATURE [PartDesign::Pocket] Pocket113
  AllowMultiFace = false
  BaseFeature = -> Pocket114
  Length = 10
  Length2 = 100
  Placement = pos=(0,0,0) rot=(1,0,0;1.5708rad)
  Profile = -> Sketch294
  Refine = true
  Reversed = true
  Type = 0
FEATURE [PartDesign::PolarPattern] PolarPattern025
  Angle = 90
  Axis = -> Sketch297 [V_Axis]
  BaseFeature = -> Pocket113
  Occurrences = 3
  Originals = -> [Pocket114,Pocket113]
  Placement = pos=(0,0,0) rot=(1,0,0;1.5708rad)
  Refine = true
FEATURE [PartDesign::Body] Body220  label="Beam coupling001"
  Group = -> [Sketch295,Revolution052,ShapeBinder002,Sketch296,SubtractivePipe001,Sketch297,Pocket114,DatumPlane001,Sketch294,Pocket113,PolarPattern025]
  Origin = -> Origin311
  Tip = -> PolarPattern025
FEATURE [App::Part] Part090  label="Beam coupling 001"
  Group = -> [Body220,Helix002]
  Origin = -> Origin309
FEATURE [App::Part] Part089  label="Beam-coupling-8mm-5mm-001"
  Group = -> [Part090,Part091]
  Origin = -> Origin308
  Placement = pos=(384.965,242,105) rot=(0,1,0;4.72984rad)
FEATURE [Sketcher::SketchObject] Sketch304
  FullyConstrained = false
  MapMode = 3
  Placement = pos=(0,0,0) rot=(1,0,0;3.14159rad)
  sketch-geometry (9):
    g0: LineSegment StartX=-21.15 StartY=21.25 StartZ=0 EndX=21.15 EndY=21.25 EndZ=0
    g1: LineSegment StartX=21.15 StartY=21.25 StartZ=0 EndX=21.15 EndY=-21.15 EndZ=0
    g2: LineSegment StartX=21.15 StartY=-21.15 StartZ=0 EndX=-21.15 EndY=-21.15 EndZ=0
    g3: LineSegment StartX=-21.15 StartY=-21.15 StartZ=0 EndX=-21.15 EndY=21.25 EndZ=0
    g4: Circle CenterX=0 CenterY=0 CenterZ=0 NormalX=0 NormalY=0 NormalZ=1 AngleXU=0 Radius=11
    g5: Circle CenterX=-15.5 CenterY=15.5 CenterZ=0 NormalX=0 NormalY=0 NormalZ=1 AngleXU=0 Radius=1.5
    g6: Circle CenterX=15.5 CenterY=15.5 CenterZ=0 NormalX=0 NormalY=0 NormalZ=1 AngleXU=0 Radius=1.5
    g7: Circle CenterX=-15.5 CenterY=-15.5 CenterZ=0 NormalX=0 NormalY=0 NormalZ=1 AngleXU=0 Radius=1.5
    g8: Circle CenterX=15.5 CenterY=-15.5 CenterZ=0 NormalX=0 NormalY=0 NormalZ=1 AngleXU=0 Radius=1.5
  constraints (18):
    c: Coincident(g0,g1)
    c: Coincident(g1,g2)
    c: Coincident(g2,g3)
    c: Coincident(g3,g0)
    c: Horizontal(g0)
    c: Horizontal(g2)
    c: Vertical(g1)
    c: Vertical(g3)
    c: Coincident(g4,g-1)
    c: DistanceX(g0,g4) = 21.15
    c: DistanceX(g4,g0) = 21.15
    c: DistanceY(g4,g0) = 21.25
    c: DistanceY(g2,g4) = 21.15
    c: Equal(g5,g6)
    c: Equal(g5,g8)
    c: Equal(g5,g7)
    c: Diameter(g5) = 3
    c: Diameter(g4) = 22
FEATURE [PartDesign::Pad] Pad144
  Direction = (0,2e-16,-1)
  Length = 2
  Length2 = 10
  Placement = pos=(0,0,0) rot=(1,0,0;3.14159rad)
  Profile = -> Sketch304
  Type = 0
FEATURE [Sketcher::SketchObject] Sketch305
  FullyConstrained = false
  MapMode = 5
  Placement = pos=(21.15,0,0) rot=(0.57735,-0.57735,0.57735;4.18879rad)
  sketch-geometry (4):
    g0: LineSegment StartX=-21.15 StartY=0 StartZ=0 EndX=21.25 EndY=1.8e-15 EndZ=0
    g1: LineSegment StartX=21.25 StartY=1.8e-15 StartZ=0 EndX=21.25 EndY=60 EndZ=0
    g2: LineSegment StartX=21.25 StartY=60 StartZ=0 EndX=-21.15 EndY=60 EndZ=0
    g3: LineSegment StartX=-21.15 StartY=60 StartZ=0 EndX=-21.15 EndY=0 EndZ=0
  constraints (8):
    c: Coincident(g0,g1)
    c: Coincident(g1,g2)
    c: Coincident(g2,g3)
    c: Coincident(g3,g0)
    c: Horizontal(g2)
    c: Vertical(g1)
    c: Vertical(g3)
    c: DistanceY(g0,g2) = 60
FEATURE [PartDesign::Pad] Pad145
  BaseFeature = -> Pad144
  Direction = (1,-1e-16,-1e-16)
  Length = 2
  Length2 = 10
  Placement = pos=(0,0,0) rot=(1,0,0;3.14159rad)
  Profile = -> Sketch305
  Type = 0
FEATURE [Sketcher::SketchObject] Sketch303
  ExternalGeometry = -> [Pad145]
  FullyConstrained = false
  Placement = pos=(21.15,-4e-15,-3e-15) rot=(0.57735,0.57735,-0.57735;4.18879rad)
  sketch-geometry (8):
    g0: ArcOfCircle CenterX=-12 CenterY=52 CenterZ=0 NormalX=0 NormalY=0 NormalZ=1 AngleXU=0 Radius=2 StartAngle=0 EndAngle=3.14159
    g1: ArcOfCircle CenterX=-12 CenterY=12 CenterZ=0 NormalX=0 NormalY=0 NormalZ=1 AngleXU=0 Radius=2 StartAngle=3.14159 EndAngle=6.28319
    g2: LineSegment StartX=-10 StartY=52 StartZ=0 EndX=-10 EndY=12 EndZ=0
    g3: LineSegment StartX=-14 StartY=12 StartZ=0 EndX=-14 EndY=52 EndZ=0
    g4: ArcOfCircle CenterX=12 CenterY=52 CenterZ=0 NormalX=0 NormalY=0 NormalZ=1 AngleXU=0 Radius=2 StartAngle=0 EndAngle=3.14159
    g5: ArcOfCircle CenterX=12 CenterY=12 CenterZ=0 NormalX=0 NormalY=0 NormalZ=1 AngleXU=0 Radius=2 StartAngle=3.14159 EndAngle=6.28319
    g6: LineSegment StartX=10 StartY=52 StartZ=0 EndX=10 EndY=12 EndZ=0
    g7: LineSegment StartX=14 StartY=12 StartZ=0 EndX=14 EndY=52 EndZ=0
  constraints (16):
    c: Equal(g0,g1)
    c: Diameter(g1) = 4
    c: DistanceY(g0,g-3) = 8
    c: DistanceY(g1,g0) = 40
    c: DistanceX(g0,g-1) = 12
    c: DistanceX(g1,g-1) = 12
    c: Tangent(g1,g2) = 1.5708
    c: Tangent(g1,g3) = 1.5708
    c: Tangent(g0,g3) = 1.5708
    c: Tangent(g0,g2) = 1.5708
    c: Equal(g4,g5)
    c: Diameter(g5) = 4
    c: Tangent(g5,g6) = -1.5708
    c: Tangent(g5,g7) = -1.5708
    c: Tangent(g4,g7) = -1.5708
    c: Tangent(g4,g6) = -1.5708
FEATURE [PartDesign::Pocket] Pocket117
  BaseFeature = -> Pad145
  Length = 5
  Length2 = 5
  Placement = pos=(0,0,0) rot=(1,0,0;3.14159rad)
  Profile = -> Sketch303
  Type = 0
FEATURE [Sketcher::SketchObject] Sketch306
  FullyConstrained = true
  MapMode = 5
  Support = -> [XY_Plane316]
  sketch-geometry (3):
    g0: LineSegment StartX=0 StartY=0 StartZ=0 EndX=6 EndY=0 EndZ=0
    g1: LineSegment StartX=0 StartY=0 StartZ=0 EndX=0 EndY=6 EndZ=0
    g2: LineSegment StartX=0 StartY=6 StartZ=0 EndX=6 EndY=0 EndZ=0
  constraints (8):
    c: Coincident(g0,g-1)
    c: PointOnObject(g0,g-1)
    c: Coincident(g1,g0)
    c: PointOnObject(g1,g-2)
    c: Coincident(g2,g1)
    c: Coincident(g2,g0)
    c: DistanceX(g0,g0) = 6
    c: DistanceY(g0,g1) = 6
FEATURE [PartDesign::Pad] Pad143
  Direction = (0,0,1)
  Length = 2
  Length2 = 10
  Profile = -> Sketch306
  Type = 0
FEATURE [PartDesign::Body] Body226
  Group = -> [Sketch306,Pad143]
  Origin = -> Origin322
  Tip = -> Pad143
FEATURE [App::Part] Part093
  Group = -> [Body226]
  Origin = -> Origin319
  Placement = pos=(-2,21.15,-21.13) rot=(0.57735,-0.57735,0.57735;2.0944rad)
FEATURE [Sketcher::SketchObject] Sketch307
  FullyConstrained = true
  MapMode = 5
  Support = -> [XY_Plane318]
  sketch-geometry (3):
    g0: LineSegment StartX=0 StartY=0 StartZ=0 EndX=6 EndY=0 EndZ=0
    g1: LineSegment StartX=0 StartY=0 StartZ=0 EndX=0 EndY=6 EndZ=0
    g2: LineSegment StartX=0 StartY=6 StartZ=0 EndX=6 EndY=0 EndZ=0
  constraints (8):
    c: Coincident(g0,g-1)
    c: PointOnObject(g0,g-1)
    c: Coincident(g1,g0)
    c: PointOnObject(g1,g-2)
    c: Coincident(g2,g1)
    c: Coincident(g2,g0)
    c: DistanceX(g0,g0) = 6
    c: DistanceY(g0,g1) = 6
FEATURE [PartDesign::Pad] Pad146
  Direction = (0,0,1)
  Length = 2
  Length2 = 10
  Profile = -> Sketch307
  Type = 0
FEATURE [PartDesign::Body] Body228
  Group = -> [Sketch307,Pad146]
  Origin = -> Origin324
  Tip = -> Pad146
FEATURE [App::Part] Part095
  Group = -> [Body228]
  Origin = -> Origin323
  Placement = pos=(-2,-19.24,-21.13) rot=(0.57735,-0.57735,0.57735;2.0944rad)
FEATURE [PartDesign::Chamfer] Chamfer016
  Angle = 45
  Base = -> Pocket117 [Edge1]
  BaseFeature = -> Pocket117
  ChamferType = 0
  FlipDirection = false
  Placement = pos=(0,0,0) rot=(1,0,0;3.14159rad)
  Size = 2
  Size2 = 1
  SupportTransform = false
FEATURE [PartDesign::Chamfer] Chamfer017
  Angle = 45
  Base = -> Chamfer016 [Edge30]
  BaseFeature = -> Chamfer016
  ChamferType = 0
  FlipDirection = false
  Placement = pos=(0,0,0) rot=(1,0,0;3.14159rad)
  Size = 2
  Size2 = 1
  SupportTransform = false
FEATURE [Sketcher::SketchObject] Sketch309
  FullyConstrained = false
  MapMode = 3
  Placement = pos=(0,0,0) rot=(1,0,0;3.14159rad)
  sketch-geometry (9):
    g0: LineSegment StartX=-21.15 StartY=21.25 StartZ=0 EndX=21.15 EndY=21.25 EndZ=0
    g1: LineSegment StartX=21.15 StartY=21.25 StartZ=0 EndX=21.15 EndY=-21.15 EndZ=0
    g2: LineSegment StartX=21.15 StartY=-21.15 StartZ=0 EndX=-21.15 EndY=-21.15 EndZ=0
    g3: LineSegment StartX=-21.15 StartY=-21.15 StartZ=0 EndX=-21.15 EndY=21.25 EndZ=0
    g4: Circle CenterX=0 CenterY=0 CenterZ=0 NormalX=0 NormalY=0 NormalZ=1 AngleXU=0 Radius=11
    g5: Circle CenterX=-15.5 CenterY=15.5 CenterZ=0 NormalX=0 NormalY=0 NormalZ=1 AngleXU=0 Radius=1.5
    g6: Circle CenterX=15.5 CenterY=15.5 CenterZ=0 NormalX=0 NormalY=0 NormalZ=1 AngleXU=0 Radius=1.5
    g7: Circle CenterX=-15.5 CenterY=-15.5 CenterZ=0 NormalX=0 NormalY=0 NormalZ=1 AngleXU=0 Radius=1.5
    g8: Circle CenterX=15.5 CenterY=-15.5 CenterZ=0 NormalX=0 NormalY=0 NormalZ=1 AngleXU=0 Radius=1.5
  constraints (18):
    c: Coincident(g0,g1)
    c: Coincident(g1,g2)
    c: Coincident(g2,g3)
    c: Coincident(g3,g0)
    c: Horizontal(g0)
    c: Horizontal(g2)
    c: Vertical(g1)
    c: Vertical(g3)
    c: Coincident(g4,g-1)
    c: DistanceX(g0,g4) = 21.15
    c: DistanceX(g4,g0) = 21.15
    c: DistanceY(g4,g0) = 21.25
    c: DistanceY(g2,g4) = 21.15
    c: Equal(g5,g6)
    c: Equal(g5,g8)
    c: Equal(g5,g7)
    c: Diameter(g5) = 3
    c: Diameter(g4) = 22
FEATURE [PartDesign::Pad] Pad148
  Direction = (0,2e-16,-1)
  Length = 2
  Length2 = 10
  Placement = pos=(0,0,0) rot=(1,0,0;3.14159rad)
  Profile = -> Sketch309
  Type = 0
FEATURE [Sketcher::SketchObject] Sketch310
  FullyConstrained = false
  MapMode = 5
  Placement = pos=(21.15,0,0) rot=(0.57735,-0.57735,0.57735;4.18879rad)
  sketch-geometry (4):
    g0: LineSegment StartX=-21.15 StartY=0 StartZ=0 EndX=21.25 EndY=1.8e-15 EndZ=0
    g1: LineSegment StartX=21.25 StartY=1.8e-15 StartZ=0 EndX=21.25 EndY=60 EndZ=0
    g2: LineSegment StartX=21.25 StartY=60 StartZ=0 EndX=-21.15 EndY=60 EndZ=0
    g3: LineSegment StartX=-21.15 StartY=60 StartZ=0 EndX=-21.15 EndY=0 EndZ=0
  constraints (8):
    c: Coincident(g0,g1)
    c: Coincident(g1,g2)
    c: Coincident(g2,g3)
    c: Coincident(g3,g0)
    c: Horizontal(g2)
    c: Vertical(g1)
    c: Vertical(g3)
    c: DistanceY(g0,g2) = 60
FEATURE [PartDesign::Pad] Pad149
  BaseFeature = -> Pad148
  Direction = (1,-1e-16,-1e-16)
  Length = 2
  Length2 = 10
  Placement = pos=(0,0,0) rot=(1,0,0;3.14159rad)
  Profile = -> Sketch310
  Type = 0
FEATURE [Sketcher::SketchObject] Sketch308
  ExternalGeometry = -> [Pad149]
  FullyConstrained = false
  Placement = pos=(21.15,-4e-15,-3e-15) rot=(0.57735,0.57735,-0.57735;4.18879rad)
  sketch-geometry (8):
    g0: ArcOfCircle CenterX=-12 CenterY=52 CenterZ=0 NormalX=0 NormalY=0 NormalZ=1 AngleXU=0 Radius=2 StartAngle=0 EndAngle=3.14159
    g1: ArcOfCircle CenterX=-12 CenterY=12 CenterZ=0 NormalX=0 NormalY=0 NormalZ=1 AngleXU=0 Radius=2 StartAngle=3.14159 EndAngle=6.28319
    g2: LineSegment StartX=-10 StartY=52 StartZ=0 EndX=-10 EndY=12 EndZ=0
    g3: LineSegment StartX=-14 StartY=12 StartZ=0 EndX=-14 EndY=52 EndZ=0
    g4: ArcOfCircle CenterX=12 CenterY=52 CenterZ=0 NormalX=0 NormalY=0 NormalZ=1 AngleXU=0 Radius=2 StartAngle=0 EndAngle=3.14159
    g5: ArcOfCircle CenterX=12 CenterY=12 CenterZ=0 NormalX=0 NormalY=0 NormalZ=1 AngleXU=0 Radius=2 StartAngle=3.14159 EndAngle=6.28319
    g6: LineSegment StartX=10 StartY=52 StartZ=0 EndX=10 EndY=12 EndZ=0
    g7: LineSegment StartX=14 StartY=12 StartZ=0 EndX=14 EndY=52 EndZ=0
  constraints (16):
    c: Equal(g0,g1)
    c: Diameter(g1) = 4
    c: DistanceY(g0,g-3) = 8
    c: DistanceY(g1,g0) = 40
    c: DistanceX(g0,g-1) = 12
    c: DistanceX(g1,g-1) = 12
    c: Tangent(g1,g2) = 1.5708
    c: Tangent(g1,g3) = 1.5708
    c: Tangent(g0,g3) = 1.5708
    c: Tangent(g0,g2) = 1.5708
    c: Equal(g4,g5)
    c: Diameter(g5) = 4
    c: Tangent(g5,g6) = -1.5708
    c: Tangent(g5,g7) = -1.5708
    c: Tangent(g4,g7) = -1.5708
    c: Tangent(g4,g6) = -1.5708
FEATURE [PartDesign::Pocket] Pocket118
  BaseFeature = -> Pad149
  Length = 5
  Length2 = 5
  Placement = pos=(0,0,0) rot=(1,0,0;3.14159rad)
  Profile = -> Sketch308
  Type = 0
FEATURE [PartDesign::Chamfer] Chamfer018
  Angle = 45
  Base = -> Pocket118 [Edge1]
  BaseFeature = -> Pocket118
  ChamferType = 0
  FlipDirection = false
  Placement = pos=(0,0,0) rot=(1,0,0;3.14159rad)
  Size = 2
  Size2 = 1
  SupportTransform = false
FEATURE [PartDesign::Chamfer] Chamfer019
  Angle = 45
  Base = -> Chamfer018 [Edge30]
  BaseFeature = -> Chamfer018
  ChamferType = 0
  FlipDirection = false
  Placement = pos=(0,0,0) rot=(1,0,0;3.14159rad)
  Size = 2
  Size2 = 1
  SupportTransform = false
FEATURE [PartDesign::Body] Body230
  Group = -> [Sketch309,Pad148,Sketch310,Pad149,Sketch308,Pocket118,Chamfer018,Chamfer019]
  Origin = -> Origin327
  Tip = -> Chamfer019
FEATURE [App::Part] Part097  label="soporteNEMA019"
  Group = -> [Body230]
  Origin = -> Origin326
  Placement = pos=(0,0,0) rot=(0,1,0;1.5708rad)
  expr: .Placement.Rotation.Angle = 90°
FEATURE [Sketcher::SketchObject] Sketch311
  FullyConstrained = true
  MapMode = 5
  Support = -> [XY_Plane322]
  sketch-geometry (3):
    g0: LineSegment StartX=0 StartY=0 StartZ=0 EndX=6 EndY=0 EndZ=0
    g1: LineSegment StartX=0 StartY=0 StartZ=0 EndX=0 EndY=6 EndZ=0
    g2: LineSegment StartX=0 StartY=6 StartZ=0 EndX=6 EndY=0 EndZ=0
  constraints (8):
    c: Coincident(g0,g-1)
    c: PointOnObject(g0,g-1)
    c: Coincident(g1,g0)
    c: PointOnObject(g1,g-2)
    c: Coincident(g2,g1)
    c: Coincident(g2,g0)
    c: DistanceX(g0,g0) = 6
    c: DistanceY(g0,g1) = 6
FEATURE [PartDesign::Pad] Pad147
  Direction = (0,0,1)
  Length = 2
  Length2 = 10
  Profile = -> Sketch311
  Type = 0
FEATURE [PartDesign::Body] Body229
  Group = -> [Sketch311,Pad147]
  Origin = -> Origin328
  Tip = -> Pad147
FEATURE [App::Part] Part096
  Group = -> [Body229]
  Origin = -> Origin325
  Placement = pos=(-2,21.15,-21.13) rot=(0.57735,-0.57735,0.57735;2.0944rad)
FEATURE [Sketcher::SketchObject] Sketch312
  FullyConstrained = true
  MapMode = 5
  Support = -> [XY_Plane324]
  sketch-geometry (3):
    g0: LineSegment StartX=0 StartY=0 StartZ=0 EndX=6 EndY=0 EndZ=0
    g1: LineSegment StartX=0 StartY=0 StartZ=0 EndX=0 EndY=6 EndZ=0
    g2: LineSegment StartX=0 StartY=6 StartZ=0 EndX=6 EndY=0 EndZ=0
  constraints (8):
    c: Coincident(g0,g-1)
    c: PointOnObject(g0,g-1)
    c: Coincident(g1,g0)
    c: PointOnObject(g1,g-2)
    c: Coincident(g2,g1)
    c: Coincident(g2,g0)
    c: DistanceX(g0,g0) = 6
    c: DistanceY(g0,g1) = 6
FEATURE [PartDesign::Pad] Pad150
  Direction = (0,0,1)
  Length = 2
  Length2 = 10
  Profile = -> Sketch312
  Type = 0
FEATURE [PartDesign::Body] Body231
  Group = -> [Sketch312,Pad150]
  Origin = -> Origin330
  Tip = -> Pad150
FEATURE [App::Part] Part098
  Group = -> [Body231]
  Origin = -> Origin329
  Placement = pos=(-2,-19.24,-21.13) rot=(0.57735,-0.57735,0.57735;2.0944rad)
FEATURE [App::LinkGroup] LinkGroup013  label="SoporteNEMA018-002"
  ElementList = -> [Part097,Part096,Part098]
  LinkMode = 0
  Placement = pos=(400,247,106) rot=(0,0,1;0rad)
FEATURE [App::LinkGroup] LinkGroup014  label="ruedas"
  ElementList = -> [Part037,Part067,Part069]
  LinkMode = 0
FEATURE [App::LinkGroup] LinkGroup016  label="acoples-ejes-motores"
  ElementList = -> [Part086,Part089]
  LinkMode = 0
  Placement = pos=(-1.52588e-05,4.00001,3.8147e-06) rot=(0,0,1;0rad)
FEATURE [PartDesign::ShapeBinder] CopyFillet054
  TraceSupport = false
FEATURE [Sketcher::SketchObject] Sketch313
  FullyConstrained = true
  MapMode = 5
  Placement = pos=(0,-3.4,0) rot=(1,0,0;1.5708rad)
  Support = -> [CopyFillet054]
FEATURE [Sketcher::SketchObject] Sketch314
  FullyConstrained = true
  MapMode = 5
  Placement = pos=(0,0,0) rot=(1,0,0;1.5708rad)
  Support = -> [XZ_Plane315]
FEATURE [PartDesign::ShapeBinder] ReferencePad053
  Placement = pos=(0,0,0) rot=(0.57735,0.57735,0.57735;2.0944rad)
  Support = -> [Pad053]
  TraceSupport = false
FEATURE [Sketcher::SketchObject] Sketch315
  FullyConstrained = true
  MapMode = 5
  Placement = pos=(0,0,0) rot=(0.57735,0.57735,-0.57735;4.18879rad)
  Support = -> [ReferencePad053]
FEATURE [Sketcher::SketchObject] Sketch316
  FullyConstrained = true
  MapMode = 5
  Placement = pos=(0,0,0) rot=(0.57735,0.57735,0.57735;2.0944rad)
  Support = -> [YZ_Plane315]
FEATURE [PartDesign::Body] Body227
  Group = -> [Sketch304,Pad144,Sketch305,Pad145,Sketch303,Pocket117,Chamfer016,Chamfer017,CopyFillet054,Sketch313,Sketch314,ReferencePad053,Sketch315,Sketch316]
  Origin = -> Origin321
  Tip = -> Chamfer017
FEATURE [App::Part] Part094  label="soporteNEMA018"
  Group = -> [Body227]
  Origin = -> Origin320
  Placement = pos=(0,0,0) rot=(0,1,0;1.5708rad)
  expr: .Placement.Rotation.Angle = 90°
FEATURE [App::LinkGroup] LinkGroup012  label="SoporteNEMA017-001"
  ElementList = -> [Part094,Part093,Part095]
  LinkMode = 0
  Placement = pos=(400,121,106) rot=(0,0,1;0rad)
FEATURE [App::LinkGroup] LinkGroup015  label="bases"
  ElementList = -> [Part066,LinkGroup012,LinkGroup013]
  LinkMode = 0
FEATURE [Sketcher::SketchObject] Sketch317
  FullyConstrained = true
  MapMode = 5
  Placement = pos=(0,0,0) rot=(1,0,0;1.5708rad)
  Support = -> [XZ_Plane328]
  sketch-geometry (1):
    g0: Circle CenterX=5.4 CenterY=4.4 CenterZ=0 NormalX=0 NormalY=0 NormalZ=1 AngleXU=0 Radius=0.4
  constraints (3):
    c: Diameter(g0) = 0.8
    c: DistanceY(g0) = 4.4
    c: DistanceX(g0) = 5.4
FEATURE [PartDesign::AdditiveHelix] AdditiveHelix
  Angle = 0
  Axis = (0,-2e-16,1)
  Base = (0,0,0)
  HasBeenEdited = true
  Height = 17.3
  LeftHanded = false
  Mode = 2
  Outside = false
  Pitch = 2.1625
  Placement = pos=(0,0,0) rot=(1,0,0;1.5708rad)
  Profile = -> Sketch317
  ReferenceAxis = -> Sketch317 [V_Axis]
  Turns = 3
FEATURE [PartDesign::Body] Body234  label="Spring"
  Group = -> [Sketch317,AdditiveHelix]
  Origin = -> Origin334
  Tip = -> AdditiveHelix
FEATURE [Sketcher::SketchObject] Sketch318
  FullyConstrained = true
  MapMode = 5
  Placement = pos=(0,0,0) rot=(1,0,0;1.5708rad)
  Support = -> [XZ_Plane326]
  sketch-geometry (6):
    g0: LineSegment StartX=0 StartY=0 StartZ=0 EndX=0 EndY=15 EndZ=0
    g1: LineSegment StartX=0 StartY=15 StartZ=0 EndX=-5 EndY=15 EndZ=0
    g2: LineSegment StartX=-5 StartY=15 StartZ=0 EndX=-5 EndY=4 EndZ=0
    g3: LineSegment StartX=-5 StartY=4 StartZ=0 EndX=-11 EndY=4 EndZ=0
    g4: LineSegment StartX=-11 StartY=4 StartZ=0 EndX=-11 EndY=0 EndZ=0
    g5: LineSegment StartX=-11 StartY=0 StartZ=0 EndX=0 EndY=0 EndZ=0
  constraints (17):
    c: Coincident(g-1,g0)
    c: Coincident(g0,g1)
    c: Coincident(g1,g2)
    c: Coincident(g2,g3)
    c: Horizontal(g3)
    c: Coincident(g3,g4)
    c: Vertical(g4)
    c: Coincident(g4,g5)
    c: Coincident(g5,g0)
    c: Horizontal(g5)
    c: Horizontal(g1)
    c: Vertical(g2)
    c: Vertical(g0)
    c: DistanceY(g0,g0) = 15
    c: DistanceY(g4,g4) = 4
    c: DistanceX(g1,g1) = 5
    c: DistanceX(g5,g5) = 11
FEATURE [PartDesign::Revolution] Revolution053
  Angle = 360
  Axis = (0,2e-16,1)
  Base = (0,0,0)
  Placement = pos=(0,0,0) rot=(1,0,0;1.5708rad)
  Profile = -> Sketch318
  ReferenceAxis = -> Sketch318 [V_Axis]
FEATURE [Sketcher::SketchObject] Sketch319
  FullyConstrained = true
  MapMode = 5
  Placement = pos=(0,1.8e-15,4) rot=(0,0,1;3.14159rad)
  Support = -> [Revolution053]
  sketch-geometry (1):
    g0: Circle CenterX=8 CenterY=0 CenterZ=0 NormalX=0 NormalY=0 NormalZ=1 AngleXU=0 Radius=1.7
  constraints (3):
    c: PointOnObject(g0,g-1)
    c: Diameter(g0) = 3.4
    c: DistanceX(g0) = 8
FEATURE [PartDesign::Pocket] Pocket119
  BaseFeature = -> Revolution053
  Length = 5
  Length2 = 5
  Placement = pos=(0,0,0) rot=(1,0,0;1.5708rad)
  Profile = -> Sketch319
  Type = 2
FEATURE [PartDesign::Chamfer] Chamfer020
  Angle = 45
  Base = -> Pocket119 [Edge5]
  BaseFeature = -> Pocket119
  ChamferType = 0
  FlipDirection = false
  Placement = pos=(0,0,0) rot=(1,0,0;1.5708rad)
  Size = 0.25
  Size2 = 1
  SupportTransform = false
FEATURE [PartDesign::PolarPattern] PolarPattern026
  Angle = 360
  Axis = -> Sketch319 [N_Axis]
  BaseFeature = -> Chamfer020
  Occurrences = 3
  Originals = -> [Pocket119,Chamfer020]
  Placement = pos=(0,0,0) rot=(1,0,0;1.5708rad)
FEATURE [Sketcher::SketchObject] Sketch320
  FullyConstrained = true
  MapMode = 5
  Placement = pos=(0,6.6e-15,15) rot=(0,0,1;3.14159rad)
  Support = -> [PolarPattern026]
  sketch-geometry (1):
    g0: Circle CenterX=0 CenterY=0 CenterZ=0 NormalX=0 NormalY=0 NormalZ=1 AngleXU=0 Radius=3.25
  constraints (2):
    c: Coincident(g0,g-1)
    c: Diameter(g0) = 6.5
FEATURE [PartDesign::Pocket] Pocket120
  BaseFeature = -> PolarPattern026
  Length = 5
  Length2 = 5
  Placement = pos=(0,0,0) rot=(1,0,0;1.5708rad)
  Profile = -> Sketch320
  Type = 2
FEATURE [Sketcher::SketchObject] Sketch321
  ExternalGeometry = -> [Pocket120]
  FullyConstrained = true
  MapMode = 5
  Placement = pos=(0,0,0) rot=(0.57735,0.57735,0.57735;2.0944rad)
  Support = -> [YZ_Plane326]
  sketch-geometry (5):
    g0: LineSegment StartX=-1.7 StartY=11 StartZ=0 EndX=-1.7 EndY=15 EndZ=0
    g1: LineSegment StartX=-1.7 StartY=15 StartZ=0 EndX=1.7 EndY=15 EndZ=0
    g2: LineSegment StartX=1.7 StartY=15 StartZ=0 EndX=1.7 EndY=11 EndZ=0
    g3: LineSegment StartX=1.7 StartY=11 StartZ=0 EndX=-1.7 EndY=11 EndZ=0
    g4: GeomPoint X=0 Y=13 Z=0
  constraints (13):
    c: Coincident(g0,g1)
    c: Coincident(g1,g2)
    c: Coincident(g2,g3)
    c: Coincident(g3,g0)
    c: Horizontal(g1)
    c: Horizontal(g3)
    c: Vertical(g0)
    c: Vertical(g2)
    c: Symmetric(g1,g0,g4)
    c: PointOnObject(g4,g-2)
    c: PointOnObject(g1,g-3)
    c: DistanceX(g3,g3) = 3.4
    c: DistanceY(g2,g2) = 4
FEATURE [PartDesign::Pocket] Pocket121
  BaseFeature = -> Pocket120
  Length = 5
  Length2 = 5
  Midplane = true
  Placement = pos=(0,0,0) rot=(1,0,0;1.5708rad)
  Profile = -> Sketch321
  Type = 1
FEATURE [Sketcher::SketchObject] Sketch322
  FullyConstrained = true
  MapMode = 5
  Placement = pos=(0,0,0) rot=(1,0,0;1.5708rad)
  Support = -> [XZ_Plane327]
  sketch-geometry (6):
    g0: LineSegment StartX=0 StartY=11 StartZ=0 EndX=0 EndY=26 EndZ=0
    g1: LineSegment StartX=0 StartY=26 StartZ=0 EndX=-7 EndY=26 EndZ=0
    g2: LineSegment StartX=-7 StartY=26 StartZ=0 EndX=-7 EndY=22 EndZ=0
    g3: LineSegment StartX=-7 StartY=22 StartZ=0 EndX=-5 EndY=22 EndZ=0
    g4: LineSegment StartX=-5 StartY=22 StartZ=0 EndX=-5 EndY=11 EndZ=0
    g5: LineSegment StartX=-5 StartY=11 StartZ=0 EndX=0 EndY=11 EndZ=0
  constraints (18):
    c: PointOnObject(g0,g-2)
    c: Vertical(g0)
    c: Coincident(g0,g1)
    c: Horizontal(g1)
    c: Coincident(g1,g2)
    c: Vertical(g2)
    c: Coincident(g2,g3)
    c: Horizontal(g3)
    c: Coincident(g3,g4)
    c: Vertical(g4)
    c: Coincident(g4,g5)
    c: Coincident(g5,g0)
    c: Horizontal(g5)
    c: DistanceX(g1,g1) = 7
    c: DistanceX(g5,g5) = 5
    c: DistanceY(g2,g2) = 4
    c: DistanceY(g0,g0) = 15
    c: DistanceY(g0) = 11
FEATURE [PartDesign::Revolution] Revolution054
  Angle = 360
  Axis = (0,2e-16,1)
  Base = (0,0,0)
  Placement = pos=(0,0,0) rot=(1,0,0;1.5708rad)
  Profile = -> Sketch322
  ReferenceAxis = -> Sketch322 [V_Axis]
FEATURE [Sketcher::SketchObject] Sketch323
  FullyConstrained = true
  MapMode = 5
  Placement = pos=(0,1.14e-14,26) rot=(0,0,1;3.14159rad)
  Support = -> [Revolution054]
  sketch-geometry (1):
    g0: Circle CenterX=0 CenterY=0 CenterZ=0 NormalX=0 NormalY=0 NormalZ=1 AngleXU=0 Radius=3.25
  constraints (2):
    c: Coincident(g0,g-1)
    c: Diameter(g0) = 6.5
FEATURE [PartDesign::Pocket] Pocket122
  BaseFeature = -> Revolution054
  Length = 5
  Length2 = 5
  Placement = pos=(0,0,0) rot=(1,0,0;1.5708rad)
  Profile = -> Sketch323
  Type = 2
FEATURE [Sketcher::SketchObject] Sketch324
  ExternalGeometry = -> [Pocket122]
  FullyConstrained = true
  MapMode = 5
  Placement = pos=(0,0,0) rot=(1,0,0;1.5708rad)
  Support = -> [XZ_Plane327]
  sketch-geometry (5):
    g0: LineSegment StartX=-4.75 StartY=15 StartZ=0 EndX=-4.75 EndY=11 EndZ=0
    g1: LineSegment StartX=-4.75 StartY=11 StartZ=0 EndX=4.75 EndY=11 EndZ=0
    g2: LineSegment StartX=4.75 StartY=11 StartZ=0 EndX=4.75 EndY=15 EndZ=0
    g3: LineSegment StartX=4.75 StartY=15 StartZ=0 EndX=-4.75 EndY=15 EndZ=0
    g4: GeomPoint X=0 Y=13 Z=0
  constraints (13):
    c: Coincident(g0,g1)
    c: Coincident(g1,g2)
    c: Coincident(g2,g3)
    c: Coincident(g3,g0)
    c: Horizontal(g1)
    c: Horizontal(g3)
    c: Vertical(g0)
    c: Vertical(g2)
    c: Symmetric(g1,g0,g4)
    c: DistanceX(g1,g1) = 9.5
    c: DistanceY(g2,g2) = 4
    c: PointOnObject(g1,g-3)
    c: PointOnObject(g4,g-2)
FEATURE [PartDesign::Pocket] Pocket123
  BaseFeature = -> Pocket122
  Length = 5
  Length2 = 5
  Midplane = true
  Placement = pos=(0,0,0) rot=(1,0,0;1.5708rad)
  Profile = -> Sketch324
  Type = 1
FEATURE [Sketcher::SketchObject] Sketch325  label="ISO 2904"
  FullyConstrained = true
  MapMode = 5
  Placement = pos=(0,0,0) rot=(1,0,0;1.5708rad)
  Support = -> [XZ_Plane326]
  sketch-geometry (8):
    g0: LineSegment StartX=6.04904 StartY=0.75 StartZ=0 EndX=3.25 EndY=0 EndZ=0
    g1: LineSegment StartX=3.25 StartY=0 StartZ=0 EndX=6.04904 EndY=-0.75 EndZ=0
    g2: LineSegment StartX=6.04904 StartY=-0.75 StartZ=0 EndX=3.25 EndY=-1.5 EndZ=0
    g3: LineSegment StartX=3.25 StartY=-1.5 StartZ=0 EndX=6.04904 EndY=-2.25 EndZ=0
    g4: LineSegment StartX=3.25 StartY=0 StartZ=0 EndX=3.25 EndY=-1.5 EndZ=0
    g5: LineSegment StartX=3.25 StartY=-1.5 StartZ=0 EndX=4.15 EndY=-1.25885 EndZ=0
    g6: LineSegment StartX=4.15 StartY=-1.25885 StartZ=0 EndX=4.15 EndY=-0.241154 EndZ=0
    g7: LineSegment StartX=4.15 StartY=-0.241154 StartZ=0 EndX=3.25 EndY=0 EndZ=0
  constraints (23):
    c: PointOnObject(g0,g-1)
    c: Coincident(g0,g1)
    c: Coincident(g1,g2)
    c: Coincident(g2,g3)
    c: Vertical(g1,g0)
    c: Vertical(g0,g3)
    c: Vertical(g2,g0)
    c: Parallel(g0,g2)
    c: Parallel(g1,g3)
    c: Angle(g3,g2) = 0.523599
    c: Angle(g0,g-1) = 2.87979
    c: Coincident(g0,g4)
    c: Coincident(g4,g2)
    c: Coincident(g4,g5)
    c: PointOnObject(g5,g2)
    c: Coincident(g5,g6)
    c: PointOnObject(g6,g1)
    c: Vertical(g6)
    c: Coincident(g6,g7)
    c: Coincident(g7,g4)
    c: DistanceX(g4) = 3.25
    c: DistanceX(g6) = 4.15
    c: DistanceY(g3,g1) = 1.5
FEATURE [Sketcher::SketchObject] Sketch327
  FullyConstrained = true
  MapMode = 5
  Placement = pos=(0,0,0) rot=(1,0,0;1.5708rad)
  Support = -> [XZ_Plane327]
  sketch-geometry (8):
    g0: LineSegment StartX=6.04904 StartY=0.75 StartZ=0 EndX=3.25 EndY=-1e-16 EndZ=0
    g1: LineSegment StartX=3.25 StartY=-1e-16 StartZ=0 EndX=6.04904 EndY=-0.75 EndZ=0
    g2: LineSegment StartX=6.04904 StartY=-0.75 StartZ=0 EndX=3.25 EndY=-1.5 EndZ=0
    g3: LineSegment StartX=3.25 StartY=-1.5 StartZ=0 EndX=6.04904 EndY=-2.25 EndZ=0
    g4: LineSegment StartX=3.25 StartY=-1e-16 StartZ=0 EndX=3.25 EndY=-1.5 EndZ=0
    g5: LineSegment StartX=3.25 StartY=-1.5 StartZ=0 EndX=4.15 EndY=-1.25885 EndZ=0
    g6: LineSegment StartX=4.15 StartY=-1.25885 StartZ=0 EndX=4.15 EndY=-0.241154 EndZ=0
    g7: LineSegment StartX=4.15 StartY=-0.241154 StartZ=0 EndX=3.25 EndY=-1e-16 EndZ=0
  constraints (23):
    c: PointOnObject(g0,g-1)
    c: Coincident(g0,g1)
    c: Coincident(g1,g2)
    c: Coincident(g2,g3)
    c: Vertical(g3,g1)
    c: Vertical(g1,g0)
    c: Vertical(g0,g2)
    c: Parallel(g3,g1)
    c: Parallel(g2,g0)
    c: Angle(g3,g2) = 0.523599
    c: Angle(g0,g-1) = 2.87979
    c: Coincident(g0,g4)
    c: Coincident(g4,g2)
    c: Coincident(g4,g5)
    c: PointOnObject(g5,g2)
    c: Coincident(g5,g6)
    c: PointOnObject(g6,g1)
    c: Coincident(g6,g7)
    c: Coincident(g7,g4)
    c: Vertical(g6)
    c: DistanceX(g4) = 3.25
    c: DistanceX(g6) = 4.15
    c: DistanceY(g3,g1) = 1.5
FEATURE [Sketcher::SketchObject] Sketch331
  FullyConstrained = false
  MapMode = 5
  Support = -> [XY_Plane329]
  sketch-geometry (7):
    g0: LineSegment StartX=1.45322 StartY=-2.69828 StartZ=0 EndX=3.06339 EndY=-0.0906102 EndZ=0
    g1: LineSegment StartX=3.06339 StartY=-0.0906102 StartZ=0 EndX=1.61017 EndY=2.60767 EndZ=0
    g2: LineSegment StartX=1.61017 StartY=2.60767 StartZ=0 EndX=-1.45322 EndY=2.69828 EndZ=0
    g3: LineSegment StartX=-1.45322 StartY=2.69828 StartZ=0 EndX=-3.06339 EndY=0.0906102 EndZ=0
    g4: LineSegment StartX=-3.06339 StartY=0.0906102 StartZ=0 EndX=-1.61017 EndY=-2.60767 EndZ=0
    g5: LineSegment StartX=-1.61017 StartY=-2.60767 StartZ=0 EndX=1.45322 EndY=-2.69828 EndZ=0
    g6: Circle CenterX=0 CenterY=0 CenterZ=0 NormalX=0 NormalY=0 NormalZ=1 AngleXU=0 Radius=3.06473
  constraints (14):
    c: Coincident(g0,g1)
    c: Coincident(g1,g2)
    c: Coincident(g2,g3)
    c: Coincident(g3,g4)
    c: Coincident(g4,g5)
    c: Coincident(g5,g0)
    c: Equal(g0, g1-g5) x5
    c: PointOnObject(g0,g6)
    c: PointOnObject(g1,g6)
    c: PointOnObject(g2,g6)
    c: PointOnObject(g3,g6)
    c: PointOnObject(g4,g6)
    c: PointOnObject(g5,g6)
    c: Coincident(g6,g-1)
FEATURE [PartDesign::Pad] Pad154
  Direction = (0,0,1)
  Length = 4
  Length2 = 10
  Profile = -> Sketch331
  Refine = true
  Type = 0
FEATURE [Sketcher::SketchObject] Sketch332
  FullyConstrained = false
  MapMode = 5
  Support = -> [XY_Plane330]
  sketch-geometry (7):
    g0: LineSegment StartX=1.45322 StartY=-2.69828 StartZ=0 EndX=3.06339 EndY=-0.0906102 EndZ=0
    g1: LineSegment StartX=3.06339 StartY=-0.0906102 StartZ=0 EndX=1.61017 EndY=2.60767 EndZ=0
    g2: LineSegment StartX=1.61017 StartY=2.60767 StartZ=0 EndX=-1.45322 EndY=2.69828 EndZ=0
    g3: LineSegment StartX=-1.45322 StartY=2.69828 StartZ=0 EndX=-3.06339 EndY=0.0906102 EndZ=0
    g4: LineSegment StartX=-3.06339 StartY=0.0906102 StartZ=0 EndX=-1.61017 EndY=-2.60767 EndZ=0
    g5: LineSegment StartX=-1.61017 StartY=-2.60767 StartZ=0 EndX=1.45322 EndY=-2.69828 EndZ=0
    g6: Circle CenterX=0 CenterY=0 CenterZ=0 NormalX=0 NormalY=0 NormalZ=1 AngleXU=0 Radius=3.06473
  constraints (14):
    c: Coincident(g0,g1)
    c: Coincident(g1,g2)
    c: Coincident(g2,g3)
    c: Coincident(g3,g4)
    c: Coincident(g4,g5)
    c: Coincident(g5,g0)
    c: Equal(g0, g1-g5) x5
    c: PointOnObject(g0,g6)
    c: PointOnObject(g1,g6)
    c: PointOnObject(g2,g6)
    c: PointOnObject(g3,g6)
    c: PointOnObject(g4,g6)
    c: PointOnObject(g5,g6)
    c: Coincident(g6,g-1)
FEATURE [PartDesign::Pad] Pad155
  Direction = (0,0,1)
  Length = 4
  Length2 = 10
  Profile = -> Sketch332
  Refine = true
  Type = 0
FEATURE [PartDesign::Body] Body236
  Group = -> [Sketch332,Pad155]
  Origin = -> Origin336
  Placement = pos=(0,-8,-6.97) rot=(0,0,1;0rad)
  Tip = -> Pad155
FEATURE [Sketcher::SketchObject] Sketch333
  FullyConstrained = false
  MapMode = 5
  Support = -> [XY_Plane331]
  sketch-geometry (7):
    g0: LineSegment StartX=1.45322 StartY=-2.69828 StartZ=0 EndX=3.06339 EndY=-0.0906102 EndZ=0
    g1: LineSegment StartX=3.06339 StartY=-0.0906102 StartZ=0 EndX=1.61017 EndY=2.60767 EndZ=0
    g2: LineSegment StartX=1.61017 StartY=2.60767 StartZ=0 EndX=-1.45322 EndY=2.69828 EndZ=0
    g3: LineSegment StartX=-1.45322 StartY=2.69828 StartZ=0 EndX=-3.06339 EndY=0.0906102 EndZ=0
    g4: LineSegment StartX=-3.06339 StartY=0.0906102 StartZ=0 EndX=-1.61017 EndY=-2.60767 EndZ=0
    g5: LineSegment StartX=-1.61017 StartY=-2.60767 StartZ=0 EndX=1.45322 EndY=-2.69828 EndZ=0
    g6: Circle CenterX=0 CenterY=0 CenterZ=0 NormalX=0 NormalY=0 NormalZ=1 AngleXU=0 Radius=3.06473
  constraints (14):
    c: Coincident(g0,g1)
    c: Coincident(g1,g2)
    c: Coincident(g2,g3)
    c: Coincident(g3,g4)
    c: Coincident(g4,g5)
    c: Coincident(g5,g0)
    c: Equal(g0, g1-g5) x5
    c: PointOnObject(g0,g6)
    c: PointOnObject(g1,g6)
    c: PointOnObject(g2,g6)
    c: PointOnObject(g3,g6)
    c: PointOnObject(g4,g6)
    c: PointOnObject(g5,g6)
    c: Coincident(g6,g-1)
FEATURE [PartDesign::Pad] Pad156
  Direction = (0,0,1)
  Length = 4
  Length2 = 10
  Profile = -> Sketch333
  Refine = true
  Type = 0
FEATURE [PartDesign::Body] Body237
  Group = -> [Sketch333,Pad156]
  Origin = -> Origin337
  Placement = pos=(-0.04,8,-6.97) rot=(0,0,1;0rad)
  Tip = -> Pad156
FEATURE [Sketcher::SketchObject] Sketch334
  FullyConstrained = false
  MapMode = 5
  Support = -> [XY_Plane332]
  sketch-geometry (7):
    g0: LineSegment StartX=1.45322 StartY=-2.69828 StartZ=0 EndX=3.06339 EndY=-0.0906102 EndZ=0
    g1: LineSegment StartX=3.06339 StartY=-0.0906102 StartZ=0 EndX=1.61017 EndY=2.60767 EndZ=0
    g2: LineSegment StartX=1.61017 StartY=2.60767 StartZ=0 EndX=-1.45322 EndY=2.69828 EndZ=0
    g3: LineSegment StartX=-1.45322 StartY=2.69828 StartZ=0 EndX=-3.06339 EndY=0.0906102 EndZ=0
    g4: LineSegment StartX=-3.06339 StartY=0.0906102 StartZ=0 EndX=-1.61017 EndY=-2.60767 EndZ=0
    g5: LineSegment StartX=-1.61017 StartY=-2.60767 StartZ=0 EndX=1.45322 EndY=-2.69828 EndZ=0
    g6: Circle CenterX=0 CenterY=0 CenterZ=0 NormalX=0 NormalY=0 NormalZ=1 AngleXU=0 Radius=3.06473
  constraints (14):
    c: Coincident(g0,g1)
    c: Coincident(g1,g2)
    c: Coincident(g2,g3)
    c: Coincident(g3,g4)
    c: Coincident(g4,g5)
    c: Coincident(g5,g0)
    c: Equal(g0, g1-g5) x5
    c: PointOnObject(g0,g6)
    c: PointOnObject(g1,g6)
    c: PointOnObject(g2,g6)
    c: PointOnObject(g3,g6)
    c: PointOnObject(g4,g6)
    c: PointOnObject(g5,g6)
    c: Coincident(g6,g-1)
FEATURE [PartDesign::Pad] Pad157
  Direction = (0,0,1)
  Length = 4
  Length2 = 10
  Profile = -> Sketch334
  Refine = true
  Type = 0
FEATURE [PartDesign::Body] Body238
  Group = -> [Sketch334,Pad157]
  Origin = -> Origin338
  Placement = pos=(-8,-0.06,-6.97) rot=(0,0,1;0rad)
  Tip = -> Pad157
FEATURE [PartDesign::SubtractiveHelix] SubtractiveHelix
  Angle = 0
  Axis = (0,2e-16,1)
  Base = (0,0,0)
  BaseFeature = -> Pocket121
  HasBeenEdited = true
  Height = 20
  LeftHanded = false
  Mode = 0
  Outside = false
  Pitch = 8
  Placement = pos=(0,0,0) rot=(1,0,0;1.5708rad)
  Profile = -> Sketch325
  ReferenceAxis = -> Sketch325 [V_Axis]
  Turns = 3
FEATURE [PartDesign::PolarPattern] PolarPattern027
  Angle = 360
  Axis = -> Sketch325 [V_Axis]
  BaseFeature = -> SubtractiveHelix
  Occurrences = 3
  Originals = -> [SubtractiveHelix]
  Placement = pos=(0,0,0) rot=(1,0,0;1.5708rad)
FEATURE [Sketcher::SketchObject] Sketch326
  ExternalGeometry = -> [PolarPattern027]
  FullyConstrained = true
  MapMode = 5
  Placement = pos=(0,0,0) rot=(1,0,0;1.5708rad)
  Support = -> [XZ_Plane326]
  sketch-geometry (6):
    g0: LineSegment StartX=-4.25 StartY=0 StartZ=0 EndX=-3.25 EndY=0 EndZ=0
    g1: LineSegment StartX=-3.25 StartY=0 StartZ=0 EndX=-3.25 EndY=1 EndZ=0
    g2: LineSegment StartX=-3.25 StartY=1 StartZ=0 EndX=-4.25 EndY=0 EndZ=0
    g3: LineSegment StartX=-4.25 StartY=15 StartZ=0 EndX=-3.25 EndY=14 EndZ=0
    g4: LineSegment StartX=-3.25 StartY=14 StartZ=0 EndX=-3.25 EndY=15 EndZ=0
    g5: LineSegment StartX=-3.25 StartY=15 StartZ=0 EndX=-4.25 EndY=15 EndZ=0
  constraints (18):
    c: PointOnObject(g0,g-1)
    c: PointOnObject(g0,g-1)
    c: Coincident(g0,g1)
    c: Vertical(g1)
    c: Coincident(g1,g2)
    c: Coincident(g2,g0)
    c: PointOnObject(g3,g-3)
    c: Coincident(g3,g4)
    c: Vertical(g4)
    c: Coincident(g4,g5)
    c: Horizontal(g5)
    c: Coincident(g5,g3)
    c: Equal(g4,g5)
    c: Equal(g5,g1)
    c: Equal(g1,g0)
    c: DistanceX(g0,g0) = 1
    c: DistanceX(g0) = -3.25
    c: Vertical(g1,g3)
FEATURE [PartDesign::Groove] Groove006
  Angle = 360
  Axis = (0,2e-16,1)
  Base = (0,0,0)
  BaseFeature = -> PolarPattern027
  Placement = pos=(0,0,0) rot=(1,0,0;1.5708rad)
  Profile = -> Sketch326
  ReferenceAxis = -> Sketch326 [V_Axis]
  Reversed = true
FEATURE [Sketcher::SketchObject] Sketch329
  ExternalGeometry = -> [Groove006]
  FullyConstrained = false
  MapMode = 5
  Support = -> [XY_Plane326]
  sketch-geometry (22):
    g0: ArcOfCircle CenterX=0 CenterY=1.8e-15 CenterZ=0 NormalX=0 NormalY=0 NormalZ=1 AngleXU=0 Radius=12 StartAngle=6.12177 EndAngle=8.69593
    g1: Circle CenterX=0 CenterY=8 CenterZ=0 NormalX=0 NormalY=0 NormalZ=1 AngleXU=0 Radius=1.95
    g2: Circle CenterX=8 CenterY=4.4e-15 CenterZ=0 NormalX=0 NormalY=0 NormalZ=1 AngleXU=0 Radius=1.95
    g3: Circle CenterX=-8 CenterY=0 CenterZ=0 NormalX=0 NormalY=0 NormalZ=1 AngleXU=0 Radius=1.95
    g4: Circle CenterX=0 CenterY=-8 CenterZ=0 NormalX=0 NormalY=0 NormalZ=1 AngleXU=0 Radius=1.95
    g5: GeomPoint X=0 Y=1.8e-15 Z=0
    g6: GeomPoint X=0 Y=-25 Z=0
    g7: ArcOfCircle CenterX=0 CenterY=-25 CenterZ=0 NormalX=0 NormalY=0 NormalZ=1 AngleXU=0 Radius=7.5 StartAngle=3.3289 EndAngle=5.4508
    g8: Circle CenterX=0 CenterY=-25 CenterZ=0 NormalX=0 NormalY=0 NormalZ=1 AngleXU=0 Radius=4
    g9: LineSegment StartX=11.844 StartY=-1.92855 StartZ=0 EndX=8.25015 EndY=-24 EndZ=0
    g10: LineSegment StartX=-10.8555 StartY=-8.00001 StartZ=0 EndX=-7.36882 EndY=-26.3966 EndZ=0
    g11: LineSegment StartX=-25 StartY=7.99214 StartZ=0 EndX=-8.9513 EndY=7.99214 EndZ=0
    g12: LineSegment StartX=-25 StartY=-8 StartZ=0 EndX=-25 EndY=7.99214 EndZ=0
    g13: GeomPoint X=0 Y=12 Z=0
    g14: GeomPoint X=0 Y=-11 Z=0
    g15: LineSegment StartX=20 StartY=-30.5465 StartZ=0 EndX=5.04838 EndY=-30.5465 EndZ=0
    g16: LineSegment StartX=8.25015 StartY=-24 StartZ=0 EndX=20 EndY=-24 EndZ=0
    g17: LineSegment StartX=20 StartY=-24 StartZ=0 EndX=20 EndY=-30.5465 EndZ=0
    g18: GeomPoint X=1.59796e-10 Y=-29 Z=0
    g19: GeomPoint X=0 Y=-21 Z=0
    g20: LineSegment StartX=-10.8555 StartY=-8.00001 StartZ=0 EndX=-25 EndY=-8 EndZ=0
    g21: Circle CenterX=0 CenterY=1.8e-15 CenterZ=0 NormalX=0 NormalY=0 NormalZ=1 AngleXU=0 Radius=3.24154
  constraints (42):
    c: Coincident(g0,g-3)
    c: Coincident(g1,g-4)
    c: Coincident(g2,g-6)
    c: Coincident(g3,g-7)
    c: Coincident(g4,g-5)
    c: Equal(g1,g2)
    c: Equal(g2,g4)
    c: Equal(g4,g3)
    c: Diameter(g2) = 3.9
    c: Coincident(g5,g0)
    c: PointOnObject(g6,g-2)
    c: DistanceY(g6,g0) = 25
    c: Coincident(g7,g6)
    c: Coincident(g8,g7)
    c: Diameter(g8) = 8
    c: Diameter(g7) = 15
    c: Diameter(g-3) = 22
    c: Diameter(g0) = 24
    c: Tangent(g0,g9) = 1.5708
    c: Tangent(g7,g10) = -1.5708
    c: Coincident(g20,g12)
    c: Coincident(g12,g11)
    c: Horizontal(g11)
    c: Vertical(g12)
    c: PointOnObject(g13,g0)
    c: DistanceX(g13,g-1) = 0
    c: PointOnObject(g14,g-3)
    c: DistanceX(g11,g1) = 25
    c: Coincident(g16,g17)
    c: Coincident(g17,g15)
    c: Horizontal(g15)
    c: Horizontal(g16)
    c: Vertical(g17)
    c: PointOnObject(g18,g8)
    c: PointOnObject(g19,g8)
    c: DistanceX(g19,g-1) = 0
    c: DistanceX(g18,g15) = 20
    c: Coincident(g10,g20)
    c: Coincident(g0,g11)
    c: Coincident(g16,g9)
    c: Coincident(g15,g7)
    c: Coincident(g21,g0)
FEATURE [PartDesign::Pad] Pad151
  BaseFeature = -> Groove006
  Direction = (0,0,1)
  Length = 3
  Length2 = 10
  Placement = pos=(0,0,0) rot=(1,0,0;1.5708rad)
  Profile = -> Sketch329
  Refine = true
  Reversed = true
  Type = 0
  UseCustomVector = true
FEATURE [PartDesign::Fillet] Fillet178
  Base = -> Pad151 [Edge115]
  BaseFeature = -> Pad151
  Placement = pos=(0,0,0) rot=(1,0,0;1.5708rad)
  Radius = 1
  Refine = true
  SupportTransform = false
FEATURE [PartDesign::Fillet] Fillet179
  Base = -> Fillet178 [Edge19,Edge15]
  BaseFeature = -> Fillet178
  Placement = pos=(0,0,0) rot=(1,0,0;1.5708rad)
  Radius = 2
  Refine = true
  SupportTransform = false
FEATURE [PartDesign::Fillet] Fillet180
  Base = -> Fillet179 [Edge39]
  BaseFeature = -> Fillet179
  Placement = pos=(0,0,0) rot=(1,0,0;1.5708rad)
  Radius = 1
  Refine = true
  SupportTransform = false
FEATURE [PartDesign::Fillet] Fillet181
  Base = -> Fillet180 [Edge28,Edge24]
  BaseFeature = -> Fillet180
  Placement = pos=(0,0,0) rot=(1,0,0;1.5708rad)
  Radius = 2
  Refine = true
  SupportTransform = false
FEATURE [PartDesign::Fillet] Fillet182
  Base = -> Fillet181 [Edge34]
  BaseFeature = -> Fillet181
  Placement = pos=(0,0,0) rot=(1,0,0;1.5708rad)
  Radius = 1
  Refine = true
  SupportTransform = false
FEATURE [PartDesign::Pad] Pad152
  BaseFeature = -> Fillet182
  Direction = (0,0,1)
  Length = 15
  Length2 = 10
  Midplane = true
  Placement = pos=(0,0,0) rot=(1,0,0;1.5708rad)
  Refine = true
  Type = 0
FEATURE [Sketcher::SketchObject] Sketch330
  ExternalGeometry = -> [Pad152]
  FullyConstrained = true
  MapMode = 5
  Support = -> [XY_Plane326]
  sketch-geometry (4):
    g0: Circle CenterX=0 CenterY=8 CenterZ=0 NormalX=0 NormalY=0 NormalZ=1 AngleXU=0 Radius=2.25
    g1: Circle CenterX=8 CenterY=0 CenterZ=0 NormalX=0 NormalY=0 NormalZ=1 AngleXU=0 Radius=2.25
    g2: Circle CenterX=-8 CenterY=4.6e-15 CenterZ=0 NormalX=0 NormalY=0 NormalZ=1 AngleXU=0 Radius=2.25
    g3: Circle CenterX=0 CenterY=-8 CenterZ=0 NormalX=0 NormalY=0 NormalZ=1 AngleXU=0 Radius=2.25
  constraints (8):
    c: Coincident(g0,g-3)
    c: Coincident(g1,g-4)
    c: Coincident(g2,g-5)
    c: Coincident(g3,g-6)
    c: Diameter(g0) = 4.5
    c: Equal(g1,g2)
    c: Equal(g1,g3)
    c: Diameter(g1) = 4.5
FEATURE [PartDesign::Pad] Pad153
  BaseFeature = -> Pad152
  Direction = (0,0,1)
  Length = 8
  Length2 = 10
  Offset = 5
  Placement = pos=(0,0,0) rot=(1,0,0;1.5708rad)
  Profile = -> Sketch330
  Refine = true
  Type = 0
FEATURE [PartDesign::Body] Body232  label="Bottom"
  Group = -> [Sketch318,Revolution053,Sketch319,Pocket119,Chamfer020,PolarPattern026,Sketch320,Pocket120,Sketch321,Pocket121,Sketch325,SubtractiveHelix,PolarPattern027,Sketch326,Groove006,Sketch329,Pad151,Fillet178,Fillet179,Fillet180,Fillet181,Fillet182,Pad152,Sketch330,Pad153]
  Origin = -> Origin332
  Tip = -> Pad153
FEATURE [PartDesign::ShapeBinder] ReferencePad002
  Support = -> [Pad153]
  TraceSupport = false
FEATURE [PartDesign::Body] Body235
  Group = -> [Sketch331,Pad154,ReferencePad002]
  Origin = -> Origin335
  Placement = pos=(7.96,-0.06,-6.97) rot=(0,0,1;0rad)
  Tip = -> Pad154
FEATURE [PartDesign::SubtractiveHelix] SubtractiveHelix001
  Angle = 0
  Axis = (0,2e-16,1)
  Base = (0,0,0)
  BaseFeature = -> Pocket123
  HasBeenEdited = true
  Height = 30
  LeftHanded = false
  Mode = 0
  Outside = false
  Pitch = 8
  Placement = pos=(0,0,0) rot=(1,0,0;1.5708rad)
  Profile = -> Sketch327
  ReferenceAxis = -> Sketch327 [V_Axis]
  Turns = 3
FEATURE [PartDesign::PolarPattern] PolarPattern028
  Angle = 360
  Axis = -> Sketch327 [V_Axis]
  BaseFeature = -> SubtractiveHelix001
  Occurrences = 3
  Originals = -> [SubtractiveHelix001]
  Placement = pos=(0,0,0) rot=(1,0,0;1.5708rad)
FEATURE [Sketcher::SketchObject] Sketch328
  ExternalGeometry = -> [PolarPattern028]
  FullyConstrained = true
  MapMode = 5
  Placement = pos=(0,0,0) rot=(1,0,0;1.5708rad)
  Support = -> [XZ_Plane327]
  sketch-geometry (6):
    g0: LineSegment StartX=-4.25 StartY=26 StartZ=0 EndX=-3.25 EndY=26 EndZ=0
    g1: LineSegment StartX=-3.25 StartY=26 StartZ=0 EndX=-3.25 EndY=25 EndZ=0
    g2: LineSegment StartX=-3.25 StartY=25 StartZ=0 EndX=-4.25 EndY=26 EndZ=0
    g3: LineSegment StartX=-4.25 StartY=15 StartZ=0 EndX=-3.25 EndY=15 EndZ=0
    g4: LineSegment StartX=-3.25 StartY=15 StartZ=0 EndX=-3.25 EndY=16 EndZ=0
    g5: LineSegment StartX=-3.25 StartY=16 StartZ=0 EndX=-4.25 EndY=15 EndZ=0
  constraints (18):
    c: PointOnObject(g0,g-3)
    c: PointOnObject(g0,g-3)
    c: Coincident(g0,g1)
    c: Coincident(g1,g2)
    c: Coincident(g2,g0)
    c: PointOnObject(g3,g-4)
    c: PointOnObject(g3,g-4)
    c: Coincident(g3,g4)
    c: Vertical(g4)
    c: Coincident(g4,g5)
    c: Coincident(g5,g3)
    c: Vertical(g4,g1)
    c: Vertical(g1)
    c: Equal(g0,g1)
    c: Equal(g1,g3)
    c: Equal(g3,g4)
    c: DistanceX(g3,g3) = 1
    c: DistanceX(g3) = -3.25
FEATURE [PartDesign::Groove] Groove007
  Angle = 360
  Axis = (0,2e-16,1)
  Base = (0,0,0)
  BaseFeature = -> PolarPattern028
  Placement = pos=(0,0,0) rot=(1,0,0;1.5708rad)
  Profile = -> Sketch328
  ReferenceAxis = -> Sketch328 [V_Axis]
  Reversed = true
FEATURE [PartDesign::Body] Body233  label="Top"
  Group = -> [Sketch322,Revolution054,Sketch323,Pocket122,Sketch324,Pocket123,Sketch327,SubtractiveHelix001,PolarPattern028,Sketch328,Groove007]
  Origin = -> Origin333
  Tip = -> Groove007
FEATURE [App::Part] Part099  label="T8 antibacklash nut"
  Group = -> [Body232,Body233,Body234]
  Origin = -> Origin331
FEATURE [App::LinkGroup] LinkGroup017
  ElementList = -> [Body235,Body236,Body237,Body238]
  LinkMode = 0
FEATURE [App::LinkGroup] LinkGroup018  label="SoporteSensor"
  ElementList = -> [LinkGroup017,Part099]
  LinkMode = 0
  Placement = pos=(0,0,0) rot=(0.57735,-0.57735,-0.57735;2.0944rad)
FEATURE [Part::Cylinder] Cylinder  label="sensor"
  Angle = 360
  AttacherType = Attacher::AttachEngine3D
  Height = 22
  Placement = pos=(0,0,0) rot=(-1,0,0;1.5708rad)
  Radius = 8
FEATURE [App::LinkGroup] LinkGroup019  label="sensorSoporte"
  ElementList = -> [Cylinder,LinkGroup018]
  LinkMode = 0
FEATURE [Sketcher::SketchObject] Sketch335
  FullyConstrained = false
  MapMode = 5
  Placement = pos=(0,0,0) rot=(0.57735,0.57735,0.57735;2.0944rad)
  Support = -> [YZ_Plane334]
  sketch-geometry (8):
    g0: LineSegment StartX=2.8963 StartY=-2.75889 StartZ=0 EndX=3.83742 EndY=1.12882 EndZ=0
    g1: LineSegment StartX=3.83742 StartY=1.12882 StartZ=0 EndX=0.941117 EndY=3.88771 EndZ=0
    g2: LineSegment StartX=0.941117 StartY=3.88771 StartZ=0 EndX=-2.8963 EndY=2.75889 EndZ=0
    g3: LineSegment StartX=-2.8963 StartY=2.75889 StartZ=0 EndX=-3.83742 EndY=-1.12882 EndZ=0
    g4: LineSegment StartX=-3.83742 StartY=-1.12882 StartZ=0 EndX=-0.941117 EndY=-3.88771 EndZ=0
    g5: LineSegment StartX=-0.941117 StartY=-3.88771 StartZ=0 EndX=2.8963 EndY=-2.75889 EndZ=0
    g6: Circle CenterX=0 CenterY=0 CenterZ=0 NormalX=0 NormalY=0 NormalZ=1 AngleXU=0 Radius=4
    g7: Circle CenterX=0 CenterY=0 CenterZ=0 NormalX=0 NormalY=0 NormalZ=1 AngleXU=0 Radius=2.5
  constraints (17):
    c: Coincident(g0,g1)
    c: Coincident(g1,g2)
    c: Coincident(g2,g3)
    c: Coincident(g3,g4)
    c: Coincident(g4,g5)
    c: Coincident(g5,g0)
    c: Equal(g0, g1-g5) x5
    c: PointOnObject(g0,g6)
    c: PointOnObject(g1,g6)
    c: PointOnObject(g2,g6)
    c: PointOnObject(g3,g6)
    c: PointOnObject(g4,g6)
    c: PointOnObject(g5,g6)
    c: Coincident(g6,g-1)
    c: Coincident(g7,g6)
    c: Radius(g7) = 2.5
    c: Radius(g6) = 4
FEATURE [PartDesign::Pad] Pad158
  Direction = (1,-2e-16,3e-16)
  Length = 3
  Length2 = 10
  Placement = pos=(0,0,0) rot=(0.57735,0.57735,0.57735;2.0944rad)
  Profile = -> Sketch335
  Type = 0
FEATURE [PartDesign::Pad] Pad159
  BaseFeature = -> Pad158
  Direction = (1,-2e-16,6e-16)
  Length = 15
  Length2 = 10
  Placement = pos=(0,0,0) rot=(0.57735,0.57735,0.57735;2.0944rad)
  Profile = -> Pad158 [Edge20]
  Type = 0
FEATURE [PartDesign::Body] Body239
  Group = -> [Sketch335,Pad158,Pad159]
  Origin = -> Origin340
  Tip = -> Pad159
FEATURE [App::Part] Part100  label="tornillo M5-15-013"
  Group = -> [Body239]
  Origin = -> Origin339
  Placement = pos=(31,10,26) rot=(0,1,0;1.5708rad)
FEATURE [Sketcher::SketchObject] Sketch336
  FullyConstrained = false
  MapMode = 5
  Placement = pos=(0,0,0) rot=(0.57735,0.57735,0.57735;2.0944rad)
  Support = -> [YZ_Plane336]
  sketch-geometry (8):
    g0: LineSegment StartX=2.8963 StartY=-2.75889 StartZ=0 EndX=3.83742 EndY=1.12882 EndZ=0
    g1: LineSegment StartX=3.83742 StartY=1.12882 StartZ=0 EndX=0.941117 EndY=3.88771 EndZ=0
    g2: LineSegment StartX=0.941117 StartY=3.88771 StartZ=0 EndX=-2.8963 EndY=2.75889 EndZ=0
    g3: LineSegment StartX=-2.8963 StartY=2.75889 StartZ=0 EndX=-3.83742 EndY=-1.12882 EndZ=0
    g4: LineSegment StartX=-3.83742 StartY=-1.12882 StartZ=0 EndX=-0.941117 EndY=-3.88771 EndZ=0
    g5: LineSegment StartX=-0.941117 StartY=-3.88771 StartZ=0 EndX=2.8963 EndY=-2.75889 EndZ=0
    g6: Circle CenterX=0 CenterY=0 CenterZ=0 NormalX=0 NormalY=0 NormalZ=1 AngleXU=0 Radius=4
    g7: Circle CenterX=0 CenterY=0 CenterZ=0 NormalX=0 NormalY=0 NormalZ=1 AngleXU=0 Radius=2.5
  constraints (17):
    c: Coincident(g0,g1)
    c: Coincident(g1,g2)
    c: Coincident(g2,g3)
    c: Coincident(g3,g4)
    c: Coincident(g4,g5)
    c: Coincident(g5,g0)
    c: Equal(g0, g1-g5) x5
    c: PointOnObject(g0,g6)
    c: PointOnObject(g1,g6)
    c: PointOnObject(g2,g6)
    c: PointOnObject(g3,g6)
    c: PointOnObject(g4,g6)
    c: PointOnObject(g5,g6)
    c: Coincident(g6,g-1)
    c: Coincident(g7,g6)
    c: Radius(g7) = 2.5
    c: Radius(g6) = 4
FEATURE [PartDesign::Pad] Pad160
  Direction = (1,-2e-16,3e-16)
  Length = 3
  Length2 = 10
  Placement = pos=(0,0,0) rot=(0.57735,0.57735,0.57735;2.0944rad)
  Profile = -> Sketch336
  Type = 0
FEATURE [PartDesign::Pad] Pad161
  BaseFeature = -> Pad160
  Direction = (1,-2e-16,6e-16)
  Length = 15
  Length2 = 10
  Placement = pos=(0,0,0) rot=(0.57735,0.57735,0.57735;2.0944rad)
  Profile = -> Pad160 [Edge20]
  Type = 0
FEATURE [PartDesign::Body] Body240
  Group = -> [Sketch336,Pad160,Pad161]
  Origin = -> Origin342
  Tip = -> Pad161
FEATURE [App::Part] Part101  label="tornillo M5-15-014"
  Group = -> [Body240]
  Origin = -> Origin341
  Placement = pos=(26,10,33) rot=(0,1,0;3.14159rad)
FEATURE [Sketcher::SketchObject] Sketch337
  FullyConstrained = false
  MapMode = 5
  Placement = pos=(0,0,0) rot=(0.57735,0.57735,0.57735;2.0944rad)
  Support = -> [YZ_Plane337]
  sketch-geometry (8):
    g0: LineSegment StartX=2.8963 StartY=-2.75889 StartZ=0 EndX=3.83742 EndY=1.12882 EndZ=0
    g1: LineSegment StartX=3.83742 StartY=1.12882 StartZ=0 EndX=0.941117 EndY=3.88771 EndZ=0
    g2: LineSegment StartX=0.941117 StartY=3.88771 StartZ=0 EndX=-2.8963 EndY=2.75889 EndZ=0
    g3: LineSegment StartX=-2.8963 StartY=2.75889 StartZ=0 EndX=-3.83742 EndY=-1.12882 EndZ=0
    g4: LineSegment StartX=-3.83742 StartY=-1.12882 StartZ=0 EndX=-0.941117 EndY=-3.88771 EndZ=0
    g5: LineSegment StartX=-0.941117 StartY=-3.88771 StartZ=0 EndX=2.8963 EndY=-2.75889 EndZ=0
    g6: Circle CenterX=0 CenterY=0 CenterZ=0 NormalX=0 NormalY=0 NormalZ=1 AngleXU=0 Radius=4
    g7: Circle CenterX=0 CenterY=0 CenterZ=0 NormalX=0 NormalY=0 NormalZ=1 AngleXU=0 Radius=2.5
  constraints (17):
    c: Coincident(g0,g1)
    c: Coincident(g1,g2)
    c: Coincident(g2,g3)
    c: Coincident(g3,g4)
    c: Coincident(g4,g5)
    c: Coincident(g5,g0)
    c: Equal(g0, g1-g5) x5
    c: PointOnObject(g0,g6)
    c: PointOnObject(g1,g6)
    c: PointOnObject(g2,g6)
    c: PointOnObject(g3,g6)
    c: PointOnObject(g4,g6)
    c: PointOnObject(g5,g6)
    c: Coincident(g6,g-1)
    c: Coincident(g7,g6)
    c: Radius(g7) = 2.5
    c: Radius(g6) = 4
FEATURE [PartDesign::Pad] Pad162
  Direction = (1,-2e-16,3e-16)
  Length = 3
  Length2 = 10
  Placement = pos=(0,0,0) rot=(0.57735,0.57735,0.57735;2.0944rad)
  Profile = -> Sketch337
  Type = 0
FEATURE [PartDesign::Pad] Pad163
  BaseFeature = -> Pad162
  Direction = (1,-2e-16,6e-16)
  Length = 15
  Length2 = 10
  Placement = pos=(0,0,0) rot=(0.57735,0.57735,0.57735;2.0944rad)
  Profile = -> Pad162 [Edge20]
  Type = 0
FEATURE [PartDesign::Body] Body241
  Group = -> [Sketch337,Pad162,Pad163]
  Origin = -> Origin344
  Tip = -> Pad163
FEATURE [App::Part] Part102  label="tornillo M5-15-015"
  Group = -> [Body241]
  Origin = -> Origin343
  Placement = pos=(26,10,159) rot=(0,1,0;3.14159rad)
FEATURE [Sketcher::SketchObject] Sketch338
  FullyConstrained = false
  MapMode = 5
  Placement = pos=(0,0,0) rot=(0.57735,0.57735,0.57735;2.0944rad)
  Support = -> [YZ_Plane339]
  sketch-geometry (8):
    g0: LineSegment StartX=2.8963 StartY=-2.75889 StartZ=0 EndX=3.83742 EndY=1.12882 EndZ=0
    g1: LineSegment StartX=3.83742 StartY=1.12882 StartZ=0 EndX=0.941117 EndY=3.88771 EndZ=0
    g2: LineSegment StartX=0.941117 StartY=3.88771 StartZ=0 EndX=-2.8963 EndY=2.75889 EndZ=0
    g3: LineSegment StartX=-2.8963 StartY=2.75889 StartZ=0 EndX=-3.83742 EndY=-1.12882 EndZ=0
    g4: LineSegment StartX=-3.83742 StartY=-1.12882 StartZ=0 EndX=-0.941117 EndY=-3.88771 EndZ=0
    g5: LineSegment StartX=-0.941117 StartY=-3.88771 StartZ=0 EndX=2.8963 EndY=-2.75889 EndZ=0
    g6: Circle CenterX=0 CenterY=0 CenterZ=0 NormalX=0 NormalY=0 NormalZ=1 AngleXU=0 Radius=4
    g7: Circle CenterX=0 CenterY=0 CenterZ=0 NormalX=0 NormalY=0 NormalZ=1 AngleXU=0 Radius=2.5
  constraints (17):
    c: Coincident(g0,g1)
    c: Coincident(g1,g2)
    c: Coincident(g2,g3)
    c: Coincident(g3,g4)
    c: Coincident(g4,g5)
    c: Coincident(g5,g0)
    c: Equal(g0, g1-g5) x5
    c: PointOnObject(g0,g6)
    c: PointOnObject(g1,g6)
    c: PointOnObject(g2,g6)
    c: PointOnObject(g3,g6)
    c: PointOnObject(g4,g6)
    c: PointOnObject(g5,g6)
    c: Coincident(g6,g-1)
    c: Coincident(g7,g6)
    c: Radius(g7) = 2.5
    c: Radius(g6) = 4
FEATURE [PartDesign::Pad] Pad164
  Direction = (1,-2e-16,3e-16)
  Length = 3
  Length2 = 10
  Placement = pos=(0,0,0) rot=(0.57735,0.57735,0.57735;2.0944rad)
  Profile = -> Sketch338
  Type = 0
FEATURE [PartDesign::Pad] Pad165
  BaseFeature = -> Pad164
  Direction = (1,-2e-16,6e-16)
  Length = 15
  Length2 = 10
  Placement = pos=(0,0,0) rot=(0.57735,0.57735,0.57735;2.0944rad)
  Profile = -> Pad164 [Edge20]
  Type = 0
FEATURE [PartDesign::Body] Body242
  Group = -> [Sketch338,Pad164,Pad165]
  Origin = -> Origin346
  Tip = -> Pad165
FEATURE [App::Part] Part103  label="tornillo M5-15-016"
  Group = -> [Body242]
  Origin = -> Origin345
  Placement = pos=(28.2334,9.96532,164.125) rot=(0.44435,-0.754393,0.483161;1.89214rad)
FEATURE [Sketcher::SketchObject] Sketch339
  FullyConstrained = false
  MapMode = 5
  Placement = pos=(0,0,0) rot=(0.57735,0.57735,0.57735;2.0944rad)
  Support = -> [YZ_Plane342]
  sketch-geometry (8):
    g0: LineSegment StartX=2.8963 StartY=-2.75889 StartZ=0 EndX=3.83742 EndY=1.12882 EndZ=0
    g1: LineSegment StartX=3.83742 StartY=1.12882 StartZ=0 EndX=0.941117 EndY=3.88771 EndZ=0
    g2: LineSegment StartX=0.941117 StartY=3.88771 StartZ=0 EndX=-2.8963 EndY=2.75889 EndZ=0
    g3: LineSegment StartX=-2.8963 StartY=2.75889 StartZ=0 EndX=-3.83742 EndY=-1.12882 EndZ=0
    g4: LineSegment StartX=-3.83742 StartY=-1.12882 StartZ=0 EndX=-0.941117 EndY=-3.88771 EndZ=0
    g5: LineSegment StartX=-0.941117 StartY=-3.88771 StartZ=0 EndX=2.8963 EndY=-2.75889 EndZ=0
    g6: Circle CenterX=0 CenterY=0 CenterZ=0 NormalX=0 NormalY=0 NormalZ=1 AngleXU=0 Radius=4
    g7: Circle CenterX=0 CenterY=0 CenterZ=0 NormalX=0 NormalY=0 NormalZ=1 AngleXU=0 Radius=2.5
  constraints (17):
    c: Coincident(g0,g1)
    c: Coincident(g1,g2)
    c: Coincident(g2,g3)
    c: Coincident(g3,g4)
    c: Coincident(g4,g5)
    c: Coincident(g5,g0)
    c: Equal(g0, g1-g5) x5
    c: PointOnObject(g0,g6)
    c: PointOnObject(g1,g6)
    c: PointOnObject(g2,g6)
    c: PointOnObject(g3,g6)
    c: PointOnObject(g4,g6)
    c: PointOnObject(g5,g6)
    c: Coincident(g6,g-1)
    c: Coincident(g7,g6)
    c: Radius(g7) = 2.5
    c: Radius(g6) = 4
FEATURE [PartDesign::Pad] Pad167
  Direction = (1,-2e-16,3e-16)
  Length = 3
  Length2 = 10
  Placement = pos=(0,0,0) rot=(0.57735,0.57735,0.57735;2.0944rad)
  Profile = -> Sketch339
  Type = 0
FEATURE [PartDesign::Pad] Pad168
  BaseFeature = -> Pad167
  Direction = (1,-2e-16,6e-16)
  Length = 15
  Length2 = 10
  Placement = pos=(0,0,0) rot=(0.57735,0.57735,0.57735;2.0944rad)
  Profile = -> Pad167 [Edge20]
  Type = 0
FEATURE [PartDesign::Body] Body243
  Group = -> [Sketch339,Pad167,Pad168]
  Origin = -> Origin350
  Tip = -> Pad168
FEATURE [App::Part] Part104  label="tornillo M5-15-017"
  Group = -> [Body243]
  Origin = -> Origin348
  Placement = pos=(31,10,26) rot=(0,1,0;1.5708rad)
FEATURE [Sketcher::SketchObject] Sketch340
  FullyConstrained = false
  MapMode = 5
  Placement = pos=(0,0,0) rot=(0.57735,0.57735,0.57735;2.0944rad)
  Support = -> [YZ_Plane343]
  sketch-geometry (8):
    g0: LineSegment StartX=2.8963 StartY=-2.75889 StartZ=0 EndX=3.83742 EndY=1.12882 EndZ=0
    g1: LineSegment StartX=3.83742 StartY=1.12882 StartZ=0 EndX=0.941117 EndY=3.88771 EndZ=0
    g2: LineSegment StartX=0.941117 StartY=3.88771 StartZ=0 EndX=-2.8963 EndY=2.75889 EndZ=0
    g3: LineSegment StartX=-2.8963 StartY=2.75889 StartZ=0 EndX=-3.83742 EndY=-1.12882 EndZ=0
    g4: LineSegment StartX=-3.83742 StartY=-1.12882 StartZ=0 EndX=-0.941117 EndY=-3.88771 EndZ=0
    g5: LineSegment StartX=-0.941117 StartY=-3.88771 StartZ=0 EndX=2.8963 EndY=-2.75889 EndZ=0
    g6: Circle CenterX=0 CenterY=0 CenterZ=0 NormalX=0 NormalY=0 NormalZ=1 AngleXU=0 Radius=4
    g7: Circle CenterX=0 CenterY=0 CenterZ=0 NormalX=0 NormalY=0 NormalZ=1 AngleXU=0 Radius=2.5
  constraints (17):
    c: Coincident(g0,g1)
    c: Coincident(g1,g2)
    c: Coincident(g2,g3)
    c: Coincident(g3,g4)
    c: Coincident(g4,g5)
    c: Coincident(g5,g0)
    c: Equal(g0, g1-g5) x5
    c: PointOnObject(g0,g6)
    c: PointOnObject(g1,g6)
    c: PointOnObject(g2,g6)
    c: PointOnObject(g3,g6)
    c: PointOnObject(g4,g6)
    c: PointOnObject(g5,g6)
    c: Coincident(g6,g-1)
    c: Coincident(g7,g6)
    c: Radius(g7) = 2.5
    c: Radius(g6) = 4
FEATURE [PartDesign::Pad] Pad166
  Direction = (1,-2e-16,3e-16)
  Length = 3
  Length2 = 10
  Placement = pos=(0,0,0) rot=(0.57735,0.57735,0.57735;2.0944rad)
  Profile = -> Sketch340
  Type = 0
FEATURE [PartDesign::Pad] Pad170
  BaseFeature = -> Pad166
  Direction = (1,-2e-16,6e-16)
  Length = 15
  Length2 = 10
  Placement = pos=(0,0,0) rot=(0.57735,0.57735,0.57735;2.0944rad)
  Profile = -> Pad166 [Edge20]
  Type = 0
FEATURE [PartDesign::Body] Body244
  Group = -> [Sketch340,Pad166,Pad170]
  Origin = -> Origin349
  Tip = -> Pad170
FEATURE [App::Part] Part105  label="tornillo M5-15-018"
  Group = -> [Body244]
  Origin = -> Origin347
  Placement = pos=(26,10,33) rot=(0,1,0;3.14159rad)
FEATURE [Sketcher::SketchObject] Sketch341
  FullyConstrained = false
  MapMode = 5
  Placement = pos=(0,0,0) rot=(0.57735,0.57735,0.57735;2.0944rad)
  Support = -> [YZ_Plane344]
  sketch-geometry (8):
    g0: LineSegment StartX=2.8963 StartY=-2.75889 StartZ=0 EndX=3.83742 EndY=1.12882 EndZ=0
    g1: LineSegment StartX=3.83742 StartY=1.12882 StartZ=0 EndX=0.941117 EndY=3.88771 EndZ=0
    g2: LineSegment StartX=0.941117 StartY=3.88771 StartZ=0 EndX=-2.8963 EndY=2.75889 EndZ=0
    g3: LineSegment StartX=-2.8963 StartY=2.75889 StartZ=0 EndX=-3.83742 EndY=-1.12882 EndZ=0
    g4: LineSegment StartX=-3.83742 StartY=-1.12882 StartZ=0 EndX=-0.941117 EndY=-3.88771 EndZ=0
    g5: LineSegment StartX=-0.941117 StartY=-3.88771 StartZ=0 EndX=2.8963 EndY=-2.75889 EndZ=0
    g6: Circle CenterX=0 CenterY=0 CenterZ=0 NormalX=0 NormalY=0 NormalZ=1 AngleXU=0 Radius=4
    g7: Circle CenterX=0 CenterY=0 CenterZ=0 NormalX=0 NormalY=0 NormalZ=1 AngleXU=0 Radius=2.5
  constraints (17):
    c: Coincident(g0,g1)
    c: Coincident(g1,g2)
    c: Coincident(g2,g3)
    c: Coincident(g3,g4)
    c: Coincident(g4,g5)
    c: Coincident(g5,g0)
    c: Equal(g0, g1-g5) x5
    c: PointOnObject(g0,g6)
    c: PointOnObject(g1,g6)
    c: PointOnObject(g2,g6)
    c: PointOnObject(g3,g6)
    c: PointOnObject(g4,g6)
    c: PointOnObject(g5,g6)
    c: Coincident(g6,g-1)
    c: Coincident(g7,g6)
    c: Radius(g7) = 2.5
    c: Radius(g6) = 4
FEATURE [PartDesign::Pad] Pad169
  Direction = (1,-2e-16,3e-16)
  Length = 3
  Length2 = 10
  Placement = pos=(0,0,0) rot=(0.57735,0.57735,0.57735;2.0944rad)
  Profile = -> Sketch341
  Type = 0
FEATURE [PartDesign::Pad] Pad171
  BaseFeature = -> Pad169
  Direction = (1,-2e-16,6e-16)
  Length = 15
  Length2 = 10
  Placement = pos=(0,0,0) rot=(0.57735,0.57735,0.57735;2.0944rad)
  Profile = -> Pad169 [Edge20]
  Type = 0
FEATURE [PartDesign::Body] Body245
  Group = -> [Sketch341,Pad169,Pad171]
  Origin = -> Origin352
  Tip = -> Pad171
FEATURE [App::Part] Part107  label="tornillo M5-15-020"
  Group = -> [Body245]
  Origin = -> Origin351
  Placement = pos=(26,10,159) rot=(0,1,0;3.14159rad)
FEATURE [Sketcher::SketchObject] Sketch342
  FullyConstrained = false
  MapMode = 5
  Placement = pos=(0,0,0) rot=(0.57735,0.57735,0.57735;2.0944rad)
  Support = -> [YZ_Plane347]
  sketch-geometry (8):
    g0: LineSegment StartX=2.8963 StartY=-2.75889 StartZ=0 EndX=3.83742 EndY=1.12882 EndZ=0
    g1: LineSegment StartX=3.83742 StartY=1.12882 StartZ=0 EndX=0.941117 EndY=3.88771 EndZ=0
    g2: LineSegment StartX=0.941117 StartY=3.88771 StartZ=0 EndX=-2.8963 EndY=2.75889 EndZ=0
    g3: LineSegment StartX=-2.8963 StartY=2.75889 StartZ=0 EndX=-3.83742 EndY=-1.12882 EndZ=0
    g4: LineSegment StartX=-3.83742 StartY=-1.12882 StartZ=0 EndX=-0.941117 EndY=-3.88771 EndZ=0
    g5: LineSegment StartX=-0.941117 StartY=-3.88771 StartZ=0 EndX=2.8963 EndY=-2.75889 EndZ=0
    g6: Circle CenterX=0 CenterY=0 CenterZ=0 NormalX=0 NormalY=0 NormalZ=1 AngleXU=0 Radius=4
    g7: Circle CenterX=0 CenterY=0 CenterZ=0 NormalX=0 NormalY=0 NormalZ=1 AngleXU=0 Radius=2.5
  constraints (17):
    c: Coincident(g0,g1)
    c: Coincident(g1,g2)
    c: Coincident(g2,g3)
    c: Coincident(g3,g4)
    c: Coincident(g4,g5)
    c: Coincident(g5,g0)
    c: Equal(g0, g1-g5) x5
    c: PointOnObject(g0,g6)
    c: PointOnObject(g1,g6)
    c: PointOnObject(g2,g6)
    c: PointOnObject(g3,g6)
    c: PointOnObject(g4,g6)
    c: PointOnObject(g5,g6)
    c: Coincident(g6,g-1)
    c: Coincident(g7,g6)
    c: Radius(g7) = 2.5
    c: Radius(g6) = 4
FEATURE [PartDesign::Pad] Pad173
  Direction = (1,-2e-16,3e-16)
  Length = 3
  Length2 = 10
  Placement = pos=(0,0,0) rot=(0.57735,0.57735,0.57735;2.0944rad)
  Profile = -> Sketch342
  Type = 0
FEATURE [PartDesign::Pad] Pad172
  BaseFeature = -> Pad173
  Direction = (1,-2e-16,6e-16)
  Length = 15
  Length2 = 10
  Placement = pos=(0,0,0) rot=(0.57735,0.57735,0.57735;2.0944rad)
  Profile = -> Pad173 [Edge20]
  Type = 0
FEATURE [PartDesign::Body] Body246
  Group = -> [Sketch342,Pad173,Pad172]
  Origin = -> Origin354
  Tip = -> Pad172
FEATURE [App::Part] Part106  label="tornillo M5-15-019"
  Group = -> [Body246]
  Origin = -> Origin353
  Placement = pos=(28.2334,9.96532,164.125) rot=(0.44435,-0.754393,0.483161;1.89214rad)
FEATURE [App::LinkGroup] LinkGroup020
  ElementList = -> [Part104,Part105,Part106,Part107]
  LinkMode = 0
  Placement = pos=(339.888,20.1907,1.52588e-05) rot=(0,0,1;3.14159rad)
FEATURE [App::LinkGroup] LinkGroup021
  ElementList = -> [Part100,Part101,Part102,Part103,LinkGroup020]
  LinkMode = 0
FEATURE [Sketcher::SketchObject] Sketch343
  FullyConstrained = false
  MapMode = 5
  Placement = pos=(0,0,0) rot=(0.57735,0.57735,0.57735;2.0944rad)
  Support = -> [YZ_Plane350]
  sketch-geometry (8):
    g0: LineSegment StartX=2.8963 StartY=-2.75889 StartZ=0 EndX=3.83742 EndY=1.12882 EndZ=0
    g1: LineSegment StartX=3.83742 StartY=1.12882 StartZ=0 EndX=0.941117 EndY=3.88771 EndZ=0
    g2: LineSegment StartX=0.941117 StartY=3.88771 StartZ=0 EndX=-2.8963 EndY=2.75889 EndZ=0
    g3: LineSegment StartX=-2.8963 StartY=2.75889 StartZ=0 EndX=-3.83742 EndY=-1.12882 EndZ=0
    g4: LineSegment StartX=-3.83742 StartY=-1.12882 StartZ=0 EndX=-0.941117 EndY=-3.88771 EndZ=0
    g5: LineSegment StartX=-0.941117 StartY=-3.88771 StartZ=0 EndX=2.8963 EndY=-2.75889 EndZ=0
    g6: Circle CenterX=0 CenterY=0 CenterZ=0 NormalX=0 NormalY=0 NormalZ=1 AngleXU=0 Radius=4
    g7: Circle CenterX=0 CenterY=0 CenterZ=0 NormalX=0 NormalY=0 NormalZ=1 AngleXU=0 Radius=2.5
  constraints (17):
    c: Coincident(g0,g1)
    c: Coincident(g1,g2)
    c: Coincident(g2,g3)
    c: Coincident(g3,g4)
    c: Coincident(g4,g5)
    c: Coincident(g5,g0)
    c: Equal(g0, g1-g5) x5
    c: PointOnObject(g0,g6)
    c: PointOnObject(g1,g6)
    c: PointOnObject(g2,g6)
    c: PointOnObject(g3,g6)
    c: PointOnObject(g4,g6)
    c: PointOnObject(g5,g6)
    c: Coincident(g6,g-1)
    c: Coincident(g7,g6)
    c: Radius(g7) = 2.5
    c: Radius(g6) = 4
FEATURE [PartDesign::Pad] Pad175
  Direction = (1,-2e-16,3e-16)
  Length = 3
  Length2 = 10
  Placement = pos=(0,0,0) rot=(0.57735,0.57735,0.57735;2.0944rad)
  Profile = -> Sketch343
  Type = 0
FEATURE [PartDesign::Pad] Pad176
  BaseFeature = -> Pad175
  Direction = (1,-2e-16,6e-16)
  Length = 15
  Length2 = 10
  Placement = pos=(0,0,0) rot=(0.57735,0.57735,0.57735;2.0944rad)
  Profile = -> Pad175 [Edge20]
  Type = 0
FEATURE [PartDesign::Body] Body247
  Group = -> [Sketch343,Pad175,Pad176]
  Origin = -> Origin359
  Tip = -> Pad176
FEATURE [App::Part] Part108  label="tornillo M5-15-021"
  Group = -> [Body247]
  Origin = -> Origin357
  Placement = pos=(31,10,26) rot=(0,1,0;1.5708rad)
FEATURE [Sketcher::SketchObject] Sketch344
  FullyConstrained = false
  MapMode = 5
  Placement = pos=(0,0,0) rot=(0.57735,0.57735,0.57735;2.0944rad)
  Support = -> [YZ_Plane351]
  sketch-geometry (8):
    g0: LineSegment StartX=2.8963 StartY=-2.75889 StartZ=0 EndX=3.83742 EndY=1.12882 EndZ=0
    g1: LineSegment StartX=3.83742 StartY=1.12882 StartZ=0 EndX=0.941117 EndY=3.88771 EndZ=0
    g2: LineSegment StartX=0.941117 StartY=3.88771 StartZ=0 EndX=-2.8963 EndY=2.75889 EndZ=0
    g3: LineSegment StartX=-2.8963 StartY=2.75889 StartZ=0 EndX=-3.83742 EndY=-1.12882 EndZ=0
    g4: LineSegment StartX=-3.83742 StartY=-1.12882 StartZ=0 EndX=-0.941117 EndY=-3.88771 EndZ=0
    g5: LineSegment StartX=-0.941117 StartY=-3.88771 StartZ=0 EndX=2.8963 EndY=-2.75889 EndZ=0
    g6: Circle CenterX=0 CenterY=0 CenterZ=0 NormalX=0 NormalY=0 NormalZ=1 AngleXU=0 Radius=4
    g7: Circle CenterX=0 CenterY=0 CenterZ=0 NormalX=0 NormalY=0 NormalZ=1 AngleXU=0 Radius=2.5
  constraints (17):
    c: Coincident(g0,g1)
    c: Coincident(g1,g2)
    c: Coincident(g2,g3)
    c: Coincident(g3,g4)
    c: Coincident(g4,g5)
    c: Coincident(g5,g0)
    c: Equal(g0, g1-g5) x5
    c: PointOnObject(g0,g6)
    c: PointOnObject(g1,g6)
    c: PointOnObject(g2,g6)
    c: PointOnObject(g3,g6)
    c: PointOnObject(g4,g6)
    c: PointOnObject(g5,g6)
    c: Coincident(g6,g-1)
    c: Coincident(g7,g6)
    c: Radius(g7) = 2.5
    c: Radius(g6) = 4
FEATURE [PartDesign::Pad] Pad174
  Direction = (1,-2e-16,3e-16)
  Length = 3
  Length2 = 10
  Placement = pos=(0,0,0) rot=(0.57735,0.57735,0.57735;2.0944rad)
  Profile = -> Sketch344
  Type = 0
FEATURE [PartDesign::Pad] Pad178
  BaseFeature = -> Pad174
  Direction = (1,-2e-16,6e-16)
  Length = 15
  Length2 = 10
  Placement = pos=(0,0,0) rot=(0.57735,0.57735,0.57735;2.0944rad)
  Profile = -> Pad174 [Edge20]
  Type = 0
FEATURE [PartDesign::Body] Body248
  Group = -> [Sketch344,Pad174,Pad178]
  Origin = -> Origin358
  Tip = -> Pad178
FEATURE [App::Part] Part109  label="tornillo M5-15-022"
  Group = -> [Body248]
  Origin = -> Origin356
  Placement = pos=(26,10,33) rot=(0,1,0;3.14159rad)
FEATURE [Sketcher::SketchObject] Sketch345
  FullyConstrained = false
  MapMode = 5
  Placement = pos=(0,0,0) rot=(0.57735,0.57735,0.57735;2.0944rad)
  Support = -> [YZ_Plane363]
  sketch-geometry (8):
    g0: LineSegment StartX=2.8963 StartY=-2.75889 StartZ=0 EndX=3.83742 EndY=1.12882 EndZ=0
    g1: LineSegment StartX=3.83742 StartY=1.12882 StartZ=0 EndX=0.941117 EndY=3.88771 EndZ=0
    g2: LineSegment StartX=0.941117 StartY=3.88771 StartZ=0 EndX=-2.8963 EndY=2.75889 EndZ=0
    g3: LineSegment StartX=-2.8963 StartY=2.75889 StartZ=0 EndX=-3.83742 EndY=-1.12882 EndZ=0
    g4: LineSegment StartX=-3.83742 StartY=-1.12882 StartZ=0 EndX=-0.941117 EndY=-3.88771 EndZ=0
    g5: LineSegment StartX=-0.941117 StartY=-3.88771 StartZ=0 EndX=2.8963 EndY=-2.75889 EndZ=0
    g6: Circle CenterX=0 CenterY=0 CenterZ=0 NormalX=0 NormalY=0 NormalZ=1 AngleXU=0 Radius=4
    g7: Circle CenterX=0 CenterY=0 CenterZ=0 NormalX=0 NormalY=0 NormalZ=1 AngleXU=0 Radius=2.5
  constraints (17):
    c: Coincident(g0,g1)
    c: Coincident(g1,g2)
    c: Coincident(g2,g3)
    c: Coincident(g3,g4)
    c: Coincident(g4,g5)
    c: Coincident(g5,g0)
    c: Equal(g0, g1-g5) x5
    c: PointOnObject(g0,g6)
    c: PointOnObject(g1,g6)
    c: PointOnObject(g2,g6)
    c: PointOnObject(g3,g6)
    c: PointOnObject(g4,g6)
    c: PointOnObject(g5,g6)
    c: Coincident(g6,g-1)
    c: Coincident(g7,g6)
    c: Radius(g7) = 2.5
    c: Radius(g6) = 4
FEATURE [PartDesign::Pad] Pad180
  Direction = (1,-2e-16,3e-16)
  Length = 3
  Length2 = 10
  Placement = pos=(0,0,0) rot=(0.57735,0.57735,0.57735;2.0944rad)
  Profile = -> Sketch345
  Type = 0
FEATURE [Sketcher::SketchObject] Sketch346
  FullyConstrained = false
  MapMode = 5
  Placement = pos=(0,0,0) rot=(0.57735,0.57735,0.57735;2.0944rad)
  Support = -> [YZ_Plane352]
  sketch-geometry (8):
    g0: LineSegment StartX=2.8963 StartY=-2.75889 StartZ=0 EndX=3.83742 EndY=1.12882 EndZ=0
    g1: LineSegment StartX=3.83742 StartY=1.12882 StartZ=0 EndX=0.941117 EndY=3.88771 EndZ=0
    g2: LineSegment StartX=0.941117 StartY=3.88771 StartZ=0 EndX=-2.8963 EndY=2.75889 EndZ=0
    g3: LineSegment StartX=-2.8963 StartY=2.75889 StartZ=0 EndX=-3.83742 EndY=-1.12882 EndZ=0
    g4: LineSegment StartX=-3.83742 StartY=-1.12882 StartZ=0 EndX=-0.941117 EndY=-3.88771 EndZ=0
    g5: LineSegment StartX=-0.941117 StartY=-3.88771 StartZ=0 EndX=2.8963 EndY=-2.75889 EndZ=0
    g6: Circle CenterX=0 CenterY=0 CenterZ=0 NormalX=0 NormalY=0 NormalZ=1 AngleXU=0 Radius=4
    g7: Circle CenterX=0 CenterY=0 CenterZ=0 NormalX=0 NormalY=0 NormalZ=1 AngleXU=0 Radius=2.5
  constraints (17):
    c: Coincident(g0,g1)
    c: Coincident(g1,g2)
    c: Coincident(g2,g3)
    c: Coincident(g3,g4)
    c: Coincident(g4,g5)
    c: Coincident(g5,g0)
    c: Equal(g0, g1-g5) x5
    c: PointOnObject(g0,g6)
    c: PointOnObject(g1,g6)
    c: PointOnObject(g2,g6)
    c: PointOnObject(g3,g6)
    c: PointOnObject(g4,g6)
    c: PointOnObject(g5,g6)
    c: Coincident(g6,g-1)
    c: Coincident(g7,g6)
    c: Radius(g7) = 2.5
    c: Radius(g6) = 4
FEATURE [PartDesign::Pad] Pad177
  Direction = (1,-2e-16,3e-16)
  Length = 3
  Length2 = 10
  Placement = pos=(0,0,0) rot=(0.57735,0.57735,0.57735;2.0944rad)
  Profile = -> Sketch346
  Type = 0
FEATURE [PartDesign::Pad] Pad181
  BaseFeature = -> Pad177
  Direction = (1,-2e-16,6e-16)
  Length = 15
  Length2 = 10
  Placement = pos=(0,0,0) rot=(0.57735,0.57735,0.57735;2.0944rad)
  Profile = -> Pad177 [Edge20]
  Type = 0
FEATURE [PartDesign::Body] Body249
  Group = -> [Sketch346,Pad177,Pad181]
  Origin = -> Origin361
  Tip = -> Pad181
FEATURE [App::Part] Part111  label="tornillo M5-15-024"
  Group = -> [Body249]
  Origin = -> Origin360
  Placement = pos=(26,10,159) rot=(0,1,0;3.14159rad)
FEATURE [Sketcher::SketchObject] Sketch347
  FullyConstrained = false
  MapMode = 5
  Placement = pos=(0,0,0) rot=(0.57735,0.57735,0.57735;2.0944rad)
  Support = -> [YZ_Plane361]
  sketch-geometry (8):
    g0: LineSegment StartX=2.8963 StartY=-2.75889 StartZ=0 EndX=3.83742 EndY=1.12882 EndZ=0
    g1: LineSegment StartX=3.83742 StartY=1.12882 StartZ=0 EndX=0.941117 EndY=3.88771 EndZ=0
    g2: LineSegment StartX=0.941117 StartY=3.88771 StartZ=0 EndX=-2.8963 EndY=2.75889 EndZ=0
    g3: LineSegment StartX=-2.8963 StartY=2.75889 StartZ=0 EndX=-3.83742 EndY=-1.12882 EndZ=0
    g4: LineSegment StartX=-3.83742 StartY=-1.12882 StartZ=0 EndX=-0.941117 EndY=-3.88771 EndZ=0
    g5: LineSegment StartX=-0.941117 StartY=-3.88771 StartZ=0 EndX=2.8963 EndY=-2.75889 EndZ=0
    g6: Circle CenterX=0 CenterY=0 CenterZ=0 NormalX=0 NormalY=0 NormalZ=1 AngleXU=0 Radius=4
    g7: Circle CenterX=0 CenterY=0 CenterZ=0 NormalX=0 NormalY=0 NormalZ=1 AngleXU=0 Radius=2.5
  constraints (17):
    c: Coincident(g0,g1)
    c: Coincident(g1,g2)
    c: Coincident(g2,g3)
    c: Coincident(g3,g4)
    c: Coincident(g4,g5)
    c: Coincident(g5,g0)
    c: Equal(g0, g1-g5) x5
    c: PointOnObject(g0,g6)
    c: PointOnObject(g1,g6)
    c: PointOnObject(g2,g6)
    c: PointOnObject(g3,g6)
    c: PointOnObject(g4,g6)
    c: PointOnObject(g5,g6)
    c: Coincident(g6,g-1)
    c: Coincident(g7,g6)
    c: Radius(g7) = 2.5
    c: Radius(g6) = 4
FEATURE [PartDesign::Pad] Pad179
  Direction = (1,-2e-16,3e-16)
  Length = 3
  Length2 = 10
  Placement = pos=(0,0,0) rot=(0.57735,0.57735,0.57735;2.0944rad)
  Profile = -> Sketch347
  Type = 0
FEATURE [Sketcher::SketchObject] Sketch348
  FullyConstrained = false
  MapMode = 5
  Placement = pos=(0,0,0) rot=(0.57735,0.57735,0.57735;2.0944rad)
  Support = -> [YZ_Plane355]
  sketch-geometry (8):
    g0: LineSegment StartX=2.8963 StartY=-2.75889 StartZ=0 EndX=3.83742 EndY=1.12882 EndZ=0
    g1: LineSegment StartX=3.83742 StartY=1.12882 StartZ=0 EndX=0.941117 EndY=3.88771 EndZ=0
    g2: LineSegment StartX=0.941117 StartY=3.88771 StartZ=0 EndX=-2.8963 EndY=2.75889 EndZ=0
    g3: LineSegment StartX=-2.8963 StartY=2.75889 StartZ=0 EndX=-3.83742 EndY=-1.12882 EndZ=0
    g4: LineSegment StartX=-3.83742 StartY=-1.12882 StartZ=0 EndX=-0.941117 EndY=-3.88771 EndZ=0
    g5: LineSegment StartX=-0.941117 StartY=-3.88771 StartZ=0 EndX=2.8963 EndY=-2.75889 EndZ=0
    g6: Circle CenterX=0 CenterY=0 CenterZ=0 NormalX=0 NormalY=0 NormalZ=1 AngleXU=0 Radius=4
    g7: Circle CenterX=0 CenterY=0 CenterZ=0 NormalX=0 NormalY=0 NormalZ=1 AngleXU=0 Radius=2.5
  constraints (17):
    c: Coincident(g0,g1)
    c: Coincident(g1,g2)
    c: Coincident(g2,g3)
    c: Coincident(g3,g4)
    c: Coincident(g4,g5)
    c: Coincident(g5,g0)
    c: Equal(g0, g1-g5) x5
    c: PointOnObject(g0,g6)
    c: PointOnObject(g1,g6)
    c: PointOnObject(g2,g6)
    c: PointOnObject(g3,g6)
    c: PointOnObject(g4,g6)
    c: PointOnObject(g5,g6)
    c: Coincident(g6,g-1)
    c: Coincident(g7,g6)
    c: Radius(g7) = 2.5
    c: Radius(g6) = 4
FEATURE [PartDesign::Pad] Pad184
  Direction = (1,-2e-16,3e-16)
  Length = 3
  Length2 = 10
  Placement = pos=(0,0,0) rot=(0.57735,0.57735,0.57735;2.0944rad)
  Profile = -> Sketch348
  Type = 0
FEATURE [PartDesign::Pad] Pad183
  BaseFeature = -> Pad184
  Direction = (1,-2e-16,6e-16)
  Length = 15
  Length2 = 10
  Placement = pos=(0,0,0) rot=(0.57735,0.57735,0.57735;2.0944rad)
  Profile = -> Pad184 [Edge20]
  Type = 0
FEATURE [PartDesign::Body] Body253
  Group = -> [Sketch348,Pad184,Pad183]
  Origin = -> Origin363
  Tip = -> Pad183
FEATURE [App::Part] Part110  label="tornillo M5-15-023"
  Group = -> [Body253]
  Origin = -> Origin362
  Placement = pos=(28.2334,9.96532,164.125) rot=(0.44435,-0.754393,0.483161;1.89214rad)
FEATURE [PartDesign::Pad] Pad185
  BaseFeature = -> Pad180
  Direction = (1,-2e-16,6e-16)
  Length = 15
  Length2 = 10
  Placement = pos=(0,0,0) rot=(0.57735,0.57735,0.57735;2.0944rad)
  Profile = -> Pad180 [Edge20]
  Type = 0
FEATURE [PartDesign::Body] Body250
  Group = -> [Sketch345,Pad180,Pad185]
  Origin = -> Origin365
  Tip = -> Pad185
FEATURE [App::Part] Part113  label="tornillo M5-15-026"
  Group = -> [Body250]
  Origin = -> Origin367
  Placement = pos=(31,10,26) rot=(0,1,0;1.5708rad)
FEATURE [PartDesign::Pad] Pad186
  BaseFeature = -> Pad179
  Direction = (1,-2e-16,6e-16)
  Length = 15
  Length2 = 10
  Placement = pos=(0,0,0) rot=(0.57735,0.57735,0.57735;2.0944rad)
  Profile = -> Pad179 [Edge20]
  Type = 0
FEATURE [PartDesign::Body] Body251
  Group = -> [Sketch347,Pad179,Pad186]
  Origin = -> Origin366
  Tip = -> Pad186
FEATURE [App::Part] Part112  label="tornillo M5-15-025"
  Group = -> [Body251]
  Origin = -> Origin355
  Placement = pos=(26,10,33) rot=(0,1,0;3.14159rad)
FEATURE [Sketcher::SketchObject] Sketch349
  FullyConstrained = false
  MapMode = 5
  Placement = pos=(0,0,0) rot=(0.57735,0.57735,0.57735;2.0944rad)
  Support = -> [YZ_Plane358]
  sketch-geometry (8):
    g0: LineSegment StartX=2.8963 StartY=-2.75889 StartZ=0 EndX=3.83742 EndY=1.12882 EndZ=0
    g1: LineSegment StartX=3.83742 StartY=1.12882 StartZ=0 EndX=0.941117 EndY=3.88771 EndZ=0
    g2: LineSegment StartX=0.941117 StartY=3.88771 StartZ=0 EndX=-2.8963 EndY=2.75889 EndZ=0
    g3: LineSegment StartX=-2.8963 StartY=2.75889 StartZ=0 EndX=-3.83742 EndY=-1.12882 EndZ=0
    g4: LineSegment StartX=-3.83742 StartY=-1.12882 StartZ=0 EndX=-0.941117 EndY=-3.88771 EndZ=0
    g5: LineSegment StartX=-0.941117 StartY=-3.88771 StartZ=0 EndX=2.8963 EndY=-2.75889 EndZ=0
    g6: Circle CenterX=0 CenterY=0 CenterZ=0 NormalX=0 NormalY=0 NormalZ=1 AngleXU=0 Radius=4
    g7: Circle CenterX=0 CenterY=0 CenterZ=0 NormalX=0 NormalY=0 NormalZ=1 AngleXU=0 Radius=2.5
  constraints (17):
    c: Coincident(g0,g1)
    c: Coincident(g1,g2)
    c: Coincident(g2,g3)
    c: Coincident(g3,g4)
    c: Coincident(g4,g5)
    c: Coincident(g5,g0)
    c: Equal(g0, g1-g5) x5
    c: PointOnObject(g0,g6)
    c: PointOnObject(g1,g6)
    c: PointOnObject(g2,g6)
    c: PointOnObject(g3,g6)
    c: PointOnObject(g4,g6)
    c: PointOnObject(g5,g6)
    c: Coincident(g6,g-1)
    c: Coincident(g7,g6)
    c: Radius(g7) = 2.5
    c: Radius(g6) = 4
FEATURE [PartDesign::Pad] Pad182
  Direction = (1,-2e-16,3e-16)
  Length = 3
  Length2 = 10
  Placement = pos=(0,0,0) rot=(0.57735,0.57735,0.57735;2.0944rad)
  Profile = -> Sketch349
  Type = 0
FEATURE [PartDesign::Pad] Pad187
  BaseFeature = -> Pad182
  Direction = (1,-2e-16,6e-16)
  Length = 15
  Length2 = 10
  Placement = pos=(0,0,0) rot=(0.57735,0.57735,0.57735;2.0944rad)
  Profile = -> Pad182 [Edge20]
  Type = 0
FEATURE [PartDesign::Body] Body252
  Group = -> [Sketch349,Pad182,Pad187]
  Origin = -> Origin369
  Tip = -> Pad187
FEATURE [App::Part] Part115  label="tornillo M5-15-028"
  Group = -> [Body252]
  Origin = -> Origin368
  Placement = pos=(26,10,159) rot=(0,1,0;3.14159rad)
FEATURE [Sketcher::SketchObject] Sketch350
  FullyConstrained = false
  MapMode = 5
  Placement = pos=(0,0,0) rot=(0.57735,0.57735,0.57735;2.0944rad)
  Support = -> [YZ_Plane356]
  sketch-geometry (8):
    g0: LineSegment StartX=2.8963 StartY=-2.75889 StartZ=0 EndX=3.83742 EndY=1.12882 EndZ=0
    g1: LineSegment StartX=3.83742 StartY=1.12882 StartZ=0 EndX=0.941117 EndY=3.88771 EndZ=0
    g2: LineSegment StartX=0.941117 StartY=3.88771 StartZ=0 EndX=-2.8963 EndY=2.75889 EndZ=0
    g3: LineSegment StartX=-2.8963 StartY=2.75889 StartZ=0 EndX=-3.83742 EndY=-1.12882 EndZ=0
    g4: LineSegment StartX=-3.83742 StartY=-1.12882 StartZ=0 EndX=-0.941117 EndY=-3.88771 EndZ=0
    g5: LineSegment StartX=-0.941117 StartY=-3.88771 StartZ=0 EndX=2.8963 EndY=-2.75889 EndZ=0
    g6: Circle CenterX=0 CenterY=0 CenterZ=0 NormalX=0 NormalY=0 NormalZ=1 AngleXU=0 Radius=4
    g7: Circle CenterX=0 CenterY=0 CenterZ=0 NormalX=0 NormalY=0 NormalZ=1 AngleXU=0 Radius=2.5
  constraints (17):
    c: Coincident(g0,g1)
    c: Coincident(g1,g2)
    c: Coincident(g2,g3)
    c: Coincident(g3,g4)
    c: Coincident(g4,g5)
    c: Coincident(g5,g0)
    c: Equal(g0, g1-g5) x5
    c: PointOnObject(g0,g6)
    c: PointOnObject(g1,g6)
    c: PointOnObject(g2,g6)
    c: PointOnObject(g3,g6)
    c: PointOnObject(g4,g6)
    c: PointOnObject(g5,g6)
    c: Coincident(g6,g-1)
    c: Coincident(g7,g6)
    c: Radius(g7) = 2.5
    c: Radius(g6) = 4
FEATURE [PartDesign::Pad] Pad189
  Direction = (1,-2e-16,3e-16)
  Length = 3
  Length2 = 10
  Placement = pos=(0,0,0) rot=(0.57735,0.57735,0.57735;2.0944rad)
  Profile = -> Sketch350
  Type = 0
FEATURE [PartDesign::Pad] Pad188
  BaseFeature = -> Pad189
  Direction = (1,-2e-16,6e-16)
  Length = 15
  Length2 = 10
  Placement = pos=(0,0,0) rot=(0.57735,0.57735,0.57735;2.0944rad)
  Profile = -> Pad189 [Edge20]
  Type = 0
FEATURE [PartDesign::Body] Body254
  Group = -> [Sketch350,Pad189,Pad188]
  Origin = -> Origin370
  Tip = -> Pad188
FEATURE [App::Part] Part114  label="tornillo M5-15-027"
  Group = -> [Body254]
  Origin = -> Origin364
  Placement = pos=(28.2334,9.96532,164.125) rot=(0.44435,-0.754393,0.483161;1.89214rad)
FEATURE [App::LinkGroup] LinkGroup022
  ElementList = -> [Part113,Part112,Part114,Part115]
  LinkMode = 0
  Placement = pos=(339.888,20.1907,1.52588e-05) rot=(0,0,1;3.14159rad)
FEATURE [App::LinkGroup] LinkGroup023
  ElementList = -> [Part108,Part109,Part111,Part110,LinkGroup022]
  LinkMode = 0
  Placement = pos=(-1.52588e-05,319,-7.62939e-06) rot=(0,0,1;0rad)
FEATURE [Sketcher::SketchObject] Sketch351
  FullyConstrained = false
  MapMode = 5
  Placement = pos=(0,0,0) rot=(0.57735,0.57735,0.57735;2.0944rad)
  Support = -> [YZ_Plane366]
  sketch-geometry (8):
    g0: LineSegment StartX=2.8963 StartY=-2.75889 StartZ=0 EndX=3.83742 EndY=1.12882 EndZ=0
    g1: LineSegment StartX=3.83742 StartY=1.12882 StartZ=0 EndX=0.941117 EndY=3.88771 EndZ=0
    g2: LineSegment StartX=0.941117 StartY=3.88771 StartZ=0 EndX=-2.8963 EndY=2.75889 EndZ=0
    g3: LineSegment StartX=-2.8963 StartY=2.75889 StartZ=0 EndX=-3.83742 EndY=-1.12882 EndZ=0
    g4: LineSegment StartX=-3.83742 StartY=-1.12882 StartZ=0 EndX=-0.941117 EndY=-3.88771 EndZ=0
    g5: LineSegment StartX=-0.941117 StartY=-3.88771 StartZ=0 EndX=2.8963 EndY=-2.75889 EndZ=0
    g6: Circle CenterX=0 CenterY=0 CenterZ=0 NormalX=0 NormalY=0 NormalZ=1 AngleXU=0 Radius=4
    g7: Circle CenterX=0 CenterY=0 CenterZ=0 NormalX=0 NormalY=0 NormalZ=1 AngleXU=0 Radius=2.5
  constraints (17):
    c: Coincident(g0,g1)
    c: Coincident(g1,g2)
    c: Coincident(g2,g3)
    c: Coincident(g3,g4)
    c: Coincident(g4,g5)
    c: Coincident(g5,g0)
    c: Equal(g0, g1-g5) x5
    c: PointOnObject(g0,g6)
    c: PointOnObject(g1,g6)
    c: PointOnObject(g2,g6)
    c: PointOnObject(g3,g6)
    c: PointOnObject(g4,g6)
    c: PointOnObject(g5,g6)
    c: Coincident(g6,g-1)
    c: Coincident(g7,g6)
    c: Radius(g7) = 2.5
    c: Radius(g6) = 4
FEATURE [PartDesign::Pad] Pad190
  Direction = (1,-2e-16,3e-16)
  Length = 3
  Length2 = 10
  Placement = pos=(0,0,0) rot=(0.57735,0.57735,0.57735;2.0944rad)
  Profile = -> Sketch351
  Type = 0
FEATURE [PartDesign::Pad] Pad191
  BaseFeature = -> Pad190
  Direction = (1,-2e-16,6e-16)
  Length = 15
  Length2 = 10
  Placement = pos=(0,0,0) rot=(0.57735,0.57735,0.57735;2.0944rad)
  Profile = -> Pad190 [Edge20]
  Type = 0
FEATURE [PartDesign::Body] Body255
  Group = -> [Sketch351,Pad190,Pad191]
  Origin = -> Origin372
  Tip = -> Pad191
FEATURE [App::Part] Part116  label="tornillo M5-15-029"
  Group = -> [Body255]
  Origin = -> Origin371
  Placement = pos=(327,28,57) rot=(0.707107,-0.707107,0;3.14159rad)
FEATURE [Sketcher::SketchObject] Sketch352
  FullyConstrained = false
  MapMode = 5
  Placement = pos=(0,0,0) rot=(0.57735,0.57735,0.57735;2.0944rad)
  Support = -> [YZ_Plane367]
  sketch-geometry (8):
    g0: LineSegment StartX=2.8963 StartY=-2.75889 StartZ=0 EndX=3.83742 EndY=1.12882 EndZ=0
    g1: LineSegment StartX=3.83742 StartY=1.12882 StartZ=0 EndX=0.941117 EndY=3.88771 EndZ=0
    g2: LineSegment StartX=0.941117 StartY=3.88771 StartZ=0 EndX=-2.8963 EndY=2.75889 EndZ=0
    g3: LineSegment StartX=-2.8963 StartY=2.75889 StartZ=0 EndX=-3.83742 EndY=-1.12882 EndZ=0
    g4: LineSegment StartX=-3.83742 StartY=-1.12882 StartZ=0 EndX=-0.941117 EndY=-3.88771 EndZ=0
    g5: LineSegment StartX=-0.941117 StartY=-3.88771 StartZ=0 EndX=2.8963 EndY=-2.75889 EndZ=0
    g6: Circle CenterX=0 CenterY=0 CenterZ=0 NormalX=0 NormalY=0 NormalZ=1 AngleXU=0 Radius=4
    g7: Circle CenterX=0 CenterY=0 CenterZ=0 NormalX=0 NormalY=0 NormalZ=1 AngleXU=0 Radius=2.5
  constraints (17):
    c: Coincident(g0,g1)
    c: Coincident(g1,g2)
    c: Coincident(g2,g3)
    c: Coincident(g3,g4)
    c: Coincident(g4,g5)
    c: Coincident(g5,g0)
    c: Equal(g0, g1-g5) x5
    c: PointOnObject(g0,g6)
    c: PointOnObject(g1,g6)
    c: PointOnObject(g2,g6)
    c: PointOnObject(g3,g6)
    c: PointOnObject(g4,g6)
    c: PointOnObject(g5,g6)
    c: Coincident(g6,g-1)
    c: Coincident(g7,g6)
    c: Radius(g7) = 2.5
    c: Radius(g6) = 4
FEATURE [PartDesign::Pad] Pad192
  Direction = (1,-2e-16,3e-16)
  Length = 3
  Length2 = 10
  Placement = pos=(0,0,0) rot=(0.57735,0.57735,0.57735;2.0944rad)
  Profile = -> Sketch352
  Type = 0
FEATURE [PartDesign::Pad] Pad193
  BaseFeature = -> Pad192
  Direction = (1,-2e-16,6e-16)
  Length = 15
  Length2 = 10
  Placement = pos=(0,0,0) rot=(0.57735,0.57735,0.57735;2.0944rad)
  Profile = -> Pad192 [Edge20]
  Type = 0
FEATURE [PartDesign::Body] Body256
  Group = -> [Sketch352,Pad192,Pad193]
  Origin = -> Origin374
  Tip = -> Pad193
FEATURE [App::Part] Part117  label="tornillo M5-15-030"
  Group = -> [Body256]
  Origin = -> Origin373
  Placement = pos=(328,31,64) rot=(-0.57735,0.57735,-0.57735;4.18879rad)
FEATURE [App::LinkGroup] LinkGroup024
  ElementList = -> [Part116,Part117]
  LinkMode = 0
FEATURE [Sketcher::SketchObject] Sketch353
  FullyConstrained = false
  MapMode = 5
  Placement = pos=(0,0,0) rot=(0.57735,0.57735,0.57735;2.0944rad)
  Support = -> [YZ_Plane370]
  sketch-geometry (8):
    g0: LineSegment StartX=2.8963 StartY=-2.75889 StartZ=0 EndX=3.83742 EndY=1.12882 EndZ=0
    g1: LineSegment StartX=3.83742 StartY=1.12882 StartZ=0 EndX=0.941117 EndY=3.88771 EndZ=0
    g2: LineSegment StartX=0.941117 StartY=3.88771 StartZ=0 EndX=-2.8963 EndY=2.75889 EndZ=0
    g3: LineSegment StartX=-2.8963 StartY=2.75889 StartZ=0 EndX=-3.83742 EndY=-1.12882 EndZ=0
    g4: LineSegment StartX=-3.83742 StartY=-1.12882 StartZ=0 EndX=-0.941117 EndY=-3.88771 EndZ=0
    g5: LineSegment StartX=-0.941117 StartY=-3.88771 StartZ=0 EndX=2.8963 EndY=-2.75889 EndZ=0
    g6: Circle CenterX=0 CenterY=0 CenterZ=0 NormalX=0 NormalY=0 NormalZ=1 AngleXU=0 Radius=4
    g7: Circle CenterX=0 CenterY=0 CenterZ=0 NormalX=0 NormalY=0 NormalZ=1 AngleXU=0 Radius=2.5
  constraints (17):
    c: Coincident(g0,g1)
    c: Coincident(g1,g2)
    c: Coincident(g2,g3)
    c: Coincident(g3,g4)
    c: Coincident(g4,g5)
    c: Coincident(g5,g0)
    c: Equal(g0, g1-g5) x5
    c: PointOnObject(g0,g6)
    c: PointOnObject(g1,g6)
    c: PointOnObject(g2,g6)
    c: PointOnObject(g3,g6)
    c: PointOnObject(g4,g6)
    c: PointOnObject(g5,g6)
    c: Coincident(g6,g-1)
    c: Coincident(g7,g6)
    c: Radius(g7) = 2.5
    c: Radius(g6) = 4
FEATURE [PartDesign::Pad] Pad195
  Direction = (1,-2e-16,3e-16)
  Length = 3
  Length2 = 10
  Placement = pos=(0,0,0) rot=(0.57735,0.57735,0.57735;2.0944rad)
  Profile = -> Sketch353
  Type = 0
FEATURE [PartDesign::Pad] Pad196
  BaseFeature = -> Pad195
  Direction = (1,-2e-16,6e-16)
  Length = 15
  Length2 = 10
  Placement = pos=(0,0,0) rot=(0.57735,0.57735,0.57735;2.0944rad)
  Profile = -> Pad195 [Edge20]
  Type = 0
FEATURE [PartDesign::Body] Body258
  Group = -> [Sketch353,Pad195,Pad196]
  Origin = -> Origin378
  Tip = -> Pad196
FEATURE [App::Part] Part118  label="tornillo M5-15-031"
  Group = -> [Body258]
  Origin = -> Origin375
  Placement = pos=(327,28,57) rot=(0.707107,-0.707107,0;3.14159rad)
FEATURE [Sketcher::SketchObject] Sketch354
  FullyConstrained = false
  MapMode = 5
  Placement = pos=(0,0,0) rot=(0.57735,0.57735,0.57735;2.0944rad)
  Support = -> [YZ_Plane369]
  sketch-geometry (8):
    g0: LineSegment StartX=2.8963 StartY=-2.75889 StartZ=0 EndX=3.83742 EndY=1.12882 EndZ=0
    g1: LineSegment StartX=3.83742 StartY=1.12882 StartZ=0 EndX=0.941117 EndY=3.88771 EndZ=0
    g2: LineSegment StartX=0.941117 StartY=3.88771 StartZ=0 EndX=-2.8963 EndY=2.75889 EndZ=0
    g3: LineSegment StartX=-2.8963 StartY=2.75889 StartZ=0 EndX=-3.83742 EndY=-1.12882 EndZ=0
    g4: LineSegment StartX=-3.83742 StartY=-1.12882 StartZ=0 EndX=-0.941117 EndY=-3.88771 EndZ=0
    g5: LineSegment StartX=-0.941117 StartY=-3.88771 StartZ=0 EndX=2.8963 EndY=-2.75889 EndZ=0
    g6: Circle CenterX=0 CenterY=0 CenterZ=0 NormalX=0 NormalY=0 NormalZ=1 AngleXU=0 Radius=4
    g7: Circle CenterX=0 CenterY=0 CenterZ=0 NormalX=0 NormalY=0 NormalZ=1 AngleXU=0 Radius=2.5
  constraints (17):
    c: Coincident(g0,g1)
    c: Coincident(g1,g2)
    c: Coincident(g2,g3)
    c: Coincident(g3,g4)
    c: Coincident(g4,g5)
    c: Coincident(g5,g0)
    c: Equal(g0, g1-g5) x5
    c: PointOnObject(g0,g6)
    c: PointOnObject(g1,g6)
    c: PointOnObject(g2,g6)
    c: PointOnObject(g3,g6)
    c: PointOnObject(g4,g6)
    c: PointOnObject(g5,g6)
    c: Coincident(g6,g-1)
    c: Coincident(g7,g6)
    c: Radius(g7) = 2.5
    c: Radius(g6) = 4
FEATURE [PartDesign::Pad] Pad197
  Direction = (1,-2e-16,3e-16)
  Length = 3
  Length2 = 10
  Placement = pos=(0,0,0) rot=(0.57735,0.57735,0.57735;2.0944rad)
  Profile = -> Sketch354
  Type = 0
FEATURE [PartDesign::Pad] Pad194
  BaseFeature = -> Pad197
  Direction = (1,-2e-16,6e-16)
  Length = 15
  Length2 = 10
  Placement = pos=(0,0,0) rot=(0.57735,0.57735,0.57735;2.0944rad)
  Profile = -> Pad197 [Edge20]
  Type = 0
FEATURE [PartDesign::Body] Body257
  Group = -> [Sketch354,Pad197,Pad194]
  Origin = -> Origin377
  Tip = -> Pad194
FEATURE [App::Part] Part119  label="tornillo M5-15-032"
  Group = -> [Body257]
  Origin = -> Origin376
  Placement = pos=(328,31,64) rot=(-0.57735,0.57735,-0.57735;4.18879rad)
FEATURE [App::LinkGroup] LinkGroup025
  ElementList = -> [Part118,Part119]
  LinkMode = 0
  Placement = pos=(658,341.888,-7.62939e-06) rot=(0,0,1;3.14159rad)
FEATURE [Sketcher::SketchObject] Sketch355
  FullyConstrained = false
  MapMode = 5
  Placement = pos=(0,0,0) rot=(0.57735,0.57735,0.57735;2.0944rad)
  Support = -> [YZ_Plane374]
  sketch-geometry (8):
    g0: LineSegment StartX=2.8963 StartY=-2.75889 StartZ=0 EndX=3.83742 EndY=1.12882 EndZ=0
    g1: LineSegment StartX=3.83742 StartY=1.12882 StartZ=0 EndX=0.941117 EndY=3.88771 EndZ=0
    g2: LineSegment StartX=0.941117 StartY=3.88771 StartZ=0 EndX=-2.8963 EndY=2.75889 EndZ=0
    g3: LineSegment StartX=-2.8963 StartY=2.75889 StartZ=0 EndX=-3.83742 EndY=-1.12882 EndZ=0
    g4: LineSegment StartX=-3.83742 StartY=-1.12882 StartZ=0 EndX=-0.941117 EndY=-3.88771 EndZ=0
    g5: LineSegment StartX=-0.941117 StartY=-3.88771 StartZ=0 EndX=2.8963 EndY=-2.75889 EndZ=0
    g6: Circle CenterX=0 CenterY=0 CenterZ=0 NormalX=0 NormalY=0 NormalZ=1 AngleXU=0 Radius=4
    g7: Circle CenterX=0 CenterY=0 CenterZ=0 NormalX=0 NormalY=0 NormalZ=1 AngleXU=0 Radius=2.5
  constraints (17):
    c: Coincident(g0,g1)
    c: Coincident(g1,g2)
    c: Coincident(g2,g3)
    c: Coincident(g3,g4)
    c: Coincident(g4,g5)
    c: Coincident(g5,g0)
    c: Equal(g0, g1-g5) x5
    c: PointOnObject(g0,g6)
    c: PointOnObject(g1,g6)
    c: PointOnObject(g2,g6)
    c: PointOnObject(g3,g6)
    c: PointOnObject(g4,g6)
    c: PointOnObject(g5,g6)
    c: Coincident(g6,g-1)
    c: Coincident(g7,g6)
    c: Radius(g7) = 2.5
    c: Radius(g6) = 4
FEATURE [PartDesign::Pad] Pad198
  Direction = (1,-2e-16,3e-16)
  Length = 3
  Length2 = 10
  Placement = pos=(0,0,0) rot=(0.57735,0.57735,0.57735;2.0944rad)
  Profile = -> Sketch355
  Type = 0
FEATURE [PartDesign::Pad] Pad199
  BaseFeature = -> Pad198
  Direction = (1,-2e-16,6e-16)
  Length = 15
  Length2 = 10
  Placement = pos=(0,0,0) rot=(0.57735,0.57735,0.57735;2.0944rad)
  Profile = -> Pad198 [Edge20]
  Type = 0
FEATURE [PartDesign::Body] Body259
  Group = -> [Sketch355,Pad198,Pad199]
  Origin = -> Origin380
  Tip = -> Pad199
FEATURE [App::Part] Part120  label="tornillo M5-15-033"
  Group = -> [Body259]
  Origin = -> Origin379
  Placement = pos=(357,108,88) rot=(0,1,0;1.5708rad)
FEATURE [Sketcher::SketchObject] Sketch356
  FullyConstrained = false
  MapMode = 5
  Placement = pos=(0,0,0) rot=(0.57735,0.57735,0.57735;2.0944rad)
  Support = -> [YZ_Plane375]
  sketch-geometry (8):
    g0: LineSegment StartX=2.8963 StartY=-2.75889 StartZ=0 EndX=3.83742 EndY=1.12882 EndZ=0
    g1: LineSegment StartX=3.83742 StartY=1.12882 StartZ=0 EndX=0.941117 EndY=3.88771 EndZ=0
    g2: LineSegment StartX=0.941117 StartY=3.88771 StartZ=0 EndX=-2.8963 EndY=2.75889 EndZ=0
    g3: LineSegment StartX=-2.8963 StartY=2.75889 StartZ=0 EndX=-3.83742 EndY=-1.12882 EndZ=0
    g4: LineSegment StartX=-3.83742 StartY=-1.12882 StartZ=0 EndX=-0.941117 EndY=-3.88771 EndZ=0
    g5: LineSegment StartX=-0.941117 StartY=-3.88771 StartZ=0 EndX=2.8963 EndY=-2.75889 EndZ=0
    g6: Circle CenterX=0 CenterY=0 CenterZ=0 NormalX=0 NormalY=0 NormalZ=1 AngleXU=0 Radius=4
    g7: Circle CenterX=0 CenterY=0 CenterZ=0 NormalX=0 NormalY=0 NormalZ=1 AngleXU=0 Radius=2.5
  constraints (17):
    c: Coincident(g0,g1)
    c: Coincident(g1,g2)
    c: Coincident(g2,g3)
    c: Coincident(g3,g4)
    c: Coincident(g4,g5)
    c: Coincident(g5,g0)
    c: Equal(g0, g1-g5) x5
    c: PointOnObject(g0,g6)
    c: PointOnObject(g1,g6)
    c: PointOnObject(g2,g6)
    c: PointOnObject(g3,g6)
    c: PointOnObject(g4,g6)
    c: PointOnObject(g5,g6)
    c: Coincident(g6,g-1)
    c: Coincident(g7,g6)
    c: Radius(g7) = 2.5
    c: Radius(g6) = 4
FEATURE [PartDesign::Pad] Pad200
  Direction = (1,-2e-16,3e-16)
  Length = 3
  Length2 = 10
  Placement = pos=(0,0,0) rot=(0.57735,0.57735,0.57735;2.0944rad)
  Profile = -> Sketch356
  Type = 0
FEATURE [PartDesign::Pad] Pad201
  BaseFeature = -> Pad200
  Direction = (1,-2e-16,6e-16)
  Length = 15
  Length2 = 10
  Placement = pos=(0,0,0) rot=(0.57735,0.57735,0.57735;2.0944rad)
  Profile = -> Pad200 [Edge20]
  Type = 0
FEATURE [PartDesign::Body] Body260
  Group = -> [Sketch356,Pad200,Pad201]
  Origin = -> Origin382
  Tip = -> Pad201
FEATURE [App::Part] Part121  label="tornillo M5-15-034"
  Group = -> [Body260]
  Origin = -> Origin381
  Placement = pos=(379,108,88) rot=(0,1,0;1.5708rad)
FEATURE [Sketcher::SketchObject] Sketch357
  FullyConstrained = false
  MapMode = 5
  Placement = pos=(0,0,0) rot=(0.57735,0.57735,0.57735;2.0944rad)
  Support = -> [YZ_Plane380]
  sketch-geometry (8):
    g0: LineSegment StartX=2.8963 StartY=-2.75889 StartZ=0 EndX=3.83742 EndY=1.12882 EndZ=0
    g1: LineSegment StartX=3.83742 StartY=1.12882 StartZ=0 EndX=0.941117 EndY=3.88771 EndZ=0
    g2: LineSegment StartX=0.941117 StartY=3.88771 StartZ=0 EndX=-2.8963 EndY=2.75889 EndZ=0
    g3: LineSegment StartX=-2.8963 StartY=2.75889 StartZ=0 EndX=-3.83742 EndY=-1.12882 EndZ=0
    g4: LineSegment StartX=-3.83742 StartY=-1.12882 StartZ=0 EndX=-0.941117 EndY=-3.88771 EndZ=0
    g5: LineSegment StartX=-0.941117 StartY=-3.88771 StartZ=0 EndX=2.8963 EndY=-2.75889 EndZ=0
    g6: Circle CenterX=0 CenterY=0 CenterZ=0 NormalX=0 NormalY=0 NormalZ=1 AngleXU=0 Radius=4
    g7: Circle CenterX=0 CenterY=0 CenterZ=0 NormalX=0 NormalY=0 NormalZ=1 AngleXU=0 Radius=2.5
  constraints (17):
    c: Coincident(g0,g1)
    c: Coincident(g1,g2)
    c: Coincident(g2,g3)
    c: Coincident(g3,g4)
    c: Coincident(g4,g5)
    c: Coincident(g5,g0)
    c: Equal(g0, g1-g5) x5
    c: PointOnObject(g0,g6)
    c: PointOnObject(g1,g6)
    c: PointOnObject(g2,g6)
    c: PointOnObject(g3,g6)
    c: PointOnObject(g4,g6)
    c: PointOnObject(g5,g6)
    c: Coincident(g6,g-1)
    c: Coincident(g7,g6)
    c: Radius(g7) = 2.5
    c: Radius(g6) = 4
FEATURE [PartDesign::Pad] Pad202
  Direction = (1,-2e-16,3e-16)
  Length = 3
  Length2 = 10
  Placement = pos=(0,0,0) rot=(0.57735,0.57735,0.57735;2.0944rad)
  Profile = -> Sketch357
  Type = 0
FEATURE [Sketcher::SketchObject] Sketch358
  FullyConstrained = false
  MapMode = 5
  Placement = pos=(0,0,0) rot=(0.57735,0.57735,0.57735;2.0944rad)
  Support = -> [YZ_Plane378]
  sketch-geometry (8):
    g0: LineSegment StartX=2.8963 StartY=-2.75889 StartZ=0 EndX=3.83742 EndY=1.12882 EndZ=0
    g1: LineSegment StartX=3.83742 StartY=1.12882 StartZ=0 EndX=0.941117 EndY=3.88771 EndZ=0
    g2: LineSegment StartX=0.941117 StartY=3.88771 StartZ=0 EndX=-2.8963 EndY=2.75889 EndZ=0
    g3: LineSegment StartX=-2.8963 StartY=2.75889 StartZ=0 EndX=-3.83742 EndY=-1.12882 EndZ=0
    g4: LineSegment StartX=-3.83742 StartY=-1.12882 StartZ=0 EndX=-0.941117 EndY=-3.88771 EndZ=0
    g5: LineSegment StartX=-0.941117 StartY=-3.88771 StartZ=0 EndX=2.8963 EndY=-2.75889 EndZ=0
    g6: Circle CenterX=0 CenterY=0 CenterZ=0 NormalX=0 NormalY=0 NormalZ=1 AngleXU=0 Radius=4
    g7: Circle CenterX=0 CenterY=0 CenterZ=0 NormalX=0 NormalY=0 NormalZ=1 AngleXU=0 Radius=2.5
  constraints (17):
    c: Coincident(g0,g1)
    c: Coincident(g1,g2)
    c: Coincident(g2,g3)
    c: Coincident(g3,g4)
    c: Coincident(g4,g5)
    c: Coincident(g5,g0)
    c: Equal(g0, g1-g5) x5
    c: PointOnObject(g0,g6)
    c: PointOnObject(g1,g6)
    c: PointOnObject(g2,g6)
    c: PointOnObject(g3,g6)
    c: PointOnObject(g4,g6)
    c: PointOnObject(g5,g6)
    c: Coincident(g6,g-1)
    c: Coincident(g7,g6)
    c: Radius(g7) = 2.5
    c: Radius(g6) = 4
FEATURE [PartDesign::Pad] Pad203
  Direction = (1,-2e-16,3e-16)
  Length = 3
  Length2 = 10
  Placement = pos=(0,0,0) rot=(0.57735,0.57735,0.57735;2.0944rad)
  Profile = -> Sketch358
  Type = 0
FEATURE [PartDesign::Pad] Pad204
  BaseFeature = -> Pad203
  Direction = (1,-2e-16,6e-16)
  Length = 15
  Length2 = 10
  Placement = pos=(0,0,0) rot=(0.57735,0.57735,0.57735;2.0944rad)
  Profile = -> Pad203 [Edge20]
  Type = 0
FEATURE [PartDesign::Body] Body262
  Group = -> [Sketch358,Pad203,Pad204]
  Origin = -> Origin385
  Tip = -> Pad204
FEATURE [App::Part] Part122  label="tornillo M5-15-035"
  Group = -> [Body262]
  Origin = -> Origin383
  Placement = pos=(357,108,88) rot=(0,1,0;1.5708rad)
FEATURE [PartDesign::Pad] Pad205
  BaseFeature = -> Pad202
  Direction = (1,-2e-16,6e-16)
  Length = 15
  Length2 = 10
  Placement = pos=(0,0,0) rot=(0.57735,0.57735,0.57735;2.0944rad)
  Profile = -> Pad202 [Edge20]
  Type = 0
FEATURE [PartDesign::Body] Body261
  Group = -> [Sketch357,Pad202,Pad205]
  Origin = -> Origin384
  Tip = -> Pad205
FEATURE [App::Part] Part123  label="tornillo M5-15-036"
  Group = -> [Body261]
  Origin = -> Origin386
  Placement = pos=(379,108,88) rot=(0,1,0;1.5708rad)
FEATURE [App::LinkGroup] LinkGroup026
  ElementList = -> [Part122,Part123]
  LinkMode = 0
  Placement = pos=(0,25,0) rot=(0,0,1;0rad)
FEATURE [App::LinkGroup] LinkGroup027
  ElementList = -> [Part120,Part121,LinkGroup026]
  LinkMode = 0
FEATURE [Sketcher::SketchObject] Sketch359
  FullyConstrained = false
  MapMode = 5
  Placement = pos=(0,0,0) rot=(0.57735,0.57735,0.57735;2.0944rad)
  Support = -> [YZ_Plane383]
  sketch-geometry (8):
    g0: LineSegment StartX=2.8963 StartY=-2.75889 StartZ=0 EndX=3.83742 EndY=1.12882 EndZ=0
    g1: LineSegment StartX=3.83742 StartY=1.12882 StartZ=0 EndX=0.941117 EndY=3.88771 EndZ=0
    g2: LineSegment StartX=0.941117 StartY=3.88771 StartZ=0 EndX=-2.8963 EndY=2.75889 EndZ=0
    g3: LineSegment StartX=-2.8963 StartY=2.75889 StartZ=0 EndX=-3.83742 EndY=-1.12882 EndZ=0
    g4: LineSegment StartX=-3.83742 StartY=-1.12882 StartZ=0 EndX=-0.941117 EndY=-3.88771 EndZ=0
    g5: LineSegment StartX=-0.941117 StartY=-3.88771 StartZ=0 EndX=2.8963 EndY=-2.75889 EndZ=0
    g6: Circle CenterX=0 CenterY=0 CenterZ=0 NormalX=0 NormalY=0 NormalZ=1 AngleXU=0 Radius=4
    g7: Circle CenterX=0 CenterY=0 CenterZ=0 NormalX=0 NormalY=0 NormalZ=1 AngleXU=0 Radius=2.5
  constraints (17):
    c: Coincident(g0,g1)
    c: Coincident(g1,g2)
    c: Coincident(g2,g3)
    c: Coincident(g3,g4)
    c: Coincident(g4,g5)
    c: Coincident(g5,g0)
    c: Equal(g0, g1-g5) x5
    c: PointOnObject(g0,g6)
    c: PointOnObject(g1,g6)
    c: PointOnObject(g2,g6)
    c: PointOnObject(g3,g6)
    c: PointOnObject(g4,g6)
    c: PointOnObject(g5,g6)
    c: Coincident(g6,g-1)
    c: Coincident(g7,g6)
    c: Radius(g7) = 2.5
    c: Radius(g6) = 4
FEATURE [PartDesign::Pad] Pad208
  Direction = (1,-2e-16,3e-16)
  Length = 3
  Length2 = 10
  Placement = pos=(0,0,0) rot=(0.57735,0.57735,0.57735;2.0944rad)
  Profile = -> Sketch359
  Type = 0
FEATURE [Sketcher::SketchObject] Sketch360
  FullyConstrained = false
  MapMode = 5
  Placement = pos=(0,0,0) rot=(0.57735,0.57735,0.57735;2.0944rad)
  Support = -> [YZ_Plane386]
  sketch-geometry (8):
    g0: LineSegment StartX=2.8963 StartY=-2.75889 StartZ=0 EndX=3.83742 EndY=1.12882 EndZ=0
    g1: LineSegment StartX=3.83742 StartY=1.12882 StartZ=0 EndX=0.941117 EndY=3.88771 EndZ=0
    g2: LineSegment StartX=0.941117 StartY=3.88771 StartZ=0 EndX=-2.8963 EndY=2.75889 EndZ=0
    g3: LineSegment StartX=-2.8963 StartY=2.75889 StartZ=0 EndX=-3.83742 EndY=-1.12882 EndZ=0
    g4: LineSegment StartX=-3.83742 StartY=-1.12882 StartZ=0 EndX=-0.941117 EndY=-3.88771 EndZ=0
    g5: LineSegment StartX=-0.941117 StartY=-3.88771 StartZ=0 EndX=2.8963 EndY=-2.75889 EndZ=0
    g6: Circle CenterX=0 CenterY=0 CenterZ=0 NormalX=0 NormalY=0 NormalZ=1 AngleXU=0 Radius=4
    g7: Circle CenterX=0 CenterY=0 CenterZ=0 NormalX=0 NormalY=0 NormalZ=1 AngleXU=0 Radius=2.5
  constraints (17):
    c: Coincident(g0,g1)
    c: Coincident(g1,g2)
    c: Coincident(g2,g3)
    c: Coincident(g3,g4)
    c: Coincident(g4,g5)
    c: Coincident(g5,g0)
    c: Equal(g0, g1-g5) x5
    c: PointOnObject(g0,g6)
    c: PointOnObject(g1,g6)
    c: PointOnObject(g2,g6)
    c: PointOnObject(g3,g6)
    c: PointOnObject(g4,g6)
    c: PointOnObject(g5,g6)
    c: Coincident(g6,g-1)
    c: Coincident(g7,g6)
    c: Radius(g7) = 2.5
    c: Radius(g6) = 4
FEATURE [PartDesign::Pad] Pad206
  Direction = (1,-2e-16,3e-16)
  Length = 3
  Length2 = 10
  Placement = pos=(0,0,0) rot=(0.57735,0.57735,0.57735;2.0944rad)
  Profile = -> Sketch360
  Type = 0
FEATURE [Sketcher::SketchObject] Sketch361
  FullyConstrained = false
  MapMode = 5
  Placement = pos=(0,0,0) rot=(0.57735,0.57735,0.57735;2.0944rad)
  Support = -> [YZ_Plane388]
  sketch-geometry (8):
    g0: LineSegment StartX=2.8963 StartY=-2.75889 StartZ=0 EndX=3.83742 EndY=1.12882 EndZ=0
    g1: LineSegment StartX=3.83742 StartY=1.12882 StartZ=0 EndX=0.941117 EndY=3.88771 EndZ=0
    g2: LineSegment StartX=0.941117 StartY=3.88771 StartZ=0 EndX=-2.8963 EndY=2.75889 EndZ=0
    g3: LineSegment StartX=-2.8963 StartY=2.75889 StartZ=0 EndX=-3.83742 EndY=-1.12882 EndZ=0
    g4: LineSegment StartX=-3.83742 StartY=-1.12882 StartZ=0 EndX=-0.941117 EndY=-3.88771 EndZ=0
    g5: LineSegment StartX=-0.941117 StartY=-3.88771 StartZ=0 EndX=2.8963 EndY=-2.75889 EndZ=0
    g6: Circle CenterX=0 CenterY=0 CenterZ=0 NormalX=0 NormalY=0 NormalZ=1 AngleXU=0 Radius=4
    g7: Circle CenterX=0 CenterY=0 CenterZ=0 NormalX=0 NormalY=0 NormalZ=1 AngleXU=0 Radius=2.5
  constraints (17):
    c: Coincident(g0,g1)
    c: Coincident(g1,g2)
    c: Coincident(g2,g3)
    c: Coincident(g3,g4)
    c: Coincident(g4,g5)
    c: Coincident(g5,g0)
    c: Equal(g0, g1-g5) x5
    c: PointOnObject(g0,g6)
    c: PointOnObject(g1,g6)
    c: PointOnObject(g2,g6)
    c: PointOnObject(g3,g6)
    c: PointOnObject(g4,g6)
    c: PointOnObject(g5,g6)
    c: Coincident(g6,g-1)
    c: Coincident(g7,g6)
    c: Radius(g7) = 2.5
    c: Radius(g6) = 4
FEATURE [PartDesign::Pad] Pad210
  Direction = (1,-2e-16,3e-16)
  Length = 3
  Length2 = 10
  Placement = pos=(0,0,0) rot=(0.57735,0.57735,0.57735;2.0944rad)
  Profile = -> Sketch361
  Type = 0
FEATURE [PartDesign::Pad] Pad207
  BaseFeature = -> Pad210
  Direction = (1,-2e-16,6e-16)
  Length = 15
  Length2 = 10
  Placement = pos=(0,0,0) rot=(0.57735,0.57735,0.57735;2.0944rad)
  Profile = -> Pad210 [Edge20]
  Type = 0
FEATURE [Sketcher::SketchObject] Sketch362
  FullyConstrained = false
  MapMode = 5
  Placement = pos=(0,0,0) rot=(0.57735,0.57735,0.57735;2.0944rad)
  Support = -> [YZ_Plane382]
  sketch-geometry (8):
    g0: LineSegment StartX=2.8963 StartY=-2.75889 StartZ=0 EndX=3.83742 EndY=1.12882 EndZ=0
    g1: LineSegment StartX=3.83742 StartY=1.12882 StartZ=0 EndX=0.941117 EndY=3.88771 EndZ=0
    g2: LineSegment StartX=0.941117 StartY=3.88771 StartZ=0 EndX=-2.8963 EndY=2.75889 EndZ=0
    g3: LineSegment StartX=-2.8963 StartY=2.75889 StartZ=0 EndX=-3.83742 EndY=-1.12882 EndZ=0
    g4: LineSegment StartX=-3.83742 StartY=-1.12882 StartZ=0 EndX=-0.941117 EndY=-3.88771 EndZ=0
    g5: LineSegment StartX=-0.941117 StartY=-3.88771 StartZ=0 EndX=2.8963 EndY=-2.75889 EndZ=0
    g6: Circle CenterX=0 CenterY=0 CenterZ=0 NormalX=0 NormalY=0 NormalZ=1 AngleXU=0 Radius=4
    g7: Circle CenterX=0 CenterY=0 CenterZ=0 NormalX=0 NormalY=0 NormalZ=1 AngleXU=0 Radius=2.5
  constraints (17):
    c: Coincident(g0,g1)
    c: Coincident(g1,g2)
    c: Coincident(g2,g3)
    c: Coincident(g3,g4)
    c: Coincident(g4,g5)
    c: Coincident(g5,g0)
    c: Equal(g0, g1-g5) x5
    c: PointOnObject(g0,g6)
    c: PointOnObject(g1,g6)
    c: PointOnObject(g2,g6)
    c: PointOnObject(g3,g6)
    c: PointOnObject(g4,g6)
    c: PointOnObject(g5,g6)
    c: Coincident(g6,g-1)
    c: Coincident(g7,g6)
    c: Radius(g7) = 2.5
    c: Radius(g6) = 4
FEATURE [PartDesign::Pad] Pad209
  Direction = (1,-2e-16,3e-16)
  Length = 3
  Length2 = 10
  Placement = pos=(0,0,0) rot=(0.57735,0.57735,0.57735;2.0944rad)
  Profile = -> Sketch362
  Type = 0
FEATURE [PartDesign::Body] Body263
  Group = -> [Sketch361,Pad210,Pad207]
  Origin = -> Origin391
  Tip = -> Pad207
FEATURE [PartDesign::Pad] Pad211
  BaseFeature = -> Pad209
  Direction = (1,-2e-16,6e-16)
  Length = 15
  Length2 = 10
  Placement = pos=(0,0,0) rot=(0.57735,0.57735,0.57735;2.0944rad)
  Profile = -> Pad209 [Edge20]
  Type = 0
FEATURE [PartDesign::Body] Body265
  Group = -> [Sketch362,Pad209,Pad211]
  Origin = -> Origin393
  Tip = -> Pad211
FEATURE [App::Part] Part124  label="tornillo M5-15-037"
  Group = -> [Body265]
  Origin = -> Origin387
  Placement = pos=(357,108,88) rot=(0,1,0;1.5708rad)
FEATURE [PartDesign::Pad] Pad212
  BaseFeature = -> Pad208
  Direction = (1,-2e-16,6e-16)
  Length = 15
  Length2 = 10
  Placement = pos=(0,0,0) rot=(0.57735,0.57735,0.57735;2.0944rad)
  Profile = -> Pad208 [Edge20]
  Type = 0
FEATURE [PartDesign::Body] Body266
  Group = -> [Sketch359,Pad208,Pad212]
  Origin = -> Origin390
  Tip = -> Pad212
FEATURE [App::Part] Part125  label="tornillo M5-15-038"
  Group = -> [Body266]
  Origin = -> Origin392
  Placement = pos=(379,108,88) rot=(0,1,0;1.5708rad)
FEATURE [App::Part] Part127  label="tornillo M5-15-040"
  Group = -> [Body263]
  Origin = -> Origin389
  Placement = pos=(357,108,88) rot=(0,1,0;1.5708rad)
FEATURE [App::LinkGroup] LinkGroup028
  ElementList = -> [Part127,Part125]
  LinkMode = 0
  Placement = pos=(0,25,0) rot=(0,0,1;0rad)
FEATURE [PartDesign::Pad] Pad213
  BaseFeature = -> Pad206
  Direction = (1,-2e-16,6e-16)
  Length = 15
  Length2 = 10
  Placement = pos=(0,0,0) rot=(0.57735,0.57735,0.57735;2.0944rad)
  Profile = -> Pad206 [Edge20]
  Type = 0
FEATURE [PartDesign::Body] Body264
  Group = -> [Sketch360,Pad206,Pad213]
  Origin = -> Origin388
  Tip = -> Pad213
FEATURE [App::Part] Part126  label="tornillo M5-15-039"
  Group = -> [Body264]
  Origin = -> Origin394
  Placement = pos=(379,108,88) rot=(0,1,0;1.5708rad)
FEATURE [App::LinkGroup] LinkGroup029
  ElementList = -> [Part124,Part126,LinkGroup028]
  LinkMode = 0
  Placement = pos=(-3.05176e-05,126,-7.62939e-06) rot=(0,0,1;0rad)
FEATURE [Sketcher::SketchObject] Sketch363
  FullyConstrained = false
  MapMode = 5
  Placement = pos=(0,0,0) rot=(0.57735,0.57735,0.57735;2.0944rad)
  Support = -> [YZ_Plane389]
  sketch-geometry (8):
    g0: LineSegment StartX=2.8963 StartY=-2.75889 StartZ=0 EndX=3.83742 EndY=1.12882 EndZ=0
    g1: LineSegment StartX=3.83742 StartY=1.12882 StartZ=0 EndX=0.941117 EndY=3.88771 EndZ=0
    g2: LineSegment StartX=0.941117 StartY=3.88771 StartZ=0 EndX=-2.8963 EndY=2.75889 EndZ=0
    g3: LineSegment StartX=-2.8963 StartY=2.75889 StartZ=0 EndX=-3.83742 EndY=-1.12882 EndZ=0
    g4: LineSegment StartX=-3.83742 StartY=-1.12882 StartZ=0 EndX=-0.941117 EndY=-3.88771 EndZ=0
    g5: LineSegment StartX=-0.941117 StartY=-3.88771 StartZ=0 EndX=2.8963 EndY=-2.75889 EndZ=0
    g6: Circle CenterX=0 CenterY=0 CenterZ=0 NormalX=0 NormalY=0 NormalZ=1 AngleXU=0 Radius=4
    g7: Circle CenterX=0 CenterY=0 CenterZ=0 NormalX=0 NormalY=0 NormalZ=1 AngleXU=0 Radius=2.5
  constraints (17):
    c: Coincident(g0,g1)
    c: Coincident(g1,g2)
    c: Coincident(g2,g3)
    c: Coincident(g3,g4)
    c: Coincident(g4,g5)
    c: Coincident(g5,g0)
    c: Equal(g0, g1-g5) x5
    c: PointOnObject(g0,g6)
    c: PointOnObject(g1,g6)
    c: PointOnObject(g2,g6)
    c: PointOnObject(g3,g6)
    c: PointOnObject(g4,g6)
    c: PointOnObject(g5,g6)
    c: Coincident(g6,g-1)
    c: Coincident(g7,g6)
    c: Radius(g7) = 2.5
    c: Radius(g6) = 4
FEATURE [PartDesign::Pad] Pad214
  Direction = (1,-2e-16,3e-16)
  Length = 3
  Length2 = 10
  Placement = pos=(0,0,0) rot=(0.57735,0.57735,0.57735;2.0944rad)
  Profile = -> Sketch363
  Type = 0
FEATURE [PartDesign::Pad] Pad215
  BaseFeature = -> Pad214
  Direction = (1,-2e-16,6e-16)
  Length = 15
  Length2 = 10
  Placement = pos=(0,0,0) rot=(0.57735,0.57735,0.57735;2.0944rad)
  Profile = -> Pad214 [Edge20]
  Type = 0
FEATURE [PartDesign::Body] Body267
  Group = -> [Sketch363,Pad214,Pad215]
  Origin = -> Origin395
  Tip = -> Pad215
FEATURE [App::Part] Part128  label="tornillo M5-15-041"
  Group = -> [Body267]
  Origin = -> Origin396
  Placement = pos=(345,10,70) rot=(0,1,0;3.14159rad)
FEATURE [Sketcher::SketchObject] Sketch364
  FullyConstrained = false
  MapMode = 5
  Placement = pos=(0,0,0) rot=(0.57735,0.57735,0.57735;2.0944rad)
  Support = -> [YZ_Plane391]
  sketch-geometry (8):
    g0: LineSegment StartX=2.8963 StartY=-2.75889 StartZ=0 EndX=3.83742 EndY=1.12882 EndZ=0
    g1: LineSegment StartX=3.83742 StartY=1.12882 StartZ=0 EndX=0.941117 EndY=3.88771 EndZ=0
    g2: LineSegment StartX=0.941117 StartY=3.88771 StartZ=0 EndX=-2.8963 EndY=2.75889 EndZ=0
    g3: LineSegment StartX=-2.8963 StartY=2.75889 StartZ=0 EndX=-3.83742 EndY=-1.12882 EndZ=0
    g4: LineSegment StartX=-3.83742 StartY=-1.12882 StartZ=0 EndX=-0.941117 EndY=-3.88771 EndZ=0
    g5: LineSegment StartX=-0.941117 StartY=-3.88771 StartZ=0 EndX=2.8963 EndY=-2.75889 EndZ=0
    g6: Circle CenterX=0 CenterY=0 CenterZ=0 NormalX=0 NormalY=0 NormalZ=1 AngleXU=0 Radius=4
    g7: Circle CenterX=0 CenterY=0 CenterZ=0 NormalX=0 NormalY=0 NormalZ=1 AngleXU=0 Radius=2.5
  constraints (17):
    c: Coincident(g0,g1)
    c: Coincident(g1,g2)
    c: Coincident(g2,g3)
    c: Coincident(g3,g4)
    c: Coincident(g4,g5)
    c: Coincident(g5,g0)
    c: Equal(g0, g1-g5) x5
    c: PointOnObject(g0,g6)
    c: PointOnObject(g1,g6)
    c: PointOnObject(g2,g6)
    c: PointOnObject(g3,g6)
    c: PointOnObject(g4,g6)
    c: PointOnObject(g5,g6)
    c: Coincident(g6,g-1)
    c: Coincident(g7,g6)
    c: Radius(g7) = 2.5
    c: Radius(g6) = 4
FEATURE [PartDesign::Pad] Pad217
  Direction = (1,-2e-16,3e-16)
  Length = 3
  Length2 = 10
  Placement = pos=(0,0,0) rot=(0.57735,0.57735,0.57735;2.0944rad)
  Profile = -> Sketch364
  Type = 0
FEATURE [PartDesign::Pad] Pad216
  BaseFeature = -> Pad217
  Direction = (1,-2e-16,6e-16)
  Length = 15
  Length2 = 10
  Placement = pos=(0,0,0) rot=(0.57735,0.57735,0.57735;2.0944rad)
  Profile = -> Pad217 [Edge20]
  Type = 0
FEATURE [PartDesign::Body] Body268
  Group = -> [Sketch364,Pad217,Pad216]
  Origin = -> Origin398
  Tip = -> Pad216
FEATURE [App::Part] Part129  label="tornillo M5-15-042"
  Group = -> [Body268]
  Origin = -> Origin397
  Placement = pos=(345,330,70) rot=(0,1,0;3.14159rad)
FEATURE [Sketcher::SketchObject] Sketch365
  FullyConstrained = false
  MapMode = 5
  Placement = pos=(0,0,0) rot=(0.57735,0.57735,0.57735;2.0944rad)
  Support = -> [YZ_Plane393]
  sketch-geometry (4):
    g0: ArcOfCircle CenterX=0 CenterY=0 CenterZ=0 NormalX=0 NormalY=0 NormalZ=1 AngleXU=0 Radius=59.8228 StartAngle=1.62097 EndAngle=7.80381
    g1: LineSegment StartX=3 StartY=59.7476 StartZ=0 EndX=3 EndY=55.9928 EndZ=0
    g2: LineSegment StartX=3 StartY=55.9928 StartZ=0 EndX=-3 EndY=55.9928 EndZ=0
    g3: LineSegment StartX=-3 StartY=55.9928 StartZ=0 EndX=-3 EndY=59.7476 EndZ=0
  constraints (10):
    c: Coincident(g0,g-1)
    c: Coincident(g1,g2)
    c: Coincident(g2,g3)
    c: Horizontal(g2)
    c: Vertical(g1)
    c: Vertical(g3)
    c: DistanceX(g0,g1) = 3
    c: DistanceX(g2,g0) = 3
    c: Coincident(g1,g0)
    c: Coincident(g3,g0)
FEATURE [PartDesign::Pad] Pad218
  Direction = (1,1,1)
  Length = 8
  Length2 = 100
  Placement = pos=(0,0,0) rot=(0.57735,0.57735,0.57735;2.0944rad)
  Profile = -> Sketch365
  Type = 0
FEATURE [PartDesign::Body] Body269  label="ruedaCuatro"
  Group = -> [Sketch365,Pad218]
  Origin = -> Origin399
  Tip = -> Pad218
FEATURE [Sketcher::SketchObject] Sketch366
  FullyConstrained = false
  MapMode = 5
  Placement = pos=(0,0,0) rot=(0.57735,0.57735,0.57735;2.0944rad)
  Support = -> [YZ_Plane394]
  sketch-geometry (2):
    g0: ArcOfCircle CenterX=0 CenterY=0 CenterZ=0 NormalX=0 NormalY=0 NormalZ=1 AngleXU=0 Radius=59.853 StartAngle=2.93973 EndAngle=6.48504
    g1: LineSegment StartX=-58.6378 StartY=12 StartZ=0 EndX=58.6378 EndY=12 EndZ=0
  constraints (3):
    c: Coincident(g0,g-1)
    c: Coincident(g1,g0)
    c: Coincident(g1,g0)
FEATURE [PartDesign::Pad] Pad219
  Direction = (1,1,1)
  Length = 8
  Length2 = 100
  Placement = pos=(0,0,0) rot=(0.57735,0.57735,0.57735;2.0944rad)
  Profile = -> Sketch366
  Type = 0
FEATURE [PartDesign::Body] Body270  label="ruedaCinco"
  Group = -> [Sketch366,Pad219]
  Origin = -> Origin400
  Tip = -> Pad219
